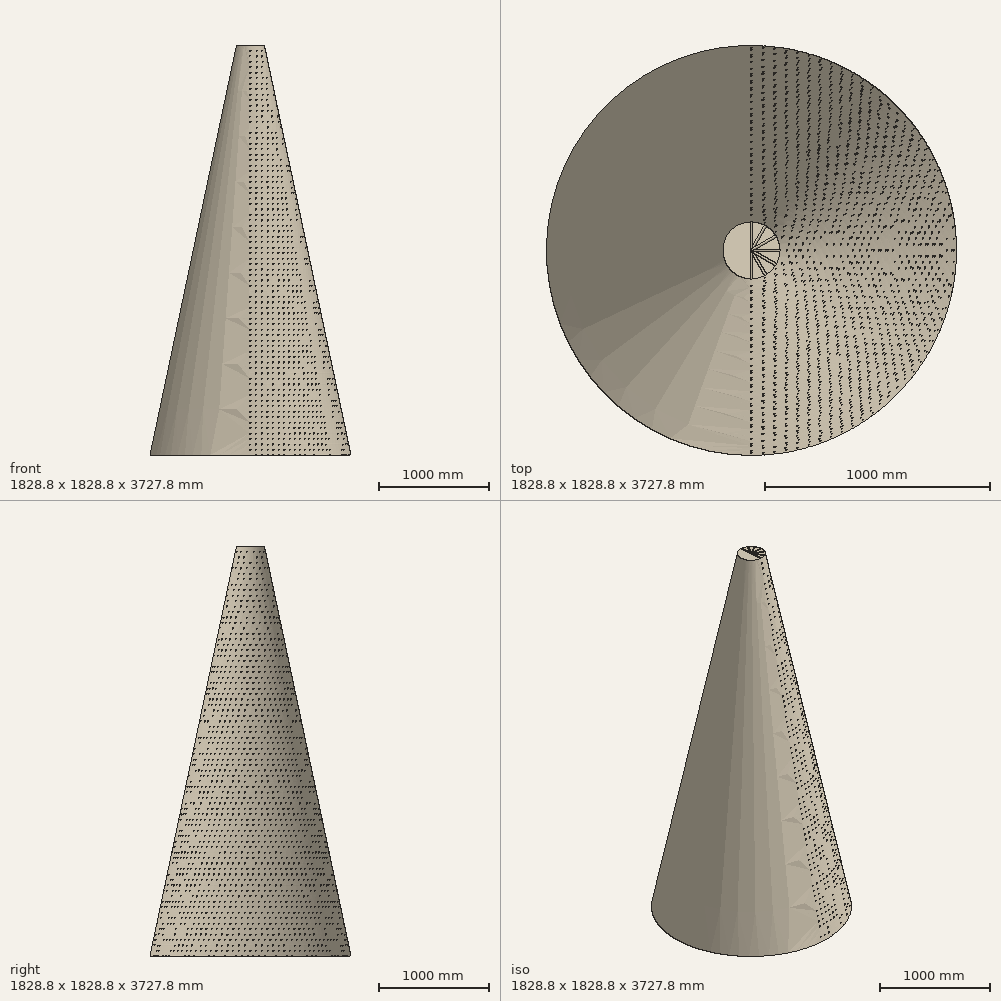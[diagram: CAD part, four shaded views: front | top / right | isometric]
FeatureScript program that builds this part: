
annotation { "Feature Type Name" : "Feature", "Feature Type Description" : "" }
export const myFeature = defineFeature(function(context is Context, id is Id, definition is map)
    precondition{}
    {
        {
            var Q0;
            Q0=qCreatedBy(makeId("Front.planeOp"),FACE);
            var sketch = newSketch(context, id + "F0", { "sketchPlane" : qUnion([Q0])});
            skLineSegment(sketch, "E0", {"start": v(0, 0) * mm, "end": v(914.4, 0) * mm});
            skLineSegment(sketch, "E1", {"start": v(914.4, 0) * mm, "end": v(127, 3727.75) * mm});
            skLineSegment(sketch, "E2", {"start": v(127, 3727.75) * mm, "end": v(0, 3727.75) * mm});
            skLineSegment(sketch, "E3", {"start": v(0, 3727.75) * mm, "end": v(0, 0) * mm});
            skLineSegment(sketch, "E4", {"start": v(0, 3727.75) * mm, "end": v(0, 4329) * mm});
            skLineSegment(sketch, "E5", {"start": v(0, 4329) * mm, "end": v(127, 3727.75) * mm});
            skCircle(sketch, "E6", {"center": v(0, 0) * mm, "radius": 6 * mm});
            skLineSegment(sketch, "E7.direction1", {"start": v(0, 0) * mm, "end": v(25.4, 0) * mm, "construction": true});
            skSolve(sketch);
        }
        {
            var Q0;
            Q0=qCreatedBy(makeId("Front.planeOp"),FACE);
            var sketch = newSketch(context, id + "F1", { "sketchPlane" : qUnion([Q0])});
            skCircle(sketch, "E8", {"center": v(0, 0) * mm, "radius": 6 * mm});
            skCircle(sketch, "E9.0.1.0", {"center": v(0, 49.7) * mm, "radius": 6 * mm});
            skCircle(sketch, "E9.0.2.0", {"center": v(0, 99.4) * mm, "radius": 6 * mm});
            skCircle(sketch, "E9.0.3.0", {"center": v(0, 149.1) * mm, "radius": 6 * mm});
            skCircle(sketch, "E9.0.4.0", {"center": v(0, 198.81) * mm, "radius": 6 * mm});
            skCircle(sketch, "E9.0.5.0", {"center": v(0, 248.52) * mm, "radius": 6 * mm});
            skCircle(sketch, "E9.0.6.0", {"center": v(0, 298.22) * mm, "radius": 6 * mm});
            skCircle(sketch, "E9.0.7.0", {"center": v(0, 347.92) * mm, "radius": 6 * mm});
            skCircle(sketch, "E9.0.8.0", {"center": v(0, 397.63) * mm, "radius": 6 * mm});
            skCircle(sketch, "E9.0.9.0", {"center": v(0, 447.33) * mm, "radius": 6 * mm});
            skCircle(sketch, "E9.0.10.0", {"center": v(0, 497.03) * mm, "radius": 6 * mm});
            skCircle(sketch, "E9.0.11.0", {"center": v(0, 546.74) * mm, "radius": 6 * mm});
            skCircle(sketch, "E9.0.12.0", {"center": v(0, 596.44) * mm, "radius": 6 * mm});
            skCircle(sketch, "E9.0.13.0", {"center": v(0, 646.14) * mm, "radius": 6 * mm});
            skCircle(sketch, "E9.0.14.0", {"center": v(0, 695.85) * mm, "radius": 6 * mm});
            skCircle(sketch, "E9.0.15.0", {"center": v(0, 745.55) * mm, "radius": 6 * mm});
            skCircle(sketch, "E9.0.16.0", {"center": v(0, 795.25) * mm, "radius": 6 * mm});
            skCircle(sketch, "E9.0.17.0", {"center": v(0, 844.96) * mm, "radius": 6 * mm});
            skCircle(sketch, "E9.0.18.0", {"center": v(0, 894.66) * mm, "radius": 6 * mm});
            skCircle(sketch, "E9.0.19.0", {"center": v(0, 944.36) * mm, "radius": 6 * mm});
            skCircle(sketch, "E9.0.20.0", {"center": v(0, 994.07) * mm, "radius": 6 * mm});
            skCircle(sketch, "E9.0.21.0", {"center": v(0, 1043.77) * mm, "radius": 6 * mm});
            skCircle(sketch, "E9.0.22.0", {"center": v(0, 1093.47) * mm, "radius": 6 * mm});
            skCircle(sketch, "E9.0.23.0", {"center": v(0, 1143.18) * mm, "radius": 6 * mm});
            skCircle(sketch, "E9.0.24.0", {"center": v(0, 1192.88) * mm, "radius": 6 * mm});
            skCircle(sketch, "E9.0.25.0", {"center": v(0, 1242.58) * mm, "radius": 6 * mm});
            skCircle(sketch, "E9.0.26.0", {"center": v(0, 1292.29) * mm, "radius": 6 * mm});
            skCircle(sketch, "E9.0.27.0", {"center": v(0, 1341.99) * mm, "radius": 6 * mm});
            skCircle(sketch, "E9.0.28.0", {"center": v(0, 1391.7) * mm, "radius": 6 * mm});
            skCircle(sketch, "E9.0.29.0", {"center": v(0, 1441.4) * mm, "radius": 6 * mm});
            skCircle(sketch, "E9.0.30.0", {"center": v(0, 1491.1) * mm, "radius": 6 * mm});
            skCircle(sketch, "E9.0.31.0", {"center": v(0, 1540.8) * mm, "radius": 6 * mm});
            skCircle(sketch, "E9.0.32.0", {"center": v(0, 1590.5) * mm, "radius": 6 * mm});
            skCircle(sketch, "E9.0.33.0", {"center": v(0, 1640.2) * mm, "radius": 6 * mm});
            skCircle(sketch, "E9.0.34.0", {"center": v(0, 1689.91) * mm, "radius": 6 * mm});
            skCircle(sketch, "E9.0.35.0", {"center": v(0, 1739.62) * mm, "radius": 6 * mm});
            skCircle(sketch, "E9.0.36.0", {"center": v(0, 1789.32) * mm, "radius": 6 * mm});
            skCircle(sketch, "E9.0.37.0", {"center": v(0, 1839.02) * mm, "radius": 6 * mm});
            skCircle(sketch, "E9.0.38.0", {"center": v(0, 1888.73) * mm, "radius": 6 * mm});
            skCircle(sketch, "E9.0.39.0", {"center": v(0, 1938.43) * mm, "radius": 6 * mm});
            skCircle(sketch, "E9.0.40.0", {"center": v(0, 1988.13) * mm, "radius": 6 * mm});
            skCircle(sketch, "E9.0.41.0", {"center": v(0, 2037.84) * mm, "radius": 6 * mm});
            skCircle(sketch, "E9.0.42.0", {"center": v(0, 2087.54) * mm, "radius": 6 * mm});
            skCircle(sketch, "E9.0.43.0", {"center": v(0, 2137.24) * mm, "radius": 6 * mm});
            skCircle(sketch, "E9.0.44.0", {"center": v(0, 2186.95) * mm, "radius": 6 * mm});
            skCircle(sketch, "E9.0.45.0", {"center": v(0, 2236.65) * mm, "radius": 6 * mm});
            skCircle(sketch, "E9.0.46.0", {"center": v(0, 2286.35) * mm, "radius": 6 * mm});
            skCircle(sketch, "E9.0.47.0", {"center": v(0, 2336.06) * mm, "radius": 6 * mm});
            skCircle(sketch, "E9.0.48.0", {"center": v(0, 2385.76) * mm, "radius": 6 * mm});
            skCircle(sketch, "E9.0.49.0", {"center": v(0, 2435.46) * mm, "radius": 6 * mm});
            skCircle(sketch, "E9.0.50.0", {"center": v(0, 2485.17) * mm, "radius": 6 * mm});
            skCircle(sketch, "E9.0.51.0", {"center": v(0, 2534.87) * mm, "radius": 6 * mm});
            skCircle(sketch, "E9.0.52.0", {"center": v(0, 2584.57) * mm, "radius": 6 * mm});
            skCircle(sketch, "E9.0.53.0", {"center": v(0, 2634.28) * mm, "radius": 6 * mm});
            skCircle(sketch, "E9.0.54.0", {"center": v(0, 2683.98) * mm, "radius": 6 * mm});
            skCircle(sketch, "E9.0.55.0", {"center": v(0, 2733.68) * mm, "radius": 6 * mm});
            skCircle(sketch, "E9.0.56.0", {"center": v(0, 2783.39) * mm, "radius": 6 * mm});
            skCircle(sketch, "E9.0.57.0", {"center": v(0, 2833.09) * mm, "radius": 6 * mm});
            skCircle(sketch, "E9.0.58.0", {"center": v(0, 2882.8) * mm, "radius": 6 * mm});
            skCircle(sketch, "E9.0.59.0", {"center": v(0, 2932.5) * mm, "radius": 6 * mm});
            skCircle(sketch, "E9.0.60.0", {"center": v(0, 2982.2) * mm, "radius": 6 * mm});
            skCircle(sketch, "E9.0.61.0", {"center": v(0, 3031.9) * mm, "radius": 6 * mm});
            skCircle(sketch, "E9.0.62.0", {"center": v(0, 3081.6) * mm, "radius": 6 * mm});
            skCircle(sketch, "E9.0.63.0", {"center": v(0, 3131.3) * mm, "radius": 6 * mm});
            skCircle(sketch, "E9.0.64.0", {"center": v(0, 3181.01) * mm, "radius": 6 * mm});
            skCircle(sketch, "E9.0.65.0", {"center": v(0, 3230.71) * mm, "radius": 6 * mm});
            skCircle(sketch, "E9.0.66.0", {"center": v(0, 3280.42) * mm, "radius": 6 * mm});
            skCircle(sketch, "E9.0.67.0", {"center": v(0, 3330.12) * mm, "radius": 6 * mm});
            skCircle(sketch, "E9.0.68.0", {"center": v(0, 3379.82) * mm, "radius": 6 * mm});
            skCircle(sketch, "E9.0.69.0", {"center": v(0, 3429.53) * mm, "radius": 6 * mm});
            skCircle(sketch, "E9.0.70.0", {"center": v(0, 3479.23) * mm, "radius": 6 * mm});
            skCircle(sketch, "E9.0.71.0", {"center": v(0, 3528.93) * mm, "radius": 6 * mm});
            skCircle(sketch, "E9.0.72.0", {"center": v(0, 3578.64) * mm, "radius": 6 * mm});
            skCircle(sketch, "E9.0.73.0", {"center": v(0, 3628.34) * mm, "radius": 6 * mm});
            skCircle(sketch, "E9.0.74.0", {"center": v(0, 3678.04) * mm, "radius": 6 * mm});
            skCircle(sketch, "E9.0.75.0", {"center": v(0, 3727.75) * mm, "radius": 6 * mm});
            skLineSegment(sketch, "E9.direction1", {"start": v(0, 0) * mm, "end": v(0, 0) * mm});
            skLineSegment(sketch, "E9.direction2", {"start": v(0, 0) * mm, "end": v(0, 49.7) * mm, "construction": true});
            skSolve(sketch);
        }
        {
            var Q0;
            {var subQ4=sQuery(id+"F0.wireOp",EDGE,"E1");Q0=makeQuery(id+"F0.imprint","IMPRINT",FACE,{"disambiguationData":[TD([[makeQuery(id+"F0.imprint","IMPRINT",EDGE,{"derivedFrom":subQ4}),1.0]])]});}
            var Q1;
            Q1=sQuery(id+"F0.wireOp",EDGE,"E3");
            revolve(context, id + "F2", {"entities" : qUnion([Q0]), "axis" : qUnion([Q1]), "revolveType" : RevolveType.FULL});
        }
        {
            var Q0;
            Q0=makeQuery(id+"F1.imprint","IMPRINT",FACE,{"disambiguationData":[TD([[makeQuery(id+"F1.imprint","IMPRINT",EDGE,{"derivedFrom":sQuery(id+"F1.wireOp",EDGE,"E9.0.6.0")}),1.0]])]});
            var Q1;
            Q1=makeQuery(id+"F1.imprint","IMPRINT",FACE,{"disambiguationData":[TD([[makeQuery(id+"F1.imprint","IMPRINT",EDGE,{"derivedFrom":sQuery(id+"F1.wireOp",EDGE,"E9.0.75.0")}),1.0]])]});
            var Q2;
            Q2=makeQuery(id+"F1.imprint","IMPRINT",FACE,{"disambiguationData":[TD([[makeQuery(id+"F1.imprint","IMPRINT",EDGE,{"derivedFrom":sQuery(id+"F1.wireOp",EDGE,"E9.0.9.0")}),1.0]])]});
            var Q3;
            Q3=makeQuery(id+"F1.imprint","IMPRINT",FACE,{"disambiguationData":[TD([[makeQuery(id+"F1.imprint","IMPRINT",EDGE,{"derivedFrom":sQuery(id+"F1.wireOp",EDGE,"E9.0.4.0")}),1.0]])]});
            var Q4;
            Q4=makeQuery(id+"F1.imprint","IMPRINT",FACE,{"disambiguationData":[TD([[makeQuery(id+"F1.imprint","IMPRINT",EDGE,{"derivedFrom":sQuery(id+"F1.wireOp",EDGE,"E9.0.7.0")}),1.0]])]});
            var Q5;
            Q5=makeQuery(id+"F1.imprint","IMPRINT",FACE,{"disambiguationData":[TD([[makeQuery(id+"F1.imprint","IMPRINT",EDGE,{"derivedFrom":sQuery(id+"F1.wireOp",EDGE,"E9.0.8.0")}),1.0]])]});
            var Q6;
            Q6=makeQuery(id+"F1.imprint","IMPRINT",FACE,{"disambiguationData":[TD([[makeQuery(id+"F1.imprint","IMPRINT",EDGE,{"derivedFrom":sQuery(id+"F1.wireOp",EDGE,"E9.0.5.0")}),1.0]])]});
            var Q7;
            Q7=makeQuery(id+"F1.imprint","IMPRINT",FACE,{"disambiguationData":[TD([[makeQuery(id+"F1.imprint","IMPRINT",EDGE,{"derivedFrom":sQuery(id+"F1.wireOp",EDGE,"E9.0.51.0")}),1.0]])]});
            var Q8;
            Q8=makeQuery(id+"F1.imprint","IMPRINT",FACE,{"disambiguationData":[TD([[makeQuery(id+"F1.imprint","IMPRINT",EDGE,{"derivedFrom":sQuery(id+"F1.wireOp",EDGE,"E9.0.39.0")}),1.0]])]});
            var Q9;
            Q9=makeQuery(id+"F1.imprint","IMPRINT",FACE,{"disambiguationData":[TD([[makeQuery(id+"F1.imprint","IMPRINT",EDGE,{"derivedFrom":sQuery(id+"F1.wireOp",EDGE,"E9.0.35.0")}),1.0]])]});
            var Q10;
            Q10=makeQuery(id+"F1.imprint","IMPRINT",FACE,{"disambiguationData":[TD([[makeQuery(id+"F1.imprint","IMPRINT",EDGE,{"derivedFrom":sQuery(id+"F1.wireOp",EDGE,"E9.0.56.0")}),1.0]])]});
            var Q11;
            Q11=makeQuery(id+"F1.imprint","IMPRINT",FACE,{"disambiguationData":[TD([[makeQuery(id+"F1.imprint","IMPRINT",EDGE,{"derivedFrom":sQuery(id+"F1.wireOp",EDGE,"E9.0.33.0")}),1.0]])]});
            var Q12;
            Q12=makeQuery(id+"F1.imprint","IMPRINT",FACE,{"disambiguationData":[TD([[makeQuery(id+"F1.imprint","IMPRINT",EDGE,{"derivedFrom":sQuery(id+"F1.wireOp",EDGE,"E9.0.49.0")}),1.0]])]});
            var Q13;
            Q13=makeQuery(id+"F1.imprint","IMPRINT",FACE,{"disambiguationData":[TD([[makeQuery(id+"F1.imprint","IMPRINT",EDGE,{"derivedFrom":sQuery(id+"F1.wireOp",EDGE,"E9.0.71.0")}),1.0]])]});
            var Q14;
            Q14=makeQuery(id+"F1.imprint","IMPRINT",FACE,{"disambiguationData":[TD([[makeQuery(id+"F1.imprint","IMPRINT",EDGE,{"derivedFrom":sQuery(id+"F1.wireOp",EDGE,"E9.0.74.0")}),1.0]])]});
            var Q15;
            Q15=makeQuery(id+"F1.imprint","IMPRINT",FACE,{"disambiguationData":[TD([[makeQuery(id+"F1.imprint","IMPRINT",EDGE,{"derivedFrom":sQuery(id+"F1.wireOp",EDGE,"E9.0.41.0")}),1.0]])]});
            var Q16;
            Q16=makeQuery(id+"F1.imprint","IMPRINT",FACE,{"disambiguationData":[TD([[makeQuery(id+"F1.imprint","IMPRINT",EDGE,{"derivedFrom":sQuery(id+"F1.wireOp",EDGE,"E9.0.3.0")}),1.0]])]});
            var Q17;
            Q17=makeQuery(id+"F1.imprint","IMPRINT",FACE,{"disambiguationData":[TD([[makeQuery(id+"F1.imprint","IMPRINT",EDGE,{"derivedFrom":sQuery(id+"F1.wireOp",EDGE,"E9.0.24.0")}),1.0]])]});
            var Q18;
            Q18=makeQuery(id+"F1.imprint","IMPRINT",FACE,{"disambiguationData":[TD([[makeQuery(id+"F1.imprint","IMPRINT",EDGE,{"derivedFrom":sQuery(id+"F1.wireOp",EDGE,"E9.0.55.0")}),1.0]])]});
            var Q19;
            Q19=makeQuery(id+"F1.imprint","IMPRINT",FACE,{"disambiguationData":[TD([[makeQuery(id+"F1.imprint","IMPRINT",EDGE,{"derivedFrom":sQuery(id+"F1.wireOp",EDGE,"E9.0.32.0")}),1.0]])]});
            var Q20;
            Q20=makeQuery(id+"F1.imprint","IMPRINT",FACE,{"disambiguationData":[TD([[makeQuery(id+"F1.imprint","IMPRINT",EDGE,{"derivedFrom":sQuery(id+"F1.wireOp",EDGE,"E9.0.73.0")}),1.0]])]});
            var Q21;
            Q21=makeQuery(id+"F1.imprint","IMPRINT",FACE,{"disambiguationData":[TD([[makeQuery(id+"F1.imprint","IMPRINT",EDGE,{"derivedFrom":sQuery(id+"F1.wireOp",EDGE,"E9.0.11.0")}),1.0]])]});
            var Q22;
            Q22=makeQuery(id+"F1.imprint","IMPRINT",FACE,{"disambiguationData":[TD([[makeQuery(id+"F1.imprint","IMPRINT",EDGE,{"derivedFrom":sQuery(id+"F1.wireOp",EDGE,"E9.0.25.0")}),1.0]])]});
            var Q23;
            Q23=makeQuery(id+"F1.imprint","IMPRINT",FACE,{"disambiguationData":[TD([[makeQuery(id+"F1.imprint","IMPRINT",EDGE,{"derivedFrom":sQuery(id+"F1.wireOp",EDGE,"E9.0.48.0")}),1.0]])]});
            var Q24;
            Q24=makeQuery(id+"F1.imprint","IMPRINT",FACE,{"disambiguationData":[TD([[makeQuery(id+"F1.imprint","IMPRINT",EDGE,{"derivedFrom":sQuery(id+"F1.wireOp",EDGE,"E9.0.50.0")}),1.0]])]});
            var Q25;
            Q25=makeQuery(id+"F1.imprint","IMPRINT",FACE,{"disambiguationData":[TD([[makeQuery(id+"F1.imprint","IMPRINT",EDGE,{"derivedFrom":sQuery(id+"F1.wireOp",EDGE,"E9.0.57.0")}),1.0]])]});
            var Q26;
            Q26=makeQuery(id+"F1.imprint","IMPRINT",FACE,{"disambiguationData":[TD([[makeQuery(id+"F1.imprint","IMPRINT",EDGE,{"derivedFrom":sQuery(id+"F1.wireOp",EDGE,"E9.0.72.0")}),1.0]])]});
            var Q27;
            Q27=makeQuery(id+"F1.imprint","IMPRINT",FACE,{"disambiguationData":[TD([[makeQuery(id+"F1.imprint","IMPRINT",EDGE,{"derivedFrom":sQuery(id+"F1.wireOp",EDGE,"E9.0.23.0")}),1.0]])]});
            var Q28;
            Q28=makeQuery(id+"F1.imprint","IMPRINT",FACE,{"disambiguationData":[TD([[makeQuery(id+"F1.imprint","IMPRINT",EDGE,{"derivedFrom":sQuery(id+"F1.wireOp",EDGE,"E9.0.34.0")}),1.0]])]});
            var Q29;
            Q29=makeQuery(id+"F1.imprint","IMPRINT",FACE,{"disambiguationData":[TD([[makeQuery(id+"F1.imprint","IMPRINT",EDGE,{"derivedFrom":sQuery(id+"F1.wireOp",EDGE,"E9.0.12.0")}),1.0]])]});
            var Q30;
            Q30=makeQuery(id+"F1.imprint","IMPRINT",FACE,{"disambiguationData":[TD([[makeQuery(id+"F1.imprint","IMPRINT",EDGE,{"derivedFrom":sQuery(id+"F1.wireOp",EDGE,"E9.0.10.0")}),1.0]])]});
            var Q31;
            Q31=makeQuery(id+"F1.imprint","IMPRINT",FACE,{"disambiguationData":[TD([[makeQuery(id+"F1.imprint","IMPRINT",EDGE,{"derivedFrom":sQuery(id+"F1.wireOp",EDGE,"E9.0.40.0")}),1.0]])]});
            var Q32;
            Q32=makeQuery(id+"F1.imprint","IMPRINT",FACE,{"disambiguationData":[TD([[makeQuery(id+"F1.imprint","IMPRINT",EDGE,{"derivedFrom":sQuery(id+"F1.wireOp",EDGE,"E9.0.28.0")}),1.0]])]});
            var Q33;
            Q33=makeQuery(id+"F1.imprint","IMPRINT",FACE,{"disambiguationData":[TD([[makeQuery(id+"F1.imprint","IMPRINT",EDGE,{"derivedFrom":sQuery(id+"F1.wireOp",EDGE,"E9.0.21.0")}),1.0]])]});
            var Q34;
            Q34=makeQuery(id+"F1.imprint","IMPRINT",FACE,{"disambiguationData":[TD([[makeQuery(id+"F1.imprint","IMPRINT",EDGE,{"derivedFrom":sQuery(id+"F1.wireOp",EDGE,"E9.0.29.0")}),1.0]])]});
            var Q35;
            Q35=makeQuery(id+"F1.imprint","IMPRINT",FACE,{"disambiguationData":[TD([[makeQuery(id+"F1.imprint","IMPRINT",EDGE,{"derivedFrom":sQuery(id+"F1.wireOp",EDGE,"E9.0.68.0")}),1.0]])]});
            var Q36;
            Q36=makeQuery(id+"F1.imprint","IMPRINT",FACE,{"disambiguationData":[TD([[makeQuery(id+"F1.imprint","IMPRINT",EDGE,{"derivedFrom":sQuery(id+"F1.wireOp",EDGE,"E9.0.63.0")}),1.0]])]});
            var Q37;
            Q37=makeQuery(id+"F1.imprint","IMPRINT",FACE,{"disambiguationData":[TD([[makeQuery(id+"F1.imprint","IMPRINT",EDGE,{"derivedFrom":sQuery(id+"F1.wireOp",EDGE,"E9.0.47.0")}),1.0]])]});
            var Q38;
            Q38=makeQuery(id+"F1.imprint","IMPRINT",FACE,{"disambiguationData":[TD([[makeQuery(id+"F1.imprint","IMPRINT",EDGE,{"derivedFrom":sQuery(id+"F1.wireOp",EDGE,"E9.0.64.0")}),1.0]])]});
            var Q39;
            Q39=makeQuery(id+"F1.imprint","IMPRINT",FACE,{"disambiguationData":[TD([[makeQuery(id+"F1.imprint","IMPRINT",EDGE,{"derivedFrom":sQuery(id+"F1.wireOp",EDGE,"E9.0.36.0")}),1.0]])]});
            var Q40;
            Q40=makeQuery(id+"F1.imprint","IMPRINT",FACE,{"disambiguationData":[TD([[makeQuery(id+"F1.imprint","IMPRINT",EDGE,{"derivedFrom":sQuery(id+"F1.wireOp",EDGE,"E9.0.58.0")}),1.0]])]});
            var Q41;
            Q41=makeQuery(id+"F1.imprint","IMPRINT",FACE,{"disambiguationData":[TD([[makeQuery(id+"F1.imprint","IMPRINT",EDGE,{"derivedFrom":sQuery(id+"F1.wireOp",EDGE,"E9.0.42.0")}),1.0]])]});
            var Q42;
            Q42=makeQuery(id+"F1.imprint","IMPRINT",FACE,{"disambiguationData":[TD([[makeQuery(id+"F1.imprint","IMPRINT",EDGE,{"derivedFrom":sQuery(id+"F1.wireOp",EDGE,"E9.0.15.0")}),1.0]])]});
            var Q43;
            Q43=makeQuery(id+"F1.imprint","IMPRINT",FACE,{"disambiguationData":[TD([[makeQuery(id+"F1.imprint","IMPRINT",EDGE,{"derivedFrom":sQuery(id+"F1.wireOp",EDGE,"E9.0.22.0")}),1.0]])]});
            var Q44;
            Q44=makeQuery(id+"F1.imprint","IMPRINT",FACE,{"disambiguationData":[TD([[makeQuery(id+"F1.imprint","IMPRINT",EDGE,{"derivedFrom":sQuery(id+"F1.wireOp",EDGE,"E9.0.43.0")}),1.0]])]});
            var Q45;
            Q45=makeQuery(id+"F1.imprint","IMPRINT",FACE,{"disambiguationData":[TD([[makeQuery(id+"F1.imprint","IMPRINT",EDGE,{"derivedFrom":sQuery(id+"F1.wireOp",EDGE,"E9.0.30.0")}),1.0]])]});
            var Q46;
            Q46=makeQuery(id+"F1.imprint","IMPRINT",FACE,{"disambiguationData":[TD([[makeQuery(id+"F1.imprint","IMPRINT",EDGE,{"derivedFrom":sQuery(id+"F1.wireOp",EDGE,"E9.0.37.0")}),1.0]])]});
            var Q47;
            Q47=makeQuery(id+"F1.imprint","IMPRINT",FACE,{"disambiguationData":[TD([[makeQuery(id+"F1.imprint","IMPRINT",EDGE,{"derivedFrom":sQuery(id+"F1.wireOp",EDGE,"E9.0.26.0")}),1.0]])]});
            var Q48;
            Q48=makeQuery(id+"F1.imprint","IMPRINT",FACE,{"disambiguationData":[TD([[makeQuery(id+"F1.imprint","IMPRINT",EDGE,{"derivedFrom":sQuery(id+"F1.wireOp",EDGE,"E9.0.66.0")}),1.0]])]});
            var Q49;
            Q49=makeQuery(id+"F1.imprint","IMPRINT",FACE,{"disambiguationData":[TD([[makeQuery(id+"F1.imprint","IMPRINT",EDGE,{"derivedFrom":sQuery(id+"F1.wireOp",EDGE,"E9.0.20.0")}),1.0]])]});
            var Q50;
            Q50=makeQuery(id+"F1.imprint","IMPRINT",FACE,{"disambiguationData":[TD([[makeQuery(id+"F1.imprint","IMPRINT",EDGE,{"derivedFrom":sQuery(id+"F1.wireOp",EDGE,"E9.0.54.0")}),1.0]])]});
            var Q51;
            Q51=makeQuery(id+"F1.imprint","IMPRINT",FACE,{"disambiguationData":[TD([[makeQuery(id+"F1.imprint","IMPRINT",EDGE,{"derivedFrom":sQuery(id+"F1.wireOp",EDGE,"E9.0.67.0")}),1.0]])]});
            var Q52;
            Q52=makeQuery(id+"F1.imprint","IMPRINT",FACE,{"disambiguationData":[TD([[makeQuery(id+"F1.imprint","IMPRINT",EDGE,{"derivedFrom":sQuery(id+"F1.wireOp",EDGE,"E9.0.59.0")}),1.0]])]});
            var Q53;
            Q53=makeQuery(id+"F1.imprint","IMPRINT",FACE,{"disambiguationData":[TD([[makeQuery(id+"F1.imprint","IMPRINT",EDGE,{"derivedFrom":sQuery(id+"F1.wireOp",EDGE,"E9.0.31.0")}),1.0]])]});
            var Q54;
            Q54=makeQuery(id+"F1.imprint","IMPRINT",FACE,{"disambiguationData":[TD([[makeQuery(id+"F1.imprint","IMPRINT",EDGE,{"derivedFrom":sQuery(id+"F1.wireOp",EDGE,"E9.0.52.0")}),1.0]])]});
            var Q55;
            Q55=makeQuery(id+"F1.imprint","IMPRINT",FACE,{"disambiguationData":[TD([[makeQuery(id+"F1.imprint","IMPRINT",EDGE,{"derivedFrom":sQuery(id+"F1.wireOp",EDGE,"E9.0.18.0")}),1.0]])]});
            var Q56;
            Q56=makeQuery(id+"F1.imprint","IMPRINT",FACE,{"disambiguationData":[TD([[makeQuery(id+"F1.imprint","IMPRINT",EDGE,{"derivedFrom":sQuery(id+"F1.wireOp",EDGE,"E9.0.45.0")}),1.0]])]});
            var Q57;
            Q57=makeQuery(id+"F1.imprint","IMPRINT",FACE,{"disambiguationData":[TD([[makeQuery(id+"F1.imprint","IMPRINT",EDGE,{"derivedFrom":sQuery(id+"F1.wireOp",EDGE,"E9.0.27.0")}),1.0]])]});
            var Q58;
            Q58=makeQuery(id+"F1.imprint","IMPRINT",FACE,{"disambiguationData":[TD([[makeQuery(id+"F1.imprint","IMPRINT",EDGE,{"derivedFrom":sQuery(id+"F1.wireOp",EDGE,"E9.0.16.0")}),1.0]])]});
            var Q59;
            Q59=makeQuery(id+"F1.imprint","IMPRINT",FACE,{"disambiguationData":[TD([[makeQuery(id+"F1.imprint","IMPRINT",EDGE,{"derivedFrom":sQuery(id+"F1.wireOp",EDGE,"E9.0.14.0")}),1.0]])]});
            var Q60;
            Q60=makeQuery(id+"F1.imprint","IMPRINT",FACE,{"disambiguationData":[TD([[makeQuery(id+"F1.imprint","IMPRINT",EDGE,{"derivedFrom":sQuery(id+"F1.wireOp",EDGE,"E9.0.53.0")}),1.0]])]});
            var Q61;
            Q61=makeQuery(id+"F1.imprint","IMPRINT",FACE,{"disambiguationData":[TD([[makeQuery(id+"F1.imprint","IMPRINT",EDGE,{"derivedFrom":sQuery(id+"F1.wireOp",EDGE,"E9.0.17.0")}),1.0]])]});
            var Q62;
            Q62=makeQuery(id+"F1.imprint","IMPRINT",FACE,{"disambiguationData":[TD([[makeQuery(id+"F1.imprint","IMPRINT",EDGE,{"derivedFrom":sQuery(id+"F1.wireOp",EDGE,"E9.0.38.0")}),1.0]])]});
            var Q63;
            Q63=makeQuery(id+"F1.imprint","IMPRINT",FACE,{"disambiguationData":[TD([[makeQuery(id+"F1.imprint","IMPRINT",EDGE,{"derivedFrom":sQuery(id+"F1.wireOp",EDGE,"E9.0.19.0")}),1.0]])]});
            var Q64;
            Q64=makeQuery(id+"F1.imprint","IMPRINT",FACE,{"disambiguationData":[TD([[makeQuery(id+"F1.imprint","IMPRINT",EDGE,{"derivedFrom":sQuery(id+"F1.wireOp",EDGE,"E9.0.60.0")}),1.0]])]});
            var Q65;
            Q65=makeQuery(id+"F1.imprint","IMPRINT",FACE,{"disambiguationData":[TD([[makeQuery(id+"F1.imprint","IMPRINT",EDGE,{"derivedFrom":sQuery(id+"F1.wireOp",EDGE,"E9.0.46.0")}),1.0]])]});
            var Q66;
            Q66=makeQuery(id+"F1.imprint","IMPRINT",FACE,{"disambiguationData":[TD([[makeQuery(id+"F1.imprint","IMPRINT",EDGE,{"derivedFrom":sQuery(id+"F1.wireOp",EDGE,"E9.0.44.0")}),1.0]])]});
            var Q67;
            Q67=makeQuery(id+"F1.imprint","IMPRINT",FACE,{"disambiguationData":[TD([[makeQuery(id+"F1.imprint","IMPRINT",EDGE,{"derivedFrom":sQuery(id+"F1.wireOp",EDGE,"E9.0.70.0")}),1.0]])]});
            var Q68;
            Q68=makeQuery(id+"F1.imprint","IMPRINT",FACE,{"disambiguationData":[TD([[makeQuery(id+"F1.imprint","IMPRINT",EDGE,{"derivedFrom":sQuery(id+"F1.wireOp",EDGE,"E9.0.69.0")}),1.0]])]});
            var Q69;
            Q69=makeQuery(id+"F1.imprint","IMPRINT",FACE,{"disambiguationData":[TD([[makeQuery(id+"F1.imprint","IMPRINT",EDGE,{"derivedFrom":sQuery(id+"F1.wireOp",EDGE,"E9.0.65.0")}),1.0]])]});
            var Q70;
            Q70=makeQuery(id+"F1.imprint","IMPRINT",FACE,{"disambiguationData":[TD([[makeQuery(id+"F1.imprint","IMPRINT",EDGE,{"derivedFrom":sQuery(id+"F1.wireOp",EDGE,"E9.0.13.0")}),1.0]])]});
            var Q71;
            Q71=makeQuery(id+"F1.imprint","IMPRINT",FACE,{"disambiguationData":[TD([[makeQuery(id+"F1.imprint","IMPRINT",EDGE,{"derivedFrom":sQuery(id+"F1.wireOp",EDGE,"E9.0.2.0")}),1.0]])]});
            var Q72;
            Q72=makeQuery(id+"F1.imprint","IMPRINT",FACE,{"disambiguationData":[TD([[makeQuery(id+"F1.imprint","IMPRINT",EDGE,{"derivedFrom":sQuery(id+"F1.wireOp",EDGE,"E9.0.62.0")}),1.0]])]});
            var Q73;
            Q73=makeQuery(id+"F1.imprint","IMPRINT",FACE,{"disambiguationData":[TD([[makeQuery(id+"F1.imprint","IMPRINT",EDGE,{"derivedFrom":sQuery(id+"F1.wireOp",EDGE,"E9.0.61.0")}),1.0]])]});
            var Q74;
            Q74=makeQuery(id+"F1.imprint","IMPRINT",FACE,{"disambiguationData":[TD([[makeQuery(id+"F1.imprint","IMPRINT",EDGE,{"derivedFrom":sQuery(id+"F1.wireOp",EDGE,"E8")}),1.0]])]});
            var Q75;
            Q75=makeQuery(id+"F1.imprint","IMPRINT",FACE,{"disambiguationData":[TD([[makeQuery(id+"F1.imprint","IMPRINT",EDGE,{"derivedFrom":sQuery(id+"F1.wireOp",EDGE,"E9.0.1.0")}),1.0]])]});
            extrude(context, id + "F3", {"entities" : qUnion([Q0, Q1, Q2, Q3, Q4, Q5, Q6, Q7, Q8, Q9, Q10, Q11, Q12, Q13, Q14, Q15, Q16, Q17, Q18, Q19, Q20, Q21, Q22, Q23, Q24, Q25, Q26, Q27, Q28, Q29, Q30, Q31, Q32, Q33, Q34, Q35, Q36, Q37, Q38, Q39, Q40, Q41, Q42, Q43, Q44, Q45, Q46, Q47, Q48, Q49, Q50, Q51, Q52, Q53, Q54, Q55, Q56, Q57, Q58, Q59, Q60, Q61, Q62, Q63, Q64, Q65, Q66, Q67, Q68, Q69, Q70, Q71, Q72, Q73, Q74, Q75]), "depth" : 914.4 * mm, "offsetDistance" : 25.4 * mm});
        }
        {
            var Q0;
            Q0=makeQuery(id+"F3.opExtrude","SWEPT_BODY",BODY,{"disambiguationData":[OSD([sQuery(id+"F1.wireOp",EDGE,"E9.0.75.0")])]});
            var Q1;
            Q1=makeQuery(id+"F2.opRevolve","SWEPT_EDGE",EDGE,{"disambiguationData":[OSD([sQuery(id+"F0.wireOp",EDGE,"E1"),sQuery(id+"F0.wireOp",EDGE,"E2"),sQuery(id+"F0.wireOp",EDGE,"E5")])]});
            circularPattern(context, id + "F4", {"entities" : qUnion([Q0]), "axis" : qUnion([Q1]), "angle" : 180 * degree, "instanceCount" : 7, "equalSpace" : true});
        }
        {
            var Q0;
            Q0=makeQuery(id+"F3.opExtrude","SWEPT_BODY",BODY,{"disambiguationData":[OSD([sQuery(id+"F1.wireOp",EDGE,"E9.0.74.0")])]});
            var Q1;
            Q1=makeQuery(id+"F2.opRevolve","SWEPT_EDGE",EDGE,{"disambiguationData":[OSD([sQuery(id+"F0.wireOp",EDGE,"E1"),sQuery(id+"F0.wireOp",EDGE,"E2"),sQuery(id+"F0.wireOp",EDGE,"E5")])]});
            circularPattern(context, id + "F5", {"entities" : qUnion([Q0]), "axis" : qUnion([Q1]), "angle" : 180 * degree, "instanceCount" : 8, "equalSpace" : true});
        }
        {
            var Q0;
            Q0=makeQuery(id+"F3.opExtrude","SWEPT_BODY",BODY,{"disambiguationData":[OSD([sQuery(id+"F1.wireOp",EDGE,"E9.0.73.0")])]});
            var Q1;
            Q1=makeQuery(id+"F2.opRevolve","SWEPT_EDGE",EDGE,{"disambiguationData":[OSD([sQuery(id+"F0.wireOp",EDGE,"E1"),sQuery(id+"F0.wireOp",EDGE,"E2"),sQuery(id+"F0.wireOp",EDGE,"E5")])]});
            circularPattern(context, id + "F6", {"entities" : qUnion([Q0]), "axis" : qUnion([Q1]), "angle" : 180 * degree, "instanceCount" : 9, "equalSpace" : true});
        }
        {
            var Q0;
            Q0=makeQuery(id+"F3.opExtrude","SWEPT_BODY",BODY,{"disambiguationData":[OSD([sQuery(id+"F1.wireOp",EDGE,"E9.0.72.0")])]});
            var Q1;
            Q1=makeQuery(id+"F2.opRevolve","SWEPT_EDGE",EDGE,{"disambiguationData":[OSD([sQuery(id+"F0.wireOp",EDGE,"E1"),sQuery(id+"F0.wireOp",EDGE,"E2"),sQuery(id+"F0.wireOp",EDGE,"E5")])]});
            circularPattern(context, id + "F7", {"entities" : qUnion([Q0]), "axis" : qUnion([Q1]), "angle" : 180 * degree, "instanceCount" : 9, "equalSpace" : true});
        }
        {
            var Q0;
            Q0=makeQuery(id+"F3.opExtrude","SWEPT_BODY",BODY,{"disambiguationData":[OSD([sQuery(id+"F1.wireOp",EDGE,"E9.0.71.0")])]});
            var Q1;
            Q1=makeQuery(id+"F2.opRevolve","SWEPT_EDGE",EDGE,{"disambiguationData":[OSD([sQuery(id+"F0.wireOp",EDGE,"E1"),sQuery(id+"F0.wireOp",EDGE,"E2"),sQuery(id+"F0.wireOp",EDGE,"E5")])]});
            circularPattern(context, id + "F8", {"entities" : qUnion([Q0]), "axis" : qUnion([Q1]), "angle" : 180 * degree, "instanceCount" : 10, "equalSpace" : true});
        }
        {
            var Q0;
            Q0=makeQuery(id+"F3.opExtrude","SWEPT_BODY",BODY,{"disambiguationData":[OSD([sQuery(id+"F1.wireOp",EDGE,"E9.0.70.0")])]});
            var Q1;
            Q1=makeQuery(id+"F2.opRevolve","SWEPT_EDGE",EDGE,{"disambiguationData":[OSD([sQuery(id+"F0.wireOp",EDGE,"E1"),sQuery(id+"F0.wireOp",EDGE,"E2"),sQuery(id+"F0.wireOp",EDGE,"E5")])]});
            circularPattern(context, id + "F9", {"entities" : qUnion([Q0]), "axis" : qUnion([Q1]), "angle" : 180 * degree, "instanceCount" : 11, "equalSpace" : true});
        }
        {
            var Q0;
            Q0=makeQuery(id+"F8.opPattern","COPY",BODY,{"derivedFrom":makeQuery(id+"F3.opExtrude","SWEPT_BODY",BODY,{"disambiguationData":[OSD([sQuery(id+"F1.wireOp",EDGE,"E9.0.71.0")])]}),"instanceName":"1"});
            var Q1;
            Q1=makeQuery(id+"F8.opPattern","COPY",BODY,{"derivedFrom":makeQuery(id+"F3.opExtrude","SWEPT_BODY",BODY,{"disambiguationData":[OSD([sQuery(id+"F1.wireOp",EDGE,"E9.0.71.0")])]}),"instanceName":"8"});
            var Q2;
            Q2=makeQuery(id+"F8.opPattern","COPY",BODY,{"derivedFrom":makeQuery(id+"F3.opExtrude","SWEPT_BODY",BODY,{"disambiguationData":[OSD([sQuery(id+"F1.wireOp",EDGE,"E9.0.71.0")])]}),"instanceName":"9"});
            var Q3;
            Q3=makeQuery(id+"F3.opExtrude","SWEPT_BODY",BODY,{"disambiguationData":[OSD([sQuery(id+"F1.wireOp",EDGE,"E9.0.75.0")])]});
            var Q4;
            Q4=makeQuery(id+"F3.opExtrude","SWEPT_BODY",BODY,{"disambiguationData":[OSD([sQuery(id+"F1.wireOp",EDGE,"E9.0.74.0")])]});
            var Q5;
            Q5=makeQuery(id+"F4.opPattern","COPY",BODY,{"derivedFrom":makeQuery(id+"F3.opExtrude","SWEPT_BODY",BODY,{"disambiguationData":[OSD([sQuery(id+"F1.wireOp",EDGE,"E9.0.75.0")])]}),"instanceName":"4"});
            var Q6;
            Q6=makeQuery(id+"F5.opPattern","COPY",BODY,{"derivedFrom":makeQuery(id+"F3.opExtrude","SWEPT_BODY",BODY,{"disambiguationData":[OSD([sQuery(id+"F1.wireOp",EDGE,"E9.0.74.0")])]}),"instanceName":"7"});
            var Q7;
            Q7=makeQuery(id+"F6.opPattern","COPY",BODY,{"derivedFrom":makeQuery(id+"F3.opExtrude","SWEPT_BODY",BODY,{"disambiguationData":[OSD([sQuery(id+"F1.wireOp",EDGE,"E9.0.73.0")])]}),"instanceName":"1"});
            var Q8;
            Q8=makeQuery(id+"F6.opPattern","COPY",BODY,{"derivedFrom":makeQuery(id+"F3.opExtrude","SWEPT_BODY",BODY,{"disambiguationData":[OSD([sQuery(id+"F1.wireOp",EDGE,"E9.0.73.0")])]}),"instanceName":"2"});
            var Q9;
            Q9=makeQuery(id+"F5.opPattern","COPY",BODY,{"derivedFrom":makeQuery(id+"F3.opExtrude","SWEPT_BODY",BODY,{"disambiguationData":[OSD([sQuery(id+"F1.wireOp",EDGE,"E9.0.74.0")])]}),"instanceName":"3"});
            var Q10;
            Q10=makeQuery(id+"F8.opPattern","COPY",BODY,{"derivedFrom":makeQuery(id+"F3.opExtrude","SWEPT_BODY",BODY,{"disambiguationData":[OSD([sQuery(id+"F1.wireOp",EDGE,"E9.0.71.0")])]}),"instanceName":"7"});
            var Q11;
            Q11=makeQuery(id+"F5.opPattern","COPY",BODY,{"derivedFrom":makeQuery(id+"F3.opExtrude","SWEPT_BODY",BODY,{"disambiguationData":[OSD([sQuery(id+"F1.wireOp",EDGE,"E9.0.74.0")])]}),"instanceName":"4"});
            var Q12;
            Q12=makeQuery(id+"F5.opPattern","COPY",BODY,{"derivedFrom":makeQuery(id+"F3.opExtrude","SWEPT_BODY",BODY,{"disambiguationData":[OSD([sQuery(id+"F1.wireOp",EDGE,"E9.0.74.0")])]}),"instanceName":"5"});
            var Q13;
            Q13=makeQuery(id+"F3.opExtrude","SWEPT_BODY",BODY,{"disambiguationData":[OSD([sQuery(id+"F1.wireOp",EDGE,"E9.0.72.0")])]});
            var Q14;
            Q14=makeQuery(id+"F3.opExtrude","SWEPT_BODY",BODY,{"disambiguationData":[OSD([sQuery(id+"F1.wireOp",EDGE,"E9.0.73.0")])]});
            var Q15;
            Q15=makeQuery(id+"F5.opPattern","COPY",BODY,{"derivedFrom":makeQuery(id+"F3.opExtrude","SWEPT_BODY",BODY,{"disambiguationData":[OSD([sQuery(id+"F1.wireOp",EDGE,"E9.0.74.0")])]}),"instanceName":"6"});
            var Q16;
            Q16=makeQuery(id+"F4.opPattern","COPY",BODY,{"derivedFrom":makeQuery(id+"F3.opExtrude","SWEPT_BODY",BODY,{"disambiguationData":[OSD([sQuery(id+"F1.wireOp",EDGE,"E9.0.75.0")])]}),"instanceName":"3"});
            var Q17;
            Q17=makeQuery(id+"F6.opPattern","COPY",BODY,{"derivedFrom":makeQuery(id+"F3.opExtrude","SWEPT_BODY",BODY,{"disambiguationData":[OSD([sQuery(id+"F1.wireOp",EDGE,"E9.0.73.0")])]}),"instanceName":"3"});
            var Q18;
            Q18=makeQuery(id+"F6.opPattern","COPY",BODY,{"derivedFrom":makeQuery(id+"F3.opExtrude","SWEPT_BODY",BODY,{"disambiguationData":[OSD([sQuery(id+"F1.wireOp",EDGE,"E9.0.73.0")])]}),"instanceName":"4"});
            var Q19;
            Q19=makeQuery(id+"F6.opPattern","COPY",BODY,{"derivedFrom":makeQuery(id+"F3.opExtrude","SWEPT_BODY",BODY,{"disambiguationData":[OSD([sQuery(id+"F1.wireOp",EDGE,"E9.0.73.0")])]}),"instanceName":"5"});
            var Q20;
            Q20=makeQuery(id+"F6.opPattern","COPY",BODY,{"derivedFrom":makeQuery(id+"F3.opExtrude","SWEPT_BODY",BODY,{"disambiguationData":[OSD([sQuery(id+"F1.wireOp",EDGE,"E9.0.73.0")])]}),"instanceName":"6"});
            var Q21;
            Q21=makeQuery(id+"F6.opPattern","COPY",BODY,{"derivedFrom":makeQuery(id+"F3.opExtrude","SWEPT_BODY",BODY,{"disambiguationData":[OSD([sQuery(id+"F1.wireOp",EDGE,"E9.0.73.0")])]}),"instanceName":"7"});
            var Q22;
            Q22=makeQuery(id+"F6.opPattern","COPY",BODY,{"derivedFrom":makeQuery(id+"F3.opExtrude","SWEPT_BODY",BODY,{"disambiguationData":[OSD([sQuery(id+"F1.wireOp",EDGE,"E9.0.73.0")])]}),"instanceName":"8"});
            var Q23;
            Q23=makeQuery(id+"F8.opPattern","COPY",BODY,{"derivedFrom":makeQuery(id+"F3.opExtrude","SWEPT_BODY",BODY,{"disambiguationData":[OSD([sQuery(id+"F1.wireOp",EDGE,"E9.0.71.0")])]}),"instanceName":"6"});
            var Q24;
            Q24=makeQuery(id+"F8.opPattern","COPY",BODY,{"derivedFrom":makeQuery(id+"F3.opExtrude","SWEPT_BODY",BODY,{"disambiguationData":[OSD([sQuery(id+"F1.wireOp",EDGE,"E9.0.71.0")])]}),"instanceName":"5"});
            var Q25;
            Q25=makeQuery(id+"F7.opPattern","COPY",BODY,{"derivedFrom":makeQuery(id+"F3.opExtrude","SWEPT_BODY",BODY,{"disambiguationData":[OSD([sQuery(id+"F1.wireOp",EDGE,"E9.0.72.0")])]}),"instanceName":"1"});
            var Q26;
            Q26=makeQuery(id+"F4.opPattern","COPY",BODY,{"derivedFrom":makeQuery(id+"F3.opExtrude","SWEPT_BODY",BODY,{"disambiguationData":[OSD([sQuery(id+"F1.wireOp",EDGE,"E9.0.75.0")])]}),"instanceName":"1"});
            var Q27;
            Q27=makeQuery(id+"F3.opExtrude","SWEPT_BODY",BODY,{"disambiguationData":[OSD([sQuery(id+"F1.wireOp",EDGE,"E9.0.71.0")])]});
            var Q28;
            Q28=makeQuery(id+"F7.opPattern","COPY",BODY,{"derivedFrom":makeQuery(id+"F3.opExtrude","SWEPT_BODY",BODY,{"disambiguationData":[OSD([sQuery(id+"F1.wireOp",EDGE,"E9.0.72.0")])]}),"instanceName":"2"});
            var Q29;
            Q29=makeQuery(id+"F7.opPattern","COPY",BODY,{"derivedFrom":makeQuery(id+"F3.opExtrude","SWEPT_BODY",BODY,{"disambiguationData":[OSD([sQuery(id+"F1.wireOp",EDGE,"E9.0.72.0")])]}),"instanceName":"3"});
            var Q30;
            Q30=makeQuery(id+"F7.opPattern","COPY",BODY,{"derivedFrom":makeQuery(id+"F3.opExtrude","SWEPT_BODY",BODY,{"disambiguationData":[OSD([sQuery(id+"F1.wireOp",EDGE,"E9.0.72.0")])]}),"instanceName":"4"});
            var Q31;
            Q31=makeQuery(id+"F7.opPattern","COPY",BODY,{"derivedFrom":makeQuery(id+"F3.opExtrude","SWEPT_BODY",BODY,{"disambiguationData":[OSD([sQuery(id+"F1.wireOp",EDGE,"E9.0.72.0")])]}),"instanceName":"5"});
            var Q32;
            Q32=makeQuery(id+"F7.opPattern","COPY",BODY,{"derivedFrom":makeQuery(id+"F3.opExtrude","SWEPT_BODY",BODY,{"disambiguationData":[OSD([sQuery(id+"F1.wireOp",EDGE,"E9.0.72.0")])]}),"instanceName":"6"});
            var Q33;
            Q33=makeQuery(id+"F7.opPattern","COPY",BODY,{"derivedFrom":makeQuery(id+"F3.opExtrude","SWEPT_BODY",BODY,{"disambiguationData":[OSD([sQuery(id+"F1.wireOp",EDGE,"E9.0.72.0")])]}),"instanceName":"7"});
            var Q34;
            Q34=makeQuery(id+"F7.opPattern","COPY",BODY,{"derivedFrom":makeQuery(id+"F3.opExtrude","SWEPT_BODY",BODY,{"disambiguationData":[OSD([sQuery(id+"F1.wireOp",EDGE,"E9.0.72.0")])]}),"instanceName":"8"});
            var Q35;
            Q35=makeQuery(id+"F8.opPattern","COPY",BODY,{"derivedFrom":makeQuery(id+"F3.opExtrude","SWEPT_BODY",BODY,{"disambiguationData":[OSD([sQuery(id+"F1.wireOp",EDGE,"E9.0.71.0")])]}),"instanceName":"4"});
            var Q36;
            Q36=makeQuery(id+"F8.opPattern","COPY",BODY,{"derivedFrom":makeQuery(id+"F3.opExtrude","SWEPT_BODY",BODY,{"disambiguationData":[OSD([sQuery(id+"F1.wireOp",EDGE,"E9.0.71.0")])]}),"instanceName":"2"});
            var Q37;
            Q37=makeQuery(id+"F8.opPattern","COPY",BODY,{"derivedFrom":makeQuery(id+"F3.opExtrude","SWEPT_BODY",BODY,{"disambiguationData":[OSD([sQuery(id+"F1.wireOp",EDGE,"E9.0.71.0")])]}),"instanceName":"3"});
            var Q38;
            Q38=makeQuery(id+"F5.opPattern","COPY",BODY,{"derivedFrom":makeQuery(id+"F3.opExtrude","SWEPT_BODY",BODY,{"disambiguationData":[OSD([sQuery(id+"F1.wireOp",EDGE,"E9.0.74.0")])]}),"instanceName":"2"});
            var Q39;
            Q39=makeQuery(id+"F5.opPattern","COPY",BODY,{"derivedFrom":makeQuery(id+"F3.opExtrude","SWEPT_BODY",BODY,{"disambiguationData":[OSD([sQuery(id+"F1.wireOp",EDGE,"E9.0.74.0")])]}),"instanceName":"1"});
            var Q40;
            Q40=makeQuery(id+"F4.opPattern","COPY",BODY,{"derivedFrom":makeQuery(id+"F3.opExtrude","SWEPT_BODY",BODY,{"disambiguationData":[OSD([sQuery(id+"F1.wireOp",EDGE,"E9.0.75.0")])]}),"instanceName":"6"});
            var Q41;
            Q41=makeQuery(id+"F4.opPattern","COPY",BODY,{"derivedFrom":makeQuery(id+"F3.opExtrude","SWEPT_BODY",BODY,{"disambiguationData":[OSD([sQuery(id+"F1.wireOp",EDGE,"E9.0.75.0")])]}),"instanceName":"5"});
            var Q42;
            Q42=makeQuery(id+"F4.opPattern","COPY",BODY,{"derivedFrom":makeQuery(id+"F3.opExtrude","SWEPT_BODY",BODY,{"disambiguationData":[OSD([sQuery(id+"F1.wireOp",EDGE,"E9.0.75.0")])]}),"instanceName":"2"});
            var Q43;
            Q43=makeQuery(id+"F2.opRevolve","SWEPT_BODY",BODY,{"disambiguationData":[OSD([sQuery(id+"F0.wireOp",EDGE,"E0"),sQuery(id+"F0.wireOp",EDGE,"E1"),sQuery(id+"F0.wireOp",EDGE,"E2"),sQuery(id+"F0.wireOp",EDGE,"E3"),sQuery(id+"F0.wireOp",EDGE,"E6")])]});
            booleanBodies(context, id + "F10", {"operationType" : BooleanOperationType.SUBTRACTION, "tools" : qUnion([Q0, Q1, Q2, Q3, Q4, Q5, Q6, Q7, Q8, Q9, Q10, Q11, Q12, Q13, Q14, Q15, Q16, Q17, Q18, Q19, Q20, Q21, Q22, Q23, Q24, Q25, Q26, Q27, Q28, Q29, Q30, Q31, Q32, Q33, Q34, Q35, Q36, Q37, Q38, Q39, Q40, Q41, Q42]), "targets" : qUnion([Q43])});
        }
        {
            var Q0;
            Q0=makeQuery(id+"F9.opPattern","COPY",BODY,{"derivedFrom":makeQuery(id+"F3.opExtrude","SWEPT_BODY",BODY,{"disambiguationData":[OSD([sQuery(id+"F1.wireOp",EDGE,"E9.0.70.0")])]}),"instanceName":"1"});
            var Q1;
            Q1=makeQuery(id+"F9.opPattern","COPY",BODY,{"derivedFrom":makeQuery(id+"F3.opExtrude","SWEPT_BODY",BODY,{"disambiguationData":[OSD([sQuery(id+"F1.wireOp",EDGE,"E9.0.70.0")])]}),"instanceName":"2"});
            var Q2;
            Q2=makeQuery(id+"F9.opPattern","COPY",BODY,{"derivedFrom":makeQuery(id+"F3.opExtrude","SWEPT_BODY",BODY,{"disambiguationData":[OSD([sQuery(id+"F1.wireOp",EDGE,"E9.0.70.0")])]}),"instanceName":"3"});
            var Q3;
            Q3=makeQuery(id+"F9.opPattern","COPY",BODY,{"derivedFrom":makeQuery(id+"F3.opExtrude","SWEPT_BODY",BODY,{"disambiguationData":[OSD([sQuery(id+"F1.wireOp",EDGE,"E9.0.70.0")])]}),"instanceName":"4"});
            var Q4;
            Q4=makeQuery(id+"F9.opPattern","COPY",BODY,{"derivedFrom":makeQuery(id+"F3.opExtrude","SWEPT_BODY",BODY,{"disambiguationData":[OSD([sQuery(id+"F1.wireOp",EDGE,"E9.0.70.0")])]}),"instanceName":"5"});
            var Q5;
            Q5=makeQuery(id+"F3.opExtrude","SWEPT_BODY",BODY,{"disambiguationData":[OSD([sQuery(id+"F1.wireOp",EDGE,"E9.0.70.0")])]});
            var Q6;
            Q6=makeQuery(id+"F9.opPattern","COPY",BODY,{"derivedFrom":makeQuery(id+"F3.opExtrude","SWEPT_BODY",BODY,{"disambiguationData":[OSD([sQuery(id+"F1.wireOp",EDGE,"E9.0.70.0")])]}),"instanceName":"6"});
            var Q7;
            Q7=makeQuery(id+"F9.opPattern","COPY",BODY,{"derivedFrom":makeQuery(id+"F3.opExtrude","SWEPT_BODY",BODY,{"disambiguationData":[OSD([sQuery(id+"F1.wireOp",EDGE,"E9.0.70.0")])]}),"instanceName":"7"});
            var Q8;
            Q8=makeQuery(id+"F9.opPattern","COPY",BODY,{"derivedFrom":makeQuery(id+"F3.opExtrude","SWEPT_BODY",BODY,{"disambiguationData":[OSD([sQuery(id+"F1.wireOp",EDGE,"E9.0.70.0")])]}),"instanceName":"8"});
            var Q9;
            Q9=makeQuery(id+"F9.opPattern","COPY",BODY,{"derivedFrom":makeQuery(id+"F3.opExtrude","SWEPT_BODY",BODY,{"disambiguationData":[OSD([sQuery(id+"F1.wireOp",EDGE,"E9.0.70.0")])]}),"instanceName":"9"});
            var Q10;
            Q10=makeQuery(id+"F9.opPattern","COPY",BODY,{"derivedFrom":makeQuery(id+"F3.opExtrude","SWEPT_BODY",BODY,{"disambiguationData":[OSD([sQuery(id+"F1.wireOp",EDGE,"E9.0.70.0")])]}),"instanceName":"10"});
            var Q11;
            Q11=makeQuery(id+"F2.opRevolve","SWEPT_BODY",BODY,{"disambiguationData":[OSD([sQuery(id+"F0.wireOp",EDGE,"E0"),sQuery(id+"F0.wireOp",EDGE,"E1"),sQuery(id+"F0.wireOp",EDGE,"E2"),sQuery(id+"F0.wireOp",EDGE,"E3"),sQuery(id+"F0.wireOp",EDGE,"E6")])]});
            booleanBodies(context, id + "F11", {"operationType" : BooleanOperationType.SUBTRACTION, "tools" : qUnion([Q0, Q1, Q2, Q3, Q4, Q5, Q6, Q7, Q8, Q9, Q10]), "targets" : qUnion([Q11])});
        }
        {
            var Q0;
            Q0=makeQuery(id+"F3.opExtrude","SWEPT_BODY",BODY,{"disambiguationData":[OSD([sQuery(id+"F1.wireOp",EDGE,"E9.0.69.0")])]});
            var Q1;
            Q1=makeQuery(id+"F2.opRevolve","SWEPT_FACE",FACE,{"disambiguationData":[OSD([sQuery(id+"F0.wireOp",EDGE,"E1")])]});
            circularPattern(context, id + "F12", {"entities" : qUnion([Q0]), "axis" : qUnion([Q1]), "angle" : 180 * degree, "instanceCount" : 11, "oppositeDirection" : true, "equalSpace" : true});
        }
        {
            var Q0;
            Q0=makeQuery(id+"F3.opExtrude","SWEPT_BODY",BODY,{"disambiguationData":[OSD([sQuery(id+"F1.wireOp",EDGE,"E9.0.68.0")])]});
            var Q1;
            Q1=makeQuery(id+"F2.opRevolve","SWEPT_FACE",FACE,{"disambiguationData":[OSD([sQuery(id+"F0.wireOp",EDGE,"E1")])]});
            circularPattern(context, id + "F13", {"entities" : qUnion([Q0]), "axis" : qUnion([Q1]), "angle" : 180 * degree, "instanceCount" : 12, "oppositeDirection" : true, "equalSpace" : true});
        }
        {
            var Q0;
            Q0=makeQuery(id+"F3.opExtrude","SWEPT_BODY",BODY,{"disambiguationData":[OSD([sQuery(id+"F1.wireOp",EDGE,"E9.0.67.0")])]});
            var Q1;
            Q1=makeQuery(id+"F3.opExtrude","SWEPT_BODY",BODY,{"disambiguationData":[OSD([sQuery(id+"F1.wireOp",EDGE,"E9.0.66.0")])]});
            var Q2;
            Q2=makeQuery(id+"F2.opRevolve","SWEPT_FACE",FACE,{"disambiguationData":[OSD([sQuery(id+"F0.wireOp",EDGE,"E1")])]});
            circularPattern(context, id + "F14", {"entities" : qUnion([Q0, Q1]), "axis" : qUnion([Q2]), "angle" : 180 * degree, "instanceCount" : 13, "oppositeDirection" : true, "equalSpace" : true});
        }
        {
            var Q0;
            Q0=makeQuery(id+"F3.opExtrude","SWEPT_BODY",BODY,{"disambiguationData":[OSD([sQuery(id+"F1.wireOp",EDGE,"E9.0.65.0")])]});
            var Q1;
            Q1=makeQuery(id+"F3.opExtrude","SWEPT_BODY",BODY,{"disambiguationData":[OSD([sQuery(id+"F1.wireOp",EDGE,"E9.0.64.0")])]});
            var Q2;
            Q2=makeQuery(id+"F2.opRevolve","SWEPT_FACE",FACE,{"disambiguationData":[OSD([sQuery(id+"F0.wireOp",EDGE,"E1")])]});
            circularPattern(context, id + "F15", {"entities" : qUnion([Q0, Q1]), "axis" : qUnion([Q2]), "angle" : 180 * degree, "instanceCount" : 14, "oppositeDirection" : true, "equalSpace" : true});
        }
        {
            var Q0;
            Q0=makeQuery(id+"F3.opExtrude","SWEPT_BODY",BODY,{"disambiguationData":[OSD([sQuery(id+"F1.wireOp",EDGE,"E9.0.63.0")])]});
            var Q1;
            Q1=makeQuery(id+"F2.opRevolve","SWEPT_FACE",FACE,{"disambiguationData":[OSD([sQuery(id+"F0.wireOp",EDGE,"E1")])]});
            circularPattern(context, id + "F16", {"entities" : qUnion([Q0]), "axis" : qUnion([Q1]), "angle" : 180 * degree, "instanceCount" : 15, "oppositeDirection" : true, "equalSpace" : true});
        }
        {
            var Q0;
            Q0=makeQuery(id+"F3.opExtrude","SWEPT_BODY",BODY,{"disambiguationData":[OSD([sQuery(id+"F1.wireOp",EDGE,"E9.0.62.0")])]});
            var Q1;
            Q1=makeQuery(id+"F3.opExtrude","SWEPT_BODY",BODY,{"disambiguationData":[OSD([sQuery(id+"F1.wireOp",EDGE,"E9.0.61.0")])]});
            var Q2;
            Q2=makeQuery(id+"F2.opRevolve","SWEPT_FACE",FACE,{"disambiguationData":[OSD([sQuery(id+"F0.wireOp",EDGE,"E1")])]});
            circularPattern(context, id + "F17", {"entities" : qUnion([Q0, Q1]), "axis" : qUnion([Q2]), "angle" : 180 * degree, "instanceCount" : 16, "oppositeDirection" : true, "equalSpace" : true});
        }
        {
            var Q0;
            Q0=makeQuery(id+"F17.opPattern","COPY",BODY,{"derivedFrom":makeQuery(id+"F3.opExtrude","SWEPT_BODY",BODY,{"disambiguationData":[OSD([sQuery(id+"F1.wireOp",EDGE,"E9.0.61.0")])]}),"instanceName":"4"});
            var Q1;
            Q1=makeQuery(id+"F17.opPattern","COPY",BODY,{"derivedFrom":makeQuery(id+"F3.opExtrude","SWEPT_BODY",BODY,{"disambiguationData":[OSD([sQuery(id+"F1.wireOp",EDGE,"E9.0.62.0")])]}),"instanceName":"4"});
            var Q2;
            Q2=makeQuery(id+"F17.opPattern","COPY",BODY,{"derivedFrom":makeQuery(id+"F3.opExtrude","SWEPT_BODY",BODY,{"disambiguationData":[OSD([sQuery(id+"F1.wireOp",EDGE,"E9.0.61.0")])]}),"instanceName":"5"});
            var Q3;
            Q3=makeQuery(id+"F17.opPattern","COPY",BODY,{"derivedFrom":makeQuery(id+"F3.opExtrude","SWEPT_BODY",BODY,{"disambiguationData":[OSD([sQuery(id+"F1.wireOp",EDGE,"E9.0.62.0")])]}),"instanceName":"5"});
            var Q4;
            Q4=makeQuery(id+"F17.opPattern","COPY",BODY,{"derivedFrom":makeQuery(id+"F3.opExtrude","SWEPT_BODY",BODY,{"disambiguationData":[OSD([sQuery(id+"F1.wireOp",EDGE,"E9.0.62.0")])]}),"instanceName":"3"});
            var Q5;
            Q5=makeQuery(id+"F13.opPattern","COPY",BODY,{"derivedFrom":makeQuery(id+"F3.opExtrude","SWEPT_BODY",BODY,{"disambiguationData":[OSD([sQuery(id+"F1.wireOp",EDGE,"E9.0.68.0")])]}),"instanceName":"6"});
            var Q6;
            Q6=makeQuery(id+"F12.opPattern","COPY",BODY,{"derivedFrom":makeQuery(id+"F3.opExtrude","SWEPT_BODY",BODY,{"disambiguationData":[OSD([sQuery(id+"F1.wireOp",EDGE,"E9.0.69.0")])]}),"instanceName":"9"});
            var Q7;
            Q7=makeQuery(id+"F17.opPattern","COPY",BODY,{"derivedFrom":makeQuery(id+"F3.opExtrude","SWEPT_BODY",BODY,{"disambiguationData":[OSD([sQuery(id+"F1.wireOp",EDGE,"E9.0.61.0")])]}),"instanceName":"3"});
            var Q8;
            Q8=makeQuery(id+"F12.opPattern","COPY",BODY,{"derivedFrom":makeQuery(id+"F3.opExtrude","SWEPT_BODY",BODY,{"disambiguationData":[OSD([sQuery(id+"F1.wireOp",EDGE,"E9.0.69.0")])]}),"instanceName":"8"});
            var Q9;
            Q9=makeQuery(id+"F15.opPattern","COPY",BODY,{"derivedFrom":makeQuery(id+"F3.opExtrude","SWEPT_BODY",BODY,{"disambiguationData":[OSD([sQuery(id+"F1.wireOp",EDGE,"E9.0.64.0")])]}),"instanceName":"1"});
            var Q10;
            Q10=makeQuery(id+"F17.opPattern","COPY",BODY,{"derivedFrom":makeQuery(id+"F3.opExtrude","SWEPT_BODY",BODY,{"disambiguationData":[OSD([sQuery(id+"F1.wireOp",EDGE,"E9.0.62.0")])]}),"instanceName":"2"});
            var Q11;
            Q11=makeQuery(id+"F17.opPattern","COPY",BODY,{"derivedFrom":makeQuery(id+"F3.opExtrude","SWEPT_BODY",BODY,{"disambiguationData":[OSD([sQuery(id+"F1.wireOp",EDGE,"E9.0.61.0")])]}),"instanceName":"2"});
            var Q12;
            Q12=makeQuery(id+"F17.opPattern","COPY",BODY,{"derivedFrom":makeQuery(id+"F3.opExtrude","SWEPT_BODY",BODY,{"disambiguationData":[OSD([sQuery(id+"F1.wireOp",EDGE,"E9.0.62.0")])]}),"instanceName":"1"});
            var Q13;
            Q13=makeQuery(id+"F17.opPattern","COPY",BODY,{"derivedFrom":makeQuery(id+"F3.opExtrude","SWEPT_BODY",BODY,{"disambiguationData":[OSD([sQuery(id+"F1.wireOp",EDGE,"E9.0.61.0")])]}),"instanceName":"1"});
            var Q14;
            Q14=makeQuery(id+"F17.opPattern","COPY",BODY,{"derivedFrom":makeQuery(id+"F3.opExtrude","SWEPT_BODY",BODY,{"disambiguationData":[OSD([sQuery(id+"F1.wireOp",EDGE,"E9.0.61.0")])]}),"instanceName":"7"});
            var Q15;
            Q15=makeQuery(id+"F15.opPattern","COPY",BODY,{"derivedFrom":makeQuery(id+"F3.opExtrude","SWEPT_BODY",BODY,{"disambiguationData":[OSD([sQuery(id+"F1.wireOp",EDGE,"E9.0.65.0")])]}),"instanceName":"1"});
            var Q16;
            Q16=makeQuery(id+"F12.opPattern","COPY",BODY,{"derivedFrom":makeQuery(id+"F3.opExtrude","SWEPT_BODY",BODY,{"disambiguationData":[OSD([sQuery(id+"F1.wireOp",EDGE,"E9.0.69.0")])]}),"instanceName":"6"});
            var Q17;
            Q17=makeQuery(id+"F12.opPattern","COPY",BODY,{"derivedFrom":makeQuery(id+"F3.opExtrude","SWEPT_BODY",BODY,{"disambiguationData":[OSD([sQuery(id+"F1.wireOp",EDGE,"E9.0.69.0")])]}),"instanceName":"5"});
            var Q18;
            Q18=makeQuery(id+"F16.opPattern","COPY",BODY,{"derivedFrom":makeQuery(id+"F3.opExtrude","SWEPT_BODY",BODY,{"disambiguationData":[OSD([sQuery(id+"F1.wireOp",EDGE,"E9.0.63.0")])]}),"instanceName":"14"});
            var Q19;
            Q19=makeQuery(id+"F12.opPattern","COPY",BODY,{"derivedFrom":makeQuery(id+"F3.opExtrude","SWEPT_BODY",BODY,{"disambiguationData":[OSD([sQuery(id+"F1.wireOp",EDGE,"E9.0.69.0")])]}),"instanceName":"4"});
            var Q20;
            Q20=makeQuery(id+"F16.opPattern","COPY",BODY,{"derivedFrom":makeQuery(id+"F3.opExtrude","SWEPT_BODY",BODY,{"disambiguationData":[OSD([sQuery(id+"F1.wireOp",EDGE,"E9.0.63.0")])]}),"instanceName":"13"});
            var Q21;
            Q21=makeQuery(id+"F12.opPattern","COPY",BODY,{"derivedFrom":makeQuery(id+"F3.opExtrude","SWEPT_BODY",BODY,{"disambiguationData":[OSD([sQuery(id+"F1.wireOp",EDGE,"E9.0.69.0")])]}),"instanceName":"3"});
            var Q22;
            Q22=makeQuery(id+"F12.opPattern","COPY",BODY,{"derivedFrom":makeQuery(id+"F3.opExtrude","SWEPT_BODY",BODY,{"disambiguationData":[OSD([sQuery(id+"F1.wireOp",EDGE,"E9.0.69.0")])]}),"instanceName":"2"});
            var Q23;
            Q23=makeQuery(id+"F16.opPattern","COPY",BODY,{"derivedFrom":makeQuery(id+"F3.opExtrude","SWEPT_BODY",BODY,{"disambiguationData":[OSD([sQuery(id+"F1.wireOp",EDGE,"E9.0.63.0")])]}),"instanceName":"12"});
            var Q24;
            Q24=makeQuery(id+"F12.opPattern","COPY",BODY,{"derivedFrom":makeQuery(id+"F3.opExtrude","SWEPT_BODY",BODY,{"disambiguationData":[OSD([sQuery(id+"F1.wireOp",EDGE,"E9.0.69.0")])]}),"instanceName":"7"});
            var Q25;
            Q25=makeQuery(id+"F16.opPattern","COPY",BODY,{"derivedFrom":makeQuery(id+"F3.opExtrude","SWEPT_BODY",BODY,{"disambiguationData":[OSD([sQuery(id+"F1.wireOp",EDGE,"E9.0.63.0")])]}),"instanceName":"11"});
            var Q26;
            Q26=makeQuery(id+"F12.opPattern","COPY",BODY,{"derivedFrom":makeQuery(id+"F3.opExtrude","SWEPT_BODY",BODY,{"disambiguationData":[OSD([sQuery(id+"F1.wireOp",EDGE,"E9.0.69.0")])]}),"instanceName":"1"});
            var Q27;
            Q27=makeQuery(id+"F16.opPattern","COPY",BODY,{"derivedFrom":makeQuery(id+"F3.opExtrude","SWEPT_BODY",BODY,{"disambiguationData":[OSD([sQuery(id+"F1.wireOp",EDGE,"E9.0.63.0")])]}),"instanceName":"10"});
            var Q28;
            Q28=makeQuery(id+"F16.opPattern","COPY",BODY,{"derivedFrom":makeQuery(id+"F3.opExtrude","SWEPT_BODY",BODY,{"disambiguationData":[OSD([sQuery(id+"F1.wireOp",EDGE,"E9.0.63.0")])]}),"instanceName":"9"});
            var Q29;
            Q29=makeQuery(id+"F16.opPattern","COPY",BODY,{"derivedFrom":makeQuery(id+"F3.opExtrude","SWEPT_BODY",BODY,{"disambiguationData":[OSD([sQuery(id+"F1.wireOp",EDGE,"E9.0.63.0")])]}),"instanceName":"8"});
            var Q30;
            Q30=makeQuery(id+"F14.opPattern","COPY",BODY,{"derivedFrom":makeQuery(id+"F3.opExtrude","SWEPT_BODY",BODY,{"disambiguationData":[OSD([sQuery(id+"F1.wireOp",EDGE,"E9.0.66.0")])]}),"instanceName":"11"});
            var Q31;
            Q31=makeQuery(id+"F16.opPattern","COPY",BODY,{"derivedFrom":makeQuery(id+"F3.opExtrude","SWEPT_BODY",BODY,{"disambiguationData":[OSD([sQuery(id+"F1.wireOp",EDGE,"E9.0.63.0")])]}),"instanceName":"7"});
            var Q32;
            Q32=makeQuery(id+"F16.opPattern","COPY",BODY,{"derivedFrom":makeQuery(id+"F3.opExtrude","SWEPT_BODY",BODY,{"disambiguationData":[OSD([sQuery(id+"F1.wireOp",EDGE,"E9.0.63.0")])]}),"instanceName":"6"});
            var Q33;
            Q33=makeQuery(id+"F16.opPattern","COPY",BODY,{"derivedFrom":makeQuery(id+"F3.opExtrude","SWEPT_BODY",BODY,{"disambiguationData":[OSD([sQuery(id+"F1.wireOp",EDGE,"E9.0.63.0")])]}),"instanceName":"5"});
            var Q34;
            Q34=makeQuery(id+"F16.opPattern","COPY",BODY,{"derivedFrom":makeQuery(id+"F3.opExtrude","SWEPT_BODY",BODY,{"disambiguationData":[OSD([sQuery(id+"F1.wireOp",EDGE,"E9.0.63.0")])]}),"instanceName":"4"});
            var Q35;
            Q35=makeQuery(id+"F16.opPattern","COPY",BODY,{"derivedFrom":makeQuery(id+"F3.opExtrude","SWEPT_BODY",BODY,{"disambiguationData":[OSD([sQuery(id+"F1.wireOp",EDGE,"E9.0.63.0")])]}),"instanceName":"3"});
            var Q36;
            Q36=makeQuery(id+"F16.opPattern","COPY",BODY,{"derivedFrom":makeQuery(id+"F3.opExtrude","SWEPT_BODY",BODY,{"disambiguationData":[OSD([sQuery(id+"F1.wireOp",EDGE,"E9.0.63.0")])]}),"instanceName":"2"});
            var Q37;
            Q37=makeQuery(id+"F16.opPattern","COPY",BODY,{"derivedFrom":makeQuery(id+"F3.opExtrude","SWEPT_BODY",BODY,{"disambiguationData":[OSD([sQuery(id+"F1.wireOp",EDGE,"E9.0.63.0")])]}),"instanceName":"1"});
            var Q38;
            Q38=makeQuery(id+"F15.opPattern","COPY",BODY,{"derivedFrom":makeQuery(id+"F3.opExtrude","SWEPT_BODY",BODY,{"disambiguationData":[OSD([sQuery(id+"F1.wireOp",EDGE,"E9.0.65.0")])]}),"instanceName":"3"});
            var Q39;
            Q39=makeQuery(id+"F15.opPattern","COPY",BODY,{"derivedFrom":makeQuery(id+"F3.opExtrude","SWEPT_BODY",BODY,{"disambiguationData":[OSD([sQuery(id+"F1.wireOp",EDGE,"E9.0.64.0")])]}),"instanceName":"4"});
            var Q40;
            Q40=makeQuery(id+"F15.opPattern","COPY",BODY,{"derivedFrom":makeQuery(id+"F3.opExtrude","SWEPT_BODY",BODY,{"disambiguationData":[OSD([sQuery(id+"F1.wireOp",EDGE,"E9.0.65.0")])]}),"instanceName":"4"});
            var Q41;
            Q41=makeQuery(id+"F14.opPattern","COPY",BODY,{"derivedFrom":makeQuery(id+"F3.opExtrude","SWEPT_BODY",BODY,{"disambiguationData":[OSD([sQuery(id+"F1.wireOp",EDGE,"E9.0.67.0")])]}),"instanceName":"6"});
            var Q42;
            Q42=makeQuery(id+"F15.opPattern","COPY",BODY,{"derivedFrom":makeQuery(id+"F3.opExtrude","SWEPT_BODY",BODY,{"disambiguationData":[OSD([sQuery(id+"F1.wireOp",EDGE,"E9.0.64.0")])]}),"instanceName":"5"});
            var Q43;
            Q43=makeQuery(id+"F15.opPattern","COPY",BODY,{"derivedFrom":makeQuery(id+"F3.opExtrude","SWEPT_BODY",BODY,{"disambiguationData":[OSD([sQuery(id+"F1.wireOp",EDGE,"E9.0.65.0")])]}),"instanceName":"5"});
            var Q44;
            Q44=makeQuery(id+"F14.opPattern","COPY",BODY,{"derivedFrom":makeQuery(id+"F3.opExtrude","SWEPT_BODY",BODY,{"disambiguationData":[OSD([sQuery(id+"F1.wireOp",EDGE,"E9.0.66.0")])]}),"instanceName":"6"});
            var Q45;
            Q45=makeQuery(id+"F15.opPattern","COPY",BODY,{"derivedFrom":makeQuery(id+"F3.opExtrude","SWEPT_BODY",BODY,{"disambiguationData":[OSD([sQuery(id+"F1.wireOp",EDGE,"E9.0.65.0")])]}),"instanceName":"13"});
            var Q46;
            Q46=makeQuery(id+"F15.opPattern","COPY",BODY,{"derivedFrom":makeQuery(id+"F3.opExtrude","SWEPT_BODY",BODY,{"disambiguationData":[OSD([sQuery(id+"F1.wireOp",EDGE,"E9.0.64.0")])]}),"instanceName":"6"});
            var Q47;
            Q47=makeQuery(id+"F15.opPattern","COPY",BODY,{"derivedFrom":makeQuery(id+"F3.opExtrude","SWEPT_BODY",BODY,{"disambiguationData":[OSD([sQuery(id+"F1.wireOp",EDGE,"E9.0.64.0")])]}),"instanceName":"13"});
            var Q48;
            Q48=makeQuery(id+"F15.opPattern","COPY",BODY,{"derivedFrom":makeQuery(id+"F3.opExtrude","SWEPT_BODY",BODY,{"disambiguationData":[OSD([sQuery(id+"F1.wireOp",EDGE,"E9.0.65.0")])]}),"instanceName":"12"});
            var Q49;
            Q49=makeQuery(id+"F15.opPattern","COPY",BODY,{"derivedFrom":makeQuery(id+"F3.opExtrude","SWEPT_BODY",BODY,{"disambiguationData":[OSD([sQuery(id+"F1.wireOp",EDGE,"E9.0.65.0")])]}),"instanceName":"6"});
            var Q50;
            Q50=makeQuery(id+"F14.opPattern","COPY",BODY,{"derivedFrom":makeQuery(id+"F3.opExtrude","SWEPT_BODY",BODY,{"disambiguationData":[OSD([sQuery(id+"F1.wireOp",EDGE,"E9.0.67.0")])]}),"instanceName":"5"});
            var Q51;
            Q51=makeQuery(id+"F15.opPattern","COPY",BODY,{"derivedFrom":makeQuery(id+"F3.opExtrude","SWEPT_BODY",BODY,{"disambiguationData":[OSD([sQuery(id+"F1.wireOp",EDGE,"E9.0.64.0")])]}),"instanceName":"7"});
            var Q52;
            Q52=makeQuery(id+"F15.opPattern","COPY",BODY,{"derivedFrom":makeQuery(id+"F3.opExtrude","SWEPT_BODY",BODY,{"disambiguationData":[OSD([sQuery(id+"F1.wireOp",EDGE,"E9.0.64.0")])]}),"instanceName":"12"});
            var Q53;
            Q53=makeQuery(id+"F15.opPattern","COPY",BODY,{"derivedFrom":makeQuery(id+"F3.opExtrude","SWEPT_BODY",BODY,{"disambiguationData":[OSD([sQuery(id+"F1.wireOp",EDGE,"E9.0.65.0")])]}),"instanceName":"11"});
            var Q54;
            Q54=makeQuery(id+"F15.opPattern","COPY",BODY,{"derivedFrom":makeQuery(id+"F3.opExtrude","SWEPT_BODY",BODY,{"disambiguationData":[OSD([sQuery(id+"F1.wireOp",EDGE,"E9.0.64.0")])]}),"instanceName":"11"});
            var Q55;
            Q55=makeQuery(id+"F14.opPattern","COPY",BODY,{"derivedFrom":makeQuery(id+"F3.opExtrude","SWEPT_BODY",BODY,{"disambiguationData":[OSD([sQuery(id+"F1.wireOp",EDGE,"E9.0.67.0")])]}),"instanceName":"8"});
            var Q56;
            Q56=makeQuery(id+"F15.opPattern","COPY",BODY,{"derivedFrom":makeQuery(id+"F3.opExtrude","SWEPT_BODY",BODY,{"disambiguationData":[OSD([sQuery(id+"F1.wireOp",EDGE,"E9.0.65.0")])]}),"instanceName":"7"});
            var Q57;
            Q57=makeQuery(id+"F15.opPattern","COPY",BODY,{"derivedFrom":makeQuery(id+"F3.opExtrude","SWEPT_BODY",BODY,{"disambiguationData":[OSD([sQuery(id+"F1.wireOp",EDGE,"E9.0.65.0")])]}),"instanceName":"10"});
            var Q58;
            Q58=makeQuery(id+"F3.opExtrude","SWEPT_BODY",BODY,{"disambiguationData":[OSD([sQuery(id+"F1.wireOp",EDGE,"E9.0.61.0")])]});
            var Q59;
            Q59=makeQuery(id+"F3.opExtrude","SWEPT_BODY",BODY,{"disambiguationData":[OSD([sQuery(id+"F1.wireOp",EDGE,"E9.0.62.0")])]});
            var Q60;
            Q60=makeQuery(id+"F3.opExtrude","SWEPT_BODY",BODY,{"disambiguationData":[OSD([sQuery(id+"F1.wireOp",EDGE,"E9.0.63.0")])]});
            var Q61;
            Q61=makeQuery(id+"F12.opPattern","COPY",BODY,{"derivedFrom":makeQuery(id+"F3.opExtrude","SWEPT_BODY",BODY,{"disambiguationData":[OSD([sQuery(id+"F1.wireOp",EDGE,"E9.0.69.0")])]}),"instanceName":"10"});
            var Q62;
            Q62=makeQuery(id+"F3.opExtrude","SWEPT_BODY",BODY,{"disambiguationData":[OSD([sQuery(id+"F1.wireOp",EDGE,"E9.0.64.0")])]});
            var Q63;
            Q63=makeQuery(id+"F3.opExtrude","SWEPT_BODY",BODY,{"disambiguationData":[OSD([sQuery(id+"F1.wireOp",EDGE,"E9.0.65.0")])]});
            var Q64;
            Q64=makeQuery(id+"F3.opExtrude","SWEPT_BODY",BODY,{"disambiguationData":[OSD([sQuery(id+"F1.wireOp",EDGE,"E9.0.66.0")])]});
            var Q65;
            Q65=makeQuery(id+"F14.opPattern","COPY",BODY,{"derivedFrom":makeQuery(id+"F3.opExtrude","SWEPT_BODY",BODY,{"disambiguationData":[OSD([sQuery(id+"F1.wireOp",EDGE,"E9.0.66.0")])]}),"instanceName":"8"});
            var Q66;
            Q66=makeQuery(id+"F14.opPattern","COPY",BODY,{"derivedFrom":makeQuery(id+"F3.opExtrude","SWEPT_BODY",BODY,{"disambiguationData":[OSD([sQuery(id+"F1.wireOp",EDGE,"E9.0.67.0")])]}),"instanceName":"7"});
            var Q67;
            Q67=makeQuery(id+"F15.opPattern","COPY",BODY,{"derivedFrom":makeQuery(id+"F3.opExtrude","SWEPT_BODY",BODY,{"disambiguationData":[OSD([sQuery(id+"F1.wireOp",EDGE,"E9.0.64.0")])]}),"instanceName":"9"});
            var Q68;
            Q68=makeQuery(id+"F3.opExtrude","SWEPT_BODY",BODY,{"disambiguationData":[OSD([sQuery(id+"F1.wireOp",EDGE,"E9.0.67.0")])]});
            var Q69;
            Q69=makeQuery(id+"F15.opPattern","COPY",BODY,{"derivedFrom":makeQuery(id+"F3.opExtrude","SWEPT_BODY",BODY,{"disambiguationData":[OSD([sQuery(id+"F1.wireOp",EDGE,"E9.0.65.0")])]}),"instanceName":"9"});
            var Q70;
            Q70=makeQuery(id+"F15.opPattern","COPY",BODY,{"derivedFrom":makeQuery(id+"F3.opExtrude","SWEPT_BODY",BODY,{"disambiguationData":[OSD([sQuery(id+"F1.wireOp",EDGE,"E9.0.64.0")])]}),"instanceName":"10"});
            var Q71;
            Q71=makeQuery(id+"F15.opPattern","COPY",BODY,{"derivedFrom":makeQuery(id+"F3.opExtrude","SWEPT_BODY",BODY,{"disambiguationData":[OSD([sQuery(id+"F1.wireOp",EDGE,"E9.0.65.0")])]}),"instanceName":"2"});
            var Q72;
            Q72=makeQuery(id+"F15.opPattern","COPY",BODY,{"derivedFrom":makeQuery(id+"F3.opExtrude","SWEPT_BODY",BODY,{"disambiguationData":[OSD([sQuery(id+"F1.wireOp",EDGE,"E9.0.64.0")])]}),"instanceName":"8"});
            var Q73;
            Q73=makeQuery(id+"F15.opPattern","COPY",BODY,{"derivedFrom":makeQuery(id+"F3.opExtrude","SWEPT_BODY",BODY,{"disambiguationData":[OSD([sQuery(id+"F1.wireOp",EDGE,"E9.0.64.0")])]}),"instanceName":"2"});
            var Q74;
            Q74=makeQuery(id+"F14.opPattern","COPY",BODY,{"derivedFrom":makeQuery(id+"F3.opExtrude","SWEPT_BODY",BODY,{"disambiguationData":[OSD([sQuery(id+"F1.wireOp",EDGE,"E9.0.66.0")])]}),"instanceName":"7"});
            var Q75;
            Q75=makeQuery(id+"F14.opPattern","COPY",BODY,{"derivedFrom":makeQuery(id+"F3.opExtrude","SWEPT_BODY",BODY,{"disambiguationData":[OSD([sQuery(id+"F1.wireOp",EDGE,"E9.0.67.0")])]}),"instanceName":"11"});
            var Q76;
            Q76=makeQuery(id+"F3.opExtrude","SWEPT_BODY",BODY,{"disambiguationData":[OSD([sQuery(id+"F1.wireOp",EDGE,"E9.0.69.0")])]});
            var Q77;
            Q77=makeQuery(id+"F15.opPattern","COPY",BODY,{"derivedFrom":makeQuery(id+"F3.opExtrude","SWEPT_BODY",BODY,{"disambiguationData":[OSD([sQuery(id+"F1.wireOp",EDGE,"E9.0.65.0")])]}),"instanceName":"8"});
            var Q78;
            Q78=makeQuery(id+"F17.opPattern","COPY",BODY,{"derivedFrom":makeQuery(id+"F3.opExtrude","SWEPT_BODY",BODY,{"disambiguationData":[OSD([sQuery(id+"F1.wireOp",EDGE,"E9.0.61.0")])]}),"instanceName":"6"});
            var Q79;
            Q79=makeQuery(id+"F17.opPattern","COPY",BODY,{"derivedFrom":makeQuery(id+"F3.opExtrude","SWEPT_BODY",BODY,{"disambiguationData":[OSD([sQuery(id+"F1.wireOp",EDGE,"E9.0.62.0")])]}),"instanceName":"6"});
            var Q80;
            Q80=makeQuery(id+"F14.opPattern","COPY",BODY,{"derivedFrom":makeQuery(id+"F3.opExtrude","SWEPT_BODY",BODY,{"disambiguationData":[OSD([sQuery(id+"F1.wireOp",EDGE,"E9.0.66.0")])]}),"instanceName":"5"});
            var Q81;
            Q81=makeQuery(id+"F14.opPattern","COPY",BODY,{"derivedFrom":makeQuery(id+"F3.opExtrude","SWEPT_BODY",BODY,{"disambiguationData":[OSD([sQuery(id+"F1.wireOp",EDGE,"E9.0.67.0")])]}),"instanceName":"4"});
            var Q82;
            Q82=makeQuery(id+"F14.opPattern","COPY",BODY,{"derivedFrom":makeQuery(id+"F3.opExtrude","SWEPT_BODY",BODY,{"disambiguationData":[OSD([sQuery(id+"F1.wireOp",EDGE,"E9.0.66.0")])]}),"instanceName":"4"});
            var Q83;
            Q83=makeQuery(id+"F17.opPattern","COPY",BODY,{"derivedFrom":makeQuery(id+"F3.opExtrude","SWEPT_BODY",BODY,{"disambiguationData":[OSD([sQuery(id+"F1.wireOp",EDGE,"E9.0.62.0")])]}),"instanceName":"15"});
            var Q84;
            Q84=makeQuery(id+"F17.opPattern","COPY",BODY,{"derivedFrom":makeQuery(id+"F3.opExtrude","SWEPT_BODY",BODY,{"disambiguationData":[OSD([sQuery(id+"F1.wireOp",EDGE,"E9.0.61.0")])]}),"instanceName":"15"});
            var Q85;
            Q85=makeQuery(id+"F14.opPattern","COPY",BODY,{"derivedFrom":makeQuery(id+"F3.opExtrude","SWEPT_BODY",BODY,{"disambiguationData":[OSD([sQuery(id+"F1.wireOp",EDGE,"E9.0.67.0")])]}),"instanceName":"3"});
            var Q86;
            Q86=makeQuery(id+"F17.opPattern","COPY",BODY,{"derivedFrom":makeQuery(id+"F3.opExtrude","SWEPT_BODY",BODY,{"disambiguationData":[OSD([sQuery(id+"F1.wireOp",EDGE,"E9.0.62.0")])]}),"instanceName":"14"});
            var Q87;
            Q87=makeQuery(id+"F17.opPattern","COPY",BODY,{"derivedFrom":makeQuery(id+"F3.opExtrude","SWEPT_BODY",BODY,{"disambiguationData":[OSD([sQuery(id+"F1.wireOp",EDGE,"E9.0.61.0")])]}),"instanceName":"14"});
            var Q88;
            Q88=makeQuery(id+"F14.opPattern","COPY",BODY,{"derivedFrom":makeQuery(id+"F3.opExtrude","SWEPT_BODY",BODY,{"disambiguationData":[OSD([sQuery(id+"F1.wireOp",EDGE,"E9.0.66.0")])]}),"instanceName":"3"});
            var Q89;
            Q89=makeQuery(id+"F14.opPattern","COPY",BODY,{"derivedFrom":makeQuery(id+"F3.opExtrude","SWEPT_BODY",BODY,{"disambiguationData":[OSD([sQuery(id+"F1.wireOp",EDGE,"E9.0.67.0")])]}),"instanceName":"2"});
            var Q90;
            Q90=makeQuery(id+"F13.opPattern","COPY",BODY,{"derivedFrom":makeQuery(id+"F3.opExtrude","SWEPT_BODY",BODY,{"disambiguationData":[OSD([sQuery(id+"F1.wireOp",EDGE,"E9.0.68.0")])]}),"instanceName":"1"});
            var Q91;
            Q91=makeQuery(id+"F17.opPattern","COPY",BODY,{"derivedFrom":makeQuery(id+"F3.opExtrude","SWEPT_BODY",BODY,{"disambiguationData":[OSD([sQuery(id+"F1.wireOp",EDGE,"E9.0.62.0")])]}),"instanceName":"13"});
            var Q92;
            Q92=makeQuery(id+"F13.opPattern","COPY",BODY,{"derivedFrom":makeQuery(id+"F3.opExtrude","SWEPT_BODY",BODY,{"disambiguationData":[OSD([sQuery(id+"F1.wireOp",EDGE,"E9.0.68.0")])]}),"instanceName":"2"});
            var Q93;
            Q93=makeQuery(id+"F14.opPattern","COPY",BODY,{"derivedFrom":makeQuery(id+"F3.opExtrude","SWEPT_BODY",BODY,{"disambiguationData":[OSD([sQuery(id+"F1.wireOp",EDGE,"E9.0.66.0")])]}),"instanceName":"2"});
            var Q94;
            Q94=makeQuery(id+"F14.opPattern","COPY",BODY,{"derivedFrom":makeQuery(id+"F3.opExtrude","SWEPT_BODY",BODY,{"disambiguationData":[OSD([sQuery(id+"F1.wireOp",EDGE,"E9.0.67.0")])]}),"instanceName":"12"});
            var Q95;
            Q95=makeQuery(id+"F17.opPattern","COPY",BODY,{"derivedFrom":makeQuery(id+"F3.opExtrude","SWEPT_BODY",BODY,{"disambiguationData":[OSD([sQuery(id+"F1.wireOp",EDGE,"E9.0.61.0")])]}),"instanceName":"13"});
            var Q96;
            Q96=makeQuery(id+"F15.opPattern","COPY",BODY,{"derivedFrom":makeQuery(id+"F3.opExtrude","SWEPT_BODY",BODY,{"disambiguationData":[OSD([sQuery(id+"F1.wireOp",EDGE,"E9.0.64.0")])]}),"instanceName":"3"});
            var Q97;
            Q97=makeQuery(id+"F14.opPattern","COPY",BODY,{"derivedFrom":makeQuery(id+"F3.opExtrude","SWEPT_BODY",BODY,{"disambiguationData":[OSD([sQuery(id+"F1.wireOp",EDGE,"E9.0.67.0")])]}),"instanceName":"1"});
            var Q98;
            Q98=makeQuery(id+"F14.opPattern","COPY",BODY,{"derivedFrom":makeQuery(id+"F3.opExtrude","SWEPT_BODY",BODY,{"disambiguationData":[OSD([sQuery(id+"F1.wireOp",EDGE,"E9.0.66.0")])]}),"instanceName":"1"});
            var Q99;
            Q99=makeQuery(id+"F17.opPattern","COPY",BODY,{"derivedFrom":makeQuery(id+"F3.opExtrude","SWEPT_BODY",BODY,{"disambiguationData":[OSD([sQuery(id+"F1.wireOp",EDGE,"E9.0.62.0")])]}),"instanceName":"12"});
            var Q100;
            Q100=makeQuery(id+"F13.opPattern","COPY",BODY,{"derivedFrom":makeQuery(id+"F3.opExtrude","SWEPT_BODY",BODY,{"disambiguationData":[OSD([sQuery(id+"F1.wireOp",EDGE,"E9.0.68.0")])]}),"instanceName":"11"});
            var Q101;
            Q101=makeQuery(id+"F17.opPattern","COPY",BODY,{"derivedFrom":makeQuery(id+"F3.opExtrude","SWEPT_BODY",BODY,{"disambiguationData":[OSD([sQuery(id+"F1.wireOp",EDGE,"E9.0.61.0")])]}),"instanceName":"12"});
            var Q102;
            Q102=makeQuery(id+"F17.opPattern","COPY",BODY,{"derivedFrom":makeQuery(id+"F3.opExtrude","SWEPT_BODY",BODY,{"disambiguationData":[OSD([sQuery(id+"F1.wireOp",EDGE,"E9.0.62.0")])]}),"instanceName":"11"});
            var Q103;
            Q103=makeQuery(id+"F17.opPattern","COPY",BODY,{"derivedFrom":makeQuery(id+"F3.opExtrude","SWEPT_BODY",BODY,{"disambiguationData":[OSD([sQuery(id+"F1.wireOp",EDGE,"E9.0.61.0")])]}),"instanceName":"11"});
            var Q104;
            Q104=makeQuery(id+"F13.opPattern","COPY",BODY,{"derivedFrom":makeQuery(id+"F3.opExtrude","SWEPT_BODY",BODY,{"disambiguationData":[OSD([sQuery(id+"F1.wireOp",EDGE,"E9.0.68.0")])]}),"instanceName":"10"});
            var Q105;
            Q105=makeQuery(id+"F17.opPattern","COPY",BODY,{"derivedFrom":makeQuery(id+"F3.opExtrude","SWEPT_BODY",BODY,{"disambiguationData":[OSD([sQuery(id+"F1.wireOp",EDGE,"E9.0.62.0")])]}),"instanceName":"10"});
            var Q106;
            Q106=makeQuery(id+"F13.opPattern","COPY",BODY,{"derivedFrom":makeQuery(id+"F3.opExtrude","SWEPT_BODY",BODY,{"disambiguationData":[OSD([sQuery(id+"F1.wireOp",EDGE,"E9.0.68.0")])]}),"instanceName":"9"});
            var Q107;
            Q107=makeQuery(id+"F17.opPattern","COPY",BODY,{"derivedFrom":makeQuery(id+"F3.opExtrude","SWEPT_BODY",BODY,{"disambiguationData":[OSD([sQuery(id+"F1.wireOp",EDGE,"E9.0.61.0")])]}),"instanceName":"10"});
            var Q108;
            Q108=makeQuery(id+"F13.opPattern","COPY",BODY,{"derivedFrom":makeQuery(id+"F3.opExtrude","SWEPT_BODY",BODY,{"disambiguationData":[OSD([sQuery(id+"F1.wireOp",EDGE,"E9.0.68.0")])]}),"instanceName":"8"});
            var Q109;
            Q109=makeQuery(id+"F13.opPattern","COPY",BODY,{"derivedFrom":makeQuery(id+"F3.opExtrude","SWEPT_BODY",BODY,{"disambiguationData":[OSD([sQuery(id+"F1.wireOp",EDGE,"E9.0.68.0")])]}),"instanceName":"7"});
            var Q110;
            Q110=makeQuery(id+"F17.opPattern","COPY",BODY,{"derivedFrom":makeQuery(id+"F3.opExtrude","SWEPT_BODY",BODY,{"disambiguationData":[OSD([sQuery(id+"F1.wireOp",EDGE,"E9.0.62.0")])]}),"instanceName":"9"});
            var Q111;
            Q111=makeQuery(id+"F13.opPattern","COPY",BODY,{"derivedFrom":makeQuery(id+"F3.opExtrude","SWEPT_BODY",BODY,{"disambiguationData":[OSD([sQuery(id+"F1.wireOp",EDGE,"E9.0.68.0")])]}),"instanceName":"3"});
            var Q112;
            Q112=makeQuery(id+"F17.opPattern","COPY",BODY,{"derivedFrom":makeQuery(id+"F3.opExtrude","SWEPT_BODY",BODY,{"disambiguationData":[OSD([sQuery(id+"F1.wireOp",EDGE,"E9.0.61.0")])]}),"instanceName":"9"});
            var Q113;
            Q113=makeQuery(id+"F17.opPattern","COPY",BODY,{"derivedFrom":makeQuery(id+"F3.opExtrude","SWEPT_BODY",BODY,{"disambiguationData":[OSD([sQuery(id+"F1.wireOp",EDGE,"E9.0.62.0")])]}),"instanceName":"8"});
            var Q114;
            Q114=makeQuery(id+"F17.opPattern","COPY",BODY,{"derivedFrom":makeQuery(id+"F3.opExtrude","SWEPT_BODY",BODY,{"disambiguationData":[OSD([sQuery(id+"F1.wireOp",EDGE,"E9.0.61.0")])]}),"instanceName":"8"});
            var Q115;
            Q115=makeQuery(id+"F17.opPattern","COPY",BODY,{"derivedFrom":makeQuery(id+"F3.opExtrude","SWEPT_BODY",BODY,{"disambiguationData":[OSD([sQuery(id+"F1.wireOp",EDGE,"E9.0.62.0")])]}),"instanceName":"7"});
            var Q116;
            Q116=makeQuery(id+"F13.opPattern","COPY",BODY,{"derivedFrom":makeQuery(id+"F3.opExtrude","SWEPT_BODY",BODY,{"disambiguationData":[OSD([sQuery(id+"F1.wireOp",EDGE,"E9.0.68.0")])]}),"instanceName":"5"});
            var Q117;
            Q117=makeQuery(id+"F13.opPattern","COPY",BODY,{"derivedFrom":makeQuery(id+"F3.opExtrude","SWEPT_BODY",BODY,{"disambiguationData":[OSD([sQuery(id+"F1.wireOp",EDGE,"E9.0.68.0")])]}),"instanceName":"4"});
            var Q118;
            Q118=makeQuery(id+"F14.opPattern","COPY",BODY,{"derivedFrom":makeQuery(id+"F3.opExtrude","SWEPT_BODY",BODY,{"disambiguationData":[OSD([sQuery(id+"F1.wireOp",EDGE,"E9.0.66.0")])]}),"instanceName":"9"});
            var Q119;
            Q119=makeQuery(id+"F14.opPattern","COPY",BODY,{"derivedFrom":makeQuery(id+"F3.opExtrude","SWEPT_BODY",BODY,{"disambiguationData":[OSD([sQuery(id+"F1.wireOp",EDGE,"E9.0.67.0")])]}),"instanceName":"9"});
            var Q120;
            Q120=makeQuery(id+"F14.opPattern","COPY",BODY,{"derivedFrom":makeQuery(id+"F3.opExtrude","SWEPT_BODY",BODY,{"disambiguationData":[OSD([sQuery(id+"F1.wireOp",EDGE,"E9.0.66.0")])]}),"instanceName":"10"});
            var Q121;
            Q121=makeQuery(id+"F14.opPattern","COPY",BODY,{"derivedFrom":makeQuery(id+"F3.opExtrude","SWEPT_BODY",BODY,{"disambiguationData":[OSD([sQuery(id+"F1.wireOp",EDGE,"E9.0.67.0")])]}),"instanceName":"10"});
            var Q122;
            Q122=makeQuery(id+"F14.opPattern","COPY",BODY,{"derivedFrom":makeQuery(id+"F3.opExtrude","SWEPT_BODY",BODY,{"disambiguationData":[OSD([sQuery(id+"F1.wireOp",EDGE,"E9.0.66.0")])]}),"instanceName":"12"});
            var Q123;
            Q123=makeQuery(id+"F3.opExtrude","SWEPT_BODY",BODY,{"disambiguationData":[OSD([sQuery(id+"F1.wireOp",EDGE,"E9.0.68.0")])]});
            var Q124;
            Q124=makeQuery(id+"F2.opRevolve","SWEPT_BODY",BODY,{"disambiguationData":[OSD([sQuery(id+"F0.wireOp",EDGE,"E0"),sQuery(id+"F0.wireOp",EDGE,"E1"),sQuery(id+"F0.wireOp",EDGE,"E2"),sQuery(id+"F0.wireOp",EDGE,"E3"),sQuery(id+"F0.wireOp",EDGE,"E6")])]});
            booleanBodies(context, id + "F18", {"operationType" : BooleanOperationType.SUBTRACTION, "tools" : qUnion([Q0, Q1, Q2, Q3, Q4, Q5, Q6, Q7, Q8, Q9, Q10, Q11, Q12, Q13, Q14, Q15, Q16, Q17, Q18, Q19, Q20, Q21, Q22, Q23, Q24, Q25, Q26, Q27, Q28, Q29, Q30, Q31, Q32, Q33, Q34, Q35, Q36, Q37, Q38, Q39, Q40, Q41, Q42, Q43, Q44, Q45, Q46, Q47, Q48, Q49, Q50, Q51, Q52, Q53, Q54, Q55, Q56, Q57, Q58, Q59, Q60, Q61, Q62, Q63, Q64, Q65, Q66, Q67, Q68, Q69, Q70, Q71, Q72, Q73, Q74, Q75, Q76, Q77, Q78, Q79, Q80, Q81, Q82, Q83, Q84, Q85, Q86, Q87, Q88, Q89, Q90, Q91, Q92, Q93, Q94, Q95, Q96, Q97, Q98, Q99, Q100, Q101, Q102, Q103, Q104, Q105, Q106, Q107, Q108, Q109, Q110, Q111, Q112, Q113, Q114, Q115, Q116, Q117, Q118, Q119, Q120, Q121, Q122, Q123]), "targets" : qUnion([Q124])});
        }
        {
            var Q0;
            Q0=makeQuery(id+"F3.opExtrude","SWEPT_BODY",BODY,{"disambiguationData":[OSD([sQuery(id+"F1.wireOp",EDGE,"E9.0.60.0")])]});
            var Q1;
            Q1=makeQuery(id+"F2.opRevolve","SWEPT_FACE",FACE,{"disambiguationData":[OSD([sQuery(id+"F0.wireOp",EDGE,"E1")])]});
            circularPattern(context, id + "F19", {"entities" : qUnion([Q0]), "axis" : qUnion([Q1]), "angle" : 180 * degree, "instanceCount" : 17, "oppositeDirection" : true, "equalSpace" : true});
        }
        {
            var Q0;
            Q0=makeQuery(id+"F3.opExtrude","SWEPT_BODY",BODY,{"disambiguationData":[OSD([sQuery(id+"F1.wireOp",EDGE,"E9.0.59.0")])]});
            var Q1;
            Q1=makeQuery(id+"F3.opExtrude","SWEPT_BODY",BODY,{"disambiguationData":[OSD([sQuery(id+"F1.wireOp",EDGE,"E9.0.58.0")])]});
            var Q2;
            Q2=makeQuery(id+"F2.opRevolve","SWEPT_FACE",FACE,{"disambiguationData":[OSD([sQuery(id+"F0.wireOp",EDGE,"E1")])]});
            circularPattern(context, id + "F20", {"entities" : qUnion([Q0, Q1]), "axis" : qUnion([Q2]), "angle" : 180 * degree, "instanceCount" : 18, "oppositeDirection" : true, "equalSpace" : true});
        }
        {
            var Q0;
            Q0=makeQuery(id+"F3.opExtrude","SWEPT_BODY",BODY,{"disambiguationData":[OSD([sQuery(id+"F1.wireOp",EDGE,"E9.0.57.0")])]});
            var Q1;
            Q1=makeQuery(id+"F2.opRevolve","SWEPT_FACE",FACE,{"disambiguationData":[OSD([sQuery(id+"F0.wireOp",EDGE,"E1")])]});
            circularPattern(context, id + "F21", {"entities" : qUnion([Q0]), "axis" : qUnion([Q1]), "angle" : 180 * degree, "instanceCount" : 19, "oppositeDirection" : true, "equalSpace" : true});
        }
        {
            var Q0;
            Q0=makeQuery(id+"F3.opExtrude","SWEPT_BODY",BODY,{"disambiguationData":[OSD([sQuery(id+"F1.wireOp",EDGE,"E9.0.56.0")])]});
            var Q1;
            Q1=makeQuery(id+"F3.opExtrude","SWEPT_BODY",BODY,{"disambiguationData":[OSD([sQuery(id+"F1.wireOp",EDGE,"E9.0.55.0")])]});
            var Q2;
            Q2=makeQuery(id+"F2.opRevolve","SWEPT_FACE",FACE,{"disambiguationData":[OSD([sQuery(id+"F0.wireOp",EDGE,"E1")])]});
            circularPattern(context, id + "F22", {"entities" : qUnion([Q0, Q1]), "axis" : qUnion([Q2]), "angle" : 180 * degree, "instanceCount" : 20, "oppositeDirection" : true, "equalSpace" : true});
        }
        {
            var Q0;
            Q0=makeQuery(id+"F22.opPattern","COPY",BODY,{"derivedFrom":makeQuery(id+"F3.opExtrude","SWEPT_BODY",BODY,{"disambiguationData":[OSD([sQuery(id+"F1.wireOp",EDGE,"E9.0.55.0")])]}),"instanceName":"13"});
            var Q1;
            Q1=makeQuery(id+"F22.opPattern","COPY",BODY,{"derivedFrom":makeQuery(id+"F3.opExtrude","SWEPT_BODY",BODY,{"disambiguationData":[OSD([sQuery(id+"F1.wireOp",EDGE,"E9.0.56.0")])]}),"instanceName":"13"});
            var Q2;
            Q2=makeQuery(id+"F22.opPattern","COPY",BODY,{"derivedFrom":makeQuery(id+"F3.opExtrude","SWEPT_BODY",BODY,{"disambiguationData":[OSD([sQuery(id+"F1.wireOp",EDGE,"E9.0.55.0")])]}),"instanceName":"14"});
            var Q3;
            Q3=makeQuery(id+"F22.opPattern","COPY",BODY,{"derivedFrom":makeQuery(id+"F3.opExtrude","SWEPT_BODY",BODY,{"disambiguationData":[OSD([sQuery(id+"F1.wireOp",EDGE,"E9.0.56.0")])]}),"instanceName":"14"});
            var Q4;
            Q4=makeQuery(id+"F22.opPattern","COPY",BODY,{"derivedFrom":makeQuery(id+"F3.opExtrude","SWEPT_BODY",BODY,{"disambiguationData":[OSD([sQuery(id+"F1.wireOp",EDGE,"E9.0.56.0")])]}),"instanceName":"12"});
            var Q5;
            Q5=makeQuery(id+"F19.opPattern","COPY",BODY,{"derivedFrom":makeQuery(id+"F3.opExtrude","SWEPT_BODY",BODY,{"disambiguationData":[OSD([sQuery(id+"F1.wireOp",EDGE,"E9.0.60.0")])]}),"instanceName":"4"});
            var Q6;
            Q6=makeQuery(id+"F19.opPattern","COPY",BODY,{"derivedFrom":makeQuery(id+"F3.opExtrude","SWEPT_BODY",BODY,{"disambiguationData":[OSD([sQuery(id+"F1.wireOp",EDGE,"E9.0.60.0")])]}),"instanceName":"11"});
            var Q7;
            Q7=makeQuery(id+"F22.opPattern","COPY",BODY,{"derivedFrom":makeQuery(id+"F3.opExtrude","SWEPT_BODY",BODY,{"disambiguationData":[OSD([sQuery(id+"F1.wireOp",EDGE,"E9.0.55.0")])]}),"instanceName":"12"});
            var Q8;
            Q8=makeQuery(id+"F19.opPattern","COPY",BODY,{"derivedFrom":makeQuery(id+"F3.opExtrude","SWEPT_BODY",BODY,{"disambiguationData":[OSD([sQuery(id+"F1.wireOp",EDGE,"E9.0.60.0")])]}),"instanceName":"12"});
            var Q9;
            Q9=makeQuery(id+"F20.opPattern","COPY",BODY,{"derivedFrom":makeQuery(id+"F3.opExtrude","SWEPT_BODY",BODY,{"disambiguationData":[OSD([sQuery(id+"F1.wireOp",EDGE,"E9.0.58.0")])]}),"instanceName":"16"});
            var Q10;
            Q10=makeQuery(id+"F22.opPattern","COPY",BODY,{"derivedFrom":makeQuery(id+"F3.opExtrude","SWEPT_BODY",BODY,{"disambiguationData":[OSD([sQuery(id+"F1.wireOp",EDGE,"E9.0.56.0")])]}),"instanceName":"11"});
            var Q11;
            Q11=makeQuery(id+"F22.opPattern","COPY",BODY,{"derivedFrom":makeQuery(id+"F3.opExtrude","SWEPT_BODY",BODY,{"disambiguationData":[OSD([sQuery(id+"F1.wireOp",EDGE,"E9.0.55.0")])]}),"instanceName":"11"});
            var Q12;
            Q12=makeQuery(id+"F22.opPattern","COPY",BODY,{"derivedFrom":makeQuery(id+"F3.opExtrude","SWEPT_BODY",BODY,{"disambiguationData":[OSD([sQuery(id+"F1.wireOp",EDGE,"E9.0.56.0")])]}),"instanceName":"10"});
            var Q13;
            Q13=makeQuery(id+"F22.opPattern","COPY",BODY,{"derivedFrom":makeQuery(id+"F3.opExtrude","SWEPT_BODY",BODY,{"disambiguationData":[OSD([sQuery(id+"F1.wireOp",EDGE,"E9.0.55.0")])]}),"instanceName":"10"});
            var Q14;
            Q14=makeQuery(id+"F22.opPattern","COPY",BODY,{"derivedFrom":makeQuery(id+"F3.opExtrude","SWEPT_BODY",BODY,{"disambiguationData":[OSD([sQuery(id+"F1.wireOp",EDGE,"E9.0.55.0")])]}),"instanceName":"16"});
            var Q15;
            Q15=makeQuery(id+"F20.opPattern","COPY",BODY,{"derivedFrom":makeQuery(id+"F3.opExtrude","SWEPT_BODY",BODY,{"disambiguationData":[OSD([sQuery(id+"F1.wireOp",EDGE,"E9.0.59.0")])]}),"instanceName":"16"});
            var Q16;
            Q16=makeQuery(id+"F19.opPattern","COPY",BODY,{"derivedFrom":makeQuery(id+"F3.opExtrude","SWEPT_BODY",BODY,{"disambiguationData":[OSD([sQuery(id+"F1.wireOp",EDGE,"E9.0.60.0")])]}),"instanceName":"14"});
            var Q17;
            Q17=makeQuery(id+"F19.opPattern","COPY",BODY,{"derivedFrom":makeQuery(id+"F3.opExtrude","SWEPT_BODY",BODY,{"disambiguationData":[OSD([sQuery(id+"F1.wireOp",EDGE,"E9.0.60.0")])]}),"instanceName":"15"});
            var Q18;
            Q18=makeQuery(id+"F22.opPattern","COPY",BODY,{"derivedFrom":makeQuery(id+"F3.opExtrude","SWEPT_BODY",BODY,{"disambiguationData":[OSD([sQuery(id+"F1.wireOp",EDGE,"E9.0.56.0")])]}),"instanceName":"9"});
            var Q19;
            Q19=makeQuery(id+"F19.opPattern","COPY",BODY,{"derivedFrom":makeQuery(id+"F3.opExtrude","SWEPT_BODY",BODY,{"disambiguationData":[OSD([sQuery(id+"F1.wireOp",EDGE,"E9.0.60.0")])]}),"instanceName":"16"});
            var Q20;
            Q20=makeQuery(id+"F22.opPattern","COPY",BODY,{"derivedFrom":makeQuery(id+"F3.opExtrude","SWEPT_BODY",BODY,{"disambiguationData":[OSD([sQuery(id+"F1.wireOp",EDGE,"E9.0.55.0")])]}),"instanceName":"9"});
            var Q21;
            Q21=makeQuery(id+"F20.opPattern","COPY",BODY,{"derivedFrom":makeQuery(id+"F3.opExtrude","SWEPT_BODY",BODY,{"disambiguationData":[OSD([sQuery(id+"F1.wireOp",EDGE,"E9.0.58.0")])]}),"instanceName":"1"});
            var Q22;
            Q22=makeQuery(id+"F20.opPattern","COPY",BODY,{"derivedFrom":makeQuery(id+"F3.opExtrude","SWEPT_BODY",BODY,{"disambiguationData":[OSD([sQuery(id+"F1.wireOp",EDGE,"E9.0.59.0")])]}),"instanceName":"1"});
            var Q23;
            Q23=makeQuery(id+"F22.opPattern","COPY",BODY,{"derivedFrom":makeQuery(id+"F3.opExtrude","SWEPT_BODY",BODY,{"disambiguationData":[OSD([sQuery(id+"F1.wireOp",EDGE,"E9.0.56.0")])]}),"instanceName":"8"});
            var Q24;
            Q24=makeQuery(id+"F19.opPattern","COPY",BODY,{"derivedFrom":makeQuery(id+"F3.opExtrude","SWEPT_BODY",BODY,{"disambiguationData":[OSD([sQuery(id+"F1.wireOp",EDGE,"E9.0.60.0")])]}),"instanceName":"13"});
            var Q25;
            Q25=makeQuery(id+"F22.opPattern","COPY",BODY,{"derivedFrom":makeQuery(id+"F3.opExtrude","SWEPT_BODY",BODY,{"disambiguationData":[OSD([sQuery(id+"F1.wireOp",EDGE,"E9.0.55.0")])]}),"instanceName":"8"});
            var Q26;
            Q26=makeQuery(id+"F20.opPattern","COPY",BODY,{"derivedFrom":makeQuery(id+"F3.opExtrude","SWEPT_BODY",BODY,{"disambiguationData":[OSD([sQuery(id+"F1.wireOp",EDGE,"E9.0.58.0")])]}),"instanceName":"2"});
            var Q27;
            Q27=makeQuery(id+"F22.opPattern","COPY",BODY,{"derivedFrom":makeQuery(id+"F3.opExtrude","SWEPT_BODY",BODY,{"disambiguationData":[OSD([sQuery(id+"F1.wireOp",EDGE,"E9.0.56.0")])]}),"instanceName":"7"});
            var Q28;
            Q28=makeQuery(id+"F22.opPattern","COPY",BODY,{"derivedFrom":makeQuery(id+"F3.opExtrude","SWEPT_BODY",BODY,{"disambiguationData":[OSD([sQuery(id+"F1.wireOp",EDGE,"E9.0.55.0")])]}),"instanceName":"7"});
            var Q29;
            Q29=makeQuery(id+"F22.opPattern","COPY",BODY,{"derivedFrom":makeQuery(id+"F3.opExtrude","SWEPT_BODY",BODY,{"disambiguationData":[OSD([sQuery(id+"F1.wireOp",EDGE,"E9.0.56.0")])]}),"instanceName":"6"});
            var Q30;
            Q30=makeQuery(id+"F20.opPattern","COPY",BODY,{"derivedFrom":makeQuery(id+"F3.opExtrude","SWEPT_BODY",BODY,{"disambiguationData":[OSD([sQuery(id+"F1.wireOp",EDGE,"E9.0.58.0")])]}),"instanceName":"14"});
            var Q31;
            Q31=makeQuery(id+"F22.opPattern","COPY",BODY,{"derivedFrom":makeQuery(id+"F3.opExtrude","SWEPT_BODY",BODY,{"disambiguationData":[OSD([sQuery(id+"F1.wireOp",EDGE,"E9.0.55.0")])]}),"instanceName":"6"});
            var Q32;
            Q32=makeQuery(id+"F22.opPattern","COPY",BODY,{"derivedFrom":makeQuery(id+"F3.opExtrude","SWEPT_BODY",BODY,{"disambiguationData":[OSD([sQuery(id+"F1.wireOp",EDGE,"E9.0.56.0")])]}),"instanceName":"5"});
            var Q33;
            Q33=makeQuery(id+"F22.opPattern","COPY",BODY,{"derivedFrom":makeQuery(id+"F3.opExtrude","SWEPT_BODY",BODY,{"disambiguationData":[OSD([sQuery(id+"F1.wireOp",EDGE,"E9.0.55.0")])]}),"instanceName":"5"});
            var Q34;
            Q34=makeQuery(id+"F22.opPattern","COPY",BODY,{"derivedFrom":makeQuery(id+"F3.opExtrude","SWEPT_BODY",BODY,{"disambiguationData":[OSD([sQuery(id+"F1.wireOp",EDGE,"E9.0.56.0")])]}),"instanceName":"4"});
            var Q35;
            Q35=makeQuery(id+"F3.opExtrude","SWEPT_BODY",BODY,{"disambiguationData":[OSD([sQuery(id+"F1.wireOp",EDGE,"E9.0.55.0")])]});
            var Q36;
            Q36=makeQuery(id+"F3.opExtrude","SWEPT_BODY",BODY,{"disambiguationData":[OSD([sQuery(id+"F1.wireOp",EDGE,"E9.0.56.0")])]});
            var Q37;
            Q37=makeQuery(id+"F22.opPattern","COPY",BODY,{"derivedFrom":makeQuery(id+"F3.opExtrude","SWEPT_BODY",BODY,{"disambiguationData":[OSD([sQuery(id+"F1.wireOp",EDGE,"E9.0.55.0")])]}),"instanceName":"4"});
            var Q38;
            Q38=makeQuery(id+"F22.opPattern","COPY",BODY,{"derivedFrom":makeQuery(id+"F3.opExtrude","SWEPT_BODY",BODY,{"disambiguationData":[OSD([sQuery(id+"F1.wireOp",EDGE,"E9.0.56.0")])]}),"instanceName":"3"});
            var Q39;
            Q39=makeQuery(id+"F22.opPattern","COPY",BODY,{"derivedFrom":makeQuery(id+"F3.opExtrude","SWEPT_BODY",BODY,{"disambiguationData":[OSD([sQuery(id+"F1.wireOp",EDGE,"E9.0.55.0")])]}),"instanceName":"3"});
            var Q40;
            Q40=makeQuery(id+"F21.opPattern","COPY",BODY,{"derivedFrom":makeQuery(id+"F3.opExtrude","SWEPT_BODY",BODY,{"disambiguationData":[OSD([sQuery(id+"F1.wireOp",EDGE,"E9.0.57.0")])]}),"instanceName":"2"});
            var Q41;
            Q41=makeQuery(id+"F21.opPattern","COPY",BODY,{"derivedFrom":makeQuery(id+"F3.opExtrude","SWEPT_BODY",BODY,{"disambiguationData":[OSD([sQuery(id+"F1.wireOp",EDGE,"E9.0.57.0")])]}),"instanceName":"3"});
            var Q42;
            Q42=makeQuery(id+"F21.opPattern","COPY",BODY,{"derivedFrom":makeQuery(id+"F3.opExtrude","SWEPT_BODY",BODY,{"disambiguationData":[OSD([sQuery(id+"F1.wireOp",EDGE,"E9.0.57.0")])]}),"instanceName":"4"});
            var Q43;
            Q43=makeQuery(id+"F3.opExtrude","SWEPT_BODY",BODY,{"disambiguationData":[OSD([sQuery(id+"F1.wireOp",EDGE,"E9.0.57.0")])]});
            var Q44;
            Q44=makeQuery(id+"F20.opPattern","COPY",BODY,{"derivedFrom":makeQuery(id+"F3.opExtrude","SWEPT_BODY",BODY,{"disambiguationData":[OSD([sQuery(id+"F1.wireOp",EDGE,"E9.0.58.0")])]}),"instanceName":"8"});
            var Q45;
            Q45=makeQuery(id+"F21.opPattern","COPY",BODY,{"derivedFrom":makeQuery(id+"F3.opExtrude","SWEPT_BODY",BODY,{"disambiguationData":[OSD([sQuery(id+"F1.wireOp",EDGE,"E9.0.57.0")])]}),"instanceName":"5"});
            var Q46;
            Q46=makeQuery(id+"F21.opPattern","COPY",BODY,{"derivedFrom":makeQuery(id+"F3.opExtrude","SWEPT_BODY",BODY,{"disambiguationData":[OSD([sQuery(id+"F1.wireOp",EDGE,"E9.0.57.0")])]}),"instanceName":"6"});
            var Q47;
            Q47=makeQuery(id+"F20.opPattern","COPY",BODY,{"derivedFrom":makeQuery(id+"F3.opExtrude","SWEPT_BODY",BODY,{"disambiguationData":[OSD([sQuery(id+"F1.wireOp",EDGE,"E9.0.59.0")])]}),"instanceName":"8"});
            var Q48;
            Q48=makeQuery(id+"F3.opExtrude","SWEPT_BODY",BODY,{"disambiguationData":[OSD([sQuery(id+"F1.wireOp",EDGE,"E9.0.58.0")])]});
            var Q49;
            Q49=makeQuery(id+"F22.opPattern","COPY",BODY,{"derivedFrom":makeQuery(id+"F3.opExtrude","SWEPT_BODY",BODY,{"disambiguationData":[OSD([sQuery(id+"F1.wireOp",EDGE,"E9.0.56.0")])]}),"instanceName":"2"});
            var Q50;
            Q50=makeQuery(id+"F21.opPattern","COPY",BODY,{"derivedFrom":makeQuery(id+"F3.opExtrude","SWEPT_BODY",BODY,{"disambiguationData":[OSD([sQuery(id+"F1.wireOp",EDGE,"E9.0.57.0")])]}),"instanceName":"7"});
            var Q51;
            Q51=makeQuery(id+"F22.opPattern","COPY",BODY,{"derivedFrom":makeQuery(id+"F3.opExtrude","SWEPT_BODY",BODY,{"disambiguationData":[OSD([sQuery(id+"F1.wireOp",EDGE,"E9.0.55.0")])]}),"instanceName":"2"});
            var Q52;
            Q52=makeQuery(id+"F3.opExtrude","SWEPT_BODY",BODY,{"disambiguationData":[OSD([sQuery(id+"F1.wireOp",EDGE,"E9.0.59.0")])]});
            var Q53;
            Q53=makeQuery(id+"F22.opPattern","COPY",BODY,{"derivedFrom":makeQuery(id+"F3.opExtrude","SWEPT_BODY",BODY,{"disambiguationData":[OSD([sQuery(id+"F1.wireOp",EDGE,"E9.0.56.0")])]}),"instanceName":"1"});
            var Q54;
            Q54=makeQuery(id+"F21.opPattern","COPY",BODY,{"derivedFrom":makeQuery(id+"F3.opExtrude","SWEPT_BODY",BODY,{"disambiguationData":[OSD([sQuery(id+"F1.wireOp",EDGE,"E9.0.57.0")])]}),"instanceName":"8"});
            var Q55;
            Q55=makeQuery(id+"F20.opPattern","COPY",BODY,{"derivedFrom":makeQuery(id+"F3.opExtrude","SWEPT_BODY",BODY,{"disambiguationData":[OSD([sQuery(id+"F1.wireOp",EDGE,"E9.0.58.0")])]}),"instanceName":"9"});
            var Q56;
            Q56=makeQuery(id+"F21.opPattern","COPY",BODY,{"derivedFrom":makeQuery(id+"F3.opExtrude","SWEPT_BODY",BODY,{"disambiguationData":[OSD([sQuery(id+"F1.wireOp",EDGE,"E9.0.57.0")])]}),"instanceName":"9"});
            var Q57;
            Q57=makeQuery(id+"F22.opPattern","COPY",BODY,{"derivedFrom":makeQuery(id+"F3.opExtrude","SWEPT_BODY",BODY,{"disambiguationData":[OSD([sQuery(id+"F1.wireOp",EDGE,"E9.0.55.0")])]}),"instanceName":"1"});
            var Q58;
            Q58=makeQuery(id+"F21.opPattern","COPY",BODY,{"derivedFrom":makeQuery(id+"F3.opExtrude","SWEPT_BODY",BODY,{"disambiguationData":[OSD([sQuery(id+"F1.wireOp",EDGE,"E9.0.57.0")])]}),"instanceName":"18"});
            var Q59;
            Q59=makeQuery(id+"F21.opPattern","COPY",BODY,{"derivedFrom":makeQuery(id+"F3.opExtrude","SWEPT_BODY",BODY,{"disambiguationData":[OSD([sQuery(id+"F1.wireOp",EDGE,"E9.0.57.0")])]}),"instanceName":"17"});
            var Q60;
            Q60=makeQuery(id+"F20.opPattern","COPY",BODY,{"derivedFrom":makeQuery(id+"F3.opExtrude","SWEPT_BODY",BODY,{"disambiguationData":[OSD([sQuery(id+"F1.wireOp",EDGE,"E9.0.58.0")])]}),"instanceName":"6"});
            var Q61;
            Q61=makeQuery(id+"F21.opPattern","COPY",BODY,{"derivedFrom":makeQuery(id+"F3.opExtrude","SWEPT_BODY",BODY,{"disambiguationData":[OSD([sQuery(id+"F1.wireOp",EDGE,"E9.0.57.0")])]}),"instanceName":"10"});
            var Q62;
            Q62=makeQuery(id+"F21.opPattern","COPY",BODY,{"derivedFrom":makeQuery(id+"F3.opExtrude","SWEPT_BODY",BODY,{"disambiguationData":[OSD([sQuery(id+"F1.wireOp",EDGE,"E9.0.57.0")])]}),"instanceName":"16"});
            var Q63;
            Q63=makeQuery(id+"F3.opExtrude","SWEPT_BODY",BODY,{"disambiguationData":[OSD([sQuery(id+"F1.wireOp",EDGE,"E9.0.60.0")])]});
            var Q64;
            Q64=makeQuery(id+"F19.opPattern","COPY",BODY,{"derivedFrom":makeQuery(id+"F3.opExtrude","SWEPT_BODY",BODY,{"disambiguationData":[OSD([sQuery(id+"F1.wireOp",EDGE,"E9.0.60.0")])]}),"instanceName":"10"});
            var Q65;
            Q65=makeQuery(id+"F20.opPattern","COPY",BODY,{"derivedFrom":makeQuery(id+"F3.opExtrude","SWEPT_BODY",BODY,{"disambiguationData":[OSD([sQuery(id+"F1.wireOp",EDGE,"E9.0.58.0")])]}),"instanceName":"5"});
            var Q66;
            Q66=makeQuery(id+"F20.opPattern","COPY",BODY,{"derivedFrom":makeQuery(id+"F3.opExtrude","SWEPT_BODY",BODY,{"disambiguationData":[OSD([sQuery(id+"F1.wireOp",EDGE,"E9.0.59.0")])]}),"instanceName":"4"});
            var Q67;
            Q67=makeQuery(id+"F20.opPattern","COPY",BODY,{"derivedFrom":makeQuery(id+"F3.opExtrude","SWEPT_BODY",BODY,{"disambiguationData":[OSD([sQuery(id+"F1.wireOp",EDGE,"E9.0.58.0")])]}),"instanceName":"4"});
            var Q68;
            Q68=makeQuery(id+"F20.opPattern","COPY",BODY,{"derivedFrom":makeQuery(id+"F3.opExtrude","SWEPT_BODY",BODY,{"disambiguationData":[OSD([sQuery(id+"F1.wireOp",EDGE,"E9.0.59.0")])]}),"instanceName":"6"});
            var Q69;
            Q69=makeQuery(id+"F20.opPattern","COPY",BODY,{"derivedFrom":makeQuery(id+"F3.opExtrude","SWEPT_BODY",BODY,{"disambiguationData":[OSD([sQuery(id+"F1.wireOp",EDGE,"E9.0.58.0")])]}),"instanceName":"7"});
            var Q70;
            Q70=makeQuery(id+"F21.opPattern","COPY",BODY,{"derivedFrom":makeQuery(id+"F3.opExtrude","SWEPT_BODY",BODY,{"disambiguationData":[OSD([sQuery(id+"F1.wireOp",EDGE,"E9.0.57.0")])]}),"instanceName":"13"});
            var Q71;
            Q71=makeQuery(id+"F20.opPattern","COPY",BODY,{"derivedFrom":makeQuery(id+"F3.opExtrude","SWEPT_BODY",BODY,{"disambiguationData":[OSD([sQuery(id+"F1.wireOp",EDGE,"E9.0.59.0")])]}),"instanceName":"3"});
            var Q72;
            Q72=makeQuery(id+"F21.opPattern","COPY",BODY,{"derivedFrom":makeQuery(id+"F3.opExtrude","SWEPT_BODY",BODY,{"disambiguationData":[OSD([sQuery(id+"F1.wireOp",EDGE,"E9.0.57.0")])]}),"instanceName":"14"});
            var Q73;
            Q73=makeQuery(id+"F21.opPattern","COPY",BODY,{"derivedFrom":makeQuery(id+"F3.opExtrude","SWEPT_BODY",BODY,{"disambiguationData":[OSD([sQuery(id+"F1.wireOp",EDGE,"E9.0.57.0")])]}),"instanceName":"15"});
            var Q74;
            Q74=makeQuery(id+"F20.opPattern","COPY",BODY,{"derivedFrom":makeQuery(id+"F3.opExtrude","SWEPT_BODY",BODY,{"disambiguationData":[OSD([sQuery(id+"F1.wireOp",EDGE,"E9.0.59.0")])]}),"instanceName":"17"});
            var Q75;
            Q75=makeQuery(id+"F21.opPattern","COPY",BODY,{"derivedFrom":makeQuery(id+"F3.opExtrude","SWEPT_BODY",BODY,{"disambiguationData":[OSD([sQuery(id+"F1.wireOp",EDGE,"E9.0.57.0")])]}),"instanceName":"11"});
            var Q76;
            Q76=makeQuery(id+"F20.opPattern","COPY",BODY,{"derivedFrom":makeQuery(id+"F3.opExtrude","SWEPT_BODY",BODY,{"disambiguationData":[OSD([sQuery(id+"F1.wireOp",EDGE,"E9.0.58.0")])]}),"instanceName":"17"});
            var Q77;
            Q77=makeQuery(id+"F20.opPattern","COPY",BODY,{"derivedFrom":makeQuery(id+"F3.opExtrude","SWEPT_BODY",BODY,{"disambiguationData":[OSD([sQuery(id+"F1.wireOp",EDGE,"E9.0.59.0")])]}),"instanceName":"7"});
            var Q78;
            Q78=makeQuery(id+"F20.opPattern","COPY",BODY,{"derivedFrom":makeQuery(id+"F3.opExtrude","SWEPT_BODY",BODY,{"disambiguationData":[OSD([sQuery(id+"F1.wireOp",EDGE,"E9.0.59.0")])]}),"instanceName":"14"});
            var Q79;
            Q79=makeQuery(id+"F20.opPattern","COPY",BODY,{"derivedFrom":makeQuery(id+"F3.opExtrude","SWEPT_BODY",BODY,{"disambiguationData":[OSD([sQuery(id+"F1.wireOp",EDGE,"E9.0.59.0")])]}),"instanceName":"2"});
            var Q80;
            Q80=makeQuery(id+"F21.opPattern","COPY",BODY,{"derivedFrom":makeQuery(id+"F3.opExtrude","SWEPT_BODY",BODY,{"disambiguationData":[OSD([sQuery(id+"F1.wireOp",EDGE,"E9.0.57.0")])]}),"instanceName":"12"});
            var Q81;
            Q81=makeQuery(id+"F22.opPattern","COPY",BODY,{"derivedFrom":makeQuery(id+"F3.opExtrude","SWEPT_BODY",BODY,{"disambiguationData":[OSD([sQuery(id+"F1.wireOp",EDGE,"E9.0.55.0")])]}),"instanceName":"15"});
            var Q82;
            Q82=makeQuery(id+"F22.opPattern","COPY",BODY,{"derivedFrom":makeQuery(id+"F3.opExtrude","SWEPT_BODY",BODY,{"disambiguationData":[OSD([sQuery(id+"F1.wireOp",EDGE,"E9.0.56.0")])]}),"instanceName":"15"});
            var Q83;
            Q83=makeQuery(id+"F20.opPattern","COPY",BODY,{"derivedFrom":makeQuery(id+"F3.opExtrude","SWEPT_BODY",BODY,{"disambiguationData":[OSD([sQuery(id+"F1.wireOp",EDGE,"E9.0.59.0")])]}),"instanceName":"9"});
            var Q84;
            Q84=makeQuery(id+"F20.opPattern","COPY",BODY,{"derivedFrom":makeQuery(id+"F3.opExtrude","SWEPT_BODY",BODY,{"disambiguationData":[OSD([sQuery(id+"F1.wireOp",EDGE,"E9.0.58.0")])]}),"instanceName":"10"});
            var Q85;
            Q85=makeQuery(id+"F20.opPattern","COPY",BODY,{"derivedFrom":makeQuery(id+"F3.opExtrude","SWEPT_BODY",BODY,{"disambiguationData":[OSD([sQuery(id+"F1.wireOp",EDGE,"E9.0.59.0")])]}),"instanceName":"10"});
            var Q86;
            Q86=makeQuery(id+"F20.opPattern","COPY",BODY,{"derivedFrom":makeQuery(id+"F3.opExtrude","SWEPT_BODY",BODY,{"disambiguationData":[OSD([sQuery(id+"F1.wireOp",EDGE,"E9.0.58.0")])]}),"instanceName":"11"});
            var Q87;
            Q87=makeQuery(id+"F20.opPattern","COPY",BODY,{"derivedFrom":makeQuery(id+"F3.opExtrude","SWEPT_BODY",BODY,{"disambiguationData":[OSD([sQuery(id+"F1.wireOp",EDGE,"E9.0.59.0")])]}),"instanceName":"11"});
            var Q88;
            Q88=makeQuery(id+"F20.opPattern","COPY",BODY,{"derivedFrom":makeQuery(id+"F3.opExtrude","SWEPT_BODY",BODY,{"disambiguationData":[OSD([sQuery(id+"F1.wireOp",EDGE,"E9.0.58.0")])]}),"instanceName":"12"});
            var Q89;
            Q89=makeQuery(id+"F19.opPattern","COPY",BODY,{"derivedFrom":makeQuery(id+"F3.opExtrude","SWEPT_BODY",BODY,{"disambiguationData":[OSD([sQuery(id+"F1.wireOp",EDGE,"E9.0.60.0")])]}),"instanceName":"9"});
            var Q90;
            Q90=makeQuery(id+"F19.opPattern","COPY",BODY,{"derivedFrom":makeQuery(id+"F3.opExtrude","SWEPT_BODY",BODY,{"disambiguationData":[OSD([sQuery(id+"F1.wireOp",EDGE,"E9.0.60.0")])]}),"instanceName":"8"});
            var Q91;
            Q91=makeQuery(id+"F20.opPattern","COPY",BODY,{"derivedFrom":makeQuery(id+"F3.opExtrude","SWEPT_BODY",BODY,{"disambiguationData":[OSD([sQuery(id+"F1.wireOp",EDGE,"E9.0.59.0")])]}),"instanceName":"15"});
            var Q92;
            Q92=makeQuery(id+"F21.opPattern","COPY",BODY,{"derivedFrom":makeQuery(id+"F3.opExtrude","SWEPT_BODY",BODY,{"disambiguationData":[OSD([sQuery(id+"F1.wireOp",EDGE,"E9.0.57.0")])]}),"instanceName":"1"});
            var Q93;
            Q93=makeQuery(id+"F22.opPattern","COPY",BODY,{"derivedFrom":makeQuery(id+"F3.opExtrude","SWEPT_BODY",BODY,{"disambiguationData":[OSD([sQuery(id+"F1.wireOp",EDGE,"E9.0.56.0")])]}),"instanceName":"19"});
            var Q94;
            Q94=makeQuery(id+"F19.opPattern","COPY",BODY,{"derivedFrom":makeQuery(id+"F3.opExtrude","SWEPT_BODY",BODY,{"disambiguationData":[OSD([sQuery(id+"F1.wireOp",EDGE,"E9.0.60.0")])]}),"instanceName":"1"});
            var Q95;
            Q95=makeQuery(id+"F22.opPattern","COPY",BODY,{"derivedFrom":makeQuery(id+"F3.opExtrude","SWEPT_BODY",BODY,{"disambiguationData":[OSD([sQuery(id+"F1.wireOp",EDGE,"E9.0.55.0")])]}),"instanceName":"19"});
            var Q96;
            Q96=makeQuery(id+"F19.opPattern","COPY",BODY,{"derivedFrom":makeQuery(id+"F3.opExtrude","SWEPT_BODY",BODY,{"disambiguationData":[OSD([sQuery(id+"F1.wireOp",EDGE,"E9.0.60.0")])]}),"instanceName":"2"});
            var Q97;
            Q97=makeQuery(id+"F19.opPattern","COPY",BODY,{"derivedFrom":makeQuery(id+"F3.opExtrude","SWEPT_BODY",BODY,{"disambiguationData":[OSD([sQuery(id+"F1.wireOp",EDGE,"E9.0.60.0")])]}),"instanceName":"3"});
            var Q98;
            Q98=makeQuery(id+"F22.opPattern","COPY",BODY,{"derivedFrom":makeQuery(id+"F3.opExtrude","SWEPT_BODY",BODY,{"disambiguationData":[OSD([sQuery(id+"F1.wireOp",EDGE,"E9.0.56.0")])]}),"instanceName":"18"});
            var Q99;
            Q99=makeQuery(id+"F19.opPattern","COPY",BODY,{"derivedFrom":makeQuery(id+"F3.opExtrude","SWEPT_BODY",BODY,{"disambiguationData":[OSD([sQuery(id+"F1.wireOp",EDGE,"E9.0.60.0")])]}),"instanceName":"7"});
            var Q100;
            Q100=makeQuery(id+"F22.opPattern","COPY",BODY,{"derivedFrom":makeQuery(id+"F3.opExtrude","SWEPT_BODY",BODY,{"disambiguationData":[OSD([sQuery(id+"F1.wireOp",EDGE,"E9.0.55.0")])]}),"instanceName":"18"});
            var Q101;
            Q101=makeQuery(id+"F22.opPattern","COPY",BODY,{"derivedFrom":makeQuery(id+"F3.opExtrude","SWEPT_BODY",BODY,{"disambiguationData":[OSD([sQuery(id+"F1.wireOp",EDGE,"E9.0.56.0")])]}),"instanceName":"17"});
            var Q102;
            Q102=makeQuery(id+"F22.opPattern","COPY",BODY,{"derivedFrom":makeQuery(id+"F3.opExtrude","SWEPT_BODY",BODY,{"disambiguationData":[OSD([sQuery(id+"F1.wireOp",EDGE,"E9.0.55.0")])]}),"instanceName":"17"});
            var Q103;
            Q103=makeQuery(id+"F22.opPattern","COPY",BODY,{"derivedFrom":makeQuery(id+"F3.opExtrude","SWEPT_BODY",BODY,{"disambiguationData":[OSD([sQuery(id+"F1.wireOp",EDGE,"E9.0.56.0")])]}),"instanceName":"16"});
            var Q104;
            Q104=makeQuery(id+"F19.opPattern","COPY",BODY,{"derivedFrom":makeQuery(id+"F3.opExtrude","SWEPT_BODY",BODY,{"disambiguationData":[OSD([sQuery(id+"F1.wireOp",EDGE,"E9.0.60.0")])]}),"instanceName":"5"});
            var Q105;
            Q105=makeQuery(id+"F19.opPattern","COPY",BODY,{"derivedFrom":makeQuery(id+"F3.opExtrude","SWEPT_BODY",BODY,{"disambiguationData":[OSD([sQuery(id+"F1.wireOp",EDGE,"E9.0.60.0")])]}),"instanceName":"6"});
            var Q106;
            Q106=makeQuery(id+"F20.opPattern","COPY",BODY,{"derivedFrom":makeQuery(id+"F3.opExtrude","SWEPT_BODY",BODY,{"disambiguationData":[OSD([sQuery(id+"F1.wireOp",EDGE,"E9.0.59.0")])]}),"instanceName":"5"});
            var Q107;
            Q107=makeQuery(id+"F20.opPattern","COPY",BODY,{"derivedFrom":makeQuery(id+"F3.opExtrude","SWEPT_BODY",BODY,{"disambiguationData":[OSD([sQuery(id+"F1.wireOp",EDGE,"E9.0.59.0")])]}),"instanceName":"12"});
            var Q108;
            Q108=makeQuery(id+"F20.opPattern","COPY",BODY,{"derivedFrom":makeQuery(id+"F3.opExtrude","SWEPT_BODY",BODY,{"disambiguationData":[OSD([sQuery(id+"F1.wireOp",EDGE,"E9.0.58.0")])]}),"instanceName":"13"});
            var Q109;
            Q109=makeQuery(id+"F20.opPattern","COPY",BODY,{"derivedFrom":makeQuery(id+"F3.opExtrude","SWEPT_BODY",BODY,{"disambiguationData":[OSD([sQuery(id+"F1.wireOp",EDGE,"E9.0.59.0")])]}),"instanceName":"13"});
            var Q110;
            Q110=makeQuery(id+"F20.opPattern","COPY",BODY,{"derivedFrom":makeQuery(id+"F3.opExtrude","SWEPT_BODY",BODY,{"disambiguationData":[OSD([sQuery(id+"F1.wireOp",EDGE,"E9.0.58.0")])]}),"instanceName":"15"});
            var Q111;
            Q111=makeQuery(id+"F20.opPattern","COPY",BODY,{"derivedFrom":makeQuery(id+"F3.opExtrude","SWEPT_BODY",BODY,{"disambiguationData":[OSD([sQuery(id+"F1.wireOp",EDGE,"E9.0.58.0")])]}),"instanceName":"3"});
            var Q112;
            Q112=makeQuery(id+"F2.opRevolve","SWEPT_BODY",BODY,{"disambiguationData":[OSD([sQuery(id+"F0.wireOp",EDGE,"E0"),sQuery(id+"F0.wireOp",EDGE,"E1"),sQuery(id+"F0.wireOp",EDGE,"E2"),sQuery(id+"F0.wireOp",EDGE,"E3"),sQuery(id+"F0.wireOp",EDGE,"E6")])]});
            booleanBodies(context, id + "F23", {"operationType" : BooleanOperationType.SUBTRACTION, "tools" : qUnion([Q0, Q1, Q2, Q3, Q4, Q5, Q6, Q7, Q8, Q9, Q10, Q11, Q12, Q13, Q14, Q15, Q16, Q17, Q18, Q19, Q20, Q21, Q22, Q23, Q24, Q25, Q26, Q27, Q28, Q29, Q30, Q31, Q32, Q33, Q34, Q35, Q36, Q37, Q38, Q39, Q40, Q41, Q42, Q43, Q44, Q45, Q46, Q47, Q48, Q49, Q50, Q51, Q52, Q53, Q54, Q55, Q56, Q57, Q58, Q59, Q60, Q61, Q62, Q63, Q64, Q65, Q66, Q67, Q68, Q69, Q70, Q71, Q72, Q73, Q74, Q75, Q76, Q77, Q78, Q79, Q80, Q81, Q82, Q83, Q84, Q85, Q86, Q87, Q88, Q89, Q90, Q91, Q92, Q93, Q94, Q95, Q96, Q97, Q98, Q99, Q100, Q101, Q102, Q103, Q104, Q105, Q106, Q107, Q108, Q109, Q110, Q111]), "targets" : qUnion([Q112])});
        }
        {
            var Q0;
            Q0=makeQuery(id+"F3.opExtrude","SWEPT_BODY",BODY,{"disambiguationData":[OSD([sQuery(id+"F1.wireOp",EDGE,"E9.0.54.0")])]});
            var Q1;
            Q1=makeQuery(id+"F2.opRevolve","SWEPT_FACE",FACE,{"disambiguationData":[OSD([sQuery(id+"F0.wireOp",EDGE,"E1")])]});
            circularPattern(context, id + "F24", {"entities" : qUnion([Q0]), "axis" : qUnion([Q1]), "angle" : 180 * degree, "instanceCount" : 21, "oppositeDirection" : true, "equalSpace" : true});
        }
        {
            var Q0;
            Q0=makeQuery(id+"F3.opExtrude","SWEPT_BODY",BODY,{"disambiguationData":[OSD([sQuery(id+"F1.wireOp",EDGE,"E9.0.53.0")])]});
            var Q1;
            Q1=makeQuery(id+"F3.opExtrude","SWEPT_BODY",BODY,{"disambiguationData":[OSD([sQuery(id+"F1.wireOp",EDGE,"E9.0.52.0")])]});
            var Q2;
            Q2=makeQuery(id+"F2.opRevolve","SWEPT_FACE",FACE,{"disambiguationData":[OSD([sQuery(id+"F0.wireOp",EDGE,"E1")])]});
            circularPattern(context, id + "F25", {"entities" : qUnion([Q0, Q1]), "axis" : qUnion([Q2]), "angle" : 180 * degree, "instanceCount" : 22, "oppositeDirection" : true, "equalSpace" : true});
        }
        {
            var Q0;
            Q0=makeQuery(id+"F3.opExtrude","SWEPT_BODY",BODY,{"disambiguationData":[OSD([sQuery(id+"F1.wireOp",EDGE,"E9.0.51.0")])]});
            var Q1;
            Q1=makeQuery(id+"F2.opRevolve","SWEPT_FACE",FACE,{"disambiguationData":[OSD([sQuery(id+"F0.wireOp",EDGE,"E1")])]});
            circularPattern(context, id + "F26", {"entities" : qUnion([Q0]), "axis" : qUnion([Q1]), "angle" : 180 * degree, "instanceCount" : 23, "oppositeDirection" : true, "equalSpace" : true});
        }
        {
            var Q0;
            Q0=makeQuery(id+"F3.opExtrude","SWEPT_BODY",BODY,{"disambiguationData":[OSD([sQuery(id+"F1.wireOp",EDGE,"E9.0.50.0")])]});
            var Q1;
            Q1=makeQuery(id+"F3.opExtrude","SWEPT_BODY",BODY,{"disambiguationData":[OSD([sQuery(id+"F1.wireOp",EDGE,"E9.0.49.0")])]});
            var Q2;
            Q2=makeQuery(id+"F2.opRevolve","SWEPT_FACE",FACE,{"disambiguationData":[OSD([sQuery(id+"F0.wireOp",EDGE,"E1")])]});
            circularPattern(context, id + "F27", {"entities" : qUnion([Q0, Q1]), "axis" : qUnion([Q2]), "angle" : 180 * degree, "instanceCount" : 24, "oppositeDirection" : true, "equalSpace" : true});
        }
        {
            var Q0;
            Q0=makeQuery(id+"F3.opExtrude","SWEPT_BODY",BODY,{"disambiguationData":[OSD([sQuery(id+"F1.wireOp",EDGE,"E9.0.48.0")])]});
            var Q1;
            Q1=makeQuery(id+"F2.opRevolve","SWEPT_FACE",FACE,{"disambiguationData":[OSD([sQuery(id+"F0.wireOp",EDGE,"E1")])]});
            circularPattern(context, id + "F28", {"entities" : qUnion([Q0]), "axis" : qUnion([Q1]), "angle" : 180 * degree, "instanceCount" : 25, "oppositeDirection" : true, "equalSpace" : true});
        }
        {
            var Q0;
            Q0=makeQuery(id+"F3.opExtrude","SWEPT_BODY",BODY,{"disambiguationData":[OSD([sQuery(id+"F1.wireOp",EDGE,"E9.0.47.0")])]});
            var Q1;
            Q1=makeQuery(id+"F3.opExtrude","SWEPT_BODY",BODY,{"disambiguationData":[OSD([sQuery(id+"F1.wireOp",EDGE,"E9.0.46.0")])]});
            var Q2;
            Q2=makeQuery(id+"F2.opRevolve","SWEPT_FACE",FACE,{"disambiguationData":[OSD([sQuery(id+"F0.wireOp",EDGE,"E1")])]});
            circularPattern(context, id + "F29", {"entities" : qUnion([Q0, Q1]), "axis" : qUnion([Q2]), "angle" : 180 * degree, "instanceCount" : 26, "oppositeDirection" : true, "equalSpace" : true});
        }
        {
            var Q0;
            Q0=makeQuery(id+"F24.opPattern","COPY",BODY,{"derivedFrom":makeQuery(id+"F3.opExtrude","SWEPT_BODY",BODY,{"disambiguationData":[OSD([sQuery(id+"F1.wireOp",EDGE,"E9.0.54.0")])]}),"instanceName":"19"});
            var Q1;
            Q1=makeQuery(id+"F27.opPattern","COPY",BODY,{"derivedFrom":makeQuery(id+"F3.opExtrude","SWEPT_BODY",BODY,{"disambiguationData":[OSD([sQuery(id+"F1.wireOp",EDGE,"E9.0.49.0")])]}),"instanceName":"18"});
            var Q2;
            Q2=makeQuery(id+"F25.opPattern","COPY",BODY,{"derivedFrom":makeQuery(id+"F3.opExtrude","SWEPT_BODY",BODY,{"disambiguationData":[OSD([sQuery(id+"F1.wireOp",EDGE,"E9.0.53.0")])]}),"instanceName":"7"});
            var Q3;
            Q3=makeQuery(id+"F27.opPattern","COPY",BODY,{"derivedFrom":makeQuery(id+"F3.opExtrude","SWEPT_BODY",BODY,{"disambiguationData":[OSD([sQuery(id+"F1.wireOp",EDGE,"E9.0.50.0")])]}),"instanceName":"18"});
            var Q4;
            Q4=makeQuery(id+"F25.opPattern","COPY",BODY,{"derivedFrom":makeQuery(id+"F3.opExtrude","SWEPT_BODY",BODY,{"disambiguationData":[OSD([sQuery(id+"F1.wireOp",EDGE,"E9.0.52.0")])]}),"instanceName":"7"});
            var Q5;
            Q5=makeQuery(id+"F25.opPattern","COPY",BODY,{"derivedFrom":makeQuery(id+"F3.opExtrude","SWEPT_BODY",BODY,{"disambiguationData":[OSD([sQuery(id+"F1.wireOp",EDGE,"E9.0.53.0")])]}),"instanceName":"6"});
            var Q6;
            Q6=makeQuery(id+"F27.opPattern","COPY",BODY,{"derivedFrom":makeQuery(id+"F3.opExtrude","SWEPT_BODY",BODY,{"disambiguationData":[OSD([sQuery(id+"F1.wireOp",EDGE,"E9.0.49.0")])]}),"instanceName":"19"});
            var Q7;
            Q7=makeQuery(id+"F25.opPattern","COPY",BODY,{"derivedFrom":makeQuery(id+"F3.opExtrude","SWEPT_BODY",BODY,{"disambiguationData":[OSD([sQuery(id+"F1.wireOp",EDGE,"E9.0.52.0")])]}),"instanceName":"6"});
            var Q8;
            Q8=makeQuery(id+"F25.opPattern","COPY",BODY,{"derivedFrom":makeQuery(id+"F3.opExtrude","SWEPT_BODY",BODY,{"disambiguationData":[OSD([sQuery(id+"F1.wireOp",EDGE,"E9.0.52.0")])]}),"instanceName":"8"});
            var Q9;
            Q9=makeQuery(id+"F27.opPattern","COPY",BODY,{"derivedFrom":makeQuery(id+"F3.opExtrude","SWEPT_BODY",BODY,{"disambiguationData":[OSD([sQuery(id+"F1.wireOp",EDGE,"E9.0.49.0")])]}),"instanceName":"3"});
            var Q10;
            Q10=makeQuery(id+"F29.opPattern","COPY",BODY,{"derivedFrom":makeQuery(id+"F3.opExtrude","SWEPT_BODY",BODY,{"disambiguationData":[OSD([sQuery(id+"F1.wireOp",EDGE,"E9.0.46.0")])]}),"instanceName":"19"});
            var Q11;
            Q11=makeQuery(id+"F29.opPattern","COPY",BODY,{"derivedFrom":makeQuery(id+"F3.opExtrude","SWEPT_BODY",BODY,{"disambiguationData":[OSD([sQuery(id+"F1.wireOp",EDGE,"E9.0.47.0")])]}),"instanceName":"22"});
            var Q12;
            Q12=makeQuery(id+"F24.opPattern","COPY",BODY,{"derivedFrom":makeQuery(id+"F3.opExtrude","SWEPT_BODY",BODY,{"disambiguationData":[OSD([sQuery(id+"F1.wireOp",EDGE,"E9.0.54.0")])]}),"instanceName":"17"});
            var Q13;
            Q13=makeQuery(id+"F25.opPattern","COPY",BODY,{"derivedFrom":makeQuery(id+"F3.opExtrude","SWEPT_BODY",BODY,{"disambiguationData":[OSD([sQuery(id+"F1.wireOp",EDGE,"E9.0.53.0")])]}),"instanceName":"8"});
            var Q14;
            Q14=makeQuery(id+"F29.opPattern","COPY",BODY,{"derivedFrom":makeQuery(id+"F3.opExtrude","SWEPT_BODY",BODY,{"disambiguationData":[OSD([sQuery(id+"F1.wireOp",EDGE,"E9.0.46.0")])]}),"instanceName":"23"});
            var Q15;
            Q15=makeQuery(id+"F24.opPattern","COPY",BODY,{"derivedFrom":makeQuery(id+"F3.opExtrude","SWEPT_BODY",BODY,{"disambiguationData":[OSD([sQuery(id+"F1.wireOp",EDGE,"E9.0.54.0")])]}),"instanceName":"16"});
            var Q16;
            Q16=makeQuery(id+"F24.opPattern","COPY",BODY,{"derivedFrom":makeQuery(id+"F3.opExtrude","SWEPT_BODY",BODY,{"disambiguationData":[OSD([sQuery(id+"F1.wireOp",EDGE,"E9.0.54.0")])]}),"instanceName":"18"});
            var Q17;
            Q17=makeQuery(id+"F25.opPattern","COPY",BODY,{"derivedFrom":makeQuery(id+"F3.opExtrude","SWEPT_BODY",BODY,{"disambiguationData":[OSD([sQuery(id+"F1.wireOp",EDGE,"E9.0.52.0")])]}),"instanceName":"9"});
            var Q18;
            Q18=makeQuery(id+"F25.opPattern","COPY",BODY,{"derivedFrom":makeQuery(id+"F3.opExtrude","SWEPT_BODY",BODY,{"disambiguationData":[OSD([sQuery(id+"F1.wireOp",EDGE,"E9.0.53.0")])]}),"instanceName":"9"});
            var Q19;
            Q19=makeQuery(id+"F24.opPattern","COPY",BODY,{"derivedFrom":makeQuery(id+"F3.opExtrude","SWEPT_BODY",BODY,{"disambiguationData":[OSD([sQuery(id+"F1.wireOp",EDGE,"E9.0.54.0")])]}),"instanceName":"15"});
            var Q20;
            Q20=makeQuery(id+"F24.opPattern","COPY",BODY,{"derivedFrom":makeQuery(id+"F3.opExtrude","SWEPT_BODY",BODY,{"disambiguationData":[OSD([sQuery(id+"F1.wireOp",EDGE,"E9.0.54.0")])]}),"instanceName":"14"});
            var Q21;
            Q21=makeQuery(id+"F25.opPattern","COPY",BODY,{"derivedFrom":makeQuery(id+"F3.opExtrude","SWEPT_BODY",BODY,{"disambiguationData":[OSD([sQuery(id+"F1.wireOp",EDGE,"E9.0.52.0")])]}),"instanceName":"10"});
            var Q22;
            Q22=makeQuery(id+"F26.opPattern","COPY",BODY,{"derivedFrom":makeQuery(id+"F3.opExtrude","SWEPT_BODY",BODY,{"disambiguationData":[OSD([sQuery(id+"F1.wireOp",EDGE,"E9.0.51.0")])]}),"instanceName":"21"});
            var Q23;
            Q23=makeQuery(id+"F29.opPattern","COPY",BODY,{"derivedFrom":makeQuery(id+"F3.opExtrude","SWEPT_BODY",BODY,{"disambiguationData":[OSD([sQuery(id+"F1.wireOp",EDGE,"E9.0.46.0")])]}),"instanceName":"4"});
            var Q24;
            Q24=makeQuery(id+"F29.opPattern","COPY",BODY,{"derivedFrom":makeQuery(id+"F3.opExtrude","SWEPT_BODY",BODY,{"disambiguationData":[OSD([sQuery(id+"F1.wireOp",EDGE,"E9.0.46.0")])]}),"instanceName":"8"});
            var Q25;
            Q25=makeQuery(id+"F24.opPattern","COPY",BODY,{"derivedFrom":makeQuery(id+"F3.opExtrude","SWEPT_BODY",BODY,{"disambiguationData":[OSD([sQuery(id+"F1.wireOp",EDGE,"E9.0.54.0")])]}),"instanceName":"13"});
            var Q26;
            Q26=makeQuery(id+"F25.opPattern","COPY",BODY,{"derivedFrom":makeQuery(id+"F3.opExtrude","SWEPT_BODY",BODY,{"disambiguationData":[OSD([sQuery(id+"F1.wireOp",EDGE,"E9.0.53.0")])]}),"instanceName":"10"});
            var Q27;
            Q27=makeQuery(id+"F25.opPattern","COPY",BODY,{"derivedFrom":makeQuery(id+"F3.opExtrude","SWEPT_BODY",BODY,{"disambiguationData":[OSD([sQuery(id+"F1.wireOp",EDGE,"E9.0.53.0")])]}),"instanceName":"4"});
            var Q28;
            Q28=makeQuery(id+"F29.opPattern","COPY",BODY,{"derivedFrom":makeQuery(id+"F3.opExtrude","SWEPT_BODY",BODY,{"disambiguationData":[OSD([sQuery(id+"F1.wireOp",EDGE,"E9.0.46.0")])]}),"instanceName":"9"});
            var Q29;
            Q29=makeQuery(id+"F29.opPattern","COPY",BODY,{"derivedFrom":makeQuery(id+"F3.opExtrude","SWEPT_BODY",BODY,{"disambiguationData":[OSD([sQuery(id+"F1.wireOp",EDGE,"E9.0.47.0")])]}),"instanceName":"8"});
            var Q30;
            Q30=makeQuery(id+"F26.opPattern","COPY",BODY,{"derivedFrom":makeQuery(id+"F3.opExtrude","SWEPT_BODY",BODY,{"disambiguationData":[OSD([sQuery(id+"F1.wireOp",EDGE,"E9.0.51.0")])]}),"instanceName":"20"});
            var Q31;
            Q31=makeQuery(id+"F24.opPattern","COPY",BODY,{"derivedFrom":makeQuery(id+"F3.opExtrude","SWEPT_BODY",BODY,{"disambiguationData":[OSD([sQuery(id+"F1.wireOp",EDGE,"E9.0.54.0")])]}),"instanceName":"12"});
            var Q32;
            Q32=makeQuery(id+"F29.opPattern","COPY",BODY,{"derivedFrom":makeQuery(id+"F3.opExtrude","SWEPT_BODY",BODY,{"disambiguationData":[OSD([sQuery(id+"F1.wireOp",EDGE,"E9.0.46.0")])]}),"instanceName":"24"});
            var Q33;
            Q33=makeQuery(id+"F27.opPattern","COPY",BODY,{"derivedFrom":makeQuery(id+"F3.opExtrude","SWEPT_BODY",BODY,{"disambiguationData":[OSD([sQuery(id+"F1.wireOp",EDGE,"E9.0.50.0")])]}),"instanceName":"17"});
            var Q34;
            Q34=makeQuery(id+"F27.opPattern","COPY",BODY,{"derivedFrom":makeQuery(id+"F3.opExtrude","SWEPT_BODY",BODY,{"disambiguationData":[OSD([sQuery(id+"F1.wireOp",EDGE,"E9.0.49.0")])]}),"instanceName":"17"});
            var Q35;
            Q35=makeQuery(id+"F29.opPattern","COPY",BODY,{"derivedFrom":makeQuery(id+"F3.opExtrude","SWEPT_BODY",BODY,{"disambiguationData":[OSD([sQuery(id+"F1.wireOp",EDGE,"E9.0.47.0")])]}),"instanceName":"24"});
            var Q36;
            Q36=makeQuery(id+"F27.opPattern","COPY",BODY,{"derivedFrom":makeQuery(id+"F3.opExtrude","SWEPT_BODY",BODY,{"disambiguationData":[OSD([sQuery(id+"F1.wireOp",EDGE,"E9.0.50.0")])]}),"instanceName":"16"});
            var Q37;
            Q37=makeQuery(id+"F25.opPattern","COPY",BODY,{"derivedFrom":makeQuery(id+"F3.opExtrude","SWEPT_BODY",BODY,{"disambiguationData":[OSD([sQuery(id+"F1.wireOp",EDGE,"E9.0.52.0")])]}),"instanceName":"11"});
            var Q38;
            Q38=makeQuery(id+"F25.opPattern","COPY",BODY,{"derivedFrom":makeQuery(id+"F3.opExtrude","SWEPT_BODY",BODY,{"disambiguationData":[OSD([sQuery(id+"F1.wireOp",EDGE,"E9.0.53.0")])]}),"instanceName":"11"});
            var Q39;
            Q39=makeQuery(id+"F24.opPattern","COPY",BODY,{"derivedFrom":makeQuery(id+"F3.opExtrude","SWEPT_BODY",BODY,{"disambiguationData":[OSD([sQuery(id+"F1.wireOp",EDGE,"E9.0.54.0")])]}),"instanceName":"11"});
            var Q40;
            Q40=makeQuery(id+"F24.opPattern","COPY",BODY,{"derivedFrom":makeQuery(id+"F3.opExtrude","SWEPT_BODY",BODY,{"disambiguationData":[OSD([sQuery(id+"F1.wireOp",EDGE,"E9.0.54.0")])]}),"instanceName":"10"});
            var Q41;
            Q41=makeQuery(id+"F25.opPattern","COPY",BODY,{"derivedFrom":makeQuery(id+"F3.opExtrude","SWEPT_BODY",BODY,{"disambiguationData":[OSD([sQuery(id+"F1.wireOp",EDGE,"E9.0.52.0")])]}),"instanceName":"12"});
            var Q42;
            Q42=makeQuery(id+"F29.opPattern","COPY",BODY,{"derivedFrom":makeQuery(id+"F3.opExtrude","SWEPT_BODY",BODY,{"disambiguationData":[OSD([sQuery(id+"F1.wireOp",EDGE,"E9.0.47.0")])]}),"instanceName":"23"});
            var Q43;
            Q43=makeQuery(id+"F25.opPattern","COPY",BODY,{"derivedFrom":makeQuery(id+"F3.opExtrude","SWEPT_BODY",BODY,{"disambiguationData":[OSD([sQuery(id+"F1.wireOp",EDGE,"E9.0.53.0")])]}),"instanceName":"12"});
            var Q44;
            Q44=makeQuery(id+"F25.opPattern","COPY",BODY,{"derivedFrom":makeQuery(id+"F3.opExtrude","SWEPT_BODY",BODY,{"disambiguationData":[OSD([sQuery(id+"F1.wireOp",EDGE,"E9.0.52.0")])]}),"instanceName":"13"});
            var Q45;
            Q45=makeQuery(id+"F29.opPattern","COPY",BODY,{"derivedFrom":makeQuery(id+"F3.opExtrude","SWEPT_BODY",BODY,{"disambiguationData":[OSD([sQuery(id+"F1.wireOp",EDGE,"E9.0.47.0")])]}),"instanceName":"1"});
            var Q46;
            Q46=makeQuery(id+"F24.opPattern","COPY",BODY,{"derivedFrom":makeQuery(id+"F3.opExtrude","SWEPT_BODY",BODY,{"disambiguationData":[OSD([sQuery(id+"F1.wireOp",EDGE,"E9.0.54.0")])]}),"instanceName":"9"});
            var Q47;
            Q47=makeQuery(id+"F24.opPattern","COPY",BODY,{"derivedFrom":makeQuery(id+"F3.opExtrude","SWEPT_BODY",BODY,{"disambiguationData":[OSD([sQuery(id+"F1.wireOp",EDGE,"E9.0.54.0")])]}),"instanceName":"8"});
            var Q48;
            Q48=makeQuery(id+"F27.opPattern","COPY",BODY,{"derivedFrom":makeQuery(id+"F3.opExtrude","SWEPT_BODY",BODY,{"disambiguationData":[OSD([sQuery(id+"F1.wireOp",EDGE,"E9.0.49.0")])]}),"instanceName":"16"});
            var Q49;
            Q49=makeQuery(id+"F25.opPattern","COPY",BODY,{"derivedFrom":makeQuery(id+"F3.opExtrude","SWEPT_BODY",BODY,{"disambiguationData":[OSD([sQuery(id+"F1.wireOp",EDGE,"E9.0.53.0")])]}),"instanceName":"13"});
            var Q50;
            Q50=makeQuery(id+"F25.opPattern","COPY",BODY,{"derivedFrom":makeQuery(id+"F3.opExtrude","SWEPT_BODY",BODY,{"disambiguationData":[OSD([sQuery(id+"F1.wireOp",EDGE,"E9.0.52.0")])]}),"instanceName":"14"});
            var Q51;
            Q51=makeQuery(id+"F25.opPattern","COPY",BODY,{"derivedFrom":makeQuery(id+"F3.opExtrude","SWEPT_BODY",BODY,{"disambiguationData":[OSD([sQuery(id+"F1.wireOp",EDGE,"E9.0.53.0")])]}),"instanceName":"14"});
            var Q52;
            Q52=makeQuery(id+"F27.opPattern","COPY",BODY,{"derivedFrom":makeQuery(id+"F3.opExtrude","SWEPT_BODY",BODY,{"disambiguationData":[OSD([sQuery(id+"F1.wireOp",EDGE,"E9.0.50.0")])]}),"instanceName":"6"});
            var Q53;
            Q53=makeQuery(id+"F26.opPattern","COPY",BODY,{"derivedFrom":makeQuery(id+"F3.opExtrude","SWEPT_BODY",BODY,{"disambiguationData":[OSD([sQuery(id+"F1.wireOp",EDGE,"E9.0.51.0")])]}),"instanceName":"19"});
            var Q54;
            Q54=makeQuery(id+"F25.opPattern","COPY",BODY,{"derivedFrom":makeQuery(id+"F3.opExtrude","SWEPT_BODY",BODY,{"disambiguationData":[OSD([sQuery(id+"F1.wireOp",EDGE,"E9.0.52.0")])]}),"instanceName":"15"});
            var Q55;
            Q55=makeQuery(id+"F25.opPattern","COPY",BODY,{"derivedFrom":makeQuery(id+"F3.opExtrude","SWEPT_BODY",BODY,{"disambiguationData":[OSD([sQuery(id+"F1.wireOp",EDGE,"E9.0.53.0")])]}),"instanceName":"15"});
            var Q56;
            Q56=makeQuery(id+"F27.opPattern","COPY",BODY,{"derivedFrom":makeQuery(id+"F3.opExtrude","SWEPT_BODY",BODY,{"disambiguationData":[OSD([sQuery(id+"F1.wireOp",EDGE,"E9.0.49.0")])]}),"instanceName":"8"});
            var Q57;
            Q57=makeQuery(id+"F25.opPattern","COPY",BODY,{"derivedFrom":makeQuery(id+"F3.opExtrude","SWEPT_BODY",BODY,{"disambiguationData":[OSD([sQuery(id+"F1.wireOp",EDGE,"E9.0.52.0")])]}),"instanceName":"16"});
            var Q58;
            Q58=makeQuery(id+"F24.opPattern","COPY",BODY,{"derivedFrom":makeQuery(id+"F3.opExtrude","SWEPT_BODY",BODY,{"disambiguationData":[OSD([sQuery(id+"F1.wireOp",EDGE,"E9.0.54.0")])]}),"instanceName":"7"});
            var Q59;
            Q59=makeQuery(id+"F29.opPattern","COPY",BODY,{"derivedFrom":makeQuery(id+"F3.opExtrude","SWEPT_BODY",BODY,{"disambiguationData":[OSD([sQuery(id+"F1.wireOp",EDGE,"E9.0.47.0")])]}),"instanceName":"14"});
            var Q60;
            Q60=makeQuery(id+"F28.opPattern","COPY",BODY,{"derivedFrom":makeQuery(id+"F3.opExtrude","SWEPT_BODY",BODY,{"disambiguationData":[OSD([sQuery(id+"F1.wireOp",EDGE,"E9.0.48.0")])]}),"instanceName":"2"});
            var Q61;
            Q61=makeQuery(id+"F29.opPattern","COPY",BODY,{"derivedFrom":makeQuery(id+"F3.opExtrude","SWEPT_BODY",BODY,{"disambiguationData":[OSD([sQuery(id+"F1.wireOp",EDGE,"E9.0.46.0")])]}),"instanceName":"15"});
            var Q62;
            Q62=makeQuery(id+"F29.opPattern","COPY",BODY,{"derivedFrom":makeQuery(id+"F3.opExtrude","SWEPT_BODY",BODY,{"disambiguationData":[OSD([sQuery(id+"F1.wireOp",EDGE,"E9.0.47.0")])]}),"instanceName":"2"});
            var Q63;
            Q63=makeQuery(id+"F24.opPattern","COPY",BODY,{"derivedFrom":makeQuery(id+"F3.opExtrude","SWEPT_BODY",BODY,{"disambiguationData":[OSD([sQuery(id+"F1.wireOp",EDGE,"E9.0.54.0")])]}),"instanceName":"6"});
            var Q64;
            Q64=makeQuery(id+"F25.opPattern","COPY",BODY,{"derivedFrom":makeQuery(id+"F3.opExtrude","SWEPT_BODY",BODY,{"disambiguationData":[OSD([sQuery(id+"F1.wireOp",EDGE,"E9.0.53.0")])]}),"instanceName":"16"});
            var Q65;
            Q65=makeQuery(id+"F24.opPattern","COPY",BODY,{"derivedFrom":makeQuery(id+"F3.opExtrude","SWEPT_BODY",BODY,{"disambiguationData":[OSD([sQuery(id+"F1.wireOp",EDGE,"E9.0.54.0")])]}),"instanceName":"5"});
            var Q66;
            Q66=makeQuery(id+"F27.opPattern","COPY",BODY,{"derivedFrom":makeQuery(id+"F3.opExtrude","SWEPT_BODY",BODY,{"disambiguationData":[OSD([sQuery(id+"F1.wireOp",EDGE,"E9.0.50.0")])]}),"instanceName":"15"});
            var Q67;
            Q67=makeQuery(id+"F25.opPattern","COPY",BODY,{"derivedFrom":makeQuery(id+"F3.opExtrude","SWEPT_BODY",BODY,{"disambiguationData":[OSD([sQuery(id+"F1.wireOp",EDGE,"E9.0.52.0")])]}),"instanceName":"17"});
            var Q68;
            Q68=makeQuery(id+"F25.opPattern","COPY",BODY,{"derivedFrom":makeQuery(id+"F3.opExtrude","SWEPT_BODY",BODY,{"disambiguationData":[OSD([sQuery(id+"F1.wireOp",EDGE,"E9.0.53.0")])]}),"instanceName":"17"});
            var Q69;
            Q69=makeQuery(id+"F27.opPattern","COPY",BODY,{"derivedFrom":makeQuery(id+"F3.opExtrude","SWEPT_BODY",BODY,{"disambiguationData":[OSD([sQuery(id+"F1.wireOp",EDGE,"E9.0.50.0")])]}),"instanceName":"7"});
            var Q70;
            Q70=makeQuery(id+"F27.opPattern","COPY",BODY,{"derivedFrom":makeQuery(id+"F3.opExtrude","SWEPT_BODY",BODY,{"disambiguationData":[OSD([sQuery(id+"F1.wireOp",EDGE,"E9.0.50.0")])]}),"instanceName":"4"});
            var Q71;
            Q71=makeQuery(id+"F29.opPattern","COPY",BODY,{"derivedFrom":makeQuery(id+"F3.opExtrude","SWEPT_BODY",BODY,{"disambiguationData":[OSD([sQuery(id+"F1.wireOp",EDGE,"E9.0.46.0")])]}),"instanceName":"2"});
            var Q72;
            Q72=makeQuery(id+"F27.opPattern","COPY",BODY,{"derivedFrom":makeQuery(id+"F3.opExtrude","SWEPT_BODY",BODY,{"disambiguationData":[OSD([sQuery(id+"F1.wireOp",EDGE,"E9.0.50.0")])]}),"instanceName":"5"});
            var Q73;
            Q73=makeQuery(id+"F29.opPattern","COPY",BODY,{"derivedFrom":makeQuery(id+"F3.opExtrude","SWEPT_BODY",BODY,{"disambiguationData":[OSD([sQuery(id+"F1.wireOp",EDGE,"E9.0.47.0")])]}),"instanceName":"15"});
            var Q74;
            Q74=makeQuery(id+"F29.opPattern","COPY",BODY,{"derivedFrom":makeQuery(id+"F3.opExtrude","SWEPT_BODY",BODY,{"disambiguationData":[OSD([sQuery(id+"F1.wireOp",EDGE,"E9.0.46.0")])]}),"instanceName":"16"});
            var Q75;
            Q75=makeQuery(id+"F24.opPattern","COPY",BODY,{"derivedFrom":makeQuery(id+"F3.opExtrude","SWEPT_BODY",BODY,{"disambiguationData":[OSD([sQuery(id+"F1.wireOp",EDGE,"E9.0.54.0")])]}),"instanceName":"4"});
            var Q76;
            Q76=makeQuery(id+"F24.opPattern","COPY",BODY,{"derivedFrom":makeQuery(id+"F3.opExtrude","SWEPT_BODY",BODY,{"disambiguationData":[OSD([sQuery(id+"F1.wireOp",EDGE,"E9.0.54.0")])]}),"instanceName":"3"});
            var Q77;
            Q77=makeQuery(id+"F25.opPattern","COPY",BODY,{"derivedFrom":makeQuery(id+"F3.opExtrude","SWEPT_BODY",BODY,{"disambiguationData":[OSD([sQuery(id+"F1.wireOp",EDGE,"E9.0.52.0")])]}),"instanceName":"18"});
            var Q78;
            Q78=makeQuery(id+"F27.opPattern","COPY",BODY,{"derivedFrom":makeQuery(id+"F3.opExtrude","SWEPT_BODY",BODY,{"disambiguationData":[OSD([sQuery(id+"F1.wireOp",EDGE,"E9.0.49.0")])]}),"instanceName":"9"});
            var Q79;
            Q79=makeQuery(id+"F25.opPattern","COPY",BODY,{"derivedFrom":makeQuery(id+"F3.opExtrude","SWEPT_BODY",BODY,{"disambiguationData":[OSD([sQuery(id+"F1.wireOp",EDGE,"E9.0.53.0")])]}),"instanceName":"18"});
            var Q80;
            Q80=makeQuery(id+"F27.opPattern","COPY",BODY,{"derivedFrom":makeQuery(id+"F3.opExtrude","SWEPT_BODY",BODY,{"disambiguationData":[OSD([sQuery(id+"F1.wireOp",EDGE,"E9.0.49.0")])]}),"instanceName":"15"});
            var Q81;
            Q81=makeQuery(id+"F29.opPattern","COPY",BODY,{"derivedFrom":makeQuery(id+"F3.opExtrude","SWEPT_BODY",BODY,{"disambiguationData":[OSD([sQuery(id+"F1.wireOp",EDGE,"E9.0.47.0")])]}),"instanceName":"16"});
            var Q82;
            Q82=makeQuery(id+"F25.opPattern","COPY",BODY,{"derivedFrom":makeQuery(id+"F3.opExtrude","SWEPT_BODY",BODY,{"disambiguationData":[OSD([sQuery(id+"F1.wireOp",EDGE,"E9.0.52.0")])]}),"instanceName":"19"});
            var Q83;
            Q83=makeQuery(id+"F28.opPattern","COPY",BODY,{"derivedFrom":makeQuery(id+"F3.opExtrude","SWEPT_BODY",BODY,{"disambiguationData":[OSD([sQuery(id+"F1.wireOp",EDGE,"E9.0.48.0")])]}),"instanceName":"1"});
            var Q84;
            Q84=makeQuery(id+"F29.opPattern","COPY",BODY,{"derivedFrom":makeQuery(id+"F3.opExtrude","SWEPT_BODY",BODY,{"disambiguationData":[OSD([sQuery(id+"F1.wireOp",EDGE,"E9.0.47.0")])]}),"instanceName":"3"});
            var Q85;
            Q85=makeQuery(id+"F24.opPattern","COPY",BODY,{"derivedFrom":makeQuery(id+"F3.opExtrude","SWEPT_BODY",BODY,{"disambiguationData":[OSD([sQuery(id+"F1.wireOp",EDGE,"E9.0.54.0")])]}),"instanceName":"2"});
            var Q86;
            Q86=makeQuery(id+"F27.opPattern","COPY",BODY,{"derivedFrom":makeQuery(id+"F3.opExtrude","SWEPT_BODY",BODY,{"disambiguationData":[OSD([sQuery(id+"F1.wireOp",EDGE,"E9.0.50.0")])]}),"instanceName":"14"});
            var Q87;
            Q87=makeQuery(id+"F24.opPattern","COPY",BODY,{"derivedFrom":makeQuery(id+"F3.opExtrude","SWEPT_BODY",BODY,{"disambiguationData":[OSD([sQuery(id+"F1.wireOp",EDGE,"E9.0.54.0")])]}),"instanceName":"1"});
            var Q88;
            Q88=makeQuery(id+"F27.opPattern","COPY",BODY,{"derivedFrom":makeQuery(id+"F3.opExtrude","SWEPT_BODY",BODY,{"disambiguationData":[OSD([sQuery(id+"F1.wireOp",EDGE,"E9.0.50.0")])]}),"instanceName":"10"});
            var Q89;
            Q89=makeQuery(id+"F25.opPattern","COPY",BODY,{"derivedFrom":makeQuery(id+"F3.opExtrude","SWEPT_BODY",BODY,{"disambiguationData":[OSD([sQuery(id+"F1.wireOp",EDGE,"E9.0.53.0")])]}),"instanceName":"19"});
            var Q90;
            Q90=makeQuery(id+"F25.opPattern","COPY",BODY,{"derivedFrom":makeQuery(id+"F3.opExtrude","SWEPT_BODY",BODY,{"disambiguationData":[OSD([sQuery(id+"F1.wireOp",EDGE,"E9.0.52.0")])]}),"instanceName":"20"});
            var Q91;
            Q91=makeQuery(id+"F25.opPattern","COPY",BODY,{"derivedFrom":makeQuery(id+"F3.opExtrude","SWEPT_BODY",BODY,{"disambiguationData":[OSD([sQuery(id+"F1.wireOp",EDGE,"E9.0.53.0")])]}),"instanceName":"20"});
            var Q92;
            Q92=makeQuery(id+"F27.opPattern","COPY",BODY,{"derivedFrom":makeQuery(id+"F3.opExtrude","SWEPT_BODY",BODY,{"disambiguationData":[OSD([sQuery(id+"F1.wireOp",EDGE,"E9.0.49.0")])]}),"instanceName":"14"});
            var Q93;
            Q93=makeQuery(id+"F28.opPattern","COPY",BODY,{"derivedFrom":makeQuery(id+"F3.opExtrude","SWEPT_BODY",BODY,{"disambiguationData":[OSD([sQuery(id+"F1.wireOp",EDGE,"E9.0.48.0")])]}),"instanceName":"8"});
            var Q94;
            Q94=makeQuery(id+"F28.opPattern","COPY",BODY,{"derivedFrom":makeQuery(id+"F3.opExtrude","SWEPT_BODY",BODY,{"disambiguationData":[OSD([sQuery(id+"F1.wireOp",EDGE,"E9.0.48.0")])]}),"instanceName":"3"});
            var Q95;
            Q95=makeQuery(id+"F29.opPattern","COPY",BODY,{"derivedFrom":makeQuery(id+"F3.opExtrude","SWEPT_BODY",BODY,{"disambiguationData":[OSD([sQuery(id+"F1.wireOp",EDGE,"E9.0.46.0")])]}),"instanceName":"17"});
            var Q96;
            Q96=makeQuery(id+"F28.opPattern","COPY",BODY,{"derivedFrom":makeQuery(id+"F3.opExtrude","SWEPT_BODY",BODY,{"disambiguationData":[OSD([sQuery(id+"F1.wireOp",EDGE,"E9.0.48.0")])]}),"instanceName":"5"});
            var Q97;
            Q97=makeQuery(id+"F29.opPattern","COPY",BODY,{"derivedFrom":makeQuery(id+"F3.opExtrude","SWEPT_BODY",BODY,{"disambiguationData":[OSD([sQuery(id+"F1.wireOp",EDGE,"E9.0.47.0")])]}),"instanceName":"6"});
            var Q98;
            Q98=makeQuery(id+"F28.opPattern","COPY",BODY,{"derivedFrom":makeQuery(id+"F3.opExtrude","SWEPT_BODY",BODY,{"disambiguationData":[OSD([sQuery(id+"F1.wireOp",EDGE,"E9.0.48.0")])]}),"instanceName":"7"});
            var Q99;
            Q99=makeQuery(id+"F27.opPattern","COPY",BODY,{"derivedFrom":makeQuery(id+"F3.opExtrude","SWEPT_BODY",BODY,{"disambiguationData":[OSD([sQuery(id+"F1.wireOp",EDGE,"E9.0.50.0")])]}),"instanceName":"13"});
            var Q100;
            Q100=makeQuery(id+"F29.opPattern","COPY",BODY,{"derivedFrom":makeQuery(id+"F3.opExtrude","SWEPT_BODY",BODY,{"disambiguationData":[OSD([sQuery(id+"F1.wireOp",EDGE,"E9.0.46.0")])]}),"instanceName":"7"});
            var Q101;
            Q101=makeQuery(id+"F28.opPattern","COPY",BODY,{"derivedFrom":makeQuery(id+"F3.opExtrude","SWEPT_BODY",BODY,{"disambiguationData":[OSD([sQuery(id+"F1.wireOp",EDGE,"E9.0.48.0")])]}),"instanceName":"9"});
            var Q102;
            Q102=makeQuery(id+"F27.opPattern","COPY",BODY,{"derivedFrom":makeQuery(id+"F3.opExtrude","SWEPT_BODY",BODY,{"disambiguationData":[OSD([sQuery(id+"F1.wireOp",EDGE,"E9.0.49.0")])]}),"instanceName":"4"});
            var Q103;
            Q103=makeQuery(id+"F28.opPattern","COPY",BODY,{"derivedFrom":makeQuery(id+"F3.opExtrude","SWEPT_BODY",BODY,{"disambiguationData":[OSD([sQuery(id+"F1.wireOp",EDGE,"E9.0.48.0")])]}),"instanceName":"10"});
            var Q104;
            Q104=makeQuery(id+"F29.opPattern","COPY",BODY,{"derivedFrom":makeQuery(id+"F3.opExtrude","SWEPT_BODY",BODY,{"disambiguationData":[OSD([sQuery(id+"F1.wireOp",EDGE,"E9.0.47.0")])]}),"instanceName":"7"});
            var Q105;
            Q105=makeQuery(id+"F27.opPattern","COPY",BODY,{"derivedFrom":makeQuery(id+"F3.opExtrude","SWEPT_BODY",BODY,{"disambiguationData":[OSD([sQuery(id+"F1.wireOp",EDGE,"E9.0.49.0")])]}),"instanceName":"13"});
            var Q106;
            Q106=makeQuery(id+"F29.opPattern","COPY",BODY,{"derivedFrom":makeQuery(id+"F3.opExtrude","SWEPT_BODY",BODY,{"disambiguationData":[OSD([sQuery(id+"F1.wireOp",EDGE,"E9.0.46.0")])]}),"instanceName":"22"});
            var Q107;
            Q107=makeQuery(id+"F27.opPattern","COPY",BODY,{"derivedFrom":makeQuery(id+"F3.opExtrude","SWEPT_BODY",BODY,{"disambiguationData":[OSD([sQuery(id+"F1.wireOp",EDGE,"E9.0.50.0")])]}),"instanceName":"12"});
            var Q108;
            Q108=makeQuery(id+"F28.opPattern","COPY",BODY,{"derivedFrom":makeQuery(id+"F3.opExtrude","SWEPT_BODY",BODY,{"disambiguationData":[OSD([sQuery(id+"F1.wireOp",EDGE,"E9.0.48.0")])]}),"instanceName":"11"});
            var Q109;
            Q109=makeQuery(id+"F28.opPattern","COPY",BODY,{"derivedFrom":makeQuery(id+"F3.opExtrude","SWEPT_BODY",BODY,{"disambiguationData":[OSD([sQuery(id+"F1.wireOp",EDGE,"E9.0.48.0")])]}),"instanceName":"12"});
            var Q110;
            Q110=makeQuery(id+"F28.opPattern","COPY",BODY,{"derivedFrom":makeQuery(id+"F3.opExtrude","SWEPT_BODY",BODY,{"disambiguationData":[OSD([sQuery(id+"F1.wireOp",EDGE,"E9.0.48.0")])]}),"instanceName":"13"});
            var Q111;
            Q111=makeQuery(id+"F27.opPattern","COPY",BODY,{"derivedFrom":makeQuery(id+"F3.opExtrude","SWEPT_BODY",BODY,{"disambiguationData":[OSD([sQuery(id+"F1.wireOp",EDGE,"E9.0.50.0")])]}),"instanceName":"1"});
            var Q112;
            Q112=makeQuery(id+"F27.opPattern","COPY",BODY,{"derivedFrom":makeQuery(id+"F3.opExtrude","SWEPT_BODY",BODY,{"disambiguationData":[OSD([sQuery(id+"F1.wireOp",EDGE,"E9.0.50.0")])]}),"instanceName":"8"});
            var Q113;
            Q113=makeQuery(id+"F28.opPattern","COPY",BODY,{"derivedFrom":makeQuery(id+"F3.opExtrude","SWEPT_BODY",BODY,{"disambiguationData":[OSD([sQuery(id+"F1.wireOp",EDGE,"E9.0.48.0")])]}),"instanceName":"14"});
            var Q114;
            Q114=makeQuery(id+"F28.opPattern","COPY",BODY,{"derivedFrom":makeQuery(id+"F3.opExtrude","SWEPT_BODY",BODY,{"disambiguationData":[OSD([sQuery(id+"F1.wireOp",EDGE,"E9.0.48.0")])]}),"instanceName":"15"});
            var Q115;
            Q115=makeQuery(id+"F27.opPattern","COPY",BODY,{"derivedFrom":makeQuery(id+"F3.opExtrude","SWEPT_BODY",BODY,{"disambiguationData":[OSD([sQuery(id+"F1.wireOp",EDGE,"E9.0.49.0")])]}),"instanceName":"12"});
            var Q116;
            Q116=makeQuery(id+"F28.opPattern","COPY",BODY,{"derivedFrom":makeQuery(id+"F3.opExtrude","SWEPT_BODY",BODY,{"disambiguationData":[OSD([sQuery(id+"F1.wireOp",EDGE,"E9.0.48.0")])]}),"instanceName":"16"});
            var Q117;
            Q117=makeQuery(id+"F28.opPattern","COPY",BODY,{"derivedFrom":makeQuery(id+"F3.opExtrude","SWEPT_BODY",BODY,{"disambiguationData":[OSD([sQuery(id+"F1.wireOp",EDGE,"E9.0.48.0")])]}),"instanceName":"17"});
            var Q118;
            Q118=makeQuery(id+"F28.opPattern","COPY",BODY,{"derivedFrom":makeQuery(id+"F3.opExtrude","SWEPT_BODY",BODY,{"disambiguationData":[OSD([sQuery(id+"F1.wireOp",EDGE,"E9.0.48.0")])]}),"instanceName":"18"});
            var Q119;
            Q119=makeQuery(id+"F27.opPattern","COPY",BODY,{"derivedFrom":makeQuery(id+"F3.opExtrude","SWEPT_BODY",BODY,{"disambiguationData":[OSD([sQuery(id+"F1.wireOp",EDGE,"E9.0.50.0")])]}),"instanceName":"11"});
            var Q120;
            Q120=makeQuery(id+"F27.opPattern","COPY",BODY,{"derivedFrom":makeQuery(id+"F3.opExtrude","SWEPT_BODY",BODY,{"disambiguationData":[OSD([sQuery(id+"F1.wireOp",EDGE,"E9.0.49.0")])]}),"instanceName":"2"});
            var Q121;
            Q121=makeQuery(id+"F28.opPattern","COPY",BODY,{"derivedFrom":makeQuery(id+"F3.opExtrude","SWEPT_BODY",BODY,{"disambiguationData":[OSD([sQuery(id+"F1.wireOp",EDGE,"E9.0.48.0")])]}),"instanceName":"19"});
            var Q122;
            Q122=makeQuery(id+"F27.opPattern","COPY",BODY,{"derivedFrom":makeQuery(id+"F3.opExtrude","SWEPT_BODY",BODY,{"disambiguationData":[OSD([sQuery(id+"F1.wireOp",EDGE,"E9.0.49.0")])]}),"instanceName":"1"});
            var Q123;
            Q123=makeQuery(id+"F28.opPattern","COPY",BODY,{"derivedFrom":makeQuery(id+"F3.opExtrude","SWEPT_BODY",BODY,{"disambiguationData":[OSD([sQuery(id+"F1.wireOp",EDGE,"E9.0.48.0")])]}),"instanceName":"20"});
            var Q124;
            Q124=makeQuery(id+"F29.opPattern","COPY",BODY,{"derivedFrom":makeQuery(id+"F3.opExtrude","SWEPT_BODY",BODY,{"disambiguationData":[OSD([sQuery(id+"F1.wireOp",EDGE,"E9.0.46.0")])]}),"instanceName":"3"});
            var Q125;
            Q125=makeQuery(id+"F27.opPattern","COPY",BODY,{"derivedFrom":makeQuery(id+"F3.opExtrude","SWEPT_BODY",BODY,{"disambiguationData":[OSD([sQuery(id+"F1.wireOp",EDGE,"E9.0.49.0")])]}),"instanceName":"11"});
            var Q126;
            Q126=makeQuery(id+"F28.opPattern","COPY",BODY,{"derivedFrom":makeQuery(id+"F3.opExtrude","SWEPT_BODY",BODY,{"disambiguationData":[OSD([sQuery(id+"F1.wireOp",EDGE,"E9.0.48.0")])]}),"instanceName":"21"});
            var Q127;
            Q127=makeQuery(id+"F25.opPattern","COPY",BODY,{"derivedFrom":makeQuery(id+"F3.opExtrude","SWEPT_BODY",BODY,{"disambiguationData":[OSD([sQuery(id+"F1.wireOp",EDGE,"E9.0.53.0")])]}),"instanceName":"5"});
            var Q128;
            Q128=makeQuery(id+"F25.opPattern","COPY",BODY,{"derivedFrom":makeQuery(id+"F3.opExtrude","SWEPT_BODY",BODY,{"disambiguationData":[OSD([sQuery(id+"F1.wireOp",EDGE,"E9.0.52.0")])]}),"instanceName":"5"});
            var Q129;
            Q129=makeQuery(id+"F27.opPattern","COPY",BODY,{"derivedFrom":makeQuery(id+"F3.opExtrude","SWEPT_BODY",BODY,{"disambiguationData":[OSD([sQuery(id+"F1.wireOp",EDGE,"E9.0.49.0")])]}),"instanceName":"10"});
            var Q130;
            Q130=makeQuery(id+"F27.opPattern","COPY",BODY,{"derivedFrom":makeQuery(id+"F3.opExtrude","SWEPT_BODY",BODY,{"disambiguationData":[OSD([sQuery(id+"F1.wireOp",EDGE,"E9.0.49.0")])]}),"instanceName":"5"});
            var Q131;
            Q131=makeQuery(id+"F29.opPattern","COPY",BODY,{"derivedFrom":makeQuery(id+"F3.opExtrude","SWEPT_BODY",BODY,{"disambiguationData":[OSD([sQuery(id+"F1.wireOp",EDGE,"E9.0.47.0")])]}),"instanceName":"4"});
            var Q132;
            Q132=makeQuery(id+"F26.opPattern","COPY",BODY,{"derivedFrom":makeQuery(id+"F3.opExtrude","SWEPT_BODY",BODY,{"disambiguationData":[OSD([sQuery(id+"F1.wireOp",EDGE,"E9.0.51.0")])]}),"instanceName":"18"});
            var Q133;
            Q133=makeQuery(id+"F29.opPattern","COPY",BODY,{"derivedFrom":makeQuery(id+"F3.opExtrude","SWEPT_BODY",BODY,{"disambiguationData":[OSD([sQuery(id+"F1.wireOp",EDGE,"E9.0.46.0")])]}),"instanceName":"5"});
            var Q134;
            Q134=makeQuery(id+"F26.opPattern","COPY",BODY,{"derivedFrom":makeQuery(id+"F3.opExtrude","SWEPT_BODY",BODY,{"disambiguationData":[OSD([sQuery(id+"F1.wireOp",EDGE,"E9.0.51.0")])]}),"instanceName":"17"});
            var Q135;
            Q135=makeQuery(id+"F26.opPattern","COPY",BODY,{"derivedFrom":makeQuery(id+"F3.opExtrude","SWEPT_BODY",BODY,{"disambiguationData":[OSD([sQuery(id+"F1.wireOp",EDGE,"E9.0.51.0")])]}),"instanceName":"16"});
            var Q136;
            Q136=makeQuery(id+"F29.opPattern","COPY",BODY,{"derivedFrom":makeQuery(id+"F3.opExtrude","SWEPT_BODY",BODY,{"disambiguationData":[OSD([sQuery(id+"F1.wireOp",EDGE,"E9.0.47.0")])]}),"instanceName":"5"});
            var Q137;
            Q137=makeQuery(id+"F29.opPattern","COPY",BODY,{"derivedFrom":makeQuery(id+"F3.opExtrude","SWEPT_BODY",BODY,{"disambiguationData":[OSD([sQuery(id+"F1.wireOp",EDGE,"E9.0.46.0")])]}),"instanceName":"6"});
            var Q138;
            Q138=makeQuery(id+"F29.opPattern","COPY",BODY,{"derivedFrom":makeQuery(id+"F3.opExtrude","SWEPT_BODY",BODY,{"disambiguationData":[OSD([sQuery(id+"F1.wireOp",EDGE,"E9.0.47.0")])]}),"instanceName":"9"});
            var Q139;
            Q139=makeQuery(id+"F29.opPattern","COPY",BODY,{"derivedFrom":makeQuery(id+"F3.opExtrude","SWEPT_BODY",BODY,{"disambiguationData":[OSD([sQuery(id+"F1.wireOp",EDGE,"E9.0.46.0")])]}),"instanceName":"10"});
            var Q140;
            Q140=makeQuery(id+"F26.opPattern","COPY",BODY,{"derivedFrom":makeQuery(id+"F3.opExtrude","SWEPT_BODY",BODY,{"disambiguationData":[OSD([sQuery(id+"F1.wireOp",EDGE,"E9.0.51.0")])]}),"instanceName":"15"});
            var Q141;
            Q141=makeQuery(id+"F26.opPattern","COPY",BODY,{"derivedFrom":makeQuery(id+"F3.opExtrude","SWEPT_BODY",BODY,{"disambiguationData":[OSD([sQuery(id+"F1.wireOp",EDGE,"E9.0.51.0")])]}),"instanceName":"14"});
            var Q142;
            Q142=makeQuery(id+"F29.opPattern","COPY",BODY,{"derivedFrom":makeQuery(id+"F3.opExtrude","SWEPT_BODY",BODY,{"disambiguationData":[OSD([sQuery(id+"F1.wireOp",EDGE,"E9.0.47.0")])]}),"instanceName":"10"});
            var Q143;
            Q143=makeQuery(id+"F26.opPattern","COPY",BODY,{"derivedFrom":makeQuery(id+"F3.opExtrude","SWEPT_BODY",BODY,{"disambiguationData":[OSD([sQuery(id+"F1.wireOp",EDGE,"E9.0.51.0")])]}),"instanceName":"13"});
            var Q144;
            Q144=makeQuery(id+"F26.opPattern","COPY",BODY,{"derivedFrom":makeQuery(id+"F3.opExtrude","SWEPT_BODY",BODY,{"disambiguationData":[OSD([sQuery(id+"F1.wireOp",EDGE,"E9.0.51.0")])]}),"instanceName":"12"});
            var Q145;
            Q145=makeQuery(id+"F29.opPattern","COPY",BODY,{"derivedFrom":makeQuery(id+"F3.opExtrude","SWEPT_BODY",BODY,{"disambiguationData":[OSD([sQuery(id+"F1.wireOp",EDGE,"E9.0.46.0")])]}),"instanceName":"11"});
            var Q146;
            Q146=makeQuery(id+"F26.opPattern","COPY",BODY,{"derivedFrom":makeQuery(id+"F3.opExtrude","SWEPT_BODY",BODY,{"disambiguationData":[OSD([sQuery(id+"F1.wireOp",EDGE,"E9.0.51.0")])]}),"instanceName":"11"});
            var Q147;
            Q147=makeQuery(id+"F26.opPattern","COPY",BODY,{"derivedFrom":makeQuery(id+"F3.opExtrude","SWEPT_BODY",BODY,{"disambiguationData":[OSD([sQuery(id+"F1.wireOp",EDGE,"E9.0.51.0")])]}),"instanceName":"10"});
            var Q148;
            Q148=makeQuery(id+"F29.opPattern","COPY",BODY,{"derivedFrom":makeQuery(id+"F3.opExtrude","SWEPT_BODY",BODY,{"disambiguationData":[OSD([sQuery(id+"F1.wireOp",EDGE,"E9.0.47.0")])]}),"instanceName":"21"});
            var Q149;
            Q149=makeQuery(id+"F29.opPattern","COPY",BODY,{"derivedFrom":makeQuery(id+"F3.opExtrude","SWEPT_BODY",BODY,{"disambiguationData":[OSD([sQuery(id+"F1.wireOp",EDGE,"E9.0.47.0")])]}),"instanceName":"11"});
            var Q150;
            Q150=makeQuery(id+"F29.opPattern","COPY",BODY,{"derivedFrom":makeQuery(id+"F3.opExtrude","SWEPT_BODY",BODY,{"disambiguationData":[OSD([sQuery(id+"F1.wireOp",EDGE,"E9.0.46.0")])]}),"instanceName":"21"});
            var Q151;
            Q151=makeQuery(id+"F26.opPattern","COPY",BODY,{"derivedFrom":makeQuery(id+"F3.opExtrude","SWEPT_BODY",BODY,{"disambiguationData":[OSD([sQuery(id+"F1.wireOp",EDGE,"E9.0.51.0")])]}),"instanceName":"9"});
            var Q152;
            Q152=makeQuery(id+"F27.opPattern","COPY",BODY,{"derivedFrom":makeQuery(id+"F3.opExtrude","SWEPT_BODY",BODY,{"disambiguationData":[OSD([sQuery(id+"F1.wireOp",EDGE,"E9.0.50.0")])]}),"instanceName":"22"});
            var Q153;
            Q153=makeQuery(id+"F27.opPattern","COPY",BODY,{"derivedFrom":makeQuery(id+"F3.opExtrude","SWEPT_BODY",BODY,{"disambiguationData":[OSD([sQuery(id+"F1.wireOp",EDGE,"E9.0.49.0")])]}),"instanceName":"22"});
            var Q154;
            Q154=makeQuery(id+"F26.opPattern","COPY",BODY,{"derivedFrom":makeQuery(id+"F3.opExtrude","SWEPT_BODY",BODY,{"disambiguationData":[OSD([sQuery(id+"F1.wireOp",EDGE,"E9.0.51.0")])]}),"instanceName":"8"});
            var Q155;
            Q155=makeQuery(id+"F29.opPattern","COPY",BODY,{"derivedFrom":makeQuery(id+"F3.opExtrude","SWEPT_BODY",BODY,{"disambiguationData":[OSD([sQuery(id+"F1.wireOp",EDGE,"E9.0.46.0")])]}),"instanceName":"12"});
            var Q156;
            Q156=makeQuery(id+"F27.opPattern","COPY",BODY,{"derivedFrom":makeQuery(id+"F3.opExtrude","SWEPT_BODY",BODY,{"disambiguationData":[OSD([sQuery(id+"F1.wireOp",EDGE,"E9.0.50.0")])]}),"instanceName":"21"});
            var Q157;
            Q157=makeQuery(id+"F29.opPattern","COPY",BODY,{"derivedFrom":makeQuery(id+"F3.opExtrude","SWEPT_BODY",BODY,{"disambiguationData":[OSD([sQuery(id+"F1.wireOp",EDGE,"E9.0.47.0")])]}),"instanceName":"12"});
            var Q158;
            Q158=makeQuery(id+"F26.opPattern","COPY",BODY,{"derivedFrom":makeQuery(id+"F3.opExtrude","SWEPT_BODY",BODY,{"disambiguationData":[OSD([sQuery(id+"F1.wireOp",EDGE,"E9.0.51.0")])]}),"instanceName":"7"});
            var Q159;
            Q159=makeQuery(id+"F26.opPattern","COPY",BODY,{"derivedFrom":makeQuery(id+"F3.opExtrude","SWEPT_BODY",BODY,{"disambiguationData":[OSD([sQuery(id+"F1.wireOp",EDGE,"E9.0.51.0")])]}),"instanceName":"6"});
            var Q160;
            Q160=makeQuery(id+"F27.opPattern","COPY",BODY,{"derivedFrom":makeQuery(id+"F3.opExtrude","SWEPT_BODY",BODY,{"disambiguationData":[OSD([sQuery(id+"F1.wireOp",EDGE,"E9.0.49.0")])]}),"instanceName":"21"});
            var Q161;
            Q161=makeQuery(id+"F27.opPattern","COPY",BODY,{"derivedFrom":makeQuery(id+"F3.opExtrude","SWEPT_BODY",BODY,{"disambiguationData":[OSD([sQuery(id+"F1.wireOp",EDGE,"E9.0.50.0")])]}),"instanceName":"3"});
            var Q162;
            Q162=makeQuery(id+"F29.opPattern","COPY",BODY,{"derivedFrom":makeQuery(id+"F3.opExtrude","SWEPT_BODY",BODY,{"disambiguationData":[OSD([sQuery(id+"F1.wireOp",EDGE,"E9.0.46.0")])]}),"instanceName":"13"});
            var Q163;
            Q163=makeQuery(id+"F29.opPattern","COPY",BODY,{"derivedFrom":makeQuery(id+"F3.opExtrude","SWEPT_BODY",BODY,{"disambiguationData":[OSD([sQuery(id+"F1.wireOp",EDGE,"E9.0.47.0")])]}),"instanceName":"13"});
            var Q164;
            Q164=makeQuery(id+"F26.opPattern","COPY",BODY,{"derivedFrom":makeQuery(id+"F3.opExtrude","SWEPT_BODY",BODY,{"disambiguationData":[OSD([sQuery(id+"F1.wireOp",EDGE,"E9.0.51.0")])]}),"instanceName":"5"});
            var Q165;
            Q165=makeQuery(id+"F29.opPattern","COPY",BODY,{"derivedFrom":makeQuery(id+"F3.opExtrude","SWEPT_BODY",BODY,{"disambiguationData":[OSD([sQuery(id+"F1.wireOp",EDGE,"E9.0.46.0")])]}),"instanceName":"14"});
            var Q166;
            Q166=makeQuery(id+"F25.opPattern","COPY",BODY,{"derivedFrom":makeQuery(id+"F3.opExtrude","SWEPT_BODY",BODY,{"disambiguationData":[OSD([sQuery(id+"F1.wireOp",EDGE,"E9.0.52.0")])]}),"instanceName":"1"});
            var Q167;
            Q167=makeQuery(id+"F26.opPattern","COPY",BODY,{"derivedFrom":makeQuery(id+"F3.opExtrude","SWEPT_BODY",BODY,{"disambiguationData":[OSD([sQuery(id+"F1.wireOp",EDGE,"E9.0.51.0")])]}),"instanceName":"4"});
            var Q168;
            Q168=makeQuery(id+"F29.opPattern","COPY",BODY,{"derivedFrom":makeQuery(id+"F3.opExtrude","SWEPT_BODY",BODY,{"disambiguationData":[OSD([sQuery(id+"F1.wireOp",EDGE,"E9.0.47.0")])]}),"instanceName":"17"});
            var Q169;
            Q169=makeQuery(id+"F27.opPattern","COPY",BODY,{"derivedFrom":makeQuery(id+"F3.opExtrude","SWEPT_BODY",BODY,{"disambiguationData":[OSD([sQuery(id+"F1.wireOp",EDGE,"E9.0.49.0")])]}),"instanceName":"6"});
            var Q170;
            Q170=makeQuery(id+"F25.opPattern","COPY",BODY,{"derivedFrom":makeQuery(id+"F3.opExtrude","SWEPT_BODY",BODY,{"disambiguationData":[OSD([sQuery(id+"F1.wireOp",EDGE,"E9.0.53.0")])]}),"instanceName":"1"});
            var Q171;
            Q171=makeQuery(id+"F29.opPattern","COPY",BODY,{"derivedFrom":makeQuery(id+"F3.opExtrude","SWEPT_BODY",BODY,{"disambiguationData":[OSD([sQuery(id+"F1.wireOp",EDGE,"E9.0.46.0")])]}),"instanceName":"18"});
            var Q172;
            Q172=makeQuery(id+"F29.opPattern","COPY",BODY,{"derivedFrom":makeQuery(id+"F3.opExtrude","SWEPT_BODY",BODY,{"disambiguationData":[OSD([sQuery(id+"F1.wireOp",EDGE,"E9.0.47.0")])]}),"instanceName":"18"});
            var Q173;
            Q173=makeQuery(id+"F25.opPattern","COPY",BODY,{"derivedFrom":makeQuery(id+"F3.opExtrude","SWEPT_BODY",BODY,{"disambiguationData":[OSD([sQuery(id+"F1.wireOp",EDGE,"E9.0.52.0")])]}),"instanceName":"2"});
            var Q174;
            Q174=makeQuery(id+"F27.opPattern","COPY",BODY,{"derivedFrom":makeQuery(id+"F3.opExtrude","SWEPT_BODY",BODY,{"disambiguationData":[OSD([sQuery(id+"F1.wireOp",EDGE,"E9.0.50.0")])]}),"instanceName":"2"});
            var Q175;
            Q175=makeQuery(id+"F29.opPattern","COPY",BODY,{"derivedFrom":makeQuery(id+"F3.opExtrude","SWEPT_BODY",BODY,{"disambiguationData":[OSD([sQuery(id+"F1.wireOp",EDGE,"E9.0.47.0")])]}),"instanceName":"20"});
            var Q176;
            Q176=makeQuery(id+"F26.opPattern","COPY",BODY,{"derivedFrom":makeQuery(id+"F3.opExtrude","SWEPT_BODY",BODY,{"disambiguationData":[OSD([sQuery(id+"F1.wireOp",EDGE,"E9.0.51.0")])]}),"instanceName":"3"});
            var Q177;
            Q177=makeQuery(id+"F28.opPattern","COPY",BODY,{"derivedFrom":makeQuery(id+"F3.opExtrude","SWEPT_BODY",BODY,{"disambiguationData":[OSD([sQuery(id+"F1.wireOp",EDGE,"E9.0.48.0")])]}),"instanceName":"6"});
            var Q178;
            Q178=makeQuery(id+"F25.opPattern","COPY",BODY,{"derivedFrom":makeQuery(id+"F3.opExtrude","SWEPT_BODY",BODY,{"disambiguationData":[OSD([sQuery(id+"F1.wireOp",EDGE,"E9.0.53.0")])]}),"instanceName":"2"});
            var Q179;
            Q179=makeQuery(id+"F27.opPattern","COPY",BODY,{"derivedFrom":makeQuery(id+"F3.opExtrude","SWEPT_BODY",BODY,{"disambiguationData":[OSD([sQuery(id+"F1.wireOp",EDGE,"E9.0.50.0")])]}),"instanceName":"20"});
            var Q180;
            Q180=makeQuery(id+"F25.opPattern","COPY",BODY,{"derivedFrom":makeQuery(id+"F3.opExtrude","SWEPT_BODY",BODY,{"disambiguationData":[OSD([sQuery(id+"F1.wireOp",EDGE,"E9.0.52.0")])]}),"instanceName":"3"});
            var Q181;
            Q181=makeQuery(id+"F26.opPattern","COPY",BODY,{"derivedFrom":makeQuery(id+"F3.opExtrude","SWEPT_BODY",BODY,{"disambiguationData":[OSD([sQuery(id+"F1.wireOp",EDGE,"E9.0.51.0")])]}),"instanceName":"2"});
            var Q182;
            Q182=makeQuery(id+"F26.opPattern","COPY",BODY,{"derivedFrom":makeQuery(id+"F3.opExtrude","SWEPT_BODY",BODY,{"disambiguationData":[OSD([sQuery(id+"F1.wireOp",EDGE,"E9.0.51.0")])]}),"instanceName":"1"});
            var Q183;
            Q183=makeQuery(id+"F25.opPattern","COPY",BODY,{"derivedFrom":makeQuery(id+"F3.opExtrude","SWEPT_BODY",BODY,{"disambiguationData":[OSD([sQuery(id+"F1.wireOp",EDGE,"E9.0.53.0")])]}),"instanceName":"3"});
            var Q184;
            Q184=makeQuery(id+"F27.opPattern","COPY",BODY,{"derivedFrom":makeQuery(id+"F3.opExtrude","SWEPT_BODY",BODY,{"disambiguationData":[OSD([sQuery(id+"F1.wireOp",EDGE,"E9.0.49.0")])]}),"instanceName":"20"});
            var Q185;
            Q185=makeQuery(id+"F27.opPattern","COPY",BODY,{"derivedFrom":makeQuery(id+"F3.opExtrude","SWEPT_BODY",BODY,{"disambiguationData":[OSD([sQuery(id+"F1.wireOp",EDGE,"E9.0.50.0")])]}),"instanceName":"19"});
            var Q186;
            Q186=makeQuery(id+"F25.opPattern","COPY",BODY,{"derivedFrom":makeQuery(id+"F3.opExtrude","SWEPT_BODY",BODY,{"disambiguationData":[OSD([sQuery(id+"F1.wireOp",EDGE,"E9.0.52.0")])]}),"instanceName":"4"});
            var Q187;
            Q187=makeQuery(id+"F29.opPattern","COPY",BODY,{"derivedFrom":makeQuery(id+"F3.opExtrude","SWEPT_BODY",BODY,{"disambiguationData":[OSD([sQuery(id+"F1.wireOp",EDGE,"E9.0.47.0")])]}),"instanceName":"19"});
            var Q188;
            Q188=makeQuery(id+"F29.opPattern","COPY",BODY,{"derivedFrom":makeQuery(id+"F3.opExtrude","SWEPT_BODY",BODY,{"disambiguationData":[OSD([sQuery(id+"F1.wireOp",EDGE,"E9.0.46.0")])]}),"instanceName":"20"});
            var Q189;
            Q189=makeQuery(id+"F29.opPattern","COPY",BODY,{"derivedFrom":makeQuery(id+"F3.opExtrude","SWEPT_BODY",BODY,{"disambiguationData":[OSD([sQuery(id+"F1.wireOp",EDGE,"E9.0.46.0")])]}),"instanceName":"1"});
            var Q190;
            Q190=makeQuery(id+"F28.opPattern","COPY",BODY,{"derivedFrom":makeQuery(id+"F3.opExtrude","SWEPT_BODY",BODY,{"disambiguationData":[OSD([sQuery(id+"F1.wireOp",EDGE,"E9.0.48.0")])]}),"instanceName":"22"});
            var Q191;
            Q191=makeQuery(id+"F27.opPattern","COPY",BODY,{"derivedFrom":makeQuery(id+"F3.opExtrude","SWEPT_BODY",BODY,{"disambiguationData":[OSD([sQuery(id+"F1.wireOp",EDGE,"E9.0.50.0")])]}),"instanceName":"9"});
            var Q192;
            Q192=makeQuery(id+"F28.opPattern","COPY",BODY,{"derivedFrom":makeQuery(id+"F3.opExtrude","SWEPT_BODY",BODY,{"disambiguationData":[OSD([sQuery(id+"F1.wireOp",EDGE,"E9.0.48.0")])]}),"instanceName":"4"});
            var Q193;
            Q193=makeQuery(id+"F27.opPattern","COPY",BODY,{"derivedFrom":makeQuery(id+"F3.opExtrude","SWEPT_BODY",BODY,{"disambiguationData":[OSD([sQuery(id+"F1.wireOp",EDGE,"E9.0.49.0")])]}),"instanceName":"7"});
            var Q194;
            Q194=makeQuery(id+"F28.opPattern","COPY",BODY,{"derivedFrom":makeQuery(id+"F3.opExtrude","SWEPT_BODY",BODY,{"disambiguationData":[OSD([sQuery(id+"F1.wireOp",EDGE,"E9.0.48.0")])]}),"instanceName":"23"});
            var Q195;
            Q195=makeQuery(id+"F24.opPattern","COPY",BODY,{"derivedFrom":makeQuery(id+"F3.opExtrude","SWEPT_BODY",BODY,{"disambiguationData":[OSD([sQuery(id+"F1.wireOp",EDGE,"E9.0.54.0")])]}),"instanceName":"20"});
            var Q196;
            Q196=makeQuery(id+"F3.opExtrude","SWEPT_BODY",BODY,{"disambiguationData":[OSD([sQuery(id+"F1.wireOp",EDGE,"E9.0.46.0")])]});
            var Q197;
            Q197=makeQuery(id+"F3.opExtrude","SWEPT_BODY",BODY,{"disambiguationData":[OSD([sQuery(id+"F1.wireOp",EDGE,"E9.0.47.0")])]});
            var Q198;
            Q198=makeQuery(id+"F3.opExtrude","SWEPT_BODY",BODY,{"disambiguationData":[OSD([sQuery(id+"F1.wireOp",EDGE,"E9.0.48.0")])]});
            var Q199;
            Q199=makeQuery(id+"F3.opExtrude","SWEPT_BODY",BODY,{"disambiguationData":[OSD([sQuery(id+"F1.wireOp",EDGE,"E9.0.49.0")])]});
            var Q200;
            Q200=makeQuery(id+"F29.opPattern","COPY",BODY,{"derivedFrom":makeQuery(id+"F3.opExtrude","SWEPT_BODY",BODY,{"disambiguationData":[OSD([sQuery(id+"F1.wireOp",EDGE,"E9.0.46.0")])]}),"instanceName":"25"});
            var Q201;
            Q201=makeQuery(id+"F29.opPattern","COPY",BODY,{"derivedFrom":makeQuery(id+"F3.opExtrude","SWEPT_BODY",BODY,{"disambiguationData":[OSD([sQuery(id+"F1.wireOp",EDGE,"E9.0.47.0")])]}),"instanceName":"25"});
            var Q202;
            Q202=makeQuery(id+"F3.opExtrude","SWEPT_BODY",BODY,{"disambiguationData":[OSD([sQuery(id+"F1.wireOp",EDGE,"E9.0.50.0")])]});
            var Q203;
            Q203=makeQuery(id+"F3.opExtrude","SWEPT_BODY",BODY,{"disambiguationData":[OSD([sQuery(id+"F1.wireOp",EDGE,"E9.0.51.0")])]});
            var Q204;
            Q204=makeQuery(id+"F3.opExtrude","SWEPT_BODY",BODY,{"disambiguationData":[OSD([sQuery(id+"F1.wireOp",EDGE,"E9.0.52.0")])]});
            var Q205;
            Q205=makeQuery(id+"F3.opExtrude","SWEPT_BODY",BODY,{"disambiguationData":[OSD([sQuery(id+"F1.wireOp",EDGE,"E9.0.53.0")])]});
            var Q206;
            Q206=makeQuery(id+"F3.opExtrude","SWEPT_BODY",BODY,{"disambiguationData":[OSD([sQuery(id+"F1.wireOp",EDGE,"E9.0.54.0")])]});
            var Q207;
            Q207=makeQuery(id+"F25.opPattern","COPY",BODY,{"derivedFrom":makeQuery(id+"F3.opExtrude","SWEPT_BODY",BODY,{"disambiguationData":[OSD([sQuery(id+"F1.wireOp",EDGE,"E9.0.52.0")])]}),"instanceName":"21"});
            var Q208;
            Q208=makeQuery(id+"F25.opPattern","COPY",BODY,{"derivedFrom":makeQuery(id+"F3.opExtrude","SWEPT_BODY",BODY,{"disambiguationData":[OSD([sQuery(id+"F1.wireOp",EDGE,"E9.0.53.0")])]}),"instanceName":"21"});
            var Q209;
            Q209=makeQuery(id+"F26.opPattern","COPY",BODY,{"derivedFrom":makeQuery(id+"F3.opExtrude","SWEPT_BODY",BODY,{"disambiguationData":[OSD([sQuery(id+"F1.wireOp",EDGE,"E9.0.51.0")])]}),"instanceName":"22"});
            var Q210;
            Q210=makeQuery(id+"F27.opPattern","COPY",BODY,{"derivedFrom":makeQuery(id+"F3.opExtrude","SWEPT_BODY",BODY,{"disambiguationData":[OSD([sQuery(id+"F1.wireOp",EDGE,"E9.0.50.0")])]}),"instanceName":"23"});
            var Q211;
            Q211=makeQuery(id+"F27.opPattern","COPY",BODY,{"derivedFrom":makeQuery(id+"F3.opExtrude","SWEPT_BODY",BODY,{"disambiguationData":[OSD([sQuery(id+"F1.wireOp",EDGE,"E9.0.49.0")])]}),"instanceName":"23"});
            var Q212;
            Q212=makeQuery(id+"F28.opPattern","COPY",BODY,{"derivedFrom":makeQuery(id+"F3.opExtrude","SWEPT_BODY",BODY,{"disambiguationData":[OSD([sQuery(id+"F1.wireOp",EDGE,"E9.0.48.0")])]}),"instanceName":"24"});
            var Q213;
            Q213=makeQuery(id+"F2.opRevolve","SWEPT_BODY",BODY,{"disambiguationData":[OSD([sQuery(id+"F0.wireOp",EDGE,"E0"),sQuery(id+"F0.wireOp",EDGE,"E1"),sQuery(id+"F0.wireOp",EDGE,"E2"),sQuery(id+"F0.wireOp",EDGE,"E3"),sQuery(id+"F0.wireOp",EDGE,"E6")])]});
            booleanBodies(context, id + "F30", {"operationType" : BooleanOperationType.SUBTRACTION, "tools" : qUnion([Q0, Q1, Q2, Q3, Q4, Q5, Q6, Q7, Q8, Q9, Q10, Q11, Q12, Q13, Q14, Q15, Q16, Q17, Q18, Q19, Q20, Q21, Q22, Q23, Q24, Q25, Q26, Q27, Q28, Q29, Q30, Q31, Q32, Q33, Q34, Q35, Q36, Q37, Q38, Q39, Q40, Q41, Q42, Q43, Q44, Q45, Q46, Q47, Q48, Q49, Q50, Q51, Q52, Q53, Q54, Q55, Q56, Q57, Q58, Q59, Q60, Q61, Q62, Q63, Q64, Q65, Q66, Q67, Q68, Q69, Q70, Q71, Q72, Q73, Q74, Q75, Q76, Q77, Q78, Q79, Q80, Q81, Q82, Q83, Q84, Q85, Q86, Q87, Q88, Q89, Q90, Q91, Q92, Q93, Q94, Q95, Q96, Q97, Q98, Q99, Q100, Q101, Q102, Q103, Q104, Q105, Q106, Q107, Q108, Q109, Q110, Q111, Q112, Q113, Q114, Q115, Q116, Q117, Q118, Q119, Q120, Q121, Q122, Q123, Q124, Q125, Q126, Q127, Q128, Q129, Q130, Q131, Q132, Q133, Q134, Q135, Q136, Q137, Q138, Q139, Q140, Q141, Q142, Q143, Q144, Q145, Q146, Q147, Q148, Q149, Q150, Q151, Q152, Q153, Q154, Q155, Q156, Q157, Q158, Q159, Q160, Q161, Q162, Q163, Q164, Q165, Q166, Q167, Q168, Q169, Q170, Q171, Q172, Q173, Q174, Q175, Q176, Q177, Q178, Q179, Q180, Q181, Q182, Q183, Q184, Q185, Q186, Q187, Q188, Q189, Q190, Q191, Q192, Q193, Q194, Q195, Q196, Q197, Q198, Q199, Q200, Q201, Q202, Q203, Q204, Q205, Q206, Q207, Q208, Q209, Q210, Q211, Q212]), "targets" : qUnion([Q213])});
        }
        {
            var Q0;
            Q0=makeQuery(id+"F3.opExtrude","SWEPT_BODY",BODY,{"disambiguationData":[OSD([sQuery(id+"F1.wireOp",EDGE,"E9.0.45.0")])]});
            var Q1;
            Q1=makeQuery(id+"F3.opExtrude","SWEPT_BODY",BODY,{"disambiguationData":[OSD([sQuery(id+"F1.wireOp",EDGE,"E9.0.44.0")])]});
            var Q2;
            Q2=makeQuery(id+"F2.opRevolve","SWEPT_FACE",FACE,{"disambiguationData":[OSD([sQuery(id+"F0.wireOp",EDGE,"E1")])]});
            circularPattern(context, id + "F31", {"entities" : qUnion([Q0, Q1]), "axis" : qUnion([Q2]), "angle" : 180 * degree, "instanceCount" : 27, "oppositeDirection" : true, "equalSpace" : true});
        }
        {
            var Q0;
            Q0=makeQuery(id+"F3.opExtrude","SWEPT_BODY",BODY,{"disambiguationData":[OSD([sQuery(id+"F1.wireOp",EDGE,"E9.0.43.0")])]});
            var Q1;
            Q1=makeQuery(id+"F2.opRevolve","SWEPT_FACE",FACE,{"disambiguationData":[OSD([sQuery(id+"F0.wireOp",EDGE,"E1")])]});
            circularPattern(context, id + "F32", {"entities" : qUnion([Q0]), "axis" : qUnion([Q1]), "angle" : 180 * degree, "instanceCount" : 28, "oppositeDirection" : true, "equalSpace" : true});
        }
        {
            var Q0;
            Q0=makeQuery(id+"F3.opExtrude","SWEPT_BODY",BODY,{"disambiguationData":[OSD([sQuery(id+"F1.wireOp",EDGE,"E9.0.42.0")])]});
            var Q1;
            Q1=makeQuery(id+"F3.opExtrude","SWEPT_BODY",BODY,{"disambiguationData":[OSD([sQuery(id+"F1.wireOp",EDGE,"E9.0.41.0")])]});
            var Q2;
            Q2=makeQuery(id+"F2.opRevolve","SWEPT_FACE",FACE,{"disambiguationData":[OSD([sQuery(id+"F0.wireOp",EDGE,"E1")])]});
            circularPattern(context, id + "F33", {"entities" : qUnion([Q0, Q1]), "axis" : qUnion([Q2]), "angle" : 180 * degree, "instanceCount" : 29, "oppositeDirection" : true, "equalSpace" : true});
        }
        {
            var Q0;
            Q0=makeQuery(id+"F3.opExtrude","SWEPT_BODY",BODY,{"disambiguationData":[OSD([sQuery(id+"F1.wireOp",EDGE,"E9.0.40.0")])]});
            var Q1;
            Q1=makeQuery(id+"F2.opRevolve","SWEPT_FACE",FACE,{"disambiguationData":[OSD([sQuery(id+"F0.wireOp",EDGE,"E1")])]});
            circularPattern(context, id + "F34", {"entities" : qUnion([Q0]), "axis" : qUnion([Q1]), "angle" : 180 * degree, "instanceCount" : 30, "oppositeDirection" : true, "equalSpace" : true});
        }
        {
            var Q0;
            Q0=makeQuery(id+"F3.opExtrude","SWEPT_BODY",BODY,{"disambiguationData":[OSD([sQuery(id+"F1.wireOp",EDGE,"E9.0.39.0")])]});
            var Q1;
            Q1=makeQuery(id+"F3.opExtrude","SWEPT_BODY",BODY,{"disambiguationData":[OSD([sQuery(id+"F1.wireOp",EDGE,"E9.0.38.0")])]});
            var Q2;
            Q2=makeQuery(id+"F2.opRevolve","SWEPT_FACE",FACE,{"disambiguationData":[OSD([sQuery(id+"F0.wireOp",EDGE,"E1")])]});
            circularPattern(context, id + "F35", {"entities" : qUnion([Q0, Q1]), "axis" : qUnion([Q2]), "angle" : 180 * degree, "instanceCount" : 31, "oppositeDirection" : true, "equalSpace" : true});
        }
        {
            var Q0;
            Q0=makeQuery(id+"F3.opExtrude","SWEPT_BODY",BODY,{"disambiguationData":[OSD([sQuery(id+"F1.wireOp",EDGE,"E9.0.37.0")])]});
            var Q1;
            Q1=makeQuery(id+"F2.opRevolve","SWEPT_FACE",FACE,{"disambiguationData":[OSD([sQuery(id+"F0.wireOp",EDGE,"E1")])]});
            circularPattern(context, id + "F36", {"entities" : qUnion([Q0]), "axis" : qUnion([Q1]), "angle" : 180 * degree, "instanceCount" : 32, "oppositeDirection" : true, "equalSpace" : true});
        }
        {
            var Q0;
            Q0=makeQuery(id+"F3.opExtrude","SWEPT_BODY",BODY,{"disambiguationData":[OSD([sQuery(id+"F1.wireOp",EDGE,"E9.0.36.0")])]});
            var Q1;
            Q1=makeQuery(id+"F3.opExtrude","SWEPT_BODY",BODY,{"disambiguationData":[OSD([sQuery(id+"F1.wireOp",EDGE,"E9.0.35.0")])]});
            var Q2;
            Q2=makeQuery(id+"F2.opRevolve","SWEPT_FACE",FACE,{"disambiguationData":[OSD([sQuery(id+"F0.wireOp",EDGE,"E1")])]});
            circularPattern(context, id + "F37", {"entities" : qUnion([Q0, Q1]), "axis" : qUnion([Q2]), "angle" : 180 * degree, "instanceCount" : 33, "oppositeDirection" : true, "equalSpace" : true});
        }
        {
            var Q0;
            Q0=makeQuery(id+"F35.opPattern","COPY",BODY,{"derivedFrom":makeQuery(id+"F3.opExtrude","SWEPT_BODY",BODY,{"disambiguationData":[OSD([sQuery(id+"F1.wireOp",EDGE,"E9.0.39.0")])]}),"instanceName":"10"});
            var Q1;
            Q1=makeQuery(id+"F33.opPattern","COPY",BODY,{"derivedFrom":makeQuery(id+"F3.opExtrude","SWEPT_BODY",BODY,{"disambiguationData":[OSD([sQuery(id+"F1.wireOp",EDGE,"E9.0.41.0")])]}),"instanceName":"3"});
            var Q2;
            Q2=makeQuery(id+"F35.opPattern","COPY",BODY,{"derivedFrom":makeQuery(id+"F3.opExtrude","SWEPT_BODY",BODY,{"disambiguationData":[OSD([sQuery(id+"F1.wireOp",EDGE,"E9.0.38.0")])]}),"instanceName":"3"});
            var Q3;
            Q3=makeQuery(id+"F3.opExtrude","SWEPT_BODY",BODY,{"disambiguationData":[OSD([sQuery(id+"F1.wireOp",EDGE,"E9.0.42.0")])]});
            var Q4;
            Q4=makeQuery(id+"F33.opPattern","COPY",BODY,{"derivedFrom":makeQuery(id+"F3.opExtrude","SWEPT_BODY",BODY,{"disambiguationData":[OSD([sQuery(id+"F1.wireOp",EDGE,"E9.0.42.0")])]}),"instanceName":"2"});
            var Q5;
            Q5=makeQuery(id+"F37.opPattern","COPY",BODY,{"derivedFrom":makeQuery(id+"F3.opExtrude","SWEPT_BODY",BODY,{"disambiguationData":[OSD([sQuery(id+"F1.wireOp",EDGE,"E9.0.35.0")])]}),"instanceName":"16"});
            var Q6;
            Q6=makeQuery(id+"F35.opPattern","COPY",BODY,{"derivedFrom":makeQuery(id+"F3.opExtrude","SWEPT_BODY",BODY,{"disambiguationData":[OSD([sQuery(id+"F1.wireOp",EDGE,"E9.0.39.0")])]}),"instanceName":"3"});
            var Q7;
            Q7=makeQuery(id+"F35.opPattern","COPY",BODY,{"derivedFrom":makeQuery(id+"F3.opExtrude","SWEPT_BODY",BODY,{"disambiguationData":[OSD([sQuery(id+"F1.wireOp",EDGE,"E9.0.38.0")])]}),"instanceName":"4"});
            var Q8;
            Q8=makeQuery(id+"F33.opPattern","COPY",BODY,{"derivedFrom":makeQuery(id+"F3.opExtrude","SWEPT_BODY",BODY,{"disambiguationData":[OSD([sQuery(id+"F1.wireOp",EDGE,"E9.0.41.0")])]}),"instanceName":"2"});
            var Q9;
            Q9=makeQuery(id+"F37.opPattern","COPY",BODY,{"derivedFrom":makeQuery(id+"F3.opExtrude","SWEPT_BODY",BODY,{"disambiguationData":[OSD([sQuery(id+"F1.wireOp",EDGE,"E9.0.36.0")])]}),"instanceName":"15"});
            var Q10;
            Q10=makeQuery(id+"F35.opPattern","COPY",BODY,{"derivedFrom":makeQuery(id+"F3.opExtrude","SWEPT_BODY",BODY,{"disambiguationData":[OSD([sQuery(id+"F1.wireOp",EDGE,"E9.0.39.0")])]}),"instanceName":"4"});
            var Q11;
            Q11=makeQuery(id+"F35.opPattern","COPY",BODY,{"derivedFrom":makeQuery(id+"F3.opExtrude","SWEPT_BODY",BODY,{"disambiguationData":[OSD([sQuery(id+"F1.wireOp",EDGE,"E9.0.39.0")])]}),"instanceName":"2"});
            var Q12;
            Q12=makeQuery(id+"F33.opPattern","COPY",BODY,{"derivedFrom":makeQuery(id+"F3.opExtrude","SWEPT_BODY",BODY,{"disambiguationData":[OSD([sQuery(id+"F1.wireOp",EDGE,"E9.0.41.0")])]}),"instanceName":"18"});
            var Q13;
            Q13=makeQuery(id+"F35.opPattern","COPY",BODY,{"derivedFrom":makeQuery(id+"F3.opExtrude","SWEPT_BODY",BODY,{"disambiguationData":[OSD([sQuery(id+"F1.wireOp",EDGE,"E9.0.38.0")])]}),"instanceName":"10"});
            var Q14;
            Q14=makeQuery(id+"F31.opPattern","COPY",BODY,{"derivedFrom":makeQuery(id+"F3.opExtrude","SWEPT_BODY",BODY,{"disambiguationData":[OSD([sQuery(id+"F1.wireOp",EDGE,"E9.0.45.0")])]}),"instanceName":"7"});
            var Q15;
            Q15=makeQuery(id+"F31.opPattern","COPY",BODY,{"derivedFrom":makeQuery(id+"F3.opExtrude","SWEPT_BODY",BODY,{"disambiguationData":[OSD([sQuery(id+"F1.wireOp",EDGE,"E9.0.44.0")])]}),"instanceName":"4"});
            var Q16;
            Q16=makeQuery(id+"F35.opPattern","COPY",BODY,{"derivedFrom":makeQuery(id+"F3.opExtrude","SWEPT_BODY",BODY,{"disambiguationData":[OSD([sQuery(id+"F1.wireOp",EDGE,"E9.0.39.0")])]}),"instanceName":"11"});
            var Q17;
            Q17=makeQuery(id+"F37.opPattern","COPY",BODY,{"derivedFrom":makeQuery(id+"F3.opExtrude","SWEPT_BODY",BODY,{"disambiguationData":[OSD([sQuery(id+"F1.wireOp",EDGE,"E9.0.35.0")])]}),"instanceName":"15"});
            var Q18;
            Q18=makeQuery(id+"F35.opPattern","COPY",BODY,{"derivedFrom":makeQuery(id+"F3.opExtrude","SWEPT_BODY",BODY,{"disambiguationData":[OSD([sQuery(id+"F1.wireOp",EDGE,"E9.0.38.0")])]}),"instanceName":"2"});
            var Q19;
            Q19=makeQuery(id+"F31.opPattern","COPY",BODY,{"derivedFrom":makeQuery(id+"F3.opExtrude","SWEPT_BODY",BODY,{"disambiguationData":[OSD([sQuery(id+"F1.wireOp",EDGE,"E9.0.45.0")])]}),"instanceName":"3"});
            var Q20;
            Q20=makeQuery(id+"F3.opExtrude","SWEPT_BODY",BODY,{"disambiguationData":[OSD([sQuery(id+"F1.wireOp",EDGE,"E9.0.43.0")])]});
            var Q21;
            Q21=makeQuery(id+"F35.opPattern","COPY",BODY,{"derivedFrom":makeQuery(id+"F3.opExtrude","SWEPT_BODY",BODY,{"disambiguationData":[OSD([sQuery(id+"F1.wireOp",EDGE,"E9.0.38.0")])]}),"instanceName":"12"});
            var Q22;
            Q22=makeQuery(id+"F36.opPattern","COPY",BODY,{"derivedFrom":makeQuery(id+"F3.opExtrude","SWEPT_BODY",BODY,{"disambiguationData":[OSD([sQuery(id+"F1.wireOp",EDGE,"E9.0.37.0")])]}),"instanceName":"17"});
            var Q23;
            Q23=makeQuery(id+"F35.opPattern","COPY",BODY,{"derivedFrom":makeQuery(id+"F3.opExtrude","SWEPT_BODY",BODY,{"disambiguationData":[OSD([sQuery(id+"F1.wireOp",EDGE,"E9.0.38.0")])]}),"instanceName":"11"});
            var Q24;
            Q24=makeQuery(id+"F3.opExtrude","SWEPT_BODY",BODY,{"disambiguationData":[OSD([sQuery(id+"F1.wireOp",EDGE,"E9.0.44.0")])]});
            var Q25;
            Q25=makeQuery(id+"F35.opPattern","COPY",BODY,{"derivedFrom":makeQuery(id+"F3.opExtrude","SWEPT_BODY",BODY,{"disambiguationData":[OSD([sQuery(id+"F1.wireOp",EDGE,"E9.0.39.0")])]}),"instanceName":"1"});
            var Q26;
            Q26=makeQuery(id+"F35.opPattern","COPY",BODY,{"derivedFrom":makeQuery(id+"F3.opExtrude","SWEPT_BODY",BODY,{"disambiguationData":[OSD([sQuery(id+"F1.wireOp",EDGE,"E9.0.38.0")])]}),"instanceName":"1"});
            var Q27;
            Q27=makeQuery(id+"F35.opPattern","COPY",BODY,{"derivedFrom":makeQuery(id+"F3.opExtrude","SWEPT_BODY",BODY,{"disambiguationData":[OSD([sQuery(id+"F1.wireOp",EDGE,"E9.0.39.0")])]}),"instanceName":"12"});
            var Q28;
            Q28=makeQuery(id+"F37.opPattern","COPY",BODY,{"derivedFrom":makeQuery(id+"F3.opExtrude","SWEPT_BODY",BODY,{"disambiguationData":[OSD([sQuery(id+"F1.wireOp",EDGE,"E9.0.36.0")])]}),"instanceName":"14"});
            var Q29;
            Q29=makeQuery(id+"F35.opPattern","COPY",BODY,{"derivedFrom":makeQuery(id+"F3.opExtrude","SWEPT_BODY",BODY,{"disambiguationData":[OSD([sQuery(id+"F1.wireOp",EDGE,"E9.0.38.0")])]}),"instanceName":"13"});
            var Q30;
            Q30=makeQuery(id+"F3.opExtrude","SWEPT_BODY",BODY,{"disambiguationData":[OSD([sQuery(id+"F1.wireOp",EDGE,"E9.0.45.0")])]});
            var Q31;
            Q31=makeQuery(id+"F37.opPattern","COPY",BODY,{"derivedFrom":makeQuery(id+"F3.opExtrude","SWEPT_BODY",BODY,{"disambiguationData":[OSD([sQuery(id+"F1.wireOp",EDGE,"E9.0.35.0")])]}),"instanceName":"14"});
            var Q32;
            Q32=makeQuery(id+"F37.opPattern","COPY",BODY,{"derivedFrom":makeQuery(id+"F3.opExtrude","SWEPT_BODY",BODY,{"disambiguationData":[OSD([sQuery(id+"F1.wireOp",EDGE,"E9.0.36.0")])]}),"instanceName":"13"});
            var Q33;
            Q33=makeQuery(id+"F35.opPattern","COPY",BODY,{"derivedFrom":makeQuery(id+"F3.opExtrude","SWEPT_BODY",BODY,{"disambiguationData":[OSD([sQuery(id+"F1.wireOp",EDGE,"E9.0.38.0")])]}),"instanceName":"24"});
            var Q34;
            Q34=makeQuery(id+"F35.opPattern","COPY",BODY,{"derivedFrom":makeQuery(id+"F3.opExtrude","SWEPT_BODY",BODY,{"disambiguationData":[OSD([sQuery(id+"F1.wireOp",EDGE,"E9.0.39.0")])]}),"instanceName":"23"});
            var Q35;
            Q35=makeQuery(id+"F33.opPattern","COPY",BODY,{"derivedFrom":makeQuery(id+"F3.opExtrude","SWEPT_BODY",BODY,{"disambiguationData":[OSD([sQuery(id+"F1.wireOp",EDGE,"E9.0.41.0")])]}),"instanceName":"21"});
            var Q36;
            Q36=makeQuery(id+"F31.opPattern","COPY",BODY,{"derivedFrom":makeQuery(id+"F3.opExtrude","SWEPT_BODY",BODY,{"disambiguationData":[OSD([sQuery(id+"F1.wireOp",EDGE,"E9.0.45.0")])]}),"instanceName":"22"});
            var Q37;
            Q37=makeQuery(id+"F31.opPattern","COPY",BODY,{"derivedFrom":makeQuery(id+"F3.opExtrude","SWEPT_BODY",BODY,{"disambiguationData":[OSD([sQuery(id+"F1.wireOp",EDGE,"E9.0.45.0")])]}),"instanceName":"18"});
            var Q38;
            Q38=makeQuery(id+"F37.opPattern","COPY",BODY,{"derivedFrom":makeQuery(id+"F3.opExtrude","SWEPT_BODY",BODY,{"disambiguationData":[OSD([sQuery(id+"F1.wireOp",EDGE,"E9.0.35.0")])]}),"instanceName":"13"});
            var Q39;
            Q39=makeQuery(id+"F35.opPattern","COPY",BODY,{"derivedFrom":makeQuery(id+"F3.opExtrude","SWEPT_BODY",BODY,{"disambiguationData":[OSD([sQuery(id+"F1.wireOp",EDGE,"E9.0.38.0")])]}),"instanceName":"23"});
            var Q40;
            Q40=makeQuery(id+"F35.opPattern","COPY",BODY,{"derivedFrom":makeQuery(id+"F3.opExtrude","SWEPT_BODY",BODY,{"disambiguationData":[OSD([sQuery(id+"F1.wireOp",EDGE,"E9.0.39.0")])]}),"instanceName":"13"});
            var Q41;
            Q41=makeQuery(id+"F34.opPattern","COPY",BODY,{"derivedFrom":makeQuery(id+"F3.opExtrude","SWEPT_BODY",BODY,{"disambiguationData":[OSD([sQuery(id+"F1.wireOp",EDGE,"E9.0.40.0")])]}),"instanceName":"28"});
            var Q42;
            Q42=makeQuery(id+"F35.opPattern","COPY",BODY,{"derivedFrom":makeQuery(id+"F3.opExtrude","SWEPT_BODY",BODY,{"disambiguationData":[OSD([sQuery(id+"F1.wireOp",EDGE,"E9.0.38.0")])]}),"instanceName":"6"});
            var Q43;
            Q43=makeQuery(id+"F37.opPattern","COPY",BODY,{"derivedFrom":makeQuery(id+"F3.opExtrude","SWEPT_BODY",BODY,{"disambiguationData":[OSD([sQuery(id+"F1.wireOp",EDGE,"E9.0.36.0")])]}),"instanceName":"12"});
            var Q44;
            Q44=makeQuery(id+"F31.opPattern","COPY",BODY,{"derivedFrom":makeQuery(id+"F3.opExtrude","SWEPT_BODY",BODY,{"disambiguationData":[OSD([sQuery(id+"F1.wireOp",EDGE,"E9.0.45.0")])]}),"instanceName":"17"});
            var Q45;
            Q45=makeQuery(id+"F31.opPattern","COPY",BODY,{"derivedFrom":makeQuery(id+"F3.opExtrude","SWEPT_BODY",BODY,{"disambiguationData":[OSD([sQuery(id+"F1.wireOp",EDGE,"E9.0.44.0")])]}),"instanceName":"18"});
            var Q46;
            Q46=makeQuery(id+"F36.opPattern","COPY",BODY,{"derivedFrom":makeQuery(id+"F3.opExtrude","SWEPT_BODY",BODY,{"disambiguationData":[OSD([sQuery(id+"F1.wireOp",EDGE,"E9.0.37.0")])]}),"instanceName":"18"});
            var Q47;
            Q47=makeQuery(id+"F33.opPattern","COPY",BODY,{"derivedFrom":makeQuery(id+"F3.opExtrude","SWEPT_BODY",BODY,{"disambiguationData":[OSD([sQuery(id+"F1.wireOp",EDGE,"E9.0.42.0")])]}),"instanceName":"21"});
            var Q48;
            Q48=makeQuery(id+"F35.opPattern","COPY",BODY,{"derivedFrom":makeQuery(id+"F3.opExtrude","SWEPT_BODY",BODY,{"disambiguationData":[OSD([sQuery(id+"F1.wireOp",EDGE,"E9.0.38.0")])]}),"instanceName":"14"});
            var Q49;
            Q49=makeQuery(id+"F31.opPattern","COPY",BODY,{"derivedFrom":makeQuery(id+"F3.opExtrude","SWEPT_BODY",BODY,{"disambiguationData":[OSD([sQuery(id+"F1.wireOp",EDGE,"E9.0.45.0")])]}),"instanceName":"2"});
            var Q50;
            Q50=makeQuery(id+"F33.opPattern","COPY",BODY,{"derivedFrom":makeQuery(id+"F3.opExtrude","SWEPT_BODY",BODY,{"disambiguationData":[OSD([sQuery(id+"F1.wireOp",EDGE,"E9.0.42.0")])]}),"instanceName":"3"});
            var Q51;
            Q51=makeQuery(id+"F33.opPattern","COPY",BODY,{"derivedFrom":makeQuery(id+"F3.opExtrude","SWEPT_BODY",BODY,{"disambiguationData":[OSD([sQuery(id+"F1.wireOp",EDGE,"E9.0.41.0")])]}),"instanceName":"4"});
            var Q52;
            Q52=makeQuery(id+"F31.opPattern","COPY",BODY,{"derivedFrom":makeQuery(id+"F3.opExtrude","SWEPT_BODY",BODY,{"disambiguationData":[OSD([sQuery(id+"F1.wireOp",EDGE,"E9.0.44.0")])]}),"instanceName":"2"});
            var Q53;
            Q53=makeQuery(id+"F37.opPattern","COPY",BODY,{"derivedFrom":makeQuery(id+"F3.opExtrude","SWEPT_BODY",BODY,{"disambiguationData":[OSD([sQuery(id+"F1.wireOp",EDGE,"E9.0.35.0")])]}),"instanceName":"12"});
            var Q54;
            Q54=makeQuery(id+"F33.opPattern","COPY",BODY,{"derivedFrom":makeQuery(id+"F3.opExtrude","SWEPT_BODY",BODY,{"disambiguationData":[OSD([sQuery(id+"F1.wireOp",EDGE,"E9.0.42.0")])]}),"instanceName":"4"});
            var Q55;
            Q55=makeQuery(id+"F35.opPattern","COPY",BODY,{"derivedFrom":makeQuery(id+"F3.opExtrude","SWEPT_BODY",BODY,{"disambiguationData":[OSD([sQuery(id+"F1.wireOp",EDGE,"E9.0.39.0")])]}),"instanceName":"22"});
            var Q56;
            Q56=makeQuery(id+"F34.opPattern","COPY",BODY,{"derivedFrom":makeQuery(id+"F3.opExtrude","SWEPT_BODY",BODY,{"disambiguationData":[OSD([sQuery(id+"F1.wireOp",EDGE,"E9.0.40.0")])]}),"instanceName":"27"});
            var Q57;
            Q57=makeQuery(id+"F37.opPattern","COPY",BODY,{"derivedFrom":makeQuery(id+"F3.opExtrude","SWEPT_BODY",BODY,{"disambiguationData":[OSD([sQuery(id+"F1.wireOp",EDGE,"E9.0.35.0")])]}),"instanceName":"22"});
            var Q58;
            Q58=makeQuery(id+"F34.opPattern","COPY",BODY,{"derivedFrom":makeQuery(id+"F3.opExtrude","SWEPT_BODY",BODY,{"disambiguationData":[OSD([sQuery(id+"F1.wireOp",EDGE,"E9.0.40.0")])]}),"instanceName":"26"});
            var Q59;
            Q59=makeQuery(id+"F35.opPattern","COPY",BODY,{"derivedFrom":makeQuery(id+"F3.opExtrude","SWEPT_BODY",BODY,{"disambiguationData":[OSD([sQuery(id+"F1.wireOp",EDGE,"E9.0.39.0")])]}),"instanceName":"14"});
            var Q60;
            Q60=makeQuery(id+"F35.opPattern","COPY",BODY,{"derivedFrom":makeQuery(id+"F3.opExtrude","SWEPT_BODY",BODY,{"disambiguationData":[OSD([sQuery(id+"F1.wireOp",EDGE,"E9.0.39.0")])]}),"instanceName":"24"});
            var Q61;
            Q61=makeQuery(id+"F35.opPattern","COPY",BODY,{"derivedFrom":makeQuery(id+"F3.opExtrude","SWEPT_BODY",BODY,{"disambiguationData":[OSD([sQuery(id+"F1.wireOp",EDGE,"E9.0.38.0")])]}),"instanceName":"22"});
            var Q62;
            Q62=makeQuery(id+"F35.opPattern","COPY",BODY,{"derivedFrom":makeQuery(id+"F3.opExtrude","SWEPT_BODY",BODY,{"disambiguationData":[OSD([sQuery(id+"F1.wireOp",EDGE,"E9.0.38.0")])]}),"instanceName":"15"});
            var Q63;
            Q63=makeQuery(id+"F35.opPattern","COPY",BODY,{"derivedFrom":makeQuery(id+"F3.opExtrude","SWEPT_BODY",BODY,{"disambiguationData":[OSD([sQuery(id+"F1.wireOp",EDGE,"E9.0.39.0")])]}),"instanceName":"21"});
            var Q64;
            Q64=makeQuery(id+"F34.opPattern","COPY",BODY,{"derivedFrom":makeQuery(id+"F3.opExtrude","SWEPT_BODY",BODY,{"disambiguationData":[OSD([sQuery(id+"F1.wireOp",EDGE,"E9.0.40.0")])]}),"instanceName":"25"});
            var Q65;
            Q65=makeQuery(id+"F35.opPattern","COPY",BODY,{"derivedFrom":makeQuery(id+"F3.opExtrude","SWEPT_BODY",BODY,{"disambiguationData":[OSD([sQuery(id+"F1.wireOp",EDGE,"E9.0.38.0")])]}),"instanceName":"21"});
            var Q66;
            Q66=makeQuery(id+"F31.opPattern","COPY",BODY,{"derivedFrom":makeQuery(id+"F3.opExtrude","SWEPT_BODY",BODY,{"disambiguationData":[OSD([sQuery(id+"F1.wireOp",EDGE,"E9.0.44.0")])]}),"instanceName":"3"});
            var Q67;
            Q67=makeQuery(id+"F34.opPattern","COPY",BODY,{"derivedFrom":makeQuery(id+"F3.opExtrude","SWEPT_BODY",BODY,{"disambiguationData":[OSD([sQuery(id+"F1.wireOp",EDGE,"E9.0.40.0")])]}),"instanceName":"24"});
            var Q68;
            Q68=makeQuery(id+"F35.opPattern","COPY",BODY,{"derivedFrom":makeQuery(id+"F3.opExtrude","SWEPT_BODY",BODY,{"disambiguationData":[OSD([sQuery(id+"F1.wireOp",EDGE,"E9.0.38.0")])]}),"instanceName":"25"});
            var Q69;
            Q69=makeQuery(id+"F37.opPattern","COPY",BODY,{"derivedFrom":makeQuery(id+"F3.opExtrude","SWEPT_BODY",BODY,{"disambiguationData":[OSD([sQuery(id+"F1.wireOp",EDGE,"E9.0.36.0")])]}),"instanceName":"11"});
            var Q70;
            Q70=makeQuery(id+"F35.opPattern","COPY",BODY,{"derivedFrom":makeQuery(id+"F3.opExtrude","SWEPT_BODY",BODY,{"disambiguationData":[OSD([sQuery(id+"F1.wireOp",EDGE,"E9.0.39.0")])]}),"instanceName":"20"});
            var Q71;
            Q71=makeQuery(id+"F34.opPattern","COPY",BODY,{"derivedFrom":makeQuery(id+"F3.opExtrude","SWEPT_BODY",BODY,{"disambiguationData":[OSD([sQuery(id+"F1.wireOp",EDGE,"E9.0.40.0")])]}),"instanceName":"23"});
            var Q72;
            Q72=makeQuery(id+"F31.opPattern","COPY",BODY,{"derivedFrom":makeQuery(id+"F3.opExtrude","SWEPT_BODY",BODY,{"disambiguationData":[OSD([sQuery(id+"F1.wireOp",EDGE,"E9.0.44.0")])]}),"instanceName":"25"});
            var Q73;
            Q73=makeQuery(id+"F35.opPattern","COPY",BODY,{"derivedFrom":makeQuery(id+"F3.opExtrude","SWEPT_BODY",BODY,{"disambiguationData":[OSD([sQuery(id+"F1.wireOp",EDGE,"E9.0.39.0")])]}),"instanceName":"15"});
            var Q74;
            Q74=makeQuery(id+"F35.opPattern","COPY",BODY,{"derivedFrom":makeQuery(id+"F3.opExtrude","SWEPT_BODY",BODY,{"disambiguationData":[OSD([sQuery(id+"F1.wireOp",EDGE,"E9.0.38.0")])]}),"instanceName":"16"});
            var Q75;
            Q75=makeQuery(id+"F33.opPattern","COPY",BODY,{"derivedFrom":makeQuery(id+"F3.opExtrude","SWEPT_BODY",BODY,{"disambiguationData":[OSD([sQuery(id+"F1.wireOp",EDGE,"E9.0.41.0")])]}),"instanceName":"5"});
            var Q76;
            Q76=makeQuery(id+"F34.opPattern","COPY",BODY,{"derivedFrom":makeQuery(id+"F3.opExtrude","SWEPT_BODY",BODY,{"disambiguationData":[OSD([sQuery(id+"F1.wireOp",EDGE,"E9.0.40.0")])]}),"instanceName":"22"});
            var Q77;
            Q77=makeQuery(id+"F37.opPattern","COPY",BODY,{"derivedFrom":makeQuery(id+"F3.opExtrude","SWEPT_BODY",BODY,{"disambiguationData":[OSD([sQuery(id+"F1.wireOp",EDGE,"E9.0.35.0")])]}),"instanceName":"11"});
            var Q78;
            Q78=makeQuery(id+"F34.opPattern","COPY",BODY,{"derivedFrom":makeQuery(id+"F3.opExtrude","SWEPT_BODY",BODY,{"disambiguationData":[OSD([sQuery(id+"F1.wireOp",EDGE,"E9.0.40.0")])]}),"instanceName":"21"});
            var Q79;
            Q79=makeQuery(id+"F36.opPattern","COPY",BODY,{"derivedFrom":makeQuery(id+"F3.opExtrude","SWEPT_BODY",BODY,{"disambiguationData":[OSD([sQuery(id+"F1.wireOp",EDGE,"E9.0.37.0")])]}),"instanceName":"13"});
            var Q80;
            Q80=makeQuery(id+"F34.opPattern","COPY",BODY,{"derivedFrom":makeQuery(id+"F3.opExtrude","SWEPT_BODY",BODY,{"disambiguationData":[OSD([sQuery(id+"F1.wireOp",EDGE,"E9.0.40.0")])]}),"instanceName":"20"});
            var Q81;
            Q81=makeQuery(id+"F37.opPattern","COPY",BODY,{"derivedFrom":makeQuery(id+"F3.opExtrude","SWEPT_BODY",BODY,{"disambiguationData":[OSD([sQuery(id+"F1.wireOp",EDGE,"E9.0.36.0")])]}),"instanceName":"10"});
            var Q82;
            Q82=makeQuery(id+"F33.opPattern","COPY",BODY,{"derivedFrom":makeQuery(id+"F3.opExtrude","SWEPT_BODY",BODY,{"disambiguationData":[OSD([sQuery(id+"F1.wireOp",EDGE,"E9.0.42.0")])]}),"instanceName":"14"});
            var Q83;
            Q83=makeQuery(id+"F33.opPattern","COPY",BODY,{"derivedFrom":makeQuery(id+"F3.opExtrude","SWEPT_BODY",BODY,{"disambiguationData":[OSD([sQuery(id+"F1.wireOp",EDGE,"E9.0.41.0")])]}),"instanceName":"22"});
            var Q84;
            Q84=makeQuery(id+"F34.opPattern","COPY",BODY,{"derivedFrom":makeQuery(id+"F3.opExtrude","SWEPT_BODY",BODY,{"disambiguationData":[OSD([sQuery(id+"F1.wireOp",EDGE,"E9.0.40.0")])]}),"instanceName":"19"});
            var Q85;
            Q85=makeQuery(id+"F34.opPattern","COPY",BODY,{"derivedFrom":makeQuery(id+"F3.opExtrude","SWEPT_BODY",BODY,{"disambiguationData":[OSD([sQuery(id+"F1.wireOp",EDGE,"E9.0.40.0")])]}),"instanceName":"18"});
            var Q86;
            Q86=makeQuery(id+"F33.opPattern","COPY",BODY,{"derivedFrom":makeQuery(id+"F3.opExtrude","SWEPT_BODY",BODY,{"disambiguationData":[OSD([sQuery(id+"F1.wireOp",EDGE,"E9.0.41.0")])]}),"instanceName":"13"});
            var Q87;
            Q87=makeQuery(id+"F37.opPattern","COPY",BODY,{"derivedFrom":makeQuery(id+"F3.opExtrude","SWEPT_BODY",BODY,{"disambiguationData":[OSD([sQuery(id+"F1.wireOp",EDGE,"E9.0.35.0")])]}),"instanceName":"10"});
            var Q88;
            Q88=makeQuery(id+"F37.opPattern","COPY",BODY,{"derivedFrom":makeQuery(id+"F3.opExtrude","SWEPT_BODY",BODY,{"disambiguationData":[OSD([sQuery(id+"F1.wireOp",EDGE,"E9.0.36.0")])]}),"instanceName":"9"});
            var Q89;
            Q89=makeQuery(id+"F34.opPattern","COPY",BODY,{"derivedFrom":makeQuery(id+"F3.opExtrude","SWEPT_BODY",BODY,{"disambiguationData":[OSD([sQuery(id+"F1.wireOp",EDGE,"E9.0.40.0")])]}),"instanceName":"17"});
            var Q90;
            Q90=makeQuery(id+"F35.opPattern","COPY",BODY,{"derivedFrom":makeQuery(id+"F3.opExtrude","SWEPT_BODY",BODY,{"disambiguationData":[OSD([sQuery(id+"F1.wireOp",EDGE,"E9.0.39.0")])]}),"instanceName":"16"});
            var Q91;
            Q91=makeQuery(id+"F35.opPattern","COPY",BODY,{"derivedFrom":makeQuery(id+"F3.opExtrude","SWEPT_BODY",BODY,{"disambiguationData":[OSD([sQuery(id+"F1.wireOp",EDGE,"E9.0.38.0")])]}),"instanceName":"20"});
            var Q92;
            Q92=makeQuery(id+"F31.opPattern","COPY",BODY,{"derivedFrom":makeQuery(id+"F3.opExtrude","SWEPT_BODY",BODY,{"disambiguationData":[OSD([sQuery(id+"F1.wireOp",EDGE,"E9.0.44.0")])]}),"instanceName":"12"});
            var Q93;
            Q93=makeQuery(id+"F32.opPattern","COPY",BODY,{"derivedFrom":makeQuery(id+"F3.opExtrude","SWEPT_BODY",BODY,{"disambiguationData":[OSD([sQuery(id+"F1.wireOp",EDGE,"E9.0.43.0")])]}),"instanceName":"19"});
            var Q94;
            Q94=makeQuery(id+"F31.opPattern","COPY",BODY,{"derivedFrom":makeQuery(id+"F3.opExtrude","SWEPT_BODY",BODY,{"disambiguationData":[OSD([sQuery(id+"F1.wireOp",EDGE,"E9.0.45.0")])]}),"instanceName":"11"});
            var Q95;
            Q95=makeQuery(id+"F31.opPattern","COPY",BODY,{"derivedFrom":makeQuery(id+"F3.opExtrude","SWEPT_BODY",BODY,{"disambiguationData":[OSD([sQuery(id+"F1.wireOp",EDGE,"E9.0.44.0")])]}),"instanceName":"24"});
            var Q96;
            Q96=makeQuery(id+"F35.opPattern","COPY",BODY,{"derivedFrom":makeQuery(id+"F3.opExtrude","SWEPT_BODY",BODY,{"disambiguationData":[OSD([sQuery(id+"F1.wireOp",EDGE,"E9.0.38.0")])]}),"instanceName":"17"});
            var Q97;
            Q97=makeQuery(id+"F34.opPattern","COPY",BODY,{"derivedFrom":makeQuery(id+"F3.opExtrude","SWEPT_BODY",BODY,{"disambiguationData":[OSD([sQuery(id+"F1.wireOp",EDGE,"E9.0.40.0")])]}),"instanceName":"16"});
            var Q98;
            Q98=makeQuery(id+"F35.opPattern","COPY",BODY,{"derivedFrom":makeQuery(id+"F3.opExtrude","SWEPT_BODY",BODY,{"disambiguationData":[OSD([sQuery(id+"F1.wireOp",EDGE,"E9.0.39.0")])]}),"instanceName":"17"});
            var Q99;
            Q99=makeQuery(id+"F33.opPattern","COPY",BODY,{"derivedFrom":makeQuery(id+"F3.opExtrude","SWEPT_BODY",BODY,{"disambiguationData":[OSD([sQuery(id+"F1.wireOp",EDGE,"E9.0.42.0")])]}),"instanceName":"5"});
            var Q100;
            Q100=makeQuery(id+"F34.opPattern","COPY",BODY,{"derivedFrom":makeQuery(id+"F3.opExtrude","SWEPT_BODY",BODY,{"disambiguationData":[OSD([sQuery(id+"F1.wireOp",EDGE,"E9.0.40.0")])]}),"instanceName":"15"});
            var Q101;
            Q101=makeQuery(id+"F34.opPattern","COPY",BODY,{"derivedFrom":makeQuery(id+"F3.opExtrude","SWEPT_BODY",BODY,{"disambiguationData":[OSD([sQuery(id+"F1.wireOp",EDGE,"E9.0.40.0")])]}),"instanceName":"14"});
            var Q102;
            Q102=makeQuery(id+"F37.opPattern","COPY",BODY,{"derivedFrom":makeQuery(id+"F3.opExtrude","SWEPT_BODY",BODY,{"disambiguationData":[OSD([sQuery(id+"F1.wireOp",EDGE,"E9.0.35.0")])]}),"instanceName":"21"});
            var Q103;
            Q103=makeQuery(id+"F37.opPattern","COPY",BODY,{"derivedFrom":makeQuery(id+"F3.opExtrude","SWEPT_BODY",BODY,{"disambiguationData":[OSD([sQuery(id+"F1.wireOp",EDGE,"E9.0.35.0")])]}),"instanceName":"9"});
            var Q104;
            Q104=makeQuery(id+"F33.opPattern","COPY",BODY,{"derivedFrom":makeQuery(id+"F3.opExtrude","SWEPT_BODY",BODY,{"disambiguationData":[OSD([sQuery(id+"F1.wireOp",EDGE,"E9.0.42.0")])]}),"instanceName":"13"});
            var Q105;
            Q105=makeQuery(id+"F33.opPattern","COPY",BODY,{"derivedFrom":makeQuery(id+"F3.opExtrude","SWEPT_BODY",BODY,{"disambiguationData":[OSD([sQuery(id+"F1.wireOp",EDGE,"E9.0.42.0")])]}),"instanceName":"16"});
            var Q106;
            Q106=makeQuery(id+"F37.opPattern","COPY",BODY,{"derivedFrom":makeQuery(id+"F3.opExtrude","SWEPT_BODY",BODY,{"disambiguationData":[OSD([sQuery(id+"F1.wireOp",EDGE,"E9.0.36.0")])]}),"instanceName":"8"});
            var Q107;
            Q107=makeQuery(id+"F31.opPattern","COPY",BODY,{"derivedFrom":makeQuery(id+"F3.opExtrude","SWEPT_BODY",BODY,{"disambiguationData":[OSD([sQuery(id+"F1.wireOp",EDGE,"E9.0.45.0")])]}),"instanceName":"24"});
            var Q108;
            Q108=makeQuery(id+"F36.opPattern","COPY",BODY,{"derivedFrom":makeQuery(id+"F3.opExtrude","SWEPT_BODY",BODY,{"disambiguationData":[OSD([sQuery(id+"F1.wireOp",EDGE,"E9.0.37.0")])]}),"instanceName":"22"});
            var Q109;
            Q109=makeQuery(id+"F36.opPattern","COPY",BODY,{"derivedFrom":makeQuery(id+"F3.opExtrude","SWEPT_BODY",BODY,{"disambiguationData":[OSD([sQuery(id+"F1.wireOp",EDGE,"E9.0.37.0")])]}),"instanceName":"23"});
            var Q110;
            Q110=makeQuery(id+"F37.opPattern","COPY",BODY,{"derivedFrom":makeQuery(id+"F3.opExtrude","SWEPT_BODY",BODY,{"disambiguationData":[OSD([sQuery(id+"F1.wireOp",EDGE,"E9.0.35.0")])]}),"instanceName":"8"});
            var Q111;
            Q111=makeQuery(id+"F37.opPattern","COPY",BODY,{"derivedFrom":makeQuery(id+"F3.opExtrude","SWEPT_BODY",BODY,{"disambiguationData":[OSD([sQuery(id+"F1.wireOp",EDGE,"E9.0.36.0")])]}),"instanceName":"7"});
            var Q112;
            Q112=makeQuery(id+"F33.opPattern","COPY",BODY,{"derivedFrom":makeQuery(id+"F3.opExtrude","SWEPT_BODY",BODY,{"disambiguationData":[OSD([sQuery(id+"F1.wireOp",EDGE,"E9.0.42.0")])]}),"instanceName":"15"});
            var Q113;
            Q113=makeQuery(id+"F36.opPattern","COPY",BODY,{"derivedFrom":makeQuery(id+"F3.opExtrude","SWEPT_BODY",BODY,{"disambiguationData":[OSD([sQuery(id+"F1.wireOp",EDGE,"E9.0.37.0")])]}),"instanceName":"24"});
            var Q114;
            Q114=makeQuery(id+"F31.opPattern","COPY",BODY,{"derivedFrom":makeQuery(id+"F3.opExtrude","SWEPT_BODY",BODY,{"disambiguationData":[OSD([sQuery(id+"F1.wireOp",EDGE,"E9.0.44.0")])]}),"instanceName":"11"});
            var Q115;
            Q115=makeQuery(id+"F36.opPattern","COPY",BODY,{"derivedFrom":makeQuery(id+"F3.opExtrude","SWEPT_BODY",BODY,{"disambiguationData":[OSD([sQuery(id+"F1.wireOp",EDGE,"E9.0.37.0")])]}),"instanceName":"1"});
            var Q116;
            Q116=makeQuery(id+"F36.opPattern","COPY",BODY,{"derivedFrom":makeQuery(id+"F3.opExtrude","SWEPT_BODY",BODY,{"disambiguationData":[OSD([sQuery(id+"F1.wireOp",EDGE,"E9.0.37.0")])]}),"instanceName":"25"});
            var Q117;
            Q117=makeQuery(id+"F36.opPattern","COPY",BODY,{"derivedFrom":makeQuery(id+"F3.opExtrude","SWEPT_BODY",BODY,{"disambiguationData":[OSD([sQuery(id+"F1.wireOp",EDGE,"E9.0.37.0")])]}),"instanceName":"26"});
            var Q118;
            Q118=makeQuery(id+"F36.opPattern","COPY",BODY,{"derivedFrom":makeQuery(id+"F3.opExtrude","SWEPT_BODY",BODY,{"disambiguationData":[OSD([sQuery(id+"F1.wireOp",EDGE,"E9.0.37.0")])]}),"instanceName":"2"});
            var Q119;
            Q119=makeQuery(id+"F31.opPattern","COPY",BODY,{"derivedFrom":makeQuery(id+"F3.opExtrude","SWEPT_BODY",BODY,{"disambiguationData":[OSD([sQuery(id+"F1.wireOp",EDGE,"E9.0.45.0")])]}),"instanceName":"10"});
            var Q120;
            Q120=makeQuery(id+"F35.opPattern","COPY",BODY,{"derivedFrom":makeQuery(id+"F3.opExtrude","SWEPT_BODY",BODY,{"disambiguationData":[OSD([sQuery(id+"F1.wireOp",EDGE,"E9.0.38.0")])]}),"instanceName":"18"});
            var Q121;
            Q121=makeQuery(id+"F35.opPattern","COPY",BODY,{"derivedFrom":makeQuery(id+"F3.opExtrude","SWEPT_BODY",BODY,{"disambiguationData":[OSD([sQuery(id+"F1.wireOp",EDGE,"E9.0.39.0")])]}),"instanceName":"18"});
            var Q122;
            Q122=makeQuery(id+"F37.opPattern","COPY",BODY,{"derivedFrom":makeQuery(id+"F3.opExtrude","SWEPT_BODY",BODY,{"disambiguationData":[OSD([sQuery(id+"F1.wireOp",EDGE,"E9.0.35.0")])]}),"instanceName":"7"});
            var Q123;
            Q123=makeQuery(id+"F34.opPattern","COPY",BODY,{"derivedFrom":makeQuery(id+"F3.opExtrude","SWEPT_BODY",BODY,{"disambiguationData":[OSD([sQuery(id+"F1.wireOp",EDGE,"E9.0.40.0")])]}),"instanceName":"13"});
            var Q124;
            Q124=makeQuery(id+"F36.opPattern","COPY",BODY,{"derivedFrom":makeQuery(id+"F3.opExtrude","SWEPT_BODY",BODY,{"disambiguationData":[OSD([sQuery(id+"F1.wireOp",EDGE,"E9.0.37.0")])]}),"instanceName":"27"});
            var Q125;
            Q125=makeQuery(id+"F33.opPattern","COPY",BODY,{"derivedFrom":makeQuery(id+"F3.opExtrude","SWEPT_BODY",BODY,{"disambiguationData":[OSD([sQuery(id+"F1.wireOp",EDGE,"E9.0.41.0")])]}),"instanceName":"12"});
            var Q126;
            Q126=makeQuery(id+"F34.opPattern","COPY",BODY,{"derivedFrom":makeQuery(id+"F3.opExtrude","SWEPT_BODY",BODY,{"disambiguationData":[OSD([sQuery(id+"F1.wireOp",EDGE,"E9.0.40.0")])]}),"instanceName":"12"});
            var Q127;
            Q127=makeQuery(id+"F37.opPattern","COPY",BODY,{"derivedFrom":makeQuery(id+"F3.opExtrude","SWEPT_BODY",BODY,{"disambiguationData":[OSD([sQuery(id+"F1.wireOp",EDGE,"E9.0.36.0")])]}),"instanceName":"6"});
            var Q128;
            Q128=makeQuery(id+"F33.opPattern","COPY",BODY,{"derivedFrom":makeQuery(id+"F3.opExtrude","SWEPT_BODY",BODY,{"disambiguationData":[OSD([sQuery(id+"F1.wireOp",EDGE,"E9.0.41.0")])]}),"instanceName":"6"});
            var Q129;
            Q129=makeQuery(id+"F37.opPattern","COPY",BODY,{"derivedFrom":makeQuery(id+"F3.opExtrude","SWEPT_BODY",BODY,{"disambiguationData":[OSD([sQuery(id+"F1.wireOp",EDGE,"E9.0.35.0")])]}),"instanceName":"6"});
            var Q130;
            Q130=makeQuery(id+"F31.opPattern","COPY",BODY,{"derivedFrom":makeQuery(id+"F3.opExtrude","SWEPT_BODY",BODY,{"disambiguationData":[OSD([sQuery(id+"F1.wireOp",EDGE,"E9.0.44.0")])]}),"instanceName":"10"});
            var Q131;
            Q131=makeQuery(id+"F34.opPattern","COPY",BODY,{"derivedFrom":makeQuery(id+"F3.opExtrude","SWEPT_BODY",BODY,{"disambiguationData":[OSD([sQuery(id+"F1.wireOp",EDGE,"E9.0.40.0")])]}),"instanceName":"11"});
            var Q132;
            Q132=makeQuery(id+"F36.opPattern","COPY",BODY,{"derivedFrom":makeQuery(id+"F3.opExtrude","SWEPT_BODY",BODY,{"disambiguationData":[OSD([sQuery(id+"F1.wireOp",EDGE,"E9.0.37.0")])]}),"instanceName":"28"});
            var Q133;
            Q133=makeQuery(id+"F32.opPattern","COPY",BODY,{"derivedFrom":makeQuery(id+"F3.opExtrude","SWEPT_BODY",BODY,{"disambiguationData":[OSD([sQuery(id+"F1.wireOp",EDGE,"E9.0.43.0")])]}),"instanceName":"20"});
            var Q134;
            Q134=makeQuery(id+"F31.opPattern","COPY",BODY,{"derivedFrom":makeQuery(id+"F3.opExtrude","SWEPT_BODY",BODY,{"disambiguationData":[OSD([sQuery(id+"F1.wireOp",EDGE,"E9.0.44.0")])]}),"instanceName":"23"});
            var Q135;
            Q135=makeQuery(id+"F36.opPattern","COPY",BODY,{"derivedFrom":makeQuery(id+"F3.opExtrude","SWEPT_BODY",BODY,{"disambiguationData":[OSD([sQuery(id+"F1.wireOp",EDGE,"E9.0.37.0")])]}),"instanceName":"3"});
            var Q136;
            Q136=makeQuery(id+"F35.opPattern","COPY",BODY,{"derivedFrom":makeQuery(id+"F3.opExtrude","SWEPT_BODY",BODY,{"disambiguationData":[OSD([sQuery(id+"F1.wireOp",EDGE,"E9.0.38.0")])]}),"instanceName":"19"});
            var Q137;
            Q137=makeQuery(id+"F33.opPattern","COPY",BODY,{"derivedFrom":makeQuery(id+"F3.opExtrude","SWEPT_BODY",BODY,{"disambiguationData":[OSD([sQuery(id+"F1.wireOp",EDGE,"E9.0.42.0")])]}),"instanceName":"6"});
            var Q138;
            Q138=makeQuery(id+"F35.opPattern","COPY",BODY,{"derivedFrom":makeQuery(id+"F3.opExtrude","SWEPT_BODY",BODY,{"disambiguationData":[OSD([sQuery(id+"F1.wireOp",EDGE,"E9.0.39.0")])]}),"instanceName":"19"});
            var Q139;
            Q139=makeQuery(id+"F33.opPattern","COPY",BODY,{"derivedFrom":makeQuery(id+"F3.opExtrude","SWEPT_BODY",BODY,{"disambiguationData":[OSD([sQuery(id+"F1.wireOp",EDGE,"E9.0.42.0")])]}),"instanceName":"10"});
            var Q140;
            Q140=makeQuery(id+"F34.opPattern","COPY",BODY,{"derivedFrom":makeQuery(id+"F3.opExtrude","SWEPT_BODY",BODY,{"disambiguationData":[OSD([sQuery(id+"F1.wireOp",EDGE,"E9.0.40.0")])]}),"instanceName":"10"});
            var Q141;
            Q141=makeQuery(id+"F34.opPattern","COPY",BODY,{"derivedFrom":makeQuery(id+"F3.opExtrude","SWEPT_BODY",BODY,{"disambiguationData":[OSD([sQuery(id+"F1.wireOp",EDGE,"E9.0.40.0")])]}),"instanceName":"9"});
            var Q142;
            Q142=makeQuery(id+"F34.opPattern","COPY",BODY,{"derivedFrom":makeQuery(id+"F3.opExtrude","SWEPT_BODY",BODY,{"disambiguationData":[OSD([sQuery(id+"F1.wireOp",EDGE,"E9.0.40.0")])]}),"instanceName":"8"});
            var Q143;
            Q143=makeQuery(id+"F33.opPattern","COPY",BODY,{"derivedFrom":makeQuery(id+"F3.opExtrude","SWEPT_BODY",BODY,{"disambiguationData":[OSD([sQuery(id+"F1.wireOp",EDGE,"E9.0.41.0")])]}),"instanceName":"7"});
            var Q144;
            Q144=makeQuery(id+"F35.opPattern","COPY",BODY,{"derivedFrom":makeQuery(id+"F3.opExtrude","SWEPT_BODY",BODY,{"disambiguationData":[OSD([sQuery(id+"F1.wireOp",EDGE,"E9.0.38.0")])]}),"instanceName":"29"});
            var Q145;
            Q145=makeQuery(id+"F36.opPattern","COPY",BODY,{"derivedFrom":makeQuery(id+"F3.opExtrude","SWEPT_BODY",BODY,{"disambiguationData":[OSD([sQuery(id+"F1.wireOp",EDGE,"E9.0.37.0")])]}),"instanceName":"30"});
            var Q146;
            Q146=makeQuery(id+"F37.opPattern","COPY",BODY,{"derivedFrom":makeQuery(id+"F3.opExtrude","SWEPT_BODY",BODY,{"disambiguationData":[OSD([sQuery(id+"F1.wireOp",EDGE,"E9.0.36.0")])]}),"instanceName":"5"});
            var Q147;
            Q147=makeQuery(id+"F32.opPattern","COPY",BODY,{"derivedFrom":makeQuery(id+"F3.opExtrude","SWEPT_BODY",BODY,{"disambiguationData":[OSD([sQuery(id+"F1.wireOp",EDGE,"E9.0.43.0")])]}),"instanceName":"13"});
            var Q148;
            Q148=makeQuery(id+"F32.opPattern","COPY",BODY,{"derivedFrom":makeQuery(id+"F3.opExtrude","SWEPT_BODY",BODY,{"disambiguationData":[OSD([sQuery(id+"F1.wireOp",EDGE,"E9.0.43.0")])]}),"instanceName":"18"});
            var Q149;
            Q149=makeQuery(id+"F34.opPattern","COPY",BODY,{"derivedFrom":makeQuery(id+"F3.opExtrude","SWEPT_BODY",BODY,{"disambiguationData":[OSD([sQuery(id+"F1.wireOp",EDGE,"E9.0.40.0")])]}),"instanceName":"7"});
            var Q150;
            Q150=makeQuery(id+"F37.opPattern","COPY",BODY,{"derivedFrom":makeQuery(id+"F3.opExtrude","SWEPT_BODY",BODY,{"disambiguationData":[OSD([sQuery(id+"F1.wireOp",EDGE,"E9.0.35.0")])]}),"instanceName":"5"});
            var Q151;
            Q151=makeQuery(id+"F31.opPattern","COPY",BODY,{"derivedFrom":makeQuery(id+"F3.opExtrude","SWEPT_BODY",BODY,{"disambiguationData":[OSD([sQuery(id+"F1.wireOp",EDGE,"E9.0.45.0")])]}),"instanceName":"9"});
            var Q152;
            Q152=makeQuery(id+"F37.opPattern","COPY",BODY,{"derivedFrom":makeQuery(id+"F3.opExtrude","SWEPT_BODY",BODY,{"disambiguationData":[OSD([sQuery(id+"F1.wireOp",EDGE,"E9.0.35.0")])]}),"instanceName":"30"});
            var Q153;
            Q153=makeQuery(id+"F37.opPattern","COPY",BODY,{"derivedFrom":makeQuery(id+"F3.opExtrude","SWEPT_BODY",BODY,{"disambiguationData":[OSD([sQuery(id+"F1.wireOp",EDGE,"E9.0.36.0")])]}),"instanceName":"30"});
            var Q154;
            Q154=makeQuery(id+"F32.opPattern","COPY",BODY,{"derivedFrom":makeQuery(id+"F3.opExtrude","SWEPT_BODY",BODY,{"disambiguationData":[OSD([sQuery(id+"F1.wireOp",EDGE,"E9.0.43.0")])]}),"instanceName":"16"});
            var Q155;
            Q155=makeQuery(id+"F31.opPattern","COPY",BODY,{"derivedFrom":makeQuery(id+"F3.opExtrude","SWEPT_BODY",BODY,{"disambiguationData":[OSD([sQuery(id+"F1.wireOp",EDGE,"E9.0.44.0")])]}),"instanceName":"20"});
            var Q156;
            Q156=makeQuery(id+"F32.opPattern","COPY",BODY,{"derivedFrom":makeQuery(id+"F3.opExtrude","SWEPT_BODY",BODY,{"disambiguationData":[OSD([sQuery(id+"F1.wireOp",EDGE,"E9.0.43.0")])]}),"instanceName":"14"});
            var Q157;
            Q157=makeQuery(id+"F33.opPattern","COPY",BODY,{"derivedFrom":makeQuery(id+"F3.opExtrude","SWEPT_BODY",BODY,{"disambiguationData":[OSD([sQuery(id+"F1.wireOp",EDGE,"E9.0.42.0")])]}),"instanceName":"7"});
            var Q158;
            Q158=makeQuery(id+"F31.opPattern","COPY",BODY,{"derivedFrom":makeQuery(id+"F3.opExtrude","SWEPT_BODY",BODY,{"disambiguationData":[OSD([sQuery(id+"F1.wireOp",EDGE,"E9.0.45.0")])]}),"instanceName":"19"});
            var Q159;
            Q159=makeQuery(id+"F32.opPattern","COPY",BODY,{"derivedFrom":makeQuery(id+"F3.opExtrude","SWEPT_BODY",BODY,{"disambiguationData":[OSD([sQuery(id+"F1.wireOp",EDGE,"E9.0.43.0")])]}),"instanceName":"12"});
            var Q160;
            Q160=makeQuery(id+"F33.opPattern","COPY",BODY,{"derivedFrom":makeQuery(id+"F3.opExtrude","SWEPT_BODY",BODY,{"disambiguationData":[OSD([sQuery(id+"F1.wireOp",EDGE,"E9.0.41.0")])]}),"instanceName":"17"});
            var Q161;
            Q161=makeQuery(id+"F37.opPattern","COPY",BODY,{"derivedFrom":makeQuery(id+"F3.opExtrude","SWEPT_BODY",BODY,{"disambiguationData":[OSD([sQuery(id+"F1.wireOp",EDGE,"E9.0.36.0")])]}),"instanceName":"21"});
            var Q162;
            Q162=makeQuery(id+"F32.opPattern","COPY",BODY,{"derivedFrom":makeQuery(id+"F3.opExtrude","SWEPT_BODY",BODY,{"disambiguationData":[OSD([sQuery(id+"F1.wireOp",EDGE,"E9.0.43.0")])]}),"instanceName":"11"});
            var Q163;
            Q163=makeQuery(id+"F31.opPattern","COPY",BODY,{"derivedFrom":makeQuery(id+"F3.opExtrude","SWEPT_BODY",BODY,{"disambiguationData":[OSD([sQuery(id+"F1.wireOp",EDGE,"E9.0.44.0")])]}),"instanceName":"19"});
            var Q164;
            Q164=makeQuery(id+"F37.opPattern","COPY",BODY,{"derivedFrom":makeQuery(id+"F3.opExtrude","SWEPT_BODY",BODY,{"disambiguationData":[OSD([sQuery(id+"F1.wireOp",EDGE,"E9.0.36.0")])]}),"instanceName":"29"});
            var Q165;
            Q165=makeQuery(id+"F33.opPattern","COPY",BODY,{"derivedFrom":makeQuery(id+"F3.opExtrude","SWEPT_BODY",BODY,{"disambiguationData":[OSD([sQuery(id+"F1.wireOp",EDGE,"E9.0.41.0")])]}),"instanceName":"8"});
            var Q166;
            Q166=makeQuery(id+"F31.opPattern","COPY",BODY,{"derivedFrom":makeQuery(id+"F3.opExtrude","SWEPT_BODY",BODY,{"disambiguationData":[OSD([sQuery(id+"F1.wireOp",EDGE,"E9.0.45.0")])]}),"instanceName":"4"});
            var Q167;
            Q167=makeQuery(id+"F33.opPattern","COPY",BODY,{"derivedFrom":makeQuery(id+"F3.opExtrude","SWEPT_BODY",BODY,{"disambiguationData":[OSD([sQuery(id+"F1.wireOp",EDGE,"E9.0.42.0")])]}),"instanceName":"8"});
            var Q168;
            Q168=makeQuery(id+"F35.opPattern","COPY",BODY,{"derivedFrom":makeQuery(id+"F3.opExtrude","SWEPT_BODY",BODY,{"disambiguationData":[OSD([sQuery(id+"F1.wireOp",EDGE,"E9.0.38.0")])]}),"instanceName":"28"});
            var Q169;
            Q169=makeQuery(id+"F37.opPattern","COPY",BODY,{"derivedFrom":makeQuery(id+"F3.opExtrude","SWEPT_BODY",BODY,{"disambiguationData":[OSD([sQuery(id+"F1.wireOp",EDGE,"E9.0.35.0")])]}),"instanceName":"29"});
            var Q170;
            Q170=makeQuery(id+"F32.opPattern","COPY",BODY,{"derivedFrom":makeQuery(id+"F3.opExtrude","SWEPT_BODY",BODY,{"disambiguationData":[OSD([sQuery(id+"F1.wireOp",EDGE,"E9.0.43.0")])]}),"instanceName":"10"});
            var Q171;
            Q171=makeQuery(id+"F32.opPattern","COPY",BODY,{"derivedFrom":makeQuery(id+"F3.opExtrude","SWEPT_BODY",BODY,{"disambiguationData":[OSD([sQuery(id+"F1.wireOp",EDGE,"E9.0.43.0")])]}),"instanceName":"9"});
            var Q172;
            Q172=makeQuery(id+"F32.opPattern","COPY",BODY,{"derivedFrom":makeQuery(id+"F3.opExtrude","SWEPT_BODY",BODY,{"disambiguationData":[OSD([sQuery(id+"F1.wireOp",EDGE,"E9.0.43.0")])]}),"instanceName":"8"});
            var Q173;
            Q173=makeQuery(id+"F33.opPattern","COPY",BODY,{"derivedFrom":makeQuery(id+"F3.opExtrude","SWEPT_BODY",BODY,{"disambiguationData":[OSD([sQuery(id+"F1.wireOp",EDGE,"E9.0.42.0")])]}),"instanceName":"19"});
            var Q174;
            Q174=makeQuery(id+"F33.opPattern","COPY",BODY,{"derivedFrom":makeQuery(id+"F3.opExtrude","SWEPT_BODY",BODY,{"disambiguationData":[OSD([sQuery(id+"F1.wireOp",EDGE,"E9.0.42.0")])]}),"instanceName":"12"});
            var Q175;
            Q175=makeQuery(id+"F35.opPattern","COPY",BODY,{"derivedFrom":makeQuery(id+"F3.opExtrude","SWEPT_BODY",BODY,{"disambiguationData":[OSD([sQuery(id+"F1.wireOp",EDGE,"E9.0.39.0")])]}),"instanceName":"27"});
            var Q176;
            Q176=makeQuery(id+"F37.opPattern","COPY",BODY,{"derivedFrom":makeQuery(id+"F3.opExtrude","SWEPT_BODY",BODY,{"disambiguationData":[OSD([sQuery(id+"F1.wireOp",EDGE,"E9.0.36.0")])]}),"instanceName":"28"});
            var Q177;
            Q177=makeQuery(id+"F37.opPattern","COPY",BODY,{"derivedFrom":makeQuery(id+"F3.opExtrude","SWEPT_BODY",BODY,{"disambiguationData":[OSD([sQuery(id+"F1.wireOp",EDGE,"E9.0.35.0")])]}),"instanceName":"28"});
            var Q178;
            Q178=makeQuery(id+"F32.opPattern","COPY",BODY,{"derivedFrom":makeQuery(id+"F3.opExtrude","SWEPT_BODY",BODY,{"disambiguationData":[OSD([sQuery(id+"F1.wireOp",EDGE,"E9.0.43.0")])]}),"instanceName":"7"});
            var Q179;
            Q179=makeQuery(id+"F32.opPattern","COPY",BODY,{"derivedFrom":makeQuery(id+"F3.opExtrude","SWEPT_BODY",BODY,{"disambiguationData":[OSD([sQuery(id+"F1.wireOp",EDGE,"E9.0.43.0")])]}),"instanceName":"6"});
            var Q180;
            Q180=makeQuery(id+"F35.opPattern","COPY",BODY,{"derivedFrom":makeQuery(id+"F3.opExtrude","SWEPT_BODY",BODY,{"disambiguationData":[OSD([sQuery(id+"F1.wireOp",EDGE,"E9.0.38.0")])]}),"instanceName":"27"});
            var Q181;
            Q181=makeQuery(id+"F35.opPattern","COPY",BODY,{"derivedFrom":makeQuery(id+"F3.opExtrude","SWEPT_BODY",BODY,{"disambiguationData":[OSD([sQuery(id+"F1.wireOp",EDGE,"E9.0.39.0")])]}),"instanceName":"29"});
            var Q182;
            Q182=makeQuery(id+"F37.opPattern","COPY",BODY,{"derivedFrom":makeQuery(id+"F3.opExtrude","SWEPT_BODY",BODY,{"disambiguationData":[OSD([sQuery(id+"F1.wireOp",EDGE,"E9.0.35.0")])]}),"instanceName":"4"});
            var Q183;
            Q183=makeQuery(id+"F37.opPattern","COPY",BODY,{"derivedFrom":makeQuery(id+"F3.opExtrude","SWEPT_BODY",BODY,{"disambiguationData":[OSD([sQuery(id+"F1.wireOp",EDGE,"E9.0.36.0")])]}),"instanceName":"4"});
            var Q184;
            Q184=makeQuery(id+"F33.opPattern","COPY",BODY,{"derivedFrom":makeQuery(id+"F3.opExtrude","SWEPT_BODY",BODY,{"disambiguationData":[OSD([sQuery(id+"F1.wireOp",EDGE,"E9.0.41.0")])]}),"instanceName":"9"});
            var Q185;
            Q185=makeQuery(id+"F37.opPattern","COPY",BODY,{"derivedFrom":makeQuery(id+"F3.opExtrude","SWEPT_BODY",BODY,{"disambiguationData":[OSD([sQuery(id+"F1.wireOp",EDGE,"E9.0.36.0")])]}),"instanceName":"27"});
            var Q186;
            Q186=makeQuery(id+"F32.opPattern","COPY",BODY,{"derivedFrom":makeQuery(id+"F3.opExtrude","SWEPT_BODY",BODY,{"disambiguationData":[OSD([sQuery(id+"F1.wireOp",EDGE,"E9.0.43.0")])]}),"instanceName":"5"});
            var Q187;
            Q187=makeQuery(id+"F37.opPattern","COPY",BODY,{"derivedFrom":makeQuery(id+"F3.opExtrude","SWEPT_BODY",BODY,{"disambiguationData":[OSD([sQuery(id+"F1.wireOp",EDGE,"E9.0.36.0")])]}),"instanceName":"1"});
            var Q188;
            Q188=makeQuery(id+"F37.opPattern","COPY",BODY,{"derivedFrom":makeQuery(id+"F3.opExtrude","SWEPT_BODY",BODY,{"disambiguationData":[OSD([sQuery(id+"F1.wireOp",EDGE,"E9.0.35.0")])]}),"instanceName":"27"});
            var Q189;
            Q189=makeQuery(id+"F37.opPattern","COPY",BODY,{"derivedFrom":makeQuery(id+"F3.opExtrude","SWEPT_BODY",BODY,{"disambiguationData":[OSD([sQuery(id+"F1.wireOp",EDGE,"E9.0.36.0")])]}),"instanceName":"26"});
            var Q190;
            Q190=makeQuery(id+"F32.opPattern","COPY",BODY,{"derivedFrom":makeQuery(id+"F3.opExtrude","SWEPT_BODY",BODY,{"disambiguationData":[OSD([sQuery(id+"F1.wireOp",EDGE,"E9.0.43.0")])]}),"instanceName":"4"});
            var Q191;
            Q191=makeQuery(id+"F37.opPattern","COPY",BODY,{"derivedFrom":makeQuery(id+"F3.opExtrude","SWEPT_BODY",BODY,{"disambiguationData":[OSD([sQuery(id+"F1.wireOp",EDGE,"E9.0.35.0")])]}),"instanceName":"26"});
            var Q192;
            Q192=makeQuery(id+"F35.opPattern","COPY",BODY,{"derivedFrom":makeQuery(id+"F3.opExtrude","SWEPT_BODY",BODY,{"disambiguationData":[OSD([sQuery(id+"F1.wireOp",EDGE,"E9.0.39.0")])]}),"instanceName":"26"});
            var Q193;
            Q193=makeQuery(id+"F32.opPattern","COPY",BODY,{"derivedFrom":makeQuery(id+"F3.opExtrude","SWEPT_BODY",BODY,{"disambiguationData":[OSD([sQuery(id+"F1.wireOp",EDGE,"E9.0.43.0")])]}),"instanceName":"3"});
            var Q194;
            Q194=makeQuery(id+"F33.opPattern","COPY",BODY,{"derivedFrom":makeQuery(id+"F3.opExtrude","SWEPT_BODY",BODY,{"disambiguationData":[OSD([sQuery(id+"F1.wireOp",EDGE,"E9.0.42.0")])]}),"instanceName":"9"});
            var Q195;
            Q195=makeQuery(id+"F37.opPattern","COPY",BODY,{"derivedFrom":makeQuery(id+"F3.opExtrude","SWEPT_BODY",BODY,{"disambiguationData":[OSD([sQuery(id+"F1.wireOp",EDGE,"E9.0.35.0")])]}),"instanceName":"2"});
            var Q196;
            Q196=makeQuery(id+"F34.opPattern","COPY",BODY,{"derivedFrom":makeQuery(id+"F3.opExtrude","SWEPT_BODY",BODY,{"disambiguationData":[OSD([sQuery(id+"F1.wireOp",EDGE,"E9.0.40.0")])]}),"instanceName":"6"});
            var Q197;
            Q197=makeQuery(id+"F36.opPattern","COPY",BODY,{"derivedFrom":makeQuery(id+"F3.opExtrude","SWEPT_BODY",BODY,{"disambiguationData":[OSD([sQuery(id+"F1.wireOp",EDGE,"E9.0.37.0")])]}),"instanceName":"20"});
            var Q198;
            Q198=makeQuery(id+"F33.opPattern","COPY",BODY,{"derivedFrom":makeQuery(id+"F3.opExtrude","SWEPT_BODY",BODY,{"disambiguationData":[OSD([sQuery(id+"F1.wireOp",EDGE,"E9.0.41.0")])]}),"instanceName":"19"});
            var Q199;
            Q199=makeQuery(id+"F32.opPattern","COPY",BODY,{"derivedFrom":makeQuery(id+"F3.opExtrude","SWEPT_BODY",BODY,{"disambiguationData":[OSD([sQuery(id+"F1.wireOp",EDGE,"E9.0.43.0")])]}),"instanceName":"2"});
            var Q200;
            Q200=makeQuery(id+"F33.opPattern","COPY",BODY,{"derivedFrom":makeQuery(id+"F3.opExtrude","SWEPT_BODY",BODY,{"disambiguationData":[OSD([sQuery(id+"F1.wireOp",EDGE,"E9.0.41.0")])]}),"instanceName":"20"});
            var Q201;
            Q201=makeQuery(id+"F33.opPattern","COPY",BODY,{"derivedFrom":makeQuery(id+"F3.opExtrude","SWEPT_BODY",BODY,{"disambiguationData":[OSD([sQuery(id+"F1.wireOp",EDGE,"E9.0.42.0")])]}),"instanceName":"20"});
            var Q202;
            Q202=makeQuery(id+"F37.opPattern","COPY",BODY,{"derivedFrom":makeQuery(id+"F3.opExtrude","SWEPT_BODY",BODY,{"disambiguationData":[OSD([sQuery(id+"F1.wireOp",EDGE,"E9.0.36.0")])]}),"instanceName":"22"});
            var Q203;
            Q203=makeQuery(id+"F37.opPattern","COPY",BODY,{"derivedFrom":makeQuery(id+"F3.opExtrude","SWEPT_BODY",BODY,{"disambiguationData":[OSD([sQuery(id+"F1.wireOp",EDGE,"E9.0.36.0")])]}),"instanceName":"25"});
            var Q204;
            Q204=makeQuery(id+"F36.opPattern","COPY",BODY,{"derivedFrom":makeQuery(id+"F3.opExtrude","SWEPT_BODY",BODY,{"disambiguationData":[OSD([sQuery(id+"F1.wireOp",EDGE,"E9.0.37.0")])]}),"instanceName":"19"});
            var Q205;
            Q205=makeQuery(id+"F37.opPattern","COPY",BODY,{"derivedFrom":makeQuery(id+"F3.opExtrude","SWEPT_BODY",BODY,{"disambiguationData":[OSD([sQuery(id+"F1.wireOp",EDGE,"E9.0.35.0")])]}),"instanceName":"25"});
            var Q206;
            Q206=makeQuery(id+"F31.opPattern","COPY",BODY,{"derivedFrom":makeQuery(id+"F3.opExtrude","SWEPT_BODY",BODY,{"disambiguationData":[OSD([sQuery(id+"F1.wireOp",EDGE,"E9.0.45.0")])]}),"instanceName":"23"});
            var Q207;
            Q207=makeQuery(id+"F36.opPattern","COPY",BODY,{"derivedFrom":makeQuery(id+"F3.opExtrude","SWEPT_BODY",BODY,{"disambiguationData":[OSD([sQuery(id+"F1.wireOp",EDGE,"E9.0.37.0")])]}),"instanceName":"14"});
            var Q208;
            Q208=makeQuery(id+"F37.opPattern","COPY",BODY,{"derivedFrom":makeQuery(id+"F3.opExtrude","SWEPT_BODY",BODY,{"disambiguationData":[OSD([sQuery(id+"F1.wireOp",EDGE,"E9.0.36.0")])]}),"instanceName":"24"});
            var Q209;
            Q209=makeQuery(id+"F35.opPattern","COPY",BODY,{"derivedFrom":makeQuery(id+"F3.opExtrude","SWEPT_BODY",BODY,{"disambiguationData":[OSD([sQuery(id+"F1.wireOp",EDGE,"E9.0.39.0")])]}),"instanceName":"25"});
            var Q210;
            Q210=makeQuery(id+"F33.opPattern","COPY",BODY,{"derivedFrom":makeQuery(id+"F3.opExtrude","SWEPT_BODY",BODY,{"disambiguationData":[OSD([sQuery(id+"F1.wireOp",EDGE,"E9.0.41.0")])]}),"instanceName":"10"});
            var Q211;
            Q211=makeQuery(id+"F37.opPattern","COPY",BODY,{"derivedFrom":makeQuery(id+"F3.opExtrude","SWEPT_BODY",BODY,{"disambiguationData":[OSD([sQuery(id+"F1.wireOp",EDGE,"E9.0.35.0")])]}),"instanceName":"1"});
            var Q212;
            Q212=makeQuery(id+"F35.opPattern","COPY",BODY,{"derivedFrom":makeQuery(id+"F3.opExtrude","SWEPT_BODY",BODY,{"disambiguationData":[OSD([sQuery(id+"F1.wireOp",EDGE,"E9.0.38.0")])]}),"instanceName":"5"});
            var Q213;
            Q213=makeQuery(id+"F35.opPattern","COPY",BODY,{"derivedFrom":makeQuery(id+"F3.opExtrude","SWEPT_BODY",BODY,{"disambiguationData":[OSD([sQuery(id+"F1.wireOp",EDGE,"E9.0.39.0")])]}),"instanceName":"5"});
            var Q214;
            Q214=makeQuery(id+"F36.opPattern","COPY",BODY,{"derivedFrom":makeQuery(id+"F3.opExtrude","SWEPT_BODY",BODY,{"disambiguationData":[OSD([sQuery(id+"F1.wireOp",EDGE,"E9.0.37.0")])]}),"instanceName":"4"});
            var Q215;
            Q215=makeQuery(id+"F33.opPattern","COPY",BODY,{"derivedFrom":makeQuery(id+"F3.opExtrude","SWEPT_BODY",BODY,{"disambiguationData":[OSD([sQuery(id+"F1.wireOp",EDGE,"E9.0.41.0")])]}),"instanceName":"11"});
            var Q216;
            Q216=makeQuery(id+"F33.opPattern","COPY",BODY,{"derivedFrom":makeQuery(id+"F3.opExtrude","SWEPT_BODY",BODY,{"disambiguationData":[OSD([sQuery(id+"F1.wireOp",EDGE,"E9.0.41.0")])]}),"instanceName":"16"});
            var Q217;
            Q217=makeQuery(id+"F31.opPattern","COPY",BODY,{"derivedFrom":makeQuery(id+"F3.opExtrude","SWEPT_BODY",BODY,{"disambiguationData":[OSD([sQuery(id+"F1.wireOp",EDGE,"E9.0.44.0")])]}),"instanceName":"22"});
            var Q218;
            Q218=makeQuery(id+"F33.opPattern","COPY",BODY,{"derivedFrom":makeQuery(id+"F3.opExtrude","SWEPT_BODY",BODY,{"disambiguationData":[OSD([sQuery(id+"F1.wireOp",EDGE,"E9.0.42.0")])]}),"instanceName":"22"});
            var Q219;
            Q219=makeQuery(id+"F31.opPattern","COPY",BODY,{"derivedFrom":makeQuery(id+"F3.opExtrude","SWEPT_BODY",BODY,{"disambiguationData":[OSD([sQuery(id+"F1.wireOp",EDGE,"E9.0.45.0")])]}),"instanceName":"21"});
            var Q220;
            Q220=makeQuery(id+"F33.opPattern","COPY",BODY,{"derivedFrom":makeQuery(id+"F3.opExtrude","SWEPT_BODY",BODY,{"disambiguationData":[OSD([sQuery(id+"F1.wireOp",EDGE,"E9.0.41.0")])]}),"instanceName":"23"});
            var Q221;
            Q221=makeQuery(id+"F33.opPattern","COPY",BODY,{"derivedFrom":makeQuery(id+"F3.opExtrude","SWEPT_BODY",BODY,{"disambiguationData":[OSD([sQuery(id+"F1.wireOp",EDGE,"E9.0.42.0")])]}),"instanceName":"23"});
            var Q222;
            Q222=makeQuery(id+"F37.opPattern","COPY",BODY,{"derivedFrom":makeQuery(id+"F3.opExtrude","SWEPT_BODY",BODY,{"disambiguationData":[OSD([sQuery(id+"F1.wireOp",EDGE,"E9.0.36.0")])]}),"instanceName":"20"});
            var Q223;
            Q223=makeQuery(id+"F31.opPattern","COPY",BODY,{"derivedFrom":makeQuery(id+"F3.opExtrude","SWEPT_BODY",BODY,{"disambiguationData":[OSD([sQuery(id+"F1.wireOp",EDGE,"E9.0.44.0")])]}),"instanceName":"21"});
            var Q224;
            Q224=makeQuery(id+"F36.opPattern","COPY",BODY,{"derivedFrom":makeQuery(id+"F3.opExtrude","SWEPT_BODY",BODY,{"disambiguationData":[OSD([sQuery(id+"F1.wireOp",EDGE,"E9.0.37.0")])]}),"instanceName":"5"});
            var Q225;
            Q225=makeQuery(id+"F36.opPattern","COPY",BODY,{"derivedFrom":makeQuery(id+"F3.opExtrude","SWEPT_BODY",BODY,{"disambiguationData":[OSD([sQuery(id+"F1.wireOp",EDGE,"E9.0.37.0")])]}),"instanceName":"6"});
            var Q226;
            Q226=makeQuery(id+"F31.opPattern","COPY",BODY,{"derivedFrom":makeQuery(id+"F3.opExtrude","SWEPT_BODY",BODY,{"disambiguationData":[OSD([sQuery(id+"F1.wireOp",EDGE,"E9.0.45.0")])]}),"instanceName":"20"});
            var Q227;
            Q227=makeQuery(id+"F31.opPattern","COPY",BODY,{"derivedFrom":makeQuery(id+"F3.opExtrude","SWEPT_BODY",BODY,{"disambiguationData":[OSD([sQuery(id+"F1.wireOp",EDGE,"E9.0.44.0")])]}),"instanceName":"17"});
            var Q228;
            Q228=makeQuery(id+"F31.opPattern","COPY",BODY,{"derivedFrom":makeQuery(id+"F3.opExtrude","SWEPT_BODY",BODY,{"disambiguationData":[OSD([sQuery(id+"F1.wireOp",EDGE,"E9.0.45.0")])]}),"instanceName":"16"});
            var Q229;
            Q229=makeQuery(id+"F33.opPattern","COPY",BODY,{"derivedFrom":makeQuery(id+"F3.opExtrude","SWEPT_BODY",BODY,{"disambiguationData":[OSD([sQuery(id+"F1.wireOp",EDGE,"E9.0.41.0")])]}),"instanceName":"24"});
            var Q230;
            Q230=makeQuery(id+"F33.opPattern","COPY",BODY,{"derivedFrom":makeQuery(id+"F3.opExtrude","SWEPT_BODY",BODY,{"disambiguationData":[OSD([sQuery(id+"F1.wireOp",EDGE,"E9.0.42.0")])]}),"instanceName":"24"});
            var Q231;
            Q231=makeQuery(id+"F36.opPattern","COPY",BODY,{"derivedFrom":makeQuery(id+"F3.opExtrude","SWEPT_BODY",BODY,{"disambiguationData":[OSD([sQuery(id+"F1.wireOp",EDGE,"E9.0.37.0")])]}),"instanceName":"7"});
            var Q232;
            Q232=makeQuery(id+"F31.opPattern","COPY",BODY,{"derivedFrom":makeQuery(id+"F3.opExtrude","SWEPT_BODY",BODY,{"disambiguationData":[OSD([sQuery(id+"F1.wireOp",EDGE,"E9.0.44.0")])]}),"instanceName":"16"});
            var Q233;
            Q233=makeQuery(id+"F33.opPattern","COPY",BODY,{"derivedFrom":makeQuery(id+"F3.opExtrude","SWEPT_BODY",BODY,{"disambiguationData":[OSD([sQuery(id+"F1.wireOp",EDGE,"E9.0.41.0")])]}),"instanceName":"25"});
            var Q234;
            Q234=makeQuery(id+"F32.opPattern","COPY",BODY,{"derivedFrom":makeQuery(id+"F3.opExtrude","SWEPT_BODY",BODY,{"disambiguationData":[OSD([sQuery(id+"F1.wireOp",EDGE,"E9.0.43.0")])]}),"instanceName":"21"});
            var Q235;
            Q235=makeQuery(id+"F33.opPattern","COPY",BODY,{"derivedFrom":makeQuery(id+"F3.opExtrude","SWEPT_BODY",BODY,{"disambiguationData":[OSD([sQuery(id+"F1.wireOp",EDGE,"E9.0.42.0")])]}),"instanceName":"25"});
            var Q236;
            Q236=makeQuery(id+"F37.opPattern","COPY",BODY,{"derivedFrom":makeQuery(id+"F3.opExtrude","SWEPT_BODY",BODY,{"disambiguationData":[OSD([sQuery(id+"F1.wireOp",EDGE,"E9.0.35.0")])]}),"instanceName":"20"});
            var Q237;
            Q237=makeQuery(id+"F32.opPattern","COPY",BODY,{"derivedFrom":makeQuery(id+"F3.opExtrude","SWEPT_BODY",BODY,{"disambiguationData":[OSD([sQuery(id+"F1.wireOp",EDGE,"E9.0.43.0")])]}),"instanceName":"22"});
            var Q238;
            Q238=makeQuery(id+"F31.opPattern","COPY",BODY,{"derivedFrom":makeQuery(id+"F3.opExtrude","SWEPT_BODY",BODY,{"disambiguationData":[OSD([sQuery(id+"F1.wireOp",EDGE,"E9.0.45.0")])]}),"instanceName":"15"});
            var Q239;
            Q239=makeQuery(id+"F37.opPattern","COPY",BODY,{"derivedFrom":makeQuery(id+"F3.opExtrude","SWEPT_BODY",BODY,{"disambiguationData":[OSD([sQuery(id+"F1.wireOp",EDGE,"E9.0.36.0")])]}),"instanceName":"19"});
            var Q240;
            Q240=makeQuery(id+"F36.opPattern","COPY",BODY,{"derivedFrom":makeQuery(id+"F3.opExtrude","SWEPT_BODY",BODY,{"disambiguationData":[OSD([sQuery(id+"F1.wireOp",EDGE,"E9.0.37.0")])]}),"instanceName":"8"});
            var Q241;
            Q241=makeQuery(id+"F33.opPattern","COPY",BODY,{"derivedFrom":makeQuery(id+"F3.opExtrude","SWEPT_BODY",BODY,{"disambiguationData":[OSD([sQuery(id+"F1.wireOp",EDGE,"E9.0.41.0")])]}),"instanceName":"26"});
            var Q242;
            Q242=makeQuery(id+"F33.opPattern","COPY",BODY,{"derivedFrom":makeQuery(id+"F3.opExtrude","SWEPT_BODY",BODY,{"disambiguationData":[OSD([sQuery(id+"F1.wireOp",EDGE,"E9.0.42.0")])]}),"instanceName":"26"});
            var Q243;
            Q243=makeQuery(id+"F37.opPattern","COPY",BODY,{"derivedFrom":makeQuery(id+"F3.opExtrude","SWEPT_BODY",BODY,{"disambiguationData":[OSD([sQuery(id+"F1.wireOp",EDGE,"E9.0.35.0")])]}),"instanceName":"19"});
            var Q244;
            Q244=makeQuery(id+"F36.opPattern","COPY",BODY,{"derivedFrom":makeQuery(id+"F3.opExtrude","SWEPT_BODY",BODY,{"disambiguationData":[OSD([sQuery(id+"F1.wireOp",EDGE,"E9.0.37.0")])]}),"instanceName":"9"});
            var Q245;
            Q245=makeQuery(id+"F31.opPattern","COPY",BODY,{"derivedFrom":makeQuery(id+"F3.opExtrude","SWEPT_BODY",BODY,{"disambiguationData":[OSD([sQuery(id+"F1.wireOp",EDGE,"E9.0.44.0")])]}),"instanceName":"5"});
            var Q246;
            Q246=makeQuery(id+"F31.opPattern","COPY",BODY,{"derivedFrom":makeQuery(id+"F3.opExtrude","SWEPT_BODY",BODY,{"disambiguationData":[OSD([sQuery(id+"F1.wireOp",EDGE,"E9.0.44.0")])]}),"instanceName":"15"});
            var Q247;
            Q247=makeQuery(id+"F31.opPattern","COPY",BODY,{"derivedFrom":makeQuery(id+"F3.opExtrude","SWEPT_BODY",BODY,{"disambiguationData":[OSD([sQuery(id+"F1.wireOp",EDGE,"E9.0.45.0")])]}),"instanceName":"5"});
            var Q248;
            Q248=makeQuery(id+"F33.opPattern","COPY",BODY,{"derivedFrom":makeQuery(id+"F3.opExtrude","SWEPT_BODY",BODY,{"disambiguationData":[OSD([sQuery(id+"F1.wireOp",EDGE,"E9.0.41.0")])]}),"instanceName":"27"});
            var Q249;
            Q249=makeQuery(id+"F37.opPattern","COPY",BODY,{"derivedFrom":makeQuery(id+"F3.opExtrude","SWEPT_BODY",BODY,{"disambiguationData":[OSD([sQuery(id+"F1.wireOp",EDGE,"E9.0.36.0")])]}),"instanceName":"18"});
            var Q250;
            Q250=makeQuery(id+"F32.opPattern","COPY",BODY,{"derivedFrom":makeQuery(id+"F3.opExtrude","SWEPT_BODY",BODY,{"disambiguationData":[OSD([sQuery(id+"F1.wireOp",EDGE,"E9.0.43.0")])]}),"instanceName":"23"});
            var Q251;
            Q251=makeQuery(id+"F36.opPattern","COPY",BODY,{"derivedFrom":makeQuery(id+"F3.opExtrude","SWEPT_BODY",BODY,{"disambiguationData":[OSD([sQuery(id+"F1.wireOp",EDGE,"E9.0.37.0")])]}),"instanceName":"16"});
            var Q252;
            Q252=makeQuery(id+"F32.opPattern","COPY",BODY,{"derivedFrom":makeQuery(id+"F3.opExtrude","SWEPT_BODY",BODY,{"disambiguationData":[OSD([sQuery(id+"F1.wireOp",EDGE,"E9.0.43.0")])]}),"instanceName":"24"});
            var Q253;
            Q253=makeQuery(id+"F33.opPattern","COPY",BODY,{"derivedFrom":makeQuery(id+"F3.opExtrude","SWEPT_BODY",BODY,{"disambiguationData":[OSD([sQuery(id+"F1.wireOp",EDGE,"E9.0.42.0")])]}),"instanceName":"27"});
            var Q254;
            Q254=makeQuery(id+"F37.opPattern","COPY",BODY,{"derivedFrom":makeQuery(id+"F3.opExtrude","SWEPT_BODY",BODY,{"disambiguationData":[OSD([sQuery(id+"F1.wireOp",EDGE,"E9.0.35.0")])]}),"instanceName":"18"});
            var Q255;
            Q255=makeQuery(id+"F31.opPattern","COPY",BODY,{"derivedFrom":makeQuery(id+"F3.opExtrude","SWEPT_BODY",BODY,{"disambiguationData":[OSD([sQuery(id+"F1.wireOp",EDGE,"E9.0.45.0")])]}),"instanceName":"14"});
            var Q256;
            Q256=makeQuery(id+"F36.opPattern","COPY",BODY,{"derivedFrom":makeQuery(id+"F3.opExtrude","SWEPT_BODY",BODY,{"disambiguationData":[OSD([sQuery(id+"F1.wireOp",EDGE,"E9.0.37.0")])]}),"instanceName":"21"});
            var Q257;
            Q257=makeQuery(id+"F37.opPattern","COPY",BODY,{"derivedFrom":makeQuery(id+"F3.opExtrude","SWEPT_BODY",BODY,{"disambiguationData":[OSD([sQuery(id+"F1.wireOp",EDGE,"E9.0.36.0")])]}),"instanceName":"3"});
            var Q258;
            Q258=makeQuery(id+"F32.opPattern","COPY",BODY,{"derivedFrom":makeQuery(id+"F3.opExtrude","SWEPT_BODY",BODY,{"disambiguationData":[OSD([sQuery(id+"F1.wireOp",EDGE,"E9.0.43.0")])]}),"instanceName":"25"});
            var Q259;
            Q259=makeQuery(id+"F31.opPattern","COPY",BODY,{"derivedFrom":makeQuery(id+"F3.opExtrude","SWEPT_BODY",BODY,{"disambiguationData":[OSD([sQuery(id+"F1.wireOp",EDGE,"E9.0.44.0")])]}),"instanceName":"14"});
            var Q260;
            Q260=makeQuery(id+"F37.opPattern","COPY",BODY,{"derivedFrom":makeQuery(id+"F3.opExtrude","SWEPT_BODY",BODY,{"disambiguationData":[OSD([sQuery(id+"F1.wireOp",EDGE,"E9.0.35.0")])]}),"instanceName":"3"});
            var Q261;
            Q261=makeQuery(id+"F32.opPattern","COPY",BODY,{"derivedFrom":makeQuery(id+"F3.opExtrude","SWEPT_BODY",BODY,{"disambiguationData":[OSD([sQuery(id+"F1.wireOp",EDGE,"E9.0.43.0")])]}),"instanceName":"26"});
            var Q262;
            Q262=makeQuery(id+"F33.opPattern","COPY",BODY,{"derivedFrom":makeQuery(id+"F3.opExtrude","SWEPT_BODY",BODY,{"disambiguationData":[OSD([sQuery(id+"F1.wireOp",EDGE,"E9.0.42.0")])]}),"instanceName":"17"});
            var Q263;
            Q263=makeQuery(id+"F31.opPattern","COPY",BODY,{"derivedFrom":makeQuery(id+"F3.opExtrude","SWEPT_BODY",BODY,{"disambiguationData":[OSD([sQuery(id+"F1.wireOp",EDGE,"E9.0.45.0")])]}),"instanceName":"13"});
            var Q264;
            Q264=makeQuery(id+"F31.opPattern","COPY",BODY,{"derivedFrom":makeQuery(id+"F3.opExtrude","SWEPT_BODY",BODY,{"disambiguationData":[OSD([sQuery(id+"F1.wireOp",EDGE,"E9.0.44.0")])]}),"instanceName":"13"});
            var Q265;
            Q265=makeQuery(id+"F34.opPattern","COPY",BODY,{"derivedFrom":makeQuery(id+"F3.opExtrude","SWEPT_BODY",BODY,{"disambiguationData":[OSD([sQuery(id+"F1.wireOp",EDGE,"E9.0.40.0")])]}),"instanceName":"1"});
            var Q266;
            Q266=makeQuery(id+"F31.opPattern","COPY",BODY,{"derivedFrom":makeQuery(id+"F3.opExtrude","SWEPT_BODY",BODY,{"disambiguationData":[OSD([sQuery(id+"F1.wireOp",EDGE,"E9.0.45.0")])]}),"instanceName":"12"});
            var Q267;
            Q267=makeQuery(id+"F37.opPattern","COPY",BODY,{"derivedFrom":makeQuery(id+"F3.opExtrude","SWEPT_BODY",BODY,{"disambiguationData":[OSD([sQuery(id+"F1.wireOp",EDGE,"E9.0.36.0")])]}),"instanceName":"2"});
            var Q268;
            Q268=makeQuery(id+"F35.opPattern","COPY",BODY,{"derivedFrom":makeQuery(id+"F3.opExtrude","SWEPT_BODY",BODY,{"disambiguationData":[OSD([sQuery(id+"F1.wireOp",EDGE,"E9.0.39.0")])]}),"instanceName":"9"});
            var Q269;
            Q269=makeQuery(id+"F34.opPattern","COPY",BODY,{"derivedFrom":makeQuery(id+"F3.opExtrude","SWEPT_BODY",BODY,{"disambiguationData":[OSD([sQuery(id+"F1.wireOp",EDGE,"E9.0.40.0")])]}),"instanceName":"2"});
            var Q270;
            Q270=makeQuery(id+"F31.opPattern","COPY",BODY,{"derivedFrom":makeQuery(id+"F3.opExtrude","SWEPT_BODY",BODY,{"disambiguationData":[OSD([sQuery(id+"F1.wireOp",EDGE,"E9.0.44.0")])]}),"instanceName":"9"});
            var Q271;
            Q271=makeQuery(id+"F37.opPattern","COPY",BODY,{"derivedFrom":makeQuery(id+"F3.opExtrude","SWEPT_BODY",BODY,{"disambiguationData":[OSD([sQuery(id+"F1.wireOp",EDGE,"E9.0.36.0")])]}),"instanceName":"17"});
            var Q272;
            Q272=makeQuery(id+"F33.opPattern","COPY",BODY,{"derivedFrom":makeQuery(id+"F3.opExtrude","SWEPT_BODY",BODY,{"disambiguationData":[OSD([sQuery(id+"F1.wireOp",EDGE,"E9.0.41.0")])]}),"instanceName":"15"});
            var Q273;
            Q273=makeQuery(id+"F35.opPattern","COPY",BODY,{"derivedFrom":makeQuery(id+"F3.opExtrude","SWEPT_BODY",BODY,{"disambiguationData":[OSD([sQuery(id+"F1.wireOp",EDGE,"E9.0.38.0")])]}),"instanceName":"9"});
            var Q274;
            Q274=makeQuery(id+"F31.opPattern","COPY",BODY,{"derivedFrom":makeQuery(id+"F3.opExtrude","SWEPT_BODY",BODY,{"disambiguationData":[OSD([sQuery(id+"F1.wireOp",EDGE,"E9.0.45.0")])]}),"instanceName":"8"});
            var Q275;
            Q275=makeQuery(id+"F31.opPattern","COPY",BODY,{"derivedFrom":makeQuery(id+"F3.opExtrude","SWEPT_BODY",BODY,{"disambiguationData":[OSD([sQuery(id+"F1.wireOp",EDGE,"E9.0.44.0")])]}),"instanceName":"8"});
            var Q276;
            Q276=makeQuery(id+"F35.opPattern","COPY",BODY,{"derivedFrom":makeQuery(id+"F3.opExtrude","SWEPT_BODY",BODY,{"disambiguationData":[OSD([sQuery(id+"F1.wireOp",EDGE,"E9.0.39.0")])]}),"instanceName":"8"});
            var Q277;
            Q277=makeQuery(id+"F37.opPattern","COPY",BODY,{"derivedFrom":makeQuery(id+"F3.opExtrude","SWEPT_BODY",BODY,{"disambiguationData":[OSD([sQuery(id+"F1.wireOp",EDGE,"E9.0.35.0")])]}),"instanceName":"17"});
            var Q278;
            Q278=makeQuery(id+"F33.opPattern","COPY",BODY,{"derivedFrom":makeQuery(id+"F3.opExtrude","SWEPT_BODY",BODY,{"disambiguationData":[OSD([sQuery(id+"F1.wireOp",EDGE,"E9.0.42.0")])]}),"instanceName":"18"});
            var Q279;
            Q279=makeQuery(id+"F31.opPattern","COPY",BODY,{"derivedFrom":makeQuery(id+"F3.opExtrude","SWEPT_BODY",BODY,{"disambiguationData":[OSD([sQuery(id+"F1.wireOp",EDGE,"E9.0.44.0")])]}),"instanceName":"6"});
            var Q280;
            Q280=makeQuery(id+"F34.opPattern","COPY",BODY,{"derivedFrom":makeQuery(id+"F3.opExtrude","SWEPT_BODY",BODY,{"disambiguationData":[OSD([sQuery(id+"F1.wireOp",EDGE,"E9.0.40.0")])]}),"instanceName":"3"});
            var Q281;
            Q281=makeQuery(id+"F32.opPattern","COPY",BODY,{"derivedFrom":makeQuery(id+"F3.opExtrude","SWEPT_BODY",BODY,{"disambiguationData":[OSD([sQuery(id+"F1.wireOp",EDGE,"E9.0.43.0")])]}),"instanceName":"15"});
            var Q282;
            Q282=makeQuery(id+"F35.opPattern","COPY",BODY,{"derivedFrom":makeQuery(id+"F3.opExtrude","SWEPT_BODY",BODY,{"disambiguationData":[OSD([sQuery(id+"F1.wireOp",EDGE,"E9.0.38.0")])]}),"instanceName":"8"});
            var Q283;
            Q283=makeQuery(id+"F35.opPattern","COPY",BODY,{"derivedFrom":makeQuery(id+"F3.opExtrude","SWEPT_BODY",BODY,{"disambiguationData":[OSD([sQuery(id+"F1.wireOp",EDGE,"E9.0.39.0")])]}),"instanceName":"7"});
            var Q284;
            Q284=makeQuery(id+"F34.opPattern","COPY",BODY,{"derivedFrom":makeQuery(id+"F3.opExtrude","SWEPT_BODY",BODY,{"disambiguationData":[OSD([sQuery(id+"F1.wireOp",EDGE,"E9.0.40.0")])]}),"instanceName":"4"});
            var Q285;
            Q285=makeQuery(id+"F34.opPattern","COPY",BODY,{"derivedFrom":makeQuery(id+"F3.opExtrude","SWEPT_BODY",BODY,{"disambiguationData":[OSD([sQuery(id+"F1.wireOp",EDGE,"E9.0.40.0")])]}),"instanceName":"5"});
            var Q286;
            Q286=makeQuery(id+"F35.opPattern","COPY",BODY,{"derivedFrom":makeQuery(id+"F3.opExtrude","SWEPT_BODY",BODY,{"disambiguationData":[OSD([sQuery(id+"F1.wireOp",EDGE,"E9.0.38.0")])]}),"instanceName":"7"});
            var Q287;
            Q287=makeQuery(id+"F37.opPattern","COPY",BODY,{"derivedFrom":makeQuery(id+"F3.opExtrude","SWEPT_BODY",BODY,{"disambiguationData":[OSD([sQuery(id+"F1.wireOp",EDGE,"E9.0.36.0")])]}),"instanceName":"16"});
            var Q288;
            Q288=makeQuery(id+"F35.opPattern","COPY",BODY,{"derivedFrom":makeQuery(id+"F3.opExtrude","SWEPT_BODY",BODY,{"disambiguationData":[OSD([sQuery(id+"F1.wireOp",EDGE,"E9.0.39.0")])]}),"instanceName":"6"});
            var Q289;
            Q289=makeQuery(id+"F31.opPattern","COPY",BODY,{"derivedFrom":makeQuery(id+"F3.opExtrude","SWEPT_BODY",BODY,{"disambiguationData":[OSD([sQuery(id+"F1.wireOp",EDGE,"E9.0.44.0")])]}),"instanceName":"7"});
            var Q290;
            Q290=makeQuery(id+"F31.opPattern","COPY",BODY,{"derivedFrom":makeQuery(id+"F3.opExtrude","SWEPT_BODY",BODY,{"disambiguationData":[OSD([sQuery(id+"F1.wireOp",EDGE,"E9.0.45.0")])]}),"instanceName":"6"});
            var Q291;
            Q291=makeQuery(id+"F3.opExtrude","SWEPT_BODY",BODY,{"disambiguationData":[OSD([sQuery(id+"F1.wireOp",EDGE,"E9.0.41.0")])]});
            var Q292;
            Q292=makeQuery(id+"F35.opPattern","COPY",BODY,{"derivedFrom":makeQuery(id+"F3.opExtrude","SWEPT_BODY",BODY,{"disambiguationData":[OSD([sQuery(id+"F1.wireOp",EDGE,"E9.0.39.0")])]}),"instanceName":"28"});
            var Q293;
            Q293=makeQuery(id+"F36.opPattern","COPY",BODY,{"derivedFrom":makeQuery(id+"F3.opExtrude","SWEPT_BODY",BODY,{"disambiguationData":[OSD([sQuery(id+"F1.wireOp",EDGE,"E9.0.37.0")])]}),"instanceName":"10"});
            var Q294;
            Q294=makeQuery(id+"F31.opPattern","COPY",BODY,{"derivedFrom":makeQuery(id+"F3.opExtrude","SWEPT_BODY",BODY,{"disambiguationData":[OSD([sQuery(id+"F1.wireOp",EDGE,"E9.0.45.0")])]}),"instanceName":"25"});
            var Q295;
            Q295=makeQuery(id+"F36.opPattern","COPY",BODY,{"derivedFrom":makeQuery(id+"F3.opExtrude","SWEPT_BODY",BODY,{"disambiguationData":[OSD([sQuery(id+"F1.wireOp",EDGE,"E9.0.37.0")])]}),"instanceName":"11"});
            var Q296;
            Q296=makeQuery(id+"F36.opPattern","COPY",BODY,{"derivedFrom":makeQuery(id+"F3.opExtrude","SWEPT_BODY",BODY,{"disambiguationData":[OSD([sQuery(id+"F1.wireOp",EDGE,"E9.0.37.0")])]}),"instanceName":"12"});
            var Q297;
            Q297=makeQuery(id+"F33.opPattern","COPY",BODY,{"derivedFrom":makeQuery(id+"F3.opExtrude","SWEPT_BODY",BODY,{"disambiguationData":[OSD([sQuery(id+"F1.wireOp",EDGE,"E9.0.42.0")])]}),"instanceName":"11"});
            var Q298;
            Q298=makeQuery(id+"F32.opPattern","COPY",BODY,{"derivedFrom":makeQuery(id+"F3.opExtrude","SWEPT_BODY",BODY,{"disambiguationData":[OSD([sQuery(id+"F1.wireOp",EDGE,"E9.0.43.0")])]}),"instanceName":"17"});
            var Q299;
            Q299=makeQuery(id+"F33.opPattern","COPY",BODY,{"derivedFrom":makeQuery(id+"F3.opExtrude","SWEPT_BODY",BODY,{"disambiguationData":[OSD([sQuery(id+"F1.wireOp",EDGE,"E9.0.41.0")])]}),"instanceName":"14"});
            var Q300;
            Q300=makeQuery(id+"F36.opPattern","COPY",BODY,{"derivedFrom":makeQuery(id+"F3.opExtrude","SWEPT_BODY",BODY,{"disambiguationData":[OSD([sQuery(id+"F1.wireOp",EDGE,"E9.0.37.0")])]}),"instanceName":"15"});
            var Q301;
            Q301=makeQuery(id+"F37.opPattern","COPY",BODY,{"derivedFrom":makeQuery(id+"F3.opExtrude","SWEPT_BODY",BODY,{"disambiguationData":[OSD([sQuery(id+"F1.wireOp",EDGE,"E9.0.35.0")])]}),"instanceName":"24"});
            var Q302;
            Q302=makeQuery(id+"F37.opPattern","COPY",BODY,{"derivedFrom":makeQuery(id+"F3.opExtrude","SWEPT_BODY",BODY,{"disambiguationData":[OSD([sQuery(id+"F1.wireOp",EDGE,"E9.0.36.0")])]}),"instanceName":"23"});
            var Q303;
            Q303=makeQuery(id+"F35.opPattern","COPY",BODY,{"derivedFrom":makeQuery(id+"F3.opExtrude","SWEPT_BODY",BODY,{"disambiguationData":[OSD([sQuery(id+"F1.wireOp",EDGE,"E9.0.38.0")])]}),"instanceName":"26"});
            var Q304;
            Q304=makeQuery(id+"F37.opPattern","COPY",BODY,{"derivedFrom":makeQuery(id+"F3.opExtrude","SWEPT_BODY",BODY,{"disambiguationData":[OSD([sQuery(id+"F1.wireOp",EDGE,"E9.0.35.0")])]}),"instanceName":"23"});
            var Q305;
            Q305=makeQuery(id+"F34.opPattern","COPY",BODY,{"derivedFrom":makeQuery(id+"F3.opExtrude","SWEPT_BODY",BODY,{"disambiguationData":[OSD([sQuery(id+"F1.wireOp",EDGE,"E9.0.40.0")])]}),"instanceName":"29"});
            var Q306;
            Q306=makeQuery(id+"F37.opPattern","COPY",BODY,{"derivedFrom":makeQuery(id+"F3.opExtrude","SWEPT_BODY",BODY,{"disambiguationData":[OSD([sQuery(id+"F1.wireOp",EDGE,"E9.0.36.0")])]}),"instanceName":"31"});
            var Q307;
            Q307=makeQuery(id+"F31.opPattern","COPY",BODY,{"derivedFrom":makeQuery(id+"F3.opExtrude","SWEPT_BODY",BODY,{"disambiguationData":[OSD([sQuery(id+"F1.wireOp",EDGE,"E9.0.45.0")])]}),"instanceName":"1"});
            var Q308;
            Q308=makeQuery(id+"F31.opPattern","COPY",BODY,{"derivedFrom":makeQuery(id+"F3.opExtrude","SWEPT_BODY",BODY,{"disambiguationData":[OSD([sQuery(id+"F1.wireOp",EDGE,"E9.0.44.0")])]}),"instanceName":"1"});
            var Q309;
            Q309=makeQuery(id+"F36.opPattern","COPY",BODY,{"derivedFrom":makeQuery(id+"F3.opExtrude","SWEPT_BODY",BODY,{"disambiguationData":[OSD([sQuery(id+"F1.wireOp",EDGE,"E9.0.37.0")])]}),"instanceName":"29"});
            var Q310;
            Q310=makeQuery(id+"F37.opPattern","COPY",BODY,{"derivedFrom":makeQuery(id+"F3.opExtrude","SWEPT_BODY",BODY,{"disambiguationData":[OSD([sQuery(id+"F1.wireOp",EDGE,"E9.0.35.0")])]}),"instanceName":"31"});
            var Q311;
            Q311=makeQuery(id+"F35.opPattern","COPY",BODY,{"derivedFrom":makeQuery(id+"F3.opExtrude","SWEPT_BODY",BODY,{"disambiguationData":[OSD([sQuery(id+"F1.wireOp",EDGE,"E9.0.38.0")])]}),"instanceName":"30"});
            var Q312;
            Q312=makeQuery(id+"F36.opPattern","COPY",BODY,{"derivedFrom":makeQuery(id+"F3.opExtrude","SWEPT_BODY",BODY,{"disambiguationData":[OSD([sQuery(id+"F1.wireOp",EDGE,"E9.0.37.0")])]}),"instanceName":"31"});
            var Q313;
            Q313=makeQuery(id+"F32.opPattern","COPY",BODY,{"derivedFrom":makeQuery(id+"F3.opExtrude","SWEPT_BODY",BODY,{"disambiguationData":[OSD([sQuery(id+"F1.wireOp",EDGE,"E9.0.43.0")])]}),"instanceName":"1"});
            var Q314;
            Q314=makeQuery(id+"F35.opPattern","COPY",BODY,{"derivedFrom":makeQuery(id+"F3.opExtrude","SWEPT_BODY",BODY,{"disambiguationData":[OSD([sQuery(id+"F1.wireOp",EDGE,"E9.0.39.0")])]}),"instanceName":"30"});
            var Q315;
            Q315=makeQuery(id+"F3.opExtrude","SWEPT_BODY",BODY,{"disambiguationData":[OSD([sQuery(id+"F1.wireOp",EDGE,"E9.0.35.0")])]});
            var Q316;
            Q316=makeQuery(id+"F3.opExtrude","SWEPT_BODY",BODY,{"disambiguationData":[OSD([sQuery(id+"F1.wireOp",EDGE,"E9.0.36.0")])]});
            var Q317;
            Q317=makeQuery(id+"F33.opPattern","COPY",BODY,{"derivedFrom":makeQuery(id+"F3.opExtrude","SWEPT_BODY",BODY,{"disambiguationData":[OSD([sQuery(id+"F1.wireOp",EDGE,"E9.0.41.0")])]}),"instanceName":"28"});
            var Q318;
            Q318=makeQuery(id+"F33.opPattern","COPY",BODY,{"derivedFrom":makeQuery(id+"F3.opExtrude","SWEPT_BODY",BODY,{"disambiguationData":[OSD([sQuery(id+"F1.wireOp",EDGE,"E9.0.42.0")])]}),"instanceName":"28"});
            var Q319;
            Q319=makeQuery(id+"F3.opExtrude","SWEPT_BODY",BODY,{"disambiguationData":[OSD([sQuery(id+"F1.wireOp",EDGE,"E9.0.37.0")])]});
            var Q320;
            Q320=makeQuery(id+"F3.opExtrude","SWEPT_BODY",BODY,{"disambiguationData":[OSD([sQuery(id+"F1.wireOp",EDGE,"E9.0.38.0")])]});
            var Q321;
            Q321=makeQuery(id+"F3.opExtrude","SWEPT_BODY",BODY,{"disambiguationData":[OSD([sQuery(id+"F1.wireOp",EDGE,"E9.0.39.0")])]});
            var Q322;
            Q322=makeQuery(id+"F32.opPattern","COPY",BODY,{"derivedFrom":makeQuery(id+"F3.opExtrude","SWEPT_BODY",BODY,{"disambiguationData":[OSD([sQuery(id+"F1.wireOp",EDGE,"E9.0.43.0")])]}),"instanceName":"27"});
            var Q323;
            Q323=makeQuery(id+"F33.opPattern","COPY",BODY,{"derivedFrom":makeQuery(id+"F3.opExtrude","SWEPT_BODY",BODY,{"disambiguationData":[OSD([sQuery(id+"F1.wireOp",EDGE,"E9.0.41.0")])]}),"instanceName":"1"});
            var Q324;
            Q324=makeQuery(id+"F3.opExtrude","SWEPT_BODY",BODY,{"disambiguationData":[OSD([sQuery(id+"F1.wireOp",EDGE,"E9.0.40.0")])]});
            var Q325;
            Q325=makeQuery(id+"F33.opPattern","COPY",BODY,{"derivedFrom":makeQuery(id+"F3.opExtrude","SWEPT_BODY",BODY,{"disambiguationData":[OSD([sQuery(id+"F1.wireOp",EDGE,"E9.0.42.0")])]}),"instanceName":"1"});
            var Q326;
            Q326=makeQuery(id+"F31.opPattern","COPY",BODY,{"derivedFrom":makeQuery(id+"F3.opExtrude","SWEPT_BODY",BODY,{"disambiguationData":[OSD([sQuery(id+"F1.wireOp",EDGE,"E9.0.44.0")])]}),"instanceName":"26"});
            var Q327;
            Q327=makeQuery(id+"F31.opPattern","COPY",BODY,{"derivedFrom":makeQuery(id+"F3.opExtrude","SWEPT_BODY",BODY,{"disambiguationData":[OSD([sQuery(id+"F1.wireOp",EDGE,"E9.0.45.0")])]}),"instanceName":"26"});
            var Q328;
            Q328=makeQuery(id+"F37.opPattern","COPY",BODY,{"derivedFrom":makeQuery(id+"F3.opExtrude","SWEPT_BODY",BODY,{"disambiguationData":[OSD([sQuery(id+"F1.wireOp",EDGE,"E9.0.36.0")])]}),"instanceName":"32"});
            var Q329;
            Q329=makeQuery(id+"F37.opPattern","COPY",BODY,{"derivedFrom":makeQuery(id+"F3.opExtrude","SWEPT_BODY",BODY,{"disambiguationData":[OSD([sQuery(id+"F1.wireOp",EDGE,"E9.0.35.0")])]}),"instanceName":"32"});
            var Q330;
            Q330=makeQuery(id+"F2.opRevolve","SWEPT_BODY",BODY,{"disambiguationData":[OSD([sQuery(id+"F0.wireOp",EDGE,"E0"),sQuery(id+"F0.wireOp",EDGE,"E1"),sQuery(id+"F0.wireOp",EDGE,"E2"),sQuery(id+"F0.wireOp",EDGE,"E3"),sQuery(id+"F0.wireOp",EDGE,"E6")])]});
            booleanBodies(context, id + "F38", {"operationType" : BooleanOperationType.SUBTRACTION, "tools" : qUnion([Q0, Q1, Q2, Q3, Q4, Q5, Q6, Q7, Q8, Q9, Q10, Q11, Q12, Q13, Q14, Q15, Q16, Q17, Q18, Q19, Q20, Q21, Q22, Q23, Q24, Q25, Q26, Q27, Q28, Q29, Q30, Q31, Q32, Q33, Q34, Q35, Q36, Q37, Q38, Q39, Q40, Q41, Q42, Q43, Q44, Q45, Q46, Q47, Q48, Q49, Q50, Q51, Q52, Q53, Q54, Q55, Q56, Q57, Q58, Q59, Q60, Q61, Q62, Q63, Q64, Q65, Q66, Q67, Q68, Q69, Q70, Q71, Q72, Q73, Q74, Q75, Q76, Q77, Q78, Q79, Q80, Q81, Q82, Q83, Q84, Q85, Q86, Q87, Q88, Q89, Q90, Q91, Q92, Q93, Q94, Q95, Q96, Q97, Q98, Q99, Q100, Q101, Q102, Q103, Q104, Q105, Q106, Q107, Q108, Q109, Q110, Q111, Q112, Q113, Q114, Q115, Q116, Q117, Q118, Q119, Q120, Q121, Q122, Q123, Q124, Q125, Q126, Q127, Q128, Q129, Q130, Q131, Q132, Q133, Q134, Q135, Q136, Q137, Q138, Q139, Q140, Q141, Q142, Q143, Q144, Q145, Q146, Q147, Q148, Q149, Q150, Q151, Q152, Q153, Q154, Q155, Q156, Q157, Q158, Q159, Q160, Q161, Q162, Q163, Q164, Q165, Q166, Q167, Q168, Q169, Q170, Q171, Q172, Q173, Q174, Q175, Q176, Q177, Q178, Q179, Q180, Q181, Q182, Q183, Q184, Q185, Q186, Q187, Q188, Q189, Q190, Q191, Q192, Q193, Q194, Q195, Q196, Q197, Q198, Q199, Q200, Q201, Q202, Q203, Q204, Q205, Q206, Q207, Q208, Q209, Q210, Q211, Q212, Q213, Q214, Q215, Q216, Q217, Q218, Q219, Q220, Q221, Q222, Q223, Q224, Q225, Q226, Q227, Q228, Q229, Q230, Q231, Q232, Q233, Q234, Q235, Q236, Q237, Q238, Q239, Q240, Q241, Q242, Q243, Q244, Q245, Q246, Q247, Q248, Q249, Q250, Q251, Q252, Q253, Q254, Q255, Q256, Q257, Q258, Q259, Q260, Q261, Q262, Q263, Q264, Q265, Q266, Q267, Q268, Q269, Q270, Q271, Q272, Q273, Q274, Q275, Q276, Q277, Q278, Q279, Q280, Q281, Q282, Q283, Q284, Q285, Q286, Q287, Q288, Q289, Q290, Q291, Q292, Q293, Q294, Q295, Q296, Q297, Q298, Q299, Q300, Q301, Q302, Q303, Q304, Q305, Q306, Q307, Q308, Q309, Q310, Q311, Q312, Q313, Q314, Q315, Q316, Q317, Q318, Q319, Q320, Q321, Q322, Q323, Q324, Q325, Q326, Q327, Q328, Q329]), "targets" : qUnion([Q330])});
        }
        {
            var Q0;
            Q0=makeQuery(id+"F3.opExtrude","SWEPT_BODY",BODY,{"disambiguationData":[OSD([sQuery(id+"F1.wireOp",EDGE,"E9.0.34.0")])]});
            var Q1;
            Q1=makeQuery(id+"F2.opRevolve","SWEPT_FACE",FACE,{"disambiguationData":[OSD([sQuery(id+"F0.wireOp",EDGE,"E1")])]});
            circularPattern(context, id + "F39", {"entities" : qUnion([Q0]), "axis" : qUnion([Q1]), "angle" : 180 * degree, "instanceCount" : 34, "oppositeDirection" : true, "equalSpace" : true});
        }
        {
            var Q0;
            Q0=makeQuery(id+"F3.opExtrude","SWEPT_BODY",BODY,{"disambiguationData":[OSD([sQuery(id+"F1.wireOp",EDGE,"E9.0.33.0")])]});
            var Q1;
            Q1=makeQuery(id+"F3.opExtrude","SWEPT_BODY",BODY,{"disambiguationData":[OSD([sQuery(id+"F1.wireOp",EDGE,"E9.0.32.0")])]});
            var Q2;
            Q2=makeQuery(id+"F2.opRevolve","SWEPT_FACE",FACE,{"disambiguationData":[OSD([sQuery(id+"F0.wireOp",EDGE,"E1")])]});
            circularPattern(context, id + "F40", {"entities" : qUnion([Q0, Q1]), "axis" : qUnion([Q2]), "angle" : 180 * degree, "instanceCount" : 35, "oppositeDirection" : true, "equalSpace" : true});
        }
        {
            var Q0;
            Q0=makeQuery(id+"F3.opExtrude","SWEPT_BODY",BODY,{"disambiguationData":[OSD([sQuery(id+"F1.wireOp",EDGE,"E9.0.31.0")])]});
            var Q1;
            Q1=makeQuery(id+"F2.opRevolve","SWEPT_FACE",FACE,{"disambiguationData":[OSD([sQuery(id+"F0.wireOp",EDGE,"E1")])]});
            circularPattern(context, id + "F41", {"entities" : qUnion([Q0]), "axis" : qUnion([Q1]), "angle" : 180 * degree, "instanceCount" : 36, "oppositeDirection" : true, "equalSpace" : true});
        }
        {
            var Q0;
            Q0=makeQuery(id+"F3.opExtrude","SWEPT_BODY",BODY,{"disambiguationData":[OSD([sQuery(id+"F1.wireOp",EDGE,"E9.0.30.0")])]});
            var Q1;
            Q1=makeQuery(id+"F3.opExtrude","SWEPT_BODY",BODY,{"disambiguationData":[OSD([sQuery(id+"F1.wireOp",EDGE,"E9.0.29.0")])]});
            var Q2;
            Q2=makeQuery(id+"F2.opRevolve","SWEPT_FACE",FACE,{"disambiguationData":[OSD([sQuery(id+"F0.wireOp",EDGE,"E1")])]});
            circularPattern(context, id + "F42", {"entities" : qUnion([Q0, Q1]), "axis" : qUnion([Q2]), "angle" : 180 * degree, "instanceCount" : 37, "oppositeDirection" : true, "equalSpace" : true});
        }
        {
            var Q0;
            Q0=makeQuery(id+"F3.opExtrude","SWEPT_BODY",BODY,{"disambiguationData":[OSD([sQuery(id+"F1.wireOp",EDGE,"E9.0.28.0")])]});
            var Q1;
            Q1=makeQuery(id+"F2.opRevolve","SWEPT_FACE",FACE,{"disambiguationData":[OSD([sQuery(id+"F0.wireOp",EDGE,"E1")])]});
            circularPattern(context, id + "F43", {"entities" : qUnion([Q0]), "axis" : qUnion([Q1]), "angle" : 180 * degree, "instanceCount" : 38, "oppositeDirection" : true, "equalSpace" : true});
        }
        {
            var Q0;
            Q0=makeQuery(id+"F43.opPattern","COPY",BODY,{"derivedFrom":makeQuery(id+"F3.opExtrude","SWEPT_BODY",BODY,{"disambiguationData":[OSD([sQuery(id+"F1.wireOp",EDGE,"E9.0.28.0")])]}),"instanceName":"28"});
            var Q1;
            Q1=makeQuery(id+"F42.opPattern","COPY",BODY,{"derivedFrom":makeQuery(id+"F3.opExtrude","SWEPT_BODY",BODY,{"disambiguationData":[OSD([sQuery(id+"F1.wireOp",EDGE,"E9.0.29.0")])]}),"instanceName":"8"});
            var Q2;
            Q2=makeQuery(id+"F43.opPattern","COPY",BODY,{"derivedFrom":makeQuery(id+"F3.opExtrude","SWEPT_BODY",BODY,{"disambiguationData":[OSD([sQuery(id+"F1.wireOp",EDGE,"E9.0.28.0")])]}),"instanceName":"29"});
            var Q3;
            Q3=makeQuery(id+"F42.opPattern","COPY",BODY,{"derivedFrom":makeQuery(id+"F3.opExtrude","SWEPT_BODY",BODY,{"disambiguationData":[OSD([sQuery(id+"F1.wireOp",EDGE,"E9.0.30.0")])]}),"instanceName":"7"});
            var Q4;
            Q4=makeQuery(id+"F42.opPattern","COPY",BODY,{"derivedFrom":makeQuery(id+"F3.opExtrude","SWEPT_BODY",BODY,{"disambiguationData":[OSD([sQuery(id+"F1.wireOp",EDGE,"E9.0.29.0")])]}),"instanceName":"7"});
            var Q5;
            Q5=makeQuery(id+"F43.opPattern","COPY",BODY,{"derivedFrom":makeQuery(id+"F3.opExtrude","SWEPT_BODY",BODY,{"disambiguationData":[OSD([sQuery(id+"F1.wireOp",EDGE,"E9.0.28.0")])]}),"instanceName":"30"});
            var Q6;
            Q6=makeQuery(id+"F42.opPattern","COPY",BODY,{"derivedFrom":makeQuery(id+"F3.opExtrude","SWEPT_BODY",BODY,{"disambiguationData":[OSD([sQuery(id+"F1.wireOp",EDGE,"E9.0.30.0")])]}),"instanceName":"6"});
            var Q7;
            Q7=makeQuery(id+"F42.opPattern","COPY",BODY,{"derivedFrom":makeQuery(id+"F3.opExtrude","SWEPT_BODY",BODY,{"disambiguationData":[OSD([sQuery(id+"F1.wireOp",EDGE,"E9.0.30.0")])]}),"instanceName":"8"});
            var Q8;
            Q8=makeQuery(id+"F42.opPattern","COPY",BODY,{"derivedFrom":makeQuery(id+"F3.opExtrude","SWEPT_BODY",BODY,{"disambiguationData":[OSD([sQuery(id+"F1.wireOp",EDGE,"E9.0.29.0")])]}),"instanceName":"1"});
            var Q9;
            Q9=makeQuery(id+"F41.opPattern","COPY",BODY,{"derivedFrom":makeQuery(id+"F3.opExtrude","SWEPT_BODY",BODY,{"disambiguationData":[OSD([sQuery(id+"F1.wireOp",EDGE,"E9.0.31.0")])]}),"instanceName":"33"});
            var Q10;
            Q10=makeQuery(id+"F40.opPattern","COPY",BODY,{"derivedFrom":makeQuery(id+"F3.opExtrude","SWEPT_BODY",BODY,{"disambiguationData":[OSD([sQuery(id+"F1.wireOp",EDGE,"E9.0.32.0")])]}),"instanceName":"2"});
            var Q11;
            Q11=makeQuery(id+"F42.opPattern","COPY",BODY,{"derivedFrom":makeQuery(id+"F3.opExtrude","SWEPT_BODY",BODY,{"disambiguationData":[OSD([sQuery(id+"F1.wireOp",EDGE,"E9.0.29.0")])]}),"instanceName":"9"});
            var Q12;
            Q12=makeQuery(id+"F41.opPattern","COPY",BODY,{"derivedFrom":makeQuery(id+"F3.opExtrude","SWEPT_BODY",BODY,{"disambiguationData":[OSD([sQuery(id+"F1.wireOp",EDGE,"E9.0.31.0")])]}),"instanceName":"32"});
            var Q13;
            Q13=makeQuery(id+"F40.opPattern","COPY",BODY,{"derivedFrom":makeQuery(id+"F3.opExtrude","SWEPT_BODY",BODY,{"disambiguationData":[OSD([sQuery(id+"F1.wireOp",EDGE,"E9.0.33.0")])]}),"instanceName":"23"});
            var Q14;
            Q14=makeQuery(id+"F42.opPattern","COPY",BODY,{"derivedFrom":makeQuery(id+"F3.opExtrude","SWEPT_BODY",BODY,{"disambiguationData":[OSD([sQuery(id+"F1.wireOp",EDGE,"E9.0.30.0")])]}),"instanceName":"9"});
            var Q15;
            Q15=makeQuery(id+"F42.opPattern","COPY",BODY,{"derivedFrom":makeQuery(id+"F3.opExtrude","SWEPT_BODY",BODY,{"disambiguationData":[OSD([sQuery(id+"F1.wireOp",EDGE,"E9.0.29.0")])]}),"instanceName":"10"});
            var Q16;
            Q16=makeQuery(id+"F41.opPattern","COPY",BODY,{"derivedFrom":makeQuery(id+"F3.opExtrude","SWEPT_BODY",BODY,{"disambiguationData":[OSD([sQuery(id+"F1.wireOp",EDGE,"E9.0.31.0")])]}),"instanceName":"31"});
            var Q17;
            Q17=makeQuery(id+"F40.opPattern","COPY",BODY,{"derivedFrom":makeQuery(id+"F3.opExtrude","SWEPT_BODY",BODY,{"disambiguationData":[OSD([sQuery(id+"F1.wireOp",EDGE,"E9.0.33.0")])]}),"instanceName":"2"});
            var Q18;
            Q18=makeQuery(id+"F41.opPattern","COPY",BODY,{"derivedFrom":makeQuery(id+"F3.opExtrude","SWEPT_BODY",BODY,{"disambiguationData":[OSD([sQuery(id+"F1.wireOp",EDGE,"E9.0.31.0")])]}),"instanceName":"30"});
            var Q19;
            Q19=makeQuery(id+"F42.opPattern","COPY",BODY,{"derivedFrom":makeQuery(id+"F3.opExtrude","SWEPT_BODY",BODY,{"disambiguationData":[OSD([sQuery(id+"F1.wireOp",EDGE,"E9.0.30.0")])]}),"instanceName":"10"});
            var Q20;
            Q20=makeQuery(id+"F40.opPattern","COPY",BODY,{"derivedFrom":makeQuery(id+"F3.opExtrude","SWEPT_BODY",BODY,{"disambiguationData":[OSD([sQuery(id+"F1.wireOp",EDGE,"E9.0.32.0")])]}),"instanceName":"3"});
            var Q21;
            Q21=makeQuery(id+"F40.opPattern","COPY",BODY,{"derivedFrom":makeQuery(id+"F3.opExtrude","SWEPT_BODY",BODY,{"disambiguationData":[OSD([sQuery(id+"F1.wireOp",EDGE,"E9.0.33.0")])]}),"instanceName":"3"});
            var Q22;
            Q22=makeQuery(id+"F41.opPattern","COPY",BODY,{"derivedFrom":makeQuery(id+"F3.opExtrude","SWEPT_BODY",BODY,{"disambiguationData":[OSD([sQuery(id+"F1.wireOp",EDGE,"E9.0.31.0")])]}),"instanceName":"8"});
            var Q23;
            Q23=makeQuery(id+"F41.opPattern","COPY",BODY,{"derivedFrom":makeQuery(id+"F3.opExtrude","SWEPT_BODY",BODY,{"disambiguationData":[OSD([sQuery(id+"F1.wireOp",EDGE,"E9.0.31.0")])]}),"instanceName":"9"});
            var Q24;
            Q24=makeQuery(id+"F42.opPattern","COPY",BODY,{"derivedFrom":makeQuery(id+"F3.opExtrude","SWEPT_BODY",BODY,{"disambiguationData":[OSD([sQuery(id+"F1.wireOp",EDGE,"E9.0.30.0")])]}),"instanceName":"32"});
            var Q25;
            Q25=makeQuery(id+"F39.opPattern","COPY",BODY,{"derivedFrom":makeQuery(id+"F3.opExtrude","SWEPT_BODY",BODY,{"disambiguationData":[OSD([sQuery(id+"F1.wireOp",EDGE,"E9.0.34.0")])]}),"instanceName":"3"});
            var Q26;
            Q26=makeQuery(id+"F40.opPattern","COPY",BODY,{"derivedFrom":makeQuery(id+"F3.opExtrude","SWEPT_BODY",BODY,{"disambiguationData":[OSD([sQuery(id+"F1.wireOp",EDGE,"E9.0.32.0")])]}),"instanceName":"4"});
            var Q27;
            Q27=makeQuery(id+"F41.opPattern","COPY",BODY,{"derivedFrom":makeQuery(id+"F3.opExtrude","SWEPT_BODY",BODY,{"disambiguationData":[OSD([sQuery(id+"F1.wireOp",EDGE,"E9.0.31.0")])]}),"instanceName":"10"});
            var Q28;
            Q28=makeQuery(id+"F41.opPattern","COPY",BODY,{"derivedFrom":makeQuery(id+"F3.opExtrude","SWEPT_BODY",BODY,{"disambiguationData":[OSD([sQuery(id+"F1.wireOp",EDGE,"E9.0.31.0")])]}),"instanceName":"29"});
            var Q29;
            Q29=makeQuery(id+"F42.opPattern","COPY",BODY,{"derivedFrom":makeQuery(id+"F3.opExtrude","SWEPT_BODY",BODY,{"disambiguationData":[OSD([sQuery(id+"F1.wireOp",EDGE,"E9.0.29.0")])]}),"instanceName":"11"});
            var Q30;
            Q30=makeQuery(id+"F42.opPattern","COPY",BODY,{"derivedFrom":makeQuery(id+"F3.opExtrude","SWEPT_BODY",BODY,{"disambiguationData":[OSD([sQuery(id+"F1.wireOp",EDGE,"E9.0.29.0")])]}),"instanceName":"5"});
            var Q31;
            Q31=makeQuery(id+"F40.opPattern","COPY",BODY,{"derivedFrom":makeQuery(id+"F3.opExtrude","SWEPT_BODY",BODY,{"disambiguationData":[OSD([sQuery(id+"F1.wireOp",EDGE,"E9.0.33.0")])]}),"instanceName":"4"});
            var Q32;
            Q32=makeQuery(id+"F40.opPattern","COPY",BODY,{"derivedFrom":makeQuery(id+"F3.opExtrude","SWEPT_BODY",BODY,{"disambiguationData":[OSD([sQuery(id+"F1.wireOp",EDGE,"E9.0.32.0")])]}),"instanceName":"23"});
            var Q33;
            Q33=makeQuery(id+"F42.opPattern","COPY",BODY,{"derivedFrom":makeQuery(id+"F3.opExtrude","SWEPT_BODY",BODY,{"disambiguationData":[OSD([sQuery(id+"F1.wireOp",EDGE,"E9.0.29.0")])]}),"instanceName":"32"});
            var Q34;
            Q34=makeQuery(id+"F41.opPattern","COPY",BODY,{"derivedFrom":makeQuery(id+"F3.opExtrude","SWEPT_BODY",BODY,{"disambiguationData":[OSD([sQuery(id+"F1.wireOp",EDGE,"E9.0.31.0")])]}),"instanceName":"28"});
            var Q35;
            Q35=makeQuery(id+"F43.opPattern","COPY",BODY,{"derivedFrom":makeQuery(id+"F3.opExtrude","SWEPT_BODY",BODY,{"disambiguationData":[OSD([sQuery(id+"F1.wireOp",EDGE,"E9.0.28.0")])]}),"instanceName":"27"});
            var Q36;
            Q36=makeQuery(id+"F43.opPattern","COPY",BODY,{"derivedFrom":makeQuery(id+"F3.opExtrude","SWEPT_BODY",BODY,{"disambiguationData":[OSD([sQuery(id+"F1.wireOp",EDGE,"E9.0.28.0")])]}),"instanceName":"26"});
            var Q37;
            Q37=makeQuery(id+"F40.opPattern","COPY",BODY,{"derivedFrom":makeQuery(id+"F3.opExtrude","SWEPT_BODY",BODY,{"disambiguationData":[OSD([sQuery(id+"F1.wireOp",EDGE,"E9.0.32.0")])]}),"instanceName":"5"});
            var Q38;
            Q38=makeQuery(id+"F43.opPattern","COPY",BODY,{"derivedFrom":makeQuery(id+"F3.opExtrude","SWEPT_BODY",BODY,{"disambiguationData":[OSD([sQuery(id+"F1.wireOp",EDGE,"E9.0.28.0")])]}),"instanceName":"25"});
            var Q39;
            Q39=makeQuery(id+"F41.opPattern","COPY",BODY,{"derivedFrom":makeQuery(id+"F3.opExtrude","SWEPT_BODY",BODY,{"disambiguationData":[OSD([sQuery(id+"F1.wireOp",EDGE,"E9.0.31.0")])]}),"instanceName":"11"});
            var Q40;
            Q40=makeQuery(id+"F42.opPattern","COPY",BODY,{"derivedFrom":makeQuery(id+"F3.opExtrude","SWEPT_BODY",BODY,{"disambiguationData":[OSD([sQuery(id+"F1.wireOp",EDGE,"E9.0.30.0")])]}),"instanceName":"11"});
            var Q41;
            Q41=makeQuery(id+"F39.opPattern","COPY",BODY,{"derivedFrom":makeQuery(id+"F3.opExtrude","SWEPT_BODY",BODY,{"disambiguationData":[OSD([sQuery(id+"F1.wireOp",EDGE,"E9.0.34.0")])]}),"instanceName":"22"});
            var Q42;
            Q42=makeQuery(id+"F42.opPattern","COPY",BODY,{"derivedFrom":makeQuery(id+"F3.opExtrude","SWEPT_BODY",BODY,{"disambiguationData":[OSD([sQuery(id+"F1.wireOp",EDGE,"E9.0.29.0")])]}),"instanceName":"12"});
            var Q43;
            Q43=makeQuery(id+"F41.opPattern","COPY",BODY,{"derivedFrom":makeQuery(id+"F3.opExtrude","SWEPT_BODY",BODY,{"disambiguationData":[OSD([sQuery(id+"F1.wireOp",EDGE,"E9.0.31.0")])]}),"instanceName":"27"});
            var Q44;
            Q44=makeQuery(id+"F41.opPattern","COPY",BODY,{"derivedFrom":makeQuery(id+"F3.opExtrude","SWEPT_BODY",BODY,{"disambiguationData":[OSD([sQuery(id+"F1.wireOp",EDGE,"E9.0.31.0")])]}),"instanceName":"7"});
            var Q45;
            Q45=makeQuery(id+"F41.opPattern","COPY",BODY,{"derivedFrom":makeQuery(id+"F3.opExtrude","SWEPT_BODY",BODY,{"disambiguationData":[OSD([sQuery(id+"F1.wireOp",EDGE,"E9.0.31.0")])]}),"instanceName":"12"});
            var Q46;
            Q46=makeQuery(id+"F41.opPattern","COPY",BODY,{"derivedFrom":makeQuery(id+"F3.opExtrude","SWEPT_BODY",BODY,{"disambiguationData":[OSD([sQuery(id+"F1.wireOp",EDGE,"E9.0.31.0")])]}),"instanceName":"26"});
            var Q47;
            Q47=makeQuery(id+"F41.opPattern","COPY",BODY,{"derivedFrom":makeQuery(id+"F3.opExtrude","SWEPT_BODY",BODY,{"disambiguationData":[OSD([sQuery(id+"F1.wireOp",EDGE,"E9.0.31.0")])]}),"instanceName":"13"});
            var Q48;
            Q48=makeQuery(id+"F42.opPattern","COPY",BODY,{"derivedFrom":makeQuery(id+"F3.opExtrude","SWEPT_BODY",BODY,{"disambiguationData":[OSD([sQuery(id+"F1.wireOp",EDGE,"E9.0.30.0")])]}),"instanceName":"12"});
            var Q49;
            Q49=makeQuery(id+"F41.opPattern","COPY",BODY,{"derivedFrom":makeQuery(id+"F3.opExtrude","SWEPT_BODY",BODY,{"disambiguationData":[OSD([sQuery(id+"F1.wireOp",EDGE,"E9.0.31.0")])]}),"instanceName":"14"});
            var Q50;
            Q50=makeQuery(id+"F42.opPattern","COPY",BODY,{"derivedFrom":makeQuery(id+"F3.opExtrude","SWEPT_BODY",BODY,{"disambiguationData":[OSD([sQuery(id+"F1.wireOp",EDGE,"E9.0.29.0")])]}),"instanceName":"13"});
            var Q51;
            Q51=makeQuery(id+"F41.opPattern","COPY",BODY,{"derivedFrom":makeQuery(id+"F3.opExtrude","SWEPT_BODY",BODY,{"disambiguationData":[OSD([sQuery(id+"F1.wireOp",EDGE,"E9.0.31.0")])]}),"instanceName":"6"});
            var Q52;
            Q52=makeQuery(id+"F40.opPattern","COPY",BODY,{"derivedFrom":makeQuery(id+"F3.opExtrude","SWEPT_BODY",BODY,{"disambiguationData":[OSD([sQuery(id+"F1.wireOp",EDGE,"E9.0.33.0")])]}),"instanceName":"5"});
            var Q53;
            Q53=makeQuery(id+"F41.opPattern","COPY",BODY,{"derivedFrom":makeQuery(id+"F3.opExtrude","SWEPT_BODY",BODY,{"disambiguationData":[OSD([sQuery(id+"F1.wireOp",EDGE,"E9.0.31.0")])]}),"instanceName":"15"});
            var Q54;
            Q54=makeQuery(id+"F42.opPattern","COPY",BODY,{"derivedFrom":makeQuery(id+"F3.opExtrude","SWEPT_BODY",BODY,{"disambiguationData":[OSD([sQuery(id+"F1.wireOp",EDGE,"E9.0.30.0")])]}),"instanceName":"13"});
            var Q55;
            Q55=makeQuery(id+"F41.opPattern","COPY",BODY,{"derivedFrom":makeQuery(id+"F3.opExtrude","SWEPT_BODY",BODY,{"disambiguationData":[OSD([sQuery(id+"F1.wireOp",EDGE,"E9.0.31.0")])]}),"instanceName":"25"});
            var Q56;
            Q56=makeQuery(id+"F41.opPattern","COPY",BODY,{"derivedFrom":makeQuery(id+"F3.opExtrude","SWEPT_BODY",BODY,{"disambiguationData":[OSD([sQuery(id+"F1.wireOp",EDGE,"E9.0.31.0")])]}),"instanceName":"24"});
            var Q57;
            Q57=makeQuery(id+"F43.opPattern","COPY",BODY,{"derivedFrom":makeQuery(id+"F3.opExtrude","SWEPT_BODY",BODY,{"disambiguationData":[OSD([sQuery(id+"F1.wireOp",EDGE,"E9.0.28.0")])]}),"instanceName":"24"});
            var Q58;
            Q58=makeQuery(id+"F42.opPattern","COPY",BODY,{"derivedFrom":makeQuery(id+"F3.opExtrude","SWEPT_BODY",BODY,{"disambiguationData":[OSD([sQuery(id+"F1.wireOp",EDGE,"E9.0.29.0")])]}),"instanceName":"14"});
            var Q59;
            Q59=makeQuery(id+"F40.opPattern","COPY",BODY,{"derivedFrom":makeQuery(id+"F3.opExtrude","SWEPT_BODY",BODY,{"disambiguationData":[OSD([sQuery(id+"F1.wireOp",EDGE,"E9.0.32.0")])]}),"instanceName":"6"});
            var Q60;
            Q60=makeQuery(id+"F42.opPattern","COPY",BODY,{"derivedFrom":makeQuery(id+"F3.opExtrude","SWEPT_BODY",BODY,{"disambiguationData":[OSD([sQuery(id+"F1.wireOp",EDGE,"E9.0.30.0")])]}),"instanceName":"14"});
            var Q61;
            Q61=makeQuery(id+"F40.opPattern","COPY",BODY,{"derivedFrom":makeQuery(id+"F3.opExtrude","SWEPT_BODY",BODY,{"disambiguationData":[OSD([sQuery(id+"F1.wireOp",EDGE,"E9.0.33.0")])]}),"instanceName":"25"});
            var Q62;
            Q62=makeQuery(id+"F42.opPattern","COPY",BODY,{"derivedFrom":makeQuery(id+"F3.opExtrude","SWEPT_BODY",BODY,{"disambiguationData":[OSD([sQuery(id+"F1.wireOp",EDGE,"E9.0.29.0")])]}),"instanceName":"15"});
            var Q63;
            Q63=makeQuery(id+"F40.opPattern","COPY",BODY,{"derivedFrom":makeQuery(id+"F3.opExtrude","SWEPT_BODY",BODY,{"disambiguationData":[OSD([sQuery(id+"F1.wireOp",EDGE,"E9.0.33.0")])]}),"instanceName":"6"});
            var Q64;
            Q64=makeQuery(id+"F43.opPattern","COPY",BODY,{"derivedFrom":makeQuery(id+"F3.opExtrude","SWEPT_BODY",BODY,{"disambiguationData":[OSD([sQuery(id+"F1.wireOp",EDGE,"E9.0.28.0")])]}),"instanceName":"5"});
            var Q65;
            Q65=makeQuery(id+"F42.opPattern","COPY",BODY,{"derivedFrom":makeQuery(id+"F3.opExtrude","SWEPT_BODY",BODY,{"disambiguationData":[OSD([sQuery(id+"F1.wireOp",EDGE,"E9.0.30.0")])]}),"instanceName":"31"});
            var Q66;
            Q66=makeQuery(id+"F42.opPattern","COPY",BODY,{"derivedFrom":makeQuery(id+"F3.opExtrude","SWEPT_BODY",BODY,{"disambiguationData":[OSD([sQuery(id+"F1.wireOp",EDGE,"E9.0.30.0")])]}),"instanceName":"15"});
            var Q67;
            Q67=makeQuery(id+"F42.opPattern","COPY",BODY,{"derivedFrom":makeQuery(id+"F3.opExtrude","SWEPT_BODY",BODY,{"disambiguationData":[OSD([sQuery(id+"F1.wireOp",EDGE,"E9.0.29.0")])]}),"instanceName":"16"});
            var Q68;
            Q68=makeQuery(id+"F43.opPattern","COPY",BODY,{"derivedFrom":makeQuery(id+"F3.opExtrude","SWEPT_BODY",BODY,{"disambiguationData":[OSD([sQuery(id+"F1.wireOp",EDGE,"E9.0.28.0")])]}),"instanceName":"8"});
            var Q69;
            Q69=makeQuery(id+"F40.opPattern","COPY",BODY,{"derivedFrom":makeQuery(id+"F3.opExtrude","SWEPT_BODY",BODY,{"disambiguationData":[OSD([sQuery(id+"F1.wireOp",EDGE,"E9.0.32.0")])]}),"instanceName":"7"});
            var Q70;
            Q70=makeQuery(id+"F40.opPattern","COPY",BODY,{"derivedFrom":makeQuery(id+"F3.opExtrude","SWEPT_BODY",BODY,{"disambiguationData":[OSD([sQuery(id+"F1.wireOp",EDGE,"E9.0.33.0")])]}),"instanceName":"7"});
            var Q71;
            Q71=makeQuery(id+"F42.opPattern","COPY",BODY,{"derivedFrom":makeQuery(id+"F3.opExtrude","SWEPT_BODY",BODY,{"disambiguationData":[OSD([sQuery(id+"F1.wireOp",EDGE,"E9.0.30.0")])]}),"instanceName":"16"});
            var Q72;
            Q72=makeQuery(id+"F41.opPattern","COPY",BODY,{"derivedFrom":makeQuery(id+"F3.opExtrude","SWEPT_BODY",BODY,{"disambiguationData":[OSD([sQuery(id+"F1.wireOp",EDGE,"E9.0.31.0")])]}),"instanceName":"23"});
            var Q73;
            Q73=makeQuery(id+"F41.opPattern","COPY",BODY,{"derivedFrom":makeQuery(id+"F3.opExtrude","SWEPT_BODY",BODY,{"disambiguationData":[OSD([sQuery(id+"F1.wireOp",EDGE,"E9.0.31.0")])]}),"instanceName":"16"});
            var Q74;
            Q74=makeQuery(id+"F41.opPattern","COPY",BODY,{"derivedFrom":makeQuery(id+"F3.opExtrude","SWEPT_BODY",BODY,{"disambiguationData":[OSD([sQuery(id+"F1.wireOp",EDGE,"E9.0.31.0")])]}),"instanceName":"22"});
            var Q75;
            Q75=makeQuery(id+"F42.opPattern","COPY",BODY,{"derivedFrom":makeQuery(id+"F3.opExtrude","SWEPT_BODY",BODY,{"disambiguationData":[OSD([sQuery(id+"F1.wireOp",EDGE,"E9.0.29.0")])]}),"instanceName":"17"});
            var Q76;
            Q76=makeQuery(id+"F41.opPattern","COPY",BODY,{"derivedFrom":makeQuery(id+"F3.opExtrude","SWEPT_BODY",BODY,{"disambiguationData":[OSD([sQuery(id+"F1.wireOp",EDGE,"E9.0.31.0")])]}),"instanceName":"21"});
            var Q77;
            Q77=makeQuery(id+"F43.opPattern","COPY",BODY,{"derivedFrom":makeQuery(id+"F3.opExtrude","SWEPT_BODY",BODY,{"disambiguationData":[OSD([sQuery(id+"F1.wireOp",EDGE,"E9.0.28.0")])]}),"instanceName":"23"});
            var Q78;
            Q78=makeQuery(id+"F42.opPattern","COPY",BODY,{"derivedFrom":makeQuery(id+"F3.opExtrude","SWEPT_BODY",BODY,{"disambiguationData":[OSD([sQuery(id+"F1.wireOp",EDGE,"E9.0.30.0")])]}),"instanceName":"17"});
            var Q79;
            Q79=makeQuery(id+"F42.opPattern","COPY",BODY,{"derivedFrom":makeQuery(id+"F3.opExtrude","SWEPT_BODY",BODY,{"disambiguationData":[OSD([sQuery(id+"F1.wireOp",EDGE,"E9.0.29.0")])]}),"instanceName":"18"});
            var Q80;
            Q80=makeQuery(id+"F39.opPattern","COPY",BODY,{"derivedFrom":makeQuery(id+"F3.opExtrude","SWEPT_BODY",BODY,{"disambiguationData":[OSD([sQuery(id+"F1.wireOp",EDGE,"E9.0.34.0")])]}),"instanceName":"24"});
            var Q81;
            Q81=makeQuery(id+"F40.opPattern","COPY",BODY,{"derivedFrom":makeQuery(id+"F3.opExtrude","SWEPT_BODY",BODY,{"disambiguationData":[OSD([sQuery(id+"F1.wireOp",EDGE,"E9.0.32.0")])]}),"instanceName":"8"});
            var Q82;
            Q82=makeQuery(id+"F43.opPattern","COPY",BODY,{"derivedFrom":makeQuery(id+"F3.opExtrude","SWEPT_BODY",BODY,{"disambiguationData":[OSD([sQuery(id+"F1.wireOp",EDGE,"E9.0.28.0")])]}),"instanceName":"7"});
            var Q83;
            Q83=makeQuery(id+"F40.opPattern","COPY",BODY,{"derivedFrom":makeQuery(id+"F3.opExtrude","SWEPT_BODY",BODY,{"disambiguationData":[OSD([sQuery(id+"F1.wireOp",EDGE,"E9.0.33.0")])]}),"instanceName":"8"});
            var Q84;
            Q84=makeQuery(id+"F40.opPattern","COPY",BODY,{"derivedFrom":makeQuery(id+"F3.opExtrude","SWEPT_BODY",BODY,{"disambiguationData":[OSD([sQuery(id+"F1.wireOp",EDGE,"E9.0.32.0")])]}),"instanceName":"21"});
            var Q85;
            Q85=makeQuery(id+"F40.opPattern","COPY",BODY,{"derivedFrom":makeQuery(id+"F3.opExtrude","SWEPT_BODY",BODY,{"disambiguationData":[OSD([sQuery(id+"F1.wireOp",EDGE,"E9.0.33.0")])]}),"instanceName":"20"});
            var Q86;
            Q86=makeQuery(id+"F40.opPattern","COPY",BODY,{"derivedFrom":makeQuery(id+"F3.opExtrude","SWEPT_BODY",BODY,{"disambiguationData":[OSD([sQuery(id+"F1.wireOp",EDGE,"E9.0.32.0")])]}),"instanceName":"9"});
            var Q87;
            Q87=makeQuery(id+"F40.opPattern","COPY",BODY,{"derivedFrom":makeQuery(id+"F3.opExtrude","SWEPT_BODY",BODY,{"disambiguationData":[OSD([sQuery(id+"F1.wireOp",EDGE,"E9.0.33.0")])]}),"instanceName":"9"});
            var Q88;
            Q88=makeQuery(id+"F43.opPattern","COPY",BODY,{"derivedFrom":makeQuery(id+"F3.opExtrude","SWEPT_BODY",BODY,{"disambiguationData":[OSD([sQuery(id+"F1.wireOp",EDGE,"E9.0.28.0")])]}),"instanceName":"3"});
            var Q89;
            Q89=makeQuery(id+"F40.opPattern","COPY",BODY,{"derivedFrom":makeQuery(id+"F3.opExtrude","SWEPT_BODY",BODY,{"disambiguationData":[OSD([sQuery(id+"F1.wireOp",EDGE,"E9.0.32.0")])]}),"instanceName":"20"});
            var Q90;
            Q90=makeQuery(id+"F40.opPattern","COPY",BODY,{"derivedFrom":makeQuery(id+"F3.opExtrude","SWEPT_BODY",BODY,{"disambiguationData":[OSD([sQuery(id+"F1.wireOp",EDGE,"E9.0.33.0")])]}),"instanceName":"31"});
            var Q91;
            Q91=makeQuery(id+"F40.opPattern","COPY",BODY,{"derivedFrom":makeQuery(id+"F3.opExtrude","SWEPT_BODY",BODY,{"disambiguationData":[OSD([sQuery(id+"F1.wireOp",EDGE,"E9.0.33.0")])]}),"instanceName":"19"});
            var Q92;
            Q92=makeQuery(id+"F40.opPattern","COPY",BODY,{"derivedFrom":makeQuery(id+"F3.opExtrude","SWEPT_BODY",BODY,{"disambiguationData":[OSD([sQuery(id+"F1.wireOp",EDGE,"E9.0.32.0")])]}),"instanceName":"19"});
            var Q93;
            Q93=makeQuery(id+"F40.opPattern","COPY",BODY,{"derivedFrom":makeQuery(id+"F3.opExtrude","SWEPT_BODY",BODY,{"disambiguationData":[OSD([sQuery(id+"F1.wireOp",EDGE,"E9.0.32.0")])]}),"instanceName":"31"});
            var Q94;
            Q94=makeQuery(id+"F41.opPattern","COPY",BODY,{"derivedFrom":makeQuery(id+"F3.opExtrude","SWEPT_BODY",BODY,{"disambiguationData":[OSD([sQuery(id+"F1.wireOp",EDGE,"E9.0.31.0")])]}),"instanceName":"20"});
            var Q95;
            Q95=makeQuery(id+"F41.opPattern","COPY",BODY,{"derivedFrom":makeQuery(id+"F3.opExtrude","SWEPT_BODY",BODY,{"disambiguationData":[OSD([sQuery(id+"F1.wireOp",EDGE,"E9.0.31.0")])]}),"instanceName":"19"});
            var Q96;
            Q96=makeQuery(id+"F40.opPattern","COPY",BODY,{"derivedFrom":makeQuery(id+"F3.opExtrude","SWEPT_BODY",BODY,{"disambiguationData":[OSD([sQuery(id+"F1.wireOp",EDGE,"E9.0.32.0")])]}),"instanceName":"10"});
            var Q97;
            Q97=makeQuery(id+"F42.opPattern","COPY",BODY,{"derivedFrom":makeQuery(id+"F3.opExtrude","SWEPT_BODY",BODY,{"disambiguationData":[OSD([sQuery(id+"F1.wireOp",EDGE,"E9.0.30.0")])]}),"instanceName":"18"});
            var Q98;
            Q98=makeQuery(id+"F40.opPattern","COPY",BODY,{"derivedFrom":makeQuery(id+"F3.opExtrude","SWEPT_BODY",BODY,{"disambiguationData":[OSD([sQuery(id+"F1.wireOp",EDGE,"E9.0.33.0")])]}),"instanceName":"18"});
            var Q99;
            Q99=makeQuery(id+"F43.opPattern","COPY",BODY,{"derivedFrom":makeQuery(id+"F3.opExtrude","SWEPT_BODY",BODY,{"disambiguationData":[OSD([sQuery(id+"F1.wireOp",EDGE,"E9.0.28.0")])]}),"instanceName":"10"});
            var Q100;
            Q100=makeQuery(id+"F42.opPattern","COPY",BODY,{"derivedFrom":makeQuery(id+"F3.opExtrude","SWEPT_BODY",BODY,{"disambiguationData":[OSD([sQuery(id+"F1.wireOp",EDGE,"E9.0.29.0")])]}),"instanceName":"19"});
            var Q101;
            Q101=makeQuery(id+"F40.opPattern","COPY",BODY,{"derivedFrom":makeQuery(id+"F3.opExtrude","SWEPT_BODY",BODY,{"disambiguationData":[OSD([sQuery(id+"F1.wireOp",EDGE,"E9.0.33.0")])]}),"instanceName":"10"});
            var Q102;
            Q102=makeQuery(id+"F43.opPattern","COPY",BODY,{"derivedFrom":makeQuery(id+"F3.opExtrude","SWEPT_BODY",BODY,{"disambiguationData":[OSD([sQuery(id+"F1.wireOp",EDGE,"E9.0.28.0")])]}),"instanceName":"22"});
            var Q103;
            Q103=makeQuery(id+"F40.opPattern","COPY",BODY,{"derivedFrom":makeQuery(id+"F3.opExtrude","SWEPT_BODY",BODY,{"disambiguationData":[OSD([sQuery(id+"F1.wireOp",EDGE,"E9.0.32.0")])]}),"instanceName":"11"});
            var Q104;
            Q104=makeQuery(id+"F42.opPattern","COPY",BODY,{"derivedFrom":makeQuery(id+"F3.opExtrude","SWEPT_BODY",BODY,{"disambiguationData":[OSD([sQuery(id+"F1.wireOp",EDGE,"E9.0.30.0")])]}),"instanceName":"19"});
            var Q105;
            Q105=makeQuery(id+"F40.opPattern","COPY",BODY,{"derivedFrom":makeQuery(id+"F3.opExtrude","SWEPT_BODY",BODY,{"disambiguationData":[OSD([sQuery(id+"F1.wireOp",EDGE,"E9.0.32.0")])]}),"instanceName":"18"});
            var Q106;
            Q106=makeQuery(id+"F40.opPattern","COPY",BODY,{"derivedFrom":makeQuery(id+"F3.opExtrude","SWEPT_BODY",BODY,{"disambiguationData":[OSD([sQuery(id+"F1.wireOp",EDGE,"E9.0.33.0")])]}),"instanceName":"30"});
            var Q107;
            Q107=makeQuery(id+"F41.opPattern","COPY",BODY,{"derivedFrom":makeQuery(id+"F3.opExtrude","SWEPT_BODY",BODY,{"disambiguationData":[OSD([sQuery(id+"F1.wireOp",EDGE,"E9.0.31.0")])]}),"instanceName":"18"});
            var Q108;
            Q108=makeQuery(id+"F43.opPattern","COPY",BODY,{"derivedFrom":makeQuery(id+"F3.opExtrude","SWEPT_BODY",BODY,{"disambiguationData":[OSD([sQuery(id+"F1.wireOp",EDGE,"E9.0.28.0")])]}),"instanceName":"21"});
            var Q109;
            Q109=makeQuery(id+"F40.opPattern","COPY",BODY,{"derivedFrom":makeQuery(id+"F3.opExtrude","SWEPT_BODY",BODY,{"disambiguationData":[OSD([sQuery(id+"F1.wireOp",EDGE,"E9.0.33.0")])]}),"instanceName":"17"});
            var Q110;
            Q110=makeQuery(id+"F41.opPattern","COPY",BODY,{"derivedFrom":makeQuery(id+"F3.opExtrude","SWEPT_BODY",BODY,{"disambiguationData":[OSD([sQuery(id+"F1.wireOp",EDGE,"E9.0.31.0")])]}),"instanceName":"17"});
            var Q111;
            Q111=makeQuery(id+"F43.opPattern","COPY",BODY,{"derivedFrom":makeQuery(id+"F3.opExtrude","SWEPT_BODY",BODY,{"disambiguationData":[OSD([sQuery(id+"F1.wireOp",EDGE,"E9.0.28.0")])]}),"instanceName":"13"});
            var Q112;
            Q112=makeQuery(id+"F42.opPattern","COPY",BODY,{"derivedFrom":makeQuery(id+"F3.opExtrude","SWEPT_BODY",BODY,{"disambiguationData":[OSD([sQuery(id+"F1.wireOp",EDGE,"E9.0.29.0")])]}),"instanceName":"20"});
            var Q113;
            Q113=makeQuery(id+"F42.opPattern","COPY",BODY,{"derivedFrom":makeQuery(id+"F3.opExtrude","SWEPT_BODY",BODY,{"disambiguationData":[OSD([sQuery(id+"F1.wireOp",EDGE,"E9.0.30.0")])]}),"instanceName":"20"});
            var Q114;
            Q114=makeQuery(id+"F42.opPattern","COPY",BODY,{"derivedFrom":makeQuery(id+"F3.opExtrude","SWEPT_BODY",BODY,{"disambiguationData":[OSD([sQuery(id+"F1.wireOp",EDGE,"E9.0.29.0")])]}),"instanceName":"21"});
            var Q115;
            Q115=makeQuery(id+"F43.opPattern","COPY",BODY,{"derivedFrom":makeQuery(id+"F3.opExtrude","SWEPT_BODY",BODY,{"disambiguationData":[OSD([sQuery(id+"F1.wireOp",EDGE,"E9.0.28.0")])]}),"instanceName":"20"});
            var Q116;
            Q116=makeQuery(id+"F40.opPattern","COPY",BODY,{"derivedFrom":makeQuery(id+"F3.opExtrude","SWEPT_BODY",BODY,{"disambiguationData":[OSD([sQuery(id+"F1.wireOp",EDGE,"E9.0.32.0")])]}),"instanceName":"17"});
            var Q117;
            Q117=makeQuery(id+"F40.opPattern","COPY",BODY,{"derivedFrom":makeQuery(id+"F3.opExtrude","SWEPT_BODY",BODY,{"disambiguationData":[OSD([sQuery(id+"F1.wireOp",EDGE,"E9.0.33.0")])]}),"instanceName":"11"});
            var Q118;
            Q118=makeQuery(id+"F42.opPattern","COPY",BODY,{"derivedFrom":makeQuery(id+"F3.opExtrude","SWEPT_BODY",BODY,{"disambiguationData":[OSD([sQuery(id+"F1.wireOp",EDGE,"E9.0.30.0")])]}),"instanceName":"21"});
            var Q119;
            Q119=makeQuery(id+"F40.opPattern","COPY",BODY,{"derivedFrom":makeQuery(id+"F3.opExtrude","SWEPT_BODY",BODY,{"disambiguationData":[OSD([sQuery(id+"F1.wireOp",EDGE,"E9.0.32.0")])]}),"instanceName":"12"});
            var Q120;
            Q120=makeQuery(id+"F39.opPattern","COPY",BODY,{"derivedFrom":makeQuery(id+"F3.opExtrude","SWEPT_BODY",BODY,{"disambiguationData":[OSD([sQuery(id+"F1.wireOp",EDGE,"E9.0.34.0")])]}),"instanceName":"4"});
            var Q121;
            Q121=makeQuery(id+"F39.opPattern","COPY",BODY,{"derivedFrom":makeQuery(id+"F3.opExtrude","SWEPT_BODY",BODY,{"disambiguationData":[OSD([sQuery(id+"F1.wireOp",EDGE,"E9.0.34.0")])]}),"instanceName":"6"});
            var Q122;
            Q122=makeQuery(id+"F39.opPattern","COPY",BODY,{"derivedFrom":makeQuery(id+"F3.opExtrude","SWEPT_BODY",BODY,{"disambiguationData":[OSD([sQuery(id+"F1.wireOp",EDGE,"E9.0.34.0")])]}),"instanceName":"5"});
            var Q123;
            Q123=makeQuery(id+"F43.opPattern","COPY",BODY,{"derivedFrom":makeQuery(id+"F3.opExtrude","SWEPT_BODY",BODY,{"disambiguationData":[OSD([sQuery(id+"F1.wireOp",EDGE,"E9.0.28.0")])]}),"instanceName":"19"});
            var Q124;
            Q124=makeQuery(id+"F39.opPattern","COPY",BODY,{"derivedFrom":makeQuery(id+"F3.opExtrude","SWEPT_BODY",BODY,{"disambiguationData":[OSD([sQuery(id+"F1.wireOp",EDGE,"E9.0.34.0")])]}),"instanceName":"23"});
            var Q125;
            Q125=makeQuery(id+"F39.opPattern","COPY",BODY,{"derivedFrom":makeQuery(id+"F3.opExtrude","SWEPT_BODY",BODY,{"disambiguationData":[OSD([sQuery(id+"F1.wireOp",EDGE,"E9.0.34.0")])]}),"instanceName":"7"});
            var Q126;
            Q126=makeQuery(id+"F43.opPattern","COPY",BODY,{"derivedFrom":makeQuery(id+"F3.opExtrude","SWEPT_BODY",BODY,{"disambiguationData":[OSD([sQuery(id+"F1.wireOp",EDGE,"E9.0.28.0")])]}),"instanceName":"18"});
            var Q127;
            Q127=makeQuery(id+"F43.opPattern","COPY",BODY,{"derivedFrom":makeQuery(id+"F3.opExtrude","SWEPT_BODY",BODY,{"disambiguationData":[OSD([sQuery(id+"F1.wireOp",EDGE,"E9.0.28.0")])]}),"instanceName":"17"});
            var Q128;
            Q128=makeQuery(id+"F39.opPattern","COPY",BODY,{"derivedFrom":makeQuery(id+"F3.opExtrude","SWEPT_BODY",BODY,{"disambiguationData":[OSD([sQuery(id+"F1.wireOp",EDGE,"E9.0.34.0")])]}),"instanceName":"8"});
            var Q129;
            Q129=makeQuery(id+"F42.opPattern","COPY",BODY,{"derivedFrom":makeQuery(id+"F3.opExtrude","SWEPT_BODY",BODY,{"disambiguationData":[OSD([sQuery(id+"F1.wireOp",EDGE,"E9.0.29.0")])]}),"instanceName":"34"});
            var Q130;
            Q130=makeQuery(id+"F43.opPattern","COPY",BODY,{"derivedFrom":makeQuery(id+"F3.opExtrude","SWEPT_BODY",BODY,{"disambiguationData":[OSD([sQuery(id+"F1.wireOp",EDGE,"E9.0.28.0")])]}),"instanceName":"9"});
            var Q131;
            Q131=makeQuery(id+"F39.opPattern","COPY",BODY,{"derivedFrom":makeQuery(id+"F3.opExtrude","SWEPT_BODY",BODY,{"disambiguationData":[OSD([sQuery(id+"F1.wireOp",EDGE,"E9.0.34.0")])]}),"instanceName":"9"});
            var Q132;
            Q132=makeQuery(id+"F39.opPattern","COPY",BODY,{"derivedFrom":makeQuery(id+"F3.opExtrude","SWEPT_BODY",BODY,{"disambiguationData":[OSD([sQuery(id+"F1.wireOp",EDGE,"E9.0.34.0")])]}),"instanceName":"10"});
            var Q133;
            Q133=makeQuery(id+"F41.opPattern","COPY",BODY,{"derivedFrom":makeQuery(id+"F3.opExtrude","SWEPT_BODY",BODY,{"disambiguationData":[OSD([sQuery(id+"F1.wireOp",EDGE,"E9.0.31.0")])]}),"instanceName":"2"});
            var Q134;
            Q134=makeQuery(id+"F40.opPattern","COPY",BODY,{"derivedFrom":makeQuery(id+"F3.opExtrude","SWEPT_BODY",BODY,{"disambiguationData":[OSD([sQuery(id+"F1.wireOp",EDGE,"E9.0.32.0")])]}),"instanceName":"13"});
            var Q135;
            Q135=makeQuery(id+"F40.opPattern","COPY",BODY,{"derivedFrom":makeQuery(id+"F3.opExtrude","SWEPT_BODY",BODY,{"disambiguationData":[OSD([sQuery(id+"F1.wireOp",EDGE,"E9.0.33.0")])]}),"instanceName":"12"});
            var Q136;
            Q136=makeQuery(id+"F43.opPattern","COPY",BODY,{"derivedFrom":makeQuery(id+"F3.opExtrude","SWEPT_BODY",BODY,{"disambiguationData":[OSD([sQuery(id+"F1.wireOp",EDGE,"E9.0.28.0")])]}),"instanceName":"16"});
            var Q137;
            Q137=makeQuery(id+"F39.opPattern","COPY",BODY,{"derivedFrom":makeQuery(id+"F3.opExtrude","SWEPT_BODY",BODY,{"disambiguationData":[OSD([sQuery(id+"F1.wireOp",EDGE,"E9.0.34.0")])]}),"instanceName":"11"});
            var Q138;
            Q138=makeQuery(id+"F40.opPattern","COPY",BODY,{"derivedFrom":makeQuery(id+"F3.opExtrude","SWEPT_BODY",BODY,{"disambiguationData":[OSD([sQuery(id+"F1.wireOp",EDGE,"E9.0.33.0")])]}),"instanceName":"32"});
            var Q139;
            Q139=makeQuery(id+"F40.opPattern","COPY",BODY,{"derivedFrom":makeQuery(id+"F3.opExtrude","SWEPT_BODY",BODY,{"disambiguationData":[OSD([sQuery(id+"F1.wireOp",EDGE,"E9.0.33.0")])]}),"instanceName":"15"});
            var Q140;
            Q140=makeQuery(id+"F39.opPattern","COPY",BODY,{"derivedFrom":makeQuery(id+"F3.opExtrude","SWEPT_BODY",BODY,{"disambiguationData":[OSD([sQuery(id+"F1.wireOp",EDGE,"E9.0.34.0")])]}),"instanceName":"12"});
            var Q141;
            Q141=makeQuery(id+"F39.opPattern","COPY",BODY,{"derivedFrom":makeQuery(id+"F3.opExtrude","SWEPT_BODY",BODY,{"disambiguationData":[OSD([sQuery(id+"F1.wireOp",EDGE,"E9.0.34.0")])]}),"instanceName":"13"});
            var Q142;
            Q142=makeQuery(id+"F39.opPattern","COPY",BODY,{"derivedFrom":makeQuery(id+"F3.opExtrude","SWEPT_BODY",BODY,{"disambiguationData":[OSD([sQuery(id+"F1.wireOp",EDGE,"E9.0.34.0")])]}),"instanceName":"14"});
            var Q143;
            Q143=makeQuery(id+"F41.opPattern","COPY",BODY,{"derivedFrom":makeQuery(id+"F3.opExtrude","SWEPT_BODY",BODY,{"disambiguationData":[OSD([sQuery(id+"F1.wireOp",EDGE,"E9.0.31.0")])]}),"instanceName":"3"});
            var Q144;
            Q144=makeQuery(id+"F43.opPattern","COPY",BODY,{"derivedFrom":makeQuery(id+"F3.opExtrude","SWEPT_BODY",BODY,{"disambiguationData":[OSD([sQuery(id+"F1.wireOp",EDGE,"E9.0.28.0")])]}),"instanceName":"15"});
            var Q145;
            Q145=makeQuery(id+"F40.opPattern","COPY",BODY,{"derivedFrom":makeQuery(id+"F3.opExtrude","SWEPT_BODY",BODY,{"disambiguationData":[OSD([sQuery(id+"F1.wireOp",EDGE,"E9.0.32.0")])]}),"instanceName":"15"});
            var Q146;
            Q146=makeQuery(id+"F42.opPattern","COPY",BODY,{"derivedFrom":makeQuery(id+"F3.opExtrude","SWEPT_BODY",BODY,{"disambiguationData":[OSD([sQuery(id+"F1.wireOp",EDGE,"E9.0.29.0")])]}),"instanceName":"22"});
            var Q147;
            Q147=makeQuery(id+"F40.opPattern","COPY",BODY,{"derivedFrom":makeQuery(id+"F3.opExtrude","SWEPT_BODY",BODY,{"disambiguationData":[OSD([sQuery(id+"F1.wireOp",EDGE,"E9.0.32.0")])]}),"instanceName":"22"});
            var Q148;
            Q148=makeQuery(id+"F42.opPattern","COPY",BODY,{"derivedFrom":makeQuery(id+"F3.opExtrude","SWEPT_BODY",BODY,{"disambiguationData":[OSD([sQuery(id+"F1.wireOp",EDGE,"E9.0.30.0")])]}),"instanceName":"34"});
            var Q149;
            Q149=makeQuery(id+"F42.opPattern","COPY",BODY,{"derivedFrom":makeQuery(id+"F3.opExtrude","SWEPT_BODY",BODY,{"disambiguationData":[OSD([sQuery(id+"F1.wireOp",EDGE,"E9.0.30.0")])]}),"instanceName":"33"});
            var Q150;
            Q150=makeQuery(id+"F42.opPattern","COPY",BODY,{"derivedFrom":makeQuery(id+"F3.opExtrude","SWEPT_BODY",BODY,{"disambiguationData":[OSD([sQuery(id+"F1.wireOp",EDGE,"E9.0.29.0")])]}),"instanceName":"33"});
            var Q151;
            Q151=makeQuery(id+"F39.opPattern","COPY",BODY,{"derivedFrom":makeQuery(id+"F3.opExtrude","SWEPT_BODY",BODY,{"disambiguationData":[OSD([sQuery(id+"F1.wireOp",EDGE,"E9.0.34.0")])]}),"instanceName":"21"});
            var Q152;
            Q152=makeQuery(id+"F40.opPattern","COPY",BODY,{"derivedFrom":makeQuery(id+"F3.opExtrude","SWEPT_BODY",BODY,{"disambiguationData":[OSD([sQuery(id+"F1.wireOp",EDGE,"E9.0.33.0")])]}),"instanceName":"16"});
            var Q153;
            Q153=makeQuery(id+"F39.opPattern","COPY",BODY,{"derivedFrom":makeQuery(id+"F3.opExtrude","SWEPT_BODY",BODY,{"disambiguationData":[OSD([sQuery(id+"F1.wireOp",EDGE,"E9.0.34.0")])]}),"instanceName":"15"});
            var Q154;
            Q154=makeQuery(id+"F40.opPattern","COPY",BODY,{"derivedFrom":makeQuery(id+"F3.opExtrude","SWEPT_BODY",BODY,{"disambiguationData":[OSD([sQuery(id+"F1.wireOp",EDGE,"E9.0.33.0")])]}),"instanceName":"22"});
            var Q155;
            Q155=makeQuery(id+"F39.opPattern","COPY",BODY,{"derivedFrom":makeQuery(id+"F3.opExtrude","SWEPT_BODY",BODY,{"disambiguationData":[OSD([sQuery(id+"F1.wireOp",EDGE,"E9.0.34.0")])]}),"instanceName":"16"});
            var Q156;
            Q156=makeQuery(id+"F40.opPattern","COPY",BODY,{"derivedFrom":makeQuery(id+"F3.opExtrude","SWEPT_BODY",BODY,{"disambiguationData":[OSD([sQuery(id+"F1.wireOp",EDGE,"E9.0.32.0")])]}),"instanceName":"32"});
            var Q157;
            Q157=makeQuery(id+"F40.opPattern","COPY",BODY,{"derivedFrom":makeQuery(id+"F3.opExtrude","SWEPT_BODY",BODY,{"disambiguationData":[OSD([sQuery(id+"F1.wireOp",EDGE,"E9.0.32.0")])]}),"instanceName":"25"});
            var Q158;
            Q158=makeQuery(id+"F39.opPattern","COPY",BODY,{"derivedFrom":makeQuery(id+"F3.opExtrude","SWEPT_BODY",BODY,{"disambiguationData":[OSD([sQuery(id+"F1.wireOp",EDGE,"E9.0.34.0")])]}),"instanceName":"17"});
            var Q159;
            Q159=makeQuery(id+"F41.opPattern","COPY",BODY,{"derivedFrom":makeQuery(id+"F3.opExtrude","SWEPT_BODY",BODY,{"disambiguationData":[OSD([sQuery(id+"F1.wireOp",EDGE,"E9.0.31.0")])]}),"instanceName":"5"});
            var Q160;
            Q160=makeQuery(id+"F43.opPattern","COPY",BODY,{"derivedFrom":makeQuery(id+"F3.opExtrude","SWEPT_BODY",BODY,{"disambiguationData":[OSD([sQuery(id+"F1.wireOp",EDGE,"E9.0.28.0")])]}),"instanceName":"14"});
            var Q161;
            Q161=makeQuery(id+"F40.opPattern","COPY",BODY,{"derivedFrom":makeQuery(id+"F3.opExtrude","SWEPT_BODY",BODY,{"disambiguationData":[OSD([sQuery(id+"F1.wireOp",EDGE,"E9.0.32.0")])]}),"instanceName":"16"});
            var Q162;
            Q162=makeQuery(id+"F42.opPattern","COPY",BODY,{"derivedFrom":makeQuery(id+"F3.opExtrude","SWEPT_BODY",BODY,{"disambiguationData":[OSD([sQuery(id+"F1.wireOp",EDGE,"E9.0.29.0")])]}),"instanceName":"6"});
            var Q163;
            Q163=makeQuery(id+"F42.opPattern","COPY",BODY,{"derivedFrom":makeQuery(id+"F3.opExtrude","SWEPT_BODY",BODY,{"disambiguationData":[OSD([sQuery(id+"F1.wireOp",EDGE,"E9.0.30.0")])]}),"instanceName":"5"});
            var Q164;
            Q164=makeQuery(id+"F40.opPattern","COPY",BODY,{"derivedFrom":makeQuery(id+"F3.opExtrude","SWEPT_BODY",BODY,{"disambiguationData":[OSD([sQuery(id+"F1.wireOp",EDGE,"E9.0.32.0")])]}),"instanceName":"30"});
            var Q165;
            Q165=makeQuery(id+"F43.opPattern","COPY",BODY,{"derivedFrom":makeQuery(id+"F3.opExtrude","SWEPT_BODY",BODY,{"disambiguationData":[OSD([sQuery(id+"F1.wireOp",EDGE,"E9.0.28.0")])]}),"instanceName":"12"});
            var Q166;
            Q166=makeQuery(id+"F43.opPattern","COPY",BODY,{"derivedFrom":makeQuery(id+"F3.opExtrude","SWEPT_BODY",BODY,{"disambiguationData":[OSD([sQuery(id+"F1.wireOp",EDGE,"E9.0.28.0")])]}),"instanceName":"2"});
            var Q167;
            Q167=makeQuery(id+"F42.opPattern","COPY",BODY,{"derivedFrom":makeQuery(id+"F3.opExtrude","SWEPT_BODY",BODY,{"disambiguationData":[OSD([sQuery(id+"F1.wireOp",EDGE,"E9.0.29.0")])]}),"instanceName":"31"});
            var Q168;
            Q168=makeQuery(id+"F42.opPattern","COPY",BODY,{"derivedFrom":makeQuery(id+"F3.opExtrude","SWEPT_BODY",BODY,{"disambiguationData":[OSD([sQuery(id+"F1.wireOp",EDGE,"E9.0.30.0")])]}),"instanceName":"30"});
            var Q169;
            Q169=makeQuery(id+"F42.opPattern","COPY",BODY,{"derivedFrom":makeQuery(id+"F3.opExtrude","SWEPT_BODY",BODY,{"disambiguationData":[OSD([sQuery(id+"F1.wireOp",EDGE,"E9.0.29.0")])]}),"instanceName":"30"});
            var Q170;
            Q170=makeQuery(id+"F39.opPattern","COPY",BODY,{"derivedFrom":makeQuery(id+"F3.opExtrude","SWEPT_BODY",BODY,{"disambiguationData":[OSD([sQuery(id+"F1.wireOp",EDGE,"E9.0.34.0")])]}),"instanceName":"25"});
            var Q171;
            Q171=makeQuery(id+"F40.opPattern","COPY",BODY,{"derivedFrom":makeQuery(id+"F3.opExtrude","SWEPT_BODY",BODY,{"disambiguationData":[OSD([sQuery(id+"F1.wireOp",EDGE,"E9.0.33.0")])]}),"instanceName":"29"});
            var Q172;
            Q172=makeQuery(id+"F40.opPattern","COPY",BODY,{"derivedFrom":makeQuery(id+"F3.opExtrude","SWEPT_BODY",BODY,{"disambiguationData":[OSD([sQuery(id+"F1.wireOp",EDGE,"E9.0.32.0")])]}),"instanceName":"29"});
            var Q173;
            Q173=makeQuery(id+"F42.opPattern","COPY",BODY,{"derivedFrom":makeQuery(id+"F3.opExtrude","SWEPT_BODY",BODY,{"disambiguationData":[OSD([sQuery(id+"F1.wireOp",EDGE,"E9.0.30.0")])]}),"instanceName":"29"});
            var Q174;
            Q174=makeQuery(id+"F42.opPattern","COPY",BODY,{"derivedFrom":makeQuery(id+"F3.opExtrude","SWEPT_BODY",BODY,{"disambiguationData":[OSD([sQuery(id+"F1.wireOp",EDGE,"E9.0.29.0")])]}),"instanceName":"29"});
            var Q175;
            Q175=makeQuery(id+"F40.opPattern","COPY",BODY,{"derivedFrom":makeQuery(id+"F3.opExtrude","SWEPT_BODY",BODY,{"disambiguationData":[OSD([sQuery(id+"F1.wireOp",EDGE,"E9.0.33.0")])]}),"instanceName":"28"});
            var Q176;
            Q176=makeQuery(id+"F42.opPattern","COPY",BODY,{"derivedFrom":makeQuery(id+"F3.opExtrude","SWEPT_BODY",BODY,{"disambiguationData":[OSD([sQuery(id+"F1.wireOp",EDGE,"E9.0.30.0")])]}),"instanceName":"28"});
            var Q177;
            Q177=makeQuery(id+"F42.opPattern","COPY",BODY,{"derivedFrom":makeQuery(id+"F3.opExtrude","SWEPT_BODY",BODY,{"disambiguationData":[OSD([sQuery(id+"F1.wireOp",EDGE,"E9.0.29.0")])]}),"instanceName":"28"});
            var Q178;
            Q178=makeQuery(id+"F39.opPattern","COPY",BODY,{"derivedFrom":makeQuery(id+"F3.opExtrude","SWEPT_BODY",BODY,{"disambiguationData":[OSD([sQuery(id+"F1.wireOp",EDGE,"E9.0.34.0")])]}),"instanceName":"26"});
            var Q179;
            Q179=makeQuery(id+"F39.opPattern","COPY",BODY,{"derivedFrom":makeQuery(id+"F3.opExtrude","SWEPT_BODY",BODY,{"disambiguationData":[OSD([sQuery(id+"F1.wireOp",EDGE,"E9.0.34.0")])]}),"instanceName":"27"});
            var Q180;
            Q180=makeQuery(id+"F40.opPattern","COPY",BODY,{"derivedFrom":makeQuery(id+"F3.opExtrude","SWEPT_BODY",BODY,{"disambiguationData":[OSD([sQuery(id+"F1.wireOp",EDGE,"E9.0.32.0")])]}),"instanceName":"28"});
            var Q181;
            Q181=makeQuery(id+"F42.opPattern","COPY",BODY,{"derivedFrom":makeQuery(id+"F3.opExtrude","SWEPT_BODY",BODY,{"disambiguationData":[OSD([sQuery(id+"F1.wireOp",EDGE,"E9.0.30.0")])]}),"instanceName":"27"});
            var Q182;
            Q182=makeQuery(id+"F42.opPattern","COPY",BODY,{"derivedFrom":makeQuery(id+"F3.opExtrude","SWEPT_BODY",BODY,{"disambiguationData":[OSD([sQuery(id+"F1.wireOp",EDGE,"E9.0.29.0")])]}),"instanceName":"27"});
            var Q183;
            Q183=makeQuery(id+"F39.opPattern","COPY",BODY,{"derivedFrom":makeQuery(id+"F3.opExtrude","SWEPT_BODY",BODY,{"disambiguationData":[OSD([sQuery(id+"F1.wireOp",EDGE,"E9.0.34.0")])]}),"instanceName":"28"});
            var Q184;
            Q184=makeQuery(id+"F40.opPattern","COPY",BODY,{"derivedFrom":makeQuery(id+"F3.opExtrude","SWEPT_BODY",BODY,{"disambiguationData":[OSD([sQuery(id+"F1.wireOp",EDGE,"E9.0.33.0")])]}),"instanceName":"27"});
            var Q185;
            Q185=makeQuery(id+"F42.opPattern","COPY",BODY,{"derivedFrom":makeQuery(id+"F3.opExtrude","SWEPT_BODY",BODY,{"disambiguationData":[OSD([sQuery(id+"F1.wireOp",EDGE,"E9.0.30.0")])]}),"instanceName":"26"});
            var Q186;
            Q186=makeQuery(id+"F39.opPattern","COPY",BODY,{"derivedFrom":makeQuery(id+"F3.opExtrude","SWEPT_BODY",BODY,{"disambiguationData":[OSD([sQuery(id+"F1.wireOp",EDGE,"E9.0.34.0")])]}),"instanceName":"29"});
            var Q187;
            Q187=makeQuery(id+"F40.opPattern","COPY",BODY,{"derivedFrom":makeQuery(id+"F3.opExtrude","SWEPT_BODY",BODY,{"disambiguationData":[OSD([sQuery(id+"F1.wireOp",EDGE,"E9.0.32.0")])]}),"instanceName":"24"});
            var Q188;
            Q188=makeQuery(id+"F42.opPattern","COPY",BODY,{"derivedFrom":makeQuery(id+"F3.opExtrude","SWEPT_BODY",BODY,{"disambiguationData":[OSD([sQuery(id+"F1.wireOp",EDGE,"E9.0.29.0")])]}),"instanceName":"26"});
            var Q189;
            Q189=makeQuery(id+"F39.opPattern","COPY",BODY,{"derivedFrom":makeQuery(id+"F3.opExtrude","SWEPT_BODY",BODY,{"disambiguationData":[OSD([sQuery(id+"F1.wireOp",EDGE,"E9.0.34.0")])]}),"instanceName":"30"});
            var Q190;
            Q190=makeQuery(id+"F40.opPattern","COPY",BODY,{"derivedFrom":makeQuery(id+"F3.opExtrude","SWEPT_BODY",BODY,{"disambiguationData":[OSD([sQuery(id+"F1.wireOp",EDGE,"E9.0.33.0")])]}),"instanceName":"21"});
            var Q191;
            Q191=makeQuery(id+"F40.opPattern","COPY",BODY,{"derivedFrom":makeQuery(id+"F3.opExtrude","SWEPT_BODY",BODY,{"disambiguationData":[OSD([sQuery(id+"F1.wireOp",EDGE,"E9.0.33.0")])]}),"instanceName":"13"});
            var Q192;
            Q192=makeQuery(id+"F43.opPattern","COPY",BODY,{"derivedFrom":makeQuery(id+"F3.opExtrude","SWEPT_BODY",BODY,{"disambiguationData":[OSD([sQuery(id+"F1.wireOp",EDGE,"E9.0.28.0")])]}),"instanceName":"35"});
            var Q193;
            Q193=makeQuery(id+"F42.opPattern","COPY",BODY,{"derivedFrom":makeQuery(id+"F3.opExtrude","SWEPT_BODY",BODY,{"disambiguationData":[OSD([sQuery(id+"F1.wireOp",EDGE,"E9.0.30.0")])]}),"instanceName":"25"});
            var Q194;
            Q194=makeQuery(id+"F40.opPattern","COPY",BODY,{"derivedFrom":makeQuery(id+"F3.opExtrude","SWEPT_BODY",BODY,{"disambiguationData":[OSD([sQuery(id+"F1.wireOp",EDGE,"E9.0.32.0")])]}),"instanceName":"14"});
            var Q195;
            Q195=makeQuery(id+"F42.opPattern","COPY",BODY,{"derivedFrom":makeQuery(id+"F3.opExtrude","SWEPT_BODY",BODY,{"disambiguationData":[OSD([sQuery(id+"F1.wireOp",EDGE,"E9.0.29.0")])]}),"instanceName":"25"});
            var Q196;
            Q196=makeQuery(id+"F43.opPattern","COPY",BODY,{"derivedFrom":makeQuery(id+"F3.opExtrude","SWEPT_BODY",BODY,{"disambiguationData":[OSD([sQuery(id+"F1.wireOp",EDGE,"E9.0.28.0")])]}),"instanceName":"34"});
            var Q197;
            Q197=makeQuery(id+"F42.opPattern","COPY",BODY,{"derivedFrom":makeQuery(id+"F3.opExtrude","SWEPT_BODY",BODY,{"disambiguationData":[OSD([sQuery(id+"F1.wireOp",EDGE,"E9.0.30.0")])]}),"instanceName":"24"});
            var Q198;
            Q198=makeQuery(id+"F40.opPattern","COPY",BODY,{"derivedFrom":makeQuery(id+"F3.opExtrude","SWEPT_BODY",BODY,{"disambiguationData":[OSD([sQuery(id+"F1.wireOp",EDGE,"E9.0.33.0")])]}),"instanceName":"14"});
            var Q199;
            Q199=makeQuery(id+"F42.opPattern","COPY",BODY,{"derivedFrom":makeQuery(id+"F3.opExtrude","SWEPT_BODY",BODY,{"disambiguationData":[OSD([sQuery(id+"F1.wireOp",EDGE,"E9.0.29.0")])]}),"instanceName":"24"});
            var Q200;
            Q200=makeQuery(id+"F39.opPattern","COPY",BODY,{"derivedFrom":makeQuery(id+"F3.opExtrude","SWEPT_BODY",BODY,{"disambiguationData":[OSD([sQuery(id+"F1.wireOp",EDGE,"E9.0.34.0")])]}),"instanceName":"31"});
            var Q201;
            Q201=makeQuery(id+"F43.opPattern","COPY",BODY,{"derivedFrom":makeQuery(id+"F3.opExtrude","SWEPT_BODY",BODY,{"disambiguationData":[OSD([sQuery(id+"F1.wireOp",EDGE,"E9.0.28.0")])]}),"instanceName":"4"});
            var Q202;
            Q202=makeQuery(id+"F42.opPattern","COPY",BODY,{"derivedFrom":makeQuery(id+"F3.opExtrude","SWEPT_BODY",BODY,{"disambiguationData":[OSD([sQuery(id+"F1.wireOp",EDGE,"E9.0.29.0")])]}),"instanceName":"2"});
            var Q203;
            Q203=makeQuery(id+"F42.opPattern","COPY",BODY,{"derivedFrom":makeQuery(id+"F3.opExtrude","SWEPT_BODY",BODY,{"disambiguationData":[OSD([sQuery(id+"F1.wireOp",EDGE,"E9.0.30.0")])]}),"instanceName":"2"});
            var Q204;
            Q204=makeQuery(id+"F42.opPattern","COPY",BODY,{"derivedFrom":makeQuery(id+"F3.opExtrude","SWEPT_BODY",BODY,{"disambiguationData":[OSD([sQuery(id+"F1.wireOp",EDGE,"E9.0.30.0")])]}),"instanceName":"23"});
            var Q205;
            Q205=makeQuery(id+"F42.opPattern","COPY",BODY,{"derivedFrom":makeQuery(id+"F3.opExtrude","SWEPT_BODY",BODY,{"disambiguationData":[OSD([sQuery(id+"F1.wireOp",EDGE,"E9.0.29.0")])]}),"instanceName":"3"});
            var Q206;
            Q206=makeQuery(id+"F43.opPattern","COPY",BODY,{"derivedFrom":makeQuery(id+"F3.opExtrude","SWEPT_BODY",BODY,{"disambiguationData":[OSD([sQuery(id+"F1.wireOp",EDGE,"E9.0.28.0")])]}),"instanceName":"33"});
            var Q207;
            Q207=makeQuery(id+"F42.opPattern","COPY",BODY,{"derivedFrom":makeQuery(id+"F3.opExtrude","SWEPT_BODY",BODY,{"disambiguationData":[OSD([sQuery(id+"F1.wireOp",EDGE,"E9.0.30.0")])]}),"instanceName":"3"});
            var Q208;
            Q208=makeQuery(id+"F42.opPattern","COPY",BODY,{"derivedFrom":makeQuery(id+"F3.opExtrude","SWEPT_BODY",BODY,{"disambiguationData":[OSD([sQuery(id+"F1.wireOp",EDGE,"E9.0.29.0")])]}),"instanceName":"23"});
            var Q209;
            Q209=makeQuery(id+"F42.opPattern","COPY",BODY,{"derivedFrom":makeQuery(id+"F3.opExtrude","SWEPT_BODY",BODY,{"disambiguationData":[OSD([sQuery(id+"F1.wireOp",EDGE,"E9.0.30.0")])]}),"instanceName":"22"});
            var Q210;
            Q210=makeQuery(id+"F42.opPattern","COPY",BODY,{"derivedFrom":makeQuery(id+"F3.opExtrude","SWEPT_BODY",BODY,{"disambiguationData":[OSD([sQuery(id+"F1.wireOp",EDGE,"E9.0.29.0")])]}),"instanceName":"4"});
            var Q211;
            Q211=makeQuery(id+"F43.opPattern","COPY",BODY,{"derivedFrom":makeQuery(id+"F3.opExtrude","SWEPT_BODY",BODY,{"disambiguationData":[OSD([sQuery(id+"F1.wireOp",EDGE,"E9.0.28.0")])]}),"instanceName":"32"});
            var Q212;
            Q212=makeQuery(id+"F43.opPattern","COPY",BODY,{"derivedFrom":makeQuery(id+"F3.opExtrude","SWEPT_BODY",BODY,{"disambiguationData":[OSD([sQuery(id+"F1.wireOp",EDGE,"E9.0.28.0")])]}),"instanceName":"31"});
            var Q213;
            Q213=makeQuery(id+"F39.opPattern","COPY",BODY,{"derivedFrom":makeQuery(id+"F3.opExtrude","SWEPT_BODY",BODY,{"disambiguationData":[OSD([sQuery(id+"F1.wireOp",EDGE,"E9.0.34.0")])]}),"instanceName":"2"});
            var Q214;
            Q214=makeQuery(id+"F42.opPattern","COPY",BODY,{"derivedFrom":makeQuery(id+"F3.opExtrude","SWEPT_BODY",BODY,{"disambiguationData":[OSD([sQuery(id+"F1.wireOp",EDGE,"E9.0.30.0")])]}),"instanceName":"4"});
            var Q215;
            Q215=makeQuery(id+"F40.opPattern","COPY",BODY,{"derivedFrom":makeQuery(id+"F3.opExtrude","SWEPT_BODY",BODY,{"disambiguationData":[OSD([sQuery(id+"F1.wireOp",EDGE,"E9.0.32.0")])]}),"instanceName":"27"});
            var Q216;
            Q216=makeQuery(id+"F40.opPattern","COPY",BODY,{"derivedFrom":makeQuery(id+"F3.opExtrude","SWEPT_BODY",BODY,{"disambiguationData":[OSD([sQuery(id+"F1.wireOp",EDGE,"E9.0.33.0")])]}),"instanceName":"26"});
            var Q217;
            Q217=makeQuery(id+"F40.opPattern","COPY",BODY,{"derivedFrom":makeQuery(id+"F3.opExtrude","SWEPT_BODY",BODY,{"disambiguationData":[OSD([sQuery(id+"F1.wireOp",EDGE,"E9.0.32.0")])]}),"instanceName":"26"});
            var Q218;
            Q218=makeQuery(id+"F43.opPattern","COPY",BODY,{"derivedFrom":makeQuery(id+"F3.opExtrude","SWEPT_BODY",BODY,{"disambiguationData":[OSD([sQuery(id+"F1.wireOp",EDGE,"E9.0.28.0")])]}),"instanceName":"11"});
            var Q219;
            Q219=makeQuery(id+"F43.opPattern","COPY",BODY,{"derivedFrom":makeQuery(id+"F3.opExtrude","SWEPT_BODY",BODY,{"disambiguationData":[OSD([sQuery(id+"F1.wireOp",EDGE,"E9.0.28.0")])]}),"instanceName":"6"});
            var Q220;
            Q220=makeQuery(id+"F40.opPattern","COPY",BODY,{"derivedFrom":makeQuery(id+"F3.opExtrude","SWEPT_BODY",BODY,{"disambiguationData":[OSD([sQuery(id+"F1.wireOp",EDGE,"E9.0.33.0")])]}),"instanceName":"24"});
            var Q221;
            Q221=makeQuery(id+"F39.opPattern","COPY",BODY,{"derivedFrom":makeQuery(id+"F3.opExtrude","SWEPT_BODY",BODY,{"disambiguationData":[OSD([sQuery(id+"F1.wireOp",EDGE,"E9.0.34.0")])]}),"instanceName":"18"});
            var Q222;
            Q222=makeQuery(id+"F39.opPattern","COPY",BODY,{"derivedFrom":makeQuery(id+"F3.opExtrude","SWEPT_BODY",BODY,{"disambiguationData":[OSD([sQuery(id+"F1.wireOp",EDGE,"E9.0.34.0")])]}),"instanceName":"19"});
            var Q223;
            Q223=makeQuery(id+"F41.opPattern","COPY",BODY,{"derivedFrom":makeQuery(id+"F3.opExtrude","SWEPT_BODY",BODY,{"disambiguationData":[OSD([sQuery(id+"F1.wireOp",EDGE,"E9.0.31.0")])]}),"instanceName":"4"});
            var Q224;
            Q224=makeQuery(id+"F39.opPattern","COPY",BODY,{"derivedFrom":makeQuery(id+"F3.opExtrude","SWEPT_BODY",BODY,{"disambiguationData":[OSD([sQuery(id+"F1.wireOp",EDGE,"E9.0.34.0")])]}),"instanceName":"20"});
            var Q225;
            Q225=makeQuery(id+"F41.opPattern","COPY",BODY,{"derivedFrom":makeQuery(id+"F3.opExtrude","SWEPT_BODY",BODY,{"disambiguationData":[OSD([sQuery(id+"F1.wireOp",EDGE,"E9.0.31.0")])]}),"instanceName":"35"});
            var Q226;
            Q226=makeQuery(id+"F40.opPattern","COPY",BODY,{"derivedFrom":makeQuery(id+"F3.opExtrude","SWEPT_BODY",BODY,{"disambiguationData":[OSD([sQuery(id+"F1.wireOp",EDGE,"E9.0.32.0")])]}),"instanceName":"1"});
            var Q227;
            Q227=makeQuery(id+"F40.opPattern","COPY",BODY,{"derivedFrom":makeQuery(id+"F3.opExtrude","SWEPT_BODY",BODY,{"disambiguationData":[OSD([sQuery(id+"F1.wireOp",EDGE,"E9.0.33.0")])]}),"instanceName":"1"});
            var Q228;
            Q228=makeQuery(id+"F42.opPattern","COPY",BODY,{"derivedFrom":makeQuery(id+"F3.opExtrude","SWEPT_BODY",BODY,{"disambiguationData":[OSD([sQuery(id+"F1.wireOp",EDGE,"E9.0.30.0")])]}),"instanceName":"35"});
            var Q229;
            Q229=makeQuery(id+"F41.opPattern","COPY",BODY,{"derivedFrom":makeQuery(id+"F3.opExtrude","SWEPT_BODY",BODY,{"disambiguationData":[OSD([sQuery(id+"F1.wireOp",EDGE,"E9.0.31.0")])]}),"instanceName":"34"});
            var Q230;
            Q230=makeQuery(id+"F43.opPattern","COPY",BODY,{"derivedFrom":makeQuery(id+"F3.opExtrude","SWEPT_BODY",BODY,{"disambiguationData":[OSD([sQuery(id+"F1.wireOp",EDGE,"E9.0.28.0")])]}),"instanceName":"1"});
            var Q231;
            Q231=makeQuery(id+"F40.opPattern","COPY",BODY,{"derivedFrom":makeQuery(id+"F3.opExtrude","SWEPT_BODY",BODY,{"disambiguationData":[OSD([sQuery(id+"F1.wireOp",EDGE,"E9.0.33.0")])]}),"instanceName":"33"});
            var Q232;
            Q232=makeQuery(id+"F42.opPattern","COPY",BODY,{"derivedFrom":makeQuery(id+"F3.opExtrude","SWEPT_BODY",BODY,{"disambiguationData":[OSD([sQuery(id+"F1.wireOp",EDGE,"E9.0.30.0")])]}),"instanceName":"36"});
            var Q233;
            Q233=makeQuery(id+"F41.opPattern","COPY",BODY,{"derivedFrom":makeQuery(id+"F3.opExtrude","SWEPT_BODY",BODY,{"disambiguationData":[OSD([sQuery(id+"F1.wireOp",EDGE,"E9.0.31.0")])]}),"instanceName":"1"});
            var Q234;
            Q234=makeQuery(id+"F40.opPattern","COPY",BODY,{"derivedFrom":makeQuery(id+"F3.opExtrude","SWEPT_BODY",BODY,{"disambiguationData":[OSD([sQuery(id+"F1.wireOp",EDGE,"E9.0.32.0")])]}),"instanceName":"33"});
            var Q235;
            Q235=makeQuery(id+"F3.opExtrude","SWEPT_BODY",BODY,{"disambiguationData":[OSD([sQuery(id+"F1.wireOp",EDGE,"E9.0.29.0")])]});
            var Q236;
            Q236=makeQuery(id+"F3.opExtrude","SWEPT_BODY",BODY,{"disambiguationData":[OSD([sQuery(id+"F1.wireOp",EDGE,"E9.0.30.0")])]});
            var Q237;
            Q237=makeQuery(id+"F3.opExtrude","SWEPT_BODY",BODY,{"disambiguationData":[OSD([sQuery(id+"F1.wireOp",EDGE,"E9.0.32.0")])]});
            var Q238;
            Q238=makeQuery(id+"F3.opExtrude","SWEPT_BODY",BODY,{"disambiguationData":[OSD([sQuery(id+"F1.wireOp",EDGE,"E9.0.33.0")])]});
            var Q239;
            Q239=makeQuery(id+"F43.opPattern","COPY",BODY,{"derivedFrom":makeQuery(id+"F3.opExtrude","SWEPT_BODY",BODY,{"disambiguationData":[OSD([sQuery(id+"F1.wireOp",EDGE,"E9.0.28.0")])]}),"instanceName":"37"});
            var Q240;
            Q240=makeQuery(id+"F43.opPattern","COPY",BODY,{"derivedFrom":makeQuery(id+"F3.opExtrude","SWEPT_BODY",BODY,{"disambiguationData":[OSD([sQuery(id+"F1.wireOp",EDGE,"E9.0.28.0")])]}),"instanceName":"36"});
            var Q241;
            Q241=makeQuery(id+"F42.opPattern","COPY",BODY,{"derivedFrom":makeQuery(id+"F3.opExtrude","SWEPT_BODY",BODY,{"disambiguationData":[OSD([sQuery(id+"F1.wireOp",EDGE,"E9.0.30.0")])]}),"instanceName":"1"});
            var Q242;
            Q242=makeQuery(id+"F39.opPattern","COPY",BODY,{"derivedFrom":makeQuery(id+"F3.opExtrude","SWEPT_BODY",BODY,{"disambiguationData":[OSD([sQuery(id+"F1.wireOp",EDGE,"E9.0.34.0")])]}),"instanceName":"32"});
            var Q243;
            Q243=makeQuery(id+"F42.opPattern","COPY",BODY,{"derivedFrom":makeQuery(id+"F3.opExtrude","SWEPT_BODY",BODY,{"disambiguationData":[OSD([sQuery(id+"F1.wireOp",EDGE,"E9.0.29.0")])]}),"instanceName":"35"});
            var Q244;
            Q244=makeQuery(id+"F39.opPattern","COPY",BODY,{"derivedFrom":makeQuery(id+"F3.opExtrude","SWEPT_BODY",BODY,{"disambiguationData":[OSD([sQuery(id+"F1.wireOp",EDGE,"E9.0.34.0")])]}),"instanceName":"1"});
            var Q245;
            Q245=makeQuery(id+"F3.opExtrude","SWEPT_BODY",BODY,{"disambiguationData":[OSD([sQuery(id+"F1.wireOp",EDGE,"E9.0.28.0")])]});
            var Q246;
            Q246=makeQuery(id+"F40.opPattern","COPY",BODY,{"derivedFrom":makeQuery(id+"F3.opExtrude","SWEPT_BODY",BODY,{"disambiguationData":[OSD([sQuery(id+"F1.wireOp",EDGE,"E9.0.33.0")])]}),"instanceName":"34"});
            var Q247;
            Q247=makeQuery(id+"F3.opExtrude","SWEPT_BODY",BODY,{"disambiguationData":[OSD([sQuery(id+"F1.wireOp",EDGE,"E9.0.31.0")])]});
            var Q248;
            Q248=makeQuery(id+"F3.opExtrude","SWEPT_BODY",BODY,{"disambiguationData":[OSD([sQuery(id+"F1.wireOp",EDGE,"E9.0.34.0")])]});
            var Q249;
            Q249=makeQuery(id+"F42.opPattern","COPY",BODY,{"derivedFrom":makeQuery(id+"F3.opExtrude","SWEPT_BODY",BODY,{"disambiguationData":[OSD([sQuery(id+"F1.wireOp",EDGE,"E9.0.29.0")])]}),"instanceName":"36"});
            var Q250;
            Q250=makeQuery(id+"F39.opPattern","COPY",BODY,{"derivedFrom":makeQuery(id+"F3.opExtrude","SWEPT_BODY",BODY,{"disambiguationData":[OSD([sQuery(id+"F1.wireOp",EDGE,"E9.0.34.0")])]}),"instanceName":"33"});
            var Q251;
            Q251=makeQuery(id+"F40.opPattern","COPY",BODY,{"derivedFrom":makeQuery(id+"F3.opExtrude","SWEPT_BODY",BODY,{"disambiguationData":[OSD([sQuery(id+"F1.wireOp",EDGE,"E9.0.32.0")])]}),"instanceName":"34"});
            var Q252;
            Q252=makeQuery(id+"F2.opRevolve","SWEPT_BODY",BODY,{"disambiguationData":[OSD([sQuery(id+"F0.wireOp",EDGE,"E0"),sQuery(id+"F0.wireOp",EDGE,"E1"),sQuery(id+"F0.wireOp",EDGE,"E2"),sQuery(id+"F0.wireOp",EDGE,"E3"),sQuery(id+"F0.wireOp",EDGE,"E6")])]});
            booleanBodies(context, id + "F44", {"operationType" : BooleanOperationType.SUBTRACTION, "tools" : qUnion([Q0, Q1, Q2, Q3, Q4, Q5, Q6, Q7, Q8, Q9, Q10, Q11, Q12, Q13, Q14, Q15, Q16, Q17, Q18, Q19, Q20, Q21, Q22, Q23, Q24, Q25, Q26, Q27, Q28, Q29, Q30, Q31, Q32, Q33, Q34, Q35, Q36, Q37, Q38, Q39, Q40, Q41, Q42, Q43, Q44, Q45, Q46, Q47, Q48, Q49, Q50, Q51, Q52, Q53, Q54, Q55, Q56, Q57, Q58, Q59, Q60, Q61, Q62, Q63, Q64, Q65, Q66, Q67, Q68, Q69, Q70, Q71, Q72, Q73, Q74, Q75, Q76, Q77, Q78, Q79, Q80, Q81, Q82, Q83, Q84, Q85, Q86, Q87, Q88, Q89, Q90, Q91, Q92, Q93, Q94, Q95, Q96, Q97, Q98, Q99, Q100, Q101, Q102, Q103, Q104, Q105, Q106, Q107, Q108, Q109, Q110, Q111, Q112, Q113, Q114, Q115, Q116, Q117, Q118, Q119, Q120, Q121, Q122, Q123, Q124, Q125, Q126, Q127, Q128, Q129, Q130, Q131, Q132, Q133, Q134, Q135, Q136, Q137, Q138, Q139, Q140, Q141, Q142, Q143, Q144, Q145, Q146, Q147, Q148, Q149, Q150, Q151, Q152, Q153, Q154, Q155, Q156, Q157, Q158, Q159, Q160, Q161, Q162, Q163, Q164, Q165, Q166, Q167, Q168, Q169, Q170, Q171, Q172, Q173, Q174, Q175, Q176, Q177, Q178, Q179, Q180, Q181, Q182, Q183, Q184, Q185, Q186, Q187, Q188, Q189, Q190, Q191, Q192, Q193, Q194, Q195, Q196, Q197, Q198, Q199, Q200, Q201, Q202, Q203, Q204, Q205, Q206, Q207, Q208, Q209, Q210, Q211, Q212, Q213, Q214, Q215, Q216, Q217, Q218, Q219, Q220, Q221, Q222, Q223, Q224, Q225, Q226, Q227, Q228, Q229, Q230, Q231, Q232, Q233, Q234, Q235, Q236, Q237, Q238, Q239, Q240, Q241, Q242, Q243, Q244, Q245, Q246, Q247, Q248, Q249, Q250, Q251]), "targets" : qUnion([Q252])});
        }
        {
            var Q0;
            Q0=makeQuery(id+"F3.opExtrude","SWEPT_BODY",BODY,{"disambiguationData":[OSD([sQuery(id+"F1.wireOp",EDGE,"E9.0.27.0")])]});
            var Q1;
            Q1=makeQuery(id+"F3.opExtrude","SWEPT_BODY",BODY,{"disambiguationData":[OSD([sQuery(id+"F1.wireOp",EDGE,"E9.0.26.0")])]});
            var Q2;
            Q2=makeQuery(id+"F2.opRevolve","SWEPT_FACE",FACE,{"disambiguationData":[OSD([sQuery(id+"F0.wireOp",EDGE,"E1")])]});
            circularPattern(context, id + "F45", {"entities" : qUnion([Q0, Q1]), "axis" : qUnion([Q2]), "angle" : 180 * degree, "instanceCount" : 39, "oppositeDirection" : true, "equalSpace" : true});
        }
        {
            var Q0;
            Q0=makeQuery(id+"F3.opExtrude","SWEPT_BODY",BODY,{"disambiguationData":[OSD([sQuery(id+"F1.wireOp",EDGE,"E9.0.25.0")])]});
            var Q1;
            Q1=makeQuery(id+"F3.opExtrude","SWEPT_BODY",BODY,{"disambiguationData":[OSD([sQuery(id+"F1.wireOp",EDGE,"E9.0.24.0")])]});
            var Q2;
            Q2=makeQuery(id+"F2.opRevolve","SWEPT_FACE",FACE,{"disambiguationData":[OSD([sQuery(id+"F0.wireOp",EDGE,"E1")])]});
            circularPattern(context, id + "F46", {"entities" : qUnion([Q0, Q1]), "axis" : qUnion([Q2]), "angle" : 180 * degree, "instanceCount" : 40, "oppositeDirection" : true, "equalSpace" : true});
        }
        {
            var Q0;
            Q0=makeQuery(id+"F3.opExtrude","SWEPT_BODY",BODY,{"disambiguationData":[OSD([sQuery(id+"F1.wireOp",EDGE,"E9.0.23.0")])]});
            var Q1;
            Q1=makeQuery(id+"F2.opRevolve","SWEPT_FACE",FACE,{"disambiguationData":[OSD([sQuery(id+"F0.wireOp",EDGE,"E1")])]});
            circularPattern(context, id + "F47", {"entities" : qUnion([Q0]), "axis" : qUnion([Q1]), "angle" : 180 * degree, "instanceCount" : 41, "oppositeDirection" : true, "equalSpace" : true});
        }
        {
            var Q0;
            Q0=makeQuery(id+"F3.opExtrude","SWEPT_BODY",BODY,{"disambiguationData":[OSD([sQuery(id+"F1.wireOp",EDGE,"E9.0.22.0")])]});
            var Q1;
            Q1=makeQuery(id+"F3.opExtrude","SWEPT_BODY",BODY,{"disambiguationData":[OSD([sQuery(id+"F1.wireOp",EDGE,"E9.0.21.0")])]});
            var Q2;
            Q2=makeQuery(id+"F2.opRevolve","SWEPT_FACE",FACE,{"disambiguationData":[OSD([sQuery(id+"F0.wireOp",EDGE,"E1")])]});
            circularPattern(context, id + "F48", {"entities" : qUnion([Q0, Q1]), "axis" : qUnion([Q2]), "angle" : 180 * degree, "instanceCount" : 42, "oppositeDirection" : true, "equalSpace" : true});
        }
        {
            var Q0;
            Q0=makeQuery(id+"F46.opPattern","COPY",BODY,{"derivedFrom":makeQuery(id+"F3.opExtrude","SWEPT_BODY",BODY,{"disambiguationData":[OSD([sQuery(id+"F1.wireOp",EDGE,"E9.0.25.0")])]}),"instanceName":"17"});
            var Q1;
            Q1=makeQuery(id+"F45.opPattern","COPY",BODY,{"derivedFrom":makeQuery(id+"F3.opExtrude","SWEPT_BODY",BODY,{"disambiguationData":[OSD([sQuery(id+"F1.wireOp",EDGE,"E9.0.27.0")])]}),"instanceName":"5"});
            var Q2;
            Q2=makeQuery(id+"F46.opPattern","COPY",BODY,{"derivedFrom":makeQuery(id+"F3.opExtrude","SWEPT_BODY",BODY,{"disambiguationData":[OSD([sQuery(id+"F1.wireOp",EDGE,"E9.0.24.0")])]}),"instanceName":"10"});
            var Q3;
            Q3=makeQuery(id+"F45.opPattern","COPY",BODY,{"derivedFrom":makeQuery(id+"F3.opExtrude","SWEPT_BODY",BODY,{"disambiguationData":[OSD([sQuery(id+"F1.wireOp",EDGE,"E9.0.26.0")])]}),"instanceName":"5"});
            var Q4;
            Q4=makeQuery(id+"F48.opPattern","COPY",BODY,{"derivedFrom":makeQuery(id+"F3.opExtrude","SWEPT_BODY",BODY,{"disambiguationData":[OSD([sQuery(id+"F1.wireOp",EDGE,"E9.0.22.0")])]}),"instanceName":"9"});
            var Q5;
            Q5=makeQuery(id+"F46.opPattern","COPY",BODY,{"derivedFrom":makeQuery(id+"F3.opExtrude","SWEPT_BODY",BODY,{"disambiguationData":[OSD([sQuery(id+"F1.wireOp",EDGE,"E9.0.25.0")])]}),"instanceName":"10"});
            var Q6;
            Q6=makeQuery(id+"F46.opPattern","COPY",BODY,{"derivedFrom":makeQuery(id+"F3.opExtrude","SWEPT_BODY",BODY,{"disambiguationData":[OSD([sQuery(id+"F1.wireOp",EDGE,"E9.0.24.0")])]}),"instanceName":"11"});
            var Q7;
            Q7=makeQuery(id+"F45.opPattern","COPY",BODY,{"derivedFrom":makeQuery(id+"F3.opExtrude","SWEPT_BODY",BODY,{"disambiguationData":[OSD([sQuery(id+"F1.wireOp",EDGE,"E9.0.27.0")])]}),"instanceName":"4"});
            var Q8;
            Q8=makeQuery(id+"F48.opPattern","COPY",BODY,{"derivedFrom":makeQuery(id+"F3.opExtrude","SWEPT_BODY",BODY,{"disambiguationData":[OSD([sQuery(id+"F1.wireOp",EDGE,"E9.0.21.0")])]}),"instanceName":"9"});
            var Q9;
            Q9=makeQuery(id+"F46.opPattern","COPY",BODY,{"derivedFrom":makeQuery(id+"F3.opExtrude","SWEPT_BODY",BODY,{"disambiguationData":[OSD([sQuery(id+"F1.wireOp",EDGE,"E9.0.25.0")])]}),"instanceName":"11"});
            var Q10;
            Q10=makeQuery(id+"F46.opPattern","COPY",BODY,{"derivedFrom":makeQuery(id+"F3.opExtrude","SWEPT_BODY",BODY,{"disambiguationData":[OSD([sQuery(id+"F1.wireOp",EDGE,"E9.0.25.0")])]}),"instanceName":"9"});
            var Q11;
            Q11=makeQuery(id+"F45.opPattern","COPY",BODY,{"derivedFrom":makeQuery(id+"F3.opExtrude","SWEPT_BODY",BODY,{"disambiguationData":[OSD([sQuery(id+"F1.wireOp",EDGE,"E9.0.27.0")])]}),"instanceName":"20"});
            var Q12;
            Q12=makeQuery(id+"F46.opPattern","COPY",BODY,{"derivedFrom":makeQuery(id+"F3.opExtrude","SWEPT_BODY",BODY,{"disambiguationData":[OSD([sQuery(id+"F1.wireOp",EDGE,"E9.0.24.0")])]}),"instanceName":"17"});
            var Q13;
            Q13=makeQuery(id+"F46.opPattern","COPY",BODY,{"derivedFrom":makeQuery(id+"F3.opExtrude","SWEPT_BODY",BODY,{"disambiguationData":[OSD([sQuery(id+"F1.wireOp",EDGE,"E9.0.25.0")])]}),"instanceName":"18"});
            var Q14;
            Q14=makeQuery(id+"F48.opPattern","COPY",BODY,{"derivedFrom":makeQuery(id+"F3.opExtrude","SWEPT_BODY",BODY,{"disambiguationData":[OSD([sQuery(id+"F1.wireOp",EDGE,"E9.0.22.0")])]}),"instanceName":"8"});
            var Q15;
            Q15=makeQuery(id+"F46.opPattern","COPY",BODY,{"derivedFrom":makeQuery(id+"F3.opExtrude","SWEPT_BODY",BODY,{"disambiguationData":[OSD([sQuery(id+"F1.wireOp",EDGE,"E9.0.24.0")])]}),"instanceName":"9"});
            var Q16;
            Q16=makeQuery(id+"F46.opPattern","COPY",BODY,{"derivedFrom":makeQuery(id+"F3.opExtrude","SWEPT_BODY",BODY,{"disambiguationData":[OSD([sQuery(id+"F1.wireOp",EDGE,"E9.0.24.0")])]}),"instanceName":"19"});
            var Q17;
            Q17=makeQuery(id+"F47.opPattern","COPY",BODY,{"derivedFrom":makeQuery(id+"F3.opExtrude","SWEPT_BODY",BODY,{"disambiguationData":[OSD([sQuery(id+"F1.wireOp",EDGE,"E9.0.23.0")])]}),"instanceName":"13"});
            var Q18;
            Q18=makeQuery(id+"F46.opPattern","COPY",BODY,{"derivedFrom":makeQuery(id+"F3.opExtrude","SWEPT_BODY",BODY,{"disambiguationData":[OSD([sQuery(id+"F1.wireOp",EDGE,"E9.0.24.0")])]}),"instanceName":"18"});
            var Q19;
            Q19=makeQuery(id+"F46.opPattern","COPY",BODY,{"derivedFrom":makeQuery(id+"F3.opExtrude","SWEPT_BODY",BODY,{"disambiguationData":[OSD([sQuery(id+"F1.wireOp",EDGE,"E9.0.25.0")])]}),"instanceName":"8"});
            var Q20;
            Q20=makeQuery(id+"F46.opPattern","COPY",BODY,{"derivedFrom":makeQuery(id+"F3.opExtrude","SWEPT_BODY",BODY,{"disambiguationData":[OSD([sQuery(id+"F1.wireOp",EDGE,"E9.0.24.0")])]}),"instanceName":"8"});
            var Q21;
            Q21=makeQuery(id+"F46.opPattern","COPY",BODY,{"derivedFrom":makeQuery(id+"F3.opExtrude","SWEPT_BODY",BODY,{"disambiguationData":[OSD([sQuery(id+"F1.wireOp",EDGE,"E9.0.25.0")])]}),"instanceName":"19"});
            var Q22;
            Q22=makeQuery(id+"F48.opPattern","COPY",BODY,{"derivedFrom":makeQuery(id+"F3.opExtrude","SWEPT_BODY",BODY,{"disambiguationData":[OSD([sQuery(id+"F1.wireOp",EDGE,"E9.0.21.0")])]}),"instanceName":"8"});
            var Q23;
            Q23=makeQuery(id+"F46.opPattern","COPY",BODY,{"derivedFrom":makeQuery(id+"F3.opExtrude","SWEPT_BODY",BODY,{"disambiguationData":[OSD([sQuery(id+"F1.wireOp",EDGE,"E9.0.24.0")])]}),"instanceName":"20"});
            var Q24;
            Q24=makeQuery(id+"F46.opPattern","COPY",BODY,{"derivedFrom":makeQuery(id+"F3.opExtrude","SWEPT_BODY",BODY,{"disambiguationData":[OSD([sQuery(id+"F1.wireOp",EDGE,"E9.0.25.0")])]}),"instanceName":"7"});
            var Q25;
            Q25=makeQuery(id+"F48.opPattern","COPY",BODY,{"derivedFrom":makeQuery(id+"F3.opExtrude","SWEPT_BODY",BODY,{"disambiguationData":[OSD([sQuery(id+"F1.wireOp",EDGE,"E9.0.22.0")])]}),"instanceName":"7"});
            var Q26;
            Q26=makeQuery(id+"F48.opPattern","COPY",BODY,{"derivedFrom":makeQuery(id+"F3.opExtrude","SWEPT_BODY",BODY,{"disambiguationData":[OSD([sQuery(id+"F1.wireOp",EDGE,"E9.0.21.0")])]}),"instanceName":"7"});
            var Q27;
            Q27=makeQuery(id+"F46.opPattern","COPY",BODY,{"derivedFrom":makeQuery(id+"F3.opExtrude","SWEPT_BODY",BODY,{"disambiguationData":[OSD([sQuery(id+"F1.wireOp",EDGE,"E9.0.24.0")])]}),"instanceName":"31"});
            var Q28;
            Q28=makeQuery(id+"F46.opPattern","COPY",BODY,{"derivedFrom":makeQuery(id+"F3.opExtrude","SWEPT_BODY",BODY,{"disambiguationData":[OSD([sQuery(id+"F1.wireOp",EDGE,"E9.0.25.0")])]}),"instanceName":"30"});
            var Q29;
            Q29=makeQuery(id+"F45.opPattern","COPY",BODY,{"derivedFrom":makeQuery(id+"F3.opExtrude","SWEPT_BODY",BODY,{"disambiguationData":[OSD([sQuery(id+"F1.wireOp",EDGE,"E9.0.27.0")])]}),"instanceName":"23"});
            var Q30;
            Q30=makeQuery(id+"F48.opPattern","COPY",BODY,{"derivedFrom":makeQuery(id+"F3.opExtrude","SWEPT_BODY",BODY,{"disambiguationData":[OSD([sQuery(id+"F1.wireOp",EDGE,"E9.0.21.0")])]}),"instanceName":"25"});
            var Q31;
            Q31=makeQuery(id+"F48.opPattern","COPY",BODY,{"derivedFrom":makeQuery(id+"F3.opExtrude","SWEPT_BODY",BODY,{"disambiguationData":[OSD([sQuery(id+"F1.wireOp",EDGE,"E9.0.22.0")])]}),"instanceName":"6"});
            var Q32;
            Q32=makeQuery(id+"F46.opPattern","COPY",BODY,{"derivedFrom":makeQuery(id+"F3.opExtrude","SWEPT_BODY",BODY,{"disambiguationData":[OSD([sQuery(id+"F1.wireOp",EDGE,"E9.0.24.0")])]}),"instanceName":"30"});
            var Q33;
            Q33=makeQuery(id+"F46.opPattern","COPY",BODY,{"derivedFrom":makeQuery(id+"F3.opExtrude","SWEPT_BODY",BODY,{"disambiguationData":[OSD([sQuery(id+"F1.wireOp",EDGE,"E9.0.25.0")])]}),"instanceName":"20"});
            var Q34;
            Q34=makeQuery(id+"F46.opPattern","COPY",BODY,{"derivedFrom":makeQuery(id+"F3.opExtrude","SWEPT_BODY",BODY,{"disambiguationData":[OSD([sQuery(id+"F1.wireOp",EDGE,"E9.0.24.0")])]}),"instanceName":"7"});
            var Q35;
            Q35=makeQuery(id+"F46.opPattern","COPY",BODY,{"derivedFrom":makeQuery(id+"F3.opExtrude","SWEPT_BODY",BODY,{"disambiguationData":[OSD([sQuery(id+"F1.wireOp",EDGE,"E9.0.24.0")])]}),"instanceName":"13"});
            var Q36;
            Q36=makeQuery(id+"F48.opPattern","COPY",BODY,{"derivedFrom":makeQuery(id+"F3.opExtrude","SWEPT_BODY",BODY,{"disambiguationData":[OSD([sQuery(id+"F1.wireOp",EDGE,"E9.0.21.0")])]}),"instanceName":"6"});
            var Q37;
            Q37=makeQuery(id+"F47.opPattern","COPY",BODY,{"derivedFrom":makeQuery(id+"F3.opExtrude","SWEPT_BODY",BODY,{"disambiguationData":[OSD([sQuery(id+"F1.wireOp",EDGE,"E9.0.23.0")])]}),"instanceName":"14"});
            var Q38;
            Q38=makeQuery(id+"F45.opPattern","COPY",BODY,{"derivedFrom":makeQuery(id+"F3.opExtrude","SWEPT_BODY",BODY,{"disambiguationData":[OSD([sQuery(id+"F1.wireOp",EDGE,"E9.0.26.0")])]}),"instanceName":"24"});
            var Q39;
            Q39=makeQuery(id+"F46.opPattern","COPY",BODY,{"derivedFrom":makeQuery(id+"F3.opExtrude","SWEPT_BODY",BODY,{"disambiguationData":[OSD([sQuery(id+"F1.wireOp",EDGE,"E9.0.24.0")])]}),"instanceName":"21"});
            var Q40;
            Q40=makeQuery(id+"F45.opPattern","COPY",BODY,{"derivedFrom":makeQuery(id+"F3.opExtrude","SWEPT_BODY",BODY,{"disambiguationData":[OSD([sQuery(id+"F1.wireOp",EDGE,"E9.0.26.0")])]}),"instanceName":"6"});
            var Q41;
            Q41=makeQuery(id+"F45.opPattern","COPY",BODY,{"derivedFrom":makeQuery(id+"F3.opExtrude","SWEPT_BODY",BODY,{"disambiguationData":[OSD([sQuery(id+"F1.wireOp",EDGE,"E9.0.27.0")])]}),"instanceName":"6"});
            var Q42;
            Q42=makeQuery(id+"F48.opPattern","COPY",BODY,{"derivedFrom":makeQuery(id+"F3.opExtrude","SWEPT_BODY",BODY,{"disambiguationData":[OSD([sQuery(id+"F1.wireOp",EDGE,"E9.0.22.0")])]}),"instanceName":"5"});
            var Q43;
            Q43=makeQuery(id+"F45.opPattern","COPY",BODY,{"derivedFrom":makeQuery(id+"F3.opExtrude","SWEPT_BODY",BODY,{"disambiguationData":[OSD([sQuery(id+"F1.wireOp",EDGE,"E9.0.26.0")])]}),"instanceName":"7"});
            var Q44;
            Q44=makeQuery(id+"F46.opPattern","COPY",BODY,{"derivedFrom":makeQuery(id+"F3.opExtrude","SWEPT_BODY",BODY,{"disambiguationData":[OSD([sQuery(id+"F1.wireOp",EDGE,"E9.0.25.0")])]}),"instanceName":"29"});
            var Q45;
            Q45=makeQuery(id+"F46.opPattern","COPY",BODY,{"derivedFrom":makeQuery(id+"F3.opExtrude","SWEPT_BODY",BODY,{"disambiguationData":[OSD([sQuery(id+"F1.wireOp",EDGE,"E9.0.25.0")])]}),"instanceName":"6"});
            var Q46;
            Q46=makeQuery(id+"F48.opPattern","COPY",BODY,{"derivedFrom":makeQuery(id+"F3.opExtrude","SWEPT_BODY",BODY,{"disambiguationData":[OSD([sQuery(id+"F1.wireOp",EDGE,"E9.0.22.0")])]}),"instanceName":"15"});
            var Q47;
            Q47=makeQuery(id+"F46.opPattern","COPY",BODY,{"derivedFrom":makeQuery(id+"F3.opExtrude","SWEPT_BODY",BODY,{"disambiguationData":[OSD([sQuery(id+"F1.wireOp",EDGE,"E9.0.24.0")])]}),"instanceName":"6"});
            var Q48;
            Q48=makeQuery(id+"F46.opPattern","COPY",BODY,{"derivedFrom":makeQuery(id+"F3.opExtrude","SWEPT_BODY",BODY,{"disambiguationData":[OSD([sQuery(id+"F1.wireOp",EDGE,"E9.0.25.0")])]}),"instanceName":"21"});
            var Q49;
            Q49=makeQuery(id+"F46.opPattern","COPY",BODY,{"derivedFrom":makeQuery(id+"F3.opExtrude","SWEPT_BODY",BODY,{"disambiguationData":[OSD([sQuery(id+"F1.wireOp",EDGE,"E9.0.25.0")])]}),"instanceName":"31"});
            var Q50;
            Q50=makeQuery(id+"F46.opPattern","COPY",BODY,{"derivedFrom":makeQuery(id+"F3.opExtrude","SWEPT_BODY",BODY,{"disambiguationData":[OSD([sQuery(id+"F1.wireOp",EDGE,"E9.0.24.0")])]}),"instanceName":"29"});
            var Q51;
            Q51=makeQuery(id+"F46.opPattern","COPY",BODY,{"derivedFrom":makeQuery(id+"F3.opExtrude","SWEPT_BODY",BODY,{"disambiguationData":[OSD([sQuery(id+"F1.wireOp",EDGE,"E9.0.24.0")])]}),"instanceName":"22"});
            var Q52;
            Q52=makeQuery(id+"F46.opPattern","COPY",BODY,{"derivedFrom":makeQuery(id+"F3.opExtrude","SWEPT_BODY",BODY,{"disambiguationData":[OSD([sQuery(id+"F1.wireOp",EDGE,"E9.0.25.0")])]}),"instanceName":"28"});
            var Q53;
            Q53=makeQuery(id+"F46.opPattern","COPY",BODY,{"derivedFrom":makeQuery(id+"F3.opExtrude","SWEPT_BODY",BODY,{"disambiguationData":[OSD([sQuery(id+"F1.wireOp",EDGE,"E9.0.25.0")])]}),"instanceName":"5"});
            var Q54;
            Q54=makeQuery(id+"F46.opPattern","COPY",BODY,{"derivedFrom":makeQuery(id+"F3.opExtrude","SWEPT_BODY",BODY,{"disambiguationData":[OSD([sQuery(id+"F1.wireOp",EDGE,"E9.0.24.0")])]}),"instanceName":"28"});
            var Q55;
            Q55=makeQuery(id+"F46.opPattern","COPY",BODY,{"derivedFrom":makeQuery(id+"F3.opExtrude","SWEPT_BODY",BODY,{"disambiguationData":[OSD([sQuery(id+"F1.wireOp",EDGE,"E9.0.24.0")])]}),"instanceName":"5"});
            var Q56;
            Q56=makeQuery(id+"F46.opPattern","COPY",BODY,{"derivedFrom":makeQuery(id+"F3.opExtrude","SWEPT_BODY",BODY,{"disambiguationData":[OSD([sQuery(id+"F1.wireOp",EDGE,"E9.0.24.0")])]}),"instanceName":"32"});
            var Q57;
            Q57=makeQuery(id+"F48.opPattern","COPY",BODY,{"derivedFrom":makeQuery(id+"F3.opExtrude","SWEPT_BODY",BODY,{"disambiguationData":[OSD([sQuery(id+"F1.wireOp",EDGE,"E9.0.21.0")])]}),"instanceName":"5"});
            var Q58;
            Q58=makeQuery(id+"F46.opPattern","COPY",BODY,{"derivedFrom":makeQuery(id+"F3.opExtrude","SWEPT_BODY",BODY,{"disambiguationData":[OSD([sQuery(id+"F1.wireOp",EDGE,"E9.0.25.0")])]}),"instanceName":"27"});
            var Q59;
            Q59=makeQuery(id+"F46.opPattern","COPY",BODY,{"derivedFrom":makeQuery(id+"F3.opExtrude","SWEPT_BODY",BODY,{"disambiguationData":[OSD([sQuery(id+"F1.wireOp",EDGE,"E9.0.25.0")])]}),"instanceName":"4"});
            var Q60;
            Q60=makeQuery(id+"F46.opPattern","COPY",BODY,{"derivedFrom":makeQuery(id+"F3.opExtrude","SWEPT_BODY",BODY,{"disambiguationData":[OSD([sQuery(id+"F1.wireOp",EDGE,"E9.0.25.0")])]}),"instanceName":"22"});
            var Q61;
            Q61=makeQuery(id+"F46.opPattern","COPY",BODY,{"derivedFrom":makeQuery(id+"F3.opExtrude","SWEPT_BODY",BODY,{"disambiguationData":[OSD([sQuery(id+"F1.wireOp",EDGE,"E9.0.24.0")])]}),"instanceName":"23"});
            var Q62;
            Q62=makeQuery(id+"F45.opPattern","COPY",BODY,{"derivedFrom":makeQuery(id+"F3.opExtrude","SWEPT_BODY",BODY,{"disambiguationData":[OSD([sQuery(id+"F1.wireOp",EDGE,"E9.0.27.0")])]}),"instanceName":"7"});
            var Q63;
            Q63=makeQuery(id+"F46.opPattern","COPY",BODY,{"derivedFrom":makeQuery(id+"F3.opExtrude","SWEPT_BODY",BODY,{"disambiguationData":[OSD([sQuery(id+"F1.wireOp",EDGE,"E9.0.24.0")])]}),"instanceName":"4"});
            var Q64;
            Q64=makeQuery(id+"F48.opPattern","COPY",BODY,{"derivedFrom":makeQuery(id+"F3.opExtrude","SWEPT_BODY",BODY,{"disambiguationData":[OSD([sQuery(id+"F1.wireOp",EDGE,"E9.0.22.0")])]}),"instanceName":"4"});
            var Q65;
            Q65=makeQuery(id+"F46.opPattern","COPY",BODY,{"derivedFrom":makeQuery(id+"F3.opExtrude","SWEPT_BODY",BODY,{"disambiguationData":[OSD([sQuery(id+"F1.wireOp",EDGE,"E9.0.25.0")])]}),"instanceName":"3"});
            var Q66;
            Q66=makeQuery(id+"F47.opPattern","COPY",BODY,{"derivedFrom":makeQuery(id+"F3.opExtrude","SWEPT_BODY",BODY,{"disambiguationData":[OSD([sQuery(id+"F1.wireOp",EDGE,"E9.0.23.0")])]}),"instanceName":"9"});
            var Q67;
            Q67=makeQuery(id+"F46.opPattern","COPY",BODY,{"derivedFrom":makeQuery(id+"F3.opExtrude","SWEPT_BODY",BODY,{"disambiguationData":[OSD([sQuery(id+"F1.wireOp",EDGE,"E9.0.24.0")])]}),"instanceName":"3"});
            var Q68;
            Q68=makeQuery(id+"F48.opPattern","COPY",BODY,{"derivedFrom":makeQuery(id+"F3.opExtrude","SWEPT_BODY",BODY,{"disambiguationData":[OSD([sQuery(id+"F1.wireOp",EDGE,"E9.0.21.0")])]}),"instanceName":"4"});
            var Q69;
            Q69=makeQuery(id+"F45.opPattern","COPY",BODY,{"derivedFrom":makeQuery(id+"F3.opExtrude","SWEPT_BODY",BODY,{"disambiguationData":[OSD([sQuery(id+"F1.wireOp",EDGE,"E9.0.26.0")])]}),"instanceName":"17"});
            var Q70;
            Q70=makeQuery(id+"F45.opPattern","COPY",BODY,{"derivedFrom":makeQuery(id+"F3.opExtrude","SWEPT_BODY",BODY,{"disambiguationData":[OSD([sQuery(id+"F1.wireOp",EDGE,"E9.0.27.0")])]}),"instanceName":"24"});
            var Q71;
            Q71=makeQuery(id+"F45.opPattern","COPY",BODY,{"derivedFrom":makeQuery(id+"F3.opExtrude","SWEPT_BODY",BODY,{"disambiguationData":[OSD([sQuery(id+"F1.wireOp",EDGE,"E9.0.27.0")])]}),"instanceName":"15"});
            var Q72;
            Q72=makeQuery(id+"F48.opPattern","COPY",BODY,{"derivedFrom":makeQuery(id+"F3.opExtrude","SWEPT_BODY",BODY,{"disambiguationData":[OSD([sQuery(id+"F1.wireOp",EDGE,"E9.0.22.0")])]}),"instanceName":"3"});
            var Q73;
            Q73=makeQuery(id+"F48.opPattern","COPY",BODY,{"derivedFrom":makeQuery(id+"F3.opExtrude","SWEPT_BODY",BODY,{"disambiguationData":[OSD([sQuery(id+"F1.wireOp",EDGE,"E9.0.21.0")])]}),"instanceName":"3"});
            var Q74;
            Q74=makeQuery(id+"F46.opPattern","COPY",BODY,{"derivedFrom":makeQuery(id+"F3.opExtrude","SWEPT_BODY",BODY,{"disambiguationData":[OSD([sQuery(id+"F1.wireOp",EDGE,"E9.0.25.0")])]}),"instanceName":"1"});
            var Q75;
            Q75=makeQuery(id+"F46.opPattern","COPY",BODY,{"derivedFrom":makeQuery(id+"F3.opExtrude","SWEPT_BODY",BODY,{"disambiguationData":[OSD([sQuery(id+"F1.wireOp",EDGE,"E9.0.25.0")])]}),"instanceName":"23"});
            var Q76;
            Q76=makeQuery(id+"F46.opPattern","COPY",BODY,{"derivedFrom":makeQuery(id+"F3.opExtrude","SWEPT_BODY",BODY,{"disambiguationData":[OSD([sQuery(id+"F1.wireOp",EDGE,"E9.0.24.0")])]}),"instanceName":"27"});
            var Q77;
            Q77=makeQuery(id+"F48.opPattern","COPY",BODY,{"derivedFrom":makeQuery(id+"F3.opExtrude","SWEPT_BODY",BODY,{"disambiguationData":[OSD([sQuery(id+"F1.wireOp",EDGE,"E9.0.22.0")])]}),"instanceName":"31"});
            var Q78;
            Q78=makeQuery(id+"F46.opPattern","COPY",BODY,{"derivedFrom":makeQuery(id+"F3.opExtrude","SWEPT_BODY",BODY,{"disambiguationData":[OSD([sQuery(id+"F1.wireOp",EDGE,"E9.0.24.0")])]}),"instanceName":"24"});
            var Q79;
            Q79=makeQuery(id+"F46.opPattern","COPY",BODY,{"derivedFrom":makeQuery(id+"F3.opExtrude","SWEPT_BODY",BODY,{"disambiguationData":[OSD([sQuery(id+"F1.wireOp",EDGE,"E9.0.24.0")])]}),"instanceName":"1"});
            var Q80;
            Q80=makeQuery(id+"F46.opPattern","COPY",BODY,{"derivedFrom":makeQuery(id+"F3.opExtrude","SWEPT_BODY",BODY,{"disambiguationData":[OSD([sQuery(id+"F1.wireOp",EDGE,"E9.0.25.0")])]}),"instanceName":"24"});
            var Q81;
            Q81=makeQuery(id+"F45.opPattern","COPY",BODY,{"derivedFrom":makeQuery(id+"F3.opExtrude","SWEPT_BODY",BODY,{"disambiguationData":[OSD([sQuery(id+"F1.wireOp",EDGE,"E9.0.26.0")])]}),"instanceName":"8"});
            var Q82;
            Q82=makeQuery(id+"F48.opPattern","COPY",BODY,{"derivedFrom":makeQuery(id+"F3.opExtrude","SWEPT_BODY",BODY,{"disambiguationData":[OSD([sQuery(id+"F1.wireOp",EDGE,"E9.0.22.0")])]}),"instanceName":"14"});
            var Q83;
            Q83=makeQuery(id+"F45.opPattern","COPY",BODY,{"derivedFrom":makeQuery(id+"F3.opExtrude","SWEPT_BODY",BODY,{"disambiguationData":[OSD([sQuery(id+"F1.wireOp",EDGE,"E9.0.26.0")])]}),"instanceName":"16"});
            var Q84;
            Q84=makeQuery(id+"F45.opPattern","COPY",BODY,{"derivedFrom":makeQuery(id+"F3.opExtrude","SWEPT_BODY",BODY,{"disambiguationData":[OSD([sQuery(id+"F1.wireOp",EDGE,"E9.0.26.0")])]}),"instanceName":"19"});
            var Q85;
            Q85=makeQuery(id+"F48.opPattern","COPY",BODY,{"derivedFrom":makeQuery(id+"F3.opExtrude","SWEPT_BODY",BODY,{"disambiguationData":[OSD([sQuery(id+"F1.wireOp",EDGE,"E9.0.22.0")])]}),"instanceName":"29"});
            var Q86;
            Q86=makeQuery(id+"F47.opPattern","COPY",BODY,{"derivedFrom":makeQuery(id+"F3.opExtrude","SWEPT_BODY",BODY,{"disambiguationData":[OSD([sQuery(id+"F1.wireOp",EDGE,"E9.0.23.0")])]}),"instanceName":"18"});
            var Q87;
            Q87=makeQuery(id+"F47.opPattern","COPY",BODY,{"derivedFrom":makeQuery(id+"F3.opExtrude","SWEPT_BODY",BODY,{"disambiguationData":[OSD([sQuery(id+"F1.wireOp",EDGE,"E9.0.23.0")])]}),"instanceName":"19"});
            var Q88;
            Q88=makeQuery(id+"F48.opPattern","COPY",BODY,{"derivedFrom":makeQuery(id+"F3.opExtrude","SWEPT_BODY",BODY,{"disambiguationData":[OSD([sQuery(id+"F1.wireOp",EDGE,"E9.0.22.0")])]}),"instanceName":"1"});
            var Q89;
            Q89=makeQuery(id+"F48.opPattern","COPY",BODY,{"derivedFrom":makeQuery(id+"F3.opExtrude","SWEPT_BODY",BODY,{"disambiguationData":[OSD([sQuery(id+"F1.wireOp",EDGE,"E9.0.21.0")])]}),"instanceName":"1"});
            var Q90;
            Q90=makeQuery(id+"F45.opPattern","COPY",BODY,{"derivedFrom":makeQuery(id+"F3.opExtrude","SWEPT_BODY",BODY,{"disambiguationData":[OSD([sQuery(id+"F1.wireOp",EDGE,"E9.0.26.0")])]}),"instanceName":"18"});
            var Q91;
            Q91=makeQuery(id+"F47.opPattern","COPY",BODY,{"derivedFrom":makeQuery(id+"F3.opExtrude","SWEPT_BODY",BODY,{"disambiguationData":[OSD([sQuery(id+"F1.wireOp",EDGE,"E9.0.23.0")])]}),"instanceName":"20"});
            var Q92;
            Q92=makeQuery(id+"F47.opPattern","COPY",BODY,{"derivedFrom":makeQuery(id+"F3.opExtrude","SWEPT_BODY",BODY,{"disambiguationData":[OSD([sQuery(id+"F1.wireOp",EDGE,"E9.0.23.0")])]}),"instanceName":"21"});
            var Q93;
            Q93=makeQuery(id+"F47.opPattern","COPY",BODY,{"derivedFrom":makeQuery(id+"F3.opExtrude","SWEPT_BODY",BODY,{"disambiguationData":[OSD([sQuery(id+"F1.wireOp",EDGE,"E9.0.23.0")])]}),"instanceName":"22"});
            var Q94;
            Q94=makeQuery(id+"F46.opPattern","COPY",BODY,{"derivedFrom":makeQuery(id+"F3.opExtrude","SWEPT_BODY",BODY,{"disambiguationData":[OSD([sQuery(id+"F1.wireOp",EDGE,"E9.0.24.0")])]}),"instanceName":"25"});
            var Q95;
            Q95=makeQuery(id+"F46.opPattern","COPY",BODY,{"derivedFrom":makeQuery(id+"F3.opExtrude","SWEPT_BODY",BODY,{"disambiguationData":[OSD([sQuery(id+"F1.wireOp",EDGE,"E9.0.25.0")])]}),"instanceName":"25"});
            var Q96;
            Q96=makeQuery(id+"F47.opPattern","COPY",BODY,{"derivedFrom":makeQuery(id+"F3.opExtrude","SWEPT_BODY",BODY,{"disambiguationData":[OSD([sQuery(id+"F1.wireOp",EDGE,"E9.0.23.0")])]}),"instanceName":"23"});
            var Q97;
            Q97=makeQuery(id+"F45.opPattern","COPY",BODY,{"derivedFrom":makeQuery(id+"F3.opExtrude","SWEPT_BODY",BODY,{"disambiguationData":[OSD([sQuery(id+"F1.wireOp",EDGE,"E9.0.27.0")])]}),"instanceName":"14"});
            var Q98;
            Q98=makeQuery(id+"F45.opPattern","COPY",BODY,{"derivedFrom":makeQuery(id+"F3.opExtrude","SWEPT_BODY",BODY,{"disambiguationData":[OSD([sQuery(id+"F1.wireOp",EDGE,"E9.0.27.0")])]}),"instanceName":"8"});
            var Q99;
            Q99=makeQuery(id+"F47.opPattern","COPY",BODY,{"derivedFrom":makeQuery(id+"F3.opExtrude","SWEPT_BODY",BODY,{"disambiguationData":[OSD([sQuery(id+"F1.wireOp",EDGE,"E9.0.23.0")])]}),"instanceName":"38"});
            var Q100;
            Q100=makeQuery(id+"F45.opPattern","COPY",BODY,{"derivedFrom":makeQuery(id+"F3.opExtrude","SWEPT_BODY",BODY,{"disambiguationData":[OSD([sQuery(id+"F1.wireOp",EDGE,"E9.0.27.0")])]}),"instanceName":"36"});
            var Q101;
            Q101=makeQuery(id+"F47.opPattern","COPY",BODY,{"derivedFrom":makeQuery(id+"F3.opExtrude","SWEPT_BODY",BODY,{"disambiguationData":[OSD([sQuery(id+"F1.wireOp",EDGE,"E9.0.23.0")])]}),"instanceName":"24"});
            var Q102;
            Q102=makeQuery(id+"F48.opPattern","COPY",BODY,{"derivedFrom":makeQuery(id+"F3.opExtrude","SWEPT_BODY",BODY,{"disambiguationData":[OSD([sQuery(id+"F1.wireOp",EDGE,"E9.0.21.0")])]}),"instanceName":"31"});
            var Q103;
            Q103=makeQuery(id+"F46.opPattern","COPY",BODY,{"derivedFrom":makeQuery(id+"F3.opExtrude","SWEPT_BODY",BODY,{"disambiguationData":[OSD([sQuery(id+"F1.wireOp",EDGE,"E9.0.24.0")])]}),"instanceName":"26"});
            var Q104;
            Q104=makeQuery(id+"F45.opPattern","COPY",BODY,{"derivedFrom":makeQuery(id+"F3.opExtrude","SWEPT_BODY",BODY,{"disambiguationData":[OSD([sQuery(id+"F1.wireOp",EDGE,"E9.0.26.0")])]}),"instanceName":"9"});
            var Q105;
            Q105=makeQuery(id+"F47.opPattern","COPY",BODY,{"derivedFrom":makeQuery(id+"F3.opExtrude","SWEPT_BODY",BODY,{"disambiguationData":[OSD([sQuery(id+"F1.wireOp",EDGE,"E9.0.23.0")])]}),"instanceName":"25"});
            var Q106;
            Q106=makeQuery(id+"F46.opPattern","COPY",BODY,{"derivedFrom":makeQuery(id+"F3.opExtrude","SWEPT_BODY",BODY,{"disambiguationData":[OSD([sQuery(id+"F1.wireOp",EDGE,"E9.0.25.0")])]}),"instanceName":"26"});
            var Q107;
            Q107=makeQuery(id+"F45.opPattern","COPY",BODY,{"derivedFrom":makeQuery(id+"F3.opExtrude","SWEPT_BODY",BODY,{"disambiguationData":[OSD([sQuery(id+"F1.wireOp",EDGE,"E9.0.26.0")])]}),"instanceName":"13"});
            var Q108;
            Q108=makeQuery(id+"F45.opPattern","COPY",BODY,{"derivedFrom":makeQuery(id+"F3.opExtrude","SWEPT_BODY",BODY,{"disambiguationData":[OSD([sQuery(id+"F1.wireOp",EDGE,"E9.0.26.0")])]}),"instanceName":"36"});
            var Q109;
            Q109=makeQuery(id+"F45.opPattern","COPY",BODY,{"derivedFrom":makeQuery(id+"F3.opExtrude","SWEPT_BODY",BODY,{"disambiguationData":[OSD([sQuery(id+"F1.wireOp",EDGE,"E9.0.27.0")])]}),"instanceName":"35"});
            var Q110;
            Q110=makeQuery(id+"F45.opPattern","COPY",BODY,{"derivedFrom":makeQuery(id+"F3.opExtrude","SWEPT_BODY",BODY,{"disambiguationData":[OSD([sQuery(id+"F1.wireOp",EDGE,"E9.0.26.0")])]}),"instanceName":"35"});
            var Q111;
            Q111=makeQuery(id+"F45.opPattern","COPY",BODY,{"derivedFrom":makeQuery(id+"F3.opExtrude","SWEPT_BODY",BODY,{"disambiguationData":[OSD([sQuery(id+"F1.wireOp",EDGE,"E9.0.27.0")])]}),"instanceName":"9"});
            var Q112;
            Q112=makeQuery(id+"F46.opPattern","COPY",BODY,{"derivedFrom":makeQuery(id+"F3.opExtrude","SWEPT_BODY",BODY,{"disambiguationData":[OSD([sQuery(id+"F1.wireOp",EDGE,"E9.0.24.0")])]}),"instanceName":"36"});
            var Q113;
            Q113=makeQuery(id+"F47.opPattern","COPY",BODY,{"derivedFrom":makeQuery(id+"F3.opExtrude","SWEPT_BODY",BODY,{"disambiguationData":[OSD([sQuery(id+"F1.wireOp",EDGE,"E9.0.23.0")])]}),"instanceName":"26"});
            var Q114;
            Q114=makeQuery(id+"F47.opPattern","COPY",BODY,{"derivedFrom":makeQuery(id+"F3.opExtrude","SWEPT_BODY",BODY,{"disambiguationData":[OSD([sQuery(id+"F1.wireOp",EDGE,"E9.0.23.0")])]}),"instanceName":"37"});
            var Q115;
            Q115=makeQuery(id+"F48.opPattern","COPY",BODY,{"derivedFrom":makeQuery(id+"F3.opExtrude","SWEPT_BODY",BODY,{"disambiguationData":[OSD([sQuery(id+"F1.wireOp",EDGE,"E9.0.22.0")])]}),"instanceName":"34"});
            var Q116;
            Q116=makeQuery(id+"F48.opPattern","COPY",BODY,{"derivedFrom":makeQuery(id+"F3.opExtrude","SWEPT_BODY",BODY,{"disambiguationData":[OSD([sQuery(id+"F1.wireOp",EDGE,"E9.0.21.0")])]}),"instanceName":"32"});
            var Q117;
            Q117=makeQuery(id+"F45.opPattern","COPY",BODY,{"derivedFrom":makeQuery(id+"F3.opExtrude","SWEPT_BODY",BODY,{"disambiguationData":[OSD([sQuery(id+"F1.wireOp",EDGE,"E9.0.27.0")])]}),"instanceName":"34"});
            var Q118;
            Q118=makeQuery(id+"F47.opPattern","COPY",BODY,{"derivedFrom":makeQuery(id+"F3.opExtrude","SWEPT_BODY",BODY,{"disambiguationData":[OSD([sQuery(id+"F1.wireOp",EDGE,"E9.0.23.0")])]}),"instanceName":"36"});
            var Q119;
            Q119=makeQuery(id+"F48.opPattern","COPY",BODY,{"derivedFrom":makeQuery(id+"F3.opExtrude","SWEPT_BODY",BODY,{"disambiguationData":[OSD([sQuery(id+"F1.wireOp",EDGE,"E9.0.22.0")])]}),"instanceName":"24"});
            var Q120;
            Q120=makeQuery(id+"F48.opPattern","COPY",BODY,{"derivedFrom":makeQuery(id+"F3.opExtrude","SWEPT_BODY",BODY,{"disambiguationData":[OSD([sQuery(id+"F1.wireOp",EDGE,"E9.0.22.0")])]}),"instanceName":"23"});
            var Q121;
            Q121=makeQuery(id+"F48.opPattern","COPY",BODY,{"derivedFrom":makeQuery(id+"F3.opExtrude","SWEPT_BODY",BODY,{"disambiguationData":[OSD([sQuery(id+"F1.wireOp",EDGE,"E9.0.21.0")])]}),"instanceName":"24"});
            var Q122;
            Q122=makeQuery(id+"F48.opPattern","COPY",BODY,{"derivedFrom":makeQuery(id+"F3.opExtrude","SWEPT_BODY",BODY,{"disambiguationData":[OSD([sQuery(id+"F1.wireOp",EDGE,"E9.0.21.0")])]}),"instanceName":"33"});
            var Q123;
            Q123=makeQuery(id+"F48.opPattern","COPY",BODY,{"derivedFrom":makeQuery(id+"F3.opExtrude","SWEPT_BODY",BODY,{"disambiguationData":[OSD([sQuery(id+"F1.wireOp",EDGE,"E9.0.21.0")])]}),"instanceName":"34"});
            var Q124;
            Q124=makeQuery(id+"F45.opPattern","COPY",BODY,{"derivedFrom":makeQuery(id+"F3.opExtrude","SWEPT_BODY",BODY,{"disambiguationData":[OSD([sQuery(id+"F1.wireOp",EDGE,"E9.0.26.0")])]}),"instanceName":"10"});
            var Q125;
            Q125=makeQuery(id+"F48.opPattern","COPY",BODY,{"derivedFrom":makeQuery(id+"F3.opExtrude","SWEPT_BODY",BODY,{"disambiguationData":[OSD([sQuery(id+"F1.wireOp",EDGE,"E9.0.21.0")])]}),"instanceName":"35"});
            var Q126;
            Q126=makeQuery(id+"F45.opPattern","COPY",BODY,{"derivedFrom":makeQuery(id+"F3.opExtrude","SWEPT_BODY",BODY,{"disambiguationData":[OSD([sQuery(id+"F1.wireOp",EDGE,"E9.0.27.0")])]}),"instanceName":"19"});
            var Q127;
            Q127=makeQuery(id+"F48.opPattern","COPY",BODY,{"derivedFrom":makeQuery(id+"F3.opExtrude","SWEPT_BODY",BODY,{"disambiguationData":[OSD([sQuery(id+"F1.wireOp",EDGE,"E9.0.21.0")])]}),"instanceName":"15"});
            var Q128;
            Q128=makeQuery(id+"F48.opPattern","COPY",BODY,{"derivedFrom":makeQuery(id+"F3.opExtrude","SWEPT_BODY",BODY,{"disambiguationData":[OSD([sQuery(id+"F1.wireOp",EDGE,"E9.0.22.0")])]}),"instanceName":"35"});
            var Q129;
            Q129=makeQuery(id+"F48.opPattern","COPY",BODY,{"derivedFrom":makeQuery(id+"F3.opExtrude","SWEPT_BODY",BODY,{"disambiguationData":[OSD([sQuery(id+"F1.wireOp",EDGE,"E9.0.21.0")])]}),"instanceName":"23"});
            var Q130;
            Q130=makeQuery(id+"F45.opPattern","COPY",BODY,{"derivedFrom":makeQuery(id+"F3.opExtrude","SWEPT_BODY",BODY,{"disambiguationData":[OSD([sQuery(id+"F1.wireOp",EDGE,"E9.0.27.0")])]}),"instanceName":"10"});
            var Q131;
            Q131=makeQuery(id+"F45.opPattern","COPY",BODY,{"derivedFrom":makeQuery(id+"F3.opExtrude","SWEPT_BODY",BODY,{"disambiguationData":[OSD([sQuery(id+"F1.wireOp",EDGE,"E9.0.26.0")])]}),"instanceName":"11"});
            var Q132;
            Q132=makeQuery(id+"F46.opPattern","COPY",BODY,{"derivedFrom":makeQuery(id+"F3.opExtrude","SWEPT_BODY",BODY,{"disambiguationData":[OSD([sQuery(id+"F1.wireOp",EDGE,"E9.0.24.0")])]}),"instanceName":"35"});
            var Q133;
            Q133=makeQuery(id+"F48.opPattern","COPY",BODY,{"derivedFrom":makeQuery(id+"F3.opExtrude","SWEPT_BODY",BODY,{"disambiguationData":[OSD([sQuery(id+"F1.wireOp",EDGE,"E9.0.22.0")])]}),"instanceName":"22"});
            var Q134;
            Q134=makeQuery(id+"F48.opPattern","COPY",BODY,{"derivedFrom":makeQuery(id+"F3.opExtrude","SWEPT_BODY",BODY,{"disambiguationData":[OSD([sQuery(id+"F1.wireOp",EDGE,"E9.0.21.0")])]}),"instanceName":"36"});
            var Q135;
            Q135=makeQuery(id+"F48.opPattern","COPY",BODY,{"derivedFrom":makeQuery(id+"F3.opExtrude","SWEPT_BODY",BODY,{"disambiguationData":[OSD([sQuery(id+"F1.wireOp",EDGE,"E9.0.22.0")])]}),"instanceName":"36"});
            var Q136;
            Q136=makeQuery(id+"F48.opPattern","COPY",BODY,{"derivedFrom":makeQuery(id+"F3.opExtrude","SWEPT_BODY",BODY,{"disambiguationData":[OSD([sQuery(id+"F1.wireOp",EDGE,"E9.0.21.0")])]}),"instanceName":"37"});
            var Q137;
            Q137=makeQuery(id+"F45.opPattern","COPY",BODY,{"derivedFrom":makeQuery(id+"F3.opExtrude","SWEPT_BODY",BODY,{"disambiguationData":[OSD([sQuery(id+"F1.wireOp",EDGE,"E9.0.26.0")])]}),"instanceName":"22"});
            var Q138;
            Q138=makeQuery(id+"F45.opPattern","COPY",BODY,{"derivedFrom":makeQuery(id+"F3.opExtrude","SWEPT_BODY",BODY,{"disambiguationData":[OSD([sQuery(id+"F1.wireOp",EDGE,"E9.0.26.0")])]}),"instanceName":"15"});
            var Q139;
            Q139=makeQuery(id+"F46.opPattern","COPY",BODY,{"derivedFrom":makeQuery(id+"F3.opExtrude","SWEPT_BODY",BODY,{"disambiguationData":[OSD([sQuery(id+"F1.wireOp",EDGE,"E9.0.25.0")])]}),"instanceName":"34"});
            var Q140;
            Q140=makeQuery(id+"F48.opPattern","COPY",BODY,{"derivedFrom":makeQuery(id+"F3.opExtrude","SWEPT_BODY",BODY,{"disambiguationData":[OSD([sQuery(id+"F1.wireOp",EDGE,"E9.0.21.0")])]}),"instanceName":"22"});
            var Q141;
            Q141=makeQuery(id+"F48.opPattern","COPY",BODY,{"derivedFrom":makeQuery(id+"F3.opExtrude","SWEPT_BODY",BODY,{"disambiguationData":[OSD([sQuery(id+"F1.wireOp",EDGE,"E9.0.22.0")])]}),"instanceName":"21"});
            var Q142;
            Q142=makeQuery(id+"F48.opPattern","COPY",BODY,{"derivedFrom":makeQuery(id+"F3.opExtrude","SWEPT_BODY",BODY,{"disambiguationData":[OSD([sQuery(id+"F1.wireOp",EDGE,"E9.0.21.0")])]}),"instanceName":"38"});
            var Q143;
            Q143=makeQuery(id+"F46.opPattern","COPY",BODY,{"derivedFrom":makeQuery(id+"F3.opExtrude","SWEPT_BODY",BODY,{"disambiguationData":[OSD([sQuery(id+"F1.wireOp",EDGE,"E9.0.24.0")])]}),"instanceName":"34"});
            var Q144;
            Q144=makeQuery(id+"F46.opPattern","COPY",BODY,{"derivedFrom":makeQuery(id+"F3.opExtrude","SWEPT_BODY",BODY,{"disambiguationData":[OSD([sQuery(id+"F1.wireOp",EDGE,"E9.0.25.0")])]}),"instanceName":"36"});
            var Q145;
            Q145=makeQuery(id+"F47.opPattern","COPY",BODY,{"derivedFrom":makeQuery(id+"F3.opExtrude","SWEPT_BODY",BODY,{"disambiguationData":[OSD([sQuery(id+"F1.wireOp",EDGE,"E9.0.23.0")])]}),"instanceName":"34"});
            var Q146;
            Q146=makeQuery(id+"F47.opPattern","COPY",BODY,{"derivedFrom":makeQuery(id+"F3.opExtrude","SWEPT_BODY",BODY,{"disambiguationData":[OSD([sQuery(id+"F1.wireOp",EDGE,"E9.0.23.0")])]}),"instanceName":"35"});
            var Q147;
            Q147=makeQuery(id+"F45.opPattern","COPY",BODY,{"derivedFrom":makeQuery(id+"F3.opExtrude","SWEPT_BODY",BODY,{"disambiguationData":[OSD([sQuery(id+"F1.wireOp",EDGE,"E9.0.27.0")])]}),"instanceName":"11"});
            var Q148;
            Q148=makeQuery(id+"F48.opPattern","COPY",BODY,{"derivedFrom":makeQuery(id+"F3.opExtrude","SWEPT_BODY",BODY,{"disambiguationData":[OSD([sQuery(id+"F1.wireOp",EDGE,"E9.0.21.0")])]}),"instanceName":"21"});
            var Q149;
            Q149=makeQuery(id+"F48.opPattern","COPY",BODY,{"derivedFrom":makeQuery(id+"F3.opExtrude","SWEPT_BODY",BODY,{"disambiguationData":[OSD([sQuery(id+"F1.wireOp",EDGE,"E9.0.22.0")])]}),"instanceName":"38"});
            var Q150;
            Q150=makeQuery(id+"F46.opPattern","COPY",BODY,{"derivedFrom":makeQuery(id+"F3.opExtrude","SWEPT_BODY",BODY,{"disambiguationData":[OSD([sQuery(id+"F1.wireOp",EDGE,"E9.0.24.0")])]}),"instanceName":"37"});
            var Q151;
            Q151=makeQuery(id+"F47.opPattern","COPY",BODY,{"derivedFrom":makeQuery(id+"F3.opExtrude","SWEPT_BODY",BODY,{"disambiguationData":[OSD([sQuery(id+"F1.wireOp",EDGE,"E9.0.23.0")])]}),"instanceName":"29"});
            var Q152;
            Q152=makeQuery(id+"F48.opPattern","COPY",BODY,{"derivedFrom":makeQuery(id+"F3.opExtrude","SWEPT_BODY",BODY,{"disambiguationData":[OSD([sQuery(id+"F1.wireOp",EDGE,"E9.0.22.0")])]}),"instanceName":"20"});
            var Q153;
            Q153=makeQuery(id+"F48.opPattern","COPY",BODY,{"derivedFrom":makeQuery(id+"F3.opExtrude","SWEPT_BODY",BODY,{"disambiguationData":[OSD([sQuery(id+"F1.wireOp",EDGE,"E9.0.21.0")])]}),"instanceName":"20"});
            var Q154;
            Q154=makeQuery(id+"F48.opPattern","COPY",BODY,{"derivedFrom":makeQuery(id+"F3.opExtrude","SWEPT_BODY",BODY,{"disambiguationData":[OSD([sQuery(id+"F1.wireOp",EDGE,"E9.0.21.0")])]}),"instanceName":"39"});
            var Q155;
            Q155=makeQuery(id+"F48.opPattern","COPY",BODY,{"derivedFrom":makeQuery(id+"F3.opExtrude","SWEPT_BODY",BODY,{"disambiguationData":[OSD([sQuery(id+"F1.wireOp",EDGE,"E9.0.22.0")])]}),"instanceName":"19"});
            var Q156;
            Q156=makeQuery(id+"F46.opPattern","COPY",BODY,{"derivedFrom":makeQuery(id+"F3.opExtrude","SWEPT_BODY",BODY,{"disambiguationData":[OSD([sQuery(id+"F1.wireOp",EDGE,"E9.0.25.0")])]}),"instanceName":"33"});
            var Q157;
            Q157=makeQuery(id+"F48.opPattern","COPY",BODY,{"derivedFrom":makeQuery(id+"F3.opExtrude","SWEPT_BODY",BODY,{"disambiguationData":[OSD([sQuery(id+"F1.wireOp",EDGE,"E9.0.22.0")])]}),"instanceName":"39"});
            var Q158;
            Q158=makeQuery(id+"F45.opPattern","COPY",BODY,{"derivedFrom":makeQuery(id+"F3.opExtrude","SWEPT_BODY",BODY,{"disambiguationData":[OSD([sQuery(id+"F1.wireOp",EDGE,"E9.0.26.0")])]}),"instanceName":"12"});
            var Q159;
            Q159=makeQuery(id+"F47.opPattern","COPY",BODY,{"derivedFrom":makeQuery(id+"F3.opExtrude","SWEPT_BODY",BODY,{"disambiguationData":[OSD([sQuery(id+"F1.wireOp",EDGE,"E9.0.23.0")])]}),"instanceName":"30"});
            var Q160;
            Q160=makeQuery(id+"F45.opPattern","COPY",BODY,{"derivedFrom":makeQuery(id+"F3.opExtrude","SWEPT_BODY",BODY,{"disambiguationData":[OSD([sQuery(id+"F1.wireOp",EDGE,"E9.0.26.0")])]}),"instanceName":"34"});
            var Q161;
            Q161=makeQuery(id+"F47.opPattern","COPY",BODY,{"derivedFrom":makeQuery(id+"F3.opExtrude","SWEPT_BODY",BODY,{"disambiguationData":[OSD([sQuery(id+"F1.wireOp",EDGE,"E9.0.23.0")])]}),"instanceName":"16"});
            var Q162;
            Q162=makeQuery(id+"F45.opPattern","COPY",BODY,{"derivedFrom":makeQuery(id+"F3.opExtrude","SWEPT_BODY",BODY,{"disambiguationData":[OSD([sQuery(id+"F1.wireOp",EDGE,"E9.0.27.0")])]}),"instanceName":"21"});
            var Q163;
            Q163=makeQuery(id+"F45.opPattern","COPY",BODY,{"derivedFrom":makeQuery(id+"F3.opExtrude","SWEPT_BODY",BODY,{"disambiguationData":[OSD([sQuery(id+"F1.wireOp",EDGE,"E9.0.27.0")])]}),"instanceName":"22"});
            var Q164;
            Q164=makeQuery(id+"F45.opPattern","COPY",BODY,{"derivedFrom":makeQuery(id+"F3.opExtrude","SWEPT_BODY",BODY,{"disambiguationData":[OSD([sQuery(id+"F1.wireOp",EDGE,"E9.0.26.0")])]}),"instanceName":"23"});
            var Q165;
            Q165=makeQuery(id+"F48.opPattern","COPY",BODY,{"derivedFrom":makeQuery(id+"F3.opExtrude","SWEPT_BODY",BODY,{"disambiguationData":[OSD([sQuery(id+"F1.wireOp",EDGE,"E9.0.21.0")])]}),"instanceName":"16"});
            var Q166;
            Q166=makeQuery(id+"F47.opPattern","COPY",BODY,{"derivedFrom":makeQuery(id+"F3.opExtrude","SWEPT_BODY",BODY,{"disambiguationData":[OSD([sQuery(id+"F1.wireOp",EDGE,"E9.0.23.0")])]}),"instanceName":"27"});
            var Q167;
            Q167=makeQuery(id+"F48.opPattern","COPY",BODY,{"derivedFrom":makeQuery(id+"F3.opExtrude","SWEPT_BODY",BODY,{"disambiguationData":[OSD([sQuery(id+"F1.wireOp",EDGE,"E9.0.21.0")])]}),"instanceName":"19"});
            var Q168;
            Q168=makeQuery(id+"F47.opPattern","COPY",BODY,{"derivedFrom":makeQuery(id+"F3.opExtrude","SWEPT_BODY",BODY,{"disambiguationData":[OSD([sQuery(id+"F1.wireOp",EDGE,"E9.0.23.0")])]}),"instanceName":"15"});
            var Q169;
            Q169=makeQuery(id+"F48.opPattern","COPY",BODY,{"derivedFrom":makeQuery(id+"F3.opExtrude","SWEPT_BODY",BODY,{"disambiguationData":[OSD([sQuery(id+"F1.wireOp",EDGE,"E9.0.22.0")])]}),"instanceName":"18"});
            var Q170;
            Q170=makeQuery(id+"F46.opPattern","COPY",BODY,{"derivedFrom":makeQuery(id+"F3.opExtrude","SWEPT_BODY",BODY,{"disambiguationData":[OSD([sQuery(id+"F1.wireOp",EDGE,"E9.0.25.0")])]}),"instanceName":"37"});
            var Q171;
            Q171=makeQuery(id+"F47.opPattern","COPY",BODY,{"derivedFrom":makeQuery(id+"F3.opExtrude","SWEPT_BODY",BODY,{"disambiguationData":[OSD([sQuery(id+"F1.wireOp",EDGE,"E9.0.23.0")])]}),"instanceName":"10"});
            var Q172;
            Q172=makeQuery(id+"F48.opPattern","COPY",BODY,{"derivedFrom":makeQuery(id+"F3.opExtrude","SWEPT_BODY",BODY,{"disambiguationData":[OSD([sQuery(id+"F1.wireOp",EDGE,"E9.0.21.0")])]}),"instanceName":"18"});
            var Q173;
            Q173=makeQuery(id+"F46.opPattern","COPY",BODY,{"derivedFrom":makeQuery(id+"F3.opExtrude","SWEPT_BODY",BODY,{"disambiguationData":[OSD([sQuery(id+"F1.wireOp",EDGE,"E9.0.25.0")])]}),"instanceName":"32"});
            var Q174;
            Q174=makeQuery(id+"F45.opPattern","COPY",BODY,{"derivedFrom":makeQuery(id+"F3.opExtrude","SWEPT_BODY",BODY,{"disambiguationData":[OSD([sQuery(id+"F1.wireOp",EDGE,"E9.0.27.0")])]}),"instanceName":"12"});
            var Q175;
            Q175=makeQuery(id+"F47.opPattern","COPY",BODY,{"derivedFrom":makeQuery(id+"F3.opExtrude","SWEPT_BODY",BODY,{"disambiguationData":[OSD([sQuery(id+"F1.wireOp",EDGE,"E9.0.23.0")])]}),"instanceName":"28"});
            var Q176;
            Q176=makeQuery(id+"F46.opPattern","COPY",BODY,{"derivedFrom":makeQuery(id+"F3.opExtrude","SWEPT_BODY",BODY,{"disambiguationData":[OSD([sQuery(id+"F1.wireOp",EDGE,"E9.0.24.0")])]}),"instanceName":"12"});
            var Q177;
            Q177=makeQuery(id+"F46.opPattern","COPY",BODY,{"derivedFrom":makeQuery(id+"F3.opExtrude","SWEPT_BODY",BODY,{"disambiguationData":[OSD([sQuery(id+"F1.wireOp",EDGE,"E9.0.25.0")])]}),"instanceName":"12"});
            var Q178;
            Q178=makeQuery(id+"F45.opPattern","COPY",BODY,{"derivedFrom":makeQuery(id+"F3.opExtrude","SWEPT_BODY",BODY,{"disambiguationData":[OSD([sQuery(id+"F1.wireOp",EDGE,"E9.0.27.0")])]}),"instanceName":"13"});
            var Q179;
            Q179=makeQuery(id+"F45.opPattern","COPY",BODY,{"derivedFrom":makeQuery(id+"F3.opExtrude","SWEPT_BODY",BODY,{"disambiguationData":[OSD([sQuery(id+"F1.wireOp",EDGE,"E9.0.27.0")])]}),"instanceName":"18"});
            var Q180;
            Q180=makeQuery(id+"F45.opPattern","COPY",BODY,{"derivedFrom":makeQuery(id+"F3.opExtrude","SWEPT_BODY",BODY,{"disambiguationData":[OSD([sQuery(id+"F1.wireOp",EDGE,"E9.0.26.0")])]}),"instanceName":"25"});
            var Q181;
            Q181=makeQuery(id+"F45.opPattern","COPY",BODY,{"derivedFrom":makeQuery(id+"F3.opExtrude","SWEPT_BODY",BODY,{"disambiguationData":[OSD([sQuery(id+"F1.wireOp",EDGE,"E9.0.27.0")])]}),"instanceName":"25"});
            var Q182;
            Q182=makeQuery(id+"F45.opPattern","COPY",BODY,{"derivedFrom":makeQuery(id+"F3.opExtrude","SWEPT_BODY",BODY,{"disambiguationData":[OSD([sQuery(id+"F1.wireOp",EDGE,"E9.0.26.0")])]}),"instanceName":"26"});
            var Q183;
            Q183=makeQuery(id+"F48.opPattern","COPY",BODY,{"derivedFrom":makeQuery(id+"F3.opExtrude","SWEPT_BODY",BODY,{"disambiguationData":[OSD([sQuery(id+"F1.wireOp",EDGE,"E9.0.21.0")])]}),"instanceName":"14"});
            var Q184;
            Q184=makeQuery(id+"F47.opPattern","COPY",BODY,{"derivedFrom":makeQuery(id+"F3.opExtrude","SWEPT_BODY",BODY,{"disambiguationData":[OSD([sQuery(id+"F1.wireOp",EDGE,"E9.0.23.0")])]}),"instanceName":"1"});
            var Q185;
            Q185=makeQuery(id+"F45.opPattern","COPY",BODY,{"derivedFrom":makeQuery(id+"F3.opExtrude","SWEPT_BODY",BODY,{"disambiguationData":[OSD([sQuery(id+"F1.wireOp",EDGE,"E9.0.27.0")])]}),"instanceName":"26"});
            var Q186;
            Q186=makeQuery(id+"F45.opPattern","COPY",BODY,{"derivedFrom":makeQuery(id+"F3.opExtrude","SWEPT_BODY",BODY,{"disambiguationData":[OSD([sQuery(id+"F1.wireOp",EDGE,"E9.0.26.0")])]}),"instanceName":"27"});
            var Q187;
            Q187=makeQuery(id+"F48.opPattern","COPY",BODY,{"derivedFrom":makeQuery(id+"F3.opExtrude","SWEPT_BODY",BODY,{"disambiguationData":[OSD([sQuery(id+"F1.wireOp",EDGE,"E9.0.21.0")])]}),"instanceName":"29"});
            var Q188;
            Q188=makeQuery(id+"F47.opPattern","COPY",BODY,{"derivedFrom":makeQuery(id+"F3.opExtrude","SWEPT_BODY",BODY,{"disambiguationData":[OSD([sQuery(id+"F1.wireOp",EDGE,"E9.0.23.0")])]}),"instanceName":"3"});
            var Q189;
            Q189=makeQuery(id+"F48.opPattern","COPY",BODY,{"derivedFrom":makeQuery(id+"F3.opExtrude","SWEPT_BODY",BODY,{"disambiguationData":[OSD([sQuery(id+"F1.wireOp",EDGE,"E9.0.22.0")])]}),"instanceName":"28"});
            var Q190;
            Q190=makeQuery(id+"F48.opPattern","COPY",BODY,{"derivedFrom":makeQuery(id+"F3.opExtrude","SWEPT_BODY",BODY,{"disambiguationData":[OSD([sQuery(id+"F1.wireOp",EDGE,"E9.0.21.0")])]}),"instanceName":"28"});
            var Q191;
            Q191=makeQuery(id+"F45.opPattern","COPY",BODY,{"derivedFrom":makeQuery(id+"F3.opExtrude","SWEPT_BODY",BODY,{"disambiguationData":[OSD([sQuery(id+"F1.wireOp",EDGE,"E9.0.27.0")])]}),"instanceName":"27"});
            var Q192;
            Q192=makeQuery(id+"F48.opPattern","COPY",BODY,{"derivedFrom":makeQuery(id+"F3.opExtrude","SWEPT_BODY",BODY,{"disambiguationData":[OSD([sQuery(id+"F1.wireOp",EDGE,"E9.0.22.0")])]}),"instanceName":"30"});
            var Q193;
            Q193=makeQuery(id+"F45.opPattern","COPY",BODY,{"derivedFrom":makeQuery(id+"F3.opExtrude","SWEPT_BODY",BODY,{"disambiguationData":[OSD([sQuery(id+"F1.wireOp",EDGE,"E9.0.26.0")])]}),"instanceName":"28"});
            var Q194;
            Q194=makeQuery(id+"F48.opPattern","COPY",BODY,{"derivedFrom":makeQuery(id+"F3.opExtrude","SWEPT_BODY",BODY,{"disambiguationData":[OSD([sQuery(id+"F1.wireOp",EDGE,"E9.0.22.0")])]}),"instanceName":"13"});
            var Q195;
            Q195=makeQuery(id+"F48.opPattern","COPY",BODY,{"derivedFrom":makeQuery(id+"F3.opExtrude","SWEPT_BODY",BODY,{"disambiguationData":[OSD([sQuery(id+"F1.wireOp",EDGE,"E9.0.21.0")])]}),"instanceName":"30"});
            var Q196;
            Q196=makeQuery(id+"F48.opPattern","COPY",BODY,{"derivedFrom":makeQuery(id+"F3.opExtrude","SWEPT_BODY",BODY,{"disambiguationData":[OSD([sQuery(id+"F1.wireOp",EDGE,"E9.0.21.0")])]}),"instanceName":"13"});
            var Q197;
            Q197=makeQuery(id+"F47.opPattern","COPY",BODY,{"derivedFrom":makeQuery(id+"F3.opExtrude","SWEPT_BODY",BODY,{"disambiguationData":[OSD([sQuery(id+"F1.wireOp",EDGE,"E9.0.23.0")])]}),"instanceName":"4"});
            var Q198;
            Q198=makeQuery(id+"F48.opPattern","COPY",BODY,{"derivedFrom":makeQuery(id+"F3.opExtrude","SWEPT_BODY",BODY,{"disambiguationData":[OSD([sQuery(id+"F1.wireOp",EDGE,"E9.0.22.0")])]}),"instanceName":"27"});
            var Q199;
            Q199=makeQuery(id+"F45.opPattern","COPY",BODY,{"derivedFrom":makeQuery(id+"F3.opExtrude","SWEPT_BODY",BODY,{"disambiguationData":[OSD([sQuery(id+"F1.wireOp",EDGE,"E9.0.27.0")])]}),"instanceName":"28"});
            var Q200;
            Q200=makeQuery(id+"F45.opPattern","COPY",BODY,{"derivedFrom":makeQuery(id+"F3.opExtrude","SWEPT_BODY",BODY,{"disambiguationData":[OSD([sQuery(id+"F1.wireOp",EDGE,"E9.0.26.0")])]}),"instanceName":"29"});
            var Q201;
            Q201=makeQuery(id+"F48.opPattern","COPY",BODY,{"derivedFrom":makeQuery(id+"F3.opExtrude","SWEPT_BODY",BODY,{"disambiguationData":[OSD([sQuery(id+"F1.wireOp",EDGE,"E9.0.22.0")])]}),"instanceName":"12"});
            var Q202;
            Q202=makeQuery(id+"F47.opPattern","COPY",BODY,{"derivedFrom":makeQuery(id+"F3.opExtrude","SWEPT_BODY",BODY,{"disambiguationData":[OSD([sQuery(id+"F1.wireOp",EDGE,"E9.0.23.0")])]}),"instanceName":"5"});
            var Q203;
            Q203=makeQuery(id+"F48.opPattern","COPY",BODY,{"derivedFrom":makeQuery(id+"F3.opExtrude","SWEPT_BODY",BODY,{"disambiguationData":[OSD([sQuery(id+"F1.wireOp",EDGE,"E9.0.21.0")])]}),"instanceName":"27"});
            var Q204;
            Q204=makeQuery(id+"F48.opPattern","COPY",BODY,{"derivedFrom":makeQuery(id+"F3.opExtrude","SWEPT_BODY",BODY,{"disambiguationData":[OSD([sQuery(id+"F1.wireOp",EDGE,"E9.0.22.0")])]}),"instanceName":"26"});
            var Q205;
            Q205=makeQuery(id+"F45.opPattern","COPY",BODY,{"derivedFrom":makeQuery(id+"F3.opExtrude","SWEPT_BODY",BODY,{"disambiguationData":[OSD([sQuery(id+"F1.wireOp",EDGE,"E9.0.27.0")])]}),"instanceName":"29"});
            var Q206;
            Q206=makeQuery(id+"F48.opPattern","COPY",BODY,{"derivedFrom":makeQuery(id+"F3.opExtrude","SWEPT_BODY",BODY,{"disambiguationData":[OSD([sQuery(id+"F1.wireOp",EDGE,"E9.0.21.0")])]}),"instanceName":"12"});
            var Q207;
            Q207=makeQuery(id+"F45.opPattern","COPY",BODY,{"derivedFrom":makeQuery(id+"F3.opExtrude","SWEPT_BODY",BODY,{"disambiguationData":[OSD([sQuery(id+"F1.wireOp",EDGE,"E9.0.26.0")])]}),"instanceName":"1"});
            var Q208;
            Q208=makeQuery(id+"F47.opPattern","COPY",BODY,{"derivedFrom":makeQuery(id+"F3.opExtrude","SWEPT_BODY",BODY,{"disambiguationData":[OSD([sQuery(id+"F1.wireOp",EDGE,"E9.0.23.0")])]}),"instanceName":"12"});
            var Q209;
            Q209=makeQuery(id+"F45.opPattern","COPY",BODY,{"derivedFrom":makeQuery(id+"F3.opExtrude","SWEPT_BODY",BODY,{"disambiguationData":[OSD([sQuery(id+"F1.wireOp",EDGE,"E9.0.27.0")])]}),"instanceName":"1"});
            var Q210;
            Q210=makeQuery(id+"F45.opPattern","COPY",BODY,{"derivedFrom":makeQuery(id+"F3.opExtrude","SWEPT_BODY",BODY,{"disambiguationData":[OSD([sQuery(id+"F1.wireOp",EDGE,"E9.0.26.0")])]}),"instanceName":"30"});
            var Q211;
            Q211=makeQuery(id+"F48.opPattern","COPY",BODY,{"derivedFrom":makeQuery(id+"F3.opExtrude","SWEPT_BODY",BODY,{"disambiguationData":[OSD([sQuery(id+"F1.wireOp",EDGE,"E9.0.22.0")])]}),"instanceName":"11"});
            var Q212;
            Q212=makeQuery(id+"F47.opPattern","COPY",BODY,{"derivedFrom":makeQuery(id+"F3.opExtrude","SWEPT_BODY",BODY,{"disambiguationData":[OSD([sQuery(id+"F1.wireOp",EDGE,"E9.0.23.0")])]}),"instanceName":"17"});
            var Q213;
            Q213=makeQuery(id+"F47.opPattern","COPY",BODY,{"derivedFrom":makeQuery(id+"F3.opExtrude","SWEPT_BODY",BODY,{"disambiguationData":[OSD([sQuery(id+"F1.wireOp",EDGE,"E9.0.23.0")])]}),"instanceName":"33"});
            var Q214;
            Q214=makeQuery(id+"F45.opPattern","COPY",BODY,{"derivedFrom":makeQuery(id+"F3.opExtrude","SWEPT_BODY",BODY,{"disambiguationData":[OSD([sQuery(id+"F1.wireOp",EDGE,"E9.0.27.0")])]}),"instanceName":"30"});
            var Q215;
            Q215=makeQuery(id+"F47.opPattern","COPY",BODY,{"derivedFrom":makeQuery(id+"F3.opExtrude","SWEPT_BODY",BODY,{"disambiguationData":[OSD([sQuery(id+"F1.wireOp",EDGE,"E9.0.23.0")])]}),"instanceName":"32"});
            var Q216;
            Q216=makeQuery(id+"F45.opPattern","COPY",BODY,{"derivedFrom":makeQuery(id+"F3.opExtrude","SWEPT_BODY",BODY,{"disambiguationData":[OSD([sQuery(id+"F1.wireOp",EDGE,"E9.0.26.0")])]}),"instanceName":"31"});
            var Q217;
            Q217=makeQuery(id+"F45.opPattern","COPY",BODY,{"derivedFrom":makeQuery(id+"F3.opExtrude","SWEPT_BODY",BODY,{"disambiguationData":[OSD([sQuery(id+"F1.wireOp",EDGE,"E9.0.26.0")])]}),"instanceName":"20"});
            var Q218;
            Q218=makeQuery(id+"F45.opPattern","COPY",BODY,{"derivedFrom":makeQuery(id+"F3.opExtrude","SWEPT_BODY",BODY,{"disambiguationData":[OSD([sQuery(id+"F1.wireOp",EDGE,"E9.0.27.0")])]}),"instanceName":"31"});
            var Q219;
            Q219=makeQuery(id+"F47.opPattern","COPY",BODY,{"derivedFrom":makeQuery(id+"F3.opExtrude","SWEPT_BODY",BODY,{"disambiguationData":[OSD([sQuery(id+"F1.wireOp",EDGE,"E9.0.23.0")])]}),"instanceName":"31"});
            var Q220;
            Q220=makeQuery(id+"F46.opPattern","COPY",BODY,{"derivedFrom":makeQuery(id+"F3.opExtrude","SWEPT_BODY",BODY,{"disambiguationData":[OSD([sQuery(id+"F1.wireOp",EDGE,"E9.0.25.0")])]}),"instanceName":"16"});
            var Q221;
            Q221=makeQuery(id+"F45.opPattern","COPY",BODY,{"derivedFrom":makeQuery(id+"F3.opExtrude","SWEPT_BODY",BODY,{"disambiguationData":[OSD([sQuery(id+"F1.wireOp",EDGE,"E9.0.26.0")])]}),"instanceName":"32"});
            var Q222;
            Q222=makeQuery(id+"F48.opPattern","COPY",BODY,{"derivedFrom":makeQuery(id+"F3.opExtrude","SWEPT_BODY",BODY,{"disambiguationData":[OSD([sQuery(id+"F1.wireOp",EDGE,"E9.0.21.0")])]}),"instanceName":"11"});
            var Q223;
            Q223=makeQuery(id+"F45.opPattern","COPY",BODY,{"derivedFrom":makeQuery(id+"F3.opExtrude","SWEPT_BODY",BODY,{"disambiguationData":[OSD([sQuery(id+"F1.wireOp",EDGE,"E9.0.27.0")])]}),"instanceName":"17"});
            var Q224;
            Q224=makeQuery(id+"F46.opPattern","COPY",BODY,{"derivedFrom":makeQuery(id+"F3.opExtrude","SWEPT_BODY",BODY,{"disambiguationData":[OSD([sQuery(id+"F1.wireOp",EDGE,"E9.0.24.0")])]}),"instanceName":"16"});
            var Q225;
            Q225=makeQuery(id+"F46.opPattern","COPY",BODY,{"derivedFrom":makeQuery(id+"F3.opExtrude","SWEPT_BODY",BODY,{"disambiguationData":[OSD([sQuery(id+"F1.wireOp",EDGE,"E9.0.25.0")])]}),"instanceName":"15"});
            var Q226;
            Q226=makeQuery(id+"F48.opPattern","COPY",BODY,{"derivedFrom":makeQuery(id+"F3.opExtrude","SWEPT_BODY",BODY,{"disambiguationData":[OSD([sQuery(id+"F1.wireOp",EDGE,"E9.0.22.0")])]}),"instanceName":"10"});
            var Q227;
            Q227=makeQuery(id+"F45.opPattern","COPY",BODY,{"derivedFrom":makeQuery(id+"F3.opExtrude","SWEPT_BODY",BODY,{"disambiguationData":[OSD([sQuery(id+"F1.wireOp",EDGE,"E9.0.26.0")])]}),"instanceName":"21"});
            var Q228;
            Q228=makeQuery(id+"F45.opPattern","COPY",BODY,{"derivedFrom":makeQuery(id+"F3.opExtrude","SWEPT_BODY",BODY,{"disambiguationData":[OSD([sQuery(id+"F1.wireOp",EDGE,"E9.0.27.0")])]}),"instanceName":"32"});
            var Q229;
            Q229=makeQuery(id+"F48.opPattern","COPY",BODY,{"derivedFrom":makeQuery(id+"F3.opExtrude","SWEPT_BODY",BODY,{"disambiguationData":[OSD([sQuery(id+"F1.wireOp",EDGE,"E9.0.22.0")])]}),"instanceName":"33"});
            var Q230;
            Q230=makeQuery(id+"F46.opPattern","COPY",BODY,{"derivedFrom":makeQuery(id+"F3.opExtrude","SWEPT_BODY",BODY,{"disambiguationData":[OSD([sQuery(id+"F1.wireOp",EDGE,"E9.0.24.0")])]}),"instanceName":"15"});
            var Q231;
            Q231=makeQuery(id+"F45.opPattern","COPY",BODY,{"derivedFrom":makeQuery(id+"F3.opExtrude","SWEPT_BODY",BODY,{"disambiguationData":[OSD([sQuery(id+"F1.wireOp",EDGE,"E9.0.26.0")])]}),"instanceName":"3"});
            var Q232;
            Q232=makeQuery(id+"F46.opPattern","COPY",BODY,{"derivedFrom":makeQuery(id+"F3.opExtrude","SWEPT_BODY",BODY,{"disambiguationData":[OSD([sQuery(id+"F1.wireOp",EDGE,"E9.0.25.0")])]}),"instanceName":"14"});
            var Q233;
            Q233=makeQuery(id+"F45.opPattern","COPY",BODY,{"derivedFrom":makeQuery(id+"F3.opExtrude","SWEPT_BODY",BODY,{"disambiguationData":[OSD([sQuery(id+"F1.wireOp",EDGE,"E9.0.26.0")])]}),"instanceName":"33"});
            var Q234;
            Q234=makeQuery(id+"F45.opPattern","COPY",BODY,{"derivedFrom":makeQuery(id+"F3.opExtrude","SWEPT_BODY",BODY,{"disambiguationData":[OSD([sQuery(id+"F1.wireOp",EDGE,"E9.0.27.0")])]}),"instanceName":"33"});
            var Q235;
            Q235=makeQuery(id+"F46.opPattern","COPY",BODY,{"derivedFrom":makeQuery(id+"F3.opExtrude","SWEPT_BODY",BODY,{"disambiguationData":[OSD([sQuery(id+"F1.wireOp",EDGE,"E9.0.24.0")])]}),"instanceName":"14"});
            var Q236;
            Q236=makeQuery(id+"F45.opPattern","COPY",BODY,{"derivedFrom":makeQuery(id+"F3.opExtrude","SWEPT_BODY",BODY,{"disambiguationData":[OSD([sQuery(id+"F1.wireOp",EDGE,"E9.0.27.0")])]}),"instanceName":"3"});
            var Q237;
            Q237=makeQuery(id+"F48.opPattern","COPY",BODY,{"derivedFrom":makeQuery(id+"F3.opExtrude","SWEPT_BODY",BODY,{"disambiguationData":[OSD([sQuery(id+"F1.wireOp",EDGE,"E9.0.21.0")])]}),"instanceName":"10"});
            var Q238;
            Q238=makeQuery(id+"F45.opPattern","COPY",BODY,{"derivedFrom":makeQuery(id+"F3.opExtrude","SWEPT_BODY",BODY,{"disambiguationData":[OSD([sQuery(id+"F1.wireOp",EDGE,"E9.0.26.0")])]}),"instanceName":"4"});
            var Q239;
            Q239=makeQuery(id+"F48.opPattern","COPY",BODY,{"derivedFrom":makeQuery(id+"F3.opExtrude","SWEPT_BODY",BODY,{"disambiguationData":[OSD([sQuery(id+"F1.wireOp",EDGE,"E9.0.21.0")])]}),"instanceName":"26"});
            var Q240;
            Q240=makeQuery(id+"F48.opPattern","COPY",BODY,{"derivedFrom":makeQuery(id+"F3.opExtrude","SWEPT_BODY",BODY,{"disambiguationData":[OSD([sQuery(id+"F1.wireOp",EDGE,"E9.0.22.0")])]}),"instanceName":"25"});
            var Q241;
            Q241=makeQuery(id+"F46.opPattern","COPY",BODY,{"derivedFrom":makeQuery(id+"F3.opExtrude","SWEPT_BODY",BODY,{"disambiguationData":[OSD([sQuery(id+"F1.wireOp",EDGE,"E9.0.25.0")])]}),"instanceName":"13"});
            var Q242;
            Q242=makeQuery(id+"F46.opPattern","COPY",BODY,{"derivedFrom":makeQuery(id+"F3.opExtrude","SWEPT_BODY",BODY,{"disambiguationData":[OSD([sQuery(id+"F1.wireOp",EDGE,"E9.0.25.0")])]}),"instanceName":"35"});
            var Q243;
            Q243=makeQuery(id+"F47.opPattern","COPY",BODY,{"derivedFrom":makeQuery(id+"F3.opExtrude","SWEPT_BODY",BODY,{"disambiguationData":[OSD([sQuery(id+"F1.wireOp",EDGE,"E9.0.23.0")])]}),"instanceName":"6"});
            var Q244;
            Q244=makeQuery(id+"F47.opPattern","COPY",BODY,{"derivedFrom":makeQuery(id+"F3.opExtrude","SWEPT_BODY",BODY,{"disambiguationData":[OSD([sQuery(id+"F1.wireOp",EDGE,"E9.0.23.0")])]}),"instanceName":"7"});
            var Q245;
            Q245=makeQuery(id+"F47.opPattern","COPY",BODY,{"derivedFrom":makeQuery(id+"F3.opExtrude","SWEPT_BODY",BODY,{"disambiguationData":[OSD([sQuery(id+"F1.wireOp",EDGE,"E9.0.23.0")])]}),"instanceName":"8"});
            var Q246;
            Q246=makeQuery(id+"F45.opPattern","COPY",BODY,{"derivedFrom":makeQuery(id+"F3.opExtrude","SWEPT_BODY",BODY,{"disambiguationData":[OSD([sQuery(id+"F1.wireOp",EDGE,"E9.0.26.0")])]}),"instanceName":"14"});
            var Q247;
            Q247=makeQuery(id+"F48.opPattern","COPY",BODY,{"derivedFrom":makeQuery(id+"F3.opExtrude","SWEPT_BODY",BODY,{"disambiguationData":[OSD([sQuery(id+"F1.wireOp",EDGE,"E9.0.22.0")])]}),"instanceName":"32"});
            var Q248;
            Q248=makeQuery(id+"F45.opPattern","COPY",BODY,{"derivedFrom":makeQuery(id+"F3.opExtrude","SWEPT_BODY",BODY,{"disambiguationData":[OSD([sQuery(id+"F1.wireOp",EDGE,"E9.0.27.0")])]}),"instanceName":"16"});
            var Q249;
            Q249=makeQuery(id+"F47.opPattern","COPY",BODY,{"derivedFrom":makeQuery(id+"F3.opExtrude","SWEPT_BODY",BODY,{"disambiguationData":[OSD([sQuery(id+"F1.wireOp",EDGE,"E9.0.23.0")])]}),"instanceName":"11"});
            var Q250;
            Q250=makeQuery(id+"F48.opPattern","COPY",BODY,{"derivedFrom":makeQuery(id+"F3.opExtrude","SWEPT_BODY",BODY,{"disambiguationData":[OSD([sQuery(id+"F1.wireOp",EDGE,"E9.0.22.0")])]}),"instanceName":"17"});
            var Q251;
            Q251=makeQuery(id+"F48.opPattern","COPY",BODY,{"derivedFrom":makeQuery(id+"F3.opExtrude","SWEPT_BODY",BODY,{"disambiguationData":[OSD([sQuery(id+"F1.wireOp",EDGE,"E9.0.21.0")])]}),"instanceName":"17"});
            var Q252;
            Q252=makeQuery(id+"F46.opPattern","COPY",BODY,{"derivedFrom":makeQuery(id+"F3.opExtrude","SWEPT_BODY",BODY,{"disambiguationData":[OSD([sQuery(id+"F1.wireOp",EDGE,"E9.0.24.0")])]}),"instanceName":"33"});
            var Q253;
            Q253=makeQuery(id+"F48.opPattern","COPY",BODY,{"derivedFrom":makeQuery(id+"F3.opExtrude","SWEPT_BODY",BODY,{"disambiguationData":[OSD([sQuery(id+"F1.wireOp",EDGE,"E9.0.22.0")])]}),"instanceName":"16"});
            var Q254;
            Q254=makeQuery(id+"F3.opExtrude","SWEPT_BODY",BODY,{"disambiguationData":[OSD([sQuery(id+"F1.wireOp",EDGE,"E9.0.27.0")])]});
            var Q255;
            Q255=makeQuery(id+"F46.opPattern","COPY",BODY,{"derivedFrom":makeQuery(id+"F3.opExtrude","SWEPT_BODY",BODY,{"disambiguationData":[OSD([sQuery(id+"F1.wireOp",EDGE,"E9.0.25.0")])]}),"instanceName":"2"});
            var Q256;
            Q256=makeQuery(id+"F46.opPattern","COPY",BODY,{"derivedFrom":makeQuery(id+"F3.opExtrude","SWEPT_BODY",BODY,{"disambiguationData":[OSD([sQuery(id+"F1.wireOp",EDGE,"E9.0.24.0")])]}),"instanceName":"2"});
            var Q257;
            Q257=makeQuery(id+"F45.opPattern","COPY",BODY,{"derivedFrom":makeQuery(id+"F3.opExtrude","SWEPT_BODY",BODY,{"disambiguationData":[OSD([sQuery(id+"F1.wireOp",EDGE,"E9.0.26.0")])]}),"instanceName":"38"});
            var Q258;
            Q258=makeQuery(id+"F48.opPattern","COPY",BODY,{"derivedFrom":makeQuery(id+"F3.opExtrude","SWEPT_BODY",BODY,{"disambiguationData":[OSD([sQuery(id+"F1.wireOp",EDGE,"E9.0.22.0")])]}),"instanceName":"2"});
            var Q259;
            Q259=makeQuery(id+"F48.opPattern","COPY",BODY,{"derivedFrom":makeQuery(id+"F3.opExtrude","SWEPT_BODY",BODY,{"disambiguationData":[OSD([sQuery(id+"F1.wireOp",EDGE,"E9.0.21.0")])]}),"instanceName":"2"});
            var Q260;
            Q260=makeQuery(id+"F46.opPattern","COPY",BODY,{"derivedFrom":makeQuery(id+"F3.opExtrude","SWEPT_BODY",BODY,{"disambiguationData":[OSD([sQuery(id+"F1.wireOp",EDGE,"E9.0.24.0")])]}),"instanceName":"38"});
            var Q261;
            Q261=makeQuery(id+"F46.opPattern","COPY",BODY,{"derivedFrom":makeQuery(id+"F3.opExtrude","SWEPT_BODY",BODY,{"disambiguationData":[OSD([sQuery(id+"F1.wireOp",EDGE,"E9.0.25.0")])]}),"instanceName":"38"});
            var Q262;
            Q262=makeQuery(id+"F45.opPattern","COPY",BODY,{"derivedFrom":makeQuery(id+"F3.opExtrude","SWEPT_BODY",BODY,{"disambiguationData":[OSD([sQuery(id+"F1.wireOp",EDGE,"E9.0.27.0")])]}),"instanceName":"37"});
            var Q263;
            Q263=makeQuery(id+"F45.opPattern","COPY",BODY,{"derivedFrom":makeQuery(id+"F3.opExtrude","SWEPT_BODY",BODY,{"disambiguationData":[OSD([sQuery(id+"F1.wireOp",EDGE,"E9.0.26.0")])]}),"instanceName":"37"});
            var Q264;
            Q264=makeQuery(id+"F47.opPattern","COPY",BODY,{"derivedFrom":makeQuery(id+"F3.opExtrude","SWEPT_BODY",BODY,{"disambiguationData":[OSD([sQuery(id+"F1.wireOp",EDGE,"E9.0.23.0")])]}),"instanceName":"39"});
            var Q265;
            Q265=makeQuery(id+"F48.opPattern","COPY",BODY,{"derivedFrom":makeQuery(id+"F3.opExtrude","SWEPT_BODY",BODY,{"disambiguationData":[OSD([sQuery(id+"F1.wireOp",EDGE,"E9.0.22.0")])]}),"instanceName":"37"});
            var Q266;
            Q266=makeQuery(id+"F48.opPattern","COPY",BODY,{"derivedFrom":makeQuery(id+"F3.opExtrude","SWEPT_BODY",BODY,{"disambiguationData":[OSD([sQuery(id+"F1.wireOp",EDGE,"E9.0.21.0")])]}),"instanceName":"40"});
            var Q267;
            Q267=makeQuery(id+"F48.opPattern","COPY",BODY,{"derivedFrom":makeQuery(id+"F3.opExtrude","SWEPT_BODY",BODY,{"disambiguationData":[OSD([sQuery(id+"F1.wireOp",EDGE,"E9.0.22.0")])]}),"instanceName":"40"});
            var Q268;
            Q268=makeQuery(id+"F47.opPattern","COPY",BODY,{"derivedFrom":makeQuery(id+"F3.opExtrude","SWEPT_BODY",BODY,{"disambiguationData":[OSD([sQuery(id+"F1.wireOp",EDGE,"E9.0.23.0")])]}),"instanceName":"2"});
            var Q269;
            Q269=makeQuery(id+"F45.opPattern","COPY",BODY,{"derivedFrom":makeQuery(id+"F3.opExtrude","SWEPT_BODY",BODY,{"disambiguationData":[OSD([sQuery(id+"F1.wireOp",EDGE,"E9.0.26.0")])]}),"instanceName":"2"});
            var Q270;
            Q270=makeQuery(id+"F45.opPattern","COPY",BODY,{"derivedFrom":makeQuery(id+"F3.opExtrude","SWEPT_BODY",BODY,{"disambiguationData":[OSD([sQuery(id+"F1.wireOp",EDGE,"E9.0.27.0")])]}),"instanceName":"2"});
            var Q271;
            Q271=makeQuery(id+"F3.opExtrude","SWEPT_BODY",BODY,{"disambiguationData":[OSD([sQuery(id+"F1.wireOp",EDGE,"E9.0.26.0")])]});
            var Q272;
            Q272=makeQuery(id+"F3.opExtrude","SWEPT_BODY",BODY,{"disambiguationData":[OSD([sQuery(id+"F1.wireOp",EDGE,"E9.0.25.0")])]});
            var Q273;
            Q273=makeQuery(id+"F3.opExtrude","SWEPT_BODY",BODY,{"disambiguationData":[OSD([sQuery(id+"F1.wireOp",EDGE,"E9.0.24.0")])]});
            var Q274;
            Q274=makeQuery(id+"F3.opExtrude","SWEPT_BODY",BODY,{"disambiguationData":[OSD([sQuery(id+"F1.wireOp",EDGE,"E9.0.21.0")])]});
            var Q275;
            Q275=makeQuery(id+"F3.opExtrude","SWEPT_BODY",BODY,{"disambiguationData":[OSD([sQuery(id+"F1.wireOp",EDGE,"E9.0.22.0")])]});
            var Q276;
            Q276=makeQuery(id+"F3.opExtrude","SWEPT_BODY",BODY,{"disambiguationData":[OSD([sQuery(id+"F1.wireOp",EDGE,"E9.0.23.0")])]});
            var Q277;
            Q277=makeQuery(id+"F45.opPattern","COPY",BODY,{"derivedFrom":makeQuery(id+"F3.opExtrude","SWEPT_BODY",BODY,{"disambiguationData":[OSD([sQuery(id+"F1.wireOp",EDGE,"E9.0.27.0")])]}),"instanceName":"38"});
            var Q278;
            Q278=makeQuery(id+"F47.opPattern","COPY",BODY,{"derivedFrom":makeQuery(id+"F3.opExtrude","SWEPT_BODY",BODY,{"disambiguationData":[OSD([sQuery(id+"F1.wireOp",EDGE,"E9.0.23.0")])]}),"instanceName":"40"});
            var Q279;
            Q279=makeQuery(id+"F46.opPattern","COPY",BODY,{"derivedFrom":makeQuery(id+"F3.opExtrude","SWEPT_BODY",BODY,{"disambiguationData":[OSD([sQuery(id+"F1.wireOp",EDGE,"E9.0.24.0")])]}),"instanceName":"39"});
            var Q280;
            Q280=makeQuery(id+"F46.opPattern","COPY",BODY,{"derivedFrom":makeQuery(id+"F3.opExtrude","SWEPT_BODY",BODY,{"disambiguationData":[OSD([sQuery(id+"F1.wireOp",EDGE,"E9.0.25.0")])]}),"instanceName":"39"});
            var Q281;
            Q281=makeQuery(id+"F48.opPattern","COPY",BODY,{"derivedFrom":makeQuery(id+"F3.opExtrude","SWEPT_BODY",BODY,{"disambiguationData":[OSD([sQuery(id+"F1.wireOp",EDGE,"E9.0.22.0")])]}),"instanceName":"41"});
            var Q282;
            Q282=makeQuery(id+"F48.opPattern","COPY",BODY,{"derivedFrom":makeQuery(id+"F3.opExtrude","SWEPT_BODY",BODY,{"disambiguationData":[OSD([sQuery(id+"F1.wireOp",EDGE,"E9.0.21.0")])]}),"instanceName":"41"});
            var Q283;
            Q283=makeQuery(id+"F2.opRevolve","SWEPT_BODY",BODY,{"disambiguationData":[OSD([sQuery(id+"F0.wireOp",EDGE,"E0"),sQuery(id+"F0.wireOp",EDGE,"E1"),sQuery(id+"F0.wireOp",EDGE,"E2"),sQuery(id+"F0.wireOp",EDGE,"E3"),sQuery(id+"F0.wireOp",EDGE,"E6")])]});
            booleanBodies(context, id + "F49", {"operationType" : BooleanOperationType.SUBTRACTION, "tools" : qUnion([Q0, Q1, Q2, Q3, Q4, Q5, Q6, Q7, Q8, Q9, Q10, Q11, Q12, Q13, Q14, Q15, Q16, Q17, Q18, Q19, Q20, Q21, Q22, Q23, Q24, Q25, Q26, Q27, Q28, Q29, Q30, Q31, Q32, Q33, Q34, Q35, Q36, Q37, Q38, Q39, Q40, Q41, Q42, Q43, Q44, Q45, Q46, Q47, Q48, Q49, Q50, Q51, Q52, Q53, Q54, Q55, Q56, Q57, Q58, Q59, Q60, Q61, Q62, Q63, Q64, Q65, Q66, Q67, Q68, Q69, Q70, Q71, Q72, Q73, Q74, Q75, Q76, Q77, Q78, Q79, Q80, Q81, Q82, Q83, Q84, Q85, Q86, Q87, Q88, Q89, Q90, Q91, Q92, Q93, Q94, Q95, Q96, Q97, Q98, Q99, Q100, Q101, Q102, Q103, Q104, Q105, Q106, Q107, Q108, Q109, Q110, Q111, Q112, Q113, Q114, Q115, Q116, Q117, Q118, Q119, Q120, Q121, Q122, Q123, Q124, Q125, Q126, Q127, Q128, Q129, Q130, Q131, Q132, Q133, Q134, Q135, Q136, Q137, Q138, Q139, Q140, Q141, Q142, Q143, Q144, Q145, Q146, Q147, Q148, Q149, Q150, Q151, Q152, Q153, Q154, Q155, Q156, Q157, Q158, Q159, Q160, Q161, Q162, Q163, Q164, Q165, Q166, Q167, Q168, Q169, Q170, Q171, Q172, Q173, Q174, Q175, Q176, Q177, Q178, Q179, Q180, Q181, Q182, Q183, Q184, Q185, Q186, Q187, Q188, Q189, Q190, Q191, Q192, Q193, Q194, Q195, Q196, Q197, Q198, Q199, Q200, Q201, Q202, Q203, Q204, Q205, Q206, Q207, Q208, Q209, Q210, Q211, Q212, Q213, Q214, Q215, Q216, Q217, Q218, Q219, Q220, Q221, Q222, Q223, Q224, Q225, Q226, Q227, Q228, Q229, Q230, Q231, Q232, Q233, Q234, Q235, Q236, Q237, Q238, Q239, Q240, Q241, Q242, Q243, Q244, Q245, Q246, Q247, Q248, Q249, Q250, Q251, Q252, Q253, Q254, Q255, Q256, Q257, Q258, Q259, Q260, Q261, Q262, Q263, Q264, Q265, Q266, Q267, Q268, Q269, Q270, Q271, Q272, Q273, Q274, Q275, Q276, Q277, Q278, Q279, Q280, Q281, Q282]), "targets" : qUnion([Q283])});
        }
        {
            var Q0;
            Q0=makeQuery(id+"F3.opExtrude","SWEPT_BODY",BODY,{"disambiguationData":[OSD([sQuery(id+"F1.wireOp",EDGE,"E9.0.20.0")])]});
            var Q1;
            Q1=makeQuery(id+"F2.opRevolve","SWEPT_FACE",FACE,{"disambiguationData":[OSD([sQuery(id+"F0.wireOp",EDGE,"E1")])]});
            circularPattern(context, id + "F50", {"entities" : qUnion([Q0]), "axis" : qUnion([Q1]), "angle" : 180 * degree, "instanceCount" : 43, "oppositeDirection" : true, "equalSpace" : true});
        }
        {
            var Q0;
            Q0=makeQuery(id+"F3.opExtrude","SWEPT_BODY",BODY,{"disambiguationData":[OSD([sQuery(id+"F1.wireOp",EDGE,"E9.0.19.0")])]});
            var Q1;
            Q1=makeQuery(id+"F3.opExtrude","SWEPT_BODY",BODY,{"disambiguationData":[OSD([sQuery(id+"F1.wireOp",EDGE,"E9.0.18.0")])]});
            var Q2;
            Q2=makeQuery(id+"F2.opRevolve","SWEPT_FACE",FACE,{"disambiguationData":[OSD([sQuery(id+"F0.wireOp",EDGE,"E1")])]});
            circularPattern(context, id + "F51", {"entities" : qUnion([Q0, Q1]), "axis" : qUnion([Q2]), "angle" : 180 * degree, "instanceCount" : 44, "oppositeDirection" : true, "equalSpace" : true});
        }
        {
            var Q0;
            Q0=makeQuery(id+"F3.opExtrude","SWEPT_BODY",BODY,{"disambiguationData":[OSD([sQuery(id+"F1.wireOp",EDGE,"E9.0.17.0")])]});
            var Q1;
            Q1=makeQuery(id+"F2.opRevolve","SWEPT_FACE",FACE,{"disambiguationData":[OSD([sQuery(id+"F0.wireOp",EDGE,"E1")])]});
            circularPattern(context, id + "F52", {"entities" : qUnion([Q0]), "axis" : qUnion([Q1]), "angle" : 180 * degree, "instanceCount" : 45, "oppositeDirection" : true, "equalSpace" : true});
        }
        {
            var Q0;
            Q0=makeQuery(id+"F3.opExtrude","SWEPT_BODY",BODY,{"disambiguationData":[OSD([sQuery(id+"F1.wireOp",EDGE,"E9.0.16.0")])]});
            var Q1;
            Q1=makeQuery(id+"F3.opExtrude","SWEPT_BODY",BODY,{"disambiguationData":[OSD([sQuery(id+"F1.wireOp",EDGE,"E9.0.15.0")])]});
            var Q2;
            Q2=makeQuery(id+"F2.opRevolve","SWEPT_FACE",FACE,{"disambiguationData":[OSD([sQuery(id+"F0.wireOp",EDGE,"E1")])]});
            circularPattern(context, id + "F53", {"entities" : qUnion([Q0, Q1]), "axis" : qUnion([Q2]), "angle" : 180 * degree, "instanceCount" : 46, "oppositeDirection" : true, "equalSpace" : true});
        }
        {
            var Q0;
            Q0=makeQuery(id+"F3.opExtrude","SWEPT_BODY",BODY,{"disambiguationData":[OSD([sQuery(id+"F1.wireOp",EDGE,"E9.0.14.0")])]});
            var Q1;
            Q1=makeQuery(id+"F2.opRevolve","SWEPT_FACE",FACE,{"disambiguationData":[OSD([sQuery(id+"F0.wireOp",EDGE,"E1")])]});
            circularPattern(context, id + "F54", {"entities" : qUnion([Q0]), "axis" : qUnion([Q1]), "angle" : 180 * degree, "instanceCount" : 47, "oppositeDirection" : true, "equalSpace" : true});
        }
        {
            var Q0;
            Q0=makeQuery(id+"F3.opExtrude","SWEPT_BODY",BODY,{"disambiguationData":[OSD([sQuery(id+"F1.wireOp",EDGE,"E9.0.13.0")])]});
            var Q1;
            Q1=makeQuery(id+"F3.opExtrude","SWEPT_BODY",BODY,{"disambiguationData":[OSD([sQuery(id+"F1.wireOp",EDGE,"E9.0.12.0")])]});
            var Q2;
            Q2=makeQuery(id+"F2.opRevolve","SWEPT_FACE",FACE,{"disambiguationData":[OSD([sQuery(id+"F0.wireOp",EDGE,"E1")])]});
            circularPattern(context, id + "F55", {"entities" : qUnion([Q0, Q1]), "axis" : qUnion([Q2]), "angle" : 180 * degree, "instanceCount" : 48, "oppositeDirection" : true, "equalSpace" : true});
        }
        {
            var Q0;
            Q0=makeQuery(id+"F52.opPattern","COPY",BODY,{"derivedFrom":makeQuery(id+"F3.opExtrude","SWEPT_BODY",BODY,{"disambiguationData":[OSD([sQuery(id+"F1.wireOp",EDGE,"E9.0.17.0")])]}),"instanceName":"3"});
            var Q1;
            Q1=makeQuery(id+"F54.opPattern","COPY",BODY,{"derivedFrom":makeQuery(id+"F3.opExtrude","SWEPT_BODY",BODY,{"disambiguationData":[OSD([sQuery(id+"F1.wireOp",EDGE,"E9.0.14.0")])]}),"instanceName":"5"});
            var Q2;
            Q2=makeQuery(id+"F53.opPattern","COPY",BODY,{"derivedFrom":makeQuery(id+"F3.opExtrude","SWEPT_BODY",BODY,{"disambiguationData":[OSD([sQuery(id+"F1.wireOp",EDGE,"E9.0.16.0")])]}),"instanceName":"5"});
            var Q3;
            Q3=makeQuery(id+"F55.opPattern","COPY",BODY,{"derivedFrom":makeQuery(id+"F3.opExtrude","SWEPT_BODY",BODY,{"disambiguationData":[OSD([sQuery(id+"F1.wireOp",EDGE,"E9.0.12.0")])]}),"instanceName":"15"});
            var Q4;
            Q4=makeQuery(id+"F54.opPattern","COPY",BODY,{"derivedFrom":makeQuery(id+"F3.opExtrude","SWEPT_BODY",BODY,{"disambiguationData":[OSD([sQuery(id+"F1.wireOp",EDGE,"E9.0.14.0")])]}),"instanceName":"6"});
            var Q5;
            Q5=makeQuery(id+"F51.opPattern","COPY",BODY,{"derivedFrom":makeQuery(id+"F3.opExtrude","SWEPT_BODY",BODY,{"disambiguationData":[OSD([sQuery(id+"F1.wireOp",EDGE,"E9.0.18.0")])]}),"instanceName":"12"});
            var Q6;
            Q6=makeQuery(id+"F53.opPattern","COPY",BODY,{"derivedFrom":makeQuery(id+"F3.opExtrude","SWEPT_BODY",BODY,{"disambiguationData":[OSD([sQuery(id+"F1.wireOp",EDGE,"E9.0.15.0")])]}),"instanceName":"5"});
            var Q7;
            Q7=makeQuery(id+"F54.opPattern","COPY",BODY,{"derivedFrom":makeQuery(id+"F3.opExtrude","SWEPT_BODY",BODY,{"disambiguationData":[OSD([sQuery(id+"F1.wireOp",EDGE,"E9.0.14.0")])]}),"instanceName":"7"});
            var Q8;
            Q8=makeQuery(id+"F51.opPattern","COPY",BODY,{"derivedFrom":makeQuery(id+"F3.opExtrude","SWEPT_BODY",BODY,{"disambiguationData":[OSD([sQuery(id+"F1.wireOp",EDGE,"E9.0.19.0")])]}),"instanceName":"12"});
            var Q9;
            Q9=makeQuery(id+"F53.opPattern","COPY",BODY,{"derivedFrom":makeQuery(id+"F3.opExtrude","SWEPT_BODY",BODY,{"disambiguationData":[OSD([sQuery(id+"F1.wireOp",EDGE,"E9.0.15.0")])]}),"instanceName":"6"});
            var Q10;
            Q10=makeQuery(id+"F53.opPattern","COPY",BODY,{"derivedFrom":makeQuery(id+"F3.opExtrude","SWEPT_BODY",BODY,{"disambiguationData":[OSD([sQuery(id+"F1.wireOp",EDGE,"E9.0.15.0")])]}),"instanceName":"33"});
            var Q11;
            Q11=makeQuery(id+"F55.opPattern","COPY",BODY,{"derivedFrom":makeQuery(id+"F3.opExtrude","SWEPT_BODY",BODY,{"disambiguationData":[OSD([sQuery(id+"F1.wireOp",EDGE,"E9.0.13.0")])]}),"instanceName":"6"});
            var Q12;
            Q12=makeQuery(id+"F55.opPattern","COPY",BODY,{"derivedFrom":makeQuery(id+"F3.opExtrude","SWEPT_BODY",BODY,{"disambiguationData":[OSD([sQuery(id+"F1.wireOp",EDGE,"E9.0.12.0")])]}),"instanceName":"10"});
            var Q13;
            Q13=makeQuery(id+"F52.opPattern","COPY",BODY,{"derivedFrom":makeQuery(id+"F3.opExtrude","SWEPT_BODY",BODY,{"disambiguationData":[OSD([sQuery(id+"F1.wireOp",EDGE,"E9.0.17.0")])]}),"instanceName":"5"});
            var Q14;
            Q14=makeQuery(id+"F51.opPattern","COPY",BODY,{"derivedFrom":makeQuery(id+"F3.opExtrude","SWEPT_BODY",BODY,{"disambiguationData":[OSD([sQuery(id+"F1.wireOp",EDGE,"E9.0.18.0")])]}),"instanceName":"13"});
            var Q15;
            Q15=makeQuery(id+"F53.opPattern","COPY",BODY,{"derivedFrom":makeQuery(id+"F3.opExtrude","SWEPT_BODY",BODY,{"disambiguationData":[OSD([sQuery(id+"F1.wireOp",EDGE,"E9.0.16.0")])]}),"instanceName":"6"});
            var Q16;
            Q16=makeQuery(id+"F55.opPattern","COPY",BODY,{"derivedFrom":makeQuery(id+"F3.opExtrude","SWEPT_BODY",BODY,{"disambiguationData":[OSD([sQuery(id+"F1.wireOp",EDGE,"E9.0.13.0")])]}),"instanceName":"10"});
            var Q17;
            Q17=makeQuery(id+"F55.opPattern","COPY",BODY,{"derivedFrom":makeQuery(id+"F3.opExtrude","SWEPT_BODY",BODY,{"disambiguationData":[OSD([sQuery(id+"F1.wireOp",EDGE,"E9.0.13.0")])]}),"instanceName":"14"});
            var Q18;
            Q18=makeQuery(id+"F52.opPattern","COPY",BODY,{"derivedFrom":makeQuery(id+"F3.opExtrude","SWEPT_BODY",BODY,{"disambiguationData":[OSD([sQuery(id+"F1.wireOp",EDGE,"E9.0.17.0")])]}),"instanceName":"6"});
            var Q19;
            Q19=makeQuery(id+"F51.opPattern","COPY",BODY,{"derivedFrom":makeQuery(id+"F3.opExtrude","SWEPT_BODY",BODY,{"disambiguationData":[OSD([sQuery(id+"F1.wireOp",EDGE,"E9.0.19.0")])]}),"instanceName":"34"});
            var Q20;
            Q20=makeQuery(id+"F52.opPattern","COPY",BODY,{"derivedFrom":makeQuery(id+"F3.opExtrude","SWEPT_BODY",BODY,{"disambiguationData":[OSD([sQuery(id+"F1.wireOp",EDGE,"E9.0.17.0")])]}),"instanceName":"4"});
            var Q21;
            Q21=makeQuery(id+"F55.opPattern","COPY",BODY,{"derivedFrom":makeQuery(id+"F3.opExtrude","SWEPT_BODY",BODY,{"disambiguationData":[OSD([sQuery(id+"F1.wireOp",EDGE,"E9.0.12.0")])]}),"instanceName":"14"});
            var Q22;
            Q22=makeQuery(id+"F53.opPattern","COPY",BODY,{"derivedFrom":makeQuery(id+"F3.opExtrude","SWEPT_BODY",BODY,{"disambiguationData":[OSD([sQuery(id+"F1.wireOp",EDGE,"E9.0.15.0")])]}),"instanceName":"7"});
            var Q23;
            Q23=makeQuery(id+"F53.opPattern","COPY",BODY,{"derivedFrom":makeQuery(id+"F3.opExtrude","SWEPT_BODY",BODY,{"disambiguationData":[OSD([sQuery(id+"F1.wireOp",EDGE,"E9.0.16.0")])]}),"instanceName":"7"});
            var Q24;
            Q24=makeQuery(id+"F52.opPattern","COPY",BODY,{"derivedFrom":makeQuery(id+"F3.opExtrude","SWEPT_BODY",BODY,{"disambiguationData":[OSD([sQuery(id+"F1.wireOp",EDGE,"E9.0.17.0")])]}),"instanceName":"7"});
            var Q25;
            Q25=makeQuery(id+"F51.opPattern","COPY",BODY,{"derivedFrom":makeQuery(id+"F3.opExtrude","SWEPT_BODY",BODY,{"disambiguationData":[OSD([sQuery(id+"F1.wireOp",EDGE,"E9.0.19.0")])]}),"instanceName":"13"});
            var Q26;
            Q26=makeQuery(id+"F52.opPattern","COPY",BODY,{"derivedFrom":makeQuery(id+"F3.opExtrude","SWEPT_BODY",BODY,{"disambiguationData":[OSD([sQuery(id+"F1.wireOp",EDGE,"E9.0.17.0")])]}),"instanceName":"8"});
            var Q27;
            Q27=makeQuery(id+"F53.opPattern","COPY",BODY,{"derivedFrom":makeQuery(id+"F3.opExtrude","SWEPT_BODY",BODY,{"disambiguationData":[OSD([sQuery(id+"F1.wireOp",EDGE,"E9.0.15.0")])]}),"instanceName":"8"});
            var Q28;
            Q28=makeQuery(id+"F55.opPattern","COPY",BODY,{"derivedFrom":makeQuery(id+"F3.opExtrude","SWEPT_BODY",BODY,{"disambiguationData":[OSD([sQuery(id+"F1.wireOp",EDGE,"E9.0.13.0")])]}),"instanceName":"13"});
            var Q29;
            Q29=makeQuery(id+"F51.opPattern","COPY",BODY,{"derivedFrom":makeQuery(id+"F3.opExtrude","SWEPT_BODY",BODY,{"disambiguationData":[OSD([sQuery(id+"F1.wireOp",EDGE,"E9.0.18.0")])]}),"instanceName":"14"});
            var Q30;
            Q30=makeQuery(id+"F51.opPattern","COPY",BODY,{"derivedFrom":makeQuery(id+"F3.opExtrude","SWEPT_BODY",BODY,{"disambiguationData":[OSD([sQuery(id+"F1.wireOp",EDGE,"E9.0.19.0")])]}),"instanceName":"14"});
            var Q31;
            Q31=makeQuery(id+"F52.opPattern","COPY",BODY,{"derivedFrom":makeQuery(id+"F3.opExtrude","SWEPT_BODY",BODY,{"disambiguationData":[OSD([sQuery(id+"F1.wireOp",EDGE,"E9.0.17.0")])]}),"instanceName":"30"});
            var Q32;
            Q32=makeQuery(id+"F52.opPattern","COPY",BODY,{"derivedFrom":makeQuery(id+"F3.opExtrude","SWEPT_BODY",BODY,{"disambiguationData":[OSD([sQuery(id+"F1.wireOp",EDGE,"E9.0.17.0")])]}),"instanceName":"29"});
            var Q33;
            Q33=makeQuery(id+"F53.opPattern","COPY",BODY,{"derivedFrom":makeQuery(id+"F3.opExtrude","SWEPT_BODY",BODY,{"disambiguationData":[OSD([sQuery(id+"F1.wireOp",EDGE,"E9.0.15.0")])]}),"instanceName":"30"});
            var Q34;
            Q34=makeQuery(id+"F50.opPattern","COPY",BODY,{"derivedFrom":makeQuery(id+"F3.opExtrude","SWEPT_BODY",BODY,{"disambiguationData":[OSD([sQuery(id+"F1.wireOp",EDGE,"E9.0.20.0")])]}),"instanceName":"34"});
            var Q35;
            Q35=makeQuery(id+"F54.opPattern","COPY",BODY,{"derivedFrom":makeQuery(id+"F3.opExtrude","SWEPT_BODY",BODY,{"disambiguationData":[OSD([sQuery(id+"F1.wireOp",EDGE,"E9.0.14.0")])]}),"instanceName":"28"});
            var Q36;
            Q36=makeQuery(id+"F54.opPattern","COPY",BODY,{"derivedFrom":makeQuery(id+"F3.opExtrude","SWEPT_BODY",BODY,{"disambiguationData":[OSD([sQuery(id+"F1.wireOp",EDGE,"E9.0.14.0")])]}),"instanceName":"36"});
            var Q37;
            Q37=makeQuery(id+"F51.opPattern","COPY",BODY,{"derivedFrom":makeQuery(id+"F3.opExtrude","SWEPT_BODY",BODY,{"disambiguationData":[OSD([sQuery(id+"F1.wireOp",EDGE,"E9.0.18.0")])]}),"instanceName":"15"});
            var Q38;
            Q38=makeQuery(id+"F52.opPattern","COPY",BODY,{"derivedFrom":makeQuery(id+"F3.opExtrude","SWEPT_BODY",BODY,{"disambiguationData":[OSD([sQuery(id+"F1.wireOp",EDGE,"E9.0.17.0")])]}),"instanceName":"28"});
            var Q39;
            Q39=makeQuery(id+"F52.opPattern","COPY",BODY,{"derivedFrom":makeQuery(id+"F3.opExtrude","SWEPT_BODY",BODY,{"disambiguationData":[OSD([sQuery(id+"F1.wireOp",EDGE,"E9.0.17.0")])]}),"instanceName":"9"});
            var Q40;
            Q40=makeQuery(id+"F53.opPattern","COPY",BODY,{"derivedFrom":makeQuery(id+"F3.opExtrude","SWEPT_BODY",BODY,{"disambiguationData":[OSD([sQuery(id+"F1.wireOp",EDGE,"E9.0.16.0")])]}),"instanceName":"8"});
            var Q41;
            Q41=makeQuery(id+"F51.opPattern","COPY",BODY,{"derivedFrom":makeQuery(id+"F3.opExtrude","SWEPT_BODY",BODY,{"disambiguationData":[OSD([sQuery(id+"F1.wireOp",EDGE,"E9.0.19.0")])]}),"instanceName":"15"});
            var Q42;
            Q42=makeQuery(id+"F54.opPattern","COPY",BODY,{"derivedFrom":makeQuery(id+"F3.opExtrude","SWEPT_BODY",BODY,{"disambiguationData":[OSD([sQuery(id+"F1.wireOp",EDGE,"E9.0.14.0")])]}),"instanceName":"38"});
            var Q43;
            Q43=makeQuery(id+"F54.opPattern","COPY",BODY,{"derivedFrom":makeQuery(id+"F3.opExtrude","SWEPT_BODY",BODY,{"disambiguationData":[OSD([sQuery(id+"F1.wireOp",EDGE,"E9.0.14.0")])]}),"instanceName":"37"});
            var Q44;
            Q44=makeQuery(id+"F51.opPattern","COPY",BODY,{"derivedFrom":makeQuery(id+"F3.opExtrude","SWEPT_BODY",BODY,{"disambiguationData":[OSD([sQuery(id+"F1.wireOp",EDGE,"E9.0.18.0")])]}),"instanceName":"34"});
            var Q45;
            Q45=makeQuery(id+"F53.opPattern","COPY",BODY,{"derivedFrom":makeQuery(id+"F3.opExtrude","SWEPT_BODY",BODY,{"disambiguationData":[OSD([sQuery(id+"F1.wireOp",EDGE,"E9.0.16.0")])]}),"instanceName":"29"});
            var Q46;
            Q46=makeQuery(id+"F52.opPattern","COPY",BODY,{"derivedFrom":makeQuery(id+"F3.opExtrude","SWEPT_BODY",BODY,{"disambiguationData":[OSD([sQuery(id+"F1.wireOp",EDGE,"E9.0.17.0")])]}),"instanceName":"10"});
            var Q47;
            Q47=makeQuery(id+"F55.opPattern","COPY",BODY,{"derivedFrom":makeQuery(id+"F3.opExtrude","SWEPT_BODY",BODY,{"disambiguationData":[OSD([sQuery(id+"F1.wireOp",EDGE,"E9.0.13.0")])]}),"instanceName":"11"});
            var Q48;
            Q48=makeQuery(id+"F54.opPattern","COPY",BODY,{"derivedFrom":makeQuery(id+"F3.opExtrude","SWEPT_BODY",BODY,{"disambiguationData":[OSD([sQuery(id+"F1.wireOp",EDGE,"E9.0.14.0")])]}),"instanceName":"3"});
            var Q49;
            Q49=makeQuery(id+"F55.opPattern","COPY",BODY,{"derivedFrom":makeQuery(id+"F3.opExtrude","SWEPT_BODY",BODY,{"disambiguationData":[OSD([sQuery(id+"F1.wireOp",EDGE,"E9.0.12.0")])]}),"instanceName":"12"});
            var Q50;
            Q50=makeQuery(id+"F51.opPattern","COPY",BODY,{"derivedFrom":makeQuery(id+"F3.opExtrude","SWEPT_BODY",BODY,{"disambiguationData":[OSD([sQuery(id+"F1.wireOp",EDGE,"E9.0.18.0")])]}),"instanceName":"16"});
            var Q51;
            Q51=makeQuery(id+"F52.opPattern","COPY",BODY,{"derivedFrom":makeQuery(id+"F3.opExtrude","SWEPT_BODY",BODY,{"disambiguationData":[OSD([sQuery(id+"F1.wireOp",EDGE,"E9.0.17.0")])]}),"instanceName":"27"});
            var Q52;
            Q52=makeQuery(id+"F53.opPattern","COPY",BODY,{"derivedFrom":makeQuery(id+"F3.opExtrude","SWEPT_BODY",BODY,{"disambiguationData":[OSD([sQuery(id+"F1.wireOp",EDGE,"E9.0.15.0")])]}),"instanceName":"9"});
            var Q53;
            Q53=makeQuery(id+"F55.opPattern","COPY",BODY,{"derivedFrom":makeQuery(id+"F3.opExtrude","SWEPT_BODY",BODY,{"disambiguationData":[OSD([sQuery(id+"F1.wireOp",EDGE,"E9.0.13.0")])]}),"instanceName":"12"});
            var Q54;
            Q54=makeQuery(id+"F51.opPattern","COPY",BODY,{"derivedFrom":makeQuery(id+"F3.opExtrude","SWEPT_BODY",BODY,{"disambiguationData":[OSD([sQuery(id+"F1.wireOp",EDGE,"E9.0.18.0")])]}),"instanceName":"6"});
            var Q55;
            Q55=makeQuery(id+"F53.opPattern","COPY",BODY,{"derivedFrom":makeQuery(id+"F3.opExtrude","SWEPT_BODY",BODY,{"disambiguationData":[OSD([sQuery(id+"F1.wireOp",EDGE,"E9.0.16.0")])]}),"instanceName":"9"});
            var Q56;
            Q56=makeQuery(id+"F55.opPattern","COPY",BODY,{"derivedFrom":makeQuery(id+"F3.opExtrude","SWEPT_BODY",BODY,{"disambiguationData":[OSD([sQuery(id+"F1.wireOp",EDGE,"E9.0.12.0")])]}),"instanceName":"13"});
            var Q57;
            Q57=makeQuery(id+"F52.opPattern","COPY",BODY,{"derivedFrom":makeQuery(id+"F3.opExtrude","SWEPT_BODY",BODY,{"disambiguationData":[OSD([sQuery(id+"F1.wireOp",EDGE,"E9.0.17.0")])]}),"instanceName":"11"});
            var Q58;
            Q58=makeQuery(id+"F52.opPattern","COPY",BODY,{"derivedFrom":makeQuery(id+"F3.opExtrude","SWEPT_BODY",BODY,{"disambiguationData":[OSD([sQuery(id+"F1.wireOp",EDGE,"E9.0.17.0")])]}),"instanceName":"31"});
            var Q59;
            Q59=makeQuery(id+"F52.opPattern","COPY",BODY,{"derivedFrom":makeQuery(id+"F3.opExtrude","SWEPT_BODY",BODY,{"disambiguationData":[OSD([sQuery(id+"F1.wireOp",EDGE,"E9.0.17.0")])]}),"instanceName":"26"});
            var Q60;
            Q60=makeQuery(id+"F52.opPattern","COPY",BODY,{"derivedFrom":makeQuery(id+"F3.opExtrude","SWEPT_BODY",BODY,{"disambiguationData":[OSD([sQuery(id+"F1.wireOp",EDGE,"E9.0.17.0")])]}),"instanceName":"12"});
            var Q61;
            Q61=makeQuery(id+"F52.opPattern","COPY",BODY,{"derivedFrom":makeQuery(id+"F3.opExtrude","SWEPT_BODY",BODY,{"disambiguationData":[OSD([sQuery(id+"F1.wireOp",EDGE,"E9.0.17.0")])]}),"instanceName":"25"});
            var Q62;
            Q62=makeQuery(id+"F53.opPattern","COPY",BODY,{"derivedFrom":makeQuery(id+"F3.opExtrude","SWEPT_BODY",BODY,{"disambiguationData":[OSD([sQuery(id+"F1.wireOp",EDGE,"E9.0.15.0")])]}),"instanceName":"10"});
            var Q63;
            Q63=makeQuery(id+"F52.opPattern","COPY",BODY,{"derivedFrom":makeQuery(id+"F3.opExtrude","SWEPT_BODY",BODY,{"disambiguationData":[OSD([sQuery(id+"F1.wireOp",EDGE,"E9.0.17.0")])]}),"instanceName":"24"});
            var Q64;
            Q64=makeQuery(id+"F55.opPattern","COPY",BODY,{"derivedFrom":makeQuery(id+"F3.opExtrude","SWEPT_BODY",BODY,{"disambiguationData":[OSD([sQuery(id+"F1.wireOp",EDGE,"E9.0.12.0")])]}),"instanceName":"11"});
            var Q65;
            Q65=makeQuery(id+"F53.opPattern","COPY",BODY,{"derivedFrom":makeQuery(id+"F3.opExtrude","SWEPT_BODY",BODY,{"disambiguationData":[OSD([sQuery(id+"F1.wireOp",EDGE,"E9.0.16.0")])]}),"instanceName":"10"});
            var Q66;
            Q66=makeQuery(id+"F52.opPattern","COPY",BODY,{"derivedFrom":makeQuery(id+"F3.opExtrude","SWEPT_BODY",BODY,{"disambiguationData":[OSD([sQuery(id+"F1.wireOp",EDGE,"E9.0.17.0")])]}),"instanceName":"32"});
            var Q67;
            Q67=makeQuery(id+"F51.opPattern","COPY",BODY,{"derivedFrom":makeQuery(id+"F3.opExtrude","SWEPT_BODY",BODY,{"disambiguationData":[OSD([sQuery(id+"F1.wireOp",EDGE,"E9.0.19.0")])]}),"instanceName":"16"});
            var Q68;
            Q68=makeQuery(id+"F52.opPattern","COPY",BODY,{"derivedFrom":makeQuery(id+"F3.opExtrude","SWEPT_BODY",BODY,{"disambiguationData":[OSD([sQuery(id+"F1.wireOp",EDGE,"E9.0.17.0")])]}),"instanceName":"23"});
            var Q69;
            Q69=makeQuery(id+"F53.opPattern","COPY",BODY,{"derivedFrom":makeQuery(id+"F3.opExtrude","SWEPT_BODY",BODY,{"disambiguationData":[OSD([sQuery(id+"F1.wireOp",EDGE,"E9.0.15.0")])]}),"instanceName":"11"});
            var Q70;
            Q70=makeQuery(id+"F54.opPattern","COPY",BODY,{"derivedFrom":makeQuery(id+"F3.opExtrude","SWEPT_BODY",BODY,{"disambiguationData":[OSD([sQuery(id+"F1.wireOp",EDGE,"E9.0.14.0")])]}),"instanceName":"23"});
            var Q71;
            Q71=makeQuery(id+"F52.opPattern","COPY",BODY,{"derivedFrom":makeQuery(id+"F3.opExtrude","SWEPT_BODY",BODY,{"disambiguationData":[OSD([sQuery(id+"F1.wireOp",EDGE,"E9.0.17.0")])]}),"instanceName":"13"});
            var Q72;
            Q72=makeQuery(id+"F52.opPattern","COPY",BODY,{"derivedFrom":makeQuery(id+"F3.opExtrude","SWEPT_BODY",BODY,{"disambiguationData":[OSD([sQuery(id+"F1.wireOp",EDGE,"E9.0.17.0")])]}),"instanceName":"14"});
            var Q73;
            Q73=makeQuery(id+"F54.opPattern","COPY",BODY,{"derivedFrom":makeQuery(id+"F3.opExtrude","SWEPT_BODY",BODY,{"disambiguationData":[OSD([sQuery(id+"F1.wireOp",EDGE,"E9.0.14.0")])]}),"instanceName":"1"});
            var Q74;
            Q74=makeQuery(id+"F53.opPattern","COPY",BODY,{"derivedFrom":makeQuery(id+"F3.opExtrude","SWEPT_BODY",BODY,{"disambiguationData":[OSD([sQuery(id+"F1.wireOp",EDGE,"E9.0.16.0")])]}),"instanceName":"11"});
            var Q75;
            Q75=makeQuery(id+"F51.opPattern","COPY",BODY,{"derivedFrom":makeQuery(id+"F3.opExtrude","SWEPT_BODY",BODY,{"disambiguationData":[OSD([sQuery(id+"F1.wireOp",EDGE,"E9.0.18.0")])]}),"instanceName":"17"});
            var Q76;
            Q76=makeQuery(id+"F53.opPattern","COPY",BODY,{"derivedFrom":makeQuery(id+"F3.opExtrude","SWEPT_BODY",BODY,{"disambiguationData":[OSD([sQuery(id+"F1.wireOp",EDGE,"E9.0.15.0")])]}),"instanceName":"12"});
            var Q77;
            Q77=makeQuery(id+"F51.opPattern","COPY",BODY,{"derivedFrom":makeQuery(id+"F3.opExtrude","SWEPT_BODY",BODY,{"disambiguationData":[OSD([sQuery(id+"F1.wireOp",EDGE,"E9.0.19.0")])]}),"instanceName":"36"});
            var Q78;
            Q78=makeQuery(id+"F53.opPattern","COPY",BODY,{"derivedFrom":makeQuery(id+"F3.opExtrude","SWEPT_BODY",BODY,{"disambiguationData":[OSD([sQuery(id+"F1.wireOp",EDGE,"E9.0.16.0")])]}),"instanceName":"12"});
            var Q79;
            Q79=makeQuery(id+"F51.opPattern","COPY",BODY,{"derivedFrom":makeQuery(id+"F3.opExtrude","SWEPT_BODY",BODY,{"disambiguationData":[OSD([sQuery(id+"F1.wireOp",EDGE,"E9.0.19.0")])]}),"instanceName":"17"});
            var Q80;
            Q80=makeQuery(id+"F54.opPattern","COPY",BODY,{"derivedFrom":makeQuery(id+"F3.opExtrude","SWEPT_BODY",BODY,{"disambiguationData":[OSD([sQuery(id+"F1.wireOp",EDGE,"E9.0.14.0")])]}),"instanceName":"15"});
            var Q81;
            Q81=makeQuery(id+"F53.opPattern","COPY",BODY,{"derivedFrom":makeQuery(id+"F3.opExtrude","SWEPT_BODY",BODY,{"disambiguationData":[OSD([sQuery(id+"F1.wireOp",EDGE,"E9.0.16.0")])]}),"instanceName":"36"});
            var Q82;
            Q82=makeQuery(id+"F53.opPattern","COPY",BODY,{"derivedFrom":makeQuery(id+"F3.opExtrude","SWEPT_BODY",BODY,{"disambiguationData":[OSD([sQuery(id+"F1.wireOp",EDGE,"E9.0.15.0")])]}),"instanceName":"29"});
            var Q83;
            Q83=makeQuery(id+"F53.opPattern","COPY",BODY,{"derivedFrom":makeQuery(id+"F3.opExtrude","SWEPT_BODY",BODY,{"disambiguationData":[OSD([sQuery(id+"F1.wireOp",EDGE,"E9.0.15.0")])]}),"instanceName":"13"});
            var Q84;
            Q84=makeQuery(id+"F53.opPattern","COPY",BODY,{"derivedFrom":makeQuery(id+"F3.opExtrude","SWEPT_BODY",BODY,{"disambiguationData":[OSD([sQuery(id+"F1.wireOp",EDGE,"E9.0.16.0")])]}),"instanceName":"13"});
            var Q85;
            Q85=makeQuery(id+"F53.opPattern","COPY",BODY,{"derivedFrom":makeQuery(id+"F3.opExtrude","SWEPT_BODY",BODY,{"disambiguationData":[OSD([sQuery(id+"F1.wireOp",EDGE,"E9.0.15.0")])]}),"instanceName":"38"});
            var Q86;
            Q86=makeQuery(id+"F51.opPattern","COPY",BODY,{"derivedFrom":makeQuery(id+"F3.opExtrude","SWEPT_BODY",BODY,{"disambiguationData":[OSD([sQuery(id+"F1.wireOp",EDGE,"E9.0.18.0")])]}),"instanceName":"18"});
            var Q87;
            Q87=makeQuery(id+"F51.opPattern","COPY",BODY,{"derivedFrom":makeQuery(id+"F3.opExtrude","SWEPT_BODY",BODY,{"disambiguationData":[OSD([sQuery(id+"F1.wireOp",EDGE,"E9.0.19.0")])]}),"instanceName":"18"});
            var Q88;
            Q88=makeQuery(id+"F53.opPattern","COPY",BODY,{"derivedFrom":makeQuery(id+"F3.opExtrude","SWEPT_BODY",BODY,{"disambiguationData":[OSD([sQuery(id+"F1.wireOp",EDGE,"E9.0.15.0")])]}),"instanceName":"14"});
            var Q89;
            Q89=makeQuery(id+"F52.opPattern","COPY",BODY,{"derivedFrom":makeQuery(id+"F3.opExtrude","SWEPT_BODY",BODY,{"disambiguationData":[OSD([sQuery(id+"F1.wireOp",EDGE,"E9.0.17.0")])]}),"instanceName":"15"});
            var Q90;
            Q90=makeQuery(id+"F52.opPattern","COPY",BODY,{"derivedFrom":makeQuery(id+"F3.opExtrude","SWEPT_BODY",BODY,{"disambiguationData":[OSD([sQuery(id+"F1.wireOp",EDGE,"E9.0.17.0")])]}),"instanceName":"22"});
            var Q91;
            Q91=makeQuery(id+"F50.opPattern","COPY",BODY,{"derivedFrom":makeQuery(id+"F3.opExtrude","SWEPT_BODY",BODY,{"disambiguationData":[OSD([sQuery(id+"F1.wireOp",EDGE,"E9.0.20.0")])]}),"instanceName":"21"});
            var Q92;
            Q92=makeQuery(id+"F54.opPattern","COPY",BODY,{"derivedFrom":makeQuery(id+"F3.opExtrude","SWEPT_BODY",BODY,{"disambiguationData":[OSD([sQuery(id+"F1.wireOp",EDGE,"E9.0.14.0")])]}),"instanceName":"25"});
            var Q93;
            Q93=makeQuery(id+"F52.opPattern","COPY",BODY,{"derivedFrom":makeQuery(id+"F3.opExtrude","SWEPT_BODY",BODY,{"disambiguationData":[OSD([sQuery(id+"F1.wireOp",EDGE,"E9.0.17.0")])]}),"instanceName":"16"});
            var Q94;
            Q94=makeQuery(id+"F53.opPattern","COPY",BODY,{"derivedFrom":makeQuery(id+"F3.opExtrude","SWEPT_BODY",BODY,{"disambiguationData":[OSD([sQuery(id+"F1.wireOp",EDGE,"E9.0.16.0")])]}),"instanceName":"14"});
            var Q95;
            Q95=makeQuery(id+"F52.opPattern","COPY",BODY,{"derivedFrom":makeQuery(id+"F3.opExtrude","SWEPT_BODY",BODY,{"disambiguationData":[OSD([sQuery(id+"F1.wireOp",EDGE,"E9.0.17.0")])]}),"instanceName":"17"});
            var Q96;
            Q96=makeQuery(id+"F53.opPattern","COPY",BODY,{"derivedFrom":makeQuery(id+"F3.opExtrude","SWEPT_BODY",BODY,{"disambiguationData":[OSD([sQuery(id+"F1.wireOp",EDGE,"E9.0.15.0")])]}),"instanceName":"15"});
            var Q97;
            Q97=makeQuery(id+"F53.opPattern","COPY",BODY,{"derivedFrom":makeQuery(id+"F3.opExtrude","SWEPT_BODY",BODY,{"disambiguationData":[OSD([sQuery(id+"F1.wireOp",EDGE,"E9.0.16.0")])]}),"instanceName":"15"});
            var Q98;
            Q98=makeQuery(id+"F51.opPattern","COPY",BODY,{"derivedFrom":makeQuery(id+"F3.opExtrude","SWEPT_BODY",BODY,{"disambiguationData":[OSD([sQuery(id+"F1.wireOp",EDGE,"E9.0.18.0")])]}),"instanceName":"7"});
            var Q99;
            Q99=makeQuery(id+"F51.opPattern","COPY",BODY,{"derivedFrom":makeQuery(id+"F3.opExtrude","SWEPT_BODY",BODY,{"disambiguationData":[OSD([sQuery(id+"F1.wireOp",EDGE,"E9.0.18.0")])]}),"instanceName":"19"});
            var Q100;
            Q100=makeQuery(id+"F53.opPattern","COPY",BODY,{"derivedFrom":makeQuery(id+"F3.opExtrude","SWEPT_BODY",BODY,{"disambiguationData":[OSD([sQuery(id+"F1.wireOp",EDGE,"E9.0.16.0")])]}),"instanceName":"37"});
            var Q101;
            Q101=makeQuery(id+"F53.opPattern","COPY",BODY,{"derivedFrom":makeQuery(id+"F3.opExtrude","SWEPT_BODY",BODY,{"disambiguationData":[OSD([sQuery(id+"F1.wireOp",EDGE,"E9.0.16.0")])]}),"instanceName":"34"});
            var Q102;
            Q102=makeQuery(id+"F51.opPattern","COPY",BODY,{"derivedFrom":makeQuery(id+"F3.opExtrude","SWEPT_BODY",BODY,{"disambiguationData":[OSD([sQuery(id+"F1.wireOp",EDGE,"E9.0.19.0")])]}),"instanceName":"19"});
            var Q103;
            Q103=makeQuery(id+"F54.opPattern","COPY",BODY,{"derivedFrom":makeQuery(id+"F3.opExtrude","SWEPT_BODY",BODY,{"disambiguationData":[OSD([sQuery(id+"F1.wireOp",EDGE,"E9.0.14.0")])]}),"instanceName":"24"});
            var Q104;
            Q104=makeQuery(id+"F50.opPattern","COPY",BODY,{"derivedFrom":makeQuery(id+"F3.opExtrude","SWEPT_BODY",BODY,{"disambiguationData":[OSD([sQuery(id+"F1.wireOp",EDGE,"E9.0.20.0")])]}),"instanceName":"25"});
            var Q105;
            Q105=makeQuery(id+"F51.opPattern","COPY",BODY,{"derivedFrom":makeQuery(id+"F3.opExtrude","SWEPT_BODY",BODY,{"disambiguationData":[OSD([sQuery(id+"F1.wireOp",EDGE,"E9.0.18.0")])]}),"instanceName":"32"});
            var Q106;
            Q106=makeQuery(id+"F51.opPattern","COPY",BODY,{"derivedFrom":makeQuery(id+"F3.opExtrude","SWEPT_BODY",BODY,{"disambiguationData":[OSD([sQuery(id+"F1.wireOp",EDGE,"E9.0.19.0")])]}),"instanceName":"31"});
            var Q107;
            Q107=makeQuery(id+"F51.opPattern","COPY",BODY,{"derivedFrom":makeQuery(id+"F3.opExtrude","SWEPT_BODY",BODY,{"disambiguationData":[OSD([sQuery(id+"F1.wireOp",EDGE,"E9.0.18.0")])]}),"instanceName":"20"});
            var Q108;
            Q108=makeQuery(id+"F55.opPattern","COPY",BODY,{"derivedFrom":makeQuery(id+"F3.opExtrude","SWEPT_BODY",BODY,{"disambiguationData":[OSD([sQuery(id+"F1.wireOp",EDGE,"E9.0.13.0")])]}),"instanceName":"19"});
            var Q109;
            Q109=makeQuery(id+"F51.opPattern","COPY",BODY,{"derivedFrom":makeQuery(id+"F3.opExtrude","SWEPT_BODY",BODY,{"disambiguationData":[OSD([sQuery(id+"F1.wireOp",EDGE,"E9.0.19.0")])]}),"instanceName":"20"});
            var Q110;
            Q110=makeQuery(id+"F53.opPattern","COPY",BODY,{"derivedFrom":makeQuery(id+"F3.opExtrude","SWEPT_BODY",BODY,{"disambiguationData":[OSD([sQuery(id+"F1.wireOp",EDGE,"E9.0.16.0")])]}),"instanceName":"35"});
            var Q111;
            Q111=makeQuery(id+"F51.opPattern","COPY",BODY,{"derivedFrom":makeQuery(id+"F3.opExtrude","SWEPT_BODY",BODY,{"disambiguationData":[OSD([sQuery(id+"F1.wireOp",EDGE,"E9.0.18.0")])]}),"instanceName":"31"});
            var Q112;
            Q112=makeQuery(id+"F55.opPattern","COPY",BODY,{"derivedFrom":makeQuery(id+"F3.opExtrude","SWEPT_BODY",BODY,{"disambiguationData":[OSD([sQuery(id+"F1.wireOp",EDGE,"E9.0.12.0")])]}),"instanceName":"3"});
            var Q113;
            Q113=makeQuery(id+"F51.opPattern","COPY",BODY,{"derivedFrom":makeQuery(id+"F3.opExtrude","SWEPT_BODY",BODY,{"disambiguationData":[OSD([sQuery(id+"F1.wireOp",EDGE,"E9.0.19.0")])]}),"instanceName":"42"});
            var Q114;
            Q114=makeQuery(id+"F51.opPattern","COPY",BODY,{"derivedFrom":makeQuery(id+"F3.opExtrude","SWEPT_BODY",BODY,{"disambiguationData":[OSD([sQuery(id+"F1.wireOp",EDGE,"E9.0.19.0")])]}),"instanceName":"30"});
            var Q115;
            Q115=makeQuery(id+"F51.opPattern","COPY",BODY,{"derivedFrom":makeQuery(id+"F3.opExtrude","SWEPT_BODY",BODY,{"disambiguationData":[OSD([sQuery(id+"F1.wireOp",EDGE,"E9.0.18.0")])]}),"instanceName":"30"});
            var Q116;
            Q116=makeQuery(id+"F51.opPattern","COPY",BODY,{"derivedFrom":makeQuery(id+"F3.opExtrude","SWEPT_BODY",BODY,{"disambiguationData":[OSD([sQuery(id+"F1.wireOp",EDGE,"E9.0.18.0")])]}),"instanceName":"42"});
            var Q117;
            Q117=makeQuery(id+"F55.opPattern","COPY",BODY,{"derivedFrom":makeQuery(id+"F3.opExtrude","SWEPT_BODY",BODY,{"disambiguationData":[OSD([sQuery(id+"F1.wireOp",EDGE,"E9.0.13.0")])]}),"instanceName":"3"});
            var Q118;
            Q118=makeQuery(id+"F52.opPattern","COPY",BODY,{"derivedFrom":makeQuery(id+"F3.opExtrude","SWEPT_BODY",BODY,{"disambiguationData":[OSD([sQuery(id+"F1.wireOp",EDGE,"E9.0.17.0")])]}),"instanceName":"18"});
            var Q119;
            Q119=makeQuery(id+"F50.opPattern","COPY",BODY,{"derivedFrom":makeQuery(id+"F3.opExtrude","SWEPT_BODY",BODY,{"disambiguationData":[OSD([sQuery(id+"F1.wireOp",EDGE,"E9.0.20.0")])]}),"instanceName":"3"});
            var Q120;
            Q120=makeQuery(id+"F52.opPattern","COPY",BODY,{"derivedFrom":makeQuery(id+"F3.opExtrude","SWEPT_BODY",BODY,{"disambiguationData":[OSD([sQuery(id+"F1.wireOp",EDGE,"E9.0.17.0")])]}),"instanceName":"19"});
            var Q121;
            Q121=makeQuery(id+"F51.opPattern","COPY",BODY,{"derivedFrom":makeQuery(id+"F3.opExtrude","SWEPT_BODY",BODY,{"disambiguationData":[OSD([sQuery(id+"F1.wireOp",EDGE,"E9.0.18.0")])]}),"instanceName":"21"});
            var Q122;
            Q122=makeQuery(id+"F53.opPattern","COPY",BODY,{"derivedFrom":makeQuery(id+"F3.opExtrude","SWEPT_BODY",BODY,{"disambiguationData":[OSD([sQuery(id+"F1.wireOp",EDGE,"E9.0.15.0")])]}),"instanceName":"16"});
            var Q123;
            Q123=makeQuery(id+"F51.opPattern","COPY",BODY,{"derivedFrom":makeQuery(id+"F3.opExtrude","SWEPT_BODY",BODY,{"disambiguationData":[OSD([sQuery(id+"F1.wireOp",EDGE,"E9.0.19.0")])]}),"instanceName":"29"});
            var Q124;
            Q124=makeQuery(id+"F53.opPattern","COPY",BODY,{"derivedFrom":makeQuery(id+"F3.opExtrude","SWEPT_BODY",BODY,{"disambiguationData":[OSD([sQuery(id+"F1.wireOp",EDGE,"E9.0.15.0")])]}),"instanceName":"39"});
            var Q125;
            Q125=makeQuery(id+"F53.opPattern","COPY",BODY,{"derivedFrom":makeQuery(id+"F3.opExtrude","SWEPT_BODY",BODY,{"disambiguationData":[OSD([sQuery(id+"F1.wireOp",EDGE,"E9.0.16.0")])]}),"instanceName":"16"});
            var Q126;
            Q126=makeQuery(id+"F51.opPattern","COPY",BODY,{"derivedFrom":makeQuery(id+"F3.opExtrude","SWEPT_BODY",BODY,{"disambiguationData":[OSD([sQuery(id+"F1.wireOp",EDGE,"E9.0.19.0")])]}),"instanceName":"21"});
            var Q127;
            Q127=makeQuery(id+"F51.opPattern","COPY",BODY,{"derivedFrom":makeQuery(id+"F3.opExtrude","SWEPT_BODY",BODY,{"disambiguationData":[OSD([sQuery(id+"F1.wireOp",EDGE,"E9.0.18.0")])]}),"instanceName":"22"});
            var Q128;
            Q128=makeQuery(id+"F53.opPattern","COPY",BODY,{"derivedFrom":makeQuery(id+"F3.opExtrude","SWEPT_BODY",BODY,{"disambiguationData":[OSD([sQuery(id+"F1.wireOp",EDGE,"E9.0.15.0")])]}),"instanceName":"17"});
            var Q129;
            Q129=makeQuery(id+"F51.opPattern","COPY",BODY,{"derivedFrom":makeQuery(id+"F3.opExtrude","SWEPT_BODY",BODY,{"disambiguationData":[OSD([sQuery(id+"F1.wireOp",EDGE,"E9.0.18.0")])]}),"instanceName":"29"});
            var Q130;
            Q130=makeQuery(id+"F50.opPattern","COPY",BODY,{"derivedFrom":makeQuery(id+"F3.opExtrude","SWEPT_BODY",BODY,{"disambiguationData":[OSD([sQuery(id+"F1.wireOp",EDGE,"E9.0.20.0")])]}),"instanceName":"22"});
            var Q131;
            Q131=makeQuery(id+"F54.opPattern","COPY",BODY,{"derivedFrom":makeQuery(id+"F3.opExtrude","SWEPT_BODY",BODY,{"disambiguationData":[OSD([sQuery(id+"F1.wireOp",EDGE,"E9.0.14.0")])]}),"instanceName":"27"});
            var Q132;
            Q132=makeQuery(id+"F52.opPattern","COPY",BODY,{"derivedFrom":makeQuery(id+"F3.opExtrude","SWEPT_BODY",BODY,{"disambiguationData":[OSD([sQuery(id+"F1.wireOp",EDGE,"E9.0.17.0")])]}),"instanceName":"20"});
            var Q133;
            Q133=makeQuery(id+"F53.opPattern","COPY",BODY,{"derivedFrom":makeQuery(id+"F3.opExtrude","SWEPT_BODY",BODY,{"disambiguationData":[OSD([sQuery(id+"F1.wireOp",EDGE,"E9.0.16.0")])]}),"instanceName":"44"});
            var Q134;
            Q134=makeQuery(id+"F51.opPattern","COPY",BODY,{"derivedFrom":makeQuery(id+"F3.opExtrude","SWEPT_BODY",BODY,{"disambiguationData":[OSD([sQuery(id+"F1.wireOp",EDGE,"E9.0.19.0")])]}),"instanceName":"28"});
            var Q135;
            Q135=makeQuery(id+"F52.opPattern","COPY",BODY,{"derivedFrom":makeQuery(id+"F3.opExtrude","SWEPT_BODY",BODY,{"disambiguationData":[OSD([sQuery(id+"F1.wireOp",EDGE,"E9.0.17.0")])]}),"instanceName":"21"});
            var Q136;
            Q136=makeQuery(id+"F53.opPattern","COPY",BODY,{"derivedFrom":makeQuery(id+"F3.opExtrude","SWEPT_BODY",BODY,{"disambiguationData":[OSD([sQuery(id+"F1.wireOp",EDGE,"E9.0.16.0")])]}),"instanceName":"40"});
            var Q137;
            Q137=makeQuery(id+"F53.opPattern","COPY",BODY,{"derivedFrom":makeQuery(id+"F3.opExtrude","SWEPT_BODY",BODY,{"disambiguationData":[OSD([sQuery(id+"F1.wireOp",EDGE,"E9.0.16.0")])]}),"instanceName":"17"});
            var Q138;
            Q138=makeQuery(id+"F53.opPattern","COPY",BODY,{"derivedFrom":makeQuery(id+"F3.opExtrude","SWEPT_BODY",BODY,{"disambiguationData":[OSD([sQuery(id+"F1.wireOp",EDGE,"E9.0.15.0")])]}),"instanceName":"18"});
            var Q139;
            Q139=makeQuery(id+"F53.opPattern","COPY",BODY,{"derivedFrom":makeQuery(id+"F3.opExtrude","SWEPT_BODY",BODY,{"disambiguationData":[OSD([sQuery(id+"F1.wireOp",EDGE,"E9.0.16.0")])]}),"instanceName":"18"});
            var Q140;
            Q140=makeQuery(id+"F53.opPattern","COPY",BODY,{"derivedFrom":makeQuery(id+"F3.opExtrude","SWEPT_BODY",BODY,{"disambiguationData":[OSD([sQuery(id+"F1.wireOp",EDGE,"E9.0.15.0")])]}),"instanceName":"44"});
            var Q141;
            Q141=makeQuery(id+"F52.opPattern","COPY",BODY,{"derivedFrom":makeQuery(id+"F3.opExtrude","SWEPT_BODY",BODY,{"disambiguationData":[OSD([sQuery(id+"F1.wireOp",EDGE,"E9.0.17.0")])]}),"instanceName":"40"});
            var Q142;
            Q142=makeQuery(id+"F51.opPattern","COPY",BODY,{"derivedFrom":makeQuery(id+"F3.opExtrude","SWEPT_BODY",BODY,{"disambiguationData":[OSD([sQuery(id+"F1.wireOp",EDGE,"E9.0.18.0")])]}),"instanceName":"28"});
            var Q143;
            Q143=makeQuery(id+"F51.opPattern","COPY",BODY,{"derivedFrom":makeQuery(id+"F3.opExtrude","SWEPT_BODY",BODY,{"disambiguationData":[OSD([sQuery(id+"F1.wireOp",EDGE,"E9.0.19.0")])]}),"instanceName":"22"});
            var Q144;
            Q144=makeQuery(id+"F50.opPattern","COPY",BODY,{"derivedFrom":makeQuery(id+"F3.opExtrude","SWEPT_BODY",BODY,{"disambiguationData":[OSD([sQuery(id+"F1.wireOp",EDGE,"E9.0.20.0")])]}),"instanceName":"15"});
            var Q145;
            Q145=makeQuery(id+"F50.opPattern","COPY",BODY,{"derivedFrom":makeQuery(id+"F3.opExtrude","SWEPT_BODY",BODY,{"disambiguationData":[OSD([sQuery(id+"F1.wireOp",EDGE,"E9.0.20.0")])]}),"instanceName":"20"});
            var Q146;
            Q146=makeQuery(id+"F53.opPattern","COPY",BODY,{"derivedFrom":makeQuery(id+"F3.opExtrude","SWEPT_BODY",BODY,{"disambiguationData":[OSD([sQuery(id+"F1.wireOp",EDGE,"E9.0.15.0")])]}),"instanceName":"19"});
            var Q147;
            Q147=makeQuery(id+"F51.opPattern","COPY",BODY,{"derivedFrom":makeQuery(id+"F3.opExtrude","SWEPT_BODY",BODY,{"disambiguationData":[OSD([sQuery(id+"F1.wireOp",EDGE,"E9.0.18.0")])]}),"instanceName":"23"});
            var Q148;
            Q148=makeQuery(id+"F50.opPattern","COPY",BODY,{"derivedFrom":makeQuery(id+"F3.opExtrude","SWEPT_BODY",BODY,{"disambiguationData":[OSD([sQuery(id+"F1.wireOp",EDGE,"E9.0.20.0")])]}),"instanceName":"35"});
            var Q149;
            Q149=makeQuery(id+"F50.opPattern","COPY",BODY,{"derivedFrom":makeQuery(id+"F3.opExtrude","SWEPT_BODY",BODY,{"disambiguationData":[OSD([sQuery(id+"F1.wireOp",EDGE,"E9.0.20.0")])]}),"instanceName":"37"});
            var Q150;
            Q150=makeQuery(id+"F50.opPattern","COPY",BODY,{"derivedFrom":makeQuery(id+"F3.opExtrude","SWEPT_BODY",BODY,{"disambiguationData":[OSD([sQuery(id+"F1.wireOp",EDGE,"E9.0.20.0")])]}),"instanceName":"36"});
            var Q151;
            Q151=makeQuery(id+"F50.opPattern","COPY",BODY,{"derivedFrom":makeQuery(id+"F3.opExtrude","SWEPT_BODY",BODY,{"disambiguationData":[OSD([sQuery(id+"F1.wireOp",EDGE,"E9.0.20.0")])]}),"instanceName":"18"});
            var Q152;
            Q152=makeQuery(id+"F54.opPattern","COPY",BODY,{"derivedFrom":makeQuery(id+"F3.opExtrude","SWEPT_BODY",BODY,{"disambiguationData":[OSD([sQuery(id+"F1.wireOp",EDGE,"E9.0.14.0")])]}),"instanceName":"33"});
            var Q153;
            Q153=makeQuery(id+"F50.opPattern","COPY",BODY,{"derivedFrom":makeQuery(id+"F3.opExtrude","SWEPT_BODY",BODY,{"disambiguationData":[OSD([sQuery(id+"F1.wireOp",EDGE,"E9.0.20.0")])]}),"instanceName":"16"});
            var Q154;
            Q154=makeQuery(id+"F54.opPattern","COPY",BODY,{"derivedFrom":makeQuery(id+"F3.opExtrude","SWEPT_BODY",BODY,{"disambiguationData":[OSD([sQuery(id+"F1.wireOp",EDGE,"E9.0.14.0")])]}),"instanceName":"34"});
            var Q155;
            Q155=makeQuery(id+"F50.opPattern","COPY",BODY,{"derivedFrom":makeQuery(id+"F3.opExtrude","SWEPT_BODY",BODY,{"disambiguationData":[OSD([sQuery(id+"F1.wireOp",EDGE,"E9.0.20.0")])]}),"instanceName":"14"});
            var Q156;
            Q156=makeQuery(id+"F53.opPattern","COPY",BODY,{"derivedFrom":makeQuery(id+"F3.opExtrude","SWEPT_BODY",BODY,{"disambiguationData":[OSD([sQuery(id+"F1.wireOp",EDGE,"E9.0.15.0")])]}),"instanceName":"34"});
            var Q157;
            Q157=makeQuery(id+"F51.opPattern","COPY",BODY,{"derivedFrom":makeQuery(id+"F3.opExtrude","SWEPT_BODY",BODY,{"disambiguationData":[OSD([sQuery(id+"F1.wireOp",EDGE,"E9.0.19.0")])]}),"instanceName":"6"});
            var Q158;
            Q158=makeQuery(id+"F50.opPattern","COPY",BODY,{"derivedFrom":makeQuery(id+"F3.opExtrude","SWEPT_BODY",BODY,{"disambiguationData":[OSD([sQuery(id+"F1.wireOp",EDGE,"E9.0.20.0")])]}),"instanceName":"13"});
            var Q159;
            Q159=makeQuery(id+"F54.opPattern","COPY",BODY,{"derivedFrom":makeQuery(id+"F3.opExtrude","SWEPT_BODY",BODY,{"disambiguationData":[OSD([sQuery(id+"F1.wireOp",EDGE,"E9.0.14.0")])]}),"instanceName":"35"});
            var Q160;
            Q160=makeQuery(id+"F50.opPattern","COPY",BODY,{"derivedFrom":makeQuery(id+"F3.opExtrude","SWEPT_BODY",BODY,{"disambiguationData":[OSD([sQuery(id+"F1.wireOp",EDGE,"E9.0.20.0")])]}),"instanceName":"38"});
            var Q161;
            Q161=makeQuery(id+"F55.opPattern","COPY",BODY,{"derivedFrom":makeQuery(id+"F3.opExtrude","SWEPT_BODY",BODY,{"disambiguationData":[OSD([sQuery(id+"F1.wireOp",EDGE,"E9.0.13.0")])]}),"instanceName":"9"});
            var Q162;
            Q162=makeQuery(id+"F53.opPattern","COPY",BODY,{"derivedFrom":makeQuery(id+"F3.opExtrude","SWEPT_BODY",BODY,{"disambiguationData":[OSD([sQuery(id+"F1.wireOp",EDGE,"E9.0.16.0")])]}),"instanceName":"42"});
            var Q163;
            Q163=makeQuery(id+"F52.opPattern","COPY",BODY,{"derivedFrom":makeQuery(id+"F3.opExtrude","SWEPT_BODY",BODY,{"disambiguationData":[OSD([sQuery(id+"F1.wireOp",EDGE,"E9.0.17.0")])]}),"instanceName":"38"});
            var Q164;
            Q164=makeQuery(id+"F50.opPattern","COPY",BODY,{"derivedFrom":makeQuery(id+"F3.opExtrude","SWEPT_BODY",BODY,{"disambiguationData":[OSD([sQuery(id+"F1.wireOp",EDGE,"E9.0.20.0")])]}),"instanceName":"39"});
            var Q165;
            Q165=makeQuery(id+"F50.opPattern","COPY",BODY,{"derivedFrom":makeQuery(id+"F3.opExtrude","SWEPT_BODY",BODY,{"disambiguationData":[OSD([sQuery(id+"F1.wireOp",EDGE,"E9.0.20.0")])]}),"instanceName":"12"});
            var Q166;
            Q166=makeQuery(id+"F50.opPattern","COPY",BODY,{"derivedFrom":makeQuery(id+"F3.opExtrude","SWEPT_BODY",BODY,{"disambiguationData":[OSD([sQuery(id+"F1.wireOp",EDGE,"E9.0.20.0")])]}),"instanceName":"11"});
            var Q167;
            Q167=makeQuery(id+"F50.opPattern","COPY",BODY,{"derivedFrom":makeQuery(id+"F3.opExtrude","SWEPT_BODY",BODY,{"disambiguationData":[OSD([sQuery(id+"F1.wireOp",EDGE,"E9.0.20.0")])]}),"instanceName":"10"});
            var Q168;
            Q168=makeQuery(id+"F53.opPattern","COPY",BODY,{"derivedFrom":makeQuery(id+"F3.opExtrude","SWEPT_BODY",BODY,{"disambiguationData":[OSD([sQuery(id+"F1.wireOp",EDGE,"E9.0.16.0")])]}),"instanceName":"31"});
            var Q169;
            Q169=makeQuery(id+"F53.opPattern","COPY",BODY,{"derivedFrom":makeQuery(id+"F3.opExtrude","SWEPT_BODY",BODY,{"disambiguationData":[OSD([sQuery(id+"F1.wireOp",EDGE,"E9.0.16.0")])]}),"instanceName":"38"});
            var Q170;
            Q170=makeQuery(id+"F52.opPattern","COPY",BODY,{"derivedFrom":makeQuery(id+"F3.opExtrude","SWEPT_BODY",BODY,{"disambiguationData":[OSD([sQuery(id+"F1.wireOp",EDGE,"E9.0.17.0")])]}),"instanceName":"37"});
            var Q171;
            Q171=makeQuery(id+"F50.opPattern","COPY",BODY,{"derivedFrom":makeQuery(id+"F3.opExtrude","SWEPT_BODY",BODY,{"disambiguationData":[OSD([sQuery(id+"F1.wireOp",EDGE,"E9.0.20.0")])]}),"instanceName":"41"});
            var Q172;
            Q172=makeQuery(id+"F50.opPattern","COPY",BODY,{"derivedFrom":makeQuery(id+"F3.opExtrude","SWEPT_BODY",BODY,{"disambiguationData":[OSD([sQuery(id+"F1.wireOp",EDGE,"E9.0.20.0")])]}),"instanceName":"9"});
            var Q173;
            Q173=makeQuery(id+"F50.opPattern","COPY",BODY,{"derivedFrom":makeQuery(id+"F3.opExtrude","SWEPT_BODY",BODY,{"disambiguationData":[OSD([sQuery(id+"F1.wireOp",EDGE,"E9.0.20.0")])]}),"instanceName":"8"});
            var Q174;
            Q174=makeQuery(id+"F52.opPattern","COPY",BODY,{"derivedFrom":makeQuery(id+"F3.opExtrude","SWEPT_BODY",BODY,{"disambiguationData":[OSD([sQuery(id+"F1.wireOp",EDGE,"E9.0.17.0")])]}),"instanceName":"36"});
            var Q175;
            Q175=makeQuery(id+"F52.opPattern","COPY",BODY,{"derivedFrom":makeQuery(id+"F3.opExtrude","SWEPT_BODY",BODY,{"disambiguationData":[OSD([sQuery(id+"F1.wireOp",EDGE,"E9.0.17.0")])]}),"instanceName":"41"});
            var Q176;
            Q176=makeQuery(id+"F51.opPattern","COPY",BODY,{"derivedFrom":makeQuery(id+"F3.opExtrude","SWEPT_BODY",BODY,{"disambiguationData":[OSD([sQuery(id+"F1.wireOp",EDGE,"E9.0.18.0")])]}),"instanceName":"24"});
            var Q177;
            Q177=makeQuery(id+"F51.opPattern","COPY",BODY,{"derivedFrom":makeQuery(id+"F3.opExtrude","SWEPT_BODY",BODY,{"disambiguationData":[OSD([sQuery(id+"F1.wireOp",EDGE,"E9.0.19.0")])]}),"instanceName":"23"});
            var Q178;
            Q178=makeQuery(id+"F53.opPattern","COPY",BODY,{"derivedFrom":makeQuery(id+"F3.opExtrude","SWEPT_BODY",BODY,{"disambiguationData":[OSD([sQuery(id+"F1.wireOp",EDGE,"E9.0.15.0")])]}),"instanceName":"42"});
            var Q179;
            Q179=makeQuery(id+"F50.opPattern","COPY",BODY,{"derivedFrom":makeQuery(id+"F3.opExtrude","SWEPT_BODY",BODY,{"disambiguationData":[OSD([sQuery(id+"F1.wireOp",EDGE,"E9.0.20.0")])]}),"instanceName":"7"});
            var Q180;
            Q180=makeQuery(id+"F51.opPattern","COPY",BODY,{"derivedFrom":makeQuery(id+"F3.opExtrude","SWEPT_BODY",BODY,{"disambiguationData":[OSD([sQuery(id+"F1.wireOp",EDGE,"E9.0.19.0")])]}),"instanceName":"26"});
            var Q181;
            Q181=makeQuery(id+"F51.opPattern","COPY",BODY,{"derivedFrom":makeQuery(id+"F3.opExtrude","SWEPT_BODY",BODY,{"disambiguationData":[OSD([sQuery(id+"F1.wireOp",EDGE,"E9.0.18.0")])]}),"instanceName":"1"});
            var Q182;
            Q182=makeQuery(id+"F51.opPattern","COPY",BODY,{"derivedFrom":makeQuery(id+"F3.opExtrude","SWEPT_BODY",BODY,{"disambiguationData":[OSD([sQuery(id+"F1.wireOp",EDGE,"E9.0.19.0")])]}),"instanceName":"1"});
            var Q183;
            Q183=makeQuery(id+"F50.opPattern","COPY",BODY,{"derivedFrom":makeQuery(id+"F3.opExtrude","SWEPT_BODY",BODY,{"disambiguationData":[OSD([sQuery(id+"F1.wireOp",EDGE,"E9.0.20.0")])]}),"instanceName":"6"});
            var Q184;
            Q184=makeQuery(id+"F52.opPattern","COPY",BODY,{"derivedFrom":makeQuery(id+"F3.opExtrude","SWEPT_BODY",BODY,{"disambiguationData":[OSD([sQuery(id+"F1.wireOp",EDGE,"E9.0.17.0")])]}),"instanceName":"35"});
            var Q185;
            Q185=makeQuery(id+"F50.opPattern","COPY",BODY,{"derivedFrom":makeQuery(id+"F3.opExtrude","SWEPT_BODY",BODY,{"disambiguationData":[OSD([sQuery(id+"F1.wireOp",EDGE,"E9.0.20.0")])]}),"instanceName":"5"});
            var Q186;
            Q186=makeQuery(id+"F51.opPattern","COPY",BODY,{"derivedFrom":makeQuery(id+"F3.opExtrude","SWEPT_BODY",BODY,{"disambiguationData":[OSD([sQuery(id+"F1.wireOp",EDGE,"E9.0.18.0")])]}),"instanceName":"26"});
            var Q187;
            Q187=makeQuery(id+"F53.opPattern","COPY",BODY,{"derivedFrom":makeQuery(id+"F3.opExtrude","SWEPT_BODY",BODY,{"disambiguationData":[OSD([sQuery(id+"F1.wireOp",EDGE,"E9.0.16.0")])]}),"instanceName":"19"});
            var Q188;
            Q188=makeQuery(id+"F51.opPattern","COPY",BODY,{"derivedFrom":makeQuery(id+"F3.opExtrude","SWEPT_BODY",BODY,{"disambiguationData":[OSD([sQuery(id+"F1.wireOp",EDGE,"E9.0.18.0")])]}),"instanceName":"33"});
            var Q189;
            Q189=makeQuery(id+"F53.opPattern","COPY",BODY,{"derivedFrom":makeQuery(id+"F3.opExtrude","SWEPT_BODY",BODY,{"disambiguationData":[OSD([sQuery(id+"F1.wireOp",EDGE,"E9.0.15.0")])]}),"instanceName":"32"});
            var Q190;
            Q190=makeQuery(id+"F50.opPattern","COPY",BODY,{"derivedFrom":makeQuery(id+"F3.opExtrude","SWEPT_BODY",BODY,{"disambiguationData":[OSD([sQuery(id+"F1.wireOp",EDGE,"E9.0.20.0")])]}),"instanceName":"4"});
            var Q191;
            Q191=makeQuery(id+"F53.opPattern","COPY",BODY,{"derivedFrom":makeQuery(id+"F3.opExtrude","SWEPT_BODY",BODY,{"disambiguationData":[OSD([sQuery(id+"F1.wireOp",EDGE,"E9.0.15.0")])]}),"instanceName":"31"});
            var Q192;
            Q192=makeQuery(id+"F53.opPattern","COPY",BODY,{"derivedFrom":makeQuery(id+"F3.opExtrude","SWEPT_BODY",BODY,{"disambiguationData":[OSD([sQuery(id+"F1.wireOp",EDGE,"E9.0.16.0")])]}),"instanceName":"30"});
            var Q193;
            Q193=makeQuery(id+"F51.opPattern","COPY",BODY,{"derivedFrom":makeQuery(id+"F3.opExtrude","SWEPT_BODY",BODY,{"disambiguationData":[OSD([sQuery(id+"F1.wireOp",EDGE,"E9.0.19.0")])]}),"instanceName":"5"});
            var Q194;
            Q194=makeQuery(id+"F51.opPattern","COPY",BODY,{"derivedFrom":makeQuery(id+"F3.opExtrude","SWEPT_BODY",BODY,{"disambiguationData":[OSD([sQuery(id+"F1.wireOp",EDGE,"E9.0.19.0")])]}),"instanceName":"27"});
            var Q195;
            Q195=makeQuery(id+"F51.opPattern","COPY",BODY,{"derivedFrom":makeQuery(id+"F3.opExtrude","SWEPT_BODY",BODY,{"disambiguationData":[OSD([sQuery(id+"F1.wireOp",EDGE,"E9.0.19.0")])]}),"instanceName":"33"});
            var Q196;
            Q196=makeQuery(id+"F51.opPattern","COPY",BODY,{"derivedFrom":makeQuery(id+"F3.opExtrude","SWEPT_BODY",BODY,{"disambiguationData":[OSD([sQuery(id+"F1.wireOp",EDGE,"E9.0.18.0")])]}),"instanceName":"3"});
            var Q197;
            Q197=makeQuery(id+"F54.opPattern","COPY",BODY,{"derivedFrom":makeQuery(id+"F3.opExtrude","SWEPT_BODY",BODY,{"disambiguationData":[OSD([sQuery(id+"F1.wireOp",EDGE,"E9.0.14.0")])]}),"instanceName":"26"});
            var Q198;
            Q198=makeQuery(id+"F51.opPattern","COPY",BODY,{"derivedFrom":makeQuery(id+"F3.opExtrude","SWEPT_BODY",BODY,{"disambiguationData":[OSD([sQuery(id+"F1.wireOp",EDGE,"E9.0.18.0")])]}),"instanceName":"36"});
            var Q199;
            Q199=makeQuery(id+"F51.opPattern","COPY",BODY,{"derivedFrom":makeQuery(id+"F3.opExtrude","SWEPT_BODY",BODY,{"disambiguationData":[OSD([sQuery(id+"F1.wireOp",EDGE,"E9.0.19.0")])]}),"instanceName":"3"});
            var Q200;
            Q200=makeQuery(id+"F52.opPattern","COPY",BODY,{"derivedFrom":makeQuery(id+"F3.opExtrude","SWEPT_BODY",BODY,{"disambiguationData":[OSD([sQuery(id+"F1.wireOp",EDGE,"E9.0.17.0")])]}),"instanceName":"33"});
            var Q201;
            Q201=makeQuery(id+"F51.opPattern","COPY",BODY,{"derivedFrom":makeQuery(id+"F3.opExtrude","SWEPT_BODY",BODY,{"disambiguationData":[OSD([sQuery(id+"F1.wireOp",EDGE,"E9.0.18.0")])]}),"instanceName":"27"});
            var Q202;
            Q202=makeQuery(id+"F50.opPattern","COPY",BODY,{"derivedFrom":makeQuery(id+"F3.opExtrude","SWEPT_BODY",BODY,{"disambiguationData":[OSD([sQuery(id+"F1.wireOp",EDGE,"E9.0.20.0")])]}),"instanceName":"1"});
            var Q203;
            Q203=makeQuery(id+"F53.opPattern","COPY",BODY,{"derivedFrom":makeQuery(id+"F3.opExtrude","SWEPT_BODY",BODY,{"disambiguationData":[OSD([sQuery(id+"F1.wireOp",EDGE,"E9.0.16.0")])]}),"instanceName":"3"});
            var Q204;
            Q204=makeQuery(id+"F53.opPattern","COPY",BODY,{"derivedFrom":makeQuery(id+"F3.opExtrude","SWEPT_BODY",BODY,{"disambiguationData":[OSD([sQuery(id+"F1.wireOp",EDGE,"E9.0.15.0")])]}),"instanceName":"3"});
            var Q205;
            Q205=makeQuery(id+"F53.opPattern","COPY",BODY,{"derivedFrom":makeQuery(id+"F3.opExtrude","SWEPT_BODY",BODY,{"disambiguationData":[OSD([sQuery(id+"F1.wireOp",EDGE,"E9.0.15.0")])]}),"instanceName":"40"});
            var Q206;
            Q206=makeQuery(id+"F53.opPattern","COPY",BODY,{"derivedFrom":makeQuery(id+"F3.opExtrude","SWEPT_BODY",BODY,{"disambiguationData":[OSD([sQuery(id+"F1.wireOp",EDGE,"E9.0.15.0")])]}),"instanceName":"35"});
            var Q207;
            Q207=makeQuery(id+"F54.opPattern","COPY",BODY,{"derivedFrom":makeQuery(id+"F3.opExtrude","SWEPT_BODY",BODY,{"disambiguationData":[OSD([sQuery(id+"F1.wireOp",EDGE,"E9.0.14.0")])]}),"instanceName":"29"});
            var Q208;
            Q208=makeQuery(id+"F53.opPattern","COPY",BODY,{"derivedFrom":makeQuery(id+"F3.opExtrude","SWEPT_BODY",BODY,{"disambiguationData":[OSD([sQuery(id+"F1.wireOp",EDGE,"E9.0.16.0")])]}),"instanceName":"28"});
            var Q209;
            Q209=makeQuery(id+"F54.opPattern","COPY",BODY,{"derivedFrom":makeQuery(id+"F3.opExtrude","SWEPT_BODY",BODY,{"disambiguationData":[OSD([sQuery(id+"F1.wireOp",EDGE,"E9.0.14.0")])]}),"instanceName":"30"});
            var Q210;
            Q210=makeQuery(id+"F53.opPattern","COPY",BODY,{"derivedFrom":makeQuery(id+"F3.opExtrude","SWEPT_BODY",BODY,{"disambiguationData":[OSD([sQuery(id+"F1.wireOp",EDGE,"E9.0.15.0")])]}),"instanceName":"28"});
            var Q211;
            Q211=makeQuery(id+"F53.opPattern","COPY",BODY,{"derivedFrom":makeQuery(id+"F3.opExtrude","SWEPT_BODY",BODY,{"disambiguationData":[OSD([sQuery(id+"F1.wireOp",EDGE,"E9.0.16.0")])]}),"instanceName":"27"});
            var Q212;
            Q212=makeQuery(id+"F51.opPattern","COPY",BODY,{"derivedFrom":makeQuery(id+"F3.opExtrude","SWEPT_BODY",BODY,{"disambiguationData":[OSD([sQuery(id+"F1.wireOp",EDGE,"E9.0.19.0")])]}),"instanceName":"7"});
            var Q213;
            Q213=makeQuery(id+"F54.opPattern","COPY",BODY,{"derivedFrom":makeQuery(id+"F3.opExtrude","SWEPT_BODY",BODY,{"disambiguationData":[OSD([sQuery(id+"F1.wireOp",EDGE,"E9.0.14.0")])]}),"instanceName":"31"});
            var Q214;
            Q214=makeQuery(id+"F51.opPattern","COPY",BODY,{"derivedFrom":makeQuery(id+"F3.opExtrude","SWEPT_BODY",BODY,{"disambiguationData":[OSD([sQuery(id+"F1.wireOp",EDGE,"E9.0.19.0")])]}),"instanceName":"40"});
            var Q215;
            Q215=makeQuery(id+"F51.opPattern","COPY",BODY,{"derivedFrom":makeQuery(id+"F3.opExtrude","SWEPT_BODY",BODY,{"disambiguationData":[OSD([sQuery(id+"F1.wireOp",EDGE,"E9.0.18.0")])]}),"instanceName":"40"});
            var Q216;
            Q216=makeQuery(id+"F54.opPattern","COPY",BODY,{"derivedFrom":makeQuery(id+"F3.opExtrude","SWEPT_BODY",BODY,{"disambiguationData":[OSD([sQuery(id+"F1.wireOp",EDGE,"E9.0.14.0")])]}),"instanceName":"32"});
            var Q217;
            Q217=makeQuery(id+"F54.opPattern","COPY",BODY,{"derivedFrom":makeQuery(id+"F3.opExtrude","SWEPT_BODY",BODY,{"disambiguationData":[OSD([sQuery(id+"F1.wireOp",EDGE,"E9.0.14.0")])]}),"instanceName":"39"});
            var Q218;
            Q218=makeQuery(id+"F54.opPattern","COPY",BODY,{"derivedFrom":makeQuery(id+"F3.opExtrude","SWEPT_BODY",BODY,{"disambiguationData":[OSD([sQuery(id+"F1.wireOp",EDGE,"E9.0.14.0")])]}),"instanceName":"40"});
            var Q219;
            Q219=makeQuery(id+"F53.opPattern","COPY",BODY,{"derivedFrom":makeQuery(id+"F3.opExtrude","SWEPT_BODY",BODY,{"disambiguationData":[OSD([sQuery(id+"F1.wireOp",EDGE,"E9.0.15.0")])]}),"instanceName":"27"});
            var Q220;
            Q220=makeQuery(id+"F53.opPattern","COPY",BODY,{"derivedFrom":makeQuery(id+"F3.opExtrude","SWEPT_BODY",BODY,{"disambiguationData":[OSD([sQuery(id+"F1.wireOp",EDGE,"E9.0.16.0")])]}),"instanceName":"26"});
            var Q221;
            Q221=makeQuery(id+"F50.opPattern","COPY",BODY,{"derivedFrom":makeQuery(id+"F3.opExtrude","SWEPT_BODY",BODY,{"disambiguationData":[OSD([sQuery(id+"F1.wireOp",EDGE,"E9.0.20.0")])]}),"instanceName":"26"});
            var Q222;
            Q222=makeQuery(id+"F51.opPattern","COPY",BODY,{"derivedFrom":makeQuery(id+"F3.opExtrude","SWEPT_BODY",BODY,{"disambiguationData":[OSD([sQuery(id+"F1.wireOp",EDGE,"E9.0.19.0")])]}),"instanceName":"39"});
            var Q223;
            Q223=makeQuery(id+"F50.opPattern","COPY",BODY,{"derivedFrom":makeQuery(id+"F3.opExtrude","SWEPT_BODY",BODY,{"disambiguationData":[OSD([sQuery(id+"F1.wireOp",EDGE,"E9.0.20.0")])]}),"instanceName":"27"});
            var Q224;
            Q224=makeQuery(id+"F50.opPattern","COPY",BODY,{"derivedFrom":makeQuery(id+"F3.opExtrude","SWEPT_BODY",BODY,{"disambiguationData":[OSD([sQuery(id+"F1.wireOp",EDGE,"E9.0.20.0")])]}),"instanceName":"28"});
            var Q225;
            Q225=makeQuery(id+"F54.opPattern","COPY",BODY,{"derivedFrom":makeQuery(id+"F3.opExtrude","SWEPT_BODY",BODY,{"disambiguationData":[OSD([sQuery(id+"F1.wireOp",EDGE,"E9.0.14.0")])]}),"instanceName":"41"});
            var Q226;
            Q226=makeQuery(id+"F53.opPattern","COPY",BODY,{"derivedFrom":makeQuery(id+"F3.opExtrude","SWEPT_BODY",BODY,{"disambiguationData":[OSD([sQuery(id+"F1.wireOp",EDGE,"E9.0.15.0")])]}),"instanceName":"26"});
            var Q227;
            Q227=makeQuery(id+"F50.opPattern","COPY",BODY,{"derivedFrom":makeQuery(id+"F3.opExtrude","SWEPT_BODY",BODY,{"disambiguationData":[OSD([sQuery(id+"F1.wireOp",EDGE,"E9.0.20.0")])]}),"instanceName":"23"});
            var Q228;
            Q228=makeQuery(id+"F53.opPattern","COPY",BODY,{"derivedFrom":makeQuery(id+"F3.opExtrude","SWEPT_BODY",BODY,{"disambiguationData":[OSD([sQuery(id+"F1.wireOp",EDGE,"E9.0.16.0")])]}),"instanceName":"25"});
            var Q229;
            Q229=makeQuery(id+"F51.opPattern","COPY",BODY,{"derivedFrom":makeQuery(id+"F3.opExtrude","SWEPT_BODY",BODY,{"disambiguationData":[OSD([sQuery(id+"F1.wireOp",EDGE,"E9.0.18.0")])]}),"instanceName":"8"});
            var Q230;
            Q230=makeQuery(id+"F50.opPattern","COPY",BODY,{"derivedFrom":makeQuery(id+"F3.opExtrude","SWEPT_BODY",BODY,{"disambiguationData":[OSD([sQuery(id+"F1.wireOp",EDGE,"E9.0.20.0")])]}),"instanceName":"24"});
            var Q231;
            Q231=makeQuery(id+"F51.opPattern","COPY",BODY,{"derivedFrom":makeQuery(id+"F3.opExtrude","SWEPT_BODY",BODY,{"disambiguationData":[OSD([sQuery(id+"F1.wireOp",EDGE,"E9.0.19.0")])]}),"instanceName":"8"});
            var Q232;
            Q232=makeQuery(id+"F51.opPattern","COPY",BODY,{"derivedFrom":makeQuery(id+"F3.opExtrude","SWEPT_BODY",BODY,{"disambiguationData":[OSD([sQuery(id+"F1.wireOp",EDGE,"E9.0.18.0")])]}),"instanceName":"39"});
            var Q233;
            Q233=makeQuery(id+"F50.opPattern","COPY",BODY,{"derivedFrom":makeQuery(id+"F3.opExtrude","SWEPT_BODY",BODY,{"disambiguationData":[OSD([sQuery(id+"F1.wireOp",EDGE,"E9.0.20.0")])]}),"instanceName":"29"});
            var Q234;
            Q234=makeQuery(id+"F53.opPattern","COPY",BODY,{"derivedFrom":makeQuery(id+"F3.opExtrude","SWEPT_BODY",BODY,{"disambiguationData":[OSD([sQuery(id+"F1.wireOp",EDGE,"E9.0.15.0")])]}),"instanceName":"25"});
            var Q235;
            Q235=makeQuery(id+"F53.opPattern","COPY",BODY,{"derivedFrom":makeQuery(id+"F3.opExtrude","SWEPT_BODY",BODY,{"disambiguationData":[OSD([sQuery(id+"F1.wireOp",EDGE,"E9.0.16.0")])]}),"instanceName":"24"});
            var Q236;
            Q236=makeQuery(id+"F51.opPattern","COPY",BODY,{"derivedFrom":makeQuery(id+"F3.opExtrude","SWEPT_BODY",BODY,{"disambiguationData":[OSD([sQuery(id+"F1.wireOp",EDGE,"E9.0.18.0")])]}),"instanceName":"9"});
            var Q237;
            Q237=makeQuery(id+"F51.opPattern","COPY",BODY,{"derivedFrom":makeQuery(id+"F3.opExtrude","SWEPT_BODY",BODY,{"disambiguationData":[OSD([sQuery(id+"F1.wireOp",EDGE,"E9.0.19.0")])]}),"instanceName":"38"});
            var Q238;
            Q238=makeQuery(id+"F50.opPattern","COPY",BODY,{"derivedFrom":makeQuery(id+"F3.opExtrude","SWEPT_BODY",BODY,{"disambiguationData":[OSD([sQuery(id+"F1.wireOp",EDGE,"E9.0.20.0")])]}),"instanceName":"30"});
            var Q239;
            Q239=makeQuery(id+"F50.opPattern","COPY",BODY,{"derivedFrom":makeQuery(id+"F3.opExtrude","SWEPT_BODY",BODY,{"disambiguationData":[OSD([sQuery(id+"F1.wireOp",EDGE,"E9.0.20.0")])]}),"instanceName":"31"});
            var Q240;
            Q240=makeQuery(id+"F55.opPattern","COPY",BODY,{"derivedFrom":makeQuery(id+"F3.opExtrude","SWEPT_BODY",BODY,{"disambiguationData":[OSD([sQuery(id+"F1.wireOp",EDGE,"E9.0.12.0")])]}),"instanceName":"9"});
            var Q241;
            Q241=makeQuery(id+"F55.opPattern","COPY",BODY,{"derivedFrom":makeQuery(id+"F3.opExtrude","SWEPT_BODY",BODY,{"disambiguationData":[OSD([sQuery(id+"F1.wireOp",EDGE,"E9.0.13.0")])]}),"instanceName":"18"});
            var Q242;
            Q242=makeQuery(id+"F54.opPattern","COPY",BODY,{"derivedFrom":makeQuery(id+"F3.opExtrude","SWEPT_BODY",BODY,{"disambiguationData":[OSD([sQuery(id+"F1.wireOp",EDGE,"E9.0.14.0")])]}),"instanceName":"43"});
            var Q243;
            Q243=makeQuery(id+"F55.opPattern","COPY",BODY,{"derivedFrom":makeQuery(id+"F3.opExtrude","SWEPT_BODY",BODY,{"disambiguationData":[OSD([sQuery(id+"F1.wireOp",EDGE,"E9.0.13.0")])]}),"instanceName":"8"});
            var Q244;
            Q244=makeQuery(id+"F55.opPattern","COPY",BODY,{"derivedFrom":makeQuery(id+"F3.opExtrude","SWEPT_BODY",BODY,{"disambiguationData":[OSD([sQuery(id+"F1.wireOp",EDGE,"E9.0.12.0")])]}),"instanceName":"18"});
            var Q245;
            Q245=makeQuery(id+"F53.opPattern","COPY",BODY,{"derivedFrom":makeQuery(id+"F3.opExtrude","SWEPT_BODY",BODY,{"disambiguationData":[OSD([sQuery(id+"F1.wireOp",EDGE,"E9.0.15.0")])]}),"instanceName":"24"});
            var Q246;
            Q246=makeQuery(id+"F51.opPattern","COPY",BODY,{"derivedFrom":makeQuery(id+"F3.opExtrude","SWEPT_BODY",BODY,{"disambiguationData":[OSD([sQuery(id+"F1.wireOp",EDGE,"E9.0.19.0")])]}),"instanceName":"9"});
            var Q247;
            Q247=makeQuery(id+"F54.opPattern","COPY",BODY,{"derivedFrom":makeQuery(id+"F3.opExtrude","SWEPT_BODY",BODY,{"disambiguationData":[OSD([sQuery(id+"F1.wireOp",EDGE,"E9.0.14.0")])]}),"instanceName":"14"});
            var Q248;
            Q248=makeQuery(id+"F51.opPattern","COPY",BODY,{"derivedFrom":makeQuery(id+"F3.opExtrude","SWEPT_BODY",BODY,{"disambiguationData":[OSD([sQuery(id+"F1.wireOp",EDGE,"E9.0.18.0")])]}),"instanceName":"35"});
            var Q249;
            Q249=makeQuery(id+"F54.opPattern","COPY",BODY,{"derivedFrom":makeQuery(id+"F3.opExtrude","SWEPT_BODY",BODY,{"disambiguationData":[OSD([sQuery(id+"F1.wireOp",EDGE,"E9.0.14.0")])]}),"instanceName":"13"});
            var Q250;
            Q250=makeQuery(id+"F53.opPattern","COPY",BODY,{"derivedFrom":makeQuery(id+"F3.opExtrude","SWEPT_BODY",BODY,{"disambiguationData":[OSD([sQuery(id+"F1.wireOp",EDGE,"E9.0.16.0")])]}),"instanceName":"23"});
            var Q251;
            Q251=makeQuery(id+"F51.opPattern","COPY",BODY,{"derivedFrom":makeQuery(id+"F3.opExtrude","SWEPT_BODY",BODY,{"disambiguationData":[OSD([sQuery(id+"F1.wireOp",EDGE,"E9.0.18.0")])]}),"instanceName":"10"});
            var Q252;
            Q252=makeQuery(id+"F51.opPattern","COPY",BODY,{"derivedFrom":makeQuery(id+"F3.opExtrude","SWEPT_BODY",BODY,{"disambiguationData":[OSD([sQuery(id+"F1.wireOp",EDGE,"E9.0.19.0")])]}),"instanceName":"32"});
            var Q253;
            Q253=makeQuery(id+"F51.opPattern","COPY",BODY,{"derivedFrom":makeQuery(id+"F3.opExtrude","SWEPT_BODY",BODY,{"disambiguationData":[OSD([sQuery(id+"F1.wireOp",EDGE,"E9.0.19.0")])]}),"instanceName":"24"});
            var Q254;
            Q254=makeQuery(id+"F54.opPattern","COPY",BODY,{"derivedFrom":makeQuery(id+"F3.opExtrude","SWEPT_BODY",BODY,{"disambiguationData":[OSD([sQuery(id+"F1.wireOp",EDGE,"E9.0.14.0")])]}),"instanceName":"12"});
            var Q255;
            Q255=makeQuery(id+"F53.opPattern","COPY",BODY,{"derivedFrom":makeQuery(id+"F3.opExtrude","SWEPT_BODY",BODY,{"disambiguationData":[OSD([sQuery(id+"F1.wireOp",EDGE,"E9.0.15.0")])]}),"instanceName":"23"});
            var Q256;
            Q256=makeQuery(id+"F51.opPattern","COPY",BODY,{"derivedFrom":makeQuery(id+"F3.opExtrude","SWEPT_BODY",BODY,{"disambiguationData":[OSD([sQuery(id+"F1.wireOp",EDGE,"E9.0.18.0")])]}),"instanceName":"25"});
            var Q257;
            Q257=makeQuery(id+"F53.opPattern","COPY",BODY,{"derivedFrom":makeQuery(id+"F3.opExtrude","SWEPT_BODY",BODY,{"disambiguationData":[OSD([sQuery(id+"F1.wireOp",EDGE,"E9.0.16.0")])]}),"instanceName":"22"});
            var Q258;
            Q258=makeQuery(id+"F54.opPattern","COPY",BODY,{"derivedFrom":makeQuery(id+"F3.opExtrude","SWEPT_BODY",BODY,{"disambiguationData":[OSD([sQuery(id+"F1.wireOp",EDGE,"E9.0.14.0")])]}),"instanceName":"11"});
            var Q259;
            Q259=makeQuery(id+"F53.opPattern","COPY",BODY,{"derivedFrom":makeQuery(id+"F3.opExtrude","SWEPT_BODY",BODY,{"disambiguationData":[OSD([sQuery(id+"F1.wireOp",EDGE,"E9.0.16.0")])]}),"instanceName":"33"});
            var Q260;
            Q260=makeQuery(id+"F54.opPattern","COPY",BODY,{"derivedFrom":makeQuery(id+"F3.opExtrude","SWEPT_BODY",BODY,{"disambiguationData":[OSD([sQuery(id+"F1.wireOp",EDGE,"E9.0.14.0")])]}),"instanceName":"46"});
            var Q261;
            Q261=makeQuery(id+"F55.opPattern","COPY",BODY,{"derivedFrom":makeQuery(id+"F3.opExtrude","SWEPT_BODY",BODY,{"disambiguationData":[OSD([sQuery(id+"F1.wireOp",EDGE,"E9.0.12.0")])]}),"instanceName":"1"});
            var Q262;
            Q262=makeQuery(id+"F55.opPattern","COPY",BODY,{"derivedFrom":makeQuery(id+"F3.opExtrude","SWEPT_BODY",BODY,{"disambiguationData":[OSD([sQuery(id+"F1.wireOp",EDGE,"E9.0.13.0")])]}),"instanceName":"17"});
            var Q263;
            Q263=makeQuery(id+"F55.opPattern","COPY",BODY,{"derivedFrom":makeQuery(id+"F3.opExtrude","SWEPT_BODY",BODY,{"disambiguationData":[OSD([sQuery(id+"F1.wireOp",EDGE,"E9.0.12.0")])]}),"instanceName":"17"});
            var Q264;
            Q264=makeQuery(id+"F53.opPattern","COPY",BODY,{"derivedFrom":makeQuery(id+"F3.opExtrude","SWEPT_BODY",BODY,{"disambiguationData":[OSD([sQuery(id+"F1.wireOp",EDGE,"E9.0.15.0")])]}),"instanceName":"22"});
            var Q265;
            Q265=makeQuery(id+"F55.opPattern","COPY",BODY,{"derivedFrom":makeQuery(id+"F3.opExtrude","SWEPT_BODY",BODY,{"disambiguationData":[OSD([sQuery(id+"F1.wireOp",EDGE,"E9.0.13.0")])]}),"instanceName":"16"});
            var Q266;
            Q266=makeQuery(id+"F55.opPattern","COPY",BODY,{"derivedFrom":makeQuery(id+"F3.opExtrude","SWEPT_BODY",BODY,{"disambiguationData":[OSD([sQuery(id+"F1.wireOp",EDGE,"E9.0.13.0")])]}),"instanceName":"1"});
            var Q267;
            Q267=makeQuery(id+"F51.opPattern","COPY",BODY,{"derivedFrom":makeQuery(id+"F3.opExtrude","SWEPT_BODY",BODY,{"disambiguationData":[OSD([sQuery(id+"F1.wireOp",EDGE,"E9.0.19.0")])]}),"instanceName":"25"});
            var Q268;
            Q268=makeQuery(id+"F52.opPattern","COPY",BODY,{"derivedFrom":makeQuery(id+"F3.opExtrude","SWEPT_BODY",BODY,{"disambiguationData":[OSD([sQuery(id+"F1.wireOp",EDGE,"E9.0.17.0")])]}),"instanceName":"1"});
            var Q269;
            Q269=makeQuery(id+"F53.opPattern","COPY",BODY,{"derivedFrom":makeQuery(id+"F3.opExtrude","SWEPT_BODY",BODY,{"disambiguationData":[OSD([sQuery(id+"F1.wireOp",EDGE,"E9.0.16.0")])]}),"instanceName":"21"});
            var Q270;
            Q270=makeQuery(id+"F55.opPattern","COPY",BODY,{"derivedFrom":makeQuery(id+"F3.opExtrude","SWEPT_BODY",BODY,{"disambiguationData":[OSD([sQuery(id+"F1.wireOp",EDGE,"E9.0.12.0")])]}),"instanceName":"5"});
            var Q271;
            Q271=makeQuery(id+"F51.opPattern","COPY",BODY,{"derivedFrom":makeQuery(id+"F3.opExtrude","SWEPT_BODY",BODY,{"disambiguationData":[OSD([sQuery(id+"F1.wireOp",EDGE,"E9.0.19.0")])]}),"instanceName":"10"});
            var Q272;
            Q272=makeQuery(id+"F53.opPattern","COPY",BODY,{"derivedFrom":makeQuery(id+"F3.opExtrude","SWEPT_BODY",BODY,{"disambiguationData":[OSD([sQuery(id+"F1.wireOp",EDGE,"E9.0.15.0")])]}),"instanceName":"36"});
            var Q273;
            Q273=makeQuery(id+"F55.opPattern","COPY",BODY,{"derivedFrom":makeQuery(id+"F3.opExtrude","SWEPT_BODY",BODY,{"disambiguationData":[OSD([sQuery(id+"F1.wireOp",EDGE,"E9.0.13.0")])]}),"instanceName":"5"});
            var Q274;
            Q274=makeQuery(id+"F55.opPattern","COPY",BODY,{"derivedFrom":makeQuery(id+"F3.opExtrude","SWEPT_BODY",BODY,{"disambiguationData":[OSD([sQuery(id+"F1.wireOp",EDGE,"E9.0.12.0")])]}),"instanceName":"6"});
            var Q275;
            Q275=makeQuery(id+"F51.opPattern","COPY",BODY,{"derivedFrom":makeQuery(id+"F3.opExtrude","SWEPT_BODY",BODY,{"disambiguationData":[OSD([sQuery(id+"F1.wireOp",EDGE,"E9.0.18.0")])]}),"instanceName":"11"});
            var Q276;
            Q276=makeQuery(id+"F53.opPattern","COPY",BODY,{"derivedFrom":makeQuery(id+"F3.opExtrude","SWEPT_BODY",BODY,{"disambiguationData":[OSD([sQuery(id+"F1.wireOp",EDGE,"E9.0.16.0")])]}),"instanceName":"32"});
            var Q277;
            Q277=makeQuery(id+"F55.opPattern","COPY",BODY,{"derivedFrom":makeQuery(id+"F3.opExtrude","SWEPT_BODY",BODY,{"disambiguationData":[OSD([sQuery(id+"F1.wireOp",EDGE,"E9.0.12.0")])]}),"instanceName":"8"});
            var Q278;
            Q278=makeQuery(id+"F53.opPattern","COPY",BODY,{"derivedFrom":makeQuery(id+"F3.opExtrude","SWEPT_BODY",BODY,{"disambiguationData":[OSD([sQuery(id+"F1.wireOp",EDGE,"E9.0.15.0")])]}),"instanceName":"21"});
            var Q279;
            Q279=makeQuery(id+"F50.opPattern","COPY",BODY,{"derivedFrom":makeQuery(id+"F3.opExtrude","SWEPT_BODY",BODY,{"disambiguationData":[OSD([sQuery(id+"F1.wireOp",EDGE,"E9.0.20.0")])]}),"instanceName":"17"});
            var Q280;
            Q280=makeQuery(id+"F54.opPattern","COPY",BODY,{"derivedFrom":makeQuery(id+"F3.opExtrude","SWEPT_BODY",BODY,{"disambiguationData":[OSD([sQuery(id+"F1.wireOp",EDGE,"E9.0.14.0")])]}),"instanceName":"10"});
            var Q281;
            Q281=makeQuery(id+"F53.opPattern","COPY",BODY,{"derivedFrom":makeQuery(id+"F3.opExtrude","SWEPT_BODY",BODY,{"disambiguationData":[OSD([sQuery(id+"F1.wireOp",EDGE,"E9.0.15.0")])]}),"instanceName":"1"});
            var Q282;
            Q282=makeQuery(id+"F53.opPattern","COPY",BODY,{"derivedFrom":makeQuery(id+"F3.opExtrude","SWEPT_BODY",BODY,{"disambiguationData":[OSD([sQuery(id+"F1.wireOp",EDGE,"E9.0.16.0")])]}),"instanceName":"20"});
            var Q283;
            Q283=makeQuery(id+"F53.opPattern","COPY",BODY,{"derivedFrom":makeQuery(id+"F3.opExtrude","SWEPT_BODY",BODY,{"disambiguationData":[OSD([sQuery(id+"F1.wireOp",EDGE,"E9.0.15.0")])]}),"instanceName":"20"});
            var Q284;
            Q284=makeQuery(id+"F53.opPattern","COPY",BODY,{"derivedFrom":makeQuery(id+"F3.opExtrude","SWEPT_BODY",BODY,{"disambiguationData":[OSD([sQuery(id+"F1.wireOp",EDGE,"E9.0.16.0")])]}),"instanceName":"1"});
            var Q285;
            Q285=makeQuery(id+"F54.opPattern","COPY",BODY,{"derivedFrom":makeQuery(id+"F3.opExtrude","SWEPT_BODY",BODY,{"disambiguationData":[OSD([sQuery(id+"F1.wireOp",EDGE,"E9.0.14.0")])]}),"instanceName":"9"});
            var Q286;
            Q286=makeQuery(id+"F55.opPattern","COPY",BODY,{"derivedFrom":makeQuery(id+"F3.opExtrude","SWEPT_BODY",BODY,{"disambiguationData":[OSD([sQuery(id+"F1.wireOp",EDGE,"E9.0.12.0")])]}),"instanceName":"16"});
            var Q287;
            Q287=makeQuery(id+"F51.opPattern","COPY",BODY,{"derivedFrom":makeQuery(id+"F3.opExtrude","SWEPT_BODY",BODY,{"disambiguationData":[OSD([sQuery(id+"F1.wireOp",EDGE,"E9.0.19.0")])]}),"instanceName":"11"});
            var Q288;
            Q288=makeQuery(id+"F54.opPattern","COPY",BODY,{"derivedFrom":makeQuery(id+"F3.opExtrude","SWEPT_BODY",BODY,{"disambiguationData":[OSD([sQuery(id+"F1.wireOp",EDGE,"E9.0.14.0")])]}),"instanceName":"8"});
            var Q289;
            Q289=makeQuery(id+"F50.opPattern","COPY",BODY,{"derivedFrom":makeQuery(id+"F3.opExtrude","SWEPT_BODY",BODY,{"disambiguationData":[OSD([sQuery(id+"F1.wireOp",EDGE,"E9.0.20.0")])]}),"instanceName":"32"});
            var Q290;
            Q290=makeQuery(id+"F50.opPattern","COPY",BODY,{"derivedFrom":makeQuery(id+"F3.opExtrude","SWEPT_BODY",BODY,{"disambiguationData":[OSD([sQuery(id+"F1.wireOp",EDGE,"E9.0.20.0")])]}),"instanceName":"33"});
            var Q291;
            Q291=makeQuery(id+"F55.opPattern","COPY",BODY,{"derivedFrom":makeQuery(id+"F3.opExtrude","SWEPT_BODY",BODY,{"disambiguationData":[OSD([sQuery(id+"F1.wireOp",EDGE,"E9.0.12.0")])]}),"instanceName":"7"});
            var Q292;
            Q292=makeQuery(id+"F55.opPattern","COPY",BODY,{"derivedFrom":makeQuery(id+"F3.opExtrude","SWEPT_BODY",BODY,{"disambiguationData":[OSD([sQuery(id+"F1.wireOp",EDGE,"E9.0.13.0")])]}),"instanceName":"7"});
            var Q293;
            Q293=makeQuery(id+"F55.opPattern","COPY",BODY,{"derivedFrom":makeQuery(id+"F3.opExtrude","SWEPT_BODY",BODY,{"disambiguationData":[OSD([sQuery(id+"F1.wireOp",EDGE,"E9.0.13.0")])]}),"instanceName":"15"});
            var Q294;
            Q294=makeQuery(id+"F54.opPattern","COPY",BODY,{"derivedFrom":makeQuery(id+"F3.opExtrude","SWEPT_BODY",BODY,{"disambiguationData":[OSD([sQuery(id+"F1.wireOp",EDGE,"E9.0.14.0")])]}),"instanceName":"16"});
            var Q295;
            Q295=makeQuery(id+"F54.opPattern","COPY",BODY,{"derivedFrom":makeQuery(id+"F3.opExtrude","SWEPT_BODY",BODY,{"disambiguationData":[OSD([sQuery(id+"F1.wireOp",EDGE,"E9.0.14.0")])]}),"instanceName":"17"});
            var Q296;
            Q296=makeQuery(id+"F52.opPattern","COPY",BODY,{"derivedFrom":makeQuery(id+"F3.opExtrude","SWEPT_BODY",BODY,{"disambiguationData":[OSD([sQuery(id+"F1.wireOp",EDGE,"E9.0.17.0")])]}),"instanceName":"39"});
            var Q297;
            Q297=makeQuery(id+"F54.opPattern","COPY",BODY,{"derivedFrom":makeQuery(id+"F3.opExtrude","SWEPT_BODY",BODY,{"disambiguationData":[OSD([sQuery(id+"F1.wireOp",EDGE,"E9.0.14.0")])]}),"instanceName":"18"});
            var Q298;
            Q298=makeQuery(id+"F51.opPattern","COPY",BODY,{"derivedFrom":makeQuery(id+"F3.opExtrude","SWEPT_BODY",BODY,{"disambiguationData":[OSD([sQuery(id+"F1.wireOp",EDGE,"E9.0.18.0")])]}),"instanceName":"38"});
            var Q299;
            Q299=makeQuery(id+"F54.opPattern","COPY",BODY,{"derivedFrom":makeQuery(id+"F3.opExtrude","SWEPT_BODY",BODY,{"disambiguationData":[OSD([sQuery(id+"F1.wireOp",EDGE,"E9.0.14.0")])]}),"instanceName":"22"});
            var Q300;
            Q300=makeQuery(id+"F51.opPattern","COPY",BODY,{"derivedFrom":makeQuery(id+"F3.opExtrude","SWEPT_BODY",BODY,{"disambiguationData":[OSD([sQuery(id+"F1.wireOp",EDGE,"E9.0.19.0")])]}),"instanceName":"37"});
            var Q301;
            Q301=makeQuery(id+"F51.opPattern","COPY",BODY,{"derivedFrom":makeQuery(id+"F3.opExtrude","SWEPT_BODY",BODY,{"disambiguationData":[OSD([sQuery(id+"F1.wireOp",EDGE,"E9.0.18.0")])]}),"instanceName":"37"});
            var Q302;
            Q302=makeQuery(id+"F53.opPattern","COPY",BODY,{"derivedFrom":makeQuery(id+"F3.opExtrude","SWEPT_BODY",BODY,{"disambiguationData":[OSD([sQuery(id+"F1.wireOp",EDGE,"E9.0.16.0")])]}),"instanceName":"39"});
            var Q303;
            Q303=makeQuery(id+"F50.opPattern","COPY",BODY,{"derivedFrom":makeQuery(id+"F3.opExtrude","SWEPT_BODY",BODY,{"disambiguationData":[OSD([sQuery(id+"F1.wireOp",EDGE,"E9.0.20.0")])]}),"instanceName":"19"});
            var Q304;
            Q304=makeQuery(id+"F53.opPattern","COPY",BODY,{"derivedFrom":makeQuery(id+"F3.opExtrude","SWEPT_BODY",BODY,{"disambiguationData":[OSD([sQuery(id+"F1.wireOp",EDGE,"E9.0.15.0")])]}),"instanceName":"37"});
            var Q305;
            Q305=makeQuery(id+"F51.opPattern","COPY",BODY,{"derivedFrom":makeQuery(id+"F3.opExtrude","SWEPT_BODY",BODY,{"disambiguationData":[OSD([sQuery(id+"F1.wireOp",EDGE,"E9.0.19.0")])]}),"instanceName":"35"});
            var Q306;
            Q306=makeQuery(id+"F51.opPattern","COPY",BODY,{"derivedFrom":makeQuery(id+"F3.opExtrude","SWEPT_BODY",BODY,{"disambiguationData":[OSD([sQuery(id+"F1.wireOp",EDGE,"E9.0.18.0")])]}),"instanceName":"4"});
            var Q307;
            Q307=makeQuery(id+"F52.opPattern","COPY",BODY,{"derivedFrom":makeQuery(id+"F3.opExtrude","SWEPT_BODY",BODY,{"disambiguationData":[OSD([sQuery(id+"F1.wireOp",EDGE,"E9.0.17.0")])]}),"instanceName":"43"});
            var Q308;
            Q308=makeQuery(id+"F51.opPattern","COPY",BODY,{"derivedFrom":makeQuery(id+"F3.opExtrude","SWEPT_BODY",BODY,{"disambiguationData":[OSD([sQuery(id+"F1.wireOp",EDGE,"E9.0.19.0")])]}),"instanceName":"4"});
            var Q309;
            Q309=makeQuery(id+"F52.opPattern","COPY",BODY,{"derivedFrom":makeQuery(id+"F3.opExtrude","SWEPT_BODY",BODY,{"disambiguationData":[OSD([sQuery(id+"F1.wireOp",EDGE,"E9.0.17.0")])]}),"instanceName":"34"});
            var Q310;
            Q310=makeQuery(id+"F51.opPattern","COPY",BODY,{"derivedFrom":makeQuery(id+"F3.opExtrude","SWEPT_BODY",BODY,{"disambiguationData":[OSD([sQuery(id+"F1.wireOp",EDGE,"E9.0.18.0")])]}),"instanceName":"5"});
            var Q311;
            Q311=makeQuery(id+"F54.opPattern","COPY",BODY,{"derivedFrom":makeQuery(id+"F3.opExtrude","SWEPT_BODY",BODY,{"disambiguationData":[OSD([sQuery(id+"F1.wireOp",EDGE,"E9.0.14.0")])]}),"instanceName":"21"});
            var Q312;
            Q312=makeQuery(id+"F54.opPattern","COPY",BODY,{"derivedFrom":makeQuery(id+"F3.opExtrude","SWEPT_BODY",BODY,{"disambiguationData":[OSD([sQuery(id+"F1.wireOp",EDGE,"E9.0.14.0")])]}),"instanceName":"20"});
            var Q313;
            Q313=makeQuery(id+"F54.opPattern","COPY",BODY,{"derivedFrom":makeQuery(id+"F3.opExtrude","SWEPT_BODY",BODY,{"disambiguationData":[OSD([sQuery(id+"F1.wireOp",EDGE,"E9.0.14.0")])]}),"instanceName":"19"});
            var Q314;
            Q314=makeQuery(id+"F55.opPattern","COPY",BODY,{"derivedFrom":makeQuery(id+"F3.opExtrude","SWEPT_BODY",BODY,{"disambiguationData":[OSD([sQuery(id+"F1.wireOp",EDGE,"E9.0.12.0")])]}),"instanceName":"19"});
            var Q315;
            Q315=makeQuery(id+"F55.opPattern","COPY",BODY,{"derivedFrom":makeQuery(id+"F3.opExtrude","SWEPT_BODY",BODY,{"disambiguationData":[OSD([sQuery(id+"F1.wireOp",EDGE,"E9.0.12.0")])]}),"instanceName":"20"});
            var Q316;
            Q316=makeQuery(id+"F55.opPattern","COPY",BODY,{"derivedFrom":makeQuery(id+"F3.opExtrude","SWEPT_BODY",BODY,{"disambiguationData":[OSD([sQuery(id+"F1.wireOp",EDGE,"E9.0.13.0")])]}),"instanceName":"20"});
            var Q317;
            Q317=makeQuery(id+"F55.opPattern","COPY",BODY,{"derivedFrom":makeQuery(id+"F3.opExtrude","SWEPT_BODY",BODY,{"disambiguationData":[OSD([sQuery(id+"F1.wireOp",EDGE,"E9.0.12.0")])]}),"instanceName":"21"});
            var Q318;
            Q318=makeQuery(id+"F55.opPattern","COPY",BODY,{"derivedFrom":makeQuery(id+"F3.opExtrude","SWEPT_BODY",BODY,{"disambiguationData":[OSD([sQuery(id+"F1.wireOp",EDGE,"E9.0.13.0")])]}),"instanceName":"21"});
            var Q319;
            Q319=makeQuery(id+"F55.opPattern","COPY",BODY,{"derivedFrom":makeQuery(id+"F3.opExtrude","SWEPT_BODY",BODY,{"disambiguationData":[OSD([sQuery(id+"F1.wireOp",EDGE,"E9.0.12.0")])]}),"instanceName":"22"});
            var Q320;
            Q320=makeQuery(id+"F55.opPattern","COPY",BODY,{"derivedFrom":makeQuery(id+"F3.opExtrude","SWEPT_BODY",BODY,{"disambiguationData":[OSD([sQuery(id+"F1.wireOp",EDGE,"E9.0.13.0")])]}),"instanceName":"22"});
            var Q321;
            Q321=makeQuery(id+"F55.opPattern","COPY",BODY,{"derivedFrom":makeQuery(id+"F3.opExtrude","SWEPT_BODY",BODY,{"disambiguationData":[OSD([sQuery(id+"F1.wireOp",EDGE,"E9.0.12.0")])]}),"instanceName":"23"});
            var Q322;
            Q322=makeQuery(id+"F55.opPattern","COPY",BODY,{"derivedFrom":makeQuery(id+"F3.opExtrude","SWEPT_BODY",BODY,{"disambiguationData":[OSD([sQuery(id+"F1.wireOp",EDGE,"E9.0.13.0")])]}),"instanceName":"23"});
            var Q323;
            Q323=makeQuery(id+"F55.opPattern","COPY",BODY,{"derivedFrom":makeQuery(id+"F3.opExtrude","SWEPT_BODY",BODY,{"disambiguationData":[OSD([sQuery(id+"F1.wireOp",EDGE,"E9.0.12.0")])]}),"instanceName":"24"});
            var Q324;
            Q324=makeQuery(id+"F55.opPattern","COPY",BODY,{"derivedFrom":makeQuery(id+"F3.opExtrude","SWEPT_BODY",BODY,{"disambiguationData":[OSD([sQuery(id+"F1.wireOp",EDGE,"E9.0.13.0")])]}),"instanceName":"24"});
            var Q325;
            Q325=makeQuery(id+"F55.opPattern","COPY",BODY,{"derivedFrom":makeQuery(id+"F3.opExtrude","SWEPT_BODY",BODY,{"disambiguationData":[OSD([sQuery(id+"F1.wireOp",EDGE,"E9.0.12.0")])]}),"instanceName":"25"});
            var Q326;
            Q326=makeQuery(id+"F55.opPattern","COPY",BODY,{"derivedFrom":makeQuery(id+"F3.opExtrude","SWEPT_BODY",BODY,{"disambiguationData":[OSD([sQuery(id+"F1.wireOp",EDGE,"E9.0.13.0")])]}),"instanceName":"25"});
            var Q327;
            Q327=makeQuery(id+"F55.opPattern","COPY",BODY,{"derivedFrom":makeQuery(id+"F3.opExtrude","SWEPT_BODY",BODY,{"disambiguationData":[OSD([sQuery(id+"F1.wireOp",EDGE,"E9.0.12.0")])]}),"instanceName":"26"});
            var Q328;
            Q328=makeQuery(id+"F55.opPattern","COPY",BODY,{"derivedFrom":makeQuery(id+"F3.opExtrude","SWEPT_BODY",BODY,{"disambiguationData":[OSD([sQuery(id+"F1.wireOp",EDGE,"E9.0.13.0")])]}),"instanceName":"26"});
            var Q329;
            Q329=makeQuery(id+"F55.opPattern","COPY",BODY,{"derivedFrom":makeQuery(id+"F3.opExtrude","SWEPT_BODY",BODY,{"disambiguationData":[OSD([sQuery(id+"F1.wireOp",EDGE,"E9.0.12.0")])]}),"instanceName":"27"});
            var Q330;
            Q330=makeQuery(id+"F55.opPattern","COPY",BODY,{"derivedFrom":makeQuery(id+"F3.opExtrude","SWEPT_BODY",BODY,{"disambiguationData":[OSD([sQuery(id+"F1.wireOp",EDGE,"E9.0.13.0")])]}),"instanceName":"27"});
            var Q331;
            Q331=makeQuery(id+"F55.opPattern","COPY",BODY,{"derivedFrom":makeQuery(id+"F3.opExtrude","SWEPT_BODY",BODY,{"disambiguationData":[OSD([sQuery(id+"F1.wireOp",EDGE,"E9.0.12.0")])]}),"instanceName":"28"});
            var Q332;
            Q332=makeQuery(id+"F55.opPattern","COPY",BODY,{"derivedFrom":makeQuery(id+"F3.opExtrude","SWEPT_BODY",BODY,{"disambiguationData":[OSD([sQuery(id+"F1.wireOp",EDGE,"E9.0.13.0")])]}),"instanceName":"28"});
            var Q333;
            Q333=makeQuery(id+"F55.opPattern","COPY",BODY,{"derivedFrom":makeQuery(id+"F3.opExtrude","SWEPT_BODY",BODY,{"disambiguationData":[OSD([sQuery(id+"F1.wireOp",EDGE,"E9.0.12.0")])]}),"instanceName":"29"});
            var Q334;
            Q334=makeQuery(id+"F55.opPattern","COPY",BODY,{"derivedFrom":makeQuery(id+"F3.opExtrude","SWEPT_BODY",BODY,{"disambiguationData":[OSD([sQuery(id+"F1.wireOp",EDGE,"E9.0.13.0")])]}),"instanceName":"29"});
            var Q335;
            Q335=makeQuery(id+"F55.opPattern","COPY",BODY,{"derivedFrom":makeQuery(id+"F3.opExtrude","SWEPT_BODY",BODY,{"disambiguationData":[OSD([sQuery(id+"F1.wireOp",EDGE,"E9.0.12.0")])]}),"instanceName":"30"});
            var Q336;
            Q336=makeQuery(id+"F55.opPattern","COPY",BODY,{"derivedFrom":makeQuery(id+"F3.opExtrude","SWEPT_BODY",BODY,{"disambiguationData":[OSD([sQuery(id+"F1.wireOp",EDGE,"E9.0.13.0")])]}),"instanceName":"30"});
            var Q337;
            Q337=makeQuery(id+"F55.opPattern","COPY",BODY,{"derivedFrom":makeQuery(id+"F3.opExtrude","SWEPT_BODY",BODY,{"disambiguationData":[OSD([sQuery(id+"F1.wireOp",EDGE,"E9.0.12.0")])]}),"instanceName":"31"});
            var Q338;
            Q338=makeQuery(id+"F55.opPattern","COPY",BODY,{"derivedFrom":makeQuery(id+"F3.opExtrude","SWEPT_BODY",BODY,{"disambiguationData":[OSD([sQuery(id+"F1.wireOp",EDGE,"E9.0.13.0")])]}),"instanceName":"31"});
            var Q339;
            Q339=makeQuery(id+"F55.opPattern","COPY",BODY,{"derivedFrom":makeQuery(id+"F3.opExtrude","SWEPT_BODY",BODY,{"disambiguationData":[OSD([sQuery(id+"F1.wireOp",EDGE,"E9.0.12.0")])]}),"instanceName":"32"});
            var Q340;
            Q340=makeQuery(id+"F55.opPattern","COPY",BODY,{"derivedFrom":makeQuery(id+"F3.opExtrude","SWEPT_BODY",BODY,{"disambiguationData":[OSD([sQuery(id+"F1.wireOp",EDGE,"E9.0.13.0")])]}),"instanceName":"32"});
            var Q341;
            Q341=makeQuery(id+"F55.opPattern","COPY",BODY,{"derivedFrom":makeQuery(id+"F3.opExtrude","SWEPT_BODY",BODY,{"disambiguationData":[OSD([sQuery(id+"F1.wireOp",EDGE,"E9.0.12.0")])]}),"instanceName":"33"});
            var Q342;
            Q342=makeQuery(id+"F55.opPattern","COPY",BODY,{"derivedFrom":makeQuery(id+"F3.opExtrude","SWEPT_BODY",BODY,{"disambiguationData":[OSD([sQuery(id+"F1.wireOp",EDGE,"E9.0.13.0")])]}),"instanceName":"33"});
            var Q343;
            Q343=makeQuery(id+"F55.opPattern","COPY",BODY,{"derivedFrom":makeQuery(id+"F3.opExtrude","SWEPT_BODY",BODY,{"disambiguationData":[OSD([sQuery(id+"F1.wireOp",EDGE,"E9.0.12.0")])]}),"instanceName":"34"});
            var Q344;
            Q344=makeQuery(id+"F55.opPattern","COPY",BODY,{"derivedFrom":makeQuery(id+"F3.opExtrude","SWEPT_BODY",BODY,{"disambiguationData":[OSD([sQuery(id+"F1.wireOp",EDGE,"E9.0.13.0")])]}),"instanceName":"34"});
            var Q345;
            Q345=makeQuery(id+"F55.opPattern","COPY",BODY,{"derivedFrom":makeQuery(id+"F3.opExtrude","SWEPT_BODY",BODY,{"disambiguationData":[OSD([sQuery(id+"F1.wireOp",EDGE,"E9.0.12.0")])]}),"instanceName":"35"});
            var Q346;
            Q346=makeQuery(id+"F55.opPattern","COPY",BODY,{"derivedFrom":makeQuery(id+"F3.opExtrude","SWEPT_BODY",BODY,{"disambiguationData":[OSD([sQuery(id+"F1.wireOp",EDGE,"E9.0.13.0")])]}),"instanceName":"35"});
            var Q347;
            Q347=makeQuery(id+"F55.opPattern","COPY",BODY,{"derivedFrom":makeQuery(id+"F3.opExtrude","SWEPT_BODY",BODY,{"disambiguationData":[OSD([sQuery(id+"F1.wireOp",EDGE,"E9.0.12.0")])]}),"instanceName":"36"});
            var Q348;
            Q348=makeQuery(id+"F55.opPattern","COPY",BODY,{"derivedFrom":makeQuery(id+"F3.opExtrude","SWEPT_BODY",BODY,{"disambiguationData":[OSD([sQuery(id+"F1.wireOp",EDGE,"E9.0.13.0")])]}),"instanceName":"36"});
            var Q349;
            Q349=makeQuery(id+"F55.opPattern","COPY",BODY,{"derivedFrom":makeQuery(id+"F3.opExtrude","SWEPT_BODY",BODY,{"disambiguationData":[OSD([sQuery(id+"F1.wireOp",EDGE,"E9.0.12.0")])]}),"instanceName":"37"});
            var Q350;
            Q350=makeQuery(id+"F55.opPattern","COPY",BODY,{"derivedFrom":makeQuery(id+"F3.opExtrude","SWEPT_BODY",BODY,{"disambiguationData":[OSD([sQuery(id+"F1.wireOp",EDGE,"E9.0.13.0")])]}),"instanceName":"37"});
            var Q351;
            Q351=makeQuery(id+"F55.opPattern","COPY",BODY,{"derivedFrom":makeQuery(id+"F3.opExtrude","SWEPT_BODY",BODY,{"disambiguationData":[OSD([sQuery(id+"F1.wireOp",EDGE,"E9.0.12.0")])]}),"instanceName":"38"});
            var Q352;
            Q352=makeQuery(id+"F55.opPattern","COPY",BODY,{"derivedFrom":makeQuery(id+"F3.opExtrude","SWEPT_BODY",BODY,{"disambiguationData":[OSD([sQuery(id+"F1.wireOp",EDGE,"E9.0.13.0")])]}),"instanceName":"38"});
            var Q353;
            Q353=makeQuery(id+"F55.opPattern","COPY",BODY,{"derivedFrom":makeQuery(id+"F3.opExtrude","SWEPT_BODY",BODY,{"disambiguationData":[OSD([sQuery(id+"F1.wireOp",EDGE,"E9.0.12.0")])]}),"instanceName":"39"});
            var Q354;
            Q354=makeQuery(id+"F55.opPattern","COPY",BODY,{"derivedFrom":makeQuery(id+"F3.opExtrude","SWEPT_BODY",BODY,{"disambiguationData":[OSD([sQuery(id+"F1.wireOp",EDGE,"E9.0.13.0")])]}),"instanceName":"39"});
            var Q355;
            Q355=makeQuery(id+"F55.opPattern","COPY",BODY,{"derivedFrom":makeQuery(id+"F3.opExtrude","SWEPT_BODY",BODY,{"disambiguationData":[OSD([sQuery(id+"F1.wireOp",EDGE,"E9.0.12.0")])]}),"instanceName":"40"});
            var Q356;
            Q356=makeQuery(id+"F55.opPattern","COPY",BODY,{"derivedFrom":makeQuery(id+"F3.opExtrude","SWEPT_BODY",BODY,{"disambiguationData":[OSD([sQuery(id+"F1.wireOp",EDGE,"E9.0.13.0")])]}),"instanceName":"40"});
            var Q357;
            Q357=makeQuery(id+"F55.opPattern","COPY",BODY,{"derivedFrom":makeQuery(id+"F3.opExtrude","SWEPT_BODY",BODY,{"disambiguationData":[OSD([sQuery(id+"F1.wireOp",EDGE,"E9.0.12.0")])]}),"instanceName":"41"});
            var Q358;
            Q358=makeQuery(id+"F55.opPattern","COPY",BODY,{"derivedFrom":makeQuery(id+"F3.opExtrude","SWEPT_BODY",BODY,{"disambiguationData":[OSD([sQuery(id+"F1.wireOp",EDGE,"E9.0.13.0")])]}),"instanceName":"41"});
            var Q359;
            Q359=makeQuery(id+"F55.opPattern","COPY",BODY,{"derivedFrom":makeQuery(id+"F3.opExtrude","SWEPT_BODY",BODY,{"disambiguationData":[OSD([sQuery(id+"F1.wireOp",EDGE,"E9.0.12.0")])]}),"instanceName":"42"});
            var Q360;
            Q360=makeQuery(id+"F55.opPattern","COPY",BODY,{"derivedFrom":makeQuery(id+"F3.opExtrude","SWEPT_BODY",BODY,{"disambiguationData":[OSD([sQuery(id+"F1.wireOp",EDGE,"E9.0.13.0")])]}),"instanceName":"42"});
            var Q361;
            Q361=makeQuery(id+"F55.opPattern","COPY",BODY,{"derivedFrom":makeQuery(id+"F3.opExtrude","SWEPT_BODY",BODY,{"disambiguationData":[OSD([sQuery(id+"F1.wireOp",EDGE,"E9.0.12.0")])]}),"instanceName":"44"});
            var Q362;
            Q362=makeQuery(id+"F55.opPattern","COPY",BODY,{"derivedFrom":makeQuery(id+"F3.opExtrude","SWEPT_BODY",BODY,{"disambiguationData":[OSD([sQuery(id+"F1.wireOp",EDGE,"E9.0.13.0")])]}),"instanceName":"44"});
            var Q363;
            Q363=makeQuery(id+"F55.opPattern","COPY",BODY,{"derivedFrom":makeQuery(id+"F3.opExtrude","SWEPT_BODY",BODY,{"disambiguationData":[OSD([sQuery(id+"F1.wireOp",EDGE,"E9.0.12.0")])]}),"instanceName":"46"});
            var Q364;
            Q364=makeQuery(id+"F55.opPattern","COPY",BODY,{"derivedFrom":makeQuery(id+"F3.opExtrude","SWEPT_BODY",BODY,{"disambiguationData":[OSD([sQuery(id+"F1.wireOp",EDGE,"E9.0.13.0")])]}),"instanceName":"46"});
            var Q365;
            Q365=makeQuery(id+"F3.opExtrude","SWEPT_BODY",BODY,{"disambiguationData":[OSD([sQuery(id+"F1.wireOp",EDGE,"E9.0.16.0")])]});
            var Q366;
            Q366=makeQuery(id+"F53.opPattern","COPY",BODY,{"derivedFrom":makeQuery(id+"F3.opExtrude","SWEPT_BODY",BODY,{"disambiguationData":[OSD([sQuery(id+"F1.wireOp",EDGE,"E9.0.16.0")])]}),"instanceName":"4"});
            var Q367;
            Q367=makeQuery(id+"F53.opPattern","COPY",BODY,{"derivedFrom":makeQuery(id+"F3.opExtrude","SWEPT_BODY",BODY,{"disambiguationData":[OSD([sQuery(id+"F1.wireOp",EDGE,"E9.0.15.0")])]}),"instanceName":"4"});
            var Q368;
            Q368=makeQuery(id+"F52.opPattern","COPY",BODY,{"derivedFrom":makeQuery(id+"F3.opExtrude","SWEPT_BODY",BODY,{"disambiguationData":[OSD([sQuery(id+"F1.wireOp",EDGE,"E9.0.17.0")])]}),"instanceName":"2"});
            var Q369;
            Q369=makeQuery(id+"F53.opPattern","COPY",BODY,{"derivedFrom":makeQuery(id+"F3.opExtrude","SWEPT_BODY",BODY,{"disambiguationData":[OSD([sQuery(id+"F1.wireOp",EDGE,"E9.0.16.0")])]}),"instanceName":"2"});
            var Q370;
            Q370=makeQuery(id+"F54.opPattern","COPY",BODY,{"derivedFrom":makeQuery(id+"F3.opExtrude","SWEPT_BODY",BODY,{"disambiguationData":[OSD([sQuery(id+"F1.wireOp",EDGE,"E9.0.14.0")])]}),"instanceName":"4"});
            var Q371;
            Q371=makeQuery(id+"F54.opPattern","COPY",BODY,{"derivedFrom":makeQuery(id+"F3.opExtrude","SWEPT_BODY",BODY,{"disambiguationData":[OSD([sQuery(id+"F1.wireOp",EDGE,"E9.0.14.0")])]}),"instanceName":"2"});
            var Q372;
            Q372=makeQuery(id+"F55.opPattern","COPY",BODY,{"derivedFrom":makeQuery(id+"F3.opExtrude","SWEPT_BODY",BODY,{"disambiguationData":[OSD([sQuery(id+"F1.wireOp",EDGE,"E9.0.12.0")])]}),"instanceName":"2"});
            var Q373;
            Q373=makeQuery(id+"F55.opPattern","COPY",BODY,{"derivedFrom":makeQuery(id+"F3.opExtrude","SWEPT_BODY",BODY,{"disambiguationData":[OSD([sQuery(id+"F1.wireOp",EDGE,"E9.0.13.0")])]}),"instanceName":"2"});
            var Q374;
            Q374=makeQuery(id+"F53.opPattern","COPY",BODY,{"derivedFrom":makeQuery(id+"F3.opExtrude","SWEPT_BODY",BODY,{"disambiguationData":[OSD([sQuery(id+"F1.wireOp",EDGE,"E9.0.16.0")])]}),"instanceName":"45"});
            var Q375;
            Q375=makeQuery(id+"F53.opPattern","COPY",BODY,{"derivedFrom":makeQuery(id+"F3.opExtrude","SWEPT_BODY",BODY,{"disambiguationData":[OSD([sQuery(id+"F1.wireOp",EDGE,"E9.0.15.0")])]}),"instanceName":"45"});
            var Q376;
            Q376=makeQuery(id+"F55.opPattern","COPY",BODY,{"derivedFrom":makeQuery(id+"F3.opExtrude","SWEPT_BODY",BODY,{"disambiguationData":[OSD([sQuery(id+"F1.wireOp",EDGE,"E9.0.12.0")])]}),"instanceName":"4"});
            var Q377;
            Q377=makeQuery(id+"F51.opPattern","COPY",BODY,{"derivedFrom":makeQuery(id+"F3.opExtrude","SWEPT_BODY",BODY,{"disambiguationData":[OSD([sQuery(id+"F1.wireOp",EDGE,"E9.0.19.0")])]}),"instanceName":"41"});
            var Q378;
            Q378=makeQuery(id+"F55.opPattern","COPY",BODY,{"derivedFrom":makeQuery(id+"F3.opExtrude","SWEPT_BODY",BODY,{"disambiguationData":[OSD([sQuery(id+"F1.wireOp",EDGE,"E9.0.13.0")])]}),"instanceName":"4"});
            var Q379;
            Q379=makeQuery(id+"F3.opExtrude","SWEPT_BODY",BODY,{"disambiguationData":[OSD([sQuery(id+"F1.wireOp",EDGE,"E9.0.15.0")])]});
            var Q380;
            Q380=makeQuery(id+"F53.opPattern","COPY",BODY,{"derivedFrom":makeQuery(id+"F3.opExtrude","SWEPT_BODY",BODY,{"disambiguationData":[OSD([sQuery(id+"F1.wireOp",EDGE,"E9.0.16.0")])]}),"instanceName":"43"});
            var Q381;
            Q381=makeQuery(id+"F53.opPattern","COPY",BODY,{"derivedFrom":makeQuery(id+"F3.opExtrude","SWEPT_BODY",BODY,{"disambiguationData":[OSD([sQuery(id+"F1.wireOp",EDGE,"E9.0.15.0")])]}),"instanceName":"43"});
            var Q382;
            Q382=makeQuery(id+"F3.opExtrude","SWEPT_BODY",BODY,{"disambiguationData":[OSD([sQuery(id+"F1.wireOp",EDGE,"E9.0.14.0")])]});
            var Q383;
            Q383=makeQuery(id+"F50.opPattern","COPY",BODY,{"derivedFrom":makeQuery(id+"F3.opExtrude","SWEPT_BODY",BODY,{"disambiguationData":[OSD([sQuery(id+"F1.wireOp",EDGE,"E9.0.20.0")])]}),"instanceName":"40"});
            var Q384;
            Q384=makeQuery(id+"F50.opPattern","COPY",BODY,{"derivedFrom":makeQuery(id+"F3.opExtrude","SWEPT_BODY",BODY,{"disambiguationData":[OSD([sQuery(id+"F1.wireOp",EDGE,"E9.0.20.0")])]}),"instanceName":"42"});
            var Q385;
            Q385=makeQuery(id+"F51.opPattern","COPY",BODY,{"derivedFrom":makeQuery(id+"F3.opExtrude","SWEPT_BODY",BODY,{"disambiguationData":[OSD([sQuery(id+"F1.wireOp",EDGE,"E9.0.19.0")])]}),"instanceName":"43"});
            var Q386;
            Q386=makeQuery(id+"F51.opPattern","COPY",BODY,{"derivedFrom":makeQuery(id+"F3.opExtrude","SWEPT_BODY",BODY,{"disambiguationData":[OSD([sQuery(id+"F1.wireOp",EDGE,"E9.0.18.0")])]}),"instanceName":"2"});
            var Q387;
            Q387=makeQuery(id+"F53.opPattern","COPY",BODY,{"derivedFrom":makeQuery(id+"F3.opExtrude","SWEPT_BODY",BODY,{"disambiguationData":[OSD([sQuery(id+"F1.wireOp",EDGE,"E9.0.16.0")])]}),"instanceName":"41"});
            var Q388;
            Q388=makeQuery(id+"F3.opExtrude","SWEPT_BODY",BODY,{"disambiguationData":[OSD([sQuery(id+"F1.wireOp",EDGE,"E9.0.13.0")])]});
            var Q389;
            Q389=makeQuery(id+"F51.opPattern","COPY",BODY,{"derivedFrom":makeQuery(id+"F3.opExtrude","SWEPT_BODY",BODY,{"disambiguationData":[OSD([sQuery(id+"F1.wireOp",EDGE,"E9.0.19.0")])]}),"instanceName":"2"});
            var Q390;
            Q390=makeQuery(id+"F52.opPattern","COPY",BODY,{"derivedFrom":makeQuery(id+"F3.opExtrude","SWEPT_BODY",BODY,{"disambiguationData":[OSD([sQuery(id+"F1.wireOp",EDGE,"E9.0.17.0")])]}),"instanceName":"42"});
            var Q391;
            Q391=makeQuery(id+"F51.opPattern","COPY",BODY,{"derivedFrom":makeQuery(id+"F3.opExtrude","SWEPT_BODY",BODY,{"disambiguationData":[OSD([sQuery(id+"F1.wireOp",EDGE,"E9.0.18.0")])]}),"instanceName":"43"});
            var Q392;
            Q392=makeQuery(id+"F53.opPattern","COPY",BODY,{"derivedFrom":makeQuery(id+"F3.opExtrude","SWEPT_BODY",BODY,{"disambiguationData":[OSD([sQuery(id+"F1.wireOp",EDGE,"E9.0.15.0")])]}),"instanceName":"41"});
            var Q393;
            Q393=makeQuery(id+"F51.opPattern","COPY",BODY,{"derivedFrom":makeQuery(id+"F3.opExtrude","SWEPT_BODY",BODY,{"disambiguationData":[OSD([sQuery(id+"F1.wireOp",EDGE,"E9.0.18.0")])]}),"instanceName":"41"});
            var Q394;
            Q394=makeQuery(id+"F54.opPattern","COPY",BODY,{"derivedFrom":makeQuery(id+"F3.opExtrude","SWEPT_BODY",BODY,{"disambiguationData":[OSD([sQuery(id+"F1.wireOp",EDGE,"E9.0.14.0")])]}),"instanceName":"42"});
            var Q395;
            Q395=makeQuery(id+"F54.opPattern","COPY",BODY,{"derivedFrom":makeQuery(id+"F3.opExtrude","SWEPT_BODY",BODY,{"disambiguationData":[OSD([sQuery(id+"F1.wireOp",EDGE,"E9.0.14.0")])]}),"instanceName":"44"});
            var Q396;
            Q396=makeQuery(id+"F54.opPattern","COPY",BODY,{"derivedFrom":makeQuery(id+"F3.opExtrude","SWEPT_BODY",BODY,{"disambiguationData":[OSD([sQuery(id+"F1.wireOp",EDGE,"E9.0.14.0")])]}),"instanceName":"45"});
            var Q397;
            Q397=makeQuery(id+"F53.opPattern","COPY",BODY,{"derivedFrom":makeQuery(id+"F3.opExtrude","SWEPT_BODY",BODY,{"disambiguationData":[OSD([sQuery(id+"F1.wireOp",EDGE,"E9.0.15.0")])]}),"instanceName":"2"});
            var Q398;
            Q398=makeQuery(id+"F3.opExtrude","SWEPT_BODY",BODY,{"disambiguationData":[OSD([sQuery(id+"F1.wireOp",EDGE,"E9.0.12.0")])]});
            var Q399;
            Q399=makeQuery(id+"F52.opPattern","COPY",BODY,{"derivedFrom":makeQuery(id+"F3.opExtrude","SWEPT_BODY",BODY,{"disambiguationData":[OSD([sQuery(id+"F1.wireOp",EDGE,"E9.0.17.0")])]}),"instanceName":"44"});
            var Q400;
            Q400=makeQuery(id+"F50.opPattern","COPY",BODY,{"derivedFrom":makeQuery(id+"F3.opExtrude","SWEPT_BODY",BODY,{"disambiguationData":[OSD([sQuery(id+"F1.wireOp",EDGE,"E9.0.20.0")])]}),"instanceName":"2"});
            var Q401;
            Q401=makeQuery(id+"F3.opExtrude","SWEPT_BODY",BODY,{"disambiguationData":[OSD([sQuery(id+"F1.wireOp",EDGE,"E9.0.20.0")])]});
            var Q402;
            Q402=makeQuery(id+"F3.opExtrude","SWEPT_BODY",BODY,{"disambiguationData":[OSD([sQuery(id+"F1.wireOp",EDGE,"E9.0.19.0")])]});
            var Q403;
            Q403=makeQuery(id+"F3.opExtrude","SWEPT_BODY",BODY,{"disambiguationData":[OSD([sQuery(id+"F1.wireOp",EDGE,"E9.0.18.0")])]});
            var Q404;
            Q404=makeQuery(id+"F3.opExtrude","SWEPT_BODY",BODY,{"disambiguationData":[OSD([sQuery(id+"F1.wireOp",EDGE,"E9.0.17.0")])]});
            var Q405;
            Q405=makeQuery(id+"F55.opPattern","COPY",BODY,{"derivedFrom":makeQuery(id+"F3.opExtrude","SWEPT_BODY",BODY,{"disambiguationData":[OSD([sQuery(id+"F1.wireOp",EDGE,"E9.0.12.0")])]}),"instanceName":"43"});
            var Q406;
            Q406=makeQuery(id+"F55.opPattern","COPY",BODY,{"derivedFrom":makeQuery(id+"F3.opExtrude","SWEPT_BODY",BODY,{"disambiguationData":[OSD([sQuery(id+"F1.wireOp",EDGE,"E9.0.13.0")])]}),"instanceName":"43"});
            var Q407;
            Q407=makeQuery(id+"F55.opPattern","COPY",BODY,{"derivedFrom":makeQuery(id+"F3.opExtrude","SWEPT_BODY",BODY,{"disambiguationData":[OSD([sQuery(id+"F1.wireOp",EDGE,"E9.0.12.0")])]}),"instanceName":"45"});
            var Q408;
            Q408=makeQuery(id+"F55.opPattern","COPY",BODY,{"derivedFrom":makeQuery(id+"F3.opExtrude","SWEPT_BODY",BODY,{"disambiguationData":[OSD([sQuery(id+"F1.wireOp",EDGE,"E9.0.13.0")])]}),"instanceName":"45"});
            var Q409;
            Q409=makeQuery(id+"F55.opPattern","COPY",BODY,{"derivedFrom":makeQuery(id+"F3.opExtrude","SWEPT_BODY",BODY,{"disambiguationData":[OSD([sQuery(id+"F1.wireOp",EDGE,"E9.0.12.0")])]}),"instanceName":"47"});
            var Q410;
            Q410=makeQuery(id+"F55.opPattern","COPY",BODY,{"derivedFrom":makeQuery(id+"F3.opExtrude","SWEPT_BODY",BODY,{"disambiguationData":[OSD([sQuery(id+"F1.wireOp",EDGE,"E9.0.13.0")])]}),"instanceName":"47"});
            var Q411;
            Q411=makeQuery(id+"F2.opRevolve","SWEPT_BODY",BODY,{"disambiguationData":[OSD([sQuery(id+"F0.wireOp",EDGE,"E0"),sQuery(id+"F0.wireOp",EDGE,"E1"),sQuery(id+"F0.wireOp",EDGE,"E2"),sQuery(id+"F0.wireOp",EDGE,"E3"),sQuery(id+"F0.wireOp",EDGE,"E6")])]});
            booleanBodies(context, id + "F56", {"operationType" : BooleanOperationType.SUBTRACTION, "tools" : qUnion([Q0, Q1, Q2, Q3, Q4, Q5, Q6, Q7, Q8, Q9, Q10, Q11, Q12, Q13, Q14, Q15, Q16, Q17, Q18, Q19, Q20, Q21, Q22, Q23, Q24, Q25, Q26, Q27, Q28, Q29, Q30, Q31, Q32, Q33, Q34, Q35, Q36, Q37, Q38, Q39, Q40, Q41, Q42, Q43, Q44, Q45, Q46, Q47, Q48, Q49, Q50, Q51, Q52, Q53, Q54, Q55, Q56, Q57, Q58, Q59, Q60, Q61, Q62, Q63, Q64, Q65, Q66, Q67, Q68, Q69, Q70, Q71, Q72, Q73, Q74, Q75, Q76, Q77, Q78, Q79, Q80, Q81, Q82, Q83, Q84, Q85, Q86, Q87, Q88, Q89, Q90, Q91, Q92, Q93, Q94, Q95, Q96, Q97, Q98, Q99, Q100, Q101, Q102, Q103, Q104, Q105, Q106, Q107, Q108, Q109, Q110, Q111, Q112, Q113, Q114, Q115, Q116, Q117, Q118, Q119, Q120, Q121, Q122, Q123, Q124, Q125, Q126, Q127, Q128, Q129, Q130, Q131, Q132, Q133, Q134, Q135, Q136, Q137, Q138, Q139, Q140, Q141, Q142, Q143, Q144, Q145, Q146, Q147, Q148, Q149, Q150, Q151, Q152, Q153, Q154, Q155, Q156, Q157, Q158, Q159, Q160, Q161, Q162, Q163, Q164, Q165, Q166, Q167, Q168, Q169, Q170, Q171, Q172, Q173, Q174, Q175, Q176, Q177, Q178, Q179, Q180, Q181, Q182, Q183, Q184, Q185, Q186, Q187, Q188, Q189, Q190, Q191, Q192, Q193, Q194, Q195, Q196, Q197, Q198, Q199, Q200, Q201, Q202, Q203, Q204, Q205, Q206, Q207, Q208, Q209, Q210, Q211, Q212, Q213, Q214, Q215, Q216, Q217, Q218, Q219, Q220, Q221, Q222, Q223, Q224, Q225, Q226, Q227, Q228, Q229, Q230, Q231, Q232, Q233, Q234, Q235, Q236, Q237, Q238, Q239, Q240, Q241, Q242, Q243, Q244, Q245, Q246, Q247, Q248, Q249, Q250, Q251, Q252, Q253, Q254, Q255, Q256, Q257, Q258, Q259, Q260, Q261, Q262, Q263, Q264, Q265, Q266, Q267, Q268, Q269, Q270, Q271, Q272, Q273, Q274, Q275, Q276, Q277, Q278, Q279, Q280, Q281, Q282, Q283, Q284, Q285, Q286, Q287, Q288, Q289, Q290, Q291, Q292, Q293, Q294, Q295, Q296, Q297, Q298, Q299, Q300, Q301, Q302, Q303, Q304, Q305, Q306, Q307, Q308, Q309, Q310, Q311, Q312, Q313, Q314, Q315, Q316, Q317, Q318, Q319, Q320, Q321, Q322, Q323, Q324, Q325, Q326, Q327, Q328, Q329, Q330, Q331, Q332, Q333, Q334, Q335, Q336, Q337, Q338, Q339, Q340, Q341, Q342, Q343, Q344, Q345, Q346, Q347, Q348, Q349, Q350, Q351, Q352, Q353, Q354, Q355, Q356, Q357, Q358, Q359, Q360, Q361, Q362, Q363, Q364, Q365, Q366, Q367, Q368, Q369, Q370, Q371, Q372, Q373, Q374, Q375, Q376, Q377, Q378, Q379, Q380, Q381, Q382, Q383, Q384, Q385, Q386, Q387, Q388, Q389, Q390, Q391, Q392, Q393, Q394, Q395, Q396, Q397, Q398, Q399, Q400, Q401, Q402, Q403, Q404, Q405, Q406, Q407, Q408, Q409, Q410]), "targets" : qUnion([Q411])});
        }
        {
            var Q0;
            Q0=makeQuery(id+"F3.opExtrude","SWEPT_BODY",BODY,{"disambiguationData":[OSD([sQuery(id+"F1.wireOp",EDGE,"E9.0.11.0")])]});
            var Q1;
            Q1=makeQuery(id+"F2.opRevolve","SWEPT_FACE",FACE,{"disambiguationData":[OSD([sQuery(id+"F0.wireOp",EDGE,"E1")])]});
            circularPattern(context, id + "F57", {"entities" : qUnion([Q0]), "axis" : qUnion([Q1]), "angle" : 180 * degree, "instanceCount" : 49, "oppositeDirection" : true, "equalSpace" : true});
        }
        {
            var Q0;
            Q0=makeQuery(id+"F3.opExtrude","SWEPT_BODY",BODY,{"disambiguationData":[OSD([sQuery(id+"F1.wireOp",EDGE,"E9.0.10.0")])]});
            var Q1;
            Q1=makeQuery(id+"F3.opExtrude","SWEPT_BODY",BODY,{"disambiguationData":[OSD([sQuery(id+"F1.wireOp",EDGE,"E9.0.9.0")])]});
            var Q2;
            Q2=makeQuery(id+"F2.opRevolve","SWEPT_FACE",FACE,{"disambiguationData":[OSD([sQuery(id+"F0.wireOp",EDGE,"E1")])]});
            circularPattern(context, id + "F58", {"entities" : qUnion([Q0, Q1]), "axis" : qUnion([Q2]), "angle" : 180 * degree, "instanceCount" : 50, "oppositeDirection" : true, "equalSpace" : true});
        }
        {
            var Q0;
            Q0=makeQuery(id+"F3.opExtrude","SWEPT_BODY",BODY,{"disambiguationData":[OSD([sQuery(id+"F1.wireOp",EDGE,"E9.0.8.0")])]});
            var Q1;
            Q1=makeQuery(id+"F2.opRevolve","SWEPT_FACE",FACE,{"disambiguationData":[OSD([sQuery(id+"F0.wireOp",EDGE,"E1")])]});
            circularPattern(context, id + "F59", {"entities" : qUnion([Q0]), "axis" : qUnion([Q1]), "angle" : 180 * degree, "instanceCount" : 51, "oppositeDirection" : true, "equalSpace" : true});
        }
        {
            var Q0;
            Q0=makeQuery(id+"F3.opExtrude","SWEPT_BODY",BODY,{"disambiguationData":[OSD([sQuery(id+"F1.wireOp",EDGE,"E9.0.7.0")])]});
            var Q1;
            Q1=makeQuery(id+"F3.opExtrude","SWEPT_BODY",BODY,{"disambiguationData":[OSD([sQuery(id+"F1.wireOp",EDGE,"E9.0.6.0")])]});
            var Q2;
            Q2=makeQuery(id+"F2.opRevolve","SWEPT_FACE",FACE,{"disambiguationData":[OSD([sQuery(id+"F0.wireOp",EDGE,"E1")])]});
            circularPattern(context, id + "F60", {"entities" : qUnion([Q0, Q1]), "axis" : qUnion([Q2]), "angle" : 180 * degree, "instanceCount" : 52, "oppositeDirection" : true, "equalSpace" : true});
        }
        {
            var Q0;
            Q0=makeQuery(id+"F3.opExtrude","SWEPT_BODY",BODY,{"disambiguationData":[OSD([sQuery(id+"F1.wireOp",EDGE,"E9.0.5.0")])]});
            var Q1;
            Q1=makeQuery(id+"F3.opExtrude","SWEPT_BODY",BODY,{"disambiguationData":[OSD([sQuery(id+"F1.wireOp",EDGE,"E9.0.4.0")])]});
            var Q2;
            Q2=makeQuery(id+"F2.opRevolve","SWEPT_FACE",FACE,{"disambiguationData":[OSD([sQuery(id+"F0.wireOp",EDGE,"E1")])]});
            circularPattern(context, id + "F61", {"entities" : qUnion([Q0, Q1]), "axis" : qUnion([Q2]), "angle" : 180 * degree, "instanceCount" : 53, "oppositeDirection" : true, "equalSpace" : true});
        }
        {
            var Q0;
            Q0=makeQuery(id+"F60.opPattern","COPY",BODY,{"derivedFrom":makeQuery(id+"F3.opExtrude","SWEPT_BODY",BODY,{"disambiguationData":[OSD([sQuery(id+"F1.wireOp",EDGE,"E9.0.7.0")])]}),"instanceName":"38"});
            var Q1;
            Q1=makeQuery(id+"F58.opPattern","COPY",BODY,{"derivedFrom":makeQuery(id+"F3.opExtrude","SWEPT_BODY",BODY,{"disambiguationData":[OSD([sQuery(id+"F1.wireOp",EDGE,"E9.0.10.0")])]}),"instanceName":"44"});
            var Q2;
            Q2=makeQuery(id+"F60.opPattern","COPY",BODY,{"derivedFrom":makeQuery(id+"F3.opExtrude","SWEPT_BODY",BODY,{"disambiguationData":[OSD([sQuery(id+"F1.wireOp",EDGE,"E9.0.6.0")])]}),"instanceName":"13"});
            var Q3;
            Q3=makeQuery(id+"F58.opPattern","COPY",BODY,{"derivedFrom":makeQuery(id+"F3.opExtrude","SWEPT_BODY",BODY,{"disambiguationData":[OSD([sQuery(id+"F1.wireOp",EDGE,"E9.0.10.0")])]}),"instanceName":"9"});
            var Q4;
            Q4=makeQuery(id+"F58.opPattern","COPY",BODY,{"derivedFrom":makeQuery(id+"F3.opExtrude","SWEPT_BODY",BODY,{"disambiguationData":[OSD([sQuery(id+"F1.wireOp",EDGE,"E9.0.9.0")])]}),"instanceName":"44"});
            var Q5;
            Q5=makeQuery(id+"F61.opPattern","COPY",BODY,{"derivedFrom":makeQuery(id+"F3.opExtrude","SWEPT_BODY",BODY,{"disambiguationData":[OSD([sQuery(id+"F1.wireOp",EDGE,"E9.0.5.0")])]}),"instanceName":"20"});
            var Q6;
            Q6=makeQuery(id+"F60.opPattern","COPY",BODY,{"derivedFrom":makeQuery(id+"F3.opExtrude","SWEPT_BODY",BODY,{"disambiguationData":[OSD([sQuery(id+"F1.wireOp",EDGE,"E9.0.7.0")])]}),"instanceName":"13"});
            var Q7;
            Q7=makeQuery(id+"F60.opPattern","COPY",BODY,{"derivedFrom":makeQuery(id+"F3.opExtrude","SWEPT_BODY",BODY,{"disambiguationData":[OSD([sQuery(id+"F1.wireOp",EDGE,"E9.0.6.0")])]}),"instanceName":"14"});
            var Q8;
            Q8=makeQuery(id+"F58.opPattern","COPY",BODY,{"derivedFrom":makeQuery(id+"F3.opExtrude","SWEPT_BODY",BODY,{"disambiguationData":[OSD([sQuery(id+"F1.wireOp",EDGE,"E9.0.10.0")])]}),"instanceName":"43"});
            var Q9;
            Q9=makeQuery(id+"F61.opPattern","COPY",BODY,{"derivedFrom":makeQuery(id+"F3.opExtrude","SWEPT_BODY",BODY,{"disambiguationData":[OSD([sQuery(id+"F1.wireOp",EDGE,"E9.0.4.0")])]}),"instanceName":"20"});
            var Q10;
            Q10=makeQuery(id+"F60.opPattern","COPY",BODY,{"derivedFrom":makeQuery(id+"F3.opExtrude","SWEPT_BODY",BODY,{"disambiguationData":[OSD([sQuery(id+"F1.wireOp",EDGE,"E9.0.7.0")])]}),"instanceName":"14"});
            var Q11;
            Q11=makeQuery(id+"F60.opPattern","COPY",BODY,{"derivedFrom":makeQuery(id+"F3.opExtrude","SWEPT_BODY",BODY,{"disambiguationData":[OSD([sQuery(id+"F1.wireOp",EDGE,"E9.0.7.0")])]}),"instanceName":"12"});
            var Q12;
            Q12=makeQuery(id+"F59.opPattern","COPY",BODY,{"derivedFrom":makeQuery(id+"F3.opExtrude","SWEPT_BODY",BODY,{"disambiguationData":[OSD([sQuery(id+"F1.wireOp",EDGE,"E9.0.8.0")])]}),"instanceName":"20"});
            var Q13;
            Q13=makeQuery(id+"F60.opPattern","COPY",BODY,{"derivedFrom":makeQuery(id+"F3.opExtrude","SWEPT_BODY",BODY,{"disambiguationData":[OSD([sQuery(id+"F1.wireOp",EDGE,"E9.0.6.0")])]}),"instanceName":"39"});
            var Q14;
            Q14=makeQuery(id+"F58.opPattern","COPY",BODY,{"derivedFrom":makeQuery(id+"F3.opExtrude","SWEPT_BODY",BODY,{"disambiguationData":[OSD([sQuery(id+"F1.wireOp",EDGE,"E9.0.9.0")])]}),"instanceName":"18"});
            var Q15;
            Q15=makeQuery(id+"F58.opPattern","COPY",BODY,{"derivedFrom":makeQuery(id+"F3.opExtrude","SWEPT_BODY",BODY,{"disambiguationData":[OSD([sQuery(id+"F1.wireOp",EDGE,"E9.0.10.0")])]}),"instanceName":"14"});
            var Q16;
            Q16=makeQuery(id+"F60.opPattern","COPY",BODY,{"derivedFrom":makeQuery(id+"F3.opExtrude","SWEPT_BODY",BODY,{"disambiguationData":[OSD([sQuery(id+"F1.wireOp",EDGE,"E9.0.7.0")])]}),"instanceName":"37"});
            var Q17;
            Q17=makeQuery(id+"F61.opPattern","COPY",BODY,{"derivedFrom":makeQuery(id+"F3.opExtrude","SWEPT_BODY",BODY,{"disambiguationData":[OSD([sQuery(id+"F1.wireOp",EDGE,"E9.0.5.0")])]}),"instanceName":"19"});
            var Q18;
            Q18=makeQuery(id+"F60.opPattern","COPY",BODY,{"derivedFrom":makeQuery(id+"F3.opExtrude","SWEPT_BODY",BODY,{"disambiguationData":[OSD([sQuery(id+"F1.wireOp",EDGE,"E9.0.6.0")])]}),"instanceName":"12"});
            var Q19;
            Q19=makeQuery(id+"F58.opPattern","COPY",BODY,{"derivedFrom":makeQuery(id+"F3.opExtrude","SWEPT_BODY",BODY,{"disambiguationData":[OSD([sQuery(id+"F1.wireOp",EDGE,"E9.0.9.0")])]}),"instanceName":"14"});
            var Q20;
            Q20=makeQuery(id+"F58.opPattern","COPY",BODY,{"derivedFrom":makeQuery(id+"F3.opExtrude","SWEPT_BODY",BODY,{"disambiguationData":[OSD([sQuery(id+"F1.wireOp",EDGE,"E9.0.9.0")])]}),"instanceName":"10"});
            var Q21;
            Q21=makeQuery(id+"F60.opPattern","COPY",BODY,{"derivedFrom":makeQuery(id+"F3.opExtrude","SWEPT_BODY",BODY,{"disambiguationData":[OSD([sQuery(id+"F1.wireOp",EDGE,"E9.0.6.0")])]}),"instanceName":"37"});
            var Q22;
            Q22=makeQuery(id+"F60.opPattern","COPY",BODY,{"derivedFrom":makeQuery(id+"F3.opExtrude","SWEPT_BODY",BODY,{"disambiguationData":[OSD([sQuery(id+"F1.wireOp",EDGE,"E9.0.6.0")])]}),"instanceName":"38"});
            var Q23;
            Q23=makeQuery(id+"F58.opPattern","COPY",BODY,{"derivedFrom":makeQuery(id+"F3.opExtrude","SWEPT_BODY",BODY,{"disambiguationData":[OSD([sQuery(id+"F1.wireOp",EDGE,"E9.0.10.0")])]}),"instanceName":"10"});
            var Q24;
            Q24=makeQuery(id+"F60.opPattern","COPY",BODY,{"derivedFrom":makeQuery(id+"F3.opExtrude","SWEPT_BODY",BODY,{"disambiguationData":[OSD([sQuery(id+"F1.wireOp",EDGE,"E9.0.7.0")])]}),"instanceName":"11"});
            var Q25;
            Q25=makeQuery(id+"F60.opPattern","COPY",BODY,{"derivedFrom":makeQuery(id+"F3.opExtrude","SWEPT_BODY",BODY,{"disambiguationData":[OSD([sQuery(id+"F1.wireOp",EDGE,"E9.0.6.0")])]}),"instanceName":"11"});
            var Q26;
            Q26=makeQuery(id+"F60.opPattern","COPY",BODY,{"derivedFrom":makeQuery(id+"F3.opExtrude","SWEPT_BODY",BODY,{"disambiguationData":[OSD([sQuery(id+"F1.wireOp",EDGE,"E9.0.7.0")])]}),"instanceName":"36"});
            var Q27;
            Q27=makeQuery(id+"F61.opPattern","COPY",BODY,{"derivedFrom":makeQuery(id+"F3.opExtrude","SWEPT_BODY",BODY,{"disambiguationData":[OSD([sQuery(id+"F1.wireOp",EDGE,"E9.0.4.0")])]}),"instanceName":"19"});
            var Q28;
            Q28=makeQuery(id+"F60.opPattern","COPY",BODY,{"derivedFrom":makeQuery(id+"F3.opExtrude","SWEPT_BODY",BODY,{"disambiguationData":[OSD([sQuery(id+"F1.wireOp",EDGE,"E9.0.6.0")])]}),"instanceName":"36"});
            var Q29;
            Q29=makeQuery(id+"F60.opPattern","COPY",BODY,{"derivedFrom":makeQuery(id+"F3.opExtrude","SWEPT_BODY",BODY,{"disambiguationData":[OSD([sQuery(id+"F1.wireOp",EDGE,"E9.0.7.0")])]}),"instanceName":"10"});
            var Q30;
            Q30=makeQuery(id+"F58.opPattern","COPY",BODY,{"derivedFrom":makeQuery(id+"F3.opExtrude","SWEPT_BODY",BODY,{"disambiguationData":[OSD([sQuery(id+"F1.wireOp",EDGE,"E9.0.9.0")])]}),"instanceName":"11"});
            var Q31;
            Q31=makeQuery(id+"F61.opPattern","COPY",BODY,{"derivedFrom":makeQuery(id+"F3.opExtrude","SWEPT_BODY",BODY,{"disambiguationData":[OSD([sQuery(id+"F1.wireOp",EDGE,"E9.0.5.0")])]}),"instanceName":"18"});
            var Q32;
            Q32=makeQuery(id+"F61.opPattern","COPY",BODY,{"derivedFrom":makeQuery(id+"F3.opExtrude","SWEPT_BODY",BODY,{"disambiguationData":[OSD([sQuery(id+"F1.wireOp",EDGE,"E9.0.4.0")])]}),"instanceName":"18"});
            var Q33;
            Q33=makeQuery(id+"F60.opPattern","COPY",BODY,{"derivedFrom":makeQuery(id+"F3.opExtrude","SWEPT_BODY",BODY,{"disambiguationData":[OSD([sQuery(id+"F1.wireOp",EDGE,"E9.0.6.0")])]}),"instanceName":"25"});
            var Q34;
            Q34=makeQuery(id+"F60.opPattern","COPY",BODY,{"derivedFrom":makeQuery(id+"F3.opExtrude","SWEPT_BODY",BODY,{"disambiguationData":[OSD([sQuery(id+"F1.wireOp",EDGE,"E9.0.7.0")])]}),"instanceName":"25"});
            var Q35;
            Q35=makeQuery(id+"F59.opPattern","COPY",BODY,{"derivedFrom":makeQuery(id+"F3.opExtrude","SWEPT_BODY",BODY,{"disambiguationData":[OSD([sQuery(id+"F1.wireOp",EDGE,"E9.0.8.0")])]}),"instanceName":"26"});
            var Q36;
            Q36=makeQuery(id+"F61.opPattern","COPY",BODY,{"derivedFrom":makeQuery(id+"F3.opExtrude","SWEPT_BODY",BODY,{"disambiguationData":[OSD([sQuery(id+"F1.wireOp",EDGE,"E9.0.4.0")])]}),"instanceName":"36"});
            var Q37;
            Q37=makeQuery(id+"F58.opPattern","COPY",BODY,{"derivedFrom":makeQuery(id+"F3.opExtrude","SWEPT_BODY",BODY,{"disambiguationData":[OSD([sQuery(id+"F1.wireOp",EDGE,"E9.0.9.0")])]}),"instanceName":"33"});
            var Q38;
            Q38=makeQuery(id+"F58.opPattern","COPY",BODY,{"derivedFrom":makeQuery(id+"F3.opExtrude","SWEPT_BODY",BODY,{"disambiguationData":[OSD([sQuery(id+"F1.wireOp",EDGE,"E9.0.9.0")])]}),"instanceName":"29"});
            var Q39;
            Q39=makeQuery(id+"F61.opPattern","COPY",BODY,{"derivedFrom":makeQuery(id+"F3.opExtrude","SWEPT_BODY",BODY,{"disambiguationData":[OSD([sQuery(id+"F1.wireOp",EDGE,"E9.0.5.0")])]}),"instanceName":"17"});
            var Q40;
            Q40=makeQuery(id+"F60.opPattern","COPY",BODY,{"derivedFrom":makeQuery(id+"F3.opExtrude","SWEPT_BODY",BODY,{"disambiguationData":[OSD([sQuery(id+"F1.wireOp",EDGE,"E9.0.6.0")])]}),"instanceName":"26"});
            var Q41;
            Q41=makeQuery(id+"F60.opPattern","COPY",BODY,{"derivedFrom":makeQuery(id+"F3.opExtrude","SWEPT_BODY",BODY,{"disambiguationData":[OSD([sQuery(id+"F1.wireOp",EDGE,"E9.0.7.0")])]}),"instanceName":"35"});
            var Q42;
            Q42=makeQuery(id+"F60.opPattern","COPY",BODY,{"derivedFrom":makeQuery(id+"F3.opExtrude","SWEPT_BODY",BODY,{"disambiguationData":[OSD([sQuery(id+"F1.wireOp",EDGE,"E9.0.6.0")])]}),"instanceName":"10"});
            var Q43;
            Q43=makeQuery(id+"F60.opPattern","COPY",BODY,{"derivedFrom":makeQuery(id+"F3.opExtrude","SWEPT_BODY",BODY,{"disambiguationData":[OSD([sQuery(id+"F1.wireOp",EDGE,"E9.0.6.0")])]}),"instanceName":"16"});
            var Q44;
            Q44=makeQuery(id+"F61.opPattern","COPY",BODY,{"derivedFrom":makeQuery(id+"F3.opExtrude","SWEPT_BODY",BODY,{"disambiguationData":[OSD([sQuery(id+"F1.wireOp",EDGE,"E9.0.4.0")])]}),"instanceName":"17"});
            var Q45;
            Q45=makeQuery(id+"F58.opPattern","COPY",BODY,{"derivedFrom":makeQuery(id+"F3.opExtrude","SWEPT_BODY",BODY,{"disambiguationData":[OSD([sQuery(id+"F1.wireOp",EDGE,"E9.0.9.0")])]}),"instanceName":"28"});
            var Q46;
            Q46=makeQuery(id+"F58.opPattern","COPY",BODY,{"derivedFrom":makeQuery(id+"F3.opExtrude","SWEPT_BODY",BODY,{"disambiguationData":[OSD([sQuery(id+"F1.wireOp",EDGE,"E9.0.10.0")])]}),"instanceName":"28"});
            var Q47;
            Q47=makeQuery(id+"F59.opPattern","COPY",BODY,{"derivedFrom":makeQuery(id+"F3.opExtrude","SWEPT_BODY",BODY,{"disambiguationData":[OSD([sQuery(id+"F1.wireOp",EDGE,"E9.0.8.0")])]}),"instanceName":"27"});
            var Q48;
            Q48=makeQuery(id+"F60.opPattern","COPY",BODY,{"derivedFrom":makeQuery(id+"F3.opExtrude","SWEPT_BODY",BODY,{"disambiguationData":[OSD([sQuery(id+"F1.wireOp",EDGE,"E9.0.6.0")])]}),"instanceName":"35"});
            var Q49;
            Q49=makeQuery(id+"F58.opPattern","COPY",BODY,{"derivedFrom":makeQuery(id+"F3.opExtrude","SWEPT_BODY",BODY,{"disambiguationData":[OSD([sQuery(id+"F1.wireOp",EDGE,"E9.0.9.0")])]}),"instanceName":"13"});
            var Q50;
            Q50=makeQuery(id+"F58.opPattern","COPY",BODY,{"derivedFrom":makeQuery(id+"F3.opExtrude","SWEPT_BODY",BODY,{"disambiguationData":[OSD([sQuery(id+"F1.wireOp",EDGE,"E9.0.10.0")])]}),"instanceName":"12"});
            var Q51;
            Q51=makeQuery(id+"F61.opPattern","COPY",BODY,{"derivedFrom":makeQuery(id+"F3.opExtrude","SWEPT_BODY",BODY,{"disambiguationData":[OSD([sQuery(id+"F1.wireOp",EDGE,"E9.0.5.0")])]}),"instanceName":"16"});
            var Q52;
            Q52=makeQuery(id+"F58.opPattern","COPY",BODY,{"derivedFrom":makeQuery(id+"F3.opExtrude","SWEPT_BODY",BODY,{"disambiguationData":[OSD([sQuery(id+"F1.wireOp",EDGE,"E9.0.9.0")])]}),"instanceName":"46"});
            var Q53;
            Q53=makeQuery(id+"F60.opPattern","COPY",BODY,{"derivedFrom":makeQuery(id+"F3.opExtrude","SWEPT_BODY",BODY,{"disambiguationData":[OSD([sQuery(id+"F1.wireOp",EDGE,"E9.0.7.0")])]}),"instanceName":"26"});
            var Q54;
            Q54=makeQuery(id+"F60.opPattern","COPY",BODY,{"derivedFrom":makeQuery(id+"F3.opExtrude","SWEPT_BODY",BODY,{"disambiguationData":[OSD([sQuery(id+"F1.wireOp",EDGE,"E9.0.7.0")])]}),"instanceName":"9"});
            var Q55;
            Q55=makeQuery(id+"F58.opPattern","COPY",BODY,{"derivedFrom":makeQuery(id+"F3.opExtrude","SWEPT_BODY",BODY,{"disambiguationData":[OSD([sQuery(id+"F1.wireOp",EDGE,"E9.0.9.0")])]}),"instanceName":"12"});
            var Q56;
            Q56=makeQuery(id+"F61.opPattern","COPY",BODY,{"derivedFrom":makeQuery(id+"F3.opExtrude","SWEPT_BODY",BODY,{"disambiguationData":[OSD([sQuery(id+"F1.wireOp",EDGE,"E9.0.5.0")])]}),"instanceName":"26"});
            var Q57;
            Q57=makeQuery(id+"F60.opPattern","COPY",BODY,{"derivedFrom":makeQuery(id+"F3.opExtrude","SWEPT_BODY",BODY,{"disambiguationData":[OSD([sQuery(id+"F1.wireOp",EDGE,"E9.0.6.0")])]}),"instanceName":"9"});
            var Q58;
            Q58=makeQuery(id+"F58.opPattern","COPY",BODY,{"derivedFrom":makeQuery(id+"F3.opExtrude","SWEPT_BODY",BODY,{"disambiguationData":[OSD([sQuery(id+"F1.wireOp",EDGE,"E9.0.10.0")])]}),"instanceName":"11"});
            var Q59;
            Q59=makeQuery(id+"F60.opPattern","COPY",BODY,{"derivedFrom":makeQuery(id+"F3.opExtrude","SWEPT_BODY",BODY,{"disambiguationData":[OSD([sQuery(id+"F1.wireOp",EDGE,"E9.0.7.0")])]}),"instanceName":"34"});
            var Q60;
            Q60=makeQuery(id+"F60.opPattern","COPY",BODY,{"derivedFrom":makeQuery(id+"F3.opExtrude","SWEPT_BODY",BODY,{"disambiguationData":[OSD([sQuery(id+"F1.wireOp",EDGE,"E9.0.7.0")])]}),"instanceName":"24"});
            var Q61;
            Q61=makeQuery(id+"F60.opPattern","COPY",BODY,{"derivedFrom":makeQuery(id+"F3.opExtrude","SWEPT_BODY",BODY,{"disambiguationData":[OSD([sQuery(id+"F1.wireOp",EDGE,"E9.0.6.0")])]}),"instanceName":"27"});
            var Q62;
            Q62=makeQuery(id+"F60.opPattern","COPY",BODY,{"derivedFrom":makeQuery(id+"F3.opExtrude","SWEPT_BODY",BODY,{"disambiguationData":[OSD([sQuery(id+"F1.wireOp",EDGE,"E9.0.6.0")])]}),"instanceName":"34"});
            var Q63;
            Q63=makeQuery(id+"F60.opPattern","COPY",BODY,{"derivedFrom":makeQuery(id+"F3.opExtrude","SWEPT_BODY",BODY,{"disambiguationData":[OSD([sQuery(id+"F1.wireOp",EDGE,"E9.0.7.0")])]}),"instanceName":"27"});
            var Q64;
            Q64=makeQuery(id+"F60.opPattern","COPY",BODY,{"derivedFrom":makeQuery(id+"F3.opExtrude","SWEPT_BODY",BODY,{"disambiguationData":[OSD([sQuery(id+"F1.wireOp",EDGE,"E9.0.7.0")])]}),"instanceName":"8"});
            var Q65;
            Q65=makeQuery(id+"F60.opPattern","COPY",BODY,{"derivedFrom":makeQuery(id+"F3.opExtrude","SWEPT_BODY",BODY,{"disambiguationData":[OSD([sQuery(id+"F1.wireOp",EDGE,"E9.0.6.0")])]}),"instanceName":"28"});
            var Q66;
            Q66=makeQuery(id+"F58.opPattern","COPY",BODY,{"derivedFrom":makeQuery(id+"F3.opExtrude","SWEPT_BODY",BODY,{"disambiguationData":[OSD([sQuery(id+"F1.wireOp",EDGE,"E9.0.10.0")])]}),"instanceName":"13"});
            var Q67;
            Q67=makeQuery(id+"F60.opPattern","COPY",BODY,{"derivedFrom":makeQuery(id+"F3.opExtrude","SWEPT_BODY",BODY,{"disambiguationData":[OSD([sQuery(id+"F1.wireOp",EDGE,"E9.0.6.0")])]}),"instanceName":"8"});
            var Q68;
            Q68=makeQuery(id+"F60.opPattern","COPY",BODY,{"derivedFrom":makeQuery(id+"F3.opExtrude","SWEPT_BODY",BODY,{"disambiguationData":[OSD([sQuery(id+"F1.wireOp",EDGE,"E9.0.6.0")])]}),"instanceName":"24"});
            var Q69;
            Q69=makeQuery(id+"F61.opPattern","COPY",BODY,{"derivedFrom":makeQuery(id+"F3.opExtrude","SWEPT_BODY",BODY,{"disambiguationData":[OSD([sQuery(id+"F1.wireOp",EDGE,"E9.0.4.0")])]}),"instanceName":"16"});
            var Q70;
            Q70=makeQuery(id+"F60.opPattern","COPY",BODY,{"derivedFrom":makeQuery(id+"F3.opExtrude","SWEPT_BODY",BODY,{"disambiguationData":[OSD([sQuery(id+"F1.wireOp",EDGE,"E9.0.7.0")])]}),"instanceName":"28"});
            var Q71;
            Q71=makeQuery(id+"F60.opPattern","COPY",BODY,{"derivedFrom":makeQuery(id+"F3.opExtrude","SWEPT_BODY",BODY,{"disambiguationData":[OSD([sQuery(id+"F1.wireOp",EDGE,"E9.0.7.0")])]}),"instanceName":"7"});
            var Q72;
            Q72=makeQuery(id+"F58.opPattern","COPY",BODY,{"derivedFrom":makeQuery(id+"F3.opExtrude","SWEPT_BODY",BODY,{"disambiguationData":[OSD([sQuery(id+"F1.wireOp",EDGE,"E9.0.10.0")])]}),"instanceName":"35"});
            var Q73;
            Q73=makeQuery(id+"F60.opPattern","COPY",BODY,{"derivedFrom":makeQuery(id+"F3.opExtrude","SWEPT_BODY",BODY,{"disambiguationData":[OSD([sQuery(id+"F1.wireOp",EDGE,"E9.0.7.0")])]}),"instanceName":"33"});
            var Q74;
            Q74=makeQuery(id+"F60.opPattern","COPY",BODY,{"derivedFrom":makeQuery(id+"F3.opExtrude","SWEPT_BODY",BODY,{"disambiguationData":[OSD([sQuery(id+"F1.wireOp",EDGE,"E9.0.6.0")])]}),"instanceName":"33"});
            var Q75;
            Q75=makeQuery(id+"F58.opPattern","COPY",BODY,{"derivedFrom":makeQuery(id+"F3.opExtrude","SWEPT_BODY",BODY,{"disambiguationData":[OSD([sQuery(id+"F1.wireOp",EDGE,"E9.0.10.0")])]}),"instanceName":"46"});
            var Q76;
            Q76=makeQuery(id+"F60.opPattern","COPY",BODY,{"derivedFrom":makeQuery(id+"F3.opExtrude","SWEPT_BODY",BODY,{"disambiguationData":[OSD([sQuery(id+"F1.wireOp",EDGE,"E9.0.6.0")])]}),"instanceName":"7"});
            var Q77;
            Q77=makeQuery(id+"F61.opPattern","COPY",BODY,{"derivedFrom":makeQuery(id+"F3.opExtrude","SWEPT_BODY",BODY,{"disambiguationData":[OSD([sQuery(id+"F1.wireOp",EDGE,"E9.0.5.0")])]}),"instanceName":"15"});
            var Q78;
            Q78=makeQuery(id+"F60.opPattern","COPY",BODY,{"derivedFrom":makeQuery(id+"F3.opExtrude","SWEPT_BODY",BODY,{"disambiguationData":[OSD([sQuery(id+"F1.wireOp",EDGE,"E9.0.7.0")])]}),"instanceName":"6"});
            var Q79;
            Q79=makeQuery(id+"F60.opPattern","COPY",BODY,{"derivedFrom":makeQuery(id+"F3.opExtrude","SWEPT_BODY",BODY,{"disambiguationData":[OSD([sQuery(id+"F1.wireOp",EDGE,"E9.0.6.0")])]}),"instanceName":"6"});
            var Q80;
            Q80=makeQuery(id+"F61.opPattern","COPY",BODY,{"derivedFrom":makeQuery(id+"F3.opExtrude","SWEPT_BODY",BODY,{"disambiguationData":[OSD([sQuery(id+"F1.wireOp",EDGE,"E9.0.4.0")])]}),"instanceName":"15"});
            var Q81;
            Q81=makeQuery(id+"F58.opPattern","COPY",BODY,{"derivedFrom":makeQuery(id+"F3.opExtrude","SWEPT_BODY",BODY,{"disambiguationData":[OSD([sQuery(id+"F1.wireOp",EDGE,"E9.0.10.0")])]}),"instanceName":"39"});
            var Q82;
            Q82=makeQuery(id+"F59.opPattern","COPY",BODY,{"derivedFrom":makeQuery(id+"F3.opExtrude","SWEPT_BODY",BODY,{"disambiguationData":[OSD([sQuery(id+"F1.wireOp",EDGE,"E9.0.8.0")])]}),"instanceName":"13"});
            var Q83;
            Q83=makeQuery(id+"F59.opPattern","COPY",BODY,{"derivedFrom":makeQuery(id+"F3.opExtrude","SWEPT_BODY",BODY,{"disambiguationData":[OSD([sQuery(id+"F1.wireOp",EDGE,"E9.0.8.0")])]}),"instanceName":"28"});
            var Q84;
            Q84=makeQuery(id+"F60.opPattern","COPY",BODY,{"derivedFrom":makeQuery(id+"F3.opExtrude","SWEPT_BODY",BODY,{"disambiguationData":[OSD([sQuery(id+"F1.wireOp",EDGE,"E9.0.7.0")])]}),"instanceName":"5"});
            var Q85;
            Q85=makeQuery(id+"F60.opPattern","COPY",BODY,{"derivedFrom":makeQuery(id+"F3.opExtrude","SWEPT_BODY",BODY,{"disambiguationData":[OSD([sQuery(id+"F1.wireOp",EDGE,"E9.0.6.0")])]}),"instanceName":"5"});
            var Q86;
            Q86=makeQuery(id+"F59.opPattern","COPY",BODY,{"derivedFrom":makeQuery(id+"F3.opExtrude","SWEPT_BODY",BODY,{"disambiguationData":[OSD([sQuery(id+"F1.wireOp",EDGE,"E9.0.8.0")])]}),"instanceName":"10"});
            var Q87;
            Q87=makeQuery(id+"F61.opPattern","COPY",BODY,{"derivedFrom":makeQuery(id+"F3.opExtrude","SWEPT_BODY",BODY,{"disambiguationData":[OSD([sQuery(id+"F1.wireOp",EDGE,"E9.0.5.0")])]}),"instanceName":"14"});
            var Q88;
            Q88=makeQuery(id+"F61.opPattern","COPY",BODY,{"derivedFrom":makeQuery(id+"F3.opExtrude","SWEPT_BODY",BODY,{"disambiguationData":[OSD([sQuery(id+"F1.wireOp",EDGE,"E9.0.4.0")])]}),"instanceName":"14"});
            var Q89;
            Q89=makeQuery(id+"F60.opPattern","COPY",BODY,{"derivedFrom":makeQuery(id+"F3.opExtrude","SWEPT_BODY",BODY,{"disambiguationData":[OSD([sQuery(id+"F1.wireOp",EDGE,"E9.0.7.0")])]}),"instanceName":"4"});
            var Q90;
            Q90=makeQuery(id+"F60.opPattern","COPY",BODY,{"derivedFrom":makeQuery(id+"F3.opExtrude","SWEPT_BODY",BODY,{"disambiguationData":[OSD([sQuery(id+"F1.wireOp",EDGE,"E9.0.7.0")])]}),"instanceName":"32"});
            var Q91;
            Q91=makeQuery(id+"F60.opPattern","COPY",BODY,{"derivedFrom":makeQuery(id+"F3.opExtrude","SWEPT_BODY",BODY,{"disambiguationData":[OSD([sQuery(id+"F1.wireOp",EDGE,"E9.0.6.0")])]}),"instanceName":"29"});
            var Q92;
            Q92=makeQuery(id+"F58.opPattern","COPY",BODY,{"derivedFrom":makeQuery(id+"F3.opExtrude","SWEPT_BODY",BODY,{"disambiguationData":[OSD([sQuery(id+"F1.wireOp",EDGE,"E9.0.10.0")])]}),"instanceName":"22"});
            var Q93;
            Q93=makeQuery(id+"F61.opPattern","COPY",BODY,{"derivedFrom":makeQuery(id+"F3.opExtrude","SWEPT_BODY",BODY,{"disambiguationData":[OSD([sQuery(id+"F1.wireOp",EDGE,"E9.0.5.0")])]}),"instanceName":"42"});
            var Q94;
            Q94=makeQuery(id+"F58.opPattern","COPY",BODY,{"derivedFrom":makeQuery(id+"F3.opExtrude","SWEPT_BODY",BODY,{"disambiguationData":[OSD([sQuery(id+"F1.wireOp",EDGE,"E9.0.9.0")])]}),"instanceName":"22"});
            var Q95;
            Q95=makeQuery(id+"F58.opPattern","COPY",BODY,{"derivedFrom":makeQuery(id+"F3.opExtrude","SWEPT_BODY",BODY,{"disambiguationData":[OSD([sQuery(id+"F1.wireOp",EDGE,"E9.0.10.0")])]}),"instanceName":"34"});
            var Q96;
            Q96=makeQuery(id+"F60.opPattern","COPY",BODY,{"derivedFrom":makeQuery(id+"F3.opExtrude","SWEPT_BODY",BODY,{"disambiguationData":[OSD([sQuery(id+"F1.wireOp",EDGE,"E9.0.6.0")])]}),"instanceName":"32"});
            var Q97;
            Q97=makeQuery(id+"F60.opPattern","COPY",BODY,{"derivedFrom":makeQuery(id+"F3.opExtrude","SWEPT_BODY",BODY,{"disambiguationData":[OSD([sQuery(id+"F1.wireOp",EDGE,"E9.0.6.0")])]}),"instanceName":"4"});
            var Q98;
            Q98=makeQuery(id+"F60.opPattern","COPY",BODY,{"derivedFrom":makeQuery(id+"F3.opExtrude","SWEPT_BODY",BODY,{"disambiguationData":[OSD([sQuery(id+"F1.wireOp",EDGE,"E9.0.7.0")])]}),"instanceName":"31"});
            var Q99;
            Q99=makeQuery(id+"F61.opPattern","COPY",BODY,{"derivedFrom":makeQuery(id+"F3.opExtrude","SWEPT_BODY",BODY,{"disambiguationData":[OSD([sQuery(id+"F1.wireOp",EDGE,"E9.0.5.0")])]}),"instanceName":"25"});
            var Q100;
            Q100=makeQuery(id+"F61.opPattern","COPY",BODY,{"derivedFrom":makeQuery(id+"F3.opExtrude","SWEPT_BODY",BODY,{"disambiguationData":[OSD([sQuery(id+"F1.wireOp",EDGE,"E9.0.5.0")])]}),"instanceName":"13"});
            var Q101;
            Q101=makeQuery(id+"F59.opPattern","COPY",BODY,{"derivedFrom":makeQuery(id+"F3.opExtrude","SWEPT_BODY",BODY,{"disambiguationData":[OSD([sQuery(id+"F1.wireOp",EDGE,"E9.0.8.0")])]}),"instanceName":"11"});
            var Q102;
            Q102=makeQuery(id+"F59.opPattern","COPY",BODY,{"derivedFrom":makeQuery(id+"F3.opExtrude","SWEPT_BODY",BODY,{"disambiguationData":[OSD([sQuery(id+"F1.wireOp",EDGE,"E9.0.8.0")])]}),"instanceName":"17"});
            var Q103;
            Q103=makeQuery(id+"F61.opPattern","COPY",BODY,{"derivedFrom":makeQuery(id+"F3.opExtrude","SWEPT_BODY",BODY,{"disambiguationData":[OSD([sQuery(id+"F1.wireOp",EDGE,"E9.0.4.0")])]}),"instanceName":"13"});
            var Q104;
            Q104=makeQuery(id+"F58.opPattern","COPY",BODY,{"derivedFrom":makeQuery(id+"F3.opExtrude","SWEPT_BODY",BODY,{"disambiguationData":[OSD([sQuery(id+"F1.wireOp",EDGE,"E9.0.9.0")])]}),"instanceName":"35"});
            var Q105;
            Q105=makeQuery(id+"F61.opPattern","COPY",BODY,{"derivedFrom":makeQuery(id+"F3.opExtrude","SWEPT_BODY",BODY,{"disambiguationData":[OSD([sQuery(id+"F1.wireOp",EDGE,"E9.0.5.0")])]}),"instanceName":"40"});
            var Q106;
            Q106=makeQuery(id+"F61.opPattern","COPY",BODY,{"derivedFrom":makeQuery(id+"F3.opExtrude","SWEPT_BODY",BODY,{"disambiguationData":[OSD([sQuery(id+"F1.wireOp",EDGE,"E9.0.4.0")])]}),"instanceName":"1"});
            var Q107;
            Q107=makeQuery(id+"F61.opPattern","COPY",BODY,{"derivedFrom":makeQuery(id+"F3.opExtrude","SWEPT_BODY",BODY,{"disambiguationData":[OSD([sQuery(id+"F1.wireOp",EDGE,"E9.0.5.0")])]}),"instanceName":"12"});
            var Q108;
            Q108=makeQuery(id+"F58.opPattern","COPY",BODY,{"derivedFrom":makeQuery(id+"F3.opExtrude","SWEPT_BODY",BODY,{"disambiguationData":[OSD([sQuery(id+"F1.wireOp",EDGE,"E9.0.9.0")])]}),"instanceName":"5"});
            var Q109;
            Q109=makeQuery(id+"F61.opPattern","COPY",BODY,{"derivedFrom":makeQuery(id+"F3.opExtrude","SWEPT_BODY",BODY,{"disambiguationData":[OSD([sQuery(id+"F1.wireOp",EDGE,"E9.0.4.0")])]}),"instanceName":"12"});
            var Q110;
            Q110=makeQuery(id+"F59.opPattern","COPY",BODY,{"derivedFrom":makeQuery(id+"F3.opExtrude","SWEPT_BODY",BODY,{"disambiguationData":[OSD([sQuery(id+"F1.wireOp",EDGE,"E9.0.8.0")])]}),"instanceName":"15"});
            var Q111;
            Q111=makeQuery(id+"F61.opPattern","COPY",BODY,{"derivedFrom":makeQuery(id+"F3.opExtrude","SWEPT_BODY",BODY,{"disambiguationData":[OSD([sQuery(id+"F1.wireOp",EDGE,"E9.0.5.0")])]}),"instanceName":"1"});
            var Q112;
            Q112=makeQuery(id+"F58.opPattern","COPY",BODY,{"derivedFrom":makeQuery(id+"F3.opExtrude","SWEPT_BODY",BODY,{"disambiguationData":[OSD([sQuery(id+"F1.wireOp",EDGE,"E9.0.10.0")])]}),"instanceName":"21"});
            var Q113;
            Q113=makeQuery(id+"F60.opPattern","COPY",BODY,{"derivedFrom":makeQuery(id+"F3.opExtrude","SWEPT_BODY",BODY,{"disambiguationData":[OSD([sQuery(id+"F1.wireOp",EDGE,"E9.0.6.0")])]}),"instanceName":"41"});
            var Q114;
            Q114=makeQuery(id+"F60.opPattern","COPY",BODY,{"derivedFrom":makeQuery(id+"F3.opExtrude","SWEPT_BODY",BODY,{"disambiguationData":[OSD([sQuery(id+"F1.wireOp",EDGE,"E9.0.7.0")])]}),"instanceName":"41"});
            var Q115;
            Q115=makeQuery(id+"F58.opPattern","COPY",BODY,{"derivedFrom":makeQuery(id+"F3.opExtrude","SWEPT_BODY",BODY,{"disambiguationData":[OSD([sQuery(id+"F1.wireOp",EDGE,"E9.0.9.0")])]}),"instanceName":"21"});
            var Q116;
            Q116=makeQuery(id+"F60.opPattern","COPY",BODY,{"derivedFrom":makeQuery(id+"F3.opExtrude","SWEPT_BODY",BODY,{"disambiguationData":[OSD([sQuery(id+"F1.wireOp",EDGE,"E9.0.6.0")])]}),"instanceName":"31"});
            var Q117;
            Q117=makeQuery(id+"F60.opPattern","COPY",BODY,{"derivedFrom":makeQuery(id+"F3.opExtrude","SWEPT_BODY",BODY,{"disambiguationData":[OSD([sQuery(id+"F1.wireOp",EDGE,"E9.0.7.0")])]}),"instanceName":"30"});
            var Q118;
            Q118=makeQuery(id+"F61.opPattern","COPY",BODY,{"derivedFrom":makeQuery(id+"F3.opExtrude","SWEPT_BODY",BODY,{"disambiguationData":[OSD([sQuery(id+"F1.wireOp",EDGE,"E9.0.5.0")])]}),"instanceName":"11"});
            var Q119;
            Q119=makeQuery(id+"F59.opPattern","COPY",BODY,{"derivedFrom":makeQuery(id+"F3.opExtrude","SWEPT_BODY",BODY,{"disambiguationData":[OSD([sQuery(id+"F1.wireOp",EDGE,"E9.0.8.0")])]}),"instanceName":"8"});
            var Q120;
            Q120=makeQuery(id+"F61.opPattern","COPY",BODY,{"derivedFrom":makeQuery(id+"F3.opExtrude","SWEPT_BODY",BODY,{"disambiguationData":[OSD([sQuery(id+"F1.wireOp",EDGE,"E9.0.4.0")])]}),"instanceName":"11"});
            var Q121;
            Q121=makeQuery(id+"F61.opPattern","COPY",BODY,{"derivedFrom":makeQuery(id+"F3.opExtrude","SWEPT_BODY",BODY,{"disambiguationData":[OSD([sQuery(id+"F1.wireOp",EDGE,"E9.0.5.0")])]}),"instanceName":"10"});
            var Q122;
            Q122=makeQuery(id+"F58.opPattern","COPY",BODY,{"derivedFrom":makeQuery(id+"F3.opExtrude","SWEPT_BODY",BODY,{"disambiguationData":[OSD([sQuery(id+"F1.wireOp",EDGE,"E9.0.10.0")])]}),"instanceName":"20"});
            var Q123;
            Q123=makeQuery(id+"F60.opPattern","COPY",BODY,{"derivedFrom":makeQuery(id+"F3.opExtrude","SWEPT_BODY",BODY,{"disambiguationData":[OSD([sQuery(id+"F1.wireOp",EDGE,"E9.0.7.0")])]}),"instanceName":"1"});
            var Q124;
            Q124=makeQuery(id+"F61.opPattern","COPY",BODY,{"derivedFrom":makeQuery(id+"F3.opExtrude","SWEPT_BODY",BODY,{"disambiguationData":[OSD([sQuery(id+"F1.wireOp",EDGE,"E9.0.4.0")])]}),"instanceName":"42"});
            var Q125;
            Q125=makeQuery(id+"F58.opPattern","COPY",BODY,{"derivedFrom":makeQuery(id+"F3.opExtrude","SWEPT_BODY",BODY,{"disambiguationData":[OSD([sQuery(id+"F1.wireOp",EDGE,"E9.0.10.0")])]}),"instanceName":"33"});
            var Q126;
            Q126=makeQuery(id+"F60.opPattern","COPY",BODY,{"derivedFrom":makeQuery(id+"F3.opExtrude","SWEPT_BODY",BODY,{"disambiguationData":[OSD([sQuery(id+"F1.wireOp",EDGE,"E9.0.6.0")])]}),"instanceName":"42"});
            var Q127;
            Q127=makeQuery(id+"F60.opPattern","COPY",BODY,{"derivedFrom":makeQuery(id+"F3.opExtrude","SWEPT_BODY",BODY,{"disambiguationData":[OSD([sQuery(id+"F1.wireOp",EDGE,"E9.0.6.0")])]}),"instanceName":"30"});
            var Q128;
            Q128=makeQuery(id+"F61.opPattern","COPY",BODY,{"derivedFrom":makeQuery(id+"F3.opExtrude","SWEPT_BODY",BODY,{"disambiguationData":[OSD([sQuery(id+"F1.wireOp",EDGE,"E9.0.4.0")])]}),"instanceName":"4"});
            var Q129;
            Q129=makeQuery(id+"F60.opPattern","COPY",BODY,{"derivedFrom":makeQuery(id+"F3.opExtrude","SWEPT_BODY",BODY,{"disambiguationData":[OSD([sQuery(id+"F1.wireOp",EDGE,"E9.0.7.0")])]}),"instanceName":"29"});
            var Q130;
            Q130=makeQuery(id+"F59.opPattern","COPY",BODY,{"derivedFrom":makeQuery(id+"F3.opExtrude","SWEPT_BODY",BODY,{"disambiguationData":[OSD([sQuery(id+"F1.wireOp",EDGE,"E9.0.8.0")])]}),"instanceName":"5"});
            var Q131;
            Q131=makeQuery(id+"F60.opPattern","COPY",BODY,{"derivedFrom":makeQuery(id+"F3.opExtrude","SWEPT_BODY",BODY,{"disambiguationData":[OSD([sQuery(id+"F1.wireOp",EDGE,"E9.0.6.0")])]}),"instanceName":"1"});
            var Q132;
            Q132=makeQuery(id+"F60.opPattern","COPY",BODY,{"derivedFrom":makeQuery(id+"F3.opExtrude","SWEPT_BODY",BODY,{"disambiguationData":[OSD([sQuery(id+"F1.wireOp",EDGE,"E9.0.6.0")])]}),"instanceName":"20"});
            var Q133;
            Q133=makeQuery(id+"F61.opPattern","COPY",BODY,{"derivedFrom":makeQuery(id+"F3.opExtrude","SWEPT_BODY",BODY,{"disambiguationData":[OSD([sQuery(id+"F1.wireOp",EDGE,"E9.0.5.0")])]}),"instanceName":"4"});
            var Q134;
            Q134=makeQuery(id+"F61.opPattern","COPY",BODY,{"derivedFrom":makeQuery(id+"F3.opExtrude","SWEPT_BODY",BODY,{"disambiguationData":[OSD([sQuery(id+"F1.wireOp",EDGE,"E9.0.4.0")])]}),"instanceName":"10"});
            var Q135;
            Q135=makeQuery(id+"F61.opPattern","COPY",BODY,{"derivedFrom":makeQuery(id+"F3.opExtrude","SWEPT_BODY",BODY,{"disambiguationData":[OSD([sQuery(id+"F1.wireOp",EDGE,"E9.0.5.0")])]}),"instanceName":"45"});
            var Q136;
            Q136=makeQuery(id+"F61.opPattern","COPY",BODY,{"derivedFrom":makeQuery(id+"F3.opExtrude","SWEPT_BODY",BODY,{"disambiguationData":[OSD([sQuery(id+"F1.wireOp",EDGE,"E9.0.4.0")])]}),"instanceName":"43"});
            var Q137;
            Q137=makeQuery(id+"F61.opPattern","COPY",BODY,{"derivedFrom":makeQuery(id+"F3.opExtrude","SWEPT_BODY",BODY,{"disambiguationData":[OSD([sQuery(id+"F1.wireOp",EDGE,"E9.0.5.0")])]}),"instanceName":"9"});
            var Q138;
            Q138=makeQuery(id+"F61.opPattern","COPY",BODY,{"derivedFrom":makeQuery(id+"F3.opExtrude","SWEPT_BODY",BODY,{"disambiguationData":[OSD([sQuery(id+"F1.wireOp",EDGE,"E9.0.5.0")])]}),"instanceName":"35"});
            var Q139;
            Q139=makeQuery(id+"F58.opPattern","COPY",BODY,{"derivedFrom":makeQuery(id+"F3.opExtrude","SWEPT_BODY",BODY,{"disambiguationData":[OSD([sQuery(id+"F1.wireOp",EDGE,"E9.0.9.0")])]}),"instanceName":"20"});
            var Q140;
            Q140=makeQuery(id+"F61.opPattern","COPY",BODY,{"derivedFrom":makeQuery(id+"F3.opExtrude","SWEPT_BODY",BODY,{"disambiguationData":[OSD([sQuery(id+"F1.wireOp",EDGE,"E9.0.5.0")])]}),"instanceName":"34"});
            var Q141;
            Q141=makeQuery(id+"F61.opPattern","COPY",BODY,{"derivedFrom":makeQuery(id+"F3.opExtrude","SWEPT_BODY",BODY,{"disambiguationData":[OSD([sQuery(id+"F1.wireOp",EDGE,"E9.0.4.0")])]}),"instanceName":"35"});
            var Q142;
            Q142=makeQuery(id+"F61.opPattern","COPY",BODY,{"derivedFrom":makeQuery(id+"F3.opExtrude","SWEPT_BODY",BODY,{"disambiguationData":[OSD([sQuery(id+"F1.wireOp",EDGE,"E9.0.4.0")])]}),"instanceName":"44"});
            var Q143;
            Q143=makeQuery(id+"F58.opPattern","COPY",BODY,{"derivedFrom":makeQuery(id+"F3.opExtrude","SWEPT_BODY",BODY,{"disambiguationData":[OSD([sQuery(id+"F1.wireOp",EDGE,"E9.0.10.0")])]}),"instanceName":"30"});
            var Q144;
            Q144=makeQuery(id+"F61.opPattern","COPY",BODY,{"derivedFrom":makeQuery(id+"F3.opExtrude","SWEPT_BODY",BODY,{"disambiguationData":[OSD([sQuery(id+"F1.wireOp",EDGE,"E9.0.4.0")])]}),"instanceName":"45"});
            var Q145;
            Q145=makeQuery(id+"F58.opPattern","COPY",BODY,{"derivedFrom":makeQuery(id+"F3.opExtrude","SWEPT_BODY",BODY,{"disambiguationData":[OSD([sQuery(id+"F1.wireOp",EDGE,"E9.0.9.0")])]}),"instanceName":"30"});
            var Q146;
            Q146=makeQuery(id+"F61.opPattern","COPY",BODY,{"derivedFrom":makeQuery(id+"F3.opExtrude","SWEPT_BODY",BODY,{"disambiguationData":[OSD([sQuery(id+"F1.wireOp",EDGE,"E9.0.4.0")])]}),"instanceName":"46"});
            var Q147;
            Q147=makeQuery(id+"F59.opPattern","COPY",BODY,{"derivedFrom":makeQuery(id+"F3.opExtrude","SWEPT_BODY",BODY,{"disambiguationData":[OSD([sQuery(id+"F1.wireOp",EDGE,"E9.0.8.0")])]}),"instanceName":"18"});
            var Q148;
            Q148=makeQuery(id+"F61.opPattern","COPY",BODY,{"derivedFrom":makeQuery(id+"F3.opExtrude","SWEPT_BODY",BODY,{"disambiguationData":[OSD([sQuery(id+"F1.wireOp",EDGE,"E9.0.4.0")])]}),"instanceName":"26"});
            var Q149;
            Q149=makeQuery(id+"F61.opPattern","COPY",BODY,{"derivedFrom":makeQuery(id+"F3.opExtrude","SWEPT_BODY",BODY,{"disambiguationData":[OSD([sQuery(id+"F1.wireOp",EDGE,"E9.0.5.0")])]}),"instanceName":"46"});
            var Q150;
            Q150=makeQuery(id+"F58.opPattern","COPY",BODY,{"derivedFrom":makeQuery(id+"F3.opExtrude","SWEPT_BODY",BODY,{"disambiguationData":[OSD([sQuery(id+"F1.wireOp",EDGE,"E9.0.10.0")])]}),"instanceName":"29"});
            var Q151;
            Q151=makeQuery(id+"F61.opPattern","COPY",BODY,{"derivedFrom":makeQuery(id+"F3.opExtrude","SWEPT_BODY",BODY,{"disambiguationData":[OSD([sQuery(id+"F1.wireOp",EDGE,"E9.0.4.0")])]}),"instanceName":"34"});
            var Q152;
            Q152=makeQuery(id+"F58.opPattern","COPY",BODY,{"derivedFrom":makeQuery(id+"F3.opExtrude","SWEPT_BODY",BODY,{"disambiguationData":[OSD([sQuery(id+"F1.wireOp",EDGE,"E9.0.9.0")])]}),"instanceName":"15"});
            var Q153;
            Q153=makeQuery(id+"F59.opPattern","COPY",BODY,{"derivedFrom":makeQuery(id+"F3.opExtrude","SWEPT_BODY",BODY,{"disambiguationData":[OSD([sQuery(id+"F1.wireOp",EDGE,"E9.0.8.0")])]}),"instanceName":"1"});
            var Q154;
            Q154=makeQuery(id+"F60.opPattern","COPY",BODY,{"derivedFrom":makeQuery(id+"F3.opExtrude","SWEPT_BODY",BODY,{"disambiguationData":[OSD([sQuery(id+"F1.wireOp",EDGE,"E9.0.6.0")])]}),"instanceName":"21"});
            var Q155;
            Q155=makeQuery(id+"F61.opPattern","COPY",BODY,{"derivedFrom":makeQuery(id+"F3.opExtrude","SWEPT_BODY",BODY,{"disambiguationData":[OSD([sQuery(id+"F1.wireOp",EDGE,"E9.0.5.0")])]}),"instanceName":"33"});
            var Q156;
            Q156=makeQuery(id+"F61.opPattern","COPY",BODY,{"derivedFrom":makeQuery(id+"F3.opExtrude","SWEPT_BODY",BODY,{"disambiguationData":[OSD([sQuery(id+"F1.wireOp",EDGE,"E9.0.4.0")])]}),"instanceName":"47"});
            var Q157;
            Q157=makeQuery(id+"F61.opPattern","COPY",BODY,{"derivedFrom":makeQuery(id+"F3.opExtrude","SWEPT_BODY",BODY,{"disambiguationData":[OSD([sQuery(id+"F1.wireOp",EDGE,"E9.0.5.0")])]}),"instanceName":"47"});
            var Q158;
            Q158=makeQuery(id+"F59.opPattern","COPY",BODY,{"derivedFrom":makeQuery(id+"F3.opExtrude","SWEPT_BODY",BODY,{"disambiguationData":[OSD([sQuery(id+"F1.wireOp",EDGE,"E9.0.8.0")])]}),"instanceName":"23"});
            var Q159;
            Q159=makeQuery(id+"F59.opPattern","COPY",BODY,{"derivedFrom":makeQuery(id+"F3.opExtrude","SWEPT_BODY",BODY,{"disambiguationData":[OSD([sQuery(id+"F1.wireOp",EDGE,"E9.0.8.0")])]}),"instanceName":"9"});
            var Q160;
            Q160=makeQuery(id+"F60.opPattern","COPY",BODY,{"derivedFrom":makeQuery(id+"F3.opExtrude","SWEPT_BODY",BODY,{"disambiguationData":[OSD([sQuery(id+"F1.wireOp",EDGE,"E9.0.7.0")])]}),"instanceName":"21"});
            var Q161;
            Q161=makeQuery(id+"F61.opPattern","COPY",BODY,{"derivedFrom":makeQuery(id+"F3.opExtrude","SWEPT_BODY",BODY,{"disambiguationData":[OSD([sQuery(id+"F1.wireOp",EDGE,"E9.0.4.0")])]}),"instanceName":"33"});
            var Q162;
            Q162=makeQuery(id+"F61.opPattern","COPY",BODY,{"derivedFrom":makeQuery(id+"F3.opExtrude","SWEPT_BODY",BODY,{"disambiguationData":[OSD([sQuery(id+"F1.wireOp",EDGE,"E9.0.5.0")])]}),"instanceName":"32"});
            var Q163;
            Q163=makeQuery(id+"F61.opPattern","COPY",BODY,{"derivedFrom":makeQuery(id+"F3.opExtrude","SWEPT_BODY",BODY,{"disambiguationData":[OSD([sQuery(id+"F1.wireOp",EDGE,"E9.0.4.0")])]}),"instanceName":"49"});
            var Q164;
            Q164=makeQuery(id+"F60.opPattern","COPY",BODY,{"derivedFrom":makeQuery(id+"F3.opExtrude","SWEPT_BODY",BODY,{"disambiguationData":[OSD([sQuery(id+"F1.wireOp",EDGE,"E9.0.6.0")])]}),"instanceName":"22"});
            var Q165;
            Q165=makeQuery(id+"F60.opPattern","COPY",BODY,{"derivedFrom":makeQuery(id+"F3.opExtrude","SWEPT_BODY",BODY,{"disambiguationData":[OSD([sQuery(id+"F1.wireOp",EDGE,"E9.0.7.0")])]}),"instanceName":"19"});
            var Q166;
            Q166=makeQuery(id+"F61.opPattern","COPY",BODY,{"derivedFrom":makeQuery(id+"F3.opExtrude","SWEPT_BODY",BODY,{"disambiguationData":[OSD([sQuery(id+"F1.wireOp",EDGE,"E9.0.5.0")])]}),"instanceName":"8"});
            var Q167;
            Q167=makeQuery(id+"F61.opPattern","COPY",BODY,{"derivedFrom":makeQuery(id+"F3.opExtrude","SWEPT_BODY",BODY,{"disambiguationData":[OSD([sQuery(id+"F1.wireOp",EDGE,"E9.0.4.0")])]}),"instanceName":"9"});
            var Q168;
            Q168=makeQuery(id+"F61.opPattern","COPY",BODY,{"derivedFrom":makeQuery(id+"F3.opExtrude","SWEPT_BODY",BODY,{"disambiguationData":[OSD([sQuery(id+"F1.wireOp",EDGE,"E9.0.4.0")])]}),"instanceName":"32"});
            var Q169;
            Q169=makeQuery(id+"F61.opPattern","COPY",BODY,{"derivedFrom":makeQuery(id+"F3.opExtrude","SWEPT_BODY",BODY,{"disambiguationData":[OSD([sQuery(id+"F1.wireOp",EDGE,"E9.0.5.0")])]}),"instanceName":"49"});
            var Q170;
            Q170=makeQuery(id+"F60.opPattern","COPY",BODY,{"derivedFrom":makeQuery(id+"F3.opExtrude","SWEPT_BODY",BODY,{"disambiguationData":[OSD([sQuery(id+"F1.wireOp",EDGE,"E9.0.6.0")])]}),"instanceName":"40"});
            var Q171;
            Q171=makeQuery(id+"F61.opPattern","COPY",BODY,{"derivedFrom":makeQuery(id+"F3.opExtrude","SWEPT_BODY",BODY,{"disambiguationData":[OSD([sQuery(id+"F1.wireOp",EDGE,"E9.0.4.0")])]}),"instanceName":"6"});
            var Q172;
            Q172=makeQuery(id+"F61.opPattern","COPY",BODY,{"derivedFrom":makeQuery(id+"F3.opExtrude","SWEPT_BODY",BODY,{"disambiguationData":[OSD([sQuery(id+"F1.wireOp",EDGE,"E9.0.5.0")])]}),"instanceName":"31"});
            var Q173;
            Q173=makeQuery(id+"F61.opPattern","COPY",BODY,{"derivedFrom":makeQuery(id+"F3.opExtrude","SWEPT_BODY",BODY,{"disambiguationData":[OSD([sQuery(id+"F1.wireOp",EDGE,"E9.0.4.0")])]}),"instanceName":"31"});
            var Q174;
            Q174=makeQuery(id+"F61.opPattern","COPY",BODY,{"derivedFrom":makeQuery(id+"F3.opExtrude","SWEPT_BODY",BODY,{"disambiguationData":[OSD([sQuery(id+"F1.wireOp",EDGE,"E9.0.5.0")])]}),"instanceName":"30"});
            var Q175;
            Q175=makeQuery(id+"F60.opPattern","COPY",BODY,{"derivedFrom":makeQuery(id+"F3.opExtrude","SWEPT_BODY",BODY,{"disambiguationData":[OSD([sQuery(id+"F1.wireOp",EDGE,"E9.0.7.0")])]}),"instanceName":"22"});
            var Q176;
            Q176=makeQuery(id+"F59.opPattern","COPY",BODY,{"derivedFrom":makeQuery(id+"F3.opExtrude","SWEPT_BODY",BODY,{"disambiguationData":[OSD([sQuery(id+"F1.wireOp",EDGE,"E9.0.8.0")])]}),"instanceName":"3"});
            var Q177;
            Q177=makeQuery(id+"F61.opPattern","COPY",BODY,{"derivedFrom":makeQuery(id+"F3.opExtrude","SWEPT_BODY",BODY,{"disambiguationData":[OSD([sQuery(id+"F1.wireOp",EDGE,"E9.0.5.0")])]}),"instanceName":"6"});
            var Q178;
            Q178=makeQuery(id+"F59.opPattern","COPY",BODY,{"derivedFrom":makeQuery(id+"F3.opExtrude","SWEPT_BODY",BODY,{"disambiguationData":[OSD([sQuery(id+"F1.wireOp",EDGE,"E9.0.8.0")])]}),"instanceName":"47"});
            var Q179;
            Q179=makeQuery(id+"F59.opPattern","COPY",BODY,{"derivedFrom":makeQuery(id+"F3.opExtrude","SWEPT_BODY",BODY,{"disambiguationData":[OSD([sQuery(id+"F1.wireOp",EDGE,"E9.0.8.0")])]}),"instanceName":"22"});
            var Q180;
            Q180=makeQuery(id+"F59.opPattern","COPY",BODY,{"derivedFrom":makeQuery(id+"F3.opExtrude","SWEPT_BODY",BODY,{"disambiguationData":[OSD([sQuery(id+"F1.wireOp",EDGE,"E9.0.8.0")])]}),"instanceName":"24"});
            var Q181;
            Q181=makeQuery(id+"F59.opPattern","COPY",BODY,{"derivedFrom":makeQuery(id+"F3.opExtrude","SWEPT_BODY",BODY,{"disambiguationData":[OSD([sQuery(id+"F1.wireOp",EDGE,"E9.0.8.0")])]}),"instanceName":"25"});
            var Q182;
            Q182=makeQuery(id+"F61.opPattern","COPY",BODY,{"derivedFrom":makeQuery(id+"F3.opExtrude","SWEPT_BODY",BODY,{"disambiguationData":[OSD([sQuery(id+"F1.wireOp",EDGE,"E9.0.4.0")])]}),"instanceName":"27"});
            var Q183;
            Q183=makeQuery(id+"F61.opPattern","COPY",BODY,{"derivedFrom":makeQuery(id+"F3.opExtrude","SWEPT_BODY",BODY,{"disambiguationData":[OSD([sQuery(id+"F1.wireOp",EDGE,"E9.0.4.0")])]}),"instanceName":"5"});
            var Q184;
            Q184=makeQuery(id+"F61.opPattern","COPY",BODY,{"derivedFrom":makeQuery(id+"F3.opExtrude","SWEPT_BODY",BODY,{"disambiguationData":[OSD([sQuery(id+"F1.wireOp",EDGE,"E9.0.4.0")])]}),"instanceName":"30"});
            var Q185;
            Q185=makeQuery(id+"F61.opPattern","COPY",BODY,{"derivedFrom":makeQuery(id+"F3.opExtrude","SWEPT_BODY",BODY,{"disambiguationData":[OSD([sQuery(id+"F1.wireOp",EDGE,"E9.0.5.0")])]}),"instanceName":"29"});
            var Q186;
            Q186=makeQuery(id+"F60.opPattern","COPY",BODY,{"derivedFrom":makeQuery(id+"F3.opExtrude","SWEPT_BODY",BODY,{"disambiguationData":[OSD([sQuery(id+"F1.wireOp",EDGE,"E9.0.6.0")])]}),"instanceName":"19"});
            var Q187;
            Q187=makeQuery(id+"F60.opPattern","COPY",BODY,{"derivedFrom":makeQuery(id+"F3.opExtrude","SWEPT_BODY",BODY,{"disambiguationData":[OSD([sQuery(id+"F1.wireOp",EDGE,"E9.0.7.0")])]}),"instanceName":"40"});
            var Q188;
            Q188=makeQuery(id+"F58.opPattern","COPY",BODY,{"derivedFrom":makeQuery(id+"F3.opExtrude","SWEPT_BODY",BODY,{"disambiguationData":[OSD([sQuery(id+"F1.wireOp",EDGE,"E9.0.9.0")])]}),"instanceName":"34"});
            var Q189;
            Q189=makeQuery(id+"F61.opPattern","COPY",BODY,{"derivedFrom":makeQuery(id+"F3.opExtrude","SWEPT_BODY",BODY,{"disambiguationData":[OSD([sQuery(id+"F1.wireOp",EDGE,"E9.0.4.0")])]}),"instanceName":"29"});
            var Q190;
            Q190=makeQuery(id+"F60.opPattern","COPY",BODY,{"derivedFrom":makeQuery(id+"F3.opExtrude","SWEPT_BODY",BODY,{"disambiguationData":[OSD([sQuery(id+"F1.wireOp",EDGE,"E9.0.7.0")])]}),"instanceName":"23"});
            var Q191;
            Q191=makeQuery(id+"F61.opPattern","COPY",BODY,{"derivedFrom":makeQuery(id+"F3.opExtrude","SWEPT_BODY",BODY,{"disambiguationData":[OSD([sQuery(id+"F1.wireOp",EDGE,"E9.0.5.0")])]}),"instanceName":"5"});
            var Q192;
            Q192=makeQuery(id+"F60.opPattern","COPY",BODY,{"derivedFrom":makeQuery(id+"F3.opExtrude","SWEPT_BODY",BODY,{"disambiguationData":[OSD([sQuery(id+"F1.wireOp",EDGE,"E9.0.6.0")])]}),"instanceName":"15"});
            var Q193;
            Q193=makeQuery(id+"F60.opPattern","COPY",BODY,{"derivedFrom":makeQuery(id+"F3.opExtrude","SWEPT_BODY",BODY,{"disambiguationData":[OSD([sQuery(id+"F1.wireOp",EDGE,"E9.0.7.0")])]}),"instanceName":"15"});
            var Q194;
            Q194=makeQuery(id+"F60.opPattern","COPY",BODY,{"derivedFrom":makeQuery(id+"F3.opExtrude","SWEPT_BODY",BODY,{"disambiguationData":[OSD([sQuery(id+"F1.wireOp",EDGE,"E9.0.7.0")])]}),"instanceName":"42"});
            var Q195;
            Q195=makeQuery(id+"F59.opPattern","COPY",BODY,{"derivedFrom":makeQuery(id+"F3.opExtrude","SWEPT_BODY",BODY,{"disambiguationData":[OSD([sQuery(id+"F1.wireOp",EDGE,"E9.0.8.0")])]}),"instanceName":"6"});
            var Q196;
            Q196=makeQuery(id+"F59.opPattern","COPY",BODY,{"derivedFrom":makeQuery(id+"F3.opExtrude","SWEPT_BODY",BODY,{"disambiguationData":[OSD([sQuery(id+"F1.wireOp",EDGE,"E9.0.8.0")])]}),"instanceName":"16"});
            var Q197;
            Q197=makeQuery(id+"F58.opPattern","COPY",BODY,{"derivedFrom":makeQuery(id+"F3.opExtrude","SWEPT_BODY",BODY,{"disambiguationData":[OSD([sQuery(id+"F1.wireOp",EDGE,"E9.0.10.0")])]}),"instanceName":"32"});
            var Q198;
            Q198=makeQuery(id+"F59.opPattern","COPY",BODY,{"derivedFrom":makeQuery(id+"F3.opExtrude","SWEPT_BODY",BODY,{"disambiguationData":[OSD([sQuery(id+"F1.wireOp",EDGE,"E9.0.8.0")])]}),"instanceName":"29"});
            var Q199;
            Q199=makeQuery(id+"F58.opPattern","COPY",BODY,{"derivedFrom":makeQuery(id+"F3.opExtrude","SWEPT_BODY",BODY,{"disambiguationData":[OSD([sQuery(id+"F1.wireOp",EDGE,"E9.0.9.0")])]}),"instanceName":"32"});
            var Q200;
            Q200=makeQuery(id+"F59.opPattern","COPY",BODY,{"derivedFrom":makeQuery(id+"F3.opExtrude","SWEPT_BODY",BODY,{"disambiguationData":[OSD([sQuery(id+"F1.wireOp",EDGE,"E9.0.8.0")])]}),"instanceName":"30"});
            var Q201;
            Q201=makeQuery(id+"F59.opPattern","COPY",BODY,{"derivedFrom":makeQuery(id+"F3.opExtrude","SWEPT_BODY",BODY,{"disambiguationData":[OSD([sQuery(id+"F1.wireOp",EDGE,"E9.0.8.0")])]}),"instanceName":"31"});
            var Q202;
            Q202=makeQuery(id+"F61.opPattern","COPY",BODY,{"derivedFrom":makeQuery(id+"F3.opExtrude","SWEPT_BODY",BODY,{"disambiguationData":[OSD([sQuery(id+"F1.wireOp",EDGE,"E9.0.4.0")])]}),"instanceName":"25"});
            var Q203;
            Q203=makeQuery(id+"F58.opPattern","COPY",BODY,{"derivedFrom":makeQuery(id+"F3.opExtrude","SWEPT_BODY",BODY,{"disambiguationData":[OSD([sQuery(id+"F1.wireOp",EDGE,"E9.0.10.0")])]}),"instanceName":"31"});
            var Q204;
            Q204=makeQuery(id+"F60.opPattern","COPY",BODY,{"derivedFrom":makeQuery(id+"F3.opExtrude","SWEPT_BODY",BODY,{"disambiguationData":[OSD([sQuery(id+"F1.wireOp",EDGE,"E9.0.6.0")])]}),"instanceName":"43"});
            var Q205;
            Q205=makeQuery(id+"F60.opPattern","COPY",BODY,{"derivedFrom":makeQuery(id+"F3.opExtrude","SWEPT_BODY",BODY,{"disambiguationData":[OSD([sQuery(id+"F1.wireOp",EDGE,"E9.0.7.0")])]}),"instanceName":"43"});
            var Q206;
            Q206=makeQuery(id+"F58.opPattern","COPY",BODY,{"derivedFrom":makeQuery(id+"F3.opExtrude","SWEPT_BODY",BODY,{"disambiguationData":[OSD([sQuery(id+"F1.wireOp",EDGE,"E9.0.9.0")])]}),"instanceName":"31"});
            var Q207;
            Q207=makeQuery(id+"F58.opPattern","COPY",BODY,{"derivedFrom":makeQuery(id+"F3.opExtrude","SWEPT_BODY",BODY,{"disambiguationData":[OSD([sQuery(id+"F1.wireOp",EDGE,"E9.0.10.0")])]}),"instanceName":"27"});
            var Q208;
            Q208=makeQuery(id+"F58.opPattern","COPY",BODY,{"derivedFrom":makeQuery(id+"F3.opExtrude","SWEPT_BODY",BODY,{"disambiguationData":[OSD([sQuery(id+"F1.wireOp",EDGE,"E9.0.9.0")])]}),"instanceName":"27"});
            var Q209;
            Q209=makeQuery(id+"F59.opPattern","COPY",BODY,{"derivedFrom":makeQuery(id+"F3.opExtrude","SWEPT_BODY",BODY,{"disambiguationData":[OSD([sQuery(id+"F1.wireOp",EDGE,"E9.0.8.0")])]}),"instanceName":"32"});
            var Q210;
            Q210=makeQuery(id+"F59.opPattern","COPY",BODY,{"derivedFrom":makeQuery(id+"F3.opExtrude","SWEPT_BODY",BODY,{"disambiguationData":[OSD([sQuery(id+"F1.wireOp",EDGE,"E9.0.8.0")])]}),"instanceName":"33"});
            var Q211;
            Q211=makeQuery(id+"F61.opPattern","COPY",BODY,{"derivedFrom":makeQuery(id+"F3.opExtrude","SWEPT_BODY",BODY,{"disambiguationData":[OSD([sQuery(id+"F1.wireOp",EDGE,"E9.0.4.0")])]}),"instanceName":"40"});
            var Q212;
            Q212=makeQuery(id+"F60.opPattern","COPY",BODY,{"derivedFrom":makeQuery(id+"F3.opExtrude","SWEPT_BODY",BODY,{"disambiguationData":[OSD([sQuery(id+"F1.wireOp",EDGE,"E9.0.6.0")])]}),"instanceName":"44"});
            var Q213;
            Q213=makeQuery(id+"F61.opPattern","COPY",BODY,{"derivedFrom":makeQuery(id+"F3.opExtrude","SWEPT_BODY",BODY,{"disambiguationData":[OSD([sQuery(id+"F1.wireOp",EDGE,"E9.0.5.0")])]}),"instanceName":"39"});
            var Q214;
            Q214=makeQuery(id+"F61.opPattern","COPY",BODY,{"derivedFrom":makeQuery(id+"F3.opExtrude","SWEPT_BODY",BODY,{"disambiguationData":[OSD([sQuery(id+"F1.wireOp",EDGE,"E9.0.4.0")])]}),"instanceName":"39"});
            var Q215;
            Q215=makeQuery(id+"F58.opPattern","COPY",BODY,{"derivedFrom":makeQuery(id+"F3.opExtrude","SWEPT_BODY",BODY,{"disambiguationData":[OSD([sQuery(id+"F1.wireOp",EDGE,"E9.0.10.0")])]}),"instanceName":"26"});
            var Q216;
            Q216=makeQuery(id+"F59.opPattern","COPY",BODY,{"derivedFrom":makeQuery(id+"F3.opExtrude","SWEPT_BODY",BODY,{"disambiguationData":[OSD([sQuery(id+"F1.wireOp",EDGE,"E9.0.8.0")])]}),"instanceName":"34"});
            var Q217;
            Q217=makeQuery(id+"F61.opPattern","COPY",BODY,{"derivedFrom":makeQuery(id+"F3.opExtrude","SWEPT_BODY",BODY,{"disambiguationData":[OSD([sQuery(id+"F1.wireOp",EDGE,"E9.0.5.0")])]}),"instanceName":"41"});
            var Q218;
            Q218=makeQuery(id+"F59.opPattern","COPY",BODY,{"derivedFrom":makeQuery(id+"F3.opExtrude","SWEPT_BODY",BODY,{"disambiguationData":[OSD([sQuery(id+"F1.wireOp",EDGE,"E9.0.8.0")])]}),"instanceName":"35"});
            var Q219;
            Q219=makeQuery(id+"F61.opPattern","COPY",BODY,{"derivedFrom":makeQuery(id+"F3.opExtrude","SWEPT_BODY",BODY,{"disambiguationData":[OSD([sQuery(id+"F1.wireOp",EDGE,"E9.0.5.0")])]}),"instanceName":"24"});
            var Q220;
            Q220=makeQuery(id+"F61.opPattern","COPY",BODY,{"derivedFrom":makeQuery(id+"F3.opExtrude","SWEPT_BODY",BODY,{"disambiguationData":[OSD([sQuery(id+"F1.wireOp",EDGE,"E9.0.4.0")])]}),"instanceName":"41"});
            var Q221;
            Q221=makeQuery(id+"F58.opPattern","COPY",BODY,{"derivedFrom":makeQuery(id+"F3.opExtrude","SWEPT_BODY",BODY,{"disambiguationData":[OSD([sQuery(id+"F1.wireOp",EDGE,"E9.0.9.0")])]}),"instanceName":"26"});
            var Q222;
            Q222=makeQuery(id+"F61.opPattern","COPY",BODY,{"derivedFrom":makeQuery(id+"F3.opExtrude","SWEPT_BODY",BODY,{"disambiguationData":[OSD([sQuery(id+"F1.wireOp",EDGE,"E9.0.4.0")])]}),"instanceName":"24"});
            var Q223;
            Q223=makeQuery(id+"F60.opPattern","COPY",BODY,{"derivedFrom":makeQuery(id+"F3.opExtrude","SWEPT_BODY",BODY,{"disambiguationData":[OSD([sQuery(id+"F1.wireOp",EDGE,"E9.0.7.0")])]}),"instanceName":"44"});
            var Q224;
            Q224=makeQuery(id+"F61.opPattern","COPY",BODY,{"derivedFrom":makeQuery(id+"F3.opExtrude","SWEPT_BODY",BODY,{"disambiguationData":[OSD([sQuery(id+"F1.wireOp",EDGE,"E9.0.5.0")])]}),"instanceName":"38"});
            var Q225;
            Q225=makeQuery(id+"F59.opPattern","COPY",BODY,{"derivedFrom":makeQuery(id+"F3.opExtrude","SWEPT_BODY",BODY,{"disambiguationData":[OSD([sQuery(id+"F1.wireOp",EDGE,"E9.0.8.0")])]}),"instanceName":"36"});
            var Q226;
            Q226=makeQuery(id+"F59.opPattern","COPY",BODY,{"derivedFrom":makeQuery(id+"F3.opExtrude","SWEPT_BODY",BODY,{"disambiguationData":[OSD([sQuery(id+"F1.wireOp",EDGE,"E9.0.8.0")])]}),"instanceName":"37"});
            var Q227;
            Q227=makeQuery(id+"F61.opPattern","COPY",BODY,{"derivedFrom":makeQuery(id+"F3.opExtrude","SWEPT_BODY",BODY,{"disambiguationData":[OSD([sQuery(id+"F1.wireOp",EDGE,"E9.0.5.0")])]}),"instanceName":"23"});
            var Q228;
            Q228=makeQuery(id+"F60.opPattern","COPY",BODY,{"derivedFrom":makeQuery(id+"F3.opExtrude","SWEPT_BODY",BODY,{"disambiguationData":[OSD([sQuery(id+"F1.wireOp",EDGE,"E9.0.6.0")])]}),"instanceName":"45"});
            var Q229;
            Q229=makeQuery(id+"F61.opPattern","COPY",BODY,{"derivedFrom":makeQuery(id+"F3.opExtrude","SWEPT_BODY",BODY,{"disambiguationData":[OSD([sQuery(id+"F1.wireOp",EDGE,"E9.0.4.0")])]}),"instanceName":"38"});
            var Q230;
            Q230=makeQuery(id+"F61.opPattern","COPY",BODY,{"derivedFrom":makeQuery(id+"F3.opExtrude","SWEPT_BODY",BODY,{"disambiguationData":[OSD([sQuery(id+"F1.wireOp",EDGE,"E9.0.5.0")])]}),"instanceName":"37"});
            var Q231;
            Q231=makeQuery(id+"F58.opPattern","COPY",BODY,{"derivedFrom":makeQuery(id+"F3.opExtrude","SWEPT_BODY",BODY,{"disambiguationData":[OSD([sQuery(id+"F1.wireOp",EDGE,"E9.0.10.0")])]}),"instanceName":"15"});
            var Q232;
            Q232=makeQuery(id+"F58.opPattern","COPY",BODY,{"derivedFrom":makeQuery(id+"F3.opExtrude","SWEPT_BODY",BODY,{"disambiguationData":[OSD([sQuery(id+"F1.wireOp",EDGE,"E9.0.9.0")])]}),"instanceName":"6"});
            var Q233;
            Q233=makeQuery(id+"F58.opPattern","COPY",BODY,{"derivedFrom":makeQuery(id+"F3.opExtrude","SWEPT_BODY",BODY,{"disambiguationData":[OSD([sQuery(id+"F1.wireOp",EDGE,"E9.0.10.0")])]}),"instanceName":"25"});
            var Q234;
            Q234=makeQuery(id+"F58.opPattern","COPY",BODY,{"derivedFrom":makeQuery(id+"F3.opExtrude","SWEPT_BODY",BODY,{"disambiguationData":[OSD([sQuery(id+"F1.wireOp",EDGE,"E9.0.9.0")])]}),"instanceName":"16"});
            var Q235;
            Q235=makeQuery(id+"F58.opPattern","COPY",BODY,{"derivedFrom":makeQuery(id+"F3.opExtrude","SWEPT_BODY",BODY,{"disambiguationData":[OSD([sQuery(id+"F1.wireOp",EDGE,"E9.0.10.0")])]}),"instanceName":"6"});
            var Q236;
            Q236=makeQuery(id+"F59.opPattern","COPY",BODY,{"derivedFrom":makeQuery(id+"F3.opExtrude","SWEPT_BODY",BODY,{"disambiguationData":[OSD([sQuery(id+"F1.wireOp",EDGE,"E9.0.8.0")])]}),"instanceName":"38"});
            var Q237;
            Q237=makeQuery(id+"F61.opPattern","COPY",BODY,{"derivedFrom":makeQuery(id+"F3.opExtrude","SWEPT_BODY",BODY,{"disambiguationData":[OSD([sQuery(id+"F1.wireOp",EDGE,"E9.0.4.0")])]}),"instanceName":"23"});
            var Q238;
            Q238=makeQuery(id+"F58.opPattern","COPY",BODY,{"derivedFrom":makeQuery(id+"F3.opExtrude","SWEPT_BODY",BODY,{"disambiguationData":[OSD([sQuery(id+"F1.wireOp",EDGE,"E9.0.9.0")])]}),"instanceName":"40"});
            var Q239;
            Q239=makeQuery(id+"F60.opPattern","COPY",BODY,{"derivedFrom":makeQuery(id+"F3.opExtrude","SWEPT_BODY",BODY,{"disambiguationData":[OSD([sQuery(id+"F1.wireOp",EDGE,"E9.0.7.0")])]}),"instanceName":"48"});
            var Q240;
            Q240=makeQuery(id+"F58.opPattern","COPY",BODY,{"derivedFrom":makeQuery(id+"F3.opExtrude","SWEPT_BODY",BODY,{"disambiguationData":[OSD([sQuery(id+"F1.wireOp",EDGE,"E9.0.10.0")])]}),"instanceName":"40"});
            var Q241;
            Q241=makeQuery(id+"F59.opPattern","COPY",BODY,{"derivedFrom":makeQuery(id+"F3.opExtrude","SWEPT_BODY",BODY,{"disambiguationData":[OSD([sQuery(id+"F1.wireOp",EDGE,"E9.0.8.0")])]}),"instanceName":"39"});
            var Q242;
            Q242=makeQuery(id+"F61.opPattern","COPY",BODY,{"derivedFrom":makeQuery(id+"F3.opExtrude","SWEPT_BODY",BODY,{"disambiguationData":[OSD([sQuery(id+"F1.wireOp",EDGE,"E9.0.5.0")])]}),"instanceName":"22"});
            var Q243;
            Q243=makeQuery(id+"F58.opPattern","COPY",BODY,{"derivedFrom":makeQuery(id+"F3.opExtrude","SWEPT_BODY",BODY,{"disambiguationData":[OSD([sQuery(id+"F1.wireOp",EDGE,"E9.0.9.0")])]}),"instanceName":"25"});
            var Q244;
            Q244=makeQuery(id+"F61.opPattern","COPY",BODY,{"derivedFrom":makeQuery(id+"F3.opExtrude","SWEPT_BODY",BODY,{"disambiguationData":[OSD([sQuery(id+"F1.wireOp",EDGE,"E9.0.4.0")])]}),"instanceName":"8"});
            var Q245;
            Q245=makeQuery(id+"F58.opPattern","COPY",BODY,{"derivedFrom":makeQuery(id+"F3.opExtrude","SWEPT_BODY",BODY,{"disambiguationData":[OSD([sQuery(id+"F1.wireOp",EDGE,"E9.0.9.0")])]}),"instanceName":"41"});
            var Q246;
            Q246=makeQuery(id+"F58.opPattern","COPY",BODY,{"derivedFrom":makeQuery(id+"F3.opExtrude","SWEPT_BODY",BODY,{"disambiguationData":[OSD([sQuery(id+"F1.wireOp",EDGE,"E9.0.10.0")])]}),"instanceName":"24"});
            var Q247;
            Q247=makeQuery(id+"F59.opPattern","COPY",BODY,{"derivedFrom":makeQuery(id+"F3.opExtrude","SWEPT_BODY",BODY,{"disambiguationData":[OSD([sQuery(id+"F1.wireOp",EDGE,"E9.0.8.0")])]}),"instanceName":"40"});
            var Q248;
            Q248=makeQuery(id+"F61.opPattern","COPY",BODY,{"derivedFrom":makeQuery(id+"F3.opExtrude","SWEPT_BODY",BODY,{"disambiguationData":[OSD([sQuery(id+"F1.wireOp",EDGE,"E9.0.5.0")])]}),"instanceName":"7"});
            var Q249;
            Q249=makeQuery(id+"F59.opPattern","COPY",BODY,{"derivedFrom":makeQuery(id+"F3.opExtrude","SWEPT_BODY",BODY,{"disambiguationData":[OSD([sQuery(id+"F1.wireOp",EDGE,"E9.0.8.0")])]}),"instanceName":"41"});
            var Q250;
            Q250=makeQuery(id+"F58.opPattern","COPY",BODY,{"derivedFrom":makeQuery(id+"F3.opExtrude","SWEPT_BODY",BODY,{"disambiguationData":[OSD([sQuery(id+"F1.wireOp",EDGE,"E9.0.10.0")])]}),"instanceName":"41"});
            var Q251;
            Q251=makeQuery(id+"F59.opPattern","COPY",BODY,{"derivedFrom":makeQuery(id+"F3.opExtrude","SWEPT_BODY",BODY,{"disambiguationData":[OSD([sQuery(id+"F1.wireOp",EDGE,"E9.0.8.0")])]}),"instanceName":"19"});
            var Q252;
            Q252=makeQuery(id+"F58.opPattern","COPY",BODY,{"derivedFrom":makeQuery(id+"F3.opExtrude","SWEPT_BODY",BODY,{"disambiguationData":[OSD([sQuery(id+"F1.wireOp",EDGE,"E9.0.9.0")])]}),"instanceName":"24"});
            var Q253;
            Q253=makeQuery(id+"F58.opPattern","COPY",BODY,{"derivedFrom":makeQuery(id+"F3.opExtrude","SWEPT_BODY",BODY,{"disambiguationData":[OSD([sQuery(id+"F1.wireOp",EDGE,"E9.0.10.0")])]}),"instanceName":"23"});
            var Q254;
            Q254=makeQuery(id+"F58.opPattern","COPY",BODY,{"derivedFrom":makeQuery(id+"F3.opExtrude","SWEPT_BODY",BODY,{"disambiguationData":[OSD([sQuery(id+"F1.wireOp",EDGE,"E9.0.9.0")])]}),"instanceName":"7"});
            var Q255;
            Q255=makeQuery(id+"F58.opPattern","COPY",BODY,{"derivedFrom":makeQuery(id+"F3.opExtrude","SWEPT_BODY",BODY,{"disambiguationData":[OSD([sQuery(id+"F1.wireOp",EDGE,"E9.0.10.0")])]}),"instanceName":"7"});
            var Q256;
            Q256=makeQuery(id+"F59.opPattern","COPY",BODY,{"derivedFrom":makeQuery(id+"F3.opExtrude","SWEPT_BODY",BODY,{"disambiguationData":[OSD([sQuery(id+"F1.wireOp",EDGE,"E9.0.8.0")])]}),"instanceName":"42"});
            var Q257;
            Q257=makeQuery(id+"F58.opPattern","COPY",BODY,{"derivedFrom":makeQuery(id+"F3.opExtrude","SWEPT_BODY",BODY,{"disambiguationData":[OSD([sQuery(id+"F1.wireOp",EDGE,"E9.0.9.0")])]}),"instanceName":"8"});
            var Q258;
            Q258=makeQuery(id+"F58.opPattern","COPY",BODY,{"derivedFrom":makeQuery(id+"F3.opExtrude","SWEPT_BODY",BODY,{"disambiguationData":[OSD([sQuery(id+"F1.wireOp",EDGE,"E9.0.9.0")])]}),"instanceName":"23"});
            var Q259;
            Q259=makeQuery(id+"F61.opPattern","COPY",BODY,{"derivedFrom":makeQuery(id+"F3.opExtrude","SWEPT_BODY",BODY,{"disambiguationData":[OSD([sQuery(id+"F1.wireOp",EDGE,"E9.0.4.0")])]}),"instanceName":"7"});
            var Q260;
            Q260=makeQuery(id+"F60.opPattern","COPY",BODY,{"derivedFrom":makeQuery(id+"F3.opExtrude","SWEPT_BODY",BODY,{"disambiguationData":[OSD([sQuery(id+"F1.wireOp",EDGE,"E9.0.7.0")])]}),"instanceName":"39"});
            var Q261;
            Q261=makeQuery(id+"F59.opPattern","COPY",BODY,{"derivedFrom":makeQuery(id+"F3.opExtrude","SWEPT_BODY",BODY,{"disambiguationData":[OSD([sQuery(id+"F1.wireOp",EDGE,"E9.0.8.0")])]}),"instanceName":"43"});
            var Q262;
            Q262=makeQuery(id+"F58.opPattern","COPY",BODY,{"derivedFrom":makeQuery(id+"F3.opExtrude","SWEPT_BODY",BODY,{"disambiguationData":[OSD([sQuery(id+"F1.wireOp",EDGE,"E9.0.10.0")])]}),"instanceName":"19"});
            var Q263;
            Q263=makeQuery(id+"F61.opPattern","COPY",BODY,{"derivedFrom":makeQuery(id+"F3.opExtrude","SWEPT_BODY",BODY,{"disambiguationData":[OSD([sQuery(id+"F1.wireOp",EDGE,"E9.0.4.0")])]}),"instanceName":"22"});
            var Q264;
            Q264=makeQuery(id+"F59.opPattern","COPY",BODY,{"derivedFrom":makeQuery(id+"F3.opExtrude","SWEPT_BODY",BODY,{"disambiguationData":[OSD([sQuery(id+"F1.wireOp",EDGE,"E9.0.8.0")])]}),"instanceName":"14"});
            var Q265;
            Q265=makeQuery(id+"F58.opPattern","COPY",BODY,{"derivedFrom":makeQuery(id+"F3.opExtrude","SWEPT_BODY",BODY,{"disambiguationData":[OSD([sQuery(id+"F1.wireOp",EDGE,"E9.0.9.0")])]}),"instanceName":"19"});
            var Q266;
            Q266=makeQuery(id+"F58.opPattern","COPY",BODY,{"derivedFrom":makeQuery(id+"F3.opExtrude","SWEPT_BODY",BODY,{"disambiguationData":[OSD([sQuery(id+"F1.wireOp",EDGE,"E9.0.10.0")])]}),"instanceName":"18"});
            var Q267;
            Q267=makeQuery(id+"F61.opPattern","COPY",BODY,{"derivedFrom":makeQuery(id+"F3.opExtrude","SWEPT_BODY",BODY,{"disambiguationData":[OSD([sQuery(id+"F1.wireOp",EDGE,"E9.0.5.0")])]}),"instanceName":"21"});
            var Q268;
            Q268=makeQuery(id+"F59.opPattern","COPY",BODY,{"derivedFrom":makeQuery(id+"F3.opExtrude","SWEPT_BODY",BODY,{"disambiguationData":[OSD([sQuery(id+"F1.wireOp",EDGE,"E9.0.8.0")])]}),"instanceName":"21"});
            var Q269;
            Q269=makeQuery(id+"F58.opPattern","COPY",BODY,{"derivedFrom":makeQuery(id+"F3.opExtrude","SWEPT_BODY",BODY,{"disambiguationData":[OSD([sQuery(id+"F1.wireOp",EDGE,"E9.0.10.0")])]}),"instanceName":"16"});
            var Q270;
            Q270=makeQuery(id+"F59.opPattern","COPY",BODY,{"derivedFrom":makeQuery(id+"F3.opExtrude","SWEPT_BODY",BODY,{"disambiguationData":[OSD([sQuery(id+"F1.wireOp",EDGE,"E9.0.8.0")])]}),"instanceName":"44"});
            var Q271;
            Q271=makeQuery(id+"F61.opPattern","COPY",BODY,{"derivedFrom":makeQuery(id+"F3.opExtrude","SWEPT_BODY",BODY,{"disambiguationData":[OSD([sQuery(id+"F1.wireOp",EDGE,"E9.0.5.0")])]}),"instanceName":"44"});
            var Q272;
            Q272=makeQuery(id+"F58.opPattern","COPY",BODY,{"derivedFrom":makeQuery(id+"F3.opExtrude","SWEPT_BODY",BODY,{"disambiguationData":[OSD([sQuery(id+"F1.wireOp",EDGE,"E9.0.9.0")])]}),"instanceName":"42"});
            var Q273;
            Q273=makeQuery(id+"F60.opPattern","COPY",BODY,{"derivedFrom":makeQuery(id+"F3.opExtrude","SWEPT_BODY",BODY,{"disambiguationData":[OSD([sQuery(id+"F1.wireOp",EDGE,"E9.0.7.0")])]}),"instanceName":"17"});
            var Q274;
            Q274=makeQuery(id+"F59.opPattern","COPY",BODY,{"derivedFrom":makeQuery(id+"F3.opExtrude","SWEPT_BODY",BODY,{"disambiguationData":[OSD([sQuery(id+"F1.wireOp",EDGE,"E9.0.8.0")])]}),"instanceName":"45"});
            var Q275;
            Q275=makeQuery(id+"F60.opPattern","COPY",BODY,{"derivedFrom":makeQuery(id+"F3.opExtrude","SWEPT_BODY",BODY,{"disambiguationData":[OSD([sQuery(id+"F1.wireOp",EDGE,"E9.0.6.0")])]}),"instanceName":"17"});
            var Q276;
            Q276=makeQuery(id+"F58.opPattern","COPY",BODY,{"derivedFrom":makeQuery(id+"F3.opExtrude","SWEPT_BODY",BODY,{"disambiguationData":[OSD([sQuery(id+"F1.wireOp",EDGE,"E9.0.10.0")])]}),"instanceName":"42"});
            var Q277;
            Q277=makeQuery(id+"F58.opPattern","COPY",BODY,{"derivedFrom":makeQuery(id+"F3.opExtrude","SWEPT_BODY",BODY,{"disambiguationData":[OSD([sQuery(id+"F1.wireOp",EDGE,"E9.0.10.0")])]}),"instanceName":"8"});
            var Q278;
            Q278=makeQuery(id+"F61.opPattern","COPY",BODY,{"derivedFrom":makeQuery(id+"F3.opExtrude","SWEPT_BODY",BODY,{"disambiguationData":[OSD([sQuery(id+"F1.wireOp",EDGE,"E9.0.4.0")])]}),"instanceName":"21"});
            var Q279;
            Q279=makeQuery(id+"F58.opPattern","COPY",BODY,{"derivedFrom":makeQuery(id+"F3.opExtrude","SWEPT_BODY",BODY,{"disambiguationData":[OSD([sQuery(id+"F1.wireOp",EDGE,"E9.0.9.0")])]}),"instanceName":"43"});
            var Q280;
            Q280=makeQuery(id+"F61.opPattern","COPY",BODY,{"derivedFrom":makeQuery(id+"F3.opExtrude","SWEPT_BODY",BODY,{"disambiguationData":[OSD([sQuery(id+"F1.wireOp",EDGE,"E9.0.4.0")])]}),"instanceName":"37"});
            var Q281;
            Q281=makeQuery(id+"F61.opPattern","COPY",BODY,{"derivedFrom":makeQuery(id+"F3.opExtrude","SWEPT_BODY",BODY,{"disambiguationData":[OSD([sQuery(id+"F1.wireOp",EDGE,"E9.0.5.0")])]}),"instanceName":"36"});
            var Q282;
            Q282=makeQuery(id+"F60.opPattern","COPY",BODY,{"derivedFrom":makeQuery(id+"F3.opExtrude","SWEPT_BODY",BODY,{"disambiguationData":[OSD([sQuery(id+"F1.wireOp",EDGE,"E9.0.7.0")])]}),"instanceName":"16"});
            var Q283;
            Q283=makeQuery(id+"F58.opPattern","COPY",BODY,{"derivedFrom":makeQuery(id+"F3.opExtrude","SWEPT_BODY",BODY,{"disambiguationData":[OSD([sQuery(id+"F1.wireOp",EDGE,"E9.0.10.0")])]}),"instanceName":"17"});
            var Q284;
            Q284=makeQuery(id+"F58.opPattern","COPY",BODY,{"derivedFrom":makeQuery(id+"F3.opExtrude","SWEPT_BODY",BODY,{"disambiguationData":[OSD([sQuery(id+"F1.wireOp",EDGE,"E9.0.9.0")])]}),"instanceName":"17"});
            var Q285;
            Q285=makeQuery(id+"F58.opPattern","COPY",BODY,{"derivedFrom":makeQuery(id+"F3.opExtrude","SWEPT_BODY",BODY,{"disambiguationData":[OSD([sQuery(id+"F1.wireOp",EDGE,"E9.0.9.0")])]}),"instanceName":"9"});
            var Q286;
            Q286=makeQuery(id+"F58.opPattern","COPY",BODY,{"derivedFrom":makeQuery(id+"F3.opExtrude","SWEPT_BODY",BODY,{"disambiguationData":[OSD([sQuery(id+"F1.wireOp",EDGE,"E9.0.9.0")])]}),"instanceName":"39"});
            var Q287;
            Q287=makeQuery(id+"F58.opPattern","COPY",BODY,{"derivedFrom":makeQuery(id+"F3.opExtrude","SWEPT_BODY",BODY,{"disambiguationData":[OSD([sQuery(id+"F1.wireOp",EDGE,"E9.0.10.0")])]}),"instanceName":"38"});
            var Q288;
            Q288=makeQuery(id+"F60.opPattern","COPY",BODY,{"derivedFrom":makeQuery(id+"F3.opExtrude","SWEPT_BODY",BODY,{"disambiguationData":[OSD([sQuery(id+"F1.wireOp",EDGE,"E9.0.7.0")])]}),"instanceName":"20"});
            var Q289;
            Q289=makeQuery(id+"F58.opPattern","COPY",BODY,{"derivedFrom":makeQuery(id+"F3.opExtrude","SWEPT_BODY",BODY,{"disambiguationData":[OSD([sQuery(id+"F1.wireOp",EDGE,"E9.0.9.0")])]}),"instanceName":"38"});
            var Q290;
            Q290=makeQuery(id+"F60.opPattern","COPY",BODY,{"derivedFrom":makeQuery(id+"F3.opExtrude","SWEPT_BODY",BODY,{"disambiguationData":[OSD([sQuery(id+"F1.wireOp",EDGE,"E9.0.7.0")])]}),"instanceName":"45"});
            var Q291;
            Q291=makeQuery(id+"F58.opPattern","COPY",BODY,{"derivedFrom":makeQuery(id+"F3.opExtrude","SWEPT_BODY",BODY,{"disambiguationData":[OSD([sQuery(id+"F1.wireOp",EDGE,"E9.0.9.0")])]}),"instanceName":"36"});
            var Q292;
            Q292=makeQuery(id+"F60.opPattern","COPY",BODY,{"derivedFrom":makeQuery(id+"F3.opExtrude","SWEPT_BODY",BODY,{"disambiguationData":[OSD([sQuery(id+"F1.wireOp",EDGE,"E9.0.6.0")])]}),"instanceName":"46"});
            var Q293;
            Q293=makeQuery(id+"F60.opPattern","COPY",BODY,{"derivedFrom":makeQuery(id+"F3.opExtrude","SWEPT_BODY",BODY,{"disambiguationData":[OSD([sQuery(id+"F1.wireOp",EDGE,"E9.0.7.0")])]}),"instanceName":"46"});
            var Q294;
            Q294=makeQuery(id+"F60.opPattern","COPY",BODY,{"derivedFrom":makeQuery(id+"F3.opExtrude","SWEPT_BODY",BODY,{"disambiguationData":[OSD([sQuery(id+"F1.wireOp",EDGE,"E9.0.6.0")])]}),"instanceName":"18"});
            var Q295;
            Q295=makeQuery(id+"F59.opPattern","COPY",BODY,{"derivedFrom":makeQuery(id+"F3.opExtrude","SWEPT_BODY",BODY,{"disambiguationData":[OSD([sQuery(id+"F1.wireOp",EDGE,"E9.0.8.0")])]}),"instanceName":"7"});
            var Q296;
            Q296=makeQuery(id+"F61.opPattern","COPY",BODY,{"derivedFrom":makeQuery(id+"F3.opExtrude","SWEPT_BODY",BODY,{"disambiguationData":[OSD([sQuery(id+"F1.wireOp",EDGE,"E9.0.5.0")])]}),"instanceName":"43"});
            var Q297;
            Q297=makeQuery(id+"F59.opPattern","COPY",BODY,{"derivedFrom":makeQuery(id+"F3.opExtrude","SWEPT_BODY",BODY,{"disambiguationData":[OSD([sQuery(id+"F1.wireOp",EDGE,"E9.0.8.0")])]}),"instanceName":"12"});
            var Q298;
            Q298=makeQuery(id+"F60.opPattern","COPY",BODY,{"derivedFrom":makeQuery(id+"F3.opExtrude","SWEPT_BODY",BODY,{"disambiguationData":[OSD([sQuery(id+"F1.wireOp",EDGE,"E9.0.6.0")])]}),"instanceName":"48"});
            var Q299;
            Q299=makeQuery(id+"F61.opPattern","COPY",BODY,{"derivedFrom":makeQuery(id+"F3.opExtrude","SWEPT_BODY",BODY,{"disambiguationData":[OSD([sQuery(id+"F1.wireOp",EDGE,"E9.0.5.0")])]}),"instanceName":"28"});
            var Q300;
            Q300=makeQuery(id+"F60.opPattern","COPY",BODY,{"derivedFrom":makeQuery(id+"F3.opExtrude","SWEPT_BODY",BODY,{"disambiguationData":[OSD([sQuery(id+"F1.wireOp",EDGE,"E9.0.7.0")])]}),"instanceName":"18"});
            var Q301;
            Q301=makeQuery(id+"F61.opPattern","COPY",BODY,{"derivedFrom":makeQuery(id+"F3.opExtrude","SWEPT_BODY",BODY,{"disambiguationData":[OSD([sQuery(id+"F1.wireOp",EDGE,"E9.0.4.0")])]}),"instanceName":"28"});
            var Q302;
            Q302=makeQuery(id+"F60.opPattern","COPY",BODY,{"derivedFrom":makeQuery(id+"F3.opExtrude","SWEPT_BODY",BODY,{"disambiguationData":[OSD([sQuery(id+"F1.wireOp",EDGE,"E9.0.6.0")])]}),"instanceName":"23"});
            var Q303;
            Q303=makeQuery(id+"F61.opPattern","COPY",BODY,{"derivedFrom":makeQuery(id+"F3.opExtrude","SWEPT_BODY",BODY,{"disambiguationData":[OSD([sQuery(id+"F1.wireOp",EDGE,"E9.0.5.0")])]}),"instanceName":"27"});
            var Q304;
            Q304=makeQuery(id+"F58.opPattern","COPY",BODY,{"derivedFrom":makeQuery(id+"F3.opExtrude","SWEPT_BODY",BODY,{"disambiguationData":[OSD([sQuery(id+"F1.wireOp",EDGE,"E9.0.10.0")])]}),"instanceName":"36"});
            var Q305;
            Q305=makeQuery(id+"F58.opPattern","COPY",BODY,{"derivedFrom":makeQuery(id+"F3.opExtrude","SWEPT_BODY",BODY,{"disambiguationData":[OSD([sQuery(id+"F1.wireOp",EDGE,"E9.0.9.0")])]}),"instanceName":"37"});
            var Q306;
            Q306=makeQuery(id+"F58.opPattern","COPY",BODY,{"derivedFrom":makeQuery(id+"F3.opExtrude","SWEPT_BODY",BODY,{"disambiguationData":[OSD([sQuery(id+"F1.wireOp",EDGE,"E9.0.10.0")])]}),"instanceName":"37"});
            var Q307;
            Q307=makeQuery(id+"F58.opPattern","COPY",BODY,{"derivedFrom":makeQuery(id+"F3.opExtrude","SWEPT_BODY",BODY,{"disambiguationData":[OSD([sQuery(id+"F1.wireOp",EDGE,"E9.0.10.0")])]}),"instanceName":"5"});
            var Q308;
            Q308=makeQuery(id+"F58.opPattern","COPY",BODY,{"derivedFrom":makeQuery(id+"F3.opExtrude","SWEPT_BODY",BODY,{"disambiguationData":[OSD([sQuery(id+"F1.wireOp",EDGE,"E9.0.10.0")])]}),"instanceName":"3"});
            var Q309;
            Q309=makeQuery(id+"F58.opPattern","COPY",BODY,{"derivedFrom":makeQuery(id+"F3.opExtrude","SWEPT_BODY",BODY,{"disambiguationData":[OSD([sQuery(id+"F1.wireOp",EDGE,"E9.0.9.0")])]}),"instanceName":"3"});
            var Q310;
            Q310=makeQuery(id+"F58.opPattern","COPY",BODY,{"derivedFrom":makeQuery(id+"F3.opExtrude","SWEPT_BODY",BODY,{"disambiguationData":[OSD([sQuery(id+"F1.wireOp",EDGE,"E9.0.10.0")])]}),"instanceName":"1"});
            var Q311;
            Q311=makeQuery(id+"F58.opPattern","COPY",BODY,{"derivedFrom":makeQuery(id+"F3.opExtrude","SWEPT_BODY",BODY,{"disambiguationData":[OSD([sQuery(id+"F1.wireOp",EDGE,"E9.0.9.0")])]}),"instanceName":"1"});
            var Q312;
            Q312=makeQuery(id+"F57.opPattern","COPY",BODY,{"derivedFrom":makeQuery(id+"F3.opExtrude","SWEPT_BODY",BODY,{"disambiguationData":[OSD([sQuery(id+"F1.wireOp",EDGE,"E9.0.11.0")])]}),"instanceName":"45"});
            var Q313;
            Q313=makeQuery(id+"F57.opPattern","COPY",BODY,{"derivedFrom":makeQuery(id+"F3.opExtrude","SWEPT_BODY",BODY,{"disambiguationData":[OSD([sQuery(id+"F1.wireOp",EDGE,"E9.0.11.0")])]}),"instanceName":"44"});
            var Q314;
            Q314=makeQuery(id+"F57.opPattern","COPY",BODY,{"derivedFrom":makeQuery(id+"F3.opExtrude","SWEPT_BODY",BODY,{"disambiguationData":[OSD([sQuery(id+"F1.wireOp",EDGE,"E9.0.11.0")])]}),"instanceName":"42"});
            var Q315;
            Q315=makeQuery(id+"F57.opPattern","COPY",BODY,{"derivedFrom":makeQuery(id+"F3.opExtrude","SWEPT_BODY",BODY,{"disambiguationData":[OSD([sQuery(id+"F1.wireOp",EDGE,"E9.0.11.0")])]}),"instanceName":"41"});
            var Q316;
            Q316=makeQuery(id+"F57.opPattern","COPY",BODY,{"derivedFrom":makeQuery(id+"F3.opExtrude","SWEPT_BODY",BODY,{"disambiguationData":[OSD([sQuery(id+"F1.wireOp",EDGE,"E9.0.11.0")])]}),"instanceName":"40"});
            var Q317;
            Q317=makeQuery(id+"F57.opPattern","COPY",BODY,{"derivedFrom":makeQuery(id+"F3.opExtrude","SWEPT_BODY",BODY,{"disambiguationData":[OSD([sQuery(id+"F1.wireOp",EDGE,"E9.0.11.0")])]}),"instanceName":"39"});
            var Q318;
            Q318=makeQuery(id+"F57.opPattern","COPY",BODY,{"derivedFrom":makeQuery(id+"F3.opExtrude","SWEPT_BODY",BODY,{"disambiguationData":[OSD([sQuery(id+"F1.wireOp",EDGE,"E9.0.11.0")])]}),"instanceName":"38"});
            var Q319;
            Q319=makeQuery(id+"F57.opPattern","COPY",BODY,{"derivedFrom":makeQuery(id+"F3.opExtrude","SWEPT_BODY",BODY,{"disambiguationData":[OSD([sQuery(id+"F1.wireOp",EDGE,"E9.0.11.0")])]}),"instanceName":"37"});
            var Q320;
            Q320=makeQuery(id+"F57.opPattern","COPY",BODY,{"derivedFrom":makeQuery(id+"F3.opExtrude","SWEPT_BODY",BODY,{"disambiguationData":[OSD([sQuery(id+"F1.wireOp",EDGE,"E9.0.11.0")])]}),"instanceName":"36"});
            var Q321;
            Q321=makeQuery(id+"F57.opPattern","COPY",BODY,{"derivedFrom":makeQuery(id+"F3.opExtrude","SWEPT_BODY",BODY,{"disambiguationData":[OSD([sQuery(id+"F1.wireOp",EDGE,"E9.0.11.0")])]}),"instanceName":"35"});
            var Q322;
            Q322=makeQuery(id+"F57.opPattern","COPY",BODY,{"derivedFrom":makeQuery(id+"F3.opExtrude","SWEPT_BODY",BODY,{"disambiguationData":[OSD([sQuery(id+"F1.wireOp",EDGE,"E9.0.11.0")])]}),"instanceName":"34"});
            var Q323;
            Q323=makeQuery(id+"F57.opPattern","COPY",BODY,{"derivedFrom":makeQuery(id+"F3.opExtrude","SWEPT_BODY",BODY,{"disambiguationData":[OSD([sQuery(id+"F1.wireOp",EDGE,"E9.0.11.0")])]}),"instanceName":"33"});
            var Q324;
            Q324=makeQuery(id+"F57.opPattern","COPY",BODY,{"derivedFrom":makeQuery(id+"F3.opExtrude","SWEPT_BODY",BODY,{"disambiguationData":[OSD([sQuery(id+"F1.wireOp",EDGE,"E9.0.11.0")])]}),"instanceName":"32"});
            var Q325;
            Q325=makeQuery(id+"F57.opPattern","COPY",BODY,{"derivedFrom":makeQuery(id+"F3.opExtrude","SWEPT_BODY",BODY,{"disambiguationData":[OSD([sQuery(id+"F1.wireOp",EDGE,"E9.0.11.0")])]}),"instanceName":"31"});
            var Q326;
            Q326=makeQuery(id+"F57.opPattern","COPY",BODY,{"derivedFrom":makeQuery(id+"F3.opExtrude","SWEPT_BODY",BODY,{"disambiguationData":[OSD([sQuery(id+"F1.wireOp",EDGE,"E9.0.11.0")])]}),"instanceName":"30"});
            var Q327;
            Q327=makeQuery(id+"F57.opPattern","COPY",BODY,{"derivedFrom":makeQuery(id+"F3.opExtrude","SWEPT_BODY",BODY,{"disambiguationData":[OSD([sQuery(id+"F1.wireOp",EDGE,"E9.0.11.0")])]}),"instanceName":"29"});
            var Q328;
            Q328=makeQuery(id+"F57.opPattern","COPY",BODY,{"derivedFrom":makeQuery(id+"F3.opExtrude","SWEPT_BODY",BODY,{"disambiguationData":[OSD([sQuery(id+"F1.wireOp",EDGE,"E9.0.11.0")])]}),"instanceName":"28"});
            var Q329;
            Q329=makeQuery(id+"F57.opPattern","COPY",BODY,{"derivedFrom":makeQuery(id+"F3.opExtrude","SWEPT_BODY",BODY,{"disambiguationData":[OSD([sQuery(id+"F1.wireOp",EDGE,"E9.0.11.0")])]}),"instanceName":"27"});
            var Q330;
            Q330=makeQuery(id+"F57.opPattern","COPY",BODY,{"derivedFrom":makeQuery(id+"F3.opExtrude","SWEPT_BODY",BODY,{"disambiguationData":[OSD([sQuery(id+"F1.wireOp",EDGE,"E9.0.11.0")])]}),"instanceName":"26"});
            var Q331;
            Q331=makeQuery(id+"F57.opPattern","COPY",BODY,{"derivedFrom":makeQuery(id+"F3.opExtrude","SWEPT_BODY",BODY,{"disambiguationData":[OSD([sQuery(id+"F1.wireOp",EDGE,"E9.0.11.0")])]}),"instanceName":"25"});
            var Q332;
            Q332=makeQuery(id+"F57.opPattern","COPY",BODY,{"derivedFrom":makeQuery(id+"F3.opExtrude","SWEPT_BODY",BODY,{"disambiguationData":[OSD([sQuery(id+"F1.wireOp",EDGE,"E9.0.11.0")])]}),"instanceName":"24"});
            var Q333;
            Q333=makeQuery(id+"F57.opPattern","COPY",BODY,{"derivedFrom":makeQuery(id+"F3.opExtrude","SWEPT_BODY",BODY,{"disambiguationData":[OSD([sQuery(id+"F1.wireOp",EDGE,"E9.0.11.0")])]}),"instanceName":"23"});
            var Q334;
            Q334=makeQuery(id+"F57.opPattern","COPY",BODY,{"derivedFrom":makeQuery(id+"F3.opExtrude","SWEPT_BODY",BODY,{"disambiguationData":[OSD([sQuery(id+"F1.wireOp",EDGE,"E9.0.11.0")])]}),"instanceName":"22"});
            var Q335;
            Q335=makeQuery(id+"F57.opPattern","COPY",BODY,{"derivedFrom":makeQuery(id+"F3.opExtrude","SWEPT_BODY",BODY,{"disambiguationData":[OSD([sQuery(id+"F1.wireOp",EDGE,"E9.0.11.0")])]}),"instanceName":"21"});
            var Q336;
            Q336=makeQuery(id+"F57.opPattern","COPY",BODY,{"derivedFrom":makeQuery(id+"F3.opExtrude","SWEPT_BODY",BODY,{"disambiguationData":[OSD([sQuery(id+"F1.wireOp",EDGE,"E9.0.11.0")])]}),"instanceName":"20"});
            var Q337;
            Q337=makeQuery(id+"F57.opPattern","COPY",BODY,{"derivedFrom":makeQuery(id+"F3.opExtrude","SWEPT_BODY",BODY,{"disambiguationData":[OSD([sQuery(id+"F1.wireOp",EDGE,"E9.0.11.0")])]}),"instanceName":"19"});
            var Q338;
            Q338=makeQuery(id+"F57.opPattern","COPY",BODY,{"derivedFrom":makeQuery(id+"F3.opExtrude","SWEPT_BODY",BODY,{"disambiguationData":[OSD([sQuery(id+"F1.wireOp",EDGE,"E9.0.11.0")])]}),"instanceName":"18"});
            var Q339;
            Q339=makeQuery(id+"F57.opPattern","COPY",BODY,{"derivedFrom":makeQuery(id+"F3.opExtrude","SWEPT_BODY",BODY,{"disambiguationData":[OSD([sQuery(id+"F1.wireOp",EDGE,"E9.0.11.0")])]}),"instanceName":"17"});
            var Q340;
            Q340=makeQuery(id+"F57.opPattern","COPY",BODY,{"derivedFrom":makeQuery(id+"F3.opExtrude","SWEPT_BODY",BODY,{"disambiguationData":[OSD([sQuery(id+"F1.wireOp",EDGE,"E9.0.11.0")])]}),"instanceName":"16"});
            var Q341;
            Q341=makeQuery(id+"F57.opPattern","COPY",BODY,{"derivedFrom":makeQuery(id+"F3.opExtrude","SWEPT_BODY",BODY,{"disambiguationData":[OSD([sQuery(id+"F1.wireOp",EDGE,"E9.0.11.0")])]}),"instanceName":"15"});
            var Q342;
            Q342=makeQuery(id+"F57.opPattern","COPY",BODY,{"derivedFrom":makeQuery(id+"F3.opExtrude","SWEPT_BODY",BODY,{"disambiguationData":[OSD([sQuery(id+"F1.wireOp",EDGE,"E9.0.11.0")])]}),"instanceName":"14"});
            var Q343;
            Q343=makeQuery(id+"F57.opPattern","COPY",BODY,{"derivedFrom":makeQuery(id+"F3.opExtrude","SWEPT_BODY",BODY,{"disambiguationData":[OSD([sQuery(id+"F1.wireOp",EDGE,"E9.0.11.0")])]}),"instanceName":"13"});
            var Q344;
            Q344=makeQuery(id+"F57.opPattern","COPY",BODY,{"derivedFrom":makeQuery(id+"F3.opExtrude","SWEPT_BODY",BODY,{"disambiguationData":[OSD([sQuery(id+"F1.wireOp",EDGE,"E9.0.11.0")])]}),"instanceName":"12"});
            var Q345;
            Q345=makeQuery(id+"F57.opPattern","COPY",BODY,{"derivedFrom":makeQuery(id+"F3.opExtrude","SWEPT_BODY",BODY,{"disambiguationData":[OSD([sQuery(id+"F1.wireOp",EDGE,"E9.0.11.0")])]}),"instanceName":"11"});
            var Q346;
            Q346=makeQuery(id+"F57.opPattern","COPY",BODY,{"derivedFrom":makeQuery(id+"F3.opExtrude","SWEPT_BODY",BODY,{"disambiguationData":[OSD([sQuery(id+"F1.wireOp",EDGE,"E9.0.11.0")])]}),"instanceName":"10"});
            var Q347;
            Q347=makeQuery(id+"F57.opPattern","COPY",BODY,{"derivedFrom":makeQuery(id+"F3.opExtrude","SWEPT_BODY",BODY,{"disambiguationData":[OSD([sQuery(id+"F1.wireOp",EDGE,"E9.0.11.0")])]}),"instanceName":"9"});
            var Q348;
            Q348=makeQuery(id+"F57.opPattern","COPY",BODY,{"derivedFrom":makeQuery(id+"F3.opExtrude","SWEPT_BODY",BODY,{"disambiguationData":[OSD([sQuery(id+"F1.wireOp",EDGE,"E9.0.11.0")])]}),"instanceName":"8"});
            var Q349;
            Q349=makeQuery(id+"F57.opPattern","COPY",BODY,{"derivedFrom":makeQuery(id+"F3.opExtrude","SWEPT_BODY",BODY,{"disambiguationData":[OSD([sQuery(id+"F1.wireOp",EDGE,"E9.0.11.0")])]}),"instanceName":"7"});
            var Q350;
            Q350=makeQuery(id+"F57.opPattern","COPY",BODY,{"derivedFrom":makeQuery(id+"F3.opExtrude","SWEPT_BODY",BODY,{"disambiguationData":[OSD([sQuery(id+"F1.wireOp",EDGE,"E9.0.11.0")])]}),"instanceName":"6"});
            var Q351;
            Q351=makeQuery(id+"F57.opPattern","COPY",BODY,{"derivedFrom":makeQuery(id+"F3.opExtrude","SWEPT_BODY",BODY,{"disambiguationData":[OSD([sQuery(id+"F1.wireOp",EDGE,"E9.0.11.0")])]}),"instanceName":"5"});
            var Q352;
            Q352=makeQuery(id+"F57.opPattern","COPY",BODY,{"derivedFrom":makeQuery(id+"F3.opExtrude","SWEPT_BODY",BODY,{"disambiguationData":[OSD([sQuery(id+"F1.wireOp",EDGE,"E9.0.11.0")])]}),"instanceName":"3"});
            var Q353;
            Q353=makeQuery(id+"F57.opPattern","COPY",BODY,{"derivedFrom":makeQuery(id+"F3.opExtrude","SWEPT_BODY",BODY,{"disambiguationData":[OSD([sQuery(id+"F1.wireOp",EDGE,"E9.0.11.0")])]}),"instanceName":"1"});
            var Q354;
            Q354=makeQuery(id+"F60.opPattern","COPY",BODY,{"derivedFrom":makeQuery(id+"F3.opExtrude","SWEPT_BODY",BODY,{"disambiguationData":[OSD([sQuery(id+"F1.wireOp",EDGE,"E9.0.6.0")])]}),"instanceName":"49"});
            var Q355;
            Q355=makeQuery(id+"F3.opExtrude","SWEPT_BODY",BODY,{"disambiguationData":[OSD([sQuery(id+"F1.wireOp",EDGE,"E9.0.9.0")])]});
            var Q356;
            Q356=makeQuery(id+"F60.opPattern","COPY",BODY,{"derivedFrom":makeQuery(id+"F3.opExtrude","SWEPT_BODY",BODY,{"disambiguationData":[OSD([sQuery(id+"F1.wireOp",EDGE,"E9.0.7.0")])]}),"instanceName":"49"});
            var Q357;
            Q357=makeQuery(id+"F58.opPattern","COPY",BODY,{"derivedFrom":makeQuery(id+"F3.opExtrude","SWEPT_BODY",BODY,{"disambiguationData":[OSD([sQuery(id+"F1.wireOp",EDGE,"E9.0.9.0")])]}),"instanceName":"45"});
            var Q358;
            Q358=makeQuery(id+"F58.opPattern","COPY",BODY,{"derivedFrom":makeQuery(id+"F3.opExtrude","SWEPT_BODY",BODY,{"disambiguationData":[OSD([sQuery(id+"F1.wireOp",EDGE,"E9.0.10.0")])]}),"instanceName":"45"});
            var Q359;
            Q359=makeQuery(id+"F60.opPattern","COPY",BODY,{"derivedFrom":makeQuery(id+"F3.opExtrude","SWEPT_BODY",BODY,{"disambiguationData":[OSD([sQuery(id+"F1.wireOp",EDGE,"E9.0.6.0")])]}),"instanceName":"47"});
            var Q360;
            Q360=makeQuery(id+"F3.opExtrude","SWEPT_BODY",BODY,{"disambiguationData":[OSD([sQuery(id+"F1.wireOp",EDGE,"E9.0.8.0")])]});
            var Q361;
            Q361=makeQuery(id+"F58.opPattern","COPY",BODY,{"derivedFrom":makeQuery(id+"F3.opExtrude","SWEPT_BODY",BODY,{"disambiguationData":[OSD([sQuery(id+"F1.wireOp",EDGE,"E9.0.9.0")])]}),"instanceName":"47"});
            var Q362;
            Q362=makeQuery(id+"F60.opPattern","COPY",BODY,{"derivedFrom":makeQuery(id+"F3.opExtrude","SWEPT_BODY",BODY,{"disambiguationData":[OSD([sQuery(id+"F1.wireOp",EDGE,"E9.0.7.0")])]}),"instanceName":"3"});
            var Q363;
            Q363=makeQuery(id+"F3.opExtrude","SWEPT_BODY",BODY,{"disambiguationData":[OSD([sQuery(id+"F1.wireOp",EDGE,"E9.0.7.0")])]});
            var Q364;
            Q364=makeQuery(id+"F60.opPattern","COPY",BODY,{"derivedFrom":makeQuery(id+"F3.opExtrude","SWEPT_BODY",BODY,{"disambiguationData":[OSD([sQuery(id+"F1.wireOp",EDGE,"E9.0.6.0")])]}),"instanceName":"3"});
            var Q365;
            Q365=makeQuery(id+"F60.opPattern","COPY",BODY,{"derivedFrom":makeQuery(id+"F3.opExtrude","SWEPT_BODY",BODY,{"disambiguationData":[OSD([sQuery(id+"F1.wireOp",EDGE,"E9.0.7.0")])]}),"instanceName":"51"});
            var Q366;
            Q366=makeQuery(id+"F60.opPattern","COPY",BODY,{"derivedFrom":makeQuery(id+"F3.opExtrude","SWEPT_BODY",BODY,{"disambiguationData":[OSD([sQuery(id+"F1.wireOp",EDGE,"E9.0.7.0")])]}),"instanceName":"2"});
            var Q367;
            Q367=makeQuery(id+"F61.opPattern","COPY",BODY,{"derivedFrom":makeQuery(id+"F3.opExtrude","SWEPT_BODY",BODY,{"disambiguationData":[OSD([sQuery(id+"F1.wireOp",EDGE,"E9.0.4.0")])]}),"instanceName":"3"});
            var Q368;
            Q368=makeQuery(id+"F3.opExtrude","SWEPT_BODY",BODY,{"disambiguationData":[OSD([sQuery(id+"F1.wireOp",EDGE,"E9.0.6.0")])]});
            var Q369;
            Q369=makeQuery(id+"F60.opPattern","COPY",BODY,{"derivedFrom":makeQuery(id+"F3.opExtrude","SWEPT_BODY",BODY,{"disambiguationData":[OSD([sQuery(id+"F1.wireOp",EDGE,"E9.0.6.0")])]}),"instanceName":"2"});
            var Q370;
            Q370=makeQuery(id+"F58.opPattern","COPY",BODY,{"derivedFrom":makeQuery(id+"F3.opExtrude","SWEPT_BODY",BODY,{"disambiguationData":[OSD([sQuery(id+"F1.wireOp",EDGE,"E9.0.10.0")])]}),"instanceName":"47"});
            var Q371;
            Q371=makeQuery(id+"F61.opPattern","COPY",BODY,{"derivedFrom":makeQuery(id+"F3.opExtrude","SWEPT_BODY",BODY,{"disambiguationData":[OSD([sQuery(id+"F1.wireOp",EDGE,"E9.0.5.0")])]}),"instanceName":"3"});
            var Q372;
            Q372=makeQuery(id+"F3.opExtrude","SWEPT_BODY",BODY,{"disambiguationData":[OSD([sQuery(id+"F1.wireOp",EDGE,"E9.0.5.0")])]});
            var Q373;
            Q373=makeQuery(id+"F3.opExtrude","SWEPT_BODY",BODY,{"disambiguationData":[OSD([sQuery(id+"F1.wireOp",EDGE,"E9.0.4.0")])]});
            var Q374;
            Q374=makeQuery(id+"F59.opPattern","COPY",BODY,{"derivedFrom":makeQuery(id+"F3.opExtrude","SWEPT_BODY",BODY,{"disambiguationData":[OSD([sQuery(id+"F1.wireOp",EDGE,"E9.0.8.0")])]}),"instanceName":"48"});
            var Q375;
            Q375=makeQuery(id+"F58.opPattern","COPY",BODY,{"derivedFrom":makeQuery(id+"F3.opExtrude","SWEPT_BODY",BODY,{"disambiguationData":[OSD([sQuery(id+"F1.wireOp",EDGE,"E9.0.9.0")])]}),"instanceName":"49"});
            var Q376;
            Q376=makeQuery(id+"F61.opPattern","COPY",BODY,{"derivedFrom":makeQuery(id+"F3.opExtrude","SWEPT_BODY",BODY,{"disambiguationData":[OSD([sQuery(id+"F1.wireOp",EDGE,"E9.0.4.0")])]}),"instanceName":"48"});
            var Q377;
            Q377=makeQuery(id+"F61.opPattern","COPY",BODY,{"derivedFrom":makeQuery(id+"F3.opExtrude","SWEPT_BODY",BODY,{"disambiguationData":[OSD([sQuery(id+"F1.wireOp",EDGE,"E9.0.5.0")])]}),"instanceName":"48"});
            var Q378;
            Q378=makeQuery(id+"F59.opPattern","COPY",BODY,{"derivedFrom":makeQuery(id+"F3.opExtrude","SWEPT_BODY",BODY,{"disambiguationData":[OSD([sQuery(id+"F1.wireOp",EDGE,"E9.0.8.0")])]}),"instanceName":"2"});
            var Q379;
            Q379=makeQuery(id+"F61.opPattern","COPY",BODY,{"derivedFrom":makeQuery(id+"F3.opExtrude","SWEPT_BODY",BODY,{"disambiguationData":[OSD([sQuery(id+"F1.wireOp",EDGE,"E9.0.4.0")])]}),"instanceName":"50"});
            var Q380;
            Q380=makeQuery(id+"F61.opPattern","COPY",BODY,{"derivedFrom":makeQuery(id+"F3.opExtrude","SWEPT_BODY",BODY,{"disambiguationData":[OSD([sQuery(id+"F1.wireOp",EDGE,"E9.0.5.0")])]}),"instanceName":"50"});
            var Q381;
            Q381=makeQuery(id+"F60.opPattern","COPY",BODY,{"derivedFrom":makeQuery(id+"F3.opExtrude","SWEPT_BODY",BODY,{"disambiguationData":[OSD([sQuery(id+"F1.wireOp",EDGE,"E9.0.7.0")])]}),"instanceName":"47"});
            var Q382;
            Q382=makeQuery(id+"F59.opPattern","COPY",BODY,{"derivedFrom":makeQuery(id+"F3.opExtrude","SWEPT_BODY",BODY,{"disambiguationData":[OSD([sQuery(id+"F1.wireOp",EDGE,"E9.0.8.0")])]}),"instanceName":"4"});
            var Q383;
            Q383=makeQuery(id+"F59.opPattern","COPY",BODY,{"derivedFrom":makeQuery(id+"F3.opExtrude","SWEPT_BODY",BODY,{"disambiguationData":[OSD([sQuery(id+"F1.wireOp",EDGE,"E9.0.8.0")])]}),"instanceName":"46"});
            var Q384;
            Q384=makeQuery(id+"F3.opExtrude","SWEPT_BODY",BODY,{"disambiguationData":[OSD([sQuery(id+"F1.wireOp",EDGE,"E9.0.10.0")])]});
            var Q385;
            Q385=makeQuery(id+"F3.opExtrude","SWEPT_BODY",BODY,{"disambiguationData":[OSD([sQuery(id+"F1.wireOp",EDGE,"E9.0.11.0")])]});
            var Q386;
            Q386=makeQuery(id+"F58.opPattern","COPY",BODY,{"derivedFrom":makeQuery(id+"F3.opExtrude","SWEPT_BODY",BODY,{"disambiguationData":[OSD([sQuery(id+"F1.wireOp",EDGE,"E9.0.10.0")])]}),"instanceName":"4"});
            var Q387;
            Q387=makeQuery(id+"F58.opPattern","COPY",BODY,{"derivedFrom":makeQuery(id+"F3.opExtrude","SWEPT_BODY",BODY,{"disambiguationData":[OSD([sQuery(id+"F1.wireOp",EDGE,"E9.0.9.0")])]}),"instanceName":"4"});
            var Q388;
            Q388=makeQuery(id+"F58.opPattern","COPY",BODY,{"derivedFrom":makeQuery(id+"F3.opExtrude","SWEPT_BODY",BODY,{"disambiguationData":[OSD([sQuery(id+"F1.wireOp",EDGE,"E9.0.10.0")])]}),"instanceName":"2"});
            var Q389;
            Q389=makeQuery(id+"F58.opPattern","COPY",BODY,{"derivedFrom":makeQuery(id+"F3.opExtrude","SWEPT_BODY",BODY,{"disambiguationData":[OSD([sQuery(id+"F1.wireOp",EDGE,"E9.0.9.0")])]}),"instanceName":"2"});
            var Q390;
            Q390=makeQuery(id+"F57.opPattern","COPY",BODY,{"derivedFrom":makeQuery(id+"F3.opExtrude","SWEPT_BODY",BODY,{"disambiguationData":[OSD([sQuery(id+"F1.wireOp",EDGE,"E9.0.11.0")])]}),"instanceName":"46"});
            var Q391;
            Q391=makeQuery(id+"F57.opPattern","COPY",BODY,{"derivedFrom":makeQuery(id+"F3.opExtrude","SWEPT_BODY",BODY,{"disambiguationData":[OSD([sQuery(id+"F1.wireOp",EDGE,"E9.0.11.0")])]}),"instanceName":"43"});
            var Q392;
            Q392=makeQuery(id+"F57.opPattern","COPY",BODY,{"derivedFrom":makeQuery(id+"F3.opExtrude","SWEPT_BODY",BODY,{"disambiguationData":[OSD([sQuery(id+"F1.wireOp",EDGE,"E9.0.11.0")])]}),"instanceName":"4"});
            var Q393;
            Q393=makeQuery(id+"F57.opPattern","COPY",BODY,{"derivedFrom":makeQuery(id+"F3.opExtrude","SWEPT_BODY",BODY,{"disambiguationData":[OSD([sQuery(id+"F1.wireOp",EDGE,"E9.0.11.0")])]}),"instanceName":"2"});
            var Q394;
            Q394=makeQuery(id+"F61.opPattern","COPY",BODY,{"derivedFrom":makeQuery(id+"F3.opExtrude","SWEPT_BODY",BODY,{"disambiguationData":[OSD([sQuery(id+"F1.wireOp",EDGE,"E9.0.4.0")])]}),"instanceName":"2"});
            var Q395;
            Q395=makeQuery(id+"F61.opPattern","COPY",BODY,{"derivedFrom":makeQuery(id+"F3.opExtrude","SWEPT_BODY",BODY,{"disambiguationData":[OSD([sQuery(id+"F1.wireOp",EDGE,"E9.0.5.0")])]}),"instanceName":"2"});
            var Q396;
            Q396=makeQuery(id+"F61.opPattern","COPY",BODY,{"derivedFrom":makeQuery(id+"F3.opExtrude","SWEPT_BODY",BODY,{"disambiguationData":[OSD([sQuery(id+"F1.wireOp",EDGE,"E9.0.5.0")])]}),"instanceName":"51"});
            var Q397;
            Q397=makeQuery(id+"F58.opPattern","COPY",BODY,{"derivedFrom":makeQuery(id+"F3.opExtrude","SWEPT_BODY",BODY,{"disambiguationData":[OSD([sQuery(id+"F1.wireOp",EDGE,"E9.0.9.0")])]}),"instanceName":"48"});
            var Q398;
            Q398=makeQuery(id+"F59.opPattern","COPY",BODY,{"derivedFrom":makeQuery(id+"F3.opExtrude","SWEPT_BODY",BODY,{"disambiguationData":[OSD([sQuery(id+"F1.wireOp",EDGE,"E9.0.8.0")])]}),"instanceName":"50"});
            var Q399;
            Q399=makeQuery(id+"F59.opPattern","COPY",BODY,{"derivedFrom":makeQuery(id+"F3.opExtrude","SWEPT_BODY",BODY,{"disambiguationData":[OSD([sQuery(id+"F1.wireOp",EDGE,"E9.0.8.0")])]}),"instanceName":"49"});
            var Q400;
            Q400=makeQuery(id+"F58.opPattern","COPY",BODY,{"derivedFrom":makeQuery(id+"F3.opExtrude","SWEPT_BODY",BODY,{"disambiguationData":[OSD([sQuery(id+"F1.wireOp",EDGE,"E9.0.10.0")])]}),"instanceName":"48"});
            var Q401;
            Q401=makeQuery(id+"F58.opPattern","COPY",BODY,{"derivedFrom":makeQuery(id+"F3.opExtrude","SWEPT_BODY",BODY,{"disambiguationData":[OSD([sQuery(id+"F1.wireOp",EDGE,"E9.0.10.0")])]}),"instanceName":"49"});
            var Q402;
            Q402=makeQuery(id+"F60.opPattern","COPY",BODY,{"derivedFrom":makeQuery(id+"F3.opExtrude","SWEPT_BODY",BODY,{"disambiguationData":[OSD([sQuery(id+"F1.wireOp",EDGE,"E9.0.7.0")])]}),"instanceName":"50"});
            var Q403;
            Q403=makeQuery(id+"F61.opPattern","COPY",BODY,{"derivedFrom":makeQuery(id+"F3.opExtrude","SWEPT_BODY",BODY,{"disambiguationData":[OSD([sQuery(id+"F1.wireOp",EDGE,"E9.0.4.0")])]}),"instanceName":"51"});
            var Q404;
            Q404=makeQuery(id+"F60.opPattern","COPY",BODY,{"derivedFrom":makeQuery(id+"F3.opExtrude","SWEPT_BODY",BODY,{"disambiguationData":[OSD([sQuery(id+"F1.wireOp",EDGE,"E9.0.6.0")])]}),"instanceName":"50"});
            var Q405;
            Q405=makeQuery(id+"F57.opPattern","COPY",BODY,{"derivedFrom":makeQuery(id+"F3.opExtrude","SWEPT_BODY",BODY,{"disambiguationData":[OSD([sQuery(id+"F1.wireOp",EDGE,"E9.0.11.0")])]}),"instanceName":"48"});
            var Q406;
            Q406=makeQuery(id+"F57.opPattern","COPY",BODY,{"derivedFrom":makeQuery(id+"F3.opExtrude","SWEPT_BODY",BODY,{"disambiguationData":[OSD([sQuery(id+"F1.wireOp",EDGE,"E9.0.11.0")])]}),"instanceName":"47"});
            var Q407;
            Q407=makeQuery(id+"F61.opPattern","COPY",BODY,{"derivedFrom":makeQuery(id+"F3.opExtrude","SWEPT_BODY",BODY,{"disambiguationData":[OSD([sQuery(id+"F1.wireOp",EDGE,"E9.0.5.0")])]}),"instanceName":"52"});
            var Q408;
            Q408=makeQuery(id+"F60.opPattern","COPY",BODY,{"derivedFrom":makeQuery(id+"F3.opExtrude","SWEPT_BODY",BODY,{"disambiguationData":[OSD([sQuery(id+"F1.wireOp",EDGE,"E9.0.6.0")])]}),"instanceName":"51"});
            var Q409;
            Q409=makeQuery(id+"F61.opPattern","COPY",BODY,{"derivedFrom":makeQuery(id+"F3.opExtrude","SWEPT_BODY",BODY,{"disambiguationData":[OSD([sQuery(id+"F1.wireOp",EDGE,"E9.0.4.0")])]}),"instanceName":"52"});
            var Q410;
            Q410=makeQuery(id+"F2.opRevolve","SWEPT_BODY",BODY,{"disambiguationData":[OSD([sQuery(id+"F0.wireOp",EDGE,"E0"),sQuery(id+"F0.wireOp",EDGE,"E1"),sQuery(id+"F0.wireOp",EDGE,"E2"),sQuery(id+"F0.wireOp",EDGE,"E3"),sQuery(id+"F0.wireOp",EDGE,"E6")])]});
            booleanBodies(context, id + "F62", {"operationType" : BooleanOperationType.SUBTRACTION, "tools" : qUnion([Q0, Q1, Q2, Q3, Q4, Q5, Q6, Q7, Q8, Q9, Q10, Q11, Q12, Q13, Q14, Q15, Q16, Q17, Q18, Q19, Q20, Q21, Q22, Q23, Q24, Q25, Q26, Q27, Q28, Q29, Q30, Q31, Q32, Q33, Q34, Q35, Q36, Q37, Q38, Q39, Q40, Q41, Q42, Q43, Q44, Q45, Q46, Q47, Q48, Q49, Q50, Q51, Q52, Q53, Q54, Q55, Q56, Q57, Q58, Q59, Q60, Q61, Q62, Q63, Q64, Q65, Q66, Q67, Q68, Q69, Q70, Q71, Q72, Q73, Q74, Q75, Q76, Q77, Q78, Q79, Q80, Q81, Q82, Q83, Q84, Q85, Q86, Q87, Q88, Q89, Q90, Q91, Q92, Q93, Q94, Q95, Q96, Q97, Q98, Q99, Q100, Q101, Q102, Q103, Q104, Q105, Q106, Q107, Q108, Q109, Q110, Q111, Q112, Q113, Q114, Q115, Q116, Q117, Q118, Q119, Q120, Q121, Q122, Q123, Q124, Q125, Q126, Q127, Q128, Q129, Q130, Q131, Q132, Q133, Q134, Q135, Q136, Q137, Q138, Q139, Q140, Q141, Q142, Q143, Q144, Q145, Q146, Q147, Q148, Q149, Q150, Q151, Q152, Q153, Q154, Q155, Q156, Q157, Q158, Q159, Q160, Q161, Q162, Q163, Q164, Q165, Q166, Q167, Q168, Q169, Q170, Q171, Q172, Q173, Q174, Q175, Q176, Q177, Q178, Q179, Q180, Q181, Q182, Q183, Q184, Q185, Q186, Q187, Q188, Q189, Q190, Q191, Q192, Q193, Q194, Q195, Q196, Q197, Q198, Q199, Q200, Q201, Q202, Q203, Q204, Q205, Q206, Q207, Q208, Q209, Q210, Q211, Q212, Q213, Q214, Q215, Q216, Q217, Q218, Q219, Q220, Q221, Q222, Q223, Q224, Q225, Q226, Q227, Q228, Q229, Q230, Q231, Q232, Q233, Q234, Q235, Q236, Q237, Q238, Q239, Q240, Q241, Q242, Q243, Q244, Q245, Q246, Q247, Q248, Q249, Q250, Q251, Q252, Q253, Q254, Q255, Q256, Q257, Q258, Q259, Q260, Q261, Q262, Q263, Q264, Q265, Q266, Q267, Q268, Q269, Q270, Q271, Q272, Q273, Q274, Q275, Q276, Q277, Q278, Q279, Q280, Q281, Q282, Q283, Q284, Q285, Q286, Q287, Q288, Q289, Q290, Q291, Q292, Q293, Q294, Q295, Q296, Q297, Q298, Q299, Q300, Q301, Q302, Q303, Q304, Q305, Q306, Q307, Q308, Q309, Q310, Q311, Q312, Q313, Q314, Q315, Q316, Q317, Q318, Q319, Q320, Q321, Q322, Q323, Q324, Q325, Q326, Q327, Q328, Q329, Q330, Q331, Q332, Q333, Q334, Q335, Q336, Q337, Q338, Q339, Q340, Q341, Q342, Q343, Q344, Q345, Q346, Q347, Q348, Q349, Q350, Q351, Q352, Q353, Q354, Q355, Q356, Q357, Q358, Q359, Q360, Q361, Q362, Q363, Q364, Q365, Q366, Q367, Q368, Q369, Q370, Q371, Q372, Q373, Q374, Q375, Q376, Q377, Q378, Q379, Q380, Q381, Q382, Q383, Q384, Q385, Q386, Q387, Q388, Q389, Q390, Q391, Q392, Q393, Q394, Q395, Q396, Q397, Q398, Q399, Q400, Q401, Q402, Q403, Q404, Q405, Q406, Q407, Q408, Q409]), "targets" : qUnion([Q410])});
        }
        {
            var Q0;
            Q0=makeQuery(id+"F3.opExtrude","SWEPT_BODY",BODY,{"disambiguationData":[OSD([sQuery(id+"F1.wireOp",EDGE,"E9.0.3.0")])]});
            var Q1;
            Q1=makeQuery(id+"F2.opRevolve","SWEPT_FACE",FACE,{"disambiguationData":[OSD([sQuery(id+"F0.wireOp",EDGE,"E1")])]});
            circularPattern(context, id + "F63", {"entities" : qUnion([Q0]), "axis" : qUnion([Q1]), "angle" : 180 * degree, "instanceCount" : 54, "oppositeDirection" : true, "equalSpace" : true});
        }
        {
            var Q0;
            Q0=makeQuery(id+"F3.opExtrude","SWEPT_BODY",BODY,{"disambiguationData":[OSD([sQuery(id+"F1.wireOp",EDGE,"E9.0.2.0")])]});
            var Q1;
            Q1=makeQuery(id+"F3.opExtrude","SWEPT_BODY",BODY,{"disambiguationData":[OSD([sQuery(id+"F1.wireOp",EDGE,"E9.0.1.0")])]});
            var Q2;
            Q2=makeQuery(id+"F2.opRevolve","SWEPT_FACE",FACE,{"disambiguationData":[OSD([sQuery(id+"F0.wireOp",EDGE,"E1")])]});
            circularPattern(context, id + "F64", {"entities" : qUnion([Q0, Q1]), "axis" : qUnion([Q2]), "angle" : 180 * degree, "instanceCount" : 55, "oppositeDirection" : true, "equalSpace" : true});
        }
        {
            var Q0;
            Q0=makeQuery(id+"F3.opExtrude","SWEPT_BODY",BODY,{"disambiguationData":[OSD([sQuery(id+"F1.wireOp",EDGE,"E8")])]});
            var Q1;
            Q1=makeQuery(id+"F2.opRevolve","SWEPT_FACE",FACE,{"disambiguationData":[OSD([sQuery(id+"F0.wireOp",EDGE,"E1")])]});
            circularPattern(context, id + "F65", {"entities" : qUnion([Q0]), "axis" : qUnion([Q1]), "angle" : 180 * degree, "instanceCount" : 56, "oppositeDirection" : true, "equalSpace" : true});
        }
        {
            var Q0;
            Q0=makeQuery(id+"F64.opPattern","COPY",BODY,{"derivedFrom":makeQuery(id+"F3.opExtrude","SWEPT_BODY",BODY,{"disambiguationData":[OSD([sQuery(id+"F1.wireOp",EDGE,"E9.0.2.0")])]}),"instanceName":"39"});
            var Q1;
            Q1=makeQuery(id+"F65.opPattern","COPY",BODY,{"derivedFrom":makeQuery(id+"F3.opExtrude","SWEPT_BODY",BODY,{"disambiguationData":[OSD([sQuery(id+"F1.wireOp",EDGE,"E8")])]}),"instanceName":"21"});
            var Q2;
            Q2=makeQuery(id+"F64.opPattern","COPY",BODY,{"derivedFrom":makeQuery(id+"F3.opExtrude","SWEPT_BODY",BODY,{"disambiguationData":[OSD([sQuery(id+"F1.wireOp",EDGE,"E9.0.2.0")])]}),"instanceName":"6"});
            var Q3;
            Q3=makeQuery(id+"F65.opPattern","COPY",BODY,{"derivedFrom":makeQuery(id+"F3.opExtrude","SWEPT_BODY",BODY,{"disambiguationData":[OSD([sQuery(id+"F1.wireOp",EDGE,"E8")])]}),"instanceName":"20"});
            var Q4;
            Q4=makeQuery(id+"F65.opPattern","COPY",BODY,{"derivedFrom":makeQuery(id+"F3.opExtrude","SWEPT_BODY",BODY,{"disambiguationData":[OSD([sQuery(id+"F1.wireOp",EDGE,"E8")])]}),"instanceName":"19"});
            var Q5;
            Q5=makeQuery(id+"F64.opPattern","COPY",BODY,{"derivedFrom":makeQuery(id+"F3.opExtrude","SWEPT_BODY",BODY,{"disambiguationData":[OSD([sQuery(id+"F1.wireOp",EDGE,"E9.0.1.0")])]}),"instanceName":"7"});
            var Q6;
            Q6=makeQuery(id+"F65.opPattern","COPY",BODY,{"derivedFrom":makeQuery(id+"F3.opExtrude","SWEPT_BODY",BODY,{"disambiguationData":[OSD([sQuery(id+"F1.wireOp",EDGE,"E8")])]}),"instanceName":"18"});
            var Q7;
            Q7=makeQuery(id+"F65.opPattern","COPY",BODY,{"derivedFrom":makeQuery(id+"F3.opExtrude","SWEPT_BODY",BODY,{"disambiguationData":[OSD([sQuery(id+"F1.wireOp",EDGE,"E8")])]}),"instanceName":"22"});
            var Q8;
            Q8=makeQuery(id+"F64.opPattern","COPY",BODY,{"derivedFrom":makeQuery(id+"F3.opExtrude","SWEPT_BODY",BODY,{"disambiguationData":[OSD([sQuery(id+"F1.wireOp",EDGE,"E9.0.1.0")])]}),"instanceName":"39"});
            var Q9;
            Q9=makeQuery(id+"F64.opPattern","COPY",BODY,{"derivedFrom":makeQuery(id+"F3.opExtrude","SWEPT_BODY",BODY,{"disambiguationData":[OSD([sQuery(id+"F1.wireOp",EDGE,"E9.0.2.0")])]}),"instanceName":"40"});
            var Q10;
            Q10=makeQuery(id+"F64.opPattern","COPY",BODY,{"derivedFrom":makeQuery(id+"F3.opExtrude","SWEPT_BODY",BODY,{"disambiguationData":[OSD([sQuery(id+"F1.wireOp",EDGE,"E9.0.2.0")])]}),"instanceName":"7"});
            var Q11;
            Q11=makeQuery(id+"F65.opPattern","COPY",BODY,{"derivedFrom":makeQuery(id+"F3.opExtrude","SWEPT_BODY",BODY,{"disambiguationData":[OSD([sQuery(id+"F1.wireOp",EDGE,"E8")])]}),"instanceName":"23"});
            var Q12;
            Q12=makeQuery(id+"F64.opPattern","COPY",BODY,{"derivedFrom":makeQuery(id+"F3.opExtrude","SWEPT_BODY",BODY,{"disambiguationData":[OSD([sQuery(id+"F1.wireOp",EDGE,"E9.0.1.0")])]}),"instanceName":"41"});
            var Q13;
            Q13=makeQuery(id+"F64.opPattern","COPY",BODY,{"derivedFrom":makeQuery(id+"F3.opExtrude","SWEPT_BODY",BODY,{"disambiguationData":[OSD([sQuery(id+"F1.wireOp",EDGE,"E9.0.1.0")])]}),"instanceName":"29"});
            var Q14;
            Q14=makeQuery(id+"F64.opPattern","COPY",BODY,{"derivedFrom":makeQuery(id+"F3.opExtrude","SWEPT_BODY",BODY,{"disambiguationData":[OSD([sQuery(id+"F1.wireOp",EDGE,"E9.0.1.0")])]}),"instanceName":"40"});
            var Q15;
            Q15=makeQuery(id+"F65.opPattern","COPY",BODY,{"derivedFrom":makeQuery(id+"F3.opExtrude","SWEPT_BODY",BODY,{"disambiguationData":[OSD([sQuery(id+"F1.wireOp",EDGE,"E8")])]}),"instanceName":"24"});
            var Q16;
            Q16=makeQuery(id+"F65.opPattern","COPY",BODY,{"derivedFrom":makeQuery(id+"F3.opExtrude","SWEPT_BODY",BODY,{"disambiguationData":[OSD([sQuery(id+"F1.wireOp",EDGE,"E8")])]}),"instanceName":"25"});
            var Q17;
            Q17=makeQuery(id+"F64.opPattern","COPY",BODY,{"derivedFrom":makeQuery(id+"F3.opExtrude","SWEPT_BODY",BODY,{"disambiguationData":[OSD([sQuery(id+"F1.wireOp",EDGE,"E9.0.2.0")])]}),"instanceName":"41"});
            var Q18;
            Q18=makeQuery(id+"F64.opPattern","COPY",BODY,{"derivedFrom":makeQuery(id+"F3.opExtrude","SWEPT_BODY",BODY,{"disambiguationData":[OSD([sQuery(id+"F1.wireOp",EDGE,"E9.0.1.0")])]}),"instanceName":"8"});
            var Q19;
            Q19=makeQuery(id+"F64.opPattern","COPY",BODY,{"derivedFrom":makeQuery(id+"F3.opExtrude","SWEPT_BODY",BODY,{"disambiguationData":[OSD([sQuery(id+"F1.wireOp",EDGE,"E9.0.1.0")])]}),"instanceName":"42"});
            var Q20;
            Q20=makeQuery(id+"F65.opPattern","COPY",BODY,{"derivedFrom":makeQuery(id+"F3.opExtrude","SWEPT_BODY",BODY,{"disambiguationData":[OSD([sQuery(id+"F1.wireOp",EDGE,"E8")])]}),"instanceName":"26"});
            var Q21;
            Q21=makeQuery(id+"F64.opPattern","COPY",BODY,{"derivedFrom":makeQuery(id+"F3.opExtrude","SWEPT_BODY",BODY,{"disambiguationData":[OSD([sQuery(id+"F1.wireOp",EDGE,"E9.0.2.0")])]}),"instanceName":"8"});
            var Q22;
            Q22=makeQuery(id+"F64.opPattern","COPY",BODY,{"derivedFrom":makeQuery(id+"F3.opExtrude","SWEPT_BODY",BODY,{"disambiguationData":[OSD([sQuery(id+"F1.wireOp",EDGE,"E9.0.1.0")])]}),"instanceName":"9"});
            var Q23;
            Q23=makeQuery(id+"F64.opPattern","COPY",BODY,{"derivedFrom":makeQuery(id+"F3.opExtrude","SWEPT_BODY",BODY,{"disambiguationData":[OSD([sQuery(id+"F1.wireOp",EDGE,"E9.0.1.0")])]}),"instanceName":"53"});
            var Q24;
            Q24=makeQuery(id+"F3.opExtrude","SWEPT_BODY",BODY,{"disambiguationData":[OSD([sQuery(id+"F1.wireOp",EDGE,"E8")])]});
            var Q25;
            Q25=makeQuery(id+"F63.opPattern","COPY",BODY,{"derivedFrom":makeQuery(id+"F3.opExtrude","SWEPT_BODY",BODY,{"disambiguationData":[OSD([sQuery(id+"F1.wireOp",EDGE,"E9.0.3.0")])]}),"instanceName":"34"});
            var Q26;
            Q26=makeQuery(id+"F64.opPattern","COPY",BODY,{"derivedFrom":makeQuery(id+"F3.opExtrude","SWEPT_BODY",BODY,{"disambiguationData":[OSD([sQuery(id+"F1.wireOp",EDGE,"E9.0.2.0")])]}),"instanceName":"9"});
            var Q27;
            Q27=makeQuery(id+"F64.opPattern","COPY",BODY,{"derivedFrom":makeQuery(id+"F3.opExtrude","SWEPT_BODY",BODY,{"disambiguationData":[OSD([sQuery(id+"F1.wireOp",EDGE,"E9.0.2.0")])]}),"instanceName":"42"});
            var Q28;
            Q28=makeQuery(id+"F65.opPattern","COPY",BODY,{"derivedFrom":makeQuery(id+"F3.opExtrude","SWEPT_BODY",BODY,{"disambiguationData":[OSD([sQuery(id+"F1.wireOp",EDGE,"E8")])]}),"instanceName":"15"});
            var Q29;
            Q29=makeQuery(id+"F64.opPattern","COPY",BODY,{"derivedFrom":makeQuery(id+"F3.opExtrude","SWEPT_BODY",BODY,{"disambiguationData":[OSD([sQuery(id+"F1.wireOp",EDGE,"E9.0.1.0")])]}),"instanceName":"10"});
            var Q30;
            Q30=makeQuery(id+"F64.opPattern","COPY",BODY,{"derivedFrom":makeQuery(id+"F3.opExtrude","SWEPT_BODY",BODY,{"disambiguationData":[OSD([sQuery(id+"F1.wireOp",EDGE,"E9.0.2.0")])]}),"instanceName":"28"});
            var Q31;
            Q31=makeQuery(id+"F64.opPattern","COPY",BODY,{"derivedFrom":makeQuery(id+"F3.opExtrude","SWEPT_BODY",BODY,{"disambiguationData":[OSD([sQuery(id+"F1.wireOp",EDGE,"E9.0.1.0")])]}),"instanceName":"43"});
            var Q32;
            Q32=makeQuery(id+"F64.opPattern","COPY",BODY,{"derivedFrom":makeQuery(id+"F3.opExtrude","SWEPT_BODY",BODY,{"disambiguationData":[OSD([sQuery(id+"F1.wireOp",EDGE,"E9.0.2.0")])]}),"instanceName":"10"});
            var Q33;
            Q33=makeQuery(id+"F64.opPattern","COPY",BODY,{"derivedFrom":makeQuery(id+"F3.opExtrude","SWEPT_BODY",BODY,{"disambiguationData":[OSD([sQuery(id+"F1.wireOp",EDGE,"E9.0.2.0")])]}),"instanceName":"51"});
            var Q34;
            Q34=makeQuery(id+"F65.opPattern","COPY",BODY,{"derivedFrom":makeQuery(id+"F3.opExtrude","SWEPT_BODY",BODY,{"disambiguationData":[OSD([sQuery(id+"F1.wireOp",EDGE,"E8")])]}),"instanceName":"29"});
            var Q35;
            Q35=makeQuery(id+"F64.opPattern","COPY",BODY,{"derivedFrom":makeQuery(id+"F3.opExtrude","SWEPT_BODY",BODY,{"disambiguationData":[OSD([sQuery(id+"F1.wireOp",EDGE,"E9.0.2.0")])]}),"instanceName":"43"});
            var Q36;
            Q36=makeQuery(id+"F64.opPattern","COPY",BODY,{"derivedFrom":makeQuery(id+"F3.opExtrude","SWEPT_BODY",BODY,{"disambiguationData":[OSD([sQuery(id+"F1.wireOp",EDGE,"E9.0.2.0")])]}),"instanceName":"53"});
            var Q37;
            Q37=makeQuery(id+"F64.opPattern","COPY",BODY,{"derivedFrom":makeQuery(id+"F3.opExtrude","SWEPT_BODY",BODY,{"disambiguationData":[OSD([sQuery(id+"F1.wireOp",EDGE,"E9.0.1.0")])]}),"instanceName":"51"});
            var Q38;
            Q38=makeQuery(id+"F64.opPattern","COPY",BODY,{"derivedFrom":makeQuery(id+"F3.opExtrude","SWEPT_BODY",BODY,{"disambiguationData":[OSD([sQuery(id+"F1.wireOp",EDGE,"E9.0.1.0")])]}),"instanceName":"44"});
            var Q39;
            Q39=makeQuery(id+"F64.opPattern","COPY",BODY,{"derivedFrom":makeQuery(id+"F3.opExtrude","SWEPT_BODY",BODY,{"disambiguationData":[OSD([sQuery(id+"F1.wireOp",EDGE,"E9.0.2.0")])]}),"instanceName":"50"});
            var Q40;
            Q40=makeQuery(id+"F65.opPattern","COPY",BODY,{"derivedFrom":makeQuery(id+"F3.opExtrude","SWEPT_BODY",BODY,{"disambiguationData":[OSD([sQuery(id+"F1.wireOp",EDGE,"E8")])]}),"instanceName":"30"});
            var Q41;
            Q41=makeQuery(id+"F64.opPattern","COPY",BODY,{"derivedFrom":makeQuery(id+"F3.opExtrude","SWEPT_BODY",BODY,{"disambiguationData":[OSD([sQuery(id+"F1.wireOp",EDGE,"E9.0.1.0")])]}),"instanceName":"50"});
            var Q42;
            Q42=makeQuery(id+"F65.opPattern","COPY",BODY,{"derivedFrom":makeQuery(id+"F3.opExtrude","SWEPT_BODY",BODY,{"disambiguationData":[OSD([sQuery(id+"F1.wireOp",EDGE,"E8")])]}),"instanceName":"31"});
            var Q43;
            Q43=makeQuery(id+"F64.opPattern","COPY",BODY,{"derivedFrom":makeQuery(id+"F3.opExtrude","SWEPT_BODY",BODY,{"disambiguationData":[OSD([sQuery(id+"F1.wireOp",EDGE,"E9.0.1.0")])]}),"instanceName":"11"});
            var Q44;
            Q44=makeQuery(id+"F64.opPattern","COPY",BODY,{"derivedFrom":makeQuery(id+"F3.opExtrude","SWEPT_BODY",BODY,{"disambiguationData":[OSD([sQuery(id+"F1.wireOp",EDGE,"E9.0.2.0")])]}),"instanceName":"49"});
            var Q45;
            Q45=makeQuery(id+"F65.opPattern","COPY",BODY,{"derivedFrom":makeQuery(id+"F3.opExtrude","SWEPT_BODY",BODY,{"disambiguationData":[OSD([sQuery(id+"F1.wireOp",EDGE,"E8")])]}),"instanceName":"32"});
            var Q46;
            Q46=makeQuery(id+"F64.opPattern","COPY",BODY,{"derivedFrom":makeQuery(id+"F3.opExtrude","SWEPT_BODY",BODY,{"disambiguationData":[OSD([sQuery(id+"F1.wireOp",EDGE,"E9.0.2.0")])]}),"instanceName":"44"});
            var Q47;
            Q47=makeQuery(id+"F64.opPattern","COPY",BODY,{"derivedFrom":makeQuery(id+"F3.opExtrude","SWEPT_BODY",BODY,{"disambiguationData":[OSD([sQuery(id+"F1.wireOp",EDGE,"E9.0.1.0")])]}),"instanceName":"45"});
            var Q48;
            Q48=makeQuery(id+"F65.opPattern","COPY",BODY,{"derivedFrom":makeQuery(id+"F3.opExtrude","SWEPT_BODY",BODY,{"disambiguationData":[OSD([sQuery(id+"F1.wireOp",EDGE,"E8")])]}),"instanceName":"33"});
            var Q49;
            Q49=makeQuery(id+"F64.opPattern","COPY",BODY,{"derivedFrom":makeQuery(id+"F3.opExtrude","SWEPT_BODY",BODY,{"disambiguationData":[OSD([sQuery(id+"F1.wireOp",EDGE,"E9.0.2.0")])]}),"instanceName":"11"});
            var Q50;
            Q50=makeQuery(id+"F65.opPattern","COPY",BODY,{"derivedFrom":makeQuery(id+"F3.opExtrude","SWEPT_BODY",BODY,{"disambiguationData":[OSD([sQuery(id+"F1.wireOp",EDGE,"E8")])]}),"instanceName":"34"});
            var Q51;
            Q51=makeQuery(id+"F64.opPattern","COPY",BODY,{"derivedFrom":makeQuery(id+"F3.opExtrude","SWEPT_BODY",BODY,{"disambiguationData":[OSD([sQuery(id+"F1.wireOp",EDGE,"E9.0.1.0")])]}),"instanceName":"31"});
            var Q52;
            Q52=makeQuery(id+"F65.opPattern","COPY",BODY,{"derivedFrom":makeQuery(id+"F3.opExtrude","SWEPT_BODY",BODY,{"disambiguationData":[OSD([sQuery(id+"F1.wireOp",EDGE,"E8")])]}),"instanceName":"35"});
            var Q53;
            Q53=makeQuery(id+"F64.opPattern","COPY",BODY,{"derivedFrom":makeQuery(id+"F3.opExtrude","SWEPT_BODY",BODY,{"disambiguationData":[OSD([sQuery(id+"F1.wireOp",EDGE,"E9.0.1.0")])]}),"instanceName":"12"});
            var Q54;
            Q54=makeQuery(id+"F65.opPattern","COPY",BODY,{"derivedFrom":makeQuery(id+"F3.opExtrude","SWEPT_BODY",BODY,{"disambiguationData":[OSD([sQuery(id+"F1.wireOp",EDGE,"E8")])]}),"instanceName":"36"});
            var Q55;
            Q55=makeQuery(id+"F65.opPattern","COPY",BODY,{"derivedFrom":makeQuery(id+"F3.opExtrude","SWEPT_BODY",BODY,{"disambiguationData":[OSD([sQuery(id+"F1.wireOp",EDGE,"E8")])]}),"instanceName":"37"});
            var Q56;
            Q56=makeQuery(id+"F64.opPattern","COPY",BODY,{"derivedFrom":makeQuery(id+"F3.opExtrude","SWEPT_BODY",BODY,{"disambiguationData":[OSD([sQuery(id+"F1.wireOp",EDGE,"E9.0.2.0")])]}),"instanceName":"12"});
            var Q57;
            Q57=makeQuery(id+"F64.opPattern","COPY",BODY,{"derivedFrom":makeQuery(id+"F3.opExtrude","SWEPT_BODY",BODY,{"disambiguationData":[OSD([sQuery(id+"F1.wireOp",EDGE,"E9.0.1.0")])]}),"instanceName":"13"});
            var Q58;
            Q58=makeQuery(id+"F65.opPattern","COPY",BODY,{"derivedFrom":makeQuery(id+"F3.opExtrude","SWEPT_BODY",BODY,{"disambiguationData":[OSD([sQuery(id+"F1.wireOp",EDGE,"E8")])]}),"instanceName":"38"});
            var Q59;
            Q59=makeQuery(id+"F64.opPattern","COPY",BODY,{"derivedFrom":makeQuery(id+"F3.opExtrude","SWEPT_BODY",BODY,{"disambiguationData":[OSD([sQuery(id+"F1.wireOp",EDGE,"E9.0.2.0")])]}),"instanceName":"45"});
            var Q60;
            Q60=makeQuery(id+"F64.opPattern","COPY",BODY,{"derivedFrom":makeQuery(id+"F3.opExtrude","SWEPT_BODY",BODY,{"disambiguationData":[OSD([sQuery(id+"F1.wireOp",EDGE,"E9.0.1.0")])]}),"instanceName":"49"});
            var Q61;
            Q61=makeQuery(id+"F63.opPattern","COPY",BODY,{"derivedFrom":makeQuery(id+"F3.opExtrude","SWEPT_BODY",BODY,{"disambiguationData":[OSD([sQuery(id+"F1.wireOp",EDGE,"E9.0.3.0")])]}),"instanceName":"21"});
            var Q62;
            Q62=makeQuery(id+"F64.opPattern","COPY",BODY,{"derivedFrom":makeQuery(id+"F3.opExtrude","SWEPT_BODY",BODY,{"disambiguationData":[OSD([sQuery(id+"F1.wireOp",EDGE,"E9.0.1.0")])]}),"instanceName":"46"});
            var Q63;
            Q63=makeQuery(id+"F65.opPattern","COPY",BODY,{"derivedFrom":makeQuery(id+"F3.opExtrude","SWEPT_BODY",BODY,{"disambiguationData":[OSD([sQuery(id+"F1.wireOp",EDGE,"E8")])]}),"instanceName":"39"});
            var Q64;
            Q64=makeQuery(id+"F64.opPattern","COPY",BODY,{"derivedFrom":makeQuery(id+"F3.opExtrude","SWEPT_BODY",BODY,{"disambiguationData":[OSD([sQuery(id+"F1.wireOp",EDGE,"E9.0.2.0")])]}),"instanceName":"46"});
            var Q65;
            Q65=makeQuery(id+"F65.opPattern","COPY",BODY,{"derivedFrom":makeQuery(id+"F3.opExtrude","SWEPT_BODY",BODY,{"disambiguationData":[OSD([sQuery(id+"F1.wireOp",EDGE,"E8")])]}),"instanceName":"40"});
            var Q66;
            Q66=makeQuery(id+"F65.opPattern","COPY",BODY,{"derivedFrom":makeQuery(id+"F3.opExtrude","SWEPT_BODY",BODY,{"disambiguationData":[OSD([sQuery(id+"F1.wireOp",EDGE,"E8")])]}),"instanceName":"41"});
            var Q67;
            Q67=makeQuery(id+"F64.opPattern","COPY",BODY,{"derivedFrom":makeQuery(id+"F3.opExtrude","SWEPT_BODY",BODY,{"disambiguationData":[OSD([sQuery(id+"F1.wireOp",EDGE,"E9.0.2.0")])]}),"instanceName":"13"});
            var Q68;
            Q68=makeQuery(id+"F64.opPattern","COPY",BODY,{"derivedFrom":makeQuery(id+"F3.opExtrude","SWEPT_BODY",BODY,{"disambiguationData":[OSD([sQuery(id+"F1.wireOp",EDGE,"E9.0.1.0")])]}),"instanceName":"14"});
            var Q69;
            Q69=makeQuery(id+"F63.opPattern","COPY",BODY,{"derivedFrom":makeQuery(id+"F3.opExtrude","SWEPT_BODY",BODY,{"disambiguationData":[OSD([sQuery(id+"F1.wireOp",EDGE,"E9.0.3.0")])]}),"instanceName":"25"});
            var Q70;
            Q70=makeQuery(id+"F3.opExtrude","SWEPT_BODY",BODY,{"disambiguationData":[OSD([sQuery(id+"F1.wireOp",EDGE,"E9.0.3.0")])]});
            var Q71;
            Q71=makeQuery(id+"F64.opPattern","COPY",BODY,{"derivedFrom":makeQuery(id+"F3.opExtrude","SWEPT_BODY",BODY,{"disambiguationData":[OSD([sQuery(id+"F1.wireOp",EDGE,"E9.0.2.0")])]}),"instanceName":"26"});
            var Q72;
            Q72=makeQuery(id+"F64.opPattern","COPY",BODY,{"derivedFrom":makeQuery(id+"F3.opExtrude","SWEPT_BODY",BODY,{"disambiguationData":[OSD([sQuery(id+"F1.wireOp",EDGE,"E9.0.1.0")])]}),"instanceName":"26"});
            var Q73;
            Q73=makeQuery(id+"F64.opPattern","COPY",BODY,{"derivedFrom":makeQuery(id+"F3.opExtrude","SWEPT_BODY",BODY,{"disambiguationData":[OSD([sQuery(id+"F1.wireOp",EDGE,"E9.0.2.0")])]}),"instanceName":"14"});
            var Q74;
            Q74=makeQuery(id+"F64.opPattern","COPY",BODY,{"derivedFrom":makeQuery(id+"F3.opExtrude","SWEPT_BODY",BODY,{"disambiguationData":[OSD([sQuery(id+"F1.wireOp",EDGE,"E9.0.1.0")])]}),"instanceName":"15"});
            var Q75;
            Q75=makeQuery(id+"F64.opPattern","COPY",BODY,{"derivedFrom":makeQuery(id+"F3.opExtrude","SWEPT_BODY",BODY,{"disambiguationData":[OSD([sQuery(id+"F1.wireOp",EDGE,"E9.0.2.0")])]}),"instanceName":"25"});
            var Q76;
            Q76=makeQuery(id+"F64.opPattern","COPY",BODY,{"derivedFrom":makeQuery(id+"F3.opExtrude","SWEPT_BODY",BODY,{"disambiguationData":[OSD([sQuery(id+"F1.wireOp",EDGE,"E9.0.1.0")])]}),"instanceName":"37"});
            var Q77;
            Q77=makeQuery(id+"F64.opPattern","COPY",BODY,{"derivedFrom":makeQuery(id+"F3.opExtrude","SWEPT_BODY",BODY,{"disambiguationData":[OSD([sQuery(id+"F1.wireOp",EDGE,"E9.0.1.0")])]}),"instanceName":"25"});
            var Q78;
            Q78=makeQuery(id+"F64.opPattern","COPY",BODY,{"derivedFrom":makeQuery(id+"F3.opExtrude","SWEPT_BODY",BODY,{"disambiguationData":[OSD([sQuery(id+"F1.wireOp",EDGE,"E9.0.2.0")])]}),"instanceName":"24"});
            var Q79;
            Q79=makeQuery(id+"F64.opPattern","COPY",BODY,{"derivedFrom":makeQuery(id+"F3.opExtrude","SWEPT_BODY",BODY,{"disambiguationData":[OSD([sQuery(id+"F1.wireOp",EDGE,"E9.0.2.0")])]}),"instanceName":"36"});
            var Q80;
            Q80=makeQuery(id+"F64.opPattern","COPY",BODY,{"derivedFrom":makeQuery(id+"F3.opExtrude","SWEPT_BODY",BODY,{"disambiguationData":[OSD([sQuery(id+"F1.wireOp",EDGE,"E9.0.1.0")])]}),"instanceName":"47"});
            var Q81;
            Q81=makeQuery(id+"F63.opPattern","COPY",BODY,{"derivedFrom":makeQuery(id+"F3.opExtrude","SWEPT_BODY",BODY,{"disambiguationData":[OSD([sQuery(id+"F1.wireOp",EDGE,"E9.0.3.0")])]}),"instanceName":"3"});
            var Q82;
            Q82=makeQuery(id+"F64.opPattern","COPY",BODY,{"derivedFrom":makeQuery(id+"F3.opExtrude","SWEPT_BODY",BODY,{"disambiguationData":[OSD([sQuery(id+"F1.wireOp",EDGE,"E9.0.2.0")])]}),"instanceName":"47"});
            var Q83;
            Q83=makeQuery(id+"F64.opPattern","COPY",BODY,{"derivedFrom":makeQuery(id+"F3.opExtrude","SWEPT_BODY",BODY,{"disambiguationData":[OSD([sQuery(id+"F1.wireOp",EDGE,"E9.0.2.0")])]}),"instanceName":"15"});
            var Q84;
            Q84=makeQuery(id+"F65.opPattern","COPY",BODY,{"derivedFrom":makeQuery(id+"F3.opExtrude","SWEPT_BODY",BODY,{"disambiguationData":[OSD([sQuery(id+"F1.wireOp",EDGE,"E8")])]}),"instanceName":"42"});
            var Q85;
            Q85=makeQuery(id+"F64.opPattern","COPY",BODY,{"derivedFrom":makeQuery(id+"F3.opExtrude","SWEPT_BODY",BODY,{"disambiguationData":[OSD([sQuery(id+"F1.wireOp",EDGE,"E9.0.1.0")])]}),"instanceName":"24"});
            var Q86;
            Q86=makeQuery(id+"F65.opPattern","COPY",BODY,{"derivedFrom":makeQuery(id+"F3.opExtrude","SWEPT_BODY",BODY,{"disambiguationData":[OSD([sQuery(id+"F1.wireOp",EDGE,"E8")])]}),"instanceName":"43"});
            var Q87;
            Q87=makeQuery(id+"F64.opPattern","COPY",BODY,{"derivedFrom":makeQuery(id+"F3.opExtrude","SWEPT_BODY",BODY,{"disambiguationData":[OSD([sQuery(id+"F1.wireOp",EDGE,"E9.0.1.0")])]}),"instanceName":"16"});
            var Q88;
            Q88=makeQuery(id+"F64.opPattern","COPY",BODY,{"derivedFrom":makeQuery(id+"F3.opExtrude","SWEPT_BODY",BODY,{"disambiguationData":[OSD([sQuery(id+"F1.wireOp",EDGE,"E9.0.2.0")])]}),"instanceName":"16"});
            var Q89;
            Q89=makeQuery(id+"F65.opPattern","COPY",BODY,{"derivedFrom":makeQuery(id+"F3.opExtrude","SWEPT_BODY",BODY,{"disambiguationData":[OSD([sQuery(id+"F1.wireOp",EDGE,"E8")])]}),"instanceName":"44"});
            var Q90;
            Q90=makeQuery(id+"F64.opPattern","COPY",BODY,{"derivedFrom":makeQuery(id+"F3.opExtrude","SWEPT_BODY",BODY,{"disambiguationData":[OSD([sQuery(id+"F1.wireOp",EDGE,"E9.0.2.0")])]}),"instanceName":"23"});
            var Q91;
            Q91=makeQuery(id+"F63.opPattern","COPY",BODY,{"derivedFrom":makeQuery(id+"F3.opExtrude","SWEPT_BODY",BODY,{"disambiguationData":[OSD([sQuery(id+"F1.wireOp",EDGE,"E9.0.3.0")])]}),"instanceName":"22"});
            var Q92;
            Q92=makeQuery(id+"F64.opPattern","COPY",BODY,{"derivedFrom":makeQuery(id+"F3.opExtrude","SWEPT_BODY",BODY,{"disambiguationData":[OSD([sQuery(id+"F1.wireOp",EDGE,"E9.0.1.0")])]}),"instanceName":"36"});
            var Q93;
            Q93=makeQuery(id+"F64.opPattern","COPY",BODY,{"derivedFrom":makeQuery(id+"F3.opExtrude","SWEPT_BODY",BODY,{"disambiguationData":[OSD([sQuery(id+"F1.wireOp",EDGE,"E9.0.1.0")])]}),"instanceName":"48"});
            var Q94;
            Q94=makeQuery(id+"F64.opPattern","COPY",BODY,{"derivedFrom":makeQuery(id+"F3.opExtrude","SWEPT_BODY",BODY,{"disambiguationData":[OSD([sQuery(id+"F1.wireOp",EDGE,"E9.0.1.0")])]}),"instanceName":"23"});
            var Q95;
            Q95=makeQuery(id+"F64.opPattern","COPY",BODY,{"derivedFrom":makeQuery(id+"F3.opExtrude","SWEPT_BODY",BODY,{"disambiguationData":[OSD([sQuery(id+"F1.wireOp",EDGE,"E9.0.2.0")])]}),"instanceName":"48"});
            var Q96;
            Q96=makeQuery(id+"F65.opPattern","COPY",BODY,{"derivedFrom":makeQuery(id+"F3.opExtrude","SWEPT_BODY",BODY,{"disambiguationData":[OSD([sQuery(id+"F1.wireOp",EDGE,"E8")])]}),"instanceName":"45"});
            var Q97;
            Q97=makeQuery(id+"F65.opPattern","COPY",BODY,{"derivedFrom":makeQuery(id+"F3.opExtrude","SWEPT_BODY",BODY,{"disambiguationData":[OSD([sQuery(id+"F1.wireOp",EDGE,"E8")])]}),"instanceName":"46"});
            var Q98;
            Q98=makeQuery(id+"F65.opPattern","COPY",BODY,{"derivedFrom":makeQuery(id+"F3.opExtrude","SWEPT_BODY",BODY,{"disambiguationData":[OSD([sQuery(id+"F1.wireOp",EDGE,"E8")])]}),"instanceName":"47"});
            var Q99;
            Q99=makeQuery(id+"F65.opPattern","COPY",BODY,{"derivedFrom":makeQuery(id+"F3.opExtrude","SWEPT_BODY",BODY,{"disambiguationData":[OSD([sQuery(id+"F1.wireOp",EDGE,"E8")])]}),"instanceName":"7"});
            var Q100;
            Q100=makeQuery(id+"F64.opPattern","COPY",BODY,{"derivedFrom":makeQuery(id+"F3.opExtrude","SWEPT_BODY",BODY,{"disambiguationData":[OSD([sQuery(id+"F1.wireOp",EDGE,"E9.0.2.0")])]}),"instanceName":"22"});
            var Q101;
            Q101=makeQuery(id+"F64.opPattern","COPY",BODY,{"derivedFrom":makeQuery(id+"F3.opExtrude","SWEPT_BODY",BODY,{"disambiguationData":[OSD([sQuery(id+"F1.wireOp",EDGE,"E9.0.1.0")])]}),"instanceName":"17"});
            var Q102;
            Q102=makeQuery(id+"F63.opPattern","COPY",BODY,{"derivedFrom":makeQuery(id+"F3.opExtrude","SWEPT_BODY",BODY,{"disambiguationData":[OSD([sQuery(id+"F1.wireOp",EDGE,"E9.0.3.0")])]}),"instanceName":"15"});
            var Q103;
            Q103=makeQuery(id+"F63.opPattern","COPY",BODY,{"derivedFrom":makeQuery(id+"F3.opExtrude","SWEPT_BODY",BODY,{"disambiguationData":[OSD([sQuery(id+"F1.wireOp",EDGE,"E9.0.3.0")])]}),"instanceName":"20"});
            var Q104;
            Q104=makeQuery(id+"F65.opPattern","COPY",BODY,{"derivedFrom":makeQuery(id+"F3.opExtrude","SWEPT_BODY",BODY,{"disambiguationData":[OSD([sQuery(id+"F1.wireOp",EDGE,"E8")])]}),"instanceName":"48"});
            var Q105;
            Q105=makeQuery(id+"F64.opPattern","COPY",BODY,{"derivedFrom":makeQuery(id+"F3.opExtrude","SWEPT_BODY",BODY,{"disambiguationData":[OSD([sQuery(id+"F1.wireOp",EDGE,"E9.0.2.0")])]}),"instanceName":"17"});
            var Q106;
            Q106=makeQuery(id+"F63.opPattern","COPY",BODY,{"derivedFrom":makeQuery(id+"F3.opExtrude","SWEPT_BODY",BODY,{"disambiguationData":[OSD([sQuery(id+"F1.wireOp",EDGE,"E9.0.3.0")])]}),"instanceName":"35"});
            var Q107;
            Q107=makeQuery(id+"F63.opPattern","COPY",BODY,{"derivedFrom":makeQuery(id+"F3.opExtrude","SWEPT_BODY",BODY,{"disambiguationData":[OSD([sQuery(id+"F1.wireOp",EDGE,"E9.0.3.0")])]}),"instanceName":"37"});
            var Q108;
            Q108=makeQuery(id+"F63.opPattern","COPY",BODY,{"derivedFrom":makeQuery(id+"F3.opExtrude","SWEPT_BODY",BODY,{"disambiguationData":[OSD([sQuery(id+"F1.wireOp",EDGE,"E9.0.3.0")])]}),"instanceName":"36"});
            var Q109;
            Q109=makeQuery(id+"F63.opPattern","COPY",BODY,{"derivedFrom":makeQuery(id+"F3.opExtrude","SWEPT_BODY",BODY,{"disambiguationData":[OSD([sQuery(id+"F1.wireOp",EDGE,"E9.0.3.0")])]}),"instanceName":"18"});
            var Q110;
            Q110=makeQuery(id+"F63.opPattern","COPY",BODY,{"derivedFrom":makeQuery(id+"F3.opExtrude","SWEPT_BODY",BODY,{"disambiguationData":[OSD([sQuery(id+"F1.wireOp",EDGE,"E9.0.3.0")])]}),"instanceName":"16"});
            var Q111;
            Q111=makeQuery(id+"F63.opPattern","COPY",BODY,{"derivedFrom":makeQuery(id+"F3.opExtrude","SWEPT_BODY",BODY,{"disambiguationData":[OSD([sQuery(id+"F1.wireOp",EDGE,"E9.0.3.0")])]}),"instanceName":"14"});
            var Q112;
            Q112=makeQuery(id+"F63.opPattern","COPY",BODY,{"derivedFrom":makeQuery(id+"F3.opExtrude","SWEPT_BODY",BODY,{"disambiguationData":[OSD([sQuery(id+"F1.wireOp",EDGE,"E9.0.3.0")])]}),"instanceName":"13"});
            var Q113;
            Q113=makeQuery(id+"F63.opPattern","COPY",BODY,{"derivedFrom":makeQuery(id+"F3.opExtrude","SWEPT_BODY",BODY,{"disambiguationData":[OSD([sQuery(id+"F1.wireOp",EDGE,"E9.0.3.0")])]}),"instanceName":"38"});
            var Q114;
            Q114=makeQuery(id+"F65.opPattern","COPY",BODY,{"derivedFrom":makeQuery(id+"F3.opExtrude","SWEPT_BODY",BODY,{"disambiguationData":[OSD([sQuery(id+"F1.wireOp",EDGE,"E8")])]}),"instanceName":"5"});
            var Q115;
            Q115=makeQuery(id+"F63.opPattern","COPY",BODY,{"derivedFrom":makeQuery(id+"F3.opExtrude","SWEPT_BODY",BODY,{"disambiguationData":[OSD([sQuery(id+"F1.wireOp",EDGE,"E9.0.3.0")])]}),"instanceName":"39"});
            var Q116;
            Q116=makeQuery(id+"F63.opPattern","COPY",BODY,{"derivedFrom":makeQuery(id+"F3.opExtrude","SWEPT_BODY",BODY,{"disambiguationData":[OSD([sQuery(id+"F1.wireOp",EDGE,"E9.0.3.0")])]}),"instanceName":"12"});
            var Q117;
            Q117=makeQuery(id+"F63.opPattern","COPY",BODY,{"derivedFrom":makeQuery(id+"F3.opExtrude","SWEPT_BODY",BODY,{"disambiguationData":[OSD([sQuery(id+"F1.wireOp",EDGE,"E9.0.3.0")])]}),"instanceName":"11"});
            var Q118;
            Q118=makeQuery(id+"F63.opPattern","COPY",BODY,{"derivedFrom":makeQuery(id+"F3.opExtrude","SWEPT_BODY",BODY,{"disambiguationData":[OSD([sQuery(id+"F1.wireOp",EDGE,"E9.0.3.0")])]}),"instanceName":"10"});
            var Q119;
            Q119=makeQuery(id+"F65.opPattern","COPY",BODY,{"derivedFrom":makeQuery(id+"F3.opExtrude","SWEPT_BODY",BODY,{"disambiguationData":[OSD([sQuery(id+"F1.wireOp",EDGE,"E8")])]}),"instanceName":"4"});
            var Q120;
            Q120=makeQuery(id+"F63.opPattern","COPY",BODY,{"derivedFrom":makeQuery(id+"F3.opExtrude","SWEPT_BODY",BODY,{"disambiguationData":[OSD([sQuery(id+"F1.wireOp",EDGE,"E9.0.3.0")])]}),"instanceName":"40"});
            var Q121;
            Q121=makeQuery(id+"F63.opPattern","COPY",BODY,{"derivedFrom":makeQuery(id+"F3.opExtrude","SWEPT_BODY",BODY,{"disambiguationData":[OSD([sQuery(id+"F1.wireOp",EDGE,"E9.0.3.0")])]}),"instanceName":"41"});
            var Q122;
            Q122=makeQuery(id+"F63.opPattern","COPY",BODY,{"derivedFrom":makeQuery(id+"F3.opExtrude","SWEPT_BODY",BODY,{"disambiguationData":[OSD([sQuery(id+"F1.wireOp",EDGE,"E9.0.3.0")])]}),"instanceName":"9"});
            var Q123;
            Q123=makeQuery(id+"F63.opPattern","COPY",BODY,{"derivedFrom":makeQuery(id+"F3.opExtrude","SWEPT_BODY",BODY,{"disambiguationData":[OSD([sQuery(id+"F1.wireOp",EDGE,"E9.0.3.0")])]}),"instanceName":"8"});
            var Q124;
            Q124=makeQuery(id+"F65.opPattern","COPY",BODY,{"derivedFrom":makeQuery(id+"F3.opExtrude","SWEPT_BODY",BODY,{"disambiguationData":[OSD([sQuery(id+"F1.wireOp",EDGE,"E8")])]}),"instanceName":"3"});
            var Q125;
            Q125=makeQuery(id+"F65.opPattern","COPY",BODY,{"derivedFrom":makeQuery(id+"F3.opExtrude","SWEPT_BODY",BODY,{"disambiguationData":[OSD([sQuery(id+"F1.wireOp",EDGE,"E8")])]}),"instanceName":"8"});
            var Q126;
            Q126=makeQuery(id+"F64.opPattern","COPY",BODY,{"derivedFrom":makeQuery(id+"F3.opExtrude","SWEPT_BODY",BODY,{"disambiguationData":[OSD([sQuery(id+"F1.wireOp",EDGE,"E9.0.2.0")])]}),"instanceName":"18"});
            var Q127;
            Q127=makeQuery(id+"F64.opPattern","COPY",BODY,{"derivedFrom":makeQuery(id+"F3.opExtrude","SWEPT_BODY",BODY,{"disambiguationData":[OSD([sQuery(id+"F1.wireOp",EDGE,"E9.0.1.0")])]}),"instanceName":"18"});
            var Q128;
            Q128=makeQuery(id+"F3.opExtrude","SWEPT_BODY",BODY,{"disambiguationData":[OSD([sQuery(id+"F1.wireOp",EDGE,"E9.0.2.0")])]});
            var Q129;
            Q129=makeQuery(id+"F63.opPattern","COPY",BODY,{"derivedFrom":makeQuery(id+"F3.opExtrude","SWEPT_BODY",BODY,{"disambiguationData":[OSD([sQuery(id+"F1.wireOp",EDGE,"E9.0.3.0")])]}),"instanceName":"42"});
            var Q130;
            Q130=makeQuery(id+"F63.opPattern","COPY",BODY,{"derivedFrom":makeQuery(id+"F3.opExtrude","SWEPT_BODY",BODY,{"disambiguationData":[OSD([sQuery(id+"F1.wireOp",EDGE,"E9.0.3.0")])]}),"instanceName":"7"});
            var Q131;
            Q131=makeQuery(id+"F64.opPattern","COPY",BODY,{"derivedFrom":makeQuery(id+"F3.opExtrude","SWEPT_BODY",BODY,{"disambiguationData":[OSD([sQuery(id+"F1.wireOp",EDGE,"E9.0.1.0")])]}),"instanceName":"38"});
            var Q132;
            Q132=makeQuery(id+"F64.opPattern","COPY",BODY,{"derivedFrom":makeQuery(id+"F3.opExtrude","SWEPT_BODY",BODY,{"disambiguationData":[OSD([sQuery(id+"F1.wireOp",EDGE,"E9.0.1.0")])]}),"instanceName":"21"});
            var Q133;
            Q133=makeQuery(id+"F63.opPattern","COPY",BODY,{"derivedFrom":makeQuery(id+"F3.opExtrude","SWEPT_BODY",BODY,{"disambiguationData":[OSD([sQuery(id+"F1.wireOp",EDGE,"E9.0.3.0")])]}),"instanceName":"43"});
            var Q134;
            Q134=makeQuery(id+"F63.opPattern","COPY",BODY,{"derivedFrom":makeQuery(id+"F3.opExtrude","SWEPT_BODY",BODY,{"disambiguationData":[OSD([sQuery(id+"F1.wireOp",EDGE,"E9.0.3.0")])]}),"instanceName":"44"});
            var Q135;
            Q135=makeQuery(id+"F63.opPattern","COPY",BODY,{"derivedFrom":makeQuery(id+"F3.opExtrude","SWEPT_BODY",BODY,{"disambiguationData":[OSD([sQuery(id+"F1.wireOp",EDGE,"E9.0.3.0")])]}),"instanceName":"6"});
            var Q136;
            Q136=makeQuery(id+"F63.opPattern","COPY",BODY,{"derivedFrom":makeQuery(id+"F3.opExtrude","SWEPT_BODY",BODY,{"disambiguationData":[OSD([sQuery(id+"F1.wireOp",EDGE,"E9.0.3.0")])]}),"instanceName":"45"});
            var Q137;
            Q137=makeQuery(id+"F65.opPattern","COPY",BODY,{"derivedFrom":makeQuery(id+"F3.opExtrude","SWEPT_BODY",BODY,{"disambiguationData":[OSD([sQuery(id+"F1.wireOp",EDGE,"E8")])]}),"instanceName":"2"});
            var Q138;
            Q138=makeQuery(id+"F63.opPattern","COPY",BODY,{"derivedFrom":makeQuery(id+"F3.opExtrude","SWEPT_BODY",BODY,{"disambiguationData":[OSD([sQuery(id+"F1.wireOp",EDGE,"E9.0.3.0")])]}),"instanceName":"5"});
            var Q139;
            Q139=makeQuery(id+"F64.opPattern","COPY",BODY,{"derivedFrom":makeQuery(id+"F3.opExtrude","SWEPT_BODY",BODY,{"disambiguationData":[OSD([sQuery(id+"F1.wireOp",EDGE,"E9.0.2.0")])]}),"instanceName":"20"});
            var Q140;
            Q140=makeQuery(id+"F65.opPattern","COPY",BODY,{"derivedFrom":makeQuery(id+"F3.opExtrude","SWEPT_BODY",BODY,{"disambiguationData":[OSD([sQuery(id+"F1.wireOp",EDGE,"E8")])]}),"instanceName":"49"});
            var Q141;
            Q141=makeQuery(id+"F64.opPattern","COPY",BODY,{"derivedFrom":makeQuery(id+"F3.opExtrude","SWEPT_BODY",BODY,{"disambiguationData":[OSD([sQuery(id+"F1.wireOp",EDGE,"E9.0.2.0")])]}),"instanceName":"27"});
            var Q142;
            Q142=makeQuery(id+"F63.opPattern","COPY",BODY,{"derivedFrom":makeQuery(id+"F3.opExtrude","SWEPT_BODY",BODY,{"disambiguationData":[OSD([sQuery(id+"F1.wireOp",EDGE,"E9.0.3.0")])]}),"instanceName":"4"});
            var Q143;
            Q143=makeQuery(id+"F63.opPattern","COPY",BODY,{"derivedFrom":makeQuery(id+"F3.opExtrude","SWEPT_BODY",BODY,{"disambiguationData":[OSD([sQuery(id+"F1.wireOp",EDGE,"E9.0.3.0")])]}),"instanceName":"52"});
            var Q144;
            Q144=makeQuery(id+"F64.opPattern","COPY",BODY,{"derivedFrom":makeQuery(id+"F3.opExtrude","SWEPT_BODY",BODY,{"disambiguationData":[OSD([sQuery(id+"F1.wireOp",EDGE,"E9.0.1.0")])]}),"instanceName":"22"});
            var Q145;
            Q145=makeQuery(id+"F63.opPattern","COPY",BODY,{"derivedFrom":makeQuery(id+"F3.opExtrude","SWEPT_BODY",BODY,{"disambiguationData":[OSD([sQuery(id+"F1.wireOp",EDGE,"E9.0.3.0")])]}),"instanceName":"46"});
            var Q146;
            Q146=makeQuery(id+"F64.opPattern","COPY",BODY,{"derivedFrom":makeQuery(id+"F3.opExtrude","SWEPT_BODY",BODY,{"disambiguationData":[OSD([sQuery(id+"F1.wireOp",EDGE,"E9.0.1.0")])]}),"instanceName":"28"});
            var Q147;
            Q147=makeQuery(id+"F63.opPattern","COPY",BODY,{"derivedFrom":makeQuery(id+"F3.opExtrude","SWEPT_BODY",BODY,{"disambiguationData":[OSD([sQuery(id+"F1.wireOp",EDGE,"E9.0.3.0")])]}),"instanceName":"47"});
            var Q148;
            Q148=makeQuery(id+"F65.opPattern","COPY",BODY,{"derivedFrom":makeQuery(id+"F3.opExtrude","SWEPT_BODY",BODY,{"disambiguationData":[OSD([sQuery(id+"F1.wireOp",EDGE,"E8")])]}),"instanceName":"9"});
            var Q149;
            Q149=makeQuery(id+"F64.opPattern","COPY",BODY,{"derivedFrom":makeQuery(id+"F3.opExtrude","SWEPT_BODY",BODY,{"disambiguationData":[OSD([sQuery(id+"F1.wireOp",EDGE,"E9.0.2.0")])]}),"instanceName":"37"});
            var Q150;
            Q150=makeQuery(id+"F64.opPattern","COPY",BODY,{"derivedFrom":makeQuery(id+"F3.opExtrude","SWEPT_BODY",BODY,{"disambiguationData":[OSD([sQuery(id+"F1.wireOp",EDGE,"E9.0.2.0")])]}),"instanceName":"30"});
            var Q151;
            Q151=makeQuery(id+"F63.opPattern","COPY",BODY,{"derivedFrom":makeQuery(id+"F3.opExtrude","SWEPT_BODY",BODY,{"disambiguationData":[OSD([sQuery(id+"F1.wireOp",EDGE,"E9.0.3.0")])]}),"instanceName":"48"});
            var Q152;
            Q152=makeQuery(id+"F64.opPattern","COPY",BODY,{"derivedFrom":makeQuery(id+"F3.opExtrude","SWEPT_BODY",BODY,{"disambiguationData":[OSD([sQuery(id+"F1.wireOp",EDGE,"E9.0.2.0")])]}),"instanceName":"21"});
            var Q153;
            Q153=makeQuery(id+"F65.opPattern","COPY",BODY,{"derivedFrom":makeQuery(id+"F3.opExtrude","SWEPT_BODY",BODY,{"disambiguationData":[OSD([sQuery(id+"F1.wireOp",EDGE,"E8")])]}),"instanceName":"17"});
            var Q154;
            Q154=makeQuery(id+"F65.opPattern","COPY",BODY,{"derivedFrom":makeQuery(id+"F3.opExtrude","SWEPT_BODY",BODY,{"disambiguationData":[OSD([sQuery(id+"F1.wireOp",EDGE,"E8")])]}),"instanceName":"16"});
            var Q155;
            Q155=makeQuery(id+"F64.opPattern","COPY",BODY,{"derivedFrom":makeQuery(id+"F3.opExtrude","SWEPT_BODY",BODY,{"disambiguationData":[OSD([sQuery(id+"F1.wireOp",EDGE,"E9.0.2.0")])]}),"instanceName":"35"});
            var Q156;
            Q156=makeQuery(id+"F64.opPattern","COPY",BODY,{"derivedFrom":makeQuery(id+"F3.opExtrude","SWEPT_BODY",BODY,{"disambiguationData":[OSD([sQuery(id+"F1.wireOp",EDGE,"E9.0.1.0")])]}),"instanceName":"2"});
            var Q157;
            Q157=makeQuery(id+"F64.opPattern","COPY",BODY,{"derivedFrom":makeQuery(id+"F3.opExtrude","SWEPT_BODY",BODY,{"disambiguationData":[OSD([sQuery(id+"F1.wireOp",EDGE,"E9.0.1.0")])]}),"instanceName":"35"});
            var Q158;
            Q158=makeQuery(id+"F64.opPattern","COPY",BODY,{"derivedFrom":makeQuery(id+"F3.opExtrude","SWEPT_BODY",BODY,{"disambiguationData":[OSD([sQuery(id+"F1.wireOp",EDGE,"E9.0.2.0")])]}),"instanceName":"34"});
            var Q159;
            Q159=makeQuery(id+"F63.opPattern","COPY",BODY,{"derivedFrom":makeQuery(id+"F3.opExtrude","SWEPT_BODY",BODY,{"disambiguationData":[OSD([sQuery(id+"F1.wireOp",EDGE,"E9.0.3.0")])]}),"instanceName":"26"});
            var Q160;
            Q160=makeQuery(id+"F64.opPattern","COPY",BODY,{"derivedFrom":makeQuery(id+"F3.opExtrude","SWEPT_BODY",BODY,{"disambiguationData":[OSD([sQuery(id+"F1.wireOp",EDGE,"E9.0.1.0")])]}),"instanceName":"34"});
            var Q161;
            Q161=makeQuery(id+"F63.opPattern","COPY",BODY,{"derivedFrom":makeQuery(id+"F3.opExtrude","SWEPT_BODY",BODY,{"disambiguationData":[OSD([sQuery(id+"F1.wireOp",EDGE,"E9.0.3.0")])]}),"instanceName":"27"});
            var Q162;
            Q162=makeQuery(id+"F63.opPattern","COPY",BODY,{"derivedFrom":makeQuery(id+"F3.opExtrude","SWEPT_BODY",BODY,{"disambiguationData":[OSD([sQuery(id+"F1.wireOp",EDGE,"E9.0.3.0")])]}),"instanceName":"28"});
            var Q163;
            Q163=makeQuery(id+"F63.opPattern","COPY",BODY,{"derivedFrom":makeQuery(id+"F3.opExtrude","SWEPT_BODY",BODY,{"disambiguationData":[OSD([sQuery(id+"F1.wireOp",EDGE,"E9.0.3.0")])]}),"instanceName":"23"});
            var Q164;
            Q164=makeQuery(id+"F64.opPattern","COPY",BODY,{"derivedFrom":makeQuery(id+"F3.opExtrude","SWEPT_BODY",BODY,{"disambiguationData":[OSD([sQuery(id+"F1.wireOp",EDGE,"E9.0.2.0")])]}),"instanceName":"2"});
            var Q165;
            Q165=makeQuery(id+"F63.opPattern","COPY",BODY,{"derivedFrom":makeQuery(id+"F3.opExtrude","SWEPT_BODY",BODY,{"disambiguationData":[OSD([sQuery(id+"F1.wireOp",EDGE,"E9.0.3.0")])]}),"instanceName":"24"});
            var Q166;
            Q166=makeQuery(id+"F64.opPattern","COPY",BODY,{"derivedFrom":makeQuery(id+"F3.opExtrude","SWEPT_BODY",BODY,{"disambiguationData":[OSD([sQuery(id+"F1.wireOp",EDGE,"E9.0.1.0")])]}),"instanceName":"3"});
            var Q167;
            Q167=makeQuery(id+"F64.opPattern","COPY",BODY,{"derivedFrom":makeQuery(id+"F3.opExtrude","SWEPT_BODY",BODY,{"disambiguationData":[OSD([sQuery(id+"F1.wireOp",EDGE,"E9.0.2.0")])]}),"instanceName":"33"});
            var Q168;
            Q168=makeQuery(id+"F63.opPattern","COPY",BODY,{"derivedFrom":makeQuery(id+"F3.opExtrude","SWEPT_BODY",BODY,{"disambiguationData":[OSD([sQuery(id+"F1.wireOp",EDGE,"E9.0.3.0")])]}),"instanceName":"29"});
            var Q169;
            Q169=makeQuery(id+"F64.opPattern","COPY",BODY,{"derivedFrom":makeQuery(id+"F3.opExtrude","SWEPT_BODY",BODY,{"disambiguationData":[OSD([sQuery(id+"F1.wireOp",EDGE,"E9.0.2.0")])]}),"instanceName":"3"});
            var Q170;
            Q170=makeQuery(id+"F64.opPattern","COPY",BODY,{"derivedFrom":makeQuery(id+"F3.opExtrude","SWEPT_BODY",BODY,{"disambiguationData":[OSD([sQuery(id+"F1.wireOp",EDGE,"E9.0.1.0")])]}),"instanceName":"33"});
            var Q171;
            Q171=makeQuery(id+"F63.opPattern","COPY",BODY,{"derivedFrom":makeQuery(id+"F3.opExtrude","SWEPT_BODY",BODY,{"disambiguationData":[OSD([sQuery(id+"F1.wireOp",EDGE,"E9.0.3.0")])]}),"instanceName":"30"});
            var Q172;
            Q172=makeQuery(id+"F63.opPattern","COPY",BODY,{"derivedFrom":makeQuery(id+"F3.opExtrude","SWEPT_BODY",BODY,{"disambiguationData":[OSD([sQuery(id+"F1.wireOp",EDGE,"E9.0.3.0")])]}),"instanceName":"31"});
            var Q173;
            Q173=makeQuery(id+"F64.opPattern","COPY",BODY,{"derivedFrom":makeQuery(id+"F3.opExtrude","SWEPT_BODY",BODY,{"disambiguationData":[OSD([sQuery(id+"F1.wireOp",EDGE,"E9.0.1.0")])]}),"instanceName":"4"});
            var Q174;
            Q174=makeQuery(id+"F64.opPattern","COPY",BODY,{"derivedFrom":makeQuery(id+"F3.opExtrude","SWEPT_BODY",BODY,{"disambiguationData":[OSD([sQuery(id+"F1.wireOp",EDGE,"E9.0.2.0")])]}),"instanceName":"29"});
            var Q175;
            Q175=makeQuery(id+"F64.opPattern","COPY",BODY,{"derivedFrom":makeQuery(id+"F3.opExtrude","SWEPT_BODY",BODY,{"disambiguationData":[OSD([sQuery(id+"F1.wireOp",EDGE,"E9.0.2.0")])]}),"instanceName":"4"});
            var Q176;
            Q176=makeQuery(id+"F64.opPattern","COPY",BODY,{"derivedFrom":makeQuery(id+"F3.opExtrude","SWEPT_BODY",BODY,{"disambiguationData":[OSD([sQuery(id+"F1.wireOp",EDGE,"E9.0.1.0")])]}),"instanceName":"27"});
            var Q177;
            Q177=makeQuery(id+"F64.opPattern","COPY",BODY,{"derivedFrom":makeQuery(id+"F3.opExtrude","SWEPT_BODY",BODY,{"disambiguationData":[OSD([sQuery(id+"F1.wireOp",EDGE,"E9.0.1.0")])]}),"instanceName":"19"});
            var Q178;
            Q178=makeQuery(id+"F64.opPattern","COPY",BODY,{"derivedFrom":makeQuery(id+"F3.opExtrude","SWEPT_BODY",BODY,{"disambiguationData":[OSD([sQuery(id+"F1.wireOp",EDGE,"E9.0.2.0")])]}),"instanceName":"19"});
            var Q179;
            Q179=makeQuery(id+"F65.opPattern","COPY",BODY,{"derivedFrom":makeQuery(id+"F3.opExtrude","SWEPT_BODY",BODY,{"disambiguationData":[OSD([sQuery(id+"F1.wireOp",EDGE,"E8")])]}),"instanceName":"54"});
            var Q180;
            Q180=makeQuery(id+"F3.opExtrude","SWEPT_BODY",BODY,{"disambiguationData":[OSD([sQuery(id+"F1.wireOp",EDGE,"E9.0.1.0")])]});
            var Q181;
            Q181=makeQuery(id+"F64.opPattern","COPY",BODY,{"derivedFrom":makeQuery(id+"F3.opExtrude","SWEPT_BODY",BODY,{"disambiguationData":[OSD([sQuery(id+"F1.wireOp",EDGE,"E9.0.1.0")])]}),"instanceName":"20"});
            var Q182;
            Q182=makeQuery(id+"F64.opPattern","COPY",BODY,{"derivedFrom":makeQuery(id+"F3.opExtrude","SWEPT_BODY",BODY,{"disambiguationData":[OSD([sQuery(id+"F1.wireOp",EDGE,"E9.0.2.0")])]}),"instanceName":"38"});
            var Q183;
            Q183=makeQuery(id+"F65.opPattern","COPY",BODY,{"derivedFrom":makeQuery(id+"F3.opExtrude","SWEPT_BODY",BODY,{"disambiguationData":[OSD([sQuery(id+"F1.wireOp",EDGE,"E8")])]}),"instanceName":"53"});
            var Q184;
            Q184=makeQuery(id+"F64.opPattern","COPY",BODY,{"derivedFrom":makeQuery(id+"F3.opExtrude","SWEPT_BODY",BODY,{"disambiguationData":[OSD([sQuery(id+"F1.wireOp",EDGE,"E9.0.1.0")])]}),"instanceName":"5"});
            var Q185;
            Q185=makeQuery(id+"F64.opPattern","COPY",BODY,{"derivedFrom":makeQuery(id+"F3.opExtrude","SWEPT_BODY",BODY,{"disambiguationData":[OSD([sQuery(id+"F1.wireOp",EDGE,"E9.0.2.0")])]}),"instanceName":"5"});
            var Q186;
            Q186=makeQuery(id+"F65.opPattern","COPY",BODY,{"derivedFrom":makeQuery(id+"F3.opExtrude","SWEPT_BODY",BODY,{"disambiguationData":[OSD([sQuery(id+"F1.wireOp",EDGE,"E8")])]}),"instanceName":"52"});
            var Q187;
            Q187=makeQuery(id+"F63.opPattern","COPY",BODY,{"derivedFrom":makeQuery(id+"F3.opExtrude","SWEPT_BODY",BODY,{"disambiguationData":[OSD([sQuery(id+"F1.wireOp",EDGE,"E9.0.3.0")])]}),"instanceName":"17"});
            var Q188;
            Q188=makeQuery(id+"F65.opPattern","COPY",BODY,{"derivedFrom":makeQuery(id+"F3.opExtrude","SWEPT_BODY",BODY,{"disambiguationData":[OSD([sQuery(id+"F1.wireOp",EDGE,"E8")])]}),"instanceName":"12"});
            var Q189;
            Q189=makeQuery(id+"F65.opPattern","COPY",BODY,{"derivedFrom":makeQuery(id+"F3.opExtrude","SWEPT_BODY",BODY,{"disambiguationData":[OSD([sQuery(id+"F1.wireOp",EDGE,"E8")])]}),"instanceName":"51"});
            var Q190;
            Q190=makeQuery(id+"F65.opPattern","COPY",BODY,{"derivedFrom":makeQuery(id+"F3.opExtrude","SWEPT_BODY",BODY,{"disambiguationData":[OSD([sQuery(id+"F1.wireOp",EDGE,"E8")])]}),"instanceName":"50"});
            var Q191;
            Q191=makeQuery(id+"F65.opPattern","COPY",BODY,{"derivedFrom":makeQuery(id+"F3.opExtrude","SWEPT_BODY",BODY,{"disambiguationData":[OSD([sQuery(id+"F1.wireOp",EDGE,"E8")])]}),"instanceName":"13"});
            var Q192;
            Q192=makeQuery(id+"F64.opPattern","COPY",BODY,{"derivedFrom":makeQuery(id+"F3.opExtrude","SWEPT_BODY",BODY,{"disambiguationData":[OSD([sQuery(id+"F1.wireOp",EDGE,"E9.0.1.0")])]}),"instanceName":"6"});
            var Q193;
            Q193=makeQuery(id+"F63.opPattern","COPY",BODY,{"derivedFrom":makeQuery(id+"F3.opExtrude","SWEPT_BODY",BODY,{"disambiguationData":[OSD([sQuery(id+"F1.wireOp",EDGE,"E9.0.3.0")])]}),"instanceName":"32"});
            var Q194;
            Q194=makeQuery(id+"F63.opPattern","COPY",BODY,{"derivedFrom":makeQuery(id+"F3.opExtrude","SWEPT_BODY",BODY,{"disambiguationData":[OSD([sQuery(id+"F1.wireOp",EDGE,"E9.0.3.0")])]}),"instanceName":"33"});
            var Q195;
            Q195=makeQuery(id+"F65.opPattern","COPY",BODY,{"derivedFrom":makeQuery(id+"F3.opExtrude","SWEPT_BODY",BODY,{"disambiguationData":[OSD([sQuery(id+"F1.wireOp",EDGE,"E8")])]}),"instanceName":"14"});
            var Q196;
            Q196=makeQuery(id+"F65.opPattern","COPY",BODY,{"derivedFrom":makeQuery(id+"F3.opExtrude","SWEPT_BODY",BODY,{"disambiguationData":[OSD([sQuery(id+"F1.wireOp",EDGE,"E8")])]}),"instanceName":"6"});
            var Q197;
            Q197=makeQuery(id+"F64.opPattern","COPY",BODY,{"derivedFrom":makeQuery(id+"F3.opExtrude","SWEPT_BODY",BODY,{"disambiguationData":[OSD([sQuery(id+"F1.wireOp",EDGE,"E9.0.2.0")])]}),"instanceName":"32"});
            var Q198;
            Q198=makeQuery(id+"F64.opPattern","COPY",BODY,{"derivedFrom":makeQuery(id+"F3.opExtrude","SWEPT_BODY",BODY,{"disambiguationData":[OSD([sQuery(id+"F1.wireOp",EDGE,"E9.0.1.0")])]}),"instanceName":"32"});
            var Q199;
            Q199=makeQuery(id+"F64.opPattern","COPY",BODY,{"derivedFrom":makeQuery(id+"F3.opExtrude","SWEPT_BODY",BODY,{"disambiguationData":[OSD([sQuery(id+"F1.wireOp",EDGE,"E9.0.2.0")])]}),"instanceName":"31"});
            var Q200;
            Q200=makeQuery(id+"F65.opPattern","COPY",BODY,{"derivedFrom":makeQuery(id+"F3.opExtrude","SWEPT_BODY",BODY,{"disambiguationData":[OSD([sQuery(id+"F1.wireOp",EDGE,"E8")])]}),"instanceName":"11"});
            var Q201;
            Q201=makeQuery(id+"F63.opPattern","COPY",BODY,{"derivedFrom":makeQuery(id+"F3.opExtrude","SWEPT_BODY",BODY,{"disambiguationData":[OSD([sQuery(id+"F1.wireOp",EDGE,"E9.0.3.0")])]}),"instanceName":"2"});
            var Q202;
            Q202=makeQuery(id+"F63.opPattern","COPY",BODY,{"derivedFrom":makeQuery(id+"F3.opExtrude","SWEPT_BODY",BODY,{"disambiguationData":[OSD([sQuery(id+"F1.wireOp",EDGE,"E9.0.3.0")])]}),"instanceName":"19"});
            var Q203;
            Q203=makeQuery(id+"F64.opPattern","COPY",BODY,{"derivedFrom":makeQuery(id+"F3.opExtrude","SWEPT_BODY",BODY,{"disambiguationData":[OSD([sQuery(id+"F1.wireOp",EDGE,"E9.0.1.0")])]}),"instanceName":"30"});
            var Q204;
            Q204=makeQuery(id+"F63.opPattern","COPY",BODY,{"derivedFrom":makeQuery(id+"F3.opExtrude","SWEPT_BODY",BODY,{"disambiguationData":[OSD([sQuery(id+"F1.wireOp",EDGE,"E9.0.3.0")])]}),"instanceName":"49"});
            var Q205;
            Q205=makeQuery(id+"F65.opPattern","COPY",BODY,{"derivedFrom":makeQuery(id+"F3.opExtrude","SWEPT_BODY",BODY,{"disambiguationData":[OSD([sQuery(id+"F1.wireOp",EDGE,"E8")])]}),"instanceName":"10"});
            var Q206;
            Q206=makeQuery(id+"F63.opPattern","COPY",BODY,{"derivedFrom":makeQuery(id+"F3.opExtrude","SWEPT_BODY",BODY,{"disambiguationData":[OSD([sQuery(id+"F1.wireOp",EDGE,"E9.0.3.0")])]}),"instanceName":"50"});
            var Q207;
            Q207=makeQuery(id+"F64.opPattern","COPY",BODY,{"derivedFrom":makeQuery(id+"F3.opExtrude","SWEPT_BODY",BODY,{"disambiguationData":[OSD([sQuery(id+"F1.wireOp",EDGE,"E9.0.2.0")])]}),"instanceName":"52"});
            var Q208;
            Q208=makeQuery(id+"F64.opPattern","COPY",BODY,{"derivedFrom":makeQuery(id+"F3.opExtrude","SWEPT_BODY",BODY,{"disambiguationData":[OSD([sQuery(id+"F1.wireOp",EDGE,"E9.0.1.0")])]}),"instanceName":"52"});
            var Q209;
            Q209=makeQuery(id+"F65.opPattern","COPY",BODY,{"derivedFrom":makeQuery(id+"F3.opExtrude","SWEPT_BODY",BODY,{"disambiguationData":[OSD([sQuery(id+"F1.wireOp",EDGE,"E8")])]}),"instanceName":"27"});
            var Q210;
            Q210=makeQuery(id+"F65.opPattern","COPY",BODY,{"derivedFrom":makeQuery(id+"F3.opExtrude","SWEPT_BODY",BODY,{"disambiguationData":[OSD([sQuery(id+"F1.wireOp",EDGE,"E8")])]}),"instanceName":"28"});
            var Q211;
            Q211=makeQuery(id+"F63.opPattern","COPY",BODY,{"derivedFrom":makeQuery(id+"F3.opExtrude","SWEPT_BODY",BODY,{"disambiguationData":[OSD([sQuery(id+"F1.wireOp",EDGE,"E9.0.3.0")])]}),"instanceName":"53"});
            var Q212;
            Q212=makeQuery(id+"F64.opPattern","COPY",BODY,{"derivedFrom":makeQuery(id+"F3.opExtrude","SWEPT_BODY",BODY,{"disambiguationData":[OSD([sQuery(id+"F1.wireOp",EDGE,"E9.0.1.0")])]}),"instanceName":"54"});
            var Q213;
            Q213=makeQuery(id+"F64.opPattern","COPY",BODY,{"derivedFrom":makeQuery(id+"F3.opExtrude","SWEPT_BODY",BODY,{"disambiguationData":[OSD([sQuery(id+"F1.wireOp",EDGE,"E9.0.2.0")])]}),"instanceName":"1"});
            var Q214;
            Q214=makeQuery(id+"F64.opPattern","COPY",BODY,{"derivedFrom":makeQuery(id+"F3.opExtrude","SWEPT_BODY",BODY,{"disambiguationData":[OSD([sQuery(id+"F1.wireOp",EDGE,"E9.0.1.0")])]}),"instanceName":"1"});
            var Q215;
            Q215=makeQuery(id+"F64.opPattern","COPY",BODY,{"derivedFrom":makeQuery(id+"F3.opExtrude","SWEPT_BODY",BODY,{"disambiguationData":[OSD([sQuery(id+"F1.wireOp",EDGE,"E9.0.2.0")])]}),"instanceName":"54"});
            var Q216;
            Q216=makeQuery(id+"F63.opPattern","COPY",BODY,{"derivedFrom":makeQuery(id+"F3.opExtrude","SWEPT_BODY",BODY,{"disambiguationData":[OSD([sQuery(id+"F1.wireOp",EDGE,"E9.0.3.0")])]}),"instanceName":"1"});
            var Q217;
            Q217=makeQuery(id+"F65.opPattern","COPY",BODY,{"derivedFrom":makeQuery(id+"F3.opExtrude","SWEPT_BODY",BODY,{"disambiguationData":[OSD([sQuery(id+"F1.wireOp",EDGE,"E8")])]}),"instanceName":"55"});
            var Q218;
            Q218=makeQuery(id+"F65.opPattern","COPY",BODY,{"derivedFrom":makeQuery(id+"F3.opExtrude","SWEPT_BODY",BODY,{"disambiguationData":[OSD([sQuery(id+"F1.wireOp",EDGE,"E8")])]}),"instanceName":"1"});
            var Q219;
            Q219=makeQuery(id+"F63.opPattern","COPY",BODY,{"derivedFrom":makeQuery(id+"F3.opExtrude","SWEPT_BODY",BODY,{"disambiguationData":[OSD([sQuery(id+"F1.wireOp",EDGE,"E9.0.3.0")])]}),"instanceName":"51"});
            var Q220;
            Q220=makeQuery(id+"F2.opRevolve","SWEPT_BODY",BODY,{"disambiguationData":[OSD([sQuery(id+"F0.wireOp",EDGE,"E0"),sQuery(id+"F0.wireOp",EDGE,"E1"),sQuery(id+"F0.wireOp",EDGE,"E2"),sQuery(id+"F0.wireOp",EDGE,"E3"),sQuery(id+"F0.wireOp",EDGE,"E6")])]});
            booleanBodies(context, id + "F66", {"operationType" : BooleanOperationType.SUBTRACTION, "tools" : qUnion([Q0, Q1, Q2, Q3, Q4, Q5, Q6, Q7, Q8, Q9, Q10, Q11, Q12, Q13, Q14, Q15, Q16, Q17, Q18, Q19, Q20, Q21, Q22, Q23, Q24, Q25, Q26, Q27, Q28, Q29, Q30, Q31, Q32, Q33, Q34, Q35, Q36, Q37, Q38, Q39, Q40, Q41, Q42, Q43, Q44, Q45, Q46, Q47, Q48, Q49, Q50, Q51, Q52, Q53, Q54, Q55, Q56, Q57, Q58, Q59, Q60, Q61, Q62, Q63, Q64, Q65, Q66, Q67, Q68, Q69, Q70, Q71, Q72, Q73, Q74, Q75, Q76, Q77, Q78, Q79, Q80, Q81, Q82, Q83, Q84, Q85, Q86, Q87, Q88, Q89, Q90, Q91, Q92, Q93, Q94, Q95, Q96, Q97, Q98, Q99, Q100, Q101, Q102, Q103, Q104, Q105, Q106, Q107, Q108, Q109, Q110, Q111, Q112, Q113, Q114, Q115, Q116, Q117, Q118, Q119, Q120, Q121, Q122, Q123, Q124, Q125, Q126, Q127, Q128, Q129, Q130, Q131, Q132, Q133, Q134, Q135, Q136, Q137, Q138, Q139, Q140, Q141, Q142, Q143, Q144, Q145, Q146, Q147, Q148, Q149, Q150, Q151, Q152, Q153, Q154, Q155, Q156, Q157, Q158, Q159, Q160, Q161, Q162, Q163, Q164, Q165, Q166, Q167, Q168, Q169, Q170, Q171, Q172, Q173, Q174, Q175, Q176, Q177, Q178, Q179, Q180, Q181, Q182, Q183, Q184, Q185, Q186, Q187, Q188, Q189, Q190, Q191, Q192, Q193, Q194, Q195, Q196, Q197, Q198, Q199, Q200, Q201, Q202, Q203, Q204, Q205, Q206, Q207, Q208, Q209, Q210, Q211, Q212, Q213, Q214, Q215, Q216, Q217, Q218, Q219]), "targets" : qUnion([Q220])});
        }
    });
